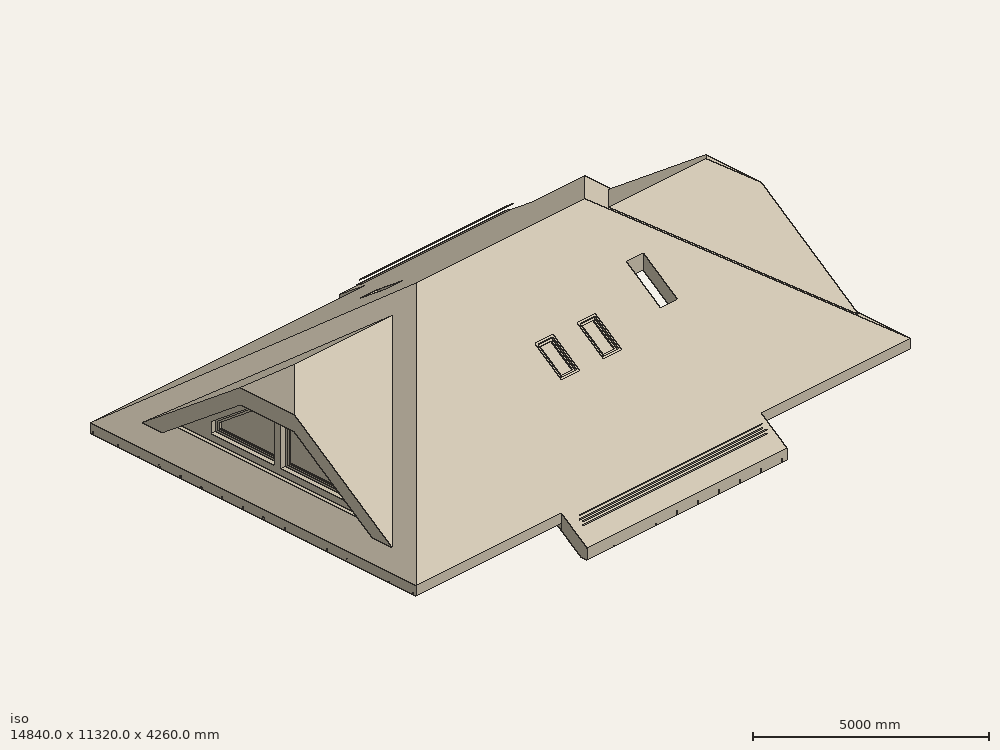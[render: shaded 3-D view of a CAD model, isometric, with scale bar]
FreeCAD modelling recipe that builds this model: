
FCSTD DOCUMENT  (FreeCAD 0.19R)
Label: 2bedr_dev_071121_BIM_mod
License: All rights reserved
LicenseURL: http://en.wikipedia.org/wiki/All_rights_reserved
objects: Part::Part2DObjectPython×578, Part::FeaturePython×547, App::FeaturePython×94, App::DocumentObjectGroupPython×73, App::GeometryPython×66, Sketcher::SketchObject×58, Part::MultiCommon×47, Part::Box×37, Part::Extrusion×36, Part::Cut×35, TechDraw::DrawViewAnnotation×28, Part::MultiFuse×25, App::MaterialObjectPython×20, TechDraw::DrawLeaderLine×17, Part::Feature×16, App::DocumentObjectGroup×12, TechDraw::DrawSVGTemplate×6, TechDraw::DrawPage×6, Part::Cylinder×5, Part::Mirroring×5, +8 more types
note: 1456 computed .brp shape members not serialized (recipe doc carries the construction recipe); baked Part::Feature solids carry a one-line shape summary decoded from their .brp

FEATURE [Part::Part2DObjectPython] Rectangle2169  label="Д-105-254-001"  # Draft 2D object (typed FeaturePython)
  ChamferSize = 0
  Columns = 1
  FilletRadius = 0
  Height = 410
  Length = 1050
  MakeFace = true
  Placement = pos=(5670,-435,0) rot=(0,0,1;0rad)
  Rows = 1
FEATURE [Part::Part2DObjectPython] Rectangle2231  label="ОК-66-001"  # Draft 2D object (typed FeaturePython)
  ChamferSize = 0
  Columns = 1
  FilletRadius = 0
  Height = 410
  Length = 660
  MakeFace = true
  Placement = pos=(7555,-435,0) rot=(0,0,1;0rad)
  Rows = 1
FEATURE [Part::Part2DObjectPython] Rectangle2230  label="ОК-66-002"  # Draft 2D object (typed FeaturePython)
  ChamferSize = 0
  Columns = 1
  FilletRadius = 0
  Height = 410
  Length = 660
  MakeFace = true
  Placement = pos=(4175,-435,0) rot=(0,0,1;0rad)
  Rows = 1
FEATURE [App::FeaturePython] Dimension001  # Draft dimension (typed FeaturePython)
  Diameter = false
  Dimline = (13900,-300,0)
  Direction = (0,0,0)
  Distance = 7510
  End = (12550,7485,0)
  Normal = (0,0,1)
  Start = (12550,-25,0)
FEATURE [App::FeaturePython] Dimension  # Draft dimension (typed FeaturePython)
  Diameter = false
  Dimline = (13600,-1100,0)
  Direction = (0,0,0)
  Distance = 12580
  End = (12550,-10,0)
  Normal = (0,0,1)
  Start = (-30,-10,0)
FEATURE [Part::Part2DObjectPython] Rectangle2234  # Draft 2D object (typed FeaturePython)
  ChamferSize = 0
  Columns = 1
  FilletRadius = 0
  Height = 1500
  Length = 3000
  MakeFace = false
  Placement = pos=(5125,-1770,0) rot=(0,0,1;0rad)
  Rows = 1
FEATURE [Part::FeaturePython] Structure016  label="Проём-ОК-66-002"  # Arch/BIM 52 (typed FeaturePython)
  Base = -> Rectangle2230
  FaceMaker = 0
  Height = 1386
  HorizontalArea = 270600
  IfcData = complex_attributes={"OwnerHistory": {}, "IsNestedBy": {}, "IsDecomposedBy": {}, "IsDefinedBy": {}, "ObjectPlacement": {}, "Representation":... (+4 chars omitted)
  IfcType = 52
  Length = 0
  MoveBase = false
  MoveWithHost = false
  Nodes = (2) [(4618,-185,0),(4618,-185,1386)]
  NodesOffset = 0
  Normal = (0,0,0)
  PerimeterLength = 2140
  Placement = pos=(0,0,955) rot=(0,0,1;0rad)
  VerticalArea = 2966040
  Width = 100
FEATURE [Part::FeaturePython] Structure017  label="Проём-ОК-66-001"  # Arch/BIM 52 (typed FeaturePython)
  Base = -> Rectangle2231
  FaceMaker = 0
  Height = 1386
  HorizontalArea = 270600
  IfcData = complex_attributes={"OwnerHistory": {}, "IsNestedBy": {}, "IsDecomposedBy": {}, "IsDefinedBy": {}, "ObjectPlacement": {}, "Representation":... (+4 chars omitted)
  IfcType = 52
  Length = 0
  MoveBase = false
  MoveWithHost = false
  Nodes = (2) [(7885,-230,0),(7885,-230,1386)]
  NodesOffset = 0
  Normal = (0,0,0)
  PerimeterLength = 2140
  Placement = pos=(0,0,955) rot=(0,0,1;0rad)
  VerticalArea = 2966040
  Width = 100
FEATURE [Part::FeaturePython] Structure019  label="Проём-Д-105-254-001"  # Arch/BIM 52 (typed FeaturePython)
  Base = -> Rectangle2169
  FaceMaker = 0
  Height = 2541
  HorizontalArea = 430500
  IfcData = complex_attributes={"OwnerHistory": {}, "IsNestedBy": {}, "IsDecomposedBy": {}, "IsDefinedBy": {}, "ObjectPlacement": {}, "Representation":... (+4 chars omitted)
  IfcType = 52
  Length = 0
  MoveBase = false
  MoveWithHost = false
  Nodes = (2) [(6195,-230,0),(6195,-230,2541)]
  NodesOffset = 0
  Normal = (0,0,0)
  PerimeterLength = 2920
  Placement = pos=(0,0,-200) rot=(0,0,1;0rad)
  VerticalArea = 7419720
  Width = 100
FEATURE [Part::Part2DObjectPython] Line1049  # Draft 2D object (typed FeaturePython)
  ChamferSize = 0
  Closed = true
  End = (-50,3680,0)
  FilletRadius = 0
  Length = 12620
  MakeFace = false
  Placement = pos=(4290,10400,0) rot=(0,0,1;1.5708rad)
  Points = (2) [(-6720,-8280,0),(-6720,4340,0)]
  Start = (12570,3680,0)
  Subdivisions = 0
FEATURE [Part::Part2DObjectPython] Line1054  # Draft 2D object (typed FeaturePython)
  ChamferSize = 0
  Closed = true
  End = (4870,7505,0)
  FilletRadius = 0
  Length = 3700
  MakeFace = false
  Placement = pos=(9650,5690,0) rot=(0,0,1;0rad)
  Points = (2) [(-4780,-1885,0),(-4780,1815,0)]
  Start = (4870,3805,0)
  Subdivisions = 0
FEATURE [Sketcher::SketchObject] Sketch231  label="Профиль ПНО 120-8"
  FullyConstrained = false
  Placement = pos=(0,0,0) rot=(1,0,0;1.5708rad)
  sketch-geometry (19):
    g0: LineSegment StartX=0 StartY=0 StartZ=0 EndX=1190 EndY=0 EndZ=0
    g1: LineSegment StartX=1190 StartY=0 StartZ=0 EndX=1190 EndY=160 EndZ=0
    g2: LineSegment StartX=1190 StartY=160 StartZ=0 EndX=0 EndY=160 EndZ=0
    g3: LineSegment StartX=0 StartY=160 StartZ=0 EndX=0 EndY=0 EndZ=0
    g4: Circle CenterX=100 CenterY=80 CenterZ=0 NormalX=0 NormalY=0 NormalZ=1 AngleXU=0 Radius=50
    g5: Circle CenterX=240 CenterY=80 CenterZ=0 NormalX=0 NormalY=0 NormalZ=1 AngleXU=0 Radius=50
    g6: LineSegment StartX=100 StartY=80 StartZ=0 EndX=240 EndY=80 EndZ=0
    g7: Circle CenterX=380 CenterY=80 CenterZ=0 NormalX=0 NormalY=0 NormalZ=1 AngleXU=0 Radius=50
    g8: LineSegment StartX=240 StartY=80 StartZ=0 EndX=380 EndY=80 EndZ=0
    g9: Circle CenterX=520 CenterY=80 CenterZ=0 NormalX=0 NormalY=0 NormalZ=1 AngleXU=0 Radius=50
    g10: LineSegment StartX=380 StartY=80 StartZ=0 EndX=520 EndY=80 EndZ=0
    g11: Circle CenterX=660 CenterY=80 CenterZ=0 NormalX=0 NormalY=0 NormalZ=1 AngleXU=0 Radius=50
    g12: LineSegment StartX=520 StartY=80 StartZ=0 EndX=660 EndY=80 EndZ=0
    g13: Circle CenterX=800 CenterY=80 CenterZ=0 NormalX=0 NormalY=0 NormalZ=1 AngleXU=0 Radius=50
    g14: LineSegment StartX=660 StartY=80 StartZ=0 EndX=800 EndY=80 EndZ=0
    g15: Circle CenterX=940 CenterY=80 CenterZ=0 NormalX=0 NormalY=0 NormalZ=1 AngleXU=0 Radius=50
    g16: LineSegment StartX=800 StartY=80 StartZ=0 EndX=940 EndY=80 EndZ=0
    g17: Circle CenterX=1080 CenterY=80 CenterZ=0 NormalX=0 NormalY=0 NormalZ=1 AngleXU=0 Radius=50
    g18: LineSegment StartX=940 StartY=80 StartZ=0 EndX=1080 EndY=80 EndZ=0
  constraints (49):
    c: Coincident(g0,g1)
    c: Coincident(g1,g2)
    c: Coincident(g2,g3)
    c: Coincident(g3,g0)
    c: Horizontal(g0)
    c: Horizontal(g2)
    c: Vertical(g1)
    c: Vertical(g3)
    c: Coincident(g0,g-1)
    c: DistanceY(g3,g3) = 160
    c: DistanceX(g2,g2) = 1190
    c: Diameter(g4) = 100
    c: DistanceY(g4,g2) = 80
    c: Diameter(g5) = 100
    c: Coincident(g4,g6)
    c: Coincident(g5,g6)
    c: Distance(g6) = 140
    c: Angle(g6) = 0
    c: Diameter(g7) = 100
    c: Coincident(g5,g8)
    c: Coincident(g7,g8)
    c: Equal(g6,g8)
    c: Parallel(g8,g6)
    c: Diameter(g9) = 100
    c: Coincident(g7,g10)
    c: Coincident(g9,g10)
    c: Equal(g6,g10)
    c: Parallel(g10,g6)
    c: Diameter(g11) = 100
    c: Coincident(g9,g12)
    c: Coincident(g11,g12)
    c: Equal(g6,g12)
    c: Parallel(g12,g6)
    c: Diameter(g13) = 100
    c: Coincident(g11,g14)
    c: Coincident(g13,g14)
    c: Equal(g6,g14)
    c: Parallel(g14,g6)
    c: Diameter(g15) = 100
    c: Coincident(g13,g16)
    c: Coincident(g15,g16)
    c: Equal(g6,g16)
    c: Parallel(g16,g6)
    c: Diameter(g17) = 100
    c: Coincident(g15,g18)
    c: Coincident(g17,g18)
    c: Equal(g6,g18)
    c: Parallel(g18,g6)
    c: DistanceX(g2,g4) = 100
FEATURE [Part::Part2DObjectPython] Line1074  label="ось фундамента внутр.стены"  # Draft 2D object (typed FeaturePython)
  ChamferSize = 0
  Closed = true
  End = (3855,9350,0)
  FilletRadius = 0
  Length = 5200
  MakeFace = false
  Placement = pos=(2155,2900,0) rot=(0,0,1;1.5708rad)
  Points = (2) [(1250,-1700,0),(6450,-1700,0)]
  Start = (3855,4150,0)
  Subdivisions = 0
FEATURE [Part::FeaturePython] Wall037  label="фундамент внутр.стена01"  # Arch/BIM 166 (typed FeaturePython)
  Align = 2
  Area = 2.6e+06
  Base = -> Line1074
  BlockHeight = 0
  BlockLength = 0
  CountBroken = 0
  CountEntire = 0
  Face = 0
  Height = 500
  HorizontalArea = 1.3e+06
  IfcType = 166
  Joint = 0
  Length = 5200
  MakeBlocks = false
  MoveBase = false
  MoveWithHost = false
  Normal = (0,0,-1)
  OffsetFirst = 0
  OffsetSecond = 0
  PerimeterLength = 10900
  Placement = pos=(0,0,-180) rot=(0,0,1;0rad)
  PredefinedType = 0
  VerticalArea = 5.45e+06
  Width = 250
FEATURE [Part::FeaturePython] Wall046  label="утепл фунд. внешней.стены 002"  # Arch/BIM 166 (typed FeaturePython)
  Align = 1
  Area = 28488000
  BlockHeight = 600
  BlockLength = 600
  CountBroken = 1
  CountEntire = 0
  Face = 0
  Height = 600
  HorizontalArea = 3798400
  IfcType = 166
  Joint = 1
  Length = 47480
  MakeBlocks = true
  MoveBase = false
  MoveWithHost = false
  Normal = (0,0,-1)
  OffsetFirst = 0
  OffsetSecond = 0
  PerimeterLength = 95120
  Placement = pos=(0,0,-380) rot=(0,0,1;0rad)
  PredefinedType = 0
  VerticalArea = 57072000
  Width = 80
FEATURE [Part::FeaturePython] Wall047  label="утепл отмостки 001"  # Arch/BIM 166 (typed FeaturePython)
  Align = 1
  Area = 2374000
  BlockHeight = 600
  BlockLength = 1200
  CountBroken = 1
  CountEntire = 0
  Face = 0
  Height = 50
  HorizontalArea = 28488000
  IfcType = 166
  Joint = 1
  Length = 47480
  MakeBlocks = true
  MoveBase = false
  MoveWithHost = false
  Normal = (0,0,-1)
  Offset = 80
  OffsetFirst = 0
  OffsetSecond = 0
  PerimeterLength = 96160
  Placement = pos=(0,0,-930) rot=(0,0,1;0rad)
  PredefinedType = 0
  VerticalArea = 4808000
  Width = 600
FEATURE [Part::Part2DObjectPython] Circle071  # Draft 2D object (typed FeaturePython)
  FirstAngle = 0
  LastAngle = 0
  MakeFace = false
  Placement = pos=(8500,900,0) rot=(0,0,1;0rad)
  Radius = 580
FEATURE [Part::Part2DObjectPython] Circle072  # Draft 2D object (typed FeaturePython)
  FirstAngle = 0
  LastAngle = 0
  MakeFace = false
  Placement = pos=(8500,900,0) rot=(0,0,1;0rad)
  Radius = 500
FEATURE [Part::Part2DObjectPython] Circle073  label="люк_контур 001"  # Draft 2D object (typed FeaturePython)
  FirstAngle = 0
  LastAngle = 0
  MakeFace = false
  Placement = pos=(8500,1000,0) rot=(0,0,1;0rad)
  Radius = 350
FEATURE [Part::FeaturePython] Structure041  label="кольцо с днищем ДК-10.9 внутр."  # Arch/BIM 52 (typed FeaturePython)
  Base = -> Circle072
  FaceMaker = 0
  Height = 800
  HorizontalArea = 785398
  IfcData = complex_attributes={"OwnerHistory": {}, "IsNestedBy": {}, "IsDecomposedBy": {}, "IsDefinedBy": {}, "ObjectPlacement": {}, "Representation":... (+4 chars omitted)
  IfcType = 52
  Length = 0
  MoveBase = false
  MoveWithHost = false
  Nodes = (2) [(8500,900,0),(8500,900,-800)]
  NodesOffset = 0
  Normal = (0,0,-1)
  PerimeterLength = 3141.59
  Placement = pos=(0,0,-300) rot=(0,0,1;0rad)
  VerticalArea = 2.51327e+06
  Width = 100
FEATURE [Part::FeaturePython] Structure040  label="кольцо с днищем ДК-10.9 габарит"  # Arch/BIM 52 (typed FeaturePython)
  Base = -> Circle071
  FaceMaker = 0
  Height = 900
  HorizontalArea = 1.05683e+06
  IfcData = complex_attributes={"OwnerHistory": {}, "IsNestedBy": {}, "IsDecomposedBy": {}, "IsDefinedBy": {}, "ObjectPlacement": {}, "Representation":... (+4 chars omitted)
  IfcType = 52
  Length = 0
  MoveBase = false
  MoveWithHost = false
  Nodes = (2) [(8500,900,0),(8500,900,-900)]
  NodesOffset = 0
  Normal = (0,0,-1)
  PerimeterLength = 3644.25
  Placement = pos=(0,0,-300) rot=(0,0,1;0rad)
  Subtractions = -> [Structure041]
  VerticalArea = 5.7931e+06
  Width = 100
FEATURE [Part::FeaturePython] Structure044  label="люк контур Д700"  # Arch/BIM 52 (typed FeaturePython)
  Base = -> Circle073
  FaceMaker = 0
  Height = 300
  HorizontalArea = 384845
  IfcData = complex_attributes={"OwnerHistory": {}, "IsNestedBy": {}, "IsDecomposedBy": {}, "IsDefinedBy": {}, "ObjectPlacement": {}, "Representation":... (+4 chars omitted)
  IfcType = 52
  Length = 0
  MoveBase = false
  MoveWithHost = false
  Nodes = (2) [(8500,1000,0),(8500,1000,-300)]
  NodesOffset = 0
  Normal = (0,0,-1)
  PerimeterLength = 2199.11
  VerticalArea = 659734
  Width = 100
FEATURE [Part::FeaturePython] Structure043  label="крышка ПП10"  # Arch/BIM 52 (typed FeaturePython)
  Base = -> Circle071
  FaceMaker = 0
  Height = 100
  HorizontalArea = 671987
  IfcData = complex_attributes={"OwnerHistory": {}, "IsNestedBy": {}, "IsDecomposedBy": {}, "IsDefinedBy": {}, "ObjectPlacement": {}, "Representation":... (+4 chars omitted)
  IfcType = 52
  Length = 0
  MoveBase = false
  MoveWithHost = false
  Nodes = (2) [(8500,900,0),(8500,900,-100)]
  NodesOffset = 0
  Normal = (0,0,-1)
  PerimeterLength = 3644.25
  Placement = pos=(0,0,-200) rot=(0,0,1;0rad)
  Subtractions = -> [Structure044]
  VerticalArea = 584336
  Width = 100
FEATURE [App::GeometryPython] BuildingPart015  label="Колодец d1000 (ввод воды и канализации)"  # Arch/BIM 52 (typed FeaturePython)
  Area = 0
  Group = -> [Structure040,Structure043]
  Height = 0
  HeightPropagate = true
  IfcData = complex_attributes={"OwnerHistory": {}, "IsNestedBy": {}, "IsDecomposedBy": {}, "IsDefinedBy": {}, "ObjectPlacement": {}, "Representation":... (+4 chars omitted)
  IfcType = 52
  LevelOffset = 0
FEATURE [Part::Part2DObjectPython] Line1077  # Draft 2D object (typed FeaturePython)
  ChamferSize = 0
  Closed = true
  End = (-50,-45,0)
  FilletRadius = 0
  Length = 12620
  MakeFace = false
  Placement = pos=(12060,265,0) rot=(0,0,1;0rad)
  Points = (2) [(510,-310,0),(-12110,-310,0)]
  Start = (12570,-45,0)
  Subdivisions = 0
FEATURE [Part::Part2DObjectPython] Rectangle2286  # Draft 2D object (typed FeaturePython)
  ChamferSize = 0
  Columns = 1
  FilletRadius = 0
  Height = 5190
  Length = 9350
  MakeFace = false
  Placement = pos=(1950,2210,0) rot=(0,0,1;0rad)
  Rows = 1
FEATURE [Part::FeaturePython] Structure049  label="вычитаемый объём 002"  # Arch/BIM 52 (typed FeaturePython)
  FaceMaker = 0
  Height = 4000
  HorizontalArea = 3.20922e+07
  IfcData = complex_attributes={"OwnerHistory": {}, "IsNestedBy": {}, "IsDecomposedBy": {}, "IsDefinedBy": {}, "ObjectPlacement": {}, "Representation":... (+4 chars omitted)
  IfcType = 52
  Length = 0
  MoveBase = false
  MoveWithHost = false
  Nodes = (2) [(506.667,3830,0),(506.667,3830,4000)]
  NodesOffset = 0
  Normal = (0,0,1)
  PerimeterLength = 27353
  Placement = pos=(0,0,3160) rot=(0,0,1;0rad)
  VerticalArea = 1.09412e+08
  Width = 100
FEATURE [Part::FeaturePython] Structure050  label="вычитаемый объём 004"  # Arch/BIM 52 (typed FeaturePython)
  FaceMaker = 0
  Height = 4000
  HorizontalArea = 5.56586e+07
  IfcData = complex_attributes={"OwnerHistory": {}, "IsNestedBy": {}, "IsDecomposedBy": {}, "IsDefinedBy": {}, "ObjectPlacement": {}, "Representation":... (+4 chars omitted)
  IfcType = 52
  Length = 0
  MoveBase = false
  MoveWithHost = false
  Nodes = (2) [(6040,886.738,0),(6040,886.738,4000)]
  NodesOffset = 0
  Normal = (0,0,1)
  PerimeterLength = 35673
  Placement = pos=(0,0,3160) rot=(0,0,1;0rad)
  VerticalArea = 1.42692e+08
  Width = 100
FEATURE [Part::FeaturePython] Structure051  label="вычитаемый объём 003"  # Arch/BIM 52 (typed FeaturePython)
  FaceMaker = 0
  Height = 4000
  HorizontalArea = 32092225
  IfcData = complex_attributes={"OwnerHistory": {}, "IsNestedBy": {}, "IsDecomposedBy": {}, "IsDefinedBy": {}, "ObjectPlacement": {}, "Representation":... (+4 chars omitted)
  IfcType = 52
  Length = 0
  MoveBase = false
  MoveWithHost = false
  Nodes = (2) [(12481.7,4805,0),(12481.7,4805,4000)]
  NodesOffset = 0
  Normal = (0,0,1)
  PerimeterLength = 27353
  Placement = pos=(0,0,3160) rot=(0,0,1;0rad)
  VerticalArea = 1.09412e+08
  Width = 100
FEATURE [App::FeaturePython] Dimension003  # Draft dimension (typed FeaturePython)
  Diameter = false
  Dimline = (14100,-1000,0)
  Direction = (0,0,0)
  Distance = 8570
  End = (13080,8015,0)
  Normal = (0,0,1)
  Start = (13080,-555,0)
FEATURE [Sketcher::SketchObject] Sketch248
  FullyConstrained = true
  Placement = pos=(3860,3535,0) rot=(1,0,0;1.5708rad)
  sketch-geometry (8):
    g0: LineSegment StartX=0 StartY=0 StartZ=0 EndX=900 EndY=0 EndZ=0
    g1: LineSegment StartX=900 StartY=0 StartZ=0 EndX=900 EndY=2150 EndZ=0
    g2: LineSegment StartX=900 StartY=2150 StartZ=0 EndX=0 EndY=2150 EndZ=0
    g3: LineSegment StartX=0 StartY=2150 StartZ=0 EndX=0 EndY=0 EndZ=0
    g4: LineSegment StartX=50 StartY=0 StartZ=0 EndX=850 EndY=0 EndZ=0
    g5: LineSegment StartX=850 StartY=0 StartZ=0 EndX=850 EndY=2100 EndZ=0
    g6: LineSegment StartX=850 StartY=2100 StartZ=0 EndX=50 EndY=2100 EndZ=0
    g7: LineSegment StartX=50 StartY=2100 StartZ=0 EndX=50 EndY=0 EndZ=0
  constraints (23):
    c: Coincident(g0,g1)
    c: Coincident(g1,g2)
    c: Coincident(g2,g3)
    c: Coincident(g3,g0)
    c: Horizontal(g0)
    c: Horizontal(g2)
    c: Vertical(g1)
    c: Vertical(g3)
    c: Coincident(g4,g5)
    c: Coincident(g5,g6)
    c: Coincident(g6,g7)
    c: Coincident(g7,g4)
    c: Horizontal(g4)
    c: Horizontal(g6)
    c: Vertical(g5)
    c: Vertical(g7)
    c: DistanceY(g1) = 2150  'Height'
    c: DistanceX(g0) = 900  'Width'
    c: DistanceY(g6,g2) = 50  'Frame1'
    c: DistanceX(g2,g6) = 50  'Frame2'
    c: DistanceX(g4,g0) = 50  'Frame3'
    c: DistanceY(g0,g4) = 0
    c: Coincident(g0,g-1)
FEATURE [Sketcher::SketchObject] Sketch249  label="Профиль ПНО 100-6"
  FullyConstrained = false
  Placement = pos=(0,0,0) rot=(1,0,0;1.5708rad)
  sketch-geometry (15):
    g0: LineSegment StartX=0 StartY=0 StartZ=0 EndX=990 EndY=0 EndZ=0
    g1: LineSegment StartX=990 StartY=0 StartZ=0 EndX=990 EndY=160 EndZ=0
    g2: LineSegment StartX=990 StartY=160 StartZ=0 EndX=0 EndY=160 EndZ=0
    g3: LineSegment StartX=0 StartY=160 StartZ=0 EndX=0 EndY=0 EndZ=0
    g4: Circle CenterX=145 CenterY=80 CenterZ=0 NormalX=0 NormalY=0 NormalZ=1 AngleXU=0 Radius=50
    g5: Circle CenterX=285 CenterY=80 CenterZ=0 NormalX=0 NormalY=0 NormalZ=1 AngleXU=0 Radius=50
    g6: LineSegment StartX=145 StartY=80 StartZ=0 EndX=285 EndY=80 EndZ=0
    g7: Circle CenterX=425 CenterY=80 CenterZ=0 NormalX=0 NormalY=0 NormalZ=1 AngleXU=0 Radius=50
    g8: LineSegment StartX=285 StartY=80 StartZ=0 EndX=425 EndY=80 EndZ=0
    g9: Circle CenterX=565 CenterY=80 CenterZ=0 NormalX=0 NormalY=0 NormalZ=1 AngleXU=0 Radius=50
    g10: LineSegment StartX=425 StartY=80 StartZ=0 EndX=565 EndY=80 EndZ=0
    g11: Circle CenterX=705 CenterY=80 CenterZ=0 NormalX=0 NormalY=0 NormalZ=1 AngleXU=0 Radius=50
    g12: LineSegment StartX=565 StartY=80 StartZ=0 EndX=705 EndY=80 EndZ=0
    g13: Circle CenterX=845 CenterY=80 CenterZ=0 NormalX=0 NormalY=0 NormalZ=1 AngleXU=0 Radius=50
    g14: LineSegment StartX=705 StartY=80 StartZ=0 EndX=845 EndY=80 EndZ=0
  constraints (39):
    c: Coincident(g0,g1)
    c: Coincident(g1,g2)
    c: Coincident(g2,g3)
    c: Coincident(g3,g0)
    c: Horizontal(g0)
    c: Horizontal(g2)
    c: Vertical(g1)
    c: Vertical(g3)
    c: Coincident(g0,g-1)
    c: DistanceY(g3,g3) = 160
    c: DistanceX(g2,g2) = 990
    c: Diameter(g4) = 100
    c: DistanceY(g4,g2) = 80
    c: Diameter(g5) = 100
    c: Coincident(g4,g6)
    c: Coincident(g5,g6)
    c: Distance(g6) = 140
    c: Angle(g6) = 0
    c: Diameter(g7) = 100
    c: Coincident(g5,g8)
    c: Coincident(g7,g8)
    c: Equal(g6,g8)
    c: Parallel(g8,g6)
    c: Diameter(g9) = 100
    c: Coincident(g7,g10)
    c: Coincident(g9,g10)
    c: Equal(g6,g10)
    c: Parallel(g10,g6)
    c: Diameter(g11) = 100
    c: Coincident(g9,g12)
    c: Coincident(g11,g12)
    c: Equal(g6,g12)
    c: Parallel(g12,g6)
    c: Diameter(g13) = 100
    c: Coincident(g11,g14)
    c: Coincident(g13,g14)
    c: Equal(g6,g14)
    c: Parallel(g14,g6)
    c: DistanceX(g2,g4) = 145
FEATURE [Part::Part2DObjectPython] Wire460  label="границы участка"  # Draft 2D object (typed FeaturePython)
  ChamferSize = 0
  Closed = true
  End = (26167.8,29983.2,0)
  FilletRadius = 0
  Length = 156987
  MakeFace = false
  Placement = pos=(24404.1,-9481.8,0) rot=(0,0,1;0.025758rad)
  Points = (7) [(0,0,0),(-3118.22,176.296,0),(-9989.98,2199.83,0),(-22349.9,2518.26,0),(-33551.4,825.818,0),(-40981.4,39865.2,0),(2779.54,39406.5,0)]
  Start = (24404.1,-9481.8,0)
  Subdivisions = 0
FEATURE [Part::Part2DObjectPython] Rectangle2365  label="зона парковки-навес"  # Draft 2D object (typed FeaturePython)
  ChamferSize = 0
  Columns = 1
  FilletRadius = 0
  Height = 7000
  Length = 7000
  MakeFace = false
  Placement = pos=(17916.6,-6918.81,0) rot=(0,0,-1;0.068796rad)
  Rows = 1
FEATURE [Part::Part2DObjectPython] Wire463  label="граница по ограждению"  # Draft 2D object (typed FeaturePython)
  ChamferSize = 0
  Closed = true
  End = (5754.6,-6612.02,0)
  FilletRadius = 0
  Length = 153279
  MakeFace = false
  Placement = pos=(24847.4,-8209.78,0) rot=(0,0,1;0rad)
  Points = (6) [(14.0233,-1.17368,0),(2632.1,37116.3,0),(-41128.8,37575,0),(-34003,133.748,0),(-24492.8,1579.34,0),(-19092.8,1597.76,0)]
  Start = (24861.5,-8210.95,0)
  Subdivisions = 0
FEATURE [Part::FeaturePython] Structure133  label="грунт в границах участка"  # Arch/BIM 52 (typed FeaturePython)
  Base = -> Wire460
  FaceMaker = 0
  Height = 1000
  HorizontalArea = 1.47224e+09
  IfcData = complex_attributes={"OwnerHistory": {}, "IsNestedBy": {}, "IsDecomposedBy": {}, "IsDefinedBy": {}, "ObjectPlacement": {}, "Representation":... (+4 chars omitted)
  IfcType = 52
  Length = 0
  MoveBase = false
  MoveWithHost = false
  Nodes = (2) [(5892.5,11504.2,0),(5892.5,11504.2,-1000)]
  NodesOffset = 0
  Normal = (0,0,-1)
  PerimeterLength = 156987
  Placement = pos=(0,0,-320) rot=(0,0,1;0rad)
  VerticalArea = 1.56987e+08
  Width = 100
FEATURE [Part::Part2DObjectPython] Wire464  label="мауэрлат003"  # Draft 2D object (typed FeaturePython)
  ChamferSize = 0
  Closed = true
  End = (14568.5,-7412.72,0)
  FilletRadius = 0
  Length = 30000
  MakeFace = false
  Placement = pos=(20304,-1451.15,0) rot=(0,0,-1;0.229406rad)
  Points = (4) [(3770.46,-7109.62,0),(3770.46,-109.624,0),(-4229.54,-109.624,0),(-4229.54,-7109.62,0)]
  Start = (22359,-9231.91,0)
  Subdivisions = 0
FEATURE [Part::Part2DObjectPython] Rectangle2375  # Draft 2D object (typed FeaturePython)
  ChamferSize = 0
  Columns = 1
  FilletRadius = 0
  Height = 150
  Length = 800
  MakeFace = true
  Placement = pos=(-1461.06,-5083.09,0) rot=(0,0,-1;1.39508rad)
  Rows = 1
FEATURE [Part::Part2DObjectPython] Rectangle2376  # Draft 2D object (typed FeaturePython)
  ChamferSize = 0
  Columns = 1
  FilletRadius = 0
  Height = 150
  Length = 500
  MakeFace = true
  Placement = pos=(-6959.67,-6719.51,0) rot=(0,0,1;1.74651rad)
  Rows = 1
FEATURE [Part::Part2DObjectPython] Rectangle2377  # Draft 2D object (typed FeaturePython)
  ChamferSize = 0
  Columns = 1
  FilletRadius = 0
  Height = 2300
  Length = 6000
  MakeFace = false
  Placement = pos=(-1444.48,-4318.42,0) rot=(0,0,1;3.31731rad)
  Rows = 1
FEATURE [Part::FeaturePython] Roof011  label="Навес над парковкой"  # Arch/BIM 113 (typed FeaturePython)
  Angles = [90,10,90,10]
  Base = -> Wire464
  BorderLength = 0
  Face = 0
  Flip = false
  Heights = [0,617.144,0,617.144]
  HorizontalArea = 5.6e+07
  IdRel = [0,0,0,0]
  IfcType = 113
  MoveBase = false
  MoveWithHost = false
  Overhang = [0,0,0,0]
  PerimeterLength = 30000
  Placement = pos=(0,0,2500) rot=(0,0,1;0rad)
  PredefinedType = 0
  RidgeLength = 0
  Runs = [0,3500,0,3500]
  Thickness = [150,150,150,150]
  VerticalArea = 7.00644e+06
FEATURE [Part::FeaturePython] Structure135  label="Structure134"  # Arch/BIM 52 (typed FeaturePython)
  Base = -> Rectangle2375
  FaceMaker = 0
  Height = 1800
  HorizontalArea = 120000
  IfcData = complex_attributes={"OwnerHistory": {}, "IsNestedBy": {}, "IsDecomposedBy": {}, "IsDefinedBy": {}, "ObjectPlacement": {}, "Representation":... (+4 chars omitted)
  IfcType = 52
  Length = 0
  MoveBase = false
  MoveWithHost = false
  Nodes = (2) [(-35.6948,-25773.1,0),(-35.6948,-25773.1,1800)]
  NodesOffset = 0
  Normal = (0,0,0)
  PerimeterLength = 1900
  VerticalArea = 3.42e+06
  Width = 100
FEATURE [Part::FeaturePython] Structure136  label="Structure135"  # Arch/BIM 52 (typed FeaturePython)
  Base = -> Rectangle2376
  FaceMaker = 0
  Height = 600
  HorizontalArea = 75000
  IfcData = complex_attributes={"OwnerHistory": {}, "IsNestedBy": {}, "IsDecomposedBy": {}, "IsDefinedBy": {}, "ObjectPlacement": {}, "Representation":... (+4 chars omitted)
  IfcType = 52
  Length = 0
  MoveBase = false
  MoveWithHost = false
  Nodes = (2) [(1351.07,-25965.1,0),(1351.07,-25965.1,600)]
  NodesOffset = 0
  Normal = (0,0,0)
  PerimeterLength = 1300
  Placement = pos=(0,-4e-15,1240) rot=(0,0,1;0rad)
  VerticalArea = 780000
  Width = 100
FEATURE [Part::FeaturePython] Wall097  label="Wall007"  # Arch/BIM 166 (typed FeaturePython)
  Align = 1
  Area = 4.067e+07
  Base = -> Rectangle2377
  BlockHeight = 0
  BlockLength = 0
  CountBroken = 0
  CountEntire = 0
  Face = 0
  Height = 2450
  HorizontalArea = 2.595e+06
  IfcType = 166
  Joint = 0
  Length = 16600
  MakeBlocks = false
  MoveBase = false
  MoveWithHost = false
  Normal = (0,0,0)
  OffsetFirst = 0
  OffsetSecond = 0
  PerimeterLength = 12600
  Placement = pos=(0,0,-150) rot=(0,0,1;0rad)
  PredefinedType = 0
  Subtractions = -> [Structure136,Structure135]
  VerticalArea = 7.564e+07
  Width = 150
FEATURE [Sketcher::SketchObject] Sketch250  label="Габарит человека"
  FullyConstrained = false
  Placement = pos=(0,0,0) rot=(1,0,0;1.5708rad)
  sketch-geometry (21):
    g0: LineSegment StartX=-250 StartY=0 StartZ=0 EndX=250 EndY=0 EndZ=0
    g1: LineSegment StartX=250 StartY=0 StartZ=0 EndX=250 EndY=1750 EndZ=0
    g2: LineSegment StartX=250 StartY=1750 StartZ=0 EndX=-250 EndY=1750 EndZ=0
    g3: LineSegment StartX=-250 StartY=1750 StartZ=0 EndX=-250 EndY=0 EndZ=0
    g4: LineSegment StartX=85 StartY=1500 StartZ=0 EndX=85 EndY=1750 EndZ=0
    g5: LineSegment StartX=85 StartY=1750 StartZ=0 EndX=-85 EndY=1750 EndZ=0
    g6: LineSegment StartX=-85 StartY=1750 StartZ=0 EndX=-85 EndY=1500 EndZ=0
    g7: LineSegment StartX=250 StartY=750 StartZ=0 EndX=250 EndY=1500 EndZ=0
    g8: LineSegment StartX=-250 StartY=1500 StartZ=0 EndX=-250 EndY=750 EndZ=0
    g9: LineSegment StartX=-110 StartY=0 StartZ=0 EndX=110 EndY=0 EndZ=0
    g10: LineSegment StartX=110 StartY=0 StartZ=0 EndX=175 EndY=750 EndZ=0
    g11: LineSegment StartX=-175 StartY=750 StartZ=0 EndX=-110 EndY=0 EndZ=0
    g12: GeomPoint X=0 Y=750 Z=0
    g13: GeomPoint X=-110 Y=0 Z=0
    g14: GeomPoint X=110 Y=0 Z=0
    g15: GeomPoint X=175 Y=750 Z=0
    g16: GeomPoint X=-175 Y=750 Z=0
    g17: LineSegment StartX=-250 StartY=1500 StartZ=0 EndX=-85 EndY=1500 EndZ=0
    g18: LineSegment StartX=85 StartY=1500 StartZ=0 EndX=250 EndY=1500 EndZ=0
    g19: LineSegment StartX=-250 StartY=750 StartZ=0 EndX=-175 EndY=750 EndZ=0
    g20: LineSegment StartX=175 StartY=750 StartZ=0 EndX=250 EndY=750 EndZ=0
  constraints (50):
    c: Coincident(g0,g1)
    c: Coincident(g1,g2)
    c: Coincident(g2,g3)
    c: Coincident(g3,g0)
    c: Horizontal(g0)
    c: Horizontal(g2)
    c: Vertical(g1)
    c: Vertical(g3)
    c: Symmetric(g0,g0,g-1)
    c: DistanceX(g2,g2) = 500
    c: DistanceY(g1,g1) = 1750
    c: Coincident(g4,g5)
    c: Coincident(g5,g6)
    c: Horizontal(g5)
    c: Vertical(g4)
    c: Vertical(g6)
    c: Vertical(g7)
    c: Vertical(g8)
    c: Coincident(g9,g10)
    c: DistanceX(g5,g5) = 170
    c: DistanceY(g4,g4) = 250
    c: PointOnObject(g4,g2)
    c: Symmetric(g6,g4,g-2)
    c: PointOnObject(g8,g3)
    c: PointOnObject(g7,g1)
    c: Coincident(g9,g11)
    c: DistanceX(g9,g9) = 220
    c: DistanceY(g0,g7) = 750
    c: PointOnObject(g12,g-2)
    c: Coincident(g13,g9)
    c: Coincident(g14,g9)
    c: Symmetric(g13,g14,g-2)
    c: PointOnObject(g14,g0)
    c: Coincident(g15,g10)
    c: Symmetric(g15,g16,g-2)
    c: DistanceX(g16,g15) = 350
    c: Coincident(g17,g8)
    c: Coincident(g17,g6)
    c: Horizontal(g17)
    c: Coincident(g18,g4)
    c: Coincident(g18,g7)
    c: Horizontal(g18)
    c: Coincident(g19,g8)
    c: Coincident(g19,g11)
    c: Horizontal(g19)
    c: Coincident(g20,g10)
    c: Coincident(g20,g7)
    c: Horizontal(g20)
    c: Equal(g19,g20)
    c: Equal(g11,g10)
FEATURE [Part::Extrusion] Extrude007  label="Габарит человека 001"
  Base = -> Sketch250
  Dir = (0,-1,2e-16)
  DirMode = 2
  FaceMakerClass = Part::FaceMakerBullseye
  LengthFwd = 290
  LengthRev = 0
  Placement = pos=(7375,4690,0) rot=(0,0,1;0rad)
  Solid = true
  Symmetric = false
FEATURE [Part::Extrusion] Extrude008  label="Габарит человека 002"
  Base = -> Sketch250
  Dir = (0,-1,2e-16)
  DirMode = 2
  FaceMakerClass = Part::FaceMakerBullseye
  LengthFwd = 290
  LengthRev = 0
  Placement = pos=(6300,5845,0) rot=(0,0,1;0rad)
  Solid = true
  Symmetric = false
FEATURE [Part::Part2DObjectPython] Rectangle2381  # Draft 2D object (typed FeaturePython)
  ChamferSize = 0
  Columns = 1
  FilletRadius = 0
  Height = 1250
  Length = 2500
  MakeFace = false
  Placement = pos=(5375,-1520,0) rot=(0,0,1;0rad)
  Rows = 1
FEATURE [Part::FeaturePython] Structure140  label="габарит крыльца001"  # Arch/BIM 52 (typed FeaturePython)
  Base = -> Rectangle2381
  FaceMaker = 0
  Height = 180
  HorizontalArea = 3125000
  IfcData = complex_attributes={"OwnerHistory": {}, "IsNestedBy": {}, "IsDecomposedBy": {}, "IsDefinedBy": {}, "ObjectPlacement": {}, "Representation":... (+4 chars omitted)
  IfcType = 52
  Length = 0
  MoveBase = false
  MoveWithHost = false
  Nodes = (2) [(5975,-1250,0),(5975,-1250,-350)]
  NodesOffset = 0
  Normal = (0,0,-1)
  PerimeterLength = 7500
  Placement = pos=(0,0,-40) rot=(0,0,1;0rad)
  VerticalArea = 1350000
  Width = 100
FEATURE [Part::FeaturePython] Structure029  label="габарит крыльца"  # Arch/BIM 52 (typed FeaturePython)
  Additions = -> [Structure140]
  Base = -> Rectangle2234
  FaceMaker = 0
  Height = 180
  HorizontalArea = 4500000
  IfcData = complex_attributes={"OwnerHistory": {}, "IsNestedBy": {}, "IsDecomposedBy": {}, "IsDefinedBy": {}, "ObjectPlacement": {}, "Representation":... (+4 chars omitted)
  IfcType = 52
  Length = 0
  MoveBase = false
  MoveWithHost = false
  Nodes = (2) [(5975,-1250,0),(5975,-1250,-350)]
  NodesOffset = 0
  Normal = (0,0,-1)
  PerimeterLength = 9000
  Placement = pos=(0,0,-220) rot=(0,0,1;0rad)
  VerticalArea = 2970000
  Width = 100
FEATURE [Part::Part2DObjectPython] Rectangle2382  label="террасса"  # Draft 2D object (typed FeaturePython)
  ChamferSize = 0
  Columns = 1
  FilletRadius = 0
  Height = 2400
  Length = 10500
  MakeFace = false
  Placement = pos=(1255,9880,0) rot=(0,0,1;0rad)
  Rows = 1
FEATURE [Part::FeaturePython] Structure028  label="габарит терассы"  # Arch/BIM 52 (typed FeaturePython)
  Base = -> Rectangle2382
  FaceMaker = 0
  Height = 400
  HorizontalArea = 25200000
  IfcData = complex_attributes={"OwnerHistory": {}, "IsNestedBy": {}, "IsDecomposedBy": {}, "IsDefinedBy": {}, "ObjectPlacement": {}, "Representation":... (+4 chars omitted)
  IfcType = 52
  Length = 0
  MoveBase = false
  MoveWithHost = false
  Nodes = (2) [(6755,9400,0),(6755,9400,-400)]
  NodesOffset = 0
  Normal = (0,0,-1)
  PerimeterLength = 25800
  Placement = pos=(0,0,-40) rot=(0,0,1;0rad)
  VerticalArea = 10320000
  Width = 100
FEATURE [App::GeometryPython] BuildingPart035  label="Внешние элементы"  # Arch/BIM 52 (typed FeaturePython)
  Area = 0
  Group = -> [Structure028,Structure029]
  Height = 0
  HeightPropagate = true
  IfcData = complex_attributes={"OwnerHistory": {}, "IsNestedBy": {}, "IsDecomposedBy": {}, "IsDefinedBy": {}, "ObjectPlacement": {}, "Representation":... (+4 chars omitted)
  IfcType = 52
  LevelOffset = 0
FEATURE [Image::ImagePlane] ImagePlane  label="План участка"
  Placement = pos=(1568.88,19724.2,-450) rot=(0,0,1;3.16731rad)
  XSize = 103541
  YSize = 98696.8
FEATURE [Sketcher::SketchObject] Sketch251
  FullyConstrained = true
  Placement = pos=(3400,2535,0) rot=(0.57735,0.57735,0.57735;2.0944rad)
  sketch-geometry (8):
    g0: LineSegment StartX=0 StartY=0 StartZ=0 EndX=900 EndY=0 EndZ=0
    g1: LineSegment StartX=900 StartY=0 StartZ=0 EndX=900 EndY=2150 EndZ=0
    g2: LineSegment StartX=900 StartY=2150 StartZ=0 EndX=0 EndY=2150 EndZ=0
    g3: LineSegment StartX=0 StartY=2150 StartZ=0 EndX=0 EndY=0 EndZ=0
    g4: LineSegment StartX=50 StartY=0 StartZ=0 EndX=850 EndY=0 EndZ=0
    g5: LineSegment StartX=850 StartY=0 StartZ=0 EndX=850 EndY=2100 EndZ=0
    g6: LineSegment StartX=850 StartY=2100 StartZ=0 EndX=50 EndY=2100 EndZ=0
    g7: LineSegment StartX=50 StartY=2100 StartZ=0 EndX=50 EndY=0 EndZ=0
  constraints (23):
    c: Coincident(g0,g1)
    c: Coincident(g1,g2)
    c: Coincident(g2,g3)
    c: Coincident(g3,g0)
    c: Horizontal(g0)
    c: Horizontal(g2)
    c: Vertical(g1)
    c: Vertical(g3)
    c: Coincident(g4,g5)
    c: Coincident(g5,g6)
    c: Coincident(g6,g7)
    c: Coincident(g7,g4)
    c: Horizontal(g4)
    c: Horizontal(g6)
    c: Vertical(g5)
    c: Vertical(g7)
    c: DistanceY(g1) = 2150  'Height'
    c: DistanceX(g0) = 900  'Width'
    c: DistanceY(g6,g2) = 50  'Frame1'
    c: DistanceX(g2,g6) = 50  'Frame2'
    c: DistanceX(g4,g0) = 50  'Frame3'
    c: DistanceY(g0,g4) = 0
    c: Coincident(g0,g-1)
FEATURE [App::FeaturePython] Dimension004  # Draft dimension (typed FeaturePython)
  Diameter = false
  Dimline = (-1600,-1000,0)
  Direction = (0,0,0)
  Distance = 3915
  End = (-1836.7,3680,0)
  Normal = (0,0,1)
  Start = (-1836.7,-235,0)
FEATURE [App::FeaturePython] Dimension006  # Draft dimension (typed FeaturePython)
  Diameter = false
  Dimline = (-1600,3680,0)
  Direction = (0,0,0)
  Distance = 4015
  End = (-1836.7,7695,0)
  Normal = (0,0,1)
  Start = (-1836.7,3680,0)
FEATURE [App::FeaturePython] Dimension007  # Draft dimension (typed FeaturePython)
  Diameter = false
  Dimline = (-600,9000,0)
  Direction = (0,0,0)
  Distance = 5110
  End = (4870,9506.46,0)
  Normal = (0,0,1)
  Start = (-240,9506.46,0)
FEATURE [App::FeaturePython] Dimension009  # Draft dimension (typed FeaturePython)
  Diameter = false
  Dimline = (7910,9000,0)
  Direction = (0,0,0)
  Distance = 1020
  End = (7910,9506.46,0)
  Normal = (0,0,1)
  Start = (6890,9506.46,0)
FEATURE [Part::Part2DObjectPython] Rectangle2392  # Draft 2D object (typed FeaturePython)
  ChamferSize = 0
  Columns = 1
  FilletRadius = 50
  Height = 400
  Length = 400
  MakeFace = false
  Placement = pos=(12050,2061,0) rot=(0,0,1;0rad)
  Rows = 1
FEATURE [Part::Part2DObjectPython] Rectangle2573  label="четверть_530-001"  # Draft 2D object (typed FeaturePython)
  ChamferSize = 0
  Columns = 1
  FilletRadius = 0
  Height = 120
  Length = 530
  MakeFace = true
  Placement = pos=(4240,-555,0) rot=(0,0,1;0rad)
  Rows = 1
FEATURE [Part::Part2DObjectPython] Rectangle2571  label="четверть_105-001"  # Draft 2D object (typed FeaturePython)
  ChamferSize = 0
  Columns = 1
  FilletRadius = 0
  Height = 120
  Length = 1050
  MakeFace = true
  Placement = pos=(5670,-555,0) rot=(0,0,1;0rad)
  Rows = 1
FEATURE [Part::FeaturePython] Structure148  label="Проём_четв._031"  # Arch/BIM 52 (typed FeaturePython)
  Base = -> Rectangle2571
  FaceMaker = 0
  Height = 2315
  HorizontalArea = 126000
  IfcData = complex_attributes={"OwnerHistory": {}, "IsNestedBy": {}, "IsDecomposedBy": {}, "IsDefinedBy": {}, "ObjectPlacement": {}, "Representation":... (+4 chars omitted)
  IfcType = 52
  Length = 0
  MoveBase = false
  MoveWithHost = false
  Nodes = (2) [(5775,-395,0),(5775,-395,2335)]
  NodesOffset = 0
  Normal = (0,0,0)
  PerimeterLength = 2340
  Placement = pos=(0,0,-40) rot=(0,0,1;0rad)
  VerticalArea = 5417100
  Width = 100
FEATURE [Part::Part2DObjectPython] Rectangle2579  label="четверть_183-001"  # Draft 2D object (typed FeaturePython)
  ChamferSize = 0
  Columns = 1
  FilletRadius = 0
  Height = 120
  Length = 1830
  MakeFace = true
  Placement = pos=(12960,3215,0) rot=(0,0,-1;1.5708rad)
  Rows = 1
FEATURE [Part::Part2DObjectPython] Rectangle2577  label="четверть_790-001"  # Draft 2D object (typed FeaturePython)
  ChamferSize = 0
  Columns = 1
  FilletRadius = 0
  Height = 120
  Length = 790
  MakeFace = true
  Placement = pos=(12960,4905,0) rot=(0,0,-1;1.5708rad)
  Rows = 1
FEATURE [Part::Part2DObjectPython] Line1184  label="Line1179"  # Draft 2D object (typed FeaturePython)
  ChamferSize = 0
  Closed = false
  End = (8280,-555,0)
  FilletRadius = 0
  Length = 790
  MakeFace = true
  Placement = pos=(7490,-555,0) rot=(0,0,-1;0rad)
  Points = (2) [(0,0,0),(790,3.41061e-13,0)]
  Start = (7490,-555,0)
  Subdivisions = 0
FEATURE [Part::Part2DObjectPython] Line1186  # Draft 2D object (typed FeaturePython)
  ChamferSize = 0
  Closed = true
  End = (6070,8015,0)
  FilletRadius = 0
  Length = 4170
  MakeFace = true
  Placement = pos=(1900,8015,0) rot=(0,0,1;0rad)
  Points = (2) [(0,0,0),(4170,0,0)]
  Start = (1900,8015,0)
  Subdivisions = 0
FEATURE [Part::Part2DObjectPython] Line1187  # Draft 2D object (typed FeaturePython)
  ChamferSize = 0
  Closed = true
  End = (13080,5035,0)
  FilletRadius = 0
  Length = 3780
  MakeFace = true
  Placement = pos=(13080,1255,0) rot=(0,0,1;1.5708rad)
  Points = (2) [(0,0,0),(3780,9.09495e-12,0)]
  Start = (13080,1255,0)
  Subdivisions = 0
FEATURE [Part::Part2DObjectPython] Rectangle2580  label="четверть_530-002"  # Draft 2D object (typed FeaturePython)
  ChamferSize = 0
  Columns = 1
  FilletRadius = 0
  Height = 120
  Length = 530
  MakeFace = true
  Placement = pos=(7620,-555,0) rot=(0,0,1;0rad)
  Rows = 1
FEATURE [Part::Part2DObjectPython] Line1191  label="Line1184"  # Draft 2D object (typed FeaturePython)
  ChamferSize = 0
  Closed = false
  End = (4900,-555,0)
  FilletRadius = 0
  Length = 790
  MakeFace = true
  Placement = pos=(4110,-585,0) rot=(0,0,-1;0rad)
  Points = (2) [(0,30,0),(790,30,0)]
  Start = (4110,-555,0)
  Subdivisions = 0
FEATURE [Sketcher::SketchObject] Sketch260
  FullyConstrained = true
  Placement = pos=(5810,2285,-180) rot=(1,0,0;1.5708rad)
  sketch-geometry (8):
    g0: LineSegment StartX=0 StartY=0 StartZ=0 EndX=900 EndY=0 EndZ=0
    g1: LineSegment StartX=900 StartY=0 StartZ=0 EndX=900 EndY=2150 EndZ=0
    g2: LineSegment StartX=900 StartY=2150 StartZ=0 EndX=0 EndY=2150 EndZ=0
    g3: LineSegment StartX=0 StartY=2150 StartZ=0 EndX=0 EndY=0 EndZ=0
    g4: LineSegment StartX=50 StartY=0 StartZ=0 EndX=850 EndY=0 EndZ=0
    g5: LineSegment StartX=850 StartY=0 StartZ=0 EndX=850 EndY=2100 EndZ=0
    g6: LineSegment StartX=850 StartY=2100 StartZ=0 EndX=50 EndY=2100 EndZ=0
    g7: LineSegment StartX=50 StartY=2100 StartZ=0 EndX=50 EndY=0 EndZ=0
  constraints (23):
    c: Coincident(g0,g1)
    c: Coincident(g1,g2)
    c: Coincident(g2,g3)
    c: Coincident(g3,g0)
    c: Horizontal(g0)
    c: Horizontal(g2)
    c: Vertical(g1)
    c: Vertical(g3)
    c: Coincident(g4,g5)
    c: Coincident(g5,g6)
    c: Coincident(g6,g7)
    c: Coincident(g7,g4)
    c: Horizontal(g4)
    c: Horizontal(g6)
    c: Vertical(g5)
    c: Vertical(g7)
    c: DistanceY(g1) = 2150  'Height'
    c: DistanceX(g0) = 900  'Width'
    c: DistanceY(g6,g2) = 50  'Frame1'
    c: DistanceX(g2,g6) = 50  'Frame2'
    c: DistanceX(g4,g0) = 50  'Frame3'
    c: DistanceY(g0,g4) = 0
    c: Coincident(g0,g-1)
FEATURE [Part::Part2DObjectPython] Line1200  label="Line1202"  # Draft 2D object (typed FeaturePython)
  ChamferSize = 0
  Closed = true
  End = (7910,6475,0)
  FilletRadius = 0
  Length = 2670
  MakeFace = false
  Placement = pos=(5440,5450,0) rot=(0,0,-1;1.5708rad)
  Points = (2) [(1645,2470,0),(-1025,2470,0)]
  Start = (7910,3805,0)
  Subdivisions = 0
FEATURE [Part::Part2DObjectPython] Line1201  label="ось фундамента внутр.стены001"  # Draft 2D object (typed FeaturePython)
  ChamferSize = 0
  Closed = true
  End = (9525,9350,0)
  FilletRadius = 0
  Length = 9090
  MakeFace = false
  Placement = pos=(7825,2900,0) rot=(0,0,1;1.5708rad)
  Points = (2) [(-2640,-1700,0),(6450,-1700,0)]
  Start = (9525,260,0)
  Subdivisions = 0
FEATURE [Part::FeaturePython] Wall129  label="фундамент внутр.стена002"  # Arch/BIM 166 (typed FeaturePython)
  Align = 2
  Area = 4545000
  Base = -> Line1201
  BlockHeight = 0
  BlockLength = 0
  CountBroken = 0
  CountEntire = 0
  Face = 0
  Height = 500
  HorizontalArea = 2.2725e+06
  IfcType = 166
  Joint = 0
  Length = 9090
  MakeBlocks = false
  MoveBase = false
  MoveWithHost = false
  Normal = (0,0,-1)
  OffsetFirst = 0
  OffsetSecond = 0
  PerimeterLength = 18680
  Placement = pos=(0,0,-180) rot=(0,0,1;0rad)
  PredefinedType = 0
  VerticalArea = 9340000
  Width = 250
FEATURE [Part::Extrusion] Extrude012  label="Габарит человека 003"
  Base = -> Sketch250
  Dir = (0,-1,2e-16)
  DirMode = 2
  FaceMakerClass = Part::FaceMakerBullseye
  LengthFwd = 290
  LengthRev = 0
  Placement = pos=(4469.4,8795.6,0) rot=(0,0,1;0rad)
  Solid = true
  Symmetric = false
FEATURE [Part::Part2DObjectPython] Rectangle2589  label="проём в перекрытии 005"  # Draft 2D object (typed FeaturePython)
  ChamferSize = 0
  Columns = 1
  FilletRadius = 0
  Height = 1550
  Length = 380
  MakeFace = false
  Placement = pos=(-3580,8320,0) rot=(0,0,1;0rad)
  Rows = 1
FEATURE [Part::Part2DObjectPython] Rectangle2597  label="проём вентшахты"  # Draft 2D object (typed FeaturePython)
  ChamferSize = 0
  Columns = 1
  FilletRadius = 0
  Height = 800
  Length = 320
  MakeFace = false
  Placement = pos=(8785,1470,0) rot=(0,0,1;0rad)
  Rows = 1
FEATURE [Part::FeaturePython] Structure158  label="Вентстояк вычитаемы объём 002"  # Arch/BIM 52 (typed FeaturePython)
  Base = -> Rectangle2597
  FaceMaker = 0
  GlobalId = 2VgUxAGbH6UvSFD9GbSn_n
  Height = 4000
  HorizontalArea = 256000
  IfcData = IfcUID=2VgUxAGbH6UvSFD9GbSn_n,attributes={"GlobalId": {"value": "2VgUxAGbH6UvSFD9GbSn_n"}},+1 more (map truncated)
  IfcType = 52
  Length = 0
  MoveBase = false
  MoveWithHost = false
  Nodes = (2) [(8945,1870,0),(8945,1870,4000)]
  NodesOffset = 0
  Normal = (0,0,0)
  PerimeterLength = 2240
  Placement = pos=(0,0,2800) rot=(0,0,1;0rad)
  VerticalArea = 8960000
  Width = 100
FEATURE [Part::Extrusion] Extrude022  label="Габарит человека 004"
  Base = -> Sketch250
  Dir = (0,-1,2e-16)
  DirMode = 2
  FaceMakerClass = Part::FaceMakerBullseye
  LengthFwd = 290
  LengthRev = 0
  Placement = pos=(11840.4,4373.49,3130) rot=(0,0,1;1.5708rad)
  Solid = true
  Symmetric = false
FEATURE [App::GeometryPython] BuildingPart036  label="Эргономика"  # Arch/BIM 52 (typed FeaturePython)
  Area = 0
  GlobalId = 1U0bveIaj1buNClxqFBVzz
  Group = -> [Extrude007,Extrude008,Extrude012,Extrude022]
  Height = 0
  HeightPropagate = true
  IfcData = IfcUID=1U0bveIaj1buNClxqFBVzz,attributes={"GlobalId": {"value": "1U0bveIaj1buNClxqFBVzz"}},+1 more (map truncated)
  IfcType = 52
  LevelOffset = 0
FEATURE [Part::FeaturePython] Wall145  label="табуретка"  # Arch/BIM 166 (typed FeaturePython)
  Align = 2
  Area = 1992000
  BlockHeight = 0
  BlockLength = 0
  CountBroken = 0
  CountEntire = 0
  Face = 0
  Height = 150
  HorizontalArea = 1.328e+06
  IfcType = 166
  Joint = 0
  Length = 13280
  MakeBlocks = false
  MoveBase = false
  MoveWithHost = false
  Normal = (0,0,0)
  OffsetFirst = 0
  OffsetSecond = 0
  PerimeterLength = 26760
  Placement = pos=(0,0,5260) rot=(0,0,1;0rad)
  PredefinedType = 0
  VerticalArea = 4.014e+06
  Width = 100
FEATURE [Part::FeaturePython] Wall146  label="Wall010"  # Arch/BIM 166 (typed FeaturePython)
  Align = 2
  Area = 420000
  BlockHeight = 0
  BlockLength = 0
  CountBroken = 0
  CountEntire = 0
  Face = 0
  Height = 150
  HorizontalArea = 280000
  IfcType = 166
  Joint = 0
  Length = 2800
  MakeBlocks = false
  MoveBase = false
  MoveWithHost = true
  Normal = (0,0,0)
  OffsetFirst = 0
  OffsetSecond = 0
  PerimeterLength = 5800
  Placement = pos=(0,0,3210) rot=(0,0,1;0rad)
  PredefinedType = 0
  VerticalArea = 870000
  Width = 100
FEATURE [Part::Part2DObjectPython] Line1228  label="Line1229"  # Draft 2D object (typed FeaturePython)
  ChamferSize = 0
  Closed = false
  End = (903.033,1056.97,0)
  FilletRadius = 0
  Length = 150
  MakeFace = false
  Placement = pos=(796.967,1163.03,0) rot=(0,0,1;0rad)
  Points = (2) [(0,0,0),(106.066,-106.066,0)]
  Start = (796.967,1163.03,0)
  Subdivisions = 0
FEATURE [Part::Part2DObjectPython] Line1229  label="Line1230"  # Draft 2D object (typed FeaturePython)
  ChamferSize = 0
  Closed = false
  End = (12453,8446.97,0)
  FilletRadius = 0
  Length = 150
  MakeFace = false
  Placement = pos=(12347,8553.03,0) rot=(0,0,1;0rad)
  Points = (2) [(0,0,0),(106.066,-106.066,0)]
  Start = (12347,8553.03,0)
  Subdivisions = 0
FEATURE [Part::Part2DObjectPython] Line1230  label="Line1231"  # Draft 2D object (typed FeaturePython)
  ChamferSize = 0
  Closed = false
  End = (13389.9,7510.05,0)
  FilletRadius = 0
  Length = 2800
  MakeFace = false
  Placement = pos=(11410.1,9489.95,0) rot=(0,0,1;0rad)
  Points = (2) [(0,0,0),(1979.9,-1979.9,0)]
  Start = (11410.1,9489.95,0)
  Subdivisions = 0
FEATURE [Part::FeaturePython] Wall149  label="Wall012"  # Arch/BIM 166 (typed FeaturePython)
  Align = 2
  Area = 420000
  Base = -> Line1230
  BlockHeight = 0
  BlockLength = 0
  CountBroken = 0
  CountEntire = 0
  Face = 0
  Height = 150
  HorizontalArea = 280000
  IfcType = 166
  Joint = 0
  Length = 2800
  MakeBlocks = false
  MoveBase = false
  MoveWithHost = true
  Normal = (0,0,0)
  OffsetFirst = 0
  OffsetSecond = 0
  PerimeterLength = 5800
  Placement = pos=(0,0,3210) rot=(0,0,1;0rad)
  PredefinedType = 0
  VerticalArea = 870000
  Width = 100
FEATURE [Part::Part2DObjectPython] Line1231  label="Line1232"  # Draft 2D object (typed FeaturePython)
  ChamferSize = 0
  Closed = false
  End = (903.033,8553.03,0)
  FilletRadius = 0
  Length = 150
  MakeFace = false
  Placement = pos=(796.967,8446.97,0) rot=(0,0,1;1.5708rad)
  Points = (2) [(0,0,0),(106.066,-106.066,0)]
  Start = (796.967,8446.97,0)
  Subdivisions = 0
FEATURE [Part::Part2DObjectPython] Line1232  label="Line1233"  # Draft 2D object (typed FeaturePython)
  ChamferSize = 0
  Closed = false
  End = (1839.95,9489.95,0)
  FilletRadius = 0
  Length = 2800
  MakeFace = false
  Placement = pos=(-139.949,7510.05,0) rot=(0,0,1;1.5708rad)
  Points = (2) [(0,0,0),(1979.9,-1979.9,0)]
  Start = (-139.949,7510.05,0)
  Subdivisions = 0
FEATURE [Part::FeaturePython] Wall152  label="Wall014"  # Arch/BIM 166 (typed FeaturePython)
  Align = 2
  Area = 420000
  Base = -> Line1232
  BlockHeight = 0
  BlockLength = 0
  CountBroken = 0
  CountEntire = 0
  Face = 0
  Height = 150
  HorizontalArea = 280000
  IfcType = 166
  Joint = 0
  Length = 2800
  MakeBlocks = false
  MoveBase = false
  MoveWithHost = true
  Normal = (0,0,0)
  OffsetFirst = 0
  OffsetSecond = 0
  PerimeterLength = 5800
  Placement = pos=(0,0,3210) rot=(0,0,1;0rad)
  PredefinedType = 0
  VerticalArea = 870000
  Width = 100
FEATURE [Part::Part2DObjectPython] Line1233  label="Line1234"  # Draft 2D object (typed FeaturePython)
  ChamferSize = 0
  Closed = false
  End = (12453,1163.03,0)
  FilletRadius = 0
  Length = 150
  MakeFace = false
  Placement = pos=(12347,1056.97,0) rot=(0,0,1;1.5708rad)
  Points = (2) [(0,0,0),(106.066,-106.066,0)]
  Start = (12347,1056.97,0)
  Subdivisions = 0
FEATURE [Part::Part2DObjectPython] Line1234  label="Line1235"  # Draft 2D object (typed FeaturePython)
  ChamferSize = 0
  Closed = false
  End = (13389.9,2099.95,0)
  FilletRadius = 0
  Length = 2800
  MakeFace = false
  Placement = pos=(11410.1,120.051,0) rot=(0,0,1;1.5708rad)
  Points = (2) [(0,0,0),(1979.9,-1979.9,0)]
  Start = (11410.1,120.051,0)
  Subdivisions = 0
FEATURE [Part::FeaturePython] Wall155  label="Wall016"  # Arch/BIM 166 (typed FeaturePython)
  Align = 2
  Area = 420000
  Base = -> Line1234
  BlockHeight = 0
  BlockLength = 0
  CountBroken = 0
  CountEntire = 0
  Face = 0
  Height = 150
  HorizontalArea = 280000
  IfcType = 166
  Joint = 0
  Length = 2800
  MakeBlocks = false
  MoveBase = false
  MoveWithHost = true
  Normal = (0,0,0)
  OffsetFirst = 0
  OffsetSecond = 0
  PerimeterLength = 5800
  Placement = pos=(0,0,3210) rot=(0,0,1;0rad)
  PredefinedType = 0
  VerticalArea = 870000
  Width = 100
FEATURE [Part::Part2DObjectPython] Rectangle2651  label="уширение фундамента 001"  # Draft 2D object (typed FeaturePython)
  ChamferSize = 0
  Columns = 1
  FilletRadius = 0
  Height = 1030
  Length = 130
  MakeFace = false
  Placement = pos=(3600,5330,0) rot=(0,0,1;0rad)
  Rows = 1
FEATURE [Part::FeaturePython] Structure172  label="уширение фундамента001"  # Arch/BIM 52 (typed FeaturePython)
  Base = -> Rectangle2651
  FaceMaker = 0
  Height = 500
  HorizontalArea = 133900
  IfcData = complex_attributes={"OwnerHistory": {}, "IsNestedBy": {}, "IsDecomposedBy": {}, "IsDefinedBy": {}, "ObjectPlacement": {}, "Representation":... (+4 chars omitted)
  IfcType = 52
  Length = 0
  MoveBase = false
  MoveWithHost = false
  Nodes = (2) [(3665,5845,0),(3665,5845,-500)]
  NodesOffset = 0
  Normal = (0,0,-1)
  PerimeterLength = 2320
  Placement = pos=(0,0,-180) rot=(0,0,1;0rad)
  VerticalArea = 1160000
  Width = 100
FEATURE [Part::FeaturePython] Wall038  label="фундамент внутр. стена 001"  # Arch/BIM 166 (typed FeaturePython)
  Additions = -> [Wall037,Structure172]
  Align = 2
  Area = 1.56e+06
  Base = -> Line1074
  BlockHeight = 0
  BlockLength = 0
  CountBroken = 0
  CountEntire = 0
  Face = 0
  Height = 300
  HorizontalArea = 2.6e+06
  IfcType = 166
  Joint = 0
  Length = 5200
  MakeBlocks = false
  MoveBase = false
  MoveWithHost = false
  Normal = (0,0,-1)
  OffsetFirst = 0
  OffsetSecond = 0
  PerimeterLength = 28620
  Placement = pos=(-25,0,-680) rot=(0,0,1;0rad)
  PredefinedType = 0
  VerticalArea = 9e+06
  Width = 500
FEATURE [Part::Part2DObjectPython] Rectangle556  label="вытяжка осн мал"  # Draft 2D object (typed FeaturePython)
  ChamferSize = 0
  Columns = 1
  FilletRadius = 0
  Height = 400
  Length = 400
  MakeFace = false
  Placement = pos=(11300,375,1600) rot=(0,0,-1;1.5708rad)
  Rows = 1
FEATURE [Part::Box] Box3145  label="ТВ"
  AttacherType = Attacher::AttachEngine3D
  Height = 750
  Length = 1400
  Placement = pos=(8090,6200,620) rot=(0,0,-1;1.5708rad)
  Width = 100
FEATURE [Part::Box] Box3143  label="шкаф книжн. "
  AttacherType = Attacher::AttachEngine3D
  Height = 2700
  Length = 900
  Placement = pos=(320,-25,0) rot=(0,0,1;1.5708rad)
  Width = 350
FEATURE [Part::Part2DObjectPython] Rectangle555  label="вытяжка осн бол"  # Draft 2D object (typed FeaturePython)
  ChamferSize = 0
  Columns = 1
  FilletRadius = 0
  Height = 600
  Length = 500
  MakeFace = false
  Placement = pos=(11200,475,1550) rot=(0,0,-1;1.5708rad)
  Rows = 1
FEATURE [Part::Loft] Loft001  label="вытяжка"
  Closed = false
  MaxDegree = 5
  Ruled = false
  Sections = -> [Rectangle555,Rectangle556]
  Solid = true
FEATURE [Part::Feature] Fillet001  label="стол обеденный"
  Placement = pos=(10350,2890,0) rot=(0,0,1;0rad)
  shape: bbox 1500 x 750 x 750 mm, 30 faces (baked)
FEATURE [Part::Feature] Fusion013  label="стул005"
  Placement = pos=(10350,2890,0) rot=(0,0,1;0rad)
  shape: bbox 480 x 520 x 910 mm, 35 faces (baked)
FEATURE [Part::Feature] Fusion014  label="стул006"
  Placement = pos=(10350,2890,0) rot=(0,0,1;0rad)
  shape: bbox 480 x 520 x 910 mm, 35 faces (baked)
FEATURE [Part::Feature] Fusion015  label="стул007"
  Placement = pos=(10350,2890,0) rot=(0,0,1;0rad)
  shape: bbox 480 x 520 x 910 mm, 35 faces (baked)
FEATURE [Part::Feature] Fusion016  label="стул008"
  Placement = pos=(10350,2890,0) rot=(0,0,1;0rad)
  shape: bbox 480 x 520 x 910 mm, 35 faces (baked)
FEATURE [Part::Box] Box3154  label="шкаф 55 одежда 001"
  AttacherType = Attacher::AttachEngine3D
  Height = 2700
  Length = 2310
  Placement = pos=(7300,-25,0) rot=(0,0,1;1.5708rad)
  Width = 500
FEATURE [Part::Box] Box3155  label="шкаф 60 одежда 002"
  AttacherType = Attacher::AttachEngine3D
  Height = 2700
  Length = 1500
  Placement = pos=(4100,1685,0) rot=(0,0,1;0rad)
  Width = 600
FEATURE [Part::Box] Box3156  label="шкаф 60 одежда 003"
  AttacherType = Attacher::AttachEngine3D
  Height = 2700
  Length = 2310
  Placement = pos=(4000,-25,0) rot=(0,0,1;1.5708rad)
  Width = 600
FEATURE [Part::Box] Box3157  label="шкаф 60 одежда 004"
  AttacherType = Attacher::AttachEngine3D
  Height = 2700
  Length = 1400
  Placement = pos=(-30,5025,0) rot=(0,0,1;0rad)
  Width = 600
FEATURE [Part::Box] Box3159  label="ТВ001"
  AttacherType = Attacher::AttachEngine3D
  Height = 750
  Length = 1200
  Placement = pos=(4720,6225,620) rot=(0,0,-1;1.5708rad)
  Width = 75
FEATURE [Part::Box] Box3163  label="обувница"
  AttacherType = Attacher::AttachEngine3D
  Height = 500
  Length = 1500
  Placement = pos=(4100,-25,0) rot=(0,0,1;0rad)
  Width = 400
FEATURE [Part::Feature] Fusion019  label="кровать 2 спальная 210х170 002"
  Placement = pos=(6970,7925,0) rot=(0,0,-1;1.5708rad)
  shape: bbox 2100 x 1700 x 800 mm, 53 faces (baked)
FEATURE [Part::Feature] Fusion027  label="Диван кабинет"
  Placement = pos=(3475,2970,0) rot=(0,0,1;3.14159rad)
  shape: bbox 1950 x 950 x 800 mm, 23 faces (baked)
FEATURE [Part::Box] Box3175  label="Холодильник"
  AttacherType = Attacher::AttachEngine3D
  Height = 1600
  Length = 600
  Placement = pos=(10150,-10,0) rot=(0,0,1;1.5708rad)
  Width = 600
FEATURE [Part::Box] Box3178  label="шкаф 45 кухонный 002"
  AttacherType = Attacher::AttachEngine3D
  Height = 700
  Length = 1800
  Placement = pos=(10750,-10,1600) rot=(0,0,1;0rad)
  Width = 450
FEATURE [Part::Box] Box3179  label="шкаф 60 кухонный 003"
  AttacherType = Attacher::AttachEngine3D
  Height = 700
  Length = 600
  Placement = pos=(9550,-10,1600) rot=(0,0,1;0rad)
  Width = 600
FEATURE [Part::Feature] Fillet003  label="Столик журнальный"
  Placement = pos=(13600,-900,0) rot=(0,0,1;0rad)
  shape: bbox 1000 x 1000 x 530 mm, 34 faces, 5 solids (baked)
FEATURE [Part::Box] Box3183  label="морозильник 60 см"
  AttacherType = Attacher::AttachEngine3D
  Height = 1800
  Length = 600
  Placement = pos=(8250,-25,0) rot=(0,0,1;0rad)
  Width = 600
FEATURE [Part::Box] Box3184  label="СМ"
  AttacherType = Attacher::AttachEngine3D
  Height = 800
  Length = 600
  Placement = pos=(8850,-25,0) rot=(0,0,1;0rad)
  Width = 600
FEATURE [Part::Feature] Fusion041  label="унитаз с инсталляцией 002"
  Placement = pos=(9508.52,16323.1,0) rot=(0,0,1;3.92699rad)
  shape: bbox 677.3 x 677.3 x 1150 mm, 15 faces (baked)
FEATURE [Part::Box] Box3191  label="кулер"
  AttacherType = Attacher::AttachEngine3D
  Height = 950
  Length = 310
  Placement = pos=(12240,4575,0) rot=(0,0,1;0rad)
  Width = 310
FEATURE [Part::Cylinder] Cylinder  label="бутыль воды"
  Angle = 360
  AttacherType = Attacher::AttachEngine3D
  Height = 400
  Placement = pos=(12395,4730,950) rot=(0,0,1;0rad)
  Radius = 150
FEATURE [Part::Box] Box3192  label="кофеварка"
  AttacherType = Attacher::AttachEngine3D
  Height = 250
  Length = 200
  Placement = pos=(12494,3045.99,850) rot=(0,0,1;1.5708rad)
  Width = 250
FEATURE [Part::Cylinder] Cylinder001  label="чайник"
  Angle = 360
  AttacherType = Attacher::AttachEngine3D
  Height = 250
  Placement = pos=(12393.3,3359.1,850) rot=(0,0,1;1.5708rad)
  Radius = 75
FEATURE [Part::Box] Box3195  label="шкаф 45 кухонный 003"
  AttacherType = Attacher::AttachEngine3D
  Height = 400
  Length = 3000
  Placement = pos=(9550,-10,2300) rot=(0,0,1;0rad)
  Width = 600
FEATURE [Part::Part2DObjectPython] Rectangle2663  label="уширение фундамента 002"  # Draft 2D object (typed FeaturePython)
  ChamferSize = 0
  Columns = 1
  FilletRadius = 0
  Height = 1030
  Length = 130
  MakeFace = false
  Placement = pos=(9650,4310,0) rot=(0,0,1;0rad)
  Rows = 1
FEATURE [Part::FeaturePython] Structure175  label="уширение фундамента002"  # Arch/BIM 52 (typed FeaturePython)
  Base = -> Rectangle2663
  FaceMaker = 0
  Height = 500
  HorizontalArea = 133900
  IfcData = complex_attributes={"OwnerHistory": {}, "IsNestedBy": {}, "IsDecomposedBy": {}, "IsDefinedBy": {}, "ObjectPlacement": {}, "Representation":... (+4 chars omitted)
  IfcType = 52
  Length = 0
  MoveBase = false
  MoveWithHost = false
  Nodes = (2) [(9715,4825,0),(9715,4825,-500)]
  NodesOffset = 0
  Normal = (0,0,-1)
  PerimeterLength = 2320
  Placement = pos=(0,0,-180) rot=(0,0,1;0rad)
  VerticalArea = 1160000
  Width = 100
FEATURE [Part::FeaturePython] Wall130  label="фундамент внутр. стена 002"  # Arch/BIM 166 (typed FeaturePython)
  Additions = -> [Wall129,Structure175]
  Align = 2
  Area = 2727000
  Base = -> Line1201
  BlockHeight = 0
  BlockLength = 0
  CountBroken = 0
  CountEntire = 0
  Face = 0
  Height = 300
  HorizontalArea = 4.55015e+06
  IfcType = 166
  Joint = 0
  Length = 9090
  MakeBlocks = false
  MoveBase = false
  MoveWithHost = false
  Normal = (0,0,-1)
  OffsetFirst = 0
  OffsetSecond = 0
  PerimeterLength = 28620
  Placement = pos=(0,0,-680) rot=(0,0,1;0rad)
  PredefinedType = 0
  VerticalArea = 15224000
  Width = 500
FEATURE [Part::Part2DObjectPython] Rectangle2695  label="Д90-007"  # Draft 2D object (typed FeaturePython)
  ChamferSize = 0
  Columns = 1
  FilletRadius = 0
  Height = 100
  Length = 900
  MakeFace = true
  Placement = pos=(9550,770,0) rot=(0,0,1;1.5708rad)
  Rows = 1
FEATURE [Part::FeaturePython] Structure026  label="Проём-Д90-020"  # Arch/BIM 52 (typed FeaturePython)
  Base = -> Rectangle2695
  FaceMaker = 0
  Height = 2170
  HorizontalArea = 90000
  IfcData = complex_attributes={"OwnerHistory": {}, "IsNestedBy": {}, "IsDecomposedBy": {}, "IsDefinedBy": {}, "ObjectPlacement": {}, "Representation":... (+4 chars omitted)
  IfcType = 52
  Length = 0
  MoveBase = false
  MoveWithHost = false
  Nodes = (2) [(13000,6050,0),(13000,6050,2180)]
  NodesOffset = 0
  Normal = (0,0,0)
  PerimeterLength = 2000
  Placement = pos=(0,0,-20) rot=(0,0,1;0rad)
  VerticalArea = 4340000
  Width = 100
FEATURE [Part::Part2DObjectPython] Rectangle2630  label="Rectangle2624"  # Draft 2D object (typed FeaturePython)
  ChamferSize = 0
  Columns = 1
  FilletRadius = 0
  Height = 1500
  Length = 2100
  MakeFace = false
  Placement = pos=(1150,2125,0) rot=(0,0,-1;1.5708rad)
  Rows = 1
FEATURE [Part::Part2DObjectPython] Rectangle2684  label="Rectangle2703"  # Draft 2D object (typed FeaturePython)
  ChamferSize = 0
  Columns = 1
  FilletRadius = 0
  Height = 1800
  Length = 900
  MakeFace = true
  Placement = pos=(1000,925,0) rot=(0,0,-1;1.5708rad)
  Rows = 1
FEATURE [Part::Part2DObjectPython] Rectangle2712  label="Rectangle2673"  # Draft 2D object (typed FeaturePython)
  ChamferSize = 0
  Columns = 1
  FilletRadius = 0
  Height = 1200
  Length = 75
  MakeFace = false
  Placement = pos=(4795,6225,0) rot=(0,0,1;3.14159rad)
  Rows = 1
FEATURE [Part::Part2DObjectPython] Rectangle2717  label="Д90-006"  # Draft 2D object (typed FeaturePython)
  ChamferSize = 0
  Columns = 1
  FilletRadius = 0
  Height = 100
  Length = 900
  MakeFace = true
  Placement = pos=(5810,2285,0) rot=(0,0,1;0rad)
  Rows = 1
FEATURE [Part::FeaturePython] Structure024  label="Проём-Д90-019"  # Arch/BIM 52 (typed FeaturePython)
  Base = -> Rectangle2717
  FaceMaker = 0
  Height = 2170
  HorizontalArea = 90000
  IfcData = complex_attributes={"OwnerHistory": {}, "IsNestedBy": {}, "IsDecomposedBy": {}, "IsDefinedBy": {}, "ObjectPlacement": {}, "Representation":... (+4 chars omitted)
  IfcType = 52
  Length = 0
  MoveBase = false
  MoveWithHost = false
  Nodes = (2) [(5000,3050,0),(5000,3050,2180)]
  NodesOffset = 0
  Normal = (0,0,0)
  PerimeterLength = 2000
  Placement = pos=(0,0,-20) rot=(0,0,1;0rad)
  VerticalArea = 4340000
  Width = 100
FEATURE [Part::Part2DObjectPython] Rectangle2730  label="Д70-004"  # Draft 2D object (typed FeaturePython)
  ChamferSize = 0
  Columns = 1
  FilletRadius = 0
  Height = 110
  Length = 900
  MakeFace = true
  Placement = pos=(4930,6485,0) rot=(0,0,1;1.5708rad)
  Rows = 1
FEATURE [Part::FeaturePython] Structure141  label="Проём-Д90-001"  # Arch/BIM 52 (typed FeaturePython)
  Base = -> Rectangle2730
  FaceMaker = 0
  Height = 2170
  HorizontalArea = 99000
  IfcData = complex_attributes={"OwnerHistory": {}, "IsNestedBy": {}, "IsDecomposedBy": {}, "IsDefinedBy": {}, "ObjectPlacement": {}, "Representation":... (+4 chars omitted)
  IfcType = 52
  Length = 0
  MoveBase = false
  MoveWithHost = false
  Nodes = (2) [(10750,4050,0),(10750,4050,2180)]
  NodesOffset = 0
  Normal = (0,0,0)
  PerimeterLength = 2020
  Placement = pos=(0,0,-20) rot=(0,0,1;0rad)
  VerticalArea = 4.3834e+06
  Width = 100
FEATURE [Part::Part2DObjectPython] Rectangle2788  label="вн_контур"  # Draft 2D object (typed FeaturePython)
  ChamferSize = 0
  Columns = 1
  FilletRadius = 0
  Height = 7480
  Length = 12580
  MakeFace = false
  Placement = pos=(-30,-10,0) rot=(0,0,1;0rad)
  Rows = 1
FEATURE [Part::Part2DObjectPython] Rectangle2792  # Draft 2D object (typed FeaturePython)
  ChamferSize = 0
  Columns = 1
  FilletRadius = 0
  Height = 600
  Length = 600
  MakeFace = false
  Placement = pos=(10150,-25,0) rot=(0,0,1;0rad)
  Rows = 1
FEATURE [Part::Part2DObjectPython] Rectangle2795  label="Д90-002"  # Draft 2D object (typed FeaturePython)
  ChamferSize = 0
  Columns = 1
  FilletRadius = 0
  Height = 290
  Length = 920
  MakeFace = true
  Placement = pos=(3850,3535,0) rot=(0,0,1;0rad)
  Rows = 1
FEATURE [Part::FeaturePython] Structure023  label="Проём-Д90-018"  # Arch/BIM 52 (typed FeaturePython)
  Base = -> Rectangle2795
  FaceMaker = 0
  Height = 2350
  HorizontalArea = 266800
  IfcData = complex_attributes={"OwnerHistory": {}, "IsNestedBy": {}, "IsDecomposedBy": {}, "IsDefinedBy": {}, "ObjectPlacement": {}, "Representation":... (+4 chars omitted)
  IfcType = 52
  Length = 0
  MoveBase = false
  MoveWithHost = false
  Nodes = (2) [(8900,5350,0),(8900,5350,2180)]
  NodesOffset = 0
  Normal = (0,0,0)
  PerimeterLength = 2420
  Placement = pos=(0,0,-200) rot=(0,0,1;0rad)
  VerticalArea = 5687000
  Width = 100
FEATURE [Part::Part2DObjectPython] Rectangle2798  label="Д90-005"  # Draft 2D object (typed FeaturePython)
  ChamferSize = 0
  Columns = 1
  FilletRadius = 0
  Height = 100
  Length = 900
  MakeFace = true
  Placement = pos=(3500,2535,0) rot=(0,0,1;1.5708rad)
  Rows = 1
FEATURE [Part::FeaturePython] Structure021  label="Проём-Д90-017"  # Arch/BIM 52 (typed FeaturePython)
  Base = -> Rectangle2798
  FaceMaker = 0
  Height = 2170
  HorizontalArea = 90000
  IfcData = complex_attributes={"OwnerHistory": {}, "IsNestedBy": {}, "IsDecomposedBy": {}, "IsDefinedBy": {}, "ObjectPlacement": {}, "Representation":... (+4 chars omitted)
  IfcType = 52
  Length = 0
  MoveBase = false
  MoveWithHost = false
  Nodes = (2) [(7500,3050,0),(7500,3050,2180)]
  NodesOffset = 0
  Normal = (0,0,0)
  PerimeterLength = 2000
  Placement = pos=(0,0,-20) rot=(0,0,1;0rad)
  VerticalArea = 4340000
  Width = 100
FEATURE [Part::Part2DObjectPython] Rectangle2807  label="Д90-001"  # Draft 2D object (typed FeaturePython)
  ChamferSize = 0
  Columns = 1
  FilletRadius = 0
  Height = 290
  Length = 920
  MakeFace = true
  Placement = pos=(6720,3825,0) rot=(0,0,1;3.14159rad)
  Rows = 1
FEATURE [Part::FeaturePython] Structure020  label="Проём-Д90-016"  # Arch/BIM 52 (typed FeaturePython)
  Base = -> Rectangle2807
  FaceMaker = 0
  Height = 2350
  HorizontalArea = 266800
  IfcData = complex_attributes={"OwnerHistory": {}, "IsNestedBy": {}, "IsDecomposedBy": {}, "IsDefinedBy": {}, "ObjectPlacement": {}, "Representation":... (+4 chars omitted)
  IfcType = 52
  Length = 0
  MoveBase = false
  MoveWithHost = false
  Nodes = (2) [(650,-4000,0),(650,-4000,2250)]
  NodesOffset = 0
  Normal = (0,0,0)
  PerimeterLength = 2420
  Placement = pos=(0,0,-200) rot=(0,0,1;0rad)
  VerticalArea = 5687000
  Width = 100
FEATURE [Part::Part2DObjectPython] Rectangle2808  # Draft 2D object (typed FeaturePython)
  ChamferSize = 0
  Columns = 1
  FilletRadius = 0
  Height = 600
  Length = 600
  MakeFace = true
  Placement = pos=(8850,-25,0) rot=(0,0,1;0rad)
  Rows = 1
FEATURE [Part::Part2DObjectPython] Rectangle  label="контур по облицовке"  # Draft 2D object (typed FeaturePython)
  ChamferSize = 0
  Columns = 1
  FilletRadius = 0
  Height = 8570
  Length = 13640
  MakeFace = false
  Placement = pos=(-560,-555,0) rot=(0,0,1;0rad)
  Rows = 1
FEATURE [Part::Extrusion] Extrude061  label="ПНО 40-10-6-003"
  Base = -> Sketch249
  Dir = (0,3980,0)
  DirMode = 0
  FaceMakerClass = Part::FaceMakerBullseye
  LengthFwd = 3980
  LengthRev = 0
  Placement = pos=(10,3685,2800) rot=(0,0,1;0rad)
  Solid = true
  Symmetric = false
FEATURE [Part::Extrusion] Extrude062  label="ПНО 40-12-8-003"
  Base = -> Sketch231
  Dir = (0,3980,0)
  DirMode = 0
  FaceMakerClass = Part::FaceMakerBullseye
  LengthFwd = 3980
  LengthRev = 0
  Placement = pos=(10,3685,2800) rot=(0,0,1;0rad)
  Solid = true
  Symmetric = false
FEATURE [Part::FeaturePython] Array038  label="ПНО-40-12 3шт."  # Draft array (typed FeaturePython)
  Angle = 360
  ArrayType = 0
  Axis = (0,0,1)
  Base = -> Extrude062
  Center = (0,0,0)
  Fuse = false
  IntervalAxis = (0,0,0)
  IntervalX = (1215,0,0)
  IntervalY = (0,0,0)
  IntervalZ = (0,0,1)
  NumberPolar = 1
  NumberX = 3
  NumberY = 1
  NumberZ = 1
  Placement = pos=(7920,9.09e-13,0) rot=(0,0,1;0rad)
FEATURE [Part::Part2DObjectPython] Rectangle544  # Draft 2D object (typed FeaturePython)
  ChamferSize = 0
  Columns = 1
  FilletRadius = 25
  Height = 300
  Length = 2500
  MakeFace = false
  Placement = pos=(12525,4960,0) rot=(0,0,1;1.5708rad)
  Rows = 1
FEATURE [Part::Part2DObjectPython] Rectangle545  # Draft 2D object (typed FeaturePython)
  ChamferSize = 0
  Columns = 1
  FilletRadius = 25
  Height = 950
  Length = 2500
  MakeFace = true
  Placement = pos=(12525,4960,0) rot=(0,0,1;1.5708rad)
  Rows = 1
  Support = -> [Rectangle544]
FEATURE [Part::Part2DObjectPython] Rectangle546  # Draft 2D object (typed FeaturePython)
  ChamferSize = 0
  Columns = 1
  FilletRadius = 25
  Height = 1620
  Length = 250
  MakeFace = false
  Placement = pos=(12525,7210,0) rot=(0,0,1;1.5708rad)
  Rows = 1
FEATURE [Part::Part2DObjectPython] Rectangle547  # Draft 2D object (typed FeaturePython)
  ChamferSize = 0
  Columns = 1
  FilletRadius = 25
  Height = 950
  Length = 250
  MakeFace = false
  Placement = pos=(12525,4960,0) rot=(0,0,1;1.5708rad)
  Rows = 1
FEATURE [Part::Part2DObjectPython] Rectangle2837  # Draft 2D object (typed FeaturePython)
  ChamferSize = 0
  Columns = 1
  FilletRadius = 25
  Height = 670
  Length = 900
  MakeFace = true
  Placement = pos=(11575,6560,0) rot=(0,0,1;1.5708rad)
  Rows = 1
FEATURE [Part::Part2DObjectPython] Rectangle2857  label="ОК-144-001"  # Draft 2D object (typed FeaturePython)
  ChamferSize = 0
  Columns = 1
  FilletRadius = 0
  Height = 410
  Length = 1440
  MakeFace = true
  Placement = pos=(-30,1840,0) rot=(0,0,1;1.5708rad)
  Rows = 1
FEATURE [Part::FeaturePython] Structure285  label="Проём-ОК-144-001"  # Arch/BIM 52 (typed FeaturePython)
  Base = -> Rectangle2857
  FaceMaker = 0
  Height = 1617
  HorizontalArea = 590400
  IfcData = complex_attributes={"OwnerHistory": {}, "IsNestedBy": {}, "IsDecomposedBy": {}, "IsDefinedBy": {}, "ObjectPlacement": {}, "Representation":... (+4 chars omitted)
  IfcType = 52
  Length = 0
  MoveBase = false
  MoveWithHost = false
  Nodes = (2) [(-8120,-170,0),(-8120,-170,1500)]
  NodesOffset = 0
  Normal = (0,0,0)
  PerimeterLength = 3700
  Placement = pos=(0,0,955) rot=(0,0,1;0rad)
  VerticalArea = 5982900
  Width = 100
FEATURE [Part::Part2DObjectPython] Rectangle2858  label="четверть_131-001"  # Draft 2D object (typed FeaturePython)
  ChamferSize = 0
  Columns = 1
  FilletRadius = 0
  Height = 120
  Length = 1310
  MakeFace = true
  Placement = pos=(-560,3215,0) rot=(0,0,-1;1.5708rad)
  Rows = 1
FEATURE [Part::Part2DObjectPython] Line1266  label="Line1267"  # Draft 2D object (typed FeaturePython)
  ChamferSize = 0
  Closed = false
  End = (-560,1775,0)
  FilletRadius = 0
  Length = 1570
  MakeFace = true
  Placement = pos=(-560,3345,0) rot=(0,0,-1;1.5708rad)
  Points = (2) [(0,0,0),(1570,-3.41061e-13,0)]
  Start = (-560,3345,0)
  Subdivisions = 0
FEATURE [Part::Part2DObjectPython] Line1271  label="Line1272"  # Draft 2D object (typed FeaturePython)
  ChamferSize = 0
  Closed = true
  End = (8660,1835,0)
  FilletRadius = 0
  Length = 800
  MakeFace = false
  Placement = pos=(11240,5185,0) rot=(0,0,-1;1.5708rad)
  Points = (2) [(3350,-1780,0),(3350,-2580,0)]
  Start = (9460,1835,0)
  Subdivisions = 0
FEATURE [Part::FeaturePython] Wall162  label="перегородка 042"  # Arch/BIM 166 (typed FeaturePython)
  Align = 2
  Area = 2.24e+06
  Base = -> Line1271
  BlockHeight = 250
  BlockLength = 0
  CountBroken = 0
  CountEntire = 0
  Face = 0
  Height = 2800
  HorizontalArea = 64000
  IfcType = 166
  Joint = 0
  Length = 800
  MakeBlocks = false
  MoveBase = false
  MoveWithHost = false
  Normal = (0,0,0)
  OffsetFirst = 0
  OffsetSecond = 300
  PerimeterLength = 1760
  PredefinedType = 0
  VerticalArea = 4.928e+06
  Width = 80
FEATURE [Part::Box] Box3203  label="шкаф подвесной"
  AttacherType = Attacher::AttachEngine3D
  Height = 1000
  Length = 600
  Placement = pos=(8850,-25,800) rot=(0,0,1;0rad)
  Width = 600
FEATURE [Part::Box] Box3204  label="шкаф 001"
  AttacherType = Attacher::AttachEngine3D
  Height = 2700
  Length = 1215
  Placement = pos=(370,3810,0) rot=(0,0,1;1.5708rad)
  Width = 400
FEATURE [Part::Box] Box3205  label="шкаф 60 кухонный 011"
  AttacherType = Attacher::AttachEngine3D
  Height = 850
  Length = 1800
  Placement = pos=(10750,-10,0) rot=(0,0,1;0rad)
  Width = 600
FEATURE [Part::FeaturePython] Wall163  label="отделка цоколя"  # Arch/BIM 166 (typed FeaturePython)
  Align = 1
  Area = 11870000
  BlockHeight = 600
  BlockLength = 600
  CountBroken = 1
  CountEntire = 0
  Face = 0
  Height = 250
  HorizontalArea = 474800
  IfcType = 166
  Joint = 1
  Length = 47480
  MakeBlocks = true
  MoveBase = false
  MoveWithHost = false
  Normal = (0,0,-1)
  Offset = 80
  OffsetFirst = 0
  OffsetSecond = 0
  PerimeterLength = 94980
  Placement = pos=(0,0,-380) rot=(0,0,1;0rad)
  PredefinedType = 0
  VerticalArea = 23745000
  Width = 10
FEATURE [Part::Part2DObjectPython] Rectangle2939  # Draft 2D object (typed FeaturePython)
  ChamferSize = 0
  Columns = 1
  FilletRadius = 100
  Height = 800
  Length = 1500
  MakeFace = true
  Placement = pos=(10350,3265,0) rot=(0,0,1;0rad)
  Rows = 1
FEATURE [Part::Part2DObjectPython] Rectangle2941  # Draft 2D object (typed FeaturePython)
  ChamferSize = 0
  Columns = 1
  FilletRadius = 0
  Height = 300
  Length = 500
  MakeFace = true
  Placement = pos=(10490,4065,0) rot=(0,0,1;0rad)
  Rows = 1
FEATURE [Part::Part2DObjectPython] Rectangle2944  # Draft 2D object (typed FeaturePython)
  ChamferSize = 0
  Columns = 1
  FilletRadius = 0
  Height = 300
  Length = 500
  MakeFace = true
  Placement = pos=(10490,2965,0) rot=(0,0,1;0rad)
  Rows = 1
FEATURE [Part::FeaturePython] Structure155  label="Вентстояк вычитаемы объём 001"  # Arch/BIM 52 (typed FeaturePython)
  Base = -> Rectangle2589
  FaceMaker = 0
  Height = 6000
  HorizontalArea = 589000
  IfcData = complex_attributes={"OwnerHistory": {}, "IsNestedBy": {}, "IsDecomposedBy": {}, "IsDefinedBy": {}, "ObjectPlacement": {}, "Representation":... (+4 chars omitted)
  IfcType = 52
  Length = 0
  MoveBase = false
  MoveWithHost = false
  Nodes = (2) [(-3390,9095,0),(-3390,9095,6000)]
  NodesOffset = 0
  Normal = (0,0,0)
  PerimeterLength = 3860
  Placement = pos=(0,0,-180) rot=(0,0,1;0rad)
  VerticalArea = 2.316e+07
  Width = 100
FEATURE [Part::Part2DObjectPython] ShapeString131  # Draft 2D object (typed FeaturePython)
  FontFile = <path>
  Placement = pos=(9798.37,89.5753,0) rot=(0,0,1;0rad)
  Size = 300
  String = *
  Tracking = 0
FEATURE [Part::Part2DObjectPython] ShapeString133  # Draft 2D object (typed FeaturePython)
  FontFile = <path>
  Placement = pos=(8956.86,201.345,0) rot=(0,0,1;0rad)
  Size = 200
  String = СМ
  Tracking = 0
FEATURE [Part::Part2DObjectPython] Wire657  label="Облицовка 120мм 001"  # Draft 2D object (typed FeaturePython)
  Area = 856800
  ChamferSize = 0
  Closed = true
  End = (4240,-555,0)
  FilletRadius = 0
  Length = 14520
  MakeFace = true
  Placement = pos=(-560,-555,0) rot=(0,0,1;0rad)
  Points = (6) [(0,0,0),(0,2460,0),(120,2460,0),(120,120,0),(4800,120,0),(4800,4.54747e-13,0)]
  Start = (-560,-555,0)
  Subdivisions = 0
FEATURE [Part::Part2DObjectPython] Wire658  label="Облицовка 120мм 031"  # Draft 2D object (typed FeaturePython)
  Area = 108000
  ChamferSize = 0
  Closed = true
  End = (5670,-555,0)
  FilletRadius = 0
  Length = 2040
  MakeFace = true
  Placement = pos=(4067,-555,0) rot=(0,0,1;0rad)
  Points = (4) [(703,4.09273e-12,0),(703,120,0),(1603,120,0),(1603,3.29692e-12,0)]
  Start = (4770,-555,0)
  Subdivisions = 0
FEATURE [Part::Part2DObjectPython] Wire660  label="Облицовка 120мм 033"  # Draft 2D object (typed FeaturePython)
  Area = 108000
  ChamferSize = 0
  Closed = true
  End = (7620,-555,0)
  FilletRadius = 0
  Length = 2040
  MakeFace = true
  Placement = pos=(5617,-555,0) rot=(0,0,1;0rad)
  Points = (4) [(1103,2.27374e-12,0),(1103,120,0),(2003,120,0),(2003,2.95586e-12,0)]
  Start = (6720,-555,0)
  Subdivisions = 0
FEATURE [Part::Part2DObjectPython] Wire661  label="Облицовка 120мм 034"  # Draft 2D object (typed FeaturePython)
  Area = 810000
  ChamferSize = 0
  Closed = true
  End = (13080,-555,0)
  FilletRadius = 0
  Length = 13740
  MakeFace = true
  Placement = pos=(9970,-555,0) rot=(0,0,1;0rad)
  Points = (6) [(-1820,9.09495e-13,0),(-1820,120,0),(2990,120,0),(2990,1940,0),(3110,1940,0),(3110,4.54747e-13,0)]
  Start = (8150,-555,0)
  Subdivisions = 0
FEATURE [Part::Part2DObjectPython] Wire663  label="Облицовка 120мм 036"  # Draft 2D object (typed FeaturePython)
  Area = 108000
  ChamferSize = 0
  Closed = true
  End = (13080,4115,0)
  FilletRadius = 0
  Length = 2040
  MakeFace = true
  Placement = pos=(13080,2465,0) rot=(0,0,1;0rad)
  Points = (4) [(-3.63798e-12,750,0),(-120,750,0),(-120,1650,0),(-3.63798e-12,1650,0)]
  Start = (13080,3215,0)
  Subdivisions = 0
FEATURE [Part::Part2DObjectPython] Wire664  label="Облицовка 120мм 037"  # Draft 2D object (typed FeaturePython)
  Area = 669600
  ChamferSize = 0
  Closed = true
  End = (13080,8015,0)
  FilletRadius = 0
  Length = 11400
  MakeFace = true
  Placement = pos=(13080,6335,0) rot=(0,0,1;0rad)
  Points = (6) [(-1.81899e-12,-1430,0),(-120,-1430,0),(-120,1560,0),(-2590,1560,0),(-2590,1680,0),(0,1680,0)]
  Start = (13080,4905,0)
  Subdivisions = 0
FEATURE [Part::Part2DObjectPython] Wire665  label="Облицовка 120мм 038"  # Draft 2D object (typed FeaturePython)
  Area = 326400
  ChamferSize = 0
  Closed = true
  End = (5940,8015,0)
  FilletRadius = 0
  Length = 5680
  MakeFace = true
  Placement = pos=(9788,8015,0) rot=(0,0,1;0rad)
  Points = (4) [(-1128,9.09495e-13,0),(-1128,-120,0),(-3848,-120,0),(-3848,1.81899e-12,0)]
  Start = (8660,8015,0)
  Subdivisions = 0
FEATURE [Part::Part2DObjectPython] Wire667  label="Облицовка 120мм 040"  # Draft 2D object (typed FeaturePython)
  Area = 872400
  ChamferSize = 0
  Closed = true
  End = (-560,8015,0)
  FilletRadius = 0
  Length = 14780
  MakeFace = true
  Placement = pos=(1520,8015,0) rot=(0,0,1;0rad)
  Points = (6) [(510,9.09495e-13,0),(510,-120,0),(-1960,-120,0),(-1960,-4800,0),(-2080,-4800,0),(-2080,0,0)]
  Start = (2030,8015,0)
  Subdivisions = 0
FEATURE [Part::Part2DObjectPython] Wire670  label="Стены_и_перегородки 032"  # Draft 2D object (typed FeaturePython)
  Area = 494500
  ChamferSize = 0
  Closed = true
  End = (12550,3810,0)
  FilletRadius = 0
  Length = 3630
  MakeFace = true
  Placement = pos=(13210,6015,0) rot=(0,0,-1;1.5708rad)
  Points = (8) [(1970,-660,0),(1970,-260,0),(2735,-260,0),(2735,-660,0),(2495,-660,0),(2495,-1310,0),(2205,-1310,0),(2205,-660,0)]
  Start = (12550,4045,0)
  Subdivisions = 0
FEATURE [Part::Part2DObjectPython] Wire671  label="Стены_и_перегородки 033"  # Draft 2D object (typed FeaturePython)
  Area = 1.984e+06
  ChamferSize = 0
  Closed = true
  End = (12550,7470,0)
  FilletRadius = 0
  Length = 10720
  MakeFace = true
  Placement = pos=(10175,7700,0) rot=(0,0,1;0rad)
  Points = (6) [(352,-230,0),(352,170,0),(2775,170,0),(2775,-2767,0),(2375,-2767,0),(2375,-230,0)]
  Start = (10527,7470,0)
  Subdivisions = 0
FEATURE [Part::Part2DObjectPython] ShapeString135  # Draft 2D object (typed FeaturePython)
  FontFile = <path>
  Placement = pos=(12278.3,1358.24,0) rot=(0,0,1;1.5708rad)
  Size = 200
  String = ПМ
  Tracking = 0
FEATURE [Part::Part2DObjectPython] Rectangle2972  label="Камин"  # Draft 2D object (typed FeaturePython)
  Area = 400000
  ChamferSize = 0
  Columns = 1
  FilletRadius = 0
  Height = 500
  Length = 800
  MakeFace = true
  Placement = pos=(8750,1885,0) rot=(0,0,1;0rad)
  Rows = 1
FEATURE [Spreadsheet::Sheet] Spreadsheet  label="Площади помещений"
  cells = C1=N/N; D1=Помещение; E1=Площадь; C2=1); D2==<<Прихожая>>.Label; E2==<<Прихожая>>.Shape.Area; C3=2); D3==<<Тех.помещение>>.Label; E3==<<Тех.помещение>>.Shape.Area; C4=3); D4==<<Кабинет>>.Label; E4==<<Кабинет>>.Shape.Area; C5=4); D5==<<Кухня-столовая>>.Label; E5==<<Кухня-столовая>>.Shape.Area; C6=5); D6==<<СУ>>.Label; E6==<<СУ>>.Shape.Area; C7=6); D7==<<Душ>>.Label; E7==<<Душ>>.Shape.Area; C8=7); D8==<<Коридор>>.Label; E8==<<Коридор>>.Shape.Area; C9=8); D9==<<Спальня 1 этаж>>.Label; E9==<<Спальня 1 этаж>>.Shape.Area; C10=9); D10==<<Гостиная>>.Label; E10==<<Гостиная>>.Shape.Area; D11=Итого:; E11==sum(E2:E10); D12=Тёплый контур (Площадь этажа):; E12==<<Тёплый контур>>.Shape.Area; B14=Мансарда (к учёту по СП54.13330); D14==<<h2,5м площадь (к=1.0) 001>>.Label; E14==<<h2,5м площадь (к=1.0) 001>>.Shape.Area * 1; D15==<<h1,6м площадь (к=0.7) 001>>.Label; E15==<<h1,6м площадь (к=0.7) 001>>.Shape.Area * 0.7; D16==<<h1,6м площадь (к=0.7) 002>>.Label; E16==<<h1,6м площадь (к=0.7) 002>>.Shape.Area * 0.7; D17==<<Вычитаемая площадь проёма>>.Label; E17==<<Вычитаемая площадь проёма>>.Shape.Area; D18=Итого:; E18==sum(E14:E16) - E17; D20=Тёплый контур+Мансарда:; E20==E12 + E18; B22=Мансарда фактически (от h=1.2m); D22==<<мансарда h1.2m>>.Label; E22==<<мансарда h1.2m>>.Shape.Area; D23==<<проём в перекрытии 007>>.Label; E23==<<проём в перекрытии 007>>.Shape.Area; E24==E22 - E23; B29=Объёмы материалов (этап коробки под крышу с облицовкой, на готовый фундамент):; B30=Блок ЛСР "Тёплый" 10.7нф; D30==<<Внешняя стена ЛСР 380мм>>.Label; E30==<<Внешняя стена ЛСР 380мм>>.Shape.Volume; D31==<<Стена ЛСР 380мм ряд перекрытия 001>>.Label; E31==<<Стена ЛСР 380мм ряд перекрытия 001>>.Shape.Volume; D32==<<Стена ЛСР 380мм ряд перекрытия 002>>.Label; E32==<<Стена ЛСР 380мм ряд перекрытия 002>>.Shape.Volume; D33==<<Стена ЛСР 380мм под мауэрлат>>.Label; E33==<<Стена ЛСР 380мм под мауэрлат>>.Shape.Volume; D34=Итого:; E34==sum(E30:E33); B36=Кирпич рядовой 1нф и 2.1нф, в соотн. 1:2; D36==<<Стена 250mm 2.1нф+1нф>>.Label; E36==<<Стена 250mm 2.1нф+1нф>>.Shape.Volume; D37==<<Ряд 1нф по плитам ПНО 001>>.Label; E37==<<Ряд 1нф по плитам ПНО 001>>.Shape.Volume; D38==<<Ряд 1нф по плитам ПНО 002>>.Label; E38==<<Ряд 1нф по плитам ПНО 002>>.Shape.Volume; D39==<<Стена 3 ряда 1NF в уровне перекрытия 001>>.Label; E39==<<Стена 3 ряда 1NF в уровне перекрытия 001>>.Shape.Volume; D40==<<Стена 3 ряда 1NF в уровне перекрытия 002>>.Label; E40==<<Стена 3 ряда 1NF в уровне перекрытия 002>>.Shape.Volume; D41==<<ряд  2.1нф в уровне армпояса>>.Label; E41==<<ряд  2.1нф в уровне армпояса>>.Shape.Volume; D42=Итого:; E42==sum(E36:E41); B43=Бетон (без учёта армирования):; D44==<<Перемычки монолитные>>.Label; E44==<<Перемычки монолитные>>.Shape.Volume; D45==<<Армпояс001>>.Label; E45==<<Армпояс001>>.Shape.Volume; D46==<<Армпояс002>>.Label; E46==<<Армпояс002>>.Shape.Volume; D47==<<Армпояс003>>.Label; E47==<<Армпояс003>>.Shape.Volume; D48==<<Армпояс004>>.Label; E48==<<Армпояс004>>.Shape.Volume; D49=Итого:; E49==sum(E44:E44); B50=Утеплитель XPS 80mm и 100mm; D51==<<Утепление перемычек XPS 100mm>>.Label; E51==<<Утепление перемычек XPS 100mm>>.Shape.Volume; D52==<<Утепление торца плит XPS 80mm 001>>.Label; E52==<<Утепление торца плит XPS 80mm 001>>.Shape.Volume; D53==<<Утепление торца плит XPS 80mm 002>>.Label; E53==<<Утепление торца плит XPS 80mm 002>>.Shape.Volume; D54==<<XPS 80mm в уровне армпояса>>.Label; E54==<<XPS 80mm в уровне армпояса>>.Shape.Volume; D55=Итого:; E55==sum(E51:E54); D57=Перегородки 80mm; E57==<<Перегородки>>.Shape.Volume; D58=Утепление перемычек XPS 100mm; E58==<<Утепление перемычек XPS 100mm>>.Shape.Volume; D60=бетон Армпояс+Пол по грунту стяжка; D64=бетон (фундамент МЗЛФ); E64==<<фундамент МЗЛФ>>.Shape.Volume; D65=Утеплитель ЭППС (МЗЛФ); E65==<<утепл фунд. внешней.стены 002>>.Shape.Volume + <<утепл отмостки 001>>.Shape.Volume + <<Утеплитель полки облицовки>>.Shape.Volume; D67=Утепление перекрытия ПСБ25; E67==<<Утепление перекрытия XPS 100mm>>.Shape.Volume; D68=Пояс перекрытия+монолит.уч.; D69=стяжка перекрытия; E69==<<Стяжка пола 50мм>>.Shape.Volume; D70=опорный ряд  под мауэрлат; E70==<<Стена ЛСР 380мм под мауэрлат>>.Shape.Volume; D72=грунт в границах участка, h=1м; E72==<<грунт в границах участка>>.Shape.Volume
FEATURE [Part::Part2DObjectPython] Rectangle2973  label="Шкаф 60 014"  # Draft 2D object (typed FeaturePython)
  Area = 630000
  ChamferSize = 0
  Columns = 1
  FilletRadius = 0
  Height = 1800
  Length = 350
  MakeFace = true
  Placement = pos=(-30,-25,0) rot=(0,0,1;0rad)
  Rows = 1
FEATURE [Part::Part2DObjectPython] ShapeString138  # Draft 2D object (typed FeaturePython)
  FontFile = <path>
  Placement = pos=(5506.65,999.608,0) rot=(0,0,1;0rad)
  Size = 250
  String = 1
  Tracking = 0
FEATURE [Part::Part2DObjectPython] Circle088  # Draft 2D object (typed FeaturePython)
  Area = 0
  FirstAngle = 0
  LastAngle = 0
  MakeFace = false
  Placement = pos=(5600,1100,0) rot=(0,0,1;0rad)
  Radius = 200
FEATURE [Part::Part2DObjectPython] Circle089  label="Circle090"  # Draft 2D object (typed FeaturePython)
  Area = 0
  FirstAngle = 0
  LastAngle = 0
  MakeFace = false
  Placement = pos=(8400,1200,0) rot=(0,0,1;0rad)
  Radius = 200
FEATURE [Part::Part2DObjectPython] ShapeString139  # Draft 2D object (typed FeaturePython)
  FontFile = <path>
  Placement = pos=(8306.65,1099.61,0) rot=(0,0,1;0rad)
  Size = 250
  String = 2
  Tracking = 0
FEATURE [Part::Part2DObjectPython] Circle090  label="Circle091"  # Draft 2D object (typed FeaturePython)
  Area = 0
  FirstAngle = 0
  LastAngle = 0
  MakeFace = false
  Placement = pos=(2300,1700,0) rot=(0,0,1;0rad)
  Radius = 200
FEATURE [Part::Part2DObjectPython] ShapeString140  # Draft 2D object (typed FeaturePython)
  FontFile = <path>
  Placement = pos=(2206.65,1599.61,0) rot=(0,0,1;0rad)
  Size = 250
  String = 3
  Tracking = 0
FEATURE [Part::Part2DObjectPython] Circle091  label="Circle092"  # Draft 2D object (typed FeaturePython)
  Area = 0
  FirstAngle = 0
  LastAngle = 0
  MakeFace = false
  Placement = pos=(7396.98,4803.11,0) rot=(0,0,1;0rad)
  Radius = 200
FEATURE [Part::Part2DObjectPython] ShapeString141  # Draft 2D object (typed FeaturePython)
  FontFile = <path>
  Placement = pos=(7303.64,4702.72,0) rot=(0,0,1;0rad)
  Size = 250
  String = 6
  Tracking = 0
FEATURE [Part::Part2DObjectPython] Circle092  label="Circle093"  # Draft 2D object (typed FeaturePython)
  Area = 0
  FirstAngle = 0
  LastAngle = 0
  MakeFace = false
  Placement = pos=(10900,1200,0) rot=(0,0,1;0rad)
  Radius = 200
FEATURE [Part::Part2DObjectPython] ShapeString142  # Draft 2D object (typed FeaturePython)
  FontFile = <path>
  Placement = pos=(10806.7,1099.61,0) rot=(0,0,1;0rad)
  Size = 250
  String = 4
  Tracking = 0
FEATURE [Part::Part2DObjectPython] Circle093  label="Circle094"  # Draft 2D object (typed FeaturePython)
  Area = 0
  FirstAngle = 0
  LastAngle = 0
  MakeFace = false
  Placement = pos=(5757,4835.02,0) rot=(0,0,1;0rad)
  Radius = 200
FEATURE [Part::Part2DObjectPython] ShapeString143  # Draft 2D object (typed FeaturePython)
  FontFile = <path>
  Placement = pos=(5663.65,4734.63,0) rot=(0,0,1;0rad)
  Size = 250
  String = 5
  Tracking = 0
FEATURE [Part::Part2DObjectPython] Circle094  label="Circle095"  # Draft 2D object (typed FeaturePython)
  Area = 0
  FirstAngle = 0
  LastAngle = 0
  MakeFace = false
  Placement = pos=(4100,5600,0) rot=(0,0,1;0rad)
  Radius = 200
FEATURE [Part::Part2DObjectPython] ShapeString144  # Draft 2D object (typed FeaturePython)
  FontFile = <path>
  Placement = pos=(4006.65,5499.61,0) rot=(0,0,1;0rad)
  Size = 250
  String = 8
  Tracking = 0
FEATURE [Part::Part2DObjectPython] Circle095  label="Circle096"  # Draft 2D object (typed FeaturePython)
  Area = 0
  FirstAngle = 0
  LastAngle = 0
  MakeFace = false
  Placement = pos=(5303.7,2946.83,0) rot=(0,0,1;0rad)
  Radius = 200
FEATURE [Part::Part2DObjectPython] ShapeString145  # Draft 2D object (typed FeaturePython)
  FontFile = <path>
  Placement = pos=(5210.35,2846.44,0) rot=(0,0,1;0rad)
  Size = 250
  String = 7
  Tracking = 0
FEATURE [Part::Part2DObjectPython] Circle097  label="Circle098"  # Draft 2D object (typed FeaturePython)
  Area = 0
  FirstAngle = 0
  LastAngle = 0
  MakeFace = false
  Placement = pos=(9400,5300,0) rot=(0,0,1;0rad)
  Radius = 200
FEATURE [Part::Part2DObjectPython] ShapeString147  # Draft 2D object (typed FeaturePython)
  FontFile = <path>
  Placement = pos=(9306.65,5199.61,0) rot=(0,0,1;0rad)
  Size = 250
  String = 9
  Tracking = 0
FEATURE [Part::Part2DObjectPython] Wire691  label="кровля_контур_001"  # Draft 2D object (typed FeaturePython)
  Area = 0
  ChamferSize = 0
  Closed = true
  End = (-1215,8670,0)
  FilletRadius = 0
  Length = 49660
  MakeFace = false
  Placement = pos=(19000,-1120,0) rot=(0,0,1;0rad)
  Points = (4) [(-20215,-90,0),(-5265,-90,0),(-5265,9790,0),(-20215,9790,0)]
  Start = (-1215,-1210,0)
  Subdivisions = 0
FEATURE [Part::FeaturePython] Roof013  label="Крыша объём стропильной системы"  # Arch/BIM 113 (typed FeaturePython)
  Angles = [30,30,30,30]
  Base = -> Wire691
  BorderLength = 49660
  Face = 0
  Flip = false
  Heights = [2852.11,3345.74,2852.11,3345.74]
  HorizontalArea = 1.47706e+08
  IdRel = [-1,-1,-1,-1]
  IfcData = attributes={"GlobalId": {"name": "GlobalId", "type": "IfcGloballyUniqueId", "is_enum": false, "enum_values": []}, "Description": {"... (+613 chars omitted),+1 more (map truncated)
  IfcType = 113
  MoveBase = false
  MoveWithHost = false
  Overhang = [0,0,0,0]
  PerimeterLength = 0
  Placement = pos=(0,0,3180) rot=(0,0,1;0rad)
  PredefinedType = 0
  RidgeLength = 35253.9
  Runs = [5795,5795,5795,5795]
  Thickness = [190,190,190,190]
  VerticalArea = 1.08951e+07
FEATURE [Part::MultiCommon] Common022
  Shapes = -> [Roof013,Structure050]
FEATURE [Part::MultiCommon] Common024
  Shapes = -> [Roof013,Structure051]
FEATURE [Part::MultiCommon] Common026
  Shapes = -> [Roof013,Structure049]
FEATURE [Part::Part2DObjectPython] Line1297  label="Line1298"  # Draft 2D object (typed FeaturePython)
  Area = 0
  ChamferSize = 0
  Closed = true
  End = (4545,4805,0)
  FilletRadius = 0
  Length = 6957.93
  MakeFace = false
  Placement = pos=(-200,-200,0) rot=(0,0,1;0rad)
  Points = (2) [(-175,85,0),(4745,5005,0)]
  Start = (-375,-115,0)
  Subdivisions = 0
FEATURE [Part::Part2DObjectPython] Line1298  label="Line1299"  # Draft 2D object (typed FeaturePython)
  Area = 0
  ChamferSize = 0
  Closed = true
  End = (4545,4805,0)
  FilletRadius = 0
  Length = 6957.93
  MakeFace = false
  Placement = pos=(-200,9550,0) rot=(0,0,1;0rad)
  Points = (2) [(-175,175,0),(4745,-4745,0)]
  Start = (-375,9725,0)
  Subdivisions = 0
FEATURE [Part::Part2DObjectPython] Line1299  label="Line1300"  # Draft 2D object (typed FeaturePython)
  Area = 0
  ChamferSize = 0
  Closed = true
  End = (8705,4805,0)
  FilletRadius = 0
  Length = 6957.93
  MakeFace = false
  Placement = pos=(13450,9550,0) rot=(0,0,1;0rad)
  Points = (2) [(175,175,0),(-4745,-4745,0)]
  Start = (13625,9725,0)
  Subdivisions = 0
FEATURE [Part::Part2DObjectPython] Line1300  label="Line1301"  # Draft 2D object (typed FeaturePython)
  Area = 0
  ChamferSize = 0
  Closed = true
  End = (8705,4805,0)
  FilletRadius = 0
  Length = 6957.93
  MakeFace = false
  Placement = pos=(13450,-200,0) rot=(0,0,1;0rad)
  Points = (2) [(175,85,0),(-4745,5005,0)]
  Start = (13625,-115,0)
  Subdivisions = 0
FEATURE [Part::Part2DObjectPython] Line1301  label="Line1302"  # Draft 2D object (typed FeaturePython)
  Area = 0
  ChamferSize = 0
  Closed = true
  End = (8705,4805,0)
  FilletRadius = 0
  Length = 4160
  MakeFace = false
  Placement = pos=(4675,4675,0) rot=(0,0,1;0rad)
  Points = (2) [(-130,130,0),(4030,130,0)]
  Start = (4545,4805,0)
  Subdivisions = 0
FEATURE [Part::FeaturePython] Wall169  label="Стена"  # Arch/BIM 166 (typed FeaturePython)
  Align = 2
  Area = 2.43528e+07
  Base = -> Line1297
  BlockHeight = 0
  BlockLength = 0
  CountBroken = 0
  CountEntire = 0
  Face = 0
  Height = 3500
  HorizontalArea = 1.04369e+06
  IfcData = attributes={"GlobalId": {"name": "GlobalId", "type": "IfcGloballyUniqueId", "is_enum": false, "enum_values": []}, "Description": {"... (+533 chars omitted),+1 more (map truncated)
  IfcType = 166
  Joint = 0
  Length = 6957.93
  MakeBlocks = false
  MoveBase = false
  MoveWithHost = false
  Normal = (0,0,0)
  OffsetFirst = 0
  OffsetSecond = 0
  PerimeterLength = 14215.9
  Placement = pos=(0,0,3160) rot=(0,0,1;0rad)
  PredefinedType = 0
  VerticalArea = 4.97555e+07
  Width = 150
FEATURE [Part::FeaturePython] Wall170  label="Стена001"  # Arch/BIM 166 (typed FeaturePython)
  Align = 2
  Area = 2.43528e+07
  Base = -> Line1298
  BlockHeight = 0
  BlockLength = 0
  CountBroken = 0
  CountEntire = 0
  Face = 0
  Height = 3500
  HorizontalArea = 1.04369e+06
  IfcData = attributes={"GlobalId": {"name": "GlobalId", "type": "IfcGloballyUniqueId", "is_enum": false, "enum_values": []}, "Description": {"... (+533 chars omitted),+1 more (map truncated)
  IfcType = 166
  Joint = 0
  Length = 6957.93
  MakeBlocks = false
  MoveBase = false
  MoveWithHost = false
  Normal = (0,0,0)
  OffsetFirst = 0
  OffsetSecond = 0
  PerimeterLength = 14215.9
  Placement = pos=(0,0,3160) rot=(0,0,1;0rad)
  PredefinedType = 0
  VerticalArea = 4.97555e+07
  Width = 150
FEATURE [Part::FeaturePython] Wall171  label="Стена002"  # Arch/BIM 166 (typed FeaturePython)
  Align = 2
  Area = 2.43528e+07
  Base = -> Line1299
  BlockHeight = 0
  BlockLength = 0
  CountBroken = 0
  CountEntire = 0
  Face = 0
  Height = 3500
  HorizontalArea = 1.04369e+06
  IfcData = attributes={"GlobalId": {"name": "GlobalId", "type": "IfcGloballyUniqueId", "is_enum": false, "enum_values": []}, "Description": {"... (+533 chars omitted),+1 more (map truncated)
  IfcType = 166
  Joint = 0
  Length = 6957.93
  MakeBlocks = false
  MoveBase = false
  MoveWithHost = false
  Normal = (0,0,0)
  OffsetFirst = 0
  OffsetSecond = 0
  PerimeterLength = 14215.9
  Placement = pos=(0,0,3160) rot=(0,0,1;0rad)
  PredefinedType = 0
  VerticalArea = 4.97555e+07
  Width = 150
FEATURE [Part::FeaturePython] Wall172  label="Стена003"  # Arch/BIM 166 (typed FeaturePython)
  Align = 2
  Area = 2.43528e+07
  Base = -> Line1300
  BlockHeight = 0
  BlockLength = 0
  CountBroken = 0
  CountEntire = 0
  Face = 0
  Height = 3500
  HorizontalArea = 1.04369e+06
  IfcData = attributes={"GlobalId": {"name": "GlobalId", "type": "IfcGloballyUniqueId", "is_enum": false, "enum_values": []}, "Description": {"... (+533 chars omitted),+1 more (map truncated)
  IfcType = 166
  Joint = 0
  Length = 6957.93
  MakeBlocks = false
  MoveBase = false
  MoveWithHost = false
  Normal = (0,0,0)
  OffsetFirst = 0
  OffsetSecond = 0
  PerimeterLength = 14215.9
  Placement = pos=(0,0,3160) rot=(0,0,1;0rad)
  PredefinedType = 0
  VerticalArea = 4.97555e+07
  Width = 150
FEATURE [Part::FeaturePython] Wall173  label="Стена004"  # Arch/BIM 166 (typed FeaturePython)
  Align = 2
  Area = 14560000
  Base = -> Line1301
  BlockHeight = 0
  BlockLength = 0
  CountBroken = 0
  CountEntire = 0
  Face = 0
  Height = 3500
  HorizontalArea = 208000
  IfcData = attributes={"GlobalId": {"name": "GlobalId", "type": "IfcGloballyUniqueId", "is_enum": false, "enum_values": []}, "Description": {"... (+533 chars omitted),+1 more (map truncated)
  IfcType = 166
  Joint = 0
  Length = 4160
  MakeBlocks = false
  MoveBase = false
  MoveWithHost = false
  Normal = (0,0,0)
  OffsetFirst = 0
  OffsetSecond = 0
  PerimeterLength = 8420
  Placement = pos=(0,0,3160) rot=(0,0,1;0rad)
  PredefinedType = 0
  VerticalArea = 2.947e+07
  Width = 50
FEATURE [Part::MultiFuse] Fusion
  Shapes = -> [Wall169,Wall170,Wall171,Wall172,Wall173]
FEATURE [Part::MultiCommon] Common028  label="Диагональные стропила"
  Shapes = -> [Fusion,Roof013]
FEATURE [Part::Part2DObjectPython] Line1302  label="ось фундамента внутр.стены002"  # Draft 2D object (typed FeaturePython)
  ChamferSize = 0
  Closed = true
  End = (9400,4025,0)
  FilletRadius = 0
  Length = 9400
  MakeFace = false
  Placement = pos=(7825,3025,0) rot=(0,0,1;1.5708rad)
  Points = (2) [(1000,7825,0),(1000,-1575,0)]
  Start = (0,4025,0)
  Subdivisions = 0
FEATURE [Part::FeaturePython] Wall174  label="фундамент внутр.стена003"  # Arch/BIM 166 (typed FeaturePython)
  Align = 2
  Area = 4.7e+06
  Base = -> Line1302
  BlockHeight = 0
  BlockLength = 0
  CountBroken = 0
  CountEntire = 0
  Face = 0
  Height = 500
  HorizontalArea = 2.35e+06
  IfcType = 166
  Joint = 0
  Length = 9400
  MakeBlocks = false
  MoveBase = false
  MoveWithHost = false
  Normal = (0,0,-1)
  OffsetFirst = 0
  OffsetSecond = 0
  PerimeterLength = 19300
  Placement = pos=(0,0,-180) rot=(0,0,1;0rad)
  PredefinedType = 0
  VerticalArea = 9.65e+06
  Width = 250
FEATURE [Part::FeaturePython] Wall175  label="фундамент внутр. стена 003"  # Arch/BIM 166 (typed FeaturePython)
  Additions = -> [Wall174]
  Align = 2
  Area = 2.82e+06
  Base = -> Line1302
  BlockHeight = 0
  BlockLength = 0
  CountBroken = 0
  CountEntire = 0
  Face = 0
  Height = 300
  HorizontalArea = 4.7e+06
  IfcType = 166
  Joint = 0
  Length = 9400
  MakeBlocks = false
  MoveBase = false
  MoveWithHost = false
  Normal = (0,0,-1)
  OffsetFirst = 0
  OffsetSecond = 0
  PerimeterLength = 28620
  Placement = pos=(0,0,-680) rot=(0,0,1;0rad)
  PredefinedType = 0
  VerticalArea = 1.559e+07
  Width = 500
FEATURE [Part::FeaturePython] Roof014  label="Крыша объём кобылок"  # Arch/BIM 113 (typed FeaturePython)
  Angles = [28,28,28,28]
  Base = -> Wire691
  BorderLength = 92920
  Face = 0
  Flip = false
  Heights = [425.368,425.368,425.368,425.368]
  HorizontalArea = 37168000
  IdRel = [-1,-1,-1,-1]
  IfcData = attributes={"GlobalId": {"name": "GlobalId", "type": "IfcGloballyUniqueId", "is_enum": false, "enum_values": []}, "Description": {"... (+613 chars omitted),+1 more (map truncated)
  IfcType = 113
  MoveBase = false
  MoveWithHost = false
  Overhang = [0,0,0,0]
  PerimeterLength = 0
  Placement = pos=(0,0,2820) rot=(0,0,1;0rad)
  PredefinedType = 0
  RidgeLength = 4834.77
  Runs = [800,800,800,800]
  Thickness = [100,100,100,100]
  VerticalArea = 1.05238e+07
FEATURE [Part::Part2DObjectPython] Circle098  label="Circle099"  # Draft 2D object (typed FeaturePython)
  Area = 0
  FirstAngle = 0
  LastAngle = 0
  MakeFace = false
  Placement = pos=(11626.7,117.473,0) rot=(0,0,1;0rad)
  Radius = 75
FEATURE [Part::FeaturePython] Array019  # Draft array (typed FeaturePython)
  Angle = 360
  ArrayType = 0
  Axis = (0,0,1)
  Base = -> Circle098
  Center = (0,0,0)
  Fuse = false
  IntervalAxis = (0,0,0)
  IntervalX = (250,0,0)
  IntervalY = (0,250,0)
  IntervalZ = (0,0,1)
  NumberPolar = 1
  NumberX = 2
  NumberY = 2
  NumberZ = 1
  Placement = pos=(-250,0,0) rot=(0,0,1;0rad)
FEATURE [Part::Extrusion] Extrude058  label="Панель индукционная"
  Base = -> Array019
  Dir = (0,0,1)
  DirMode = 2
  FaceMakerClass = Part::FaceMakerBullseye
  LengthFwd = 50
  LengthRev = 0
  Placement = pos=(0,0,800) rot=(0,0,1;0rad)
  Solid = true
  Symmetric = false
FEATURE [Part::MultiFuse] Fusion044  label="Шкаф с плитой 001"
  Shapes = -> [Box3205,Extrude058]
FEATURE [Part::Box] Box3207  label="ПММ_45_002"
  AttacherType = Attacher::AttachEngine3D
  Height = 700
  Length = 450
  Placement = pos=(12440,1345,100) rot=(0,0,1;1.5708rad)
  Width = 500
FEATURE [Part::Box] Box3209  label="ДШ_001"
  AttacherType = Attacher::AttachEngine3D
  Height = 500
  Length = 500
  Placement = pos=(10740,90,450) rot=(0,0,1;1.5708rad)
  Width = 580
FEATURE [Part::Box] Box3211  label="камин топка 700"
  AttacherType = Attacher::AttachEngine3D
  Height = 500
  Length = 800
  Placement = pos=(8750,1885,800) rot=(0,0,1;0rad)
  Width = 500
FEATURE [Part::Box] Box3215  label="Душ 100*80"
  AttacherType = Attacher::AttachEngine3D
  Height = 5
  Length = 900
  Placement = pos=(6950,3825,0) rot=(0,0,1;0rad)
  Width = 1500
FEATURE [Part::Part2DObjectPython] Rectangle3000  # Draft 2D object (typed FeaturePython)
  Area = 0
  ChamferSize = 0
  Columns = 1
  FilletRadius = 0
  Height = 1500
  Length = 900
  MakeFace = false
  Placement = pos=(6950,3825,0) rot=(0,0,1;0rad)
  Rows = 1
FEATURE [Part::Part2DObjectPython] Rectangle3004  # Draft 2D object (typed FeaturePython)
  ChamferSize = 0
  Columns = 1
  FilletRadius = 0
  Height = 600
  Length = 600
  MakeFace = true
  Placement = pos=(8250,-25,0) rot=(0,0,1;0rad)
  Rows = 1
FEATURE [Part::Part2DObjectPython] ShapeString185  # Draft 2D object (typed FeaturePython)
  FontFile = <path>
  Placement = pos=(8472.79,91.4359,0) rot=(0,0,1;0rad)
  Size = 300
  String = *
  Tracking = 0
FEATURE [Part::Part2DObjectPython] ShapeString186  # Draft 2D object (typed FeaturePython)
  FontFile = <path>
  Placement = pos=(10206,195.637,0) rot=(0,0,1;0rad)
  Size = 200
  String = ДШ
  Tracking = 0
FEATURE [Part::FeaturePython] Wall184  label="МЗЛФ нижняя часть"  # Arch/BIM 166 (typed FeaturePython)
  Align = 0
  Area = 24072000
  Base = -> Rectangle2788
  BlockHeight = 0
  BlockLength = 0
  CountBroken = 0
  CountEntire = 0
  Face = 0
  Height = 600
  HorizontalArea = 1.4532e+07
  IfcData = attributes={"GlobalId": {"name": "GlobalId", "type": "IfcGloballyUniqueId", "is_enum": false, "enum_values": []}, "Description": {"... (+533 chars omitted),+1 more (map truncated)
  IfcType = 166
  Joint = 0
  Length = 40120
  MakeBlocks = false
  MoveBase = false
  MoveWithHost = false
  Normal = (0,0,0)
  OffsetFirst = 0
  OffsetSecond = 0
  PerimeterLength = 42920
  Placement = pos=(0,0,-980) rot=(0,0,1;0rad)
  PredefinedType = 0
  VerticalArea = 49824000
  Width = 350
FEATURE [Part::Part2DObjectPython] Rectangle3023  # Draft 2D object (typed FeaturePython)
  ChamferSize = 0
  Columns = 1
  FilletRadius = 0
  Height = 300
  Length = 500
  MakeFace = true
  Placement = pos=(11190,4065,0) rot=(0,0,1;0rad)
  Rows = 1
FEATURE [Part::Part2DObjectPython] Rectangle3024  # Draft 2D object (typed FeaturePython)
  ChamferSize = 0
  Columns = 1
  FilletRadius = 0
  Height = 300
  Length = 500
  MakeFace = true
  Placement = pos=(11190,2965,0) rot=(0,0,1;0rad)
  Rows = 1
FEATURE [Part::Part2DObjectPython] Rectangle3026  # Draft 2D object (typed FeaturePython)
  Area = 0
  ChamferSize = 0
  Columns = 1
  FilletRadius = 0
  Height = 490
  Length = 450
  MakeFace = false
  Placement = pos=(12440,1330,0) rot=(0,0,1;1.5708rad)
  Rows = 1
FEATURE [Part::Part2DObjectPython] Line1316  # Draft 2D object (typed FeaturePython)
  ChamferSize = 0
  Closed = true
  End = (3490,2335,0)
  FilletRadius = 0
  Length = 5970
  MakeFace = false
  Placement = pos=(4400,5635,0) rot=(0,0,-1;1.5708rad)
  Points = (2) [(3300,5060,0),(3300,-910,0)]
  Start = (9460,2335,0)
  Subdivisions = 0
FEATURE [Part::Part2DObjectPython] Rectangle3032  # Draft 2D object (typed FeaturePython)
  ChamferSize = 0
  Columns = 1
  FilletRadius = 75
  Height = 1000
  Length = 500
  MakeFace = true
  Placement = pos=(10350,5100,0) rot=(0,0,1;0rad)
  Rows = 1
FEATURE [Part::Part2DObjectPython] Line1317  # Draft 2D object (typed FeaturePython)
  Area = 0
  ChamferSize = 0
  Closed = false
  End = (10128.9,732.87,0)
  FilletRadius = 0
  Length = 600
  MakeFace = true
  Placement = pos=(9550,575,0) rot=(0,0,1;0rad)
  Points = (2) [(0,0,0),(578.858,157.87,0)]
  Start = (9550,575,0)
  Subdivisions = 0
FEATURE [Part::Part2DObjectPython] Rectangle3034  label="Унитаз Geberit Smyle 54х35 003"  # Draft 2D object (typed FeaturePython)
  ChamferSize = 0
  Columns = 1
  FilletRadius = 0
  Height = 350
  Length = 400
  MakeFace = true
  Placement = pos=(5283.55,3931.07,0) rot=(0,0,1;0.785398rad)
  Rows = 1
FEATURE [Part::Part2DObjectPython] Rectangle3046  label="Шкаф 60 015"  # Draft 2D object (typed FeaturePython)
  Area = 498000
  ChamferSize = 0
  Columns = 1
  FilletRadius = 0
  Height = 1245
  Length = 400
  MakeFace = true
  Placement = pos=(-30,6240,0) rot=(0,0,1;0rad)
  Rows = 1
FEATURE [Part::Part2DObjectPython] Line1323  # Draft 2D object (typed FeaturePython)
  ChamferSize = 0
  Closed = true
  End = (8700,1875,0)
  FilletRadius = 0
  Length = 420
  MakeFace = false
  Placement = pos=(10280,1880,0) rot=(0,0,1;0rad)
  Points = (2) [(-1580,415,0),(-1580,-5,0)]
  Start = (8700,2295,0)
  Subdivisions = 0
FEATURE [Part::FeaturePython] Wall187  label="перегородка 044"  # Arch/BIM 166 (typed FeaturePython)
  Align = 2
  Area = 1176000
  Base = -> Line1323
  BlockHeight = 250
  BlockLength = 0
  CountBroken = 0
  CountEntire = 0
  Face = 0
  Height = 2800
  HorizontalArea = 33600
  IfcType = 166
  Joint = 0
  Length = 420
  MakeBlocks = false
  MoveBase = false
  MoveWithHost = false
  Normal = (0,0,0)
  OffsetFirst = 0
  OffsetSecond = 300
  PerimeterLength = 1000
  PredefinedType = 0
  VerticalArea = 2800000
  Width = 80
FEATURE [Part::Part2DObjectPython] Line1324  # Draft 2D object (typed FeaturePython)
  ChamferSize = 0
  Closed = true
  End = (7350,-45,0)
  FilletRadius = 0
  Length = 2340
  MakeFace = false
  Placement = pos=(9435,1900,0) rot=(0,0,1;0rad)
  Points = (2) [(-2085,395,0),(-2085,-1945,0)]
  Start = (7350,2295,0)
  Subdivisions = 0
FEATURE [Part::FeaturePython] Wall188  label="перегородка 045"  # Arch/BIM 166 (typed FeaturePython)
  Align = 2
  Area = 6552000
  Base = -> Line1324
  BlockHeight = 250
  BlockLength = 0
  CountBroken = 0
  CountEntire = 0
  Face = 0
  Height = 2800
  HorizontalArea = 187200
  IfcType = 166
  Joint = 0
  Length = 2340
  MakeBlocks = false
  MoveBase = false
  MoveWithHost = false
  Normal = (0,0,0)
  OffsetFirst = 0
  OffsetSecond = 300
  PerimeterLength = 4840
  PredefinedType = 0
  VerticalArea = 13552000
  Width = 80
FEATURE [Part::Part2DObjectPython] Line1326  # Draft 2D object (typed FeaturePython)
  Area = 0
  ChamferSize = 0
  Closed = true
  End = (14600,5100,0)
  FilletRadius = 0
  Length = 1100
  MakeFace = true
  Placement = pos=(14600,6200,0) rot=(0,0,1;0rad)
  Points = (2) [(0,0,0),(0,-1100,0)]
  Start = (14600,6200,0)
  Subdivisions = 0
FEATURE [Part::Part2DObjectPython] Line1327  # Draft 2D object (typed FeaturePython)
  Area = 0
  ChamferSize = 0
  Closed = false
  End = (14600,6200,0)
  FilletRadius = 0
  Length = 282.843
  MakeFace = true
  Placement = pos=(14400,6400,0) rot=(0,0,1;0rad)
  Points = (2) [(0,0,0),(200,-200,0)]
  Start = (14400,6400,0)
  Subdivisions = 0
FEATURE [Part::Part2DObjectPython] Line1328  # Draft 2D object (typed FeaturePython)
  Area = 0
  ChamferSize = 0
  Closed = false
  End = (14800,6400,0)
  FilletRadius = 0
  Length = 282.843
  MakeFace = true
  Placement = pos=(14600,6200,0) rot=(0,0,1;0rad)
  Points = (2) [(0,0,0),(200,200,0)]
  Start = (14600,6200,0)
  Subdivisions = 0
FEATURE [Part::Part2DObjectPython] Line1329  # Draft 2D object (typed FeaturePython)
  Area = 0
  ChamferSize = 0
  Closed = false
  End = (14400,5500,0)
  FilletRadius = 0
  Length = 447.214
  MakeFace = true
  Placement = pos=(14600,5100,0) rot=(0,0,1;0rad)
  Points = (2) [(0,0,0),(-200,400,0)]
  Start = (14600,5100,0)
  Subdivisions = 0
FEATURE [Part::Part2DObjectPython] Line1330  # Draft 2D object (typed FeaturePython)
  Area = 0
  ChamferSize = 0
  Closed = false
  End = (14800,5500,0)
  FilletRadius = 0
  Length = 447.214
  MakeFace = true
  Placement = pos=(14600,5100,0) rot=(0,0,1;0rad)
  Points = (2) [(0,0,0),(200,400,0)]
  Start = (14600,5100,0)
  Subdivisions = 0
FEATURE [Part::Part2DObjectPython] ShapeString189  # Draft 2D object (typed FeaturePython)
  FontFile = <path>
  Placement = pos=(14506.7,4699.61,0) rot=(0,0,1;0rad)
  Size = 250
  String = С
  Tracking = 0
FEATURE [Part::Part2DObjectPython] ShapeString191  # Draft 2D object (typed FeaturePython)
  FontFile = <path>
  Placement = pos=(14406.7,6499.61,0) rot=(0,0,1;0rad)
  Size = 250
  String = Юг
  Tracking = 0
FEATURE [App::FeaturePython] Dimension010  # Draft dimension (typed FeaturePython)
  Diameter = false
  Dimline = (4870,9000,0)
  Direction = (0,0,0)
  Distance = 2020
  End = (6890,9506.46,0)
  Normal = (0,0,1)
  Start = (4870,9506.46,0)
FEATURE [Part::Part2DObjectPython] Line1340  # Draft 2D object (typed FeaturePython)
  Area = 0
  ChamferSize = 0
  Closed = true
  End = (12570,-410,0)
  FilletRadius = 0
  Length = 13000
  MakeFace = false
  Placement = pos=(-400,-505,0) rot=(0,0,1;0rad)
  Points = (2) [(-30,95,0),(12970,95,0)]
  Start = (-430,-410,0)
  Subdivisions = 0
FEATURE [Part::Part2DObjectPython] Rectangle3074  label="Тёплый контур"  # Draft 2D object (typed FeaturePython)
  Area = 9.44758e+07
  ChamferSize = 0
  Columns = 1
  FilletRadius = 0
  Height = 7510
  Length = 12580
  MakeFace = true
  Placement = pos=(-30,-25,0) rot=(0,0,1;0rad)
  Rows = 1
FEATURE [Part::Part2DObjectPython] Rectangle003  label="СУ"  # Draft 2D object (typed FeaturePython)
  Area = 6954000
  ChamferSize = 0
  Columns = 1
  FilletRadius = 0
  Height = 3660
  Length = 1900
  MakeFace = true
  Placement = pos=(4930,3825,0) rot=(0,0,1;0rad)
  Rows = 1
FEATURE [Part::Part2DObjectPython] Rectangle005  label="Прихожая"  # Draft 2D object (typed FeaturePython)
  Area = 7392000
  ChamferSize = 0
  Columns = 1
  FilletRadius = 0
  Height = 2310
  Length = 3200
  MakeFace = true
  Placement = pos=(4100,-25,0) rot=(0,0,1;0rad)
  Rows = 1
FEATURE [Part::Part2DObjectPython] Rectangle006  label="Душ"  # Draft 2D object (typed FeaturePython)
  Area = 1.35e+06
  ChamferSize = 0
  Columns = 1
  FilletRadius = 0
  Height = 1500
  Length = 900
  MakeFace = true
  Placement = pos=(6950,3825,0) rot=(0,0,1;0rad)
  Rows = 1
FEATURE [Part::Part2DObjectPython] Rectangle008  label="Спальня 1 этаж"  # Draft 2D object (typed FeaturePython)
  Area = 1.7751e+07
  ChamferSize = 0
  Columns = 1
  FilletRadius = 0
  Height = 3660
  Length = 4850
  MakeFace = true
  Placement = pos=(-30,3825,0) rot=(0,0,1;0rad)
  Rows = 1
FEATURE [Part::Part2DObjectPython] Rectangle009  label="Кухня-столовая"  # Draft 2D object (typed FeaturePython)
  Area = 10680000
  ChamferSize = 0
  Columns = 1
  FilletRadius = 0
  Height = 3560
  Length = 3000
  MakeFace = true
  Placement = pos=(9550,-25,0) rot=(0,0,1;0rad)
  Rows = 1
FEATURE [Part::Part2DObjectPython] Rectangle011  label="Коридор"  # Draft 2D object (typed FeaturePython)
  Area = 5.658e+06
  ChamferSize = 0
  Columns = 1
  FilletRadius = 0
  Height = 1150
  Length = 4920
  MakeFace = true
  Placement = pos=(3500,2385,0) rot=(0,0,1;0rad)
  Rows = 1
FEATURE [Part::Part2DObjectPython] Line1341  # Draft 2D object (typed FeaturePython)
  Area = 0
  ChamferSize = 0
  Closed = true
  End = (-430,-30,0)
  FilletRadius = 0
  Length = 7900
  MakeFace = false
  Placement = pos=(-345,-380,0) rot=(0,0,1;0rad)
  Points = (2) [(-85,8250,0),(-85,350,0)]
  Start = (-430,7870,0)
  Subdivisions = 0
FEATURE [Part::Part2DObjectPython] Line1342  # Draft 2D object (typed FeaturePython)
  Area = 0
  ChamferSize = 0
  Closed = true
  End = (12950,7490,0)
  FilletRadius = 0
  Length = 7900
  MakeFace = false
  Placement = pos=(-4425,-450,0) rot=(0,0,1;0rad)
  Points = (2) [(17375,40,0),(17375,7940,0)]
  Start = (12950,-410,0)
  Subdivisions = 0
FEATURE [Part::Part2DObjectPython] Line1343  # Draft 2D object (typed FeaturePython)
  Area = 0
  ChamferSize = 0
  Closed = true
  End = (12950,-30,0)
  FilletRadius = 0
  Length = 7900
  MakeFace = false
  Placement = pos=(-4425,-760,0) rot=(0,0,1;0rad)
  Points = (2) [(17375,8630,0),(17375,730,0)]
  Start = (12950,7870,0)
  Subdivisions = 0
FEATURE [Part::Part2DObjectPython] Line1347  # Draft 2D object (typed FeaturePython)
  Area = 0
  ChamferSize = 0
  Closed = true
  End = (-430,7490,0)
  FilletRadius = 0
  Length = 7900
  MakeFace = false
  Placement = pos=(-345,-890,0) rot=(0,0,1;0rad)
  Points = (2) [(-85,480,0),(-85,8380,0)]
  Start = (-430,-410,0)
  Subdivisions = 0
FEATURE [Part::FeaturePython] Wall206  label="Стена021"  # Arch/BIM 166 (typed FeaturePython)
  Align = 0
  Area = 1824900
  Base = -> Line1343
  BlockHeight = 231
  BlockLength = 255
  CountBroken = 1
  CountEntire = 30
  Face = 0
  Height = 231
  HorizontalArea = 0
  IfcData = attributes={"GlobalId": {"name": "GlobalId", "type": "IfcGloballyUniqueId", "is_enum": false, "enum_values": []}, "Description": {"... (+533 chars omitted),+1 more (map truncated)
  IfcType = 166
  Joint = 0
  Length = 7900
  MakeBlocks = true
  MoveBase = false
  MoveWithHost = false
  Normal = (0,0,0)
  OffsetFirst = 0
  OffsetSecond = 0
  PerimeterLength = 0
  Placement = pos=(0,0,31) rot=(0,0,1;0rad)
  PredefinedType = 0
  VerticalArea = 0
  Width = 380
FEATURE [Part::FeaturePython] Wall207  label="Стена022"  # Arch/BIM 166 (typed FeaturePython)
  Align = 1
  Area = 1824900
  Base = -> Line1342
  BlockHeight = 231
  BlockLength = 255
  CountBroken = 1
  CountEntire = 30
  Face = 0
  Height = 231
  HorizontalArea = 0
  IfcData = attributes={"GlobalId": {"name": "GlobalId", "type": "IfcGloballyUniqueId", "is_enum": false, "enum_values": []}, "Description": {"... (+533 chars omitted),+1 more (map truncated)
  IfcType = 166
  Joint = 0
  Length = 7900
  MakeBlocks = true
  MoveBase = false
  MoveWithHost = false
  Normal = (0,0,0)
  OffsetFirst = 0
  OffsetSecond = 0
  PerimeterLength = 0
  Placement = pos=(0,0,-200) rot=(0,0,1;0rad)
  PredefinedType = 0
  VerticalArea = 0
  Width = 380
FEATURE [Part::FeaturePython] Wall209  label="Стена024"  # Arch/BIM 166 (typed FeaturePython)
  Align = 1
  Area = 3003000
  Base = -> Line1340
  BlockHeight = 231
  BlockLength = 255
  CountBroken = 3
  CountEntire = 44
  Face = 0
  Height = 231
  HorizontalArea = 0
  IfcData = attributes={"GlobalId": {"name": "GlobalId", "type": "IfcGloballyUniqueId", "is_enum": false, "enum_values": []}, "Description": {"... (+533 chars omitted),+1 more (map truncated)
  IfcType = 166
  Joint = 0
  Length = 13000
  MakeBlocks = true
  MoveBase = false
  MoveWithHost = false
  Normal = (0,0,0)
  OffsetFirst = 0
  OffsetSecond = 0
  PerimeterLength = 0
  Placement = pos=(0,0,-200) rot=(0,0,1;0rad)
  PredefinedType = 0
  Subtractions = -> [Structure019]
  VerticalArea = 0
  Width = 380
FEATURE [Part::FeaturePython] Wall211  label="Стена026"  # Arch/BIM 166 (typed FeaturePython)
  Align = 0
  Area = 1824900
  Base = -> Line1347
  BlockHeight = 231
  BlockLength = 255
  CountBroken = 1
  CountEntire = 30
  Face = 0
  Height = 231
  HorizontalArea = 0
  IfcData = attributes={"GlobalId": {"name": "GlobalId", "type": "IfcGloballyUniqueId", "is_enum": false, "enum_values": []}, "Description": {"... (+533 chars omitted),+1 more (map truncated)
  IfcType = 166
  Joint = 0
  Length = 7900
  MakeBlocks = true
  MoveBase = false
  MoveWithHost = false
  Normal = (0,0,0)
  OffsetFirst = 0
  OffsetSecond = 0
  PerimeterLength = 0
  Placement = pos=(0,0,31) rot=(0,0,1;0rad)
  PredefinedType = 0
  VerticalArea = 0
  Width = 380
FEATURE [Part::FeaturePython] Wall213  label="Стена028"  # Arch/BIM 166 (typed FeaturePython)
  Align = 1
  Area = 1824900
  Base = -> Line1341
  BlockHeight = 231
  BlockLength = 255
  CountBroken = 1
  CountEntire = 30
  Face = 0
  Height = 231
  HorizontalArea = 0
  IfcData = attributes={"GlobalId": {"name": "GlobalId", "type": "IfcGloballyUniqueId", "is_enum": false, "enum_values": []}, "Description": {"... (+533 chars omitted),+1 more (map truncated)
  IfcType = 166
  Joint = 0
  Length = 7900
  MakeBlocks = true
  MoveBase = false
  MoveWithHost = false
  Normal = (0,0,0)
  OffsetFirst = 0
  OffsetSecond = 0
  PerimeterLength = 0
  Placement = pos=(0,0,-200) rot=(0,0,1;0rad)
  PredefinedType = 0
  VerticalArea = 0
  Width = 380
FEATURE [Part::Part2DObjectPython] Line1349  # Draft 2D object (typed FeaturePython)
  Area = 0
  ChamferSize = 0
  Closed = true
  End = (-50,7870,0)
  FilletRadius = 0
  Length = 13000
  MakeFace = false
  Placement = pos=(-4925,-320,0) rot=(0,0,1;0rad)
  Points = (2) [(17875,8190,0),(4875,8190,0)]
  Start = (12950,7870,0)
  Subdivisions = 0
FEATURE [Part::Part2DObjectPython] Line1350  # Draft 2D object (typed FeaturePython)
  Area = 0
  ChamferSize = 0
  Closed = true
  End = (12570,7870,0)
  FilletRadius = 0
  Length = 13000
  MakeFace = false
  Placement = pos=(-345,-320,0) rot=(0,0,1;0rad)
  Points = (2) [(-85,8190,0),(12915,8190,0)]
  Start = (-430,7870,0)
  Subdivisions = 0
FEATURE [Part::Part2DObjectPython] Line1351  # Draft 2D object (typed FeaturePython)
  Area = 0
  ChamferSize = 0
  Closed = true
  End = (-50,-410,0)
  FilletRadius = 0
  Length = 13000
  MakeFace = false
  Placement = pos=(-4925,-450,0) rot=(0,0,1;0rad)
  Points = (2) [(17875,40,0),(4875,40,0)]
  Start = (12950,-410,0)
  Subdivisions = 0
FEATURE [Part::FeaturePython] Wall212  label="Стена027"  # Arch/BIM 166 (typed FeaturePython)
  Align = 0
  Area = 3003000
  Base = -> Line1351
  BlockHeight = 231
  BlockLength = 255
  CountBroken = 3
  CountEntire = 45
  Face = 0
  Height = 231
  HorizontalArea = 0
  IfcData = attributes={"GlobalId": {"name": "GlobalId", "type": "IfcGloballyUniqueId", "is_enum": false, "enum_values": []}, "Description": {"... (+533 chars omitted),+1 more (map truncated)
  IfcType = 166
  Joint = 0
  Length = 13000
  MakeBlocks = true
  MoveBase = false
  MoveWithHost = false
  Normal = (0,0,0)
  OffsetFirst = 0
  OffsetSecond = 0
  PerimeterLength = 0
  Placement = pos=(0,0,31) rot=(0,0,1;0rad)
  PredefinedType = 0
  Subtractions = -> [Structure019]
  VerticalArea = 0
  Width = 380
FEATURE [Part::Part2DObjectPython] Rectangle016  label="Контур_по_блоку_ЛСР_38_шаг255"  # Draft 2D object (typed FeaturePython)
  Area = 0
  ChamferSize = 0
  Columns = 1
  FilletRadius = 0
  Height = 7550
  Length = 12620
  MakeFace = false
  Placement = pos=(-50,-45,0) rot=(0,0,1;0rad)
  Rows = 1
FEATURE [Part::Part2DObjectPython] Rectangle3075  label="ОК-196-002"  # Draft 2D object (typed FeaturePython)
  ChamferSize = 0
  Columns = 1
  FilletRadius = 0
  Height = 410
  Length = 1960
  MakeFace = true
  Placement = pos=(12550,3280,0) rot=(0,0,-1;1.5708rad)
  Rows = 1
FEATURE [Part::FeaturePython] Structure304  label="Проём-ОК-196-002"  # Arch/BIM 52 (typed FeaturePython)
  Base = -> Rectangle3075
  FaceMaker = 0
  Height = 1386
  HorizontalArea = 803600
  IfcData = complex_attributes={"OwnerHistory": {}, "IsNestedBy": {}, "IsDecomposedBy": {}, "IsDefinedBy": {}, "ObjectPlacement": {}, "Representation":... (+4 chars omitted)
  IfcType = 52
  Length = 0
  MoveBase = false
  MoveWithHost = false
  Nodes = (2) [(4745,-225,0),(4745,-225,1350)]
  NodesOffset = 0
  Normal = (0,0,0)
  PerimeterLength = 4740
  Placement = pos=(0,0,1186) rot=(0,0,1;0rad)
  VerticalArea = 6569640
  Width = 100
FEATURE [Part::Part2DObjectPython] Rectangle3077  label="ОК-92-001"  # Draft 2D object (typed FeaturePython)
  ChamferSize = 0
  Columns = 1
  FilletRadius = 0
  Height = 410
  Length = 920
  MakeFace = true
  Placement = pos=(12550,4970,0) rot=(0,0,-1;1.5708rad)
  Rows = 1
FEATURE [Part::FeaturePython] Structure306  label="Проём-ОК-92-001"  # Arch/BIM 52 (typed FeaturePython)
  Base = -> Rectangle3077
  FaceMaker = 0
  Height = 1386
  HorizontalArea = 377200
  IfcData = complex_attributes={"OwnerHistory": {}, "IsNestedBy": {}, "IsDecomposedBy": {}, "IsDefinedBy": {}, "ObjectPlacement": {}, "Representation":... (+4 chars omitted)
  IfcType = 52
  Length = 0
  MoveBase = false
  MoveWithHost = false
  Nodes = (2) [(1035,250,0),(1035,250,600)]
  NodesOffset = 0
  Normal = (0,0,0)
  PerimeterLength = 2660
  Placement = pos=(0,0,1186) rot=(0,0,1;0rad)
  VerticalArea = 3.68676e+06
  Width = 100
FEATURE [Part::Part2DObjectPython] Rectangle3079  label="ОК-196-001"  # Draft 2D object (typed FeaturePython)
  ChamferSize = 0
  Columns = 1
  FilletRadius = 0
  Height = 410
  Length = 1960
  MakeFace = true
  Placement = pos=(8595,7485,0) rot=(0,0,1;0rad)
  Rows = 1
FEATURE [Part::FeaturePython] Structure308  label="Проём-ОК-196-001"  # Arch/BIM 52 (typed FeaturePython)
  Base = -> Rectangle3079
  FaceMaker = 0
  Height = 2772
  HorizontalArea = 803600
  IfcData = complex_attributes={"OwnerHistory": {}, "IsNestedBy": {}, "IsDecomposedBy": {}, "IsDefinedBy": {}, "ObjectPlacement": {}, "Representation":... (+4 chars omitted)
  IfcType = 52
  Length = 0
  MoveBase = false
  MoveWithHost = false
  Nodes = (2) [(1035,250,0),(1035,250,600)]
  NodesOffset = 0
  Normal = (0,0,0)
  PerimeterLength = 4740
  Placement = pos=(0,0,-200) rot=(0,0,1;0rad)
  VerticalArea = 13139280
  Width = 100
FEATURE [Part::FeaturePython] Wall208  label="Стена023"  # Arch/BIM 166 (typed FeaturePython)
  Align = 1
  Area = 3003000
  Base = -> Line1349
  BlockHeight = 231
  BlockLength = 255
  CountBroken = 3
  CountEntire = 41
  Face = 0
  Height = 231
  HorizontalArea = 0
  IfcData = attributes={"GlobalId": {"name": "GlobalId", "type": "IfcGloballyUniqueId", "is_enum": false, "enum_values": []}, "Description": {"... (+533 chars omitted),+1 more (map truncated)
  IfcType = 166
  Joint = 0
  Length = 13000
  MakeBlocks = true
  MoveBase = false
  MoveWithHost = false
  Normal = (0,0,0)
  OffsetFirst = 0
  OffsetSecond = 0
  PerimeterLength = 0
  Placement = pos=(0,0,-200) rot=(0,0,1;0rad)
  PredefinedType = 0
  Subtractions = -> [Structure308]
  VerticalArea = 0
  Width = 380
FEATURE [Part::FeaturePython] Wall210  label="Стена025"  # Arch/BIM 166 (typed FeaturePython)
  Align = 0
  Area = 3003000
  Base = -> Line1350
  BlockHeight = 231
  BlockLength = 255
  CountBroken = 3
  CountEntire = 41
  Face = 0
  Height = 231
  HorizontalArea = 0
  IfcData = attributes={"GlobalId": {"name": "GlobalId", "type": "IfcGloballyUniqueId", "is_enum": false, "enum_values": []}, "Description": {"... (+533 chars omitted),+1 more (map truncated)
  IfcType = 166
  Joint = 0
  Length = 13000
  MakeBlocks = true
  MoveBase = false
  MoveWithHost = false
  Normal = (0,0,0)
  OffsetFirst = 0
  OffsetSecond = 0
  PerimeterLength = 0
  Placement = pos=(0,0,31) rot=(0,0,1;0rad)
  PredefinedType = 0
  Subtractions = -> [Structure308]
  VerticalArea = 0
  Width = 380
FEATURE [App::GeometryPython] BuildingPart072  label="ряд 2"  # Arch/BIM 52 (typed FeaturePython)
  Area = 9655800
  Group = -> [Wall212,Wall210,Wall211,Wall206]
  Height = 0
  HeightPropagate = true
  IfcData = attributes={"GlobalId": {"name": "GlobalId", "type": "IfcGloballyUniqueId", "is_enum": false, "enum_values": []}, "Description": {"... (+484 chars omitted),+1 more (map truncated)
  IfcType = 52
  LevelOffset = 0
FEATURE [Part::Part2DObjectPython] Rectangle3084  label="ОК-92-002"  # Draft 2D object (typed FeaturePython)
  ChamferSize = 0
  Columns = 1
  FilletRadius = 0
  Height = 410
  Length = 920
  MakeFace = true
  Placement = pos=(5085,7485,0) rot=(0,0,1;0rad)
  Rows = 1
FEATURE [Part::FeaturePython] Structure313  label="Проём-ОК-92-002"  # Arch/BIM 52 (typed FeaturePython)
  Base = -> Rectangle3084
  FaceMaker = 0
  Height = 1617
  HorizontalArea = 377200
  IfcData = complex_attributes={"OwnerHistory": {}, "IsNestedBy": {}, "IsDecomposedBy": {}, "IsDefinedBy": {}, "ObjectPlacement": {}, "Representation":... (+4 chars omitted)
  IfcType = 52
  Length = 0
  MoveBase = false
  MoveWithHost = false
  Nodes = (2) [(1035,250,0),(1035,250,600)]
  NodesOffset = 0
  Normal = (0,0,0)
  PerimeterLength = 2660
  Placement = pos=(0,0,955) rot=(0,0,1;0rad)
  VerticalArea = 4301220
  Width = 100
FEATURE [Part::Part2DObjectPython] Rectangle3086  label="ОК-196-003"  # Draft 2D object (typed FeaturePython)
  ChamferSize = 0
  Columns = 1
  FilletRadius = 0
  Height = 410
  Length = 1960
  MakeFace = true
  Placement = pos=(1965,7485,0) rot=(0,0,1;0rad)
  Rows = 1
FEATURE [Part::FeaturePython] Structure315  label="Проём-ОК-196-003"  # Arch/BIM 52 (typed FeaturePython)
  Base = -> Rectangle3086
  FaceMaker = 0
  Height = 1617
  HorizontalArea = 803600
  IfcData = complex_attributes={"OwnerHistory": {}, "IsNestedBy": {}, "IsDecomposedBy": {}, "IsDefinedBy": {}, "ObjectPlacement": {}, "Representation":... (+4 chars omitted)
  IfcType = 52
  Length = 0
  MoveBase = false
  MoveWithHost = false
  Nodes = (2) [(1035,250,0),(1035,250,600)]
  NodesOffset = 0
  Normal = (0,0,0)
  PerimeterLength = 4740
  Placement = pos=(0,0,955) rot=(0,0,1;0rad)
  VerticalArea = 7664580
  Width = 100
FEATURE [Part::Part2DObjectPython] Rectangle3095  label="ПР352-001"  # Draft 2D object (typed FeaturePython)
  ChamferSize = 0
  Columns = 1
  FilletRadius = 0
  Height = 3520
  Length = 290
  MakeFace = true
  Placement = pos=(11920,3535,0) rot=(0,0,1;1.5708rad)
  Rows = 1
FEATURE [Part::FeaturePython] Structure317  label="Проём-ПР352"  # Arch/BIM 52 (typed FeaturePython)
  Base = -> Rectangle3095
  FaceMaker = 0
  Height = 2700
  HorizontalArea = 1.0208e+06
  IfcData = complex_attributes={"OwnerHistory": {}, "IsNestedBy": {}, "IsDecomposedBy": {}, "IsDefinedBy": {}, "ObjectPlacement": {}, "Representation":... (+4 chars omitted)
  IfcType = 52
  Length = 0
  MoveBase = false
  MoveWithHost = false
  Nodes = (2) [(8200,3800,0),(8200,3800,2250)]
  NodesOffset = 0
  Normal = (0,0,0)
  PerimeterLength = 7620
  Placement = pos=(0,0,-200) rot=(0,0,1;0rad)
  VerticalArea = 20574000
  Width = 100
FEATURE [Part::Part2DObjectPython] Rectangle3104  # Draft 2D object (typed FeaturePython)
  ChamferSize = 0
  Columns = 1
  FilletRadius = 0
  Height = 1060
  Length = 310
  MakeFace = true
  Placement = pos=(12240,3825,0) rot=(0,0,1;0rad)
  Rows = 1
FEATURE [App::FeaturePython] Dimension002  # Draft dimension (typed FeaturePython)
  Diameter = false
  Dimline = (6500,-1800,0)
  Direction = (0,0,0)
  Distance = 13640
  End = (13080,-555,0)
  Normal = (0,0,1)
  Start = (-560,-555,0)
FEATURE [App::FeaturePython] Dimension011  # Draft dimension (typed FeaturePython)
  Diameter = false
  Dimline = (4150,-1500,0)
  Direction = (0,0,0)
  Distance = 3300
  End = (7350,-2107.94,0)
  Normal = (0,0,1)
  Start = (4050,-2107.94,0)
FEATURE [App::FeaturePython] Dimension012  # Draft dimension (typed FeaturePython)
  Diameter = false
  Dimline = (9500,-1500,0)
  Direction = (0,0,0)
  Distance = 2150
  End = (9500,-2107.94,0)
  Normal = (0,0,1)
  Start = (7350,-2107.94,0)
FEATURE [App::FeaturePython] Dimension013  # Draft dimension (typed FeaturePython)
  Diameter = false
  Dimline = (1700,-1500,0)
  Direction = (0,0,0)
  Distance = 4290
  End = (4050,-2107.94,0)
  Normal = (0,0,1)
  Start = (-240,-2107.94,0)
FEATURE [App::FeaturePython] Dimension014  # Draft dimension (typed FeaturePython)
  Diameter = false
  Dimline = (7910,9000,0)
  Direction = (0,0,0)
  Distance = 4850
  End = (12760,9506.46,0)
  Normal = (0,0,1)
  Start = (7910,9506.46,0)
FEATURE [App::FeaturePython] Dimension015  # Draft dimension (typed FeaturePython)
  Diameter = false
  Dimline = (-1200,2335,0)
  Direction = (0,0,0)
  Distance = 2570
  End = (-1836.7,2335,0)
  Normal = (0,0,1)
  Start = (-1836.7,-235,0)
FEATURE [App::FeaturePython] Dimension016  # Draft dimension (typed FeaturePython)
  Diameter = false
  Dimline = (3550,-1350,0)
  Direction = (0,0,0)
  Distance = 600
  End = (4050,-2107.94,0)
  Normal = (0,0,1)
  Start = (3450,-2107.94,0)
FEATURE [App::FeaturePython] Dimension018  # Draft dimension (typed FeaturePython)
  Diameter = false
  Dimline = (8700,4200,0)
  Direction = (0,0,0)
  Distance = 290
  End = (8420,3825,0)
  Normal = (0,0,1)
  Start = (8420,3535,0)
FEATURE [Part::Part2DObjectPython] Wire749  # Draft 2D object (typed FeaturePython)
  Area = 308000
  ChamferSize = 0
  Closed = true
  End = (4925,-410,0)
  FilletRadius = 0
  Length = 2340
  MakeFace = true
  Placement = pos=(27002,5810,0) rot=(0,0,1;0rad)
  Points = (4) [(-22077,-5820,0),(-21307,-5820,0),(-21307,-6220,0),(-22077,-6220,0)]
  Start = (4925,-10,0)
  Subdivisions = 0
FEATURE [Part::Part2DObjectPython] Wire752  # Draft 2D object (typed FeaturePython)
  Area = 428700
  ChamferSize = 0
  Closed = true
  End = (4009,7870,0)
  FilletRadius = 0
  Length = 3132
  MakeFace = true
  Placement = pos=(5410,7880,0) rot=(0,0,1;3.14159rad)
  Points = (8) [(365,10,0),(365,410,0),(480,410,0),(480,540,0),(590,540,0),(590,410,0),(1401,410,0),(1401,10,0)]
  Start = (5045,7870,0)
  Subdivisions = 0
FEATURE [Sketcher::SketchObject] Sketch301  label="Профиль ПНО 150-001"
  FullyConstrained = true
  Placement = pos=(0,0,0) rot=(1,0,0;1.5708rad)
  sketch-geometry (23):
    g0: LineSegment StartX=0 StartY=0 StartZ=0 EndX=1490 EndY=0 EndZ=0
    g1: LineSegment StartX=1490 StartY=0 StartZ=0 EndX=1490 EndY=160 EndZ=0
    g2: LineSegment StartX=1490 StartY=160 StartZ=0 EndX=0 EndY=160 EndZ=0
    g3: LineSegment StartX=0 StartY=160 StartZ=0 EndX=0 EndY=0 EndZ=0
    g4: Circle CenterX=115 CenterY=80 CenterZ=0 NormalX=0 NormalY=0 NormalZ=1 AngleXU=0 Radius=50
    g5: Circle CenterX=255 CenterY=80 CenterZ=0 NormalX=0 NormalY=0 NormalZ=1 AngleXU=0 Radius=50
    g6: LineSegment StartX=115 StartY=80 StartZ=0 EndX=255 EndY=80 EndZ=0
    g7: Circle CenterX=395 CenterY=80 CenterZ=0 NormalX=0 NormalY=0 NormalZ=1 AngleXU=0 Radius=50
    g8: LineSegment StartX=255 StartY=80 StartZ=0 EndX=395 EndY=80 EndZ=0
    g9: Circle CenterX=535 CenterY=80 CenterZ=0 NormalX=0 NormalY=0 NormalZ=1 AngleXU=0 Radius=50
    g10: LineSegment StartX=395 StartY=80 StartZ=0 EndX=535 EndY=80 EndZ=0
    g11: Circle CenterX=675 CenterY=80 CenterZ=0 NormalX=0 NormalY=0 NormalZ=1 AngleXU=0 Radius=50
    g12: LineSegment StartX=535 StartY=80 StartZ=0 EndX=675 EndY=80 EndZ=0
    g13: Circle CenterX=815 CenterY=80 CenterZ=0 NormalX=0 NormalY=0 NormalZ=1 AngleXU=0 Radius=50
    g14: LineSegment StartX=675 StartY=80 StartZ=0 EndX=815 EndY=80 EndZ=0
    g15: Circle CenterX=955 CenterY=80 CenterZ=0 NormalX=0 NormalY=0 NormalZ=1 AngleXU=0 Radius=50
    g16: Circle CenterX=1095 CenterY=80 CenterZ=0 NormalX=0 NormalY=0 NormalZ=1 AngleXU=0 Radius=50
    g17: Circle CenterX=1235 CenterY=80 CenterZ=0 NormalX=0 NormalY=0 NormalZ=1 AngleXU=0 Radius=50
    g18: Circle CenterX=1375 CenterY=80 CenterZ=0 NormalX=0 NormalY=0 NormalZ=1 AngleXU=0 Radius=50
    g19: LineSegment StartX=1235 StartY=80 StartZ=0 EndX=1375 EndY=80 EndZ=0
    g20: LineSegment StartX=1095 StartY=80 StartZ=0 EndX=1235 EndY=80 EndZ=0
    g21: LineSegment StartX=955 StartY=80 StartZ=0 EndX=1095 EndY=80 EndZ=0
    g22: LineSegment StartX=815 StartY=80 StartZ=0 EndX=955 EndY=80 EndZ=0
  constraints (59):
    c: Coincident(g0,g1)
    c: Coincident(g1,g2)
    c: Coincident(g2,g3)
    c: Coincident(g3,g0)
    c: Horizontal(g0)
    c: Horizontal(g2)
    c: Vertical(g1)
    c: Vertical(g3)
    c: Coincident(g0,g-1)
    c: DistanceY(g3,g3) = 160
    c: DistanceX(g2,g2) = 1490
    c: Diameter(g4) = 100
    c: DistanceY(g4,g2) = 80
    c: Diameter(g5) = 100
    c: Coincident(g4,g6)
    c: Coincident(g5,g6)
    c: Distance(g6) = 140
    c: Angle(g6) = 0
    c: Diameter(g7) = 100
    c: Coincident(g5,g8)
    c: Coincident(g7,g8)
    c: Equal(g6,g8)
    c: Parallel(g8,g6)
    c: Diameter(g9) = 100
    c: Coincident(g7,g10)
    c: Coincident(g9,g10)
    c: Equal(g6,g10)
    c: Parallel(g10,g6)
    c: Diameter(g11) = 100
    c: Coincident(g9,g12)
    c: Coincident(g11,g12)
    c: Equal(g6,g12)
    c: Parallel(g12,g6)
    c: Diameter(g13) = 100
    c: Coincident(g11,g14)
    c: Coincident(g13,g14)
    c: Equal(g6,g14)
    c: Parallel(g14,g6)
    c: Diameter(g15) = 100
    c: Coincident(g15,g22)
    c: Diameter(g16) = 100
    c: Coincident(g15,g21)
    c: Coincident(g16,g21)
    c: Diameter(g17) = 100
    c: Coincident(g16,g20)
    c: Coincident(g17,g20)
    c: Diameter(g18) = 100
    c: Coincident(g17,g19)
    c: Coincident(g18,g19)
    c: Coincident(g22,g13)
    c: Equal(g14,g22)
    c: Equal(g22,g21)
    c: Equal(g21,g20)
    c: Equal(g20,g19)
    c: Horizontal(g22)
    c: Horizontal(g21)
    c: Horizontal(g20)
    c: Horizontal(g19)
    c: DistanceX(g18,g1) = 115
FEATURE [Part::Part2DObjectPython] Wire760  label="Кабинет"  # Draft 2D object (typed FeaturePython)
  Area = 1.35968e+07
  ChamferSize = 0
  Closed = true
  End = (-30,-25,0)
  FilletRadius = 0
  Length = 15180
  MakeFace = true
  Placement = pos=(-1.819e-13,2985,0) rot=(0,0,1;0rad)
  Points = (6) [(-30,550,0),(3400,550,0),(3400,-700,0),(4000,-700,0),(4000,-3010,0),(-30,-3010,0)]
  Start = (-30,3535,0)
  Subdivisions = 0
FEATURE [Part::Extrusion] Extrude084  label="ПНО 40-15-002"
  Base = -> Sketch301
  Dir = (0,3980,0)
  DirMode = 0
  FaceMakerClass = Part::FaceMakerBullseye
  LengthFwd = 3980
  LengthRev = 0
  Placement = pos=(10,3685,2800) rot=(0,0,1;0rad)
  Solid = true
  Symmetric = false
FEATURE [Part::FeaturePython] Array054  label="ПНО-40-15 3шт."  # Draft array (typed FeaturePython)
  Angle = 360
  ArrayType = 0
  Axis = (0,0,1)
  Base = -> Extrude084
  Center = (0,0,0)
  Fuse = false
  IntervalAxis = (0,0,0)
  IntervalX = (1510,0,0)
  IntervalY = (0,0,0)
  IntervalZ = (0,0,1)
  NumberPolar = 1
  NumberX = 3
  NumberY = 1
  NumberZ = 1
  Placement = pos=(-50,-9.09e-13,0) rot=(0,0,1;0rad)
FEATURE [Part::Part2DObjectPython] Rectangle3121  label="проём в перекрытии 007"  # Draft 2D object (typed FeaturePython)
  Area = 3860700
  ChamferSize = 0
  Columns = 1
  FilletRadius = 0
  Height = 3785
  Length = 1020
  MakeFace = true
  Placement = pos=(6900,3720,0) rot=(0,0,1;0rad)
  Rows = 1
FEATURE [Part::FeaturePython] Structure037  label="проём в перекрытии 004"  # Arch/BIM 52 (typed FeaturePython)
  Base = -> Rectangle3121
  FaceMaker = 0
  Height = 4500
  HorizontalArea = 3860700
  IfcData = complex_attributes={"OwnerHistory": {}, "IsNestedBy": {}, "IsDecomposedBy": {}, "IsDefinedBy": {}, "ObjectPlacement": {}, "Representation":... (+4 chars omitted)
  IfcType = 52
  Length = 0
  MoveBase = false
  MoveWithHost = false
  Nodes = (2) [(4500,6910,0),(4500,6910,4500)]
  NodesOffset = 0
  Normal = (0,0,0)
  PerimeterLength = 9610
  VerticalArea = 43245000
  Width = 100
FEATURE [Part::FeaturePython] Wall063  label="Объем стоек стропильной системы"  # Arch/BIM 166 (typed FeaturePython)
  Align = 0
  Area = 34896000
  Base = -> Rectangle2286
  BlockHeight = 0
  BlockLength = 0
  CountBroken = 0
  CountEntire = 0
  Face = 0
  Height = 1200
  HorizontalArea = 5.5625e+06
  IfcType = 166
  Joint = 0
  Length = 29080
  MakeBlocks = false
  MoveBase = false
  MoveWithHost = false
  Normal = (0,0,0)
  OffsetFirst = 0
  OffsetSecond = 0
  PerimeterLength = 30600
  Placement = pos=(0,0,3210) rot=(0,0,1;0rad)
  PredefinedType = 0
  Subtractions = -> [Structure037]
  VerticalArea = 71868000
  Width = 190
FEATURE [Part::FeaturePython] Wall064  label="опорная доска стоек стропильной системы"  # Arch/BIM 166 (typed FeaturePython)
  Align = 0
  Area = 1454000
  Base = -> Rectangle2286
  BlockHeight = 0
  BlockLength = 0
  CountBroken = 0
  CountEntire = 0
  Face = 0
  Height = 50
  HorizontalArea = 5.5625e+06
  IfcType = 166
  Joint = 0
  Length = 29080
  MakeBlocks = false
  MoveBase = false
  MoveWithHost = false
  Normal = (0,0,0)
  OffsetFirst = 0
  OffsetSecond = 0
  PerimeterLength = 30600
  Placement = pos=(0,0,3160) rot=(0,0,1;0rad)
  PredefinedType = 0
  Subtractions = -> [Structure037]
  VerticalArea = 2994500
  Width = 190
FEATURE [Part::Cut] Cut  label="Объем стоек стропильной системы_01"
  Base = -> Wall063
  Tool = -> Roof013
FEATURE [Part::Part2DObjectPython] Line1357  # Draft 2D object (typed FeaturePython)
  ChamferSize = 0
  Closed = true
  End = (4050,-45,0)
  FilletRadius = 0
  Length = 2340
  MakeFace = false
  Placement = pos=(5330,5450,0) rot=(0,0,-1;1.5708rad)
  Points = (2) [(3155,-1280,0),(5495,-1280,0)]
  Start = (4050,2295,0)
  Subdivisions = 0
FEATURE [Part::FeaturePython] Wall222  label="перегородка 048"  # Arch/BIM 166 (typed FeaturePython)
  Align = 2
  Area = 6.552e+06
  Base = -> Line1357
  BlockHeight = 250
  BlockLength = 0
  CountBroken = 0
  CountEntire = 0
  Face = 0
  Height = 2800
  HorizontalArea = 187200
  IfcType = 166
  Joint = 0
  Length = 2340
  MakeBlocks = false
  MoveBase = false
  MoveWithHost = false
  Normal = (0,0,0)
  OffsetFirst = 300
  OffsetSecond = 50
  PerimeterLength = 4840
  PredefinedType = 0
  VerticalArea = 1.3552e+07
  Width = 80
FEATURE [Part::Part2DObjectPython] Line1358  # Draft 2D object (typed FeaturePython)
  ChamferSize = 0
  Closed = true
  End = (6890,3805,0)
  FilletRadius = 0
  Length = 3700
  MakeFace = false
  Placement = pos=(5520,5450,0) rot=(0,0,-1;1.5708rad)
  Points = (2) [(-2055,1370,0),(1645,1370,0)]
  Start = (6890,7505,0)
  Subdivisions = 0
FEATURE [Part::Part2DObjectPython] Line1359  # Draft 2D object (typed FeaturePython)
  ChamferSize = 0
  Closed = true
  End = (3450,2295,0)
  FilletRadius = 0
  Length = 1260
  MakeFace = false
  Placement = pos=(5230,5435,0) rot=(0,0,-1;1.5708rad)
  Points = (2) [(1880,-1780,0),(3140,-1780,0)]
  Start = (3450,3555,0)
  Subdivisions = 0
FEATURE [Part::FeaturePython] Wall224  label="перегородка 050"  # Arch/BIM 166 (typed FeaturePython)
  Align = 2
  Area = 3.528e+06
  Base = -> Line1359
  BlockHeight = 250
  BlockLength = 0
  CountBroken = 0
  CountEntire = 0
  Face = 0
  Height = 2800
  HorizontalArea = 100800
  IfcType = 166
  Joint = 0
  Length = 1260
  MakeBlocks = false
  MoveBase = false
  MoveWithHost = false
  Normal = (0,0,0)
  OffsetFirst = 300
  OffsetSecond = 50
  PerimeterLength = 2680
  PredefinedType = 0
  VerticalArea = 7.504e+06
  Width = 80
FEATURE [Part::Part2DObjectPython] Line1360  # Draft 2D object (typed FeaturePython)
  ChamferSize = 0
  Closed = true
  End = (9500,2375,0)
  FilletRadius = 0
  Length = 2420
  MakeFace = false
  Placement = pos=(10380,1920,0) rot=(0,0,1;0rad)
  Points = (2) [(-880,-1965,0),(-880,455,0)]
  Start = (9500,-45,0)
  Subdivisions = 0
FEATURE [Part::FeaturePython] Wall225  label="перегородка 052"  # Arch/BIM 166 (typed FeaturePython)
  Align = 2
  Area = 6776000
  Base = -> Line1360
  BlockHeight = 250
  BlockLength = 0
  CountBroken = 0
  CountEntire = 0
  Face = 0
  Height = 2800
  HorizontalArea = 193600
  IfcType = 166
  Joint = 0
  Length = 2420
  MakeBlocks = false
  MoveBase = false
  MoveWithHost = false
  Normal = (0,0,0)
  OffsetFirst = 0
  OffsetSecond = 300
  PerimeterLength = 5000
  PredefinedType = 0
  VerticalArea = 1.4e+07
  Width = 80
FEATURE [Part::Part2DObjectPython] Rectangle3159  # Draft 2D object (typed FeaturePython)
  Area = 0
  ChamferSize = 0
  Columns = 1
  FilletRadius = 0
  Height = 250
  Length = 900
  MakeFace = false
  Placement = pos=(6940,5803.61,0) rot=(0,0,1;0rad)
  Rows = 1
FEATURE [App::GeometryPython] BuildingPart077  label="ряд 1"  # Arch/BIM 52 (typed FeaturePython)
  Area = 9655800
  Group = -> [Wall209,Wall208,Wall213,Wall207]
  Height = 0
  HeightPropagate = true
  IfcData = attributes={"GlobalId": {"name": "GlobalId", "type": "IfcGloballyUniqueId", "is_enum": false, "enum_values": []}, "Description": {"... (+484 chars omitted),+1 more (map truncated)
  IfcType = 52
  LevelOffset = 0
FEATURE [App::GeometryPython] BuildingPart078  label="Порядовка"  # Arch/BIM 52 (typed FeaturePython)
  Area = 19311600
  Group = -> [BuildingPart077,BuildingPart072]
  Height = 0
  HeightPropagate = true
  IfcData = attributes={"GlobalId": {"name": "GlobalId", "type": "IfcGloballyUniqueId", "is_enum": false, "enum_values": []}, "Description": {"... (+484 chars omitted),+1 more (map truncated)
  IfcType = 52
  LevelOffset = 0
FEATURE [Image::ImagePlane] ImagePlane001  label="Эскиз планировки"
  Placement = pos=(7057.85,2583.46,-10) rot=(0,0,1;0rad)
  XSize = 15451.2
  YSize = 11577
FEATURE [Part::FeaturePython] Array056  label="ПНО-40-10 1шт. (2)"  # Draft array (typed FeaturePython)
  Angle = 360
  ArrayType = 0
  Axis = (0,0,1)
  Base = -> Extrude061
  Center = (0,0,0)
  Fuse = false
  IntervalAxis = (0,0,0)
  IntervalX = (-1010,0,0)
  IntervalY = (0,0,0)
  IntervalZ = (0,0,1)
  NumberPolar = 1
  NumberX = 1
  NumberY = 1
  NumberZ = 1
  Placement = pos=(11560,9.09e-13,0) rot=(0,0,1;0rad)
FEATURE [Part::FeaturePython] Array057  label="ПНО-40-12 1шт."  # Draft array (typed FeaturePython)
  Angle = 360
  ArrayType = 0
  Axis = (0,0,1)
  Base = -> Extrude062
  Center = (0,0,0)
  Fuse = false
  IntervalAxis = (0,0,0)
  IntervalX = (1210,0,0)
  IntervalY = (0,0,0)
  IntervalZ = (0,0,1)
  NumberPolar = 1
  NumberX = 2
  NumberY = 1
  NumberZ = 1
  Placement = pos=(4480,9.09e-13,0) rot=(0,0,1;0rad)
FEATURE [Part::Extrusion] Extrude087  label="ПНО 39-10-6-005"
  Base = -> Sketch249
  Dir = (0,3880,0)
  DirMode = 0
  FaceMakerClass = Part::FaceMakerBullseye
  LengthFwd = 3880
  LengthRev = 0
  Placement = pos=(10,-205,2800) rot=(0,0,1;0rad)
  Solid = true
  Symmetric = false
FEATURE [Part::FeaturePython] Array058  label="ПНО-39-10 1шт. (1)"  # Draft array (typed FeaturePython)
  Angle = 360
  ArrayType = 0
  Axis = (0,0,1)
  Base = -> Extrude087
  Center = (0,0,0)
  Fuse = false
  IntervalAxis = (0,0,0)
  IntervalX = (-1010,0,0)
  IntervalY = (0,0,0)
  IntervalZ = (0,0,1)
  NumberPolar = 1
  NumberX = 1
  NumberY = 1
  NumberZ = 1
  Placement = pos=(-50,0,0) rot=(0,0,1;0rad)
FEATURE [Part::Extrusion] Extrude088  label="ПНО 39-12-8-005"
  Base = -> Sketch231
  Dir = (0,3880,0)
  DirMode = 0
  FaceMakerClass = Part::FaceMakerBullseye
  LengthFwd = 3880
  LengthRev = 0
  Placement = pos=(10,-205,2800) rot=(0,0,1;0rad)
  Solid = true
  Symmetric = false
FEATURE [Part::FeaturePython] Array059  label="ПНО-39-12 2шт."  # Draft array (typed FeaturePython)
  Angle = 360
  ArrayType = 0
  Axis = (0,0,1)
  Base = -> Extrude088
  Center = (0,0,0)
  Fuse = false
  IntervalAxis = (0,0,0)
  IntervalX = (1210,0,0)
  IntervalY = (0,0,0)
  IntervalZ = (0,0,1)
  NumberPolar = 1
  NumberX = 2
  NumberY = 1
  NumberZ = 1
  Placement = pos=(10150,1.364e-12,0) rot=(0,0,1;0rad)
FEATURE [Part::Extrusion] Extrude089  label="ПНО 39-15-003"
  Base = -> Sketch301
  Dir = (0,3880,0)
  DirMode = 0
  FaceMakerClass = Part::FaceMakerBullseye
  LengthFwd = 3880
  LengthRev = 0
  Placement = pos=(10,-205,2800) rot=(0,0,1;0rad)
  Solid = true
  Symmetric = false
FEATURE [Part::FeaturePython] Array060  label="ПНО-39-15 2шт."  # Draft array (typed FeaturePython)
  Angle = 360
  ArrayType = 0
  Axis = (0,0,1)
  Base = -> Extrude089
  Center = (0,0,0)
  Fuse = false
  IntervalAxis = (0,0,0)
  IntervalX = (1510,0,0)
  IntervalY = (0,0,0)
  IntervalZ = (0,0,1)
  NumberPolar = 1
  NumberX = 2
  NumberY = 1
  NumberZ = 1
  Placement = pos=(960,0,0) rot=(0,0,1;0rad)
FEATURE [Part::FeaturePython] Array061  label="ПНО-39-10 1шт. (2)"  # Draft array (typed FeaturePython)
  Angle = 360
  ArrayType = 0
  Axis = (0,0,1)
  Base = -> Extrude087
  Center = (0,0,0)
  Fuse = false
  IntervalAxis = (0,0,0)
  IntervalX = (-1010,0,0)
  IntervalY = (0,0,0)
  IntervalZ = (0,0,1)
  NumberPolar = 1
  NumberX = 1
  NumberY = 1
  NumberZ = 1
  Placement = pos=(6710,4.54e-13,0) rot=(0,0,1;0rad)
FEATURE [Part::Part2DObjectPython] Rectangle3166  label="Д70-017"  # Draft 2D object (typed FeaturePython)
  ChamferSize = 0
  Columns = 1
  FilletRadius = 0
  Height = 120
  Length = 900
  MakeFace = true
  Placement = pos=(6950,3825,0) rot=(0,0,1;1.5708rad)
  Rows = 1
FEATURE [Part::FeaturePython] Structure333  label="Проём-Д90-003"  # Arch/BIM 52 (typed FeaturePython)
  Base = -> Rectangle3166
  FaceMaker = 0
  Height = 2000
  HorizontalArea = 108000
  IfcData = complex_attributes={"OwnerHistory": {}, "IsNestedBy": {}, "IsDecomposedBy": {}, "IsDefinedBy": {}, "ObjectPlacement": {}, "Representation":... (+4 chars omitted)
  IfcType = 52
  Length = 0
  MoveBase = false
  MoveWithHost = false
  Nodes = (2) [(10750,4050,0),(10750,4050,2180)]
  NodesOffset = 0
  Normal = (0,0,0)
  PerimeterLength = 2040
  VerticalArea = 4.08e+06
  Width = 100
FEATURE [Part::Part2DObjectPython] Line1381  # Draft 2D object (typed FeaturePython)
  ChamferSize = 0
  Closed = true
  End = (5030,5625,0)
  FilletRadius = 0
  Length = 100
  MakeFace = false
  Placement = pos=(2200,7795,0) rot=(0,0,-1;1.5708rad)
  Points = (2) [(2170,2730,0),(2170,2830,0)]
  Start = (4930,5625,0)
  Subdivisions = 0
FEATURE [Part::Part2DObjectPython] Rectangle3168  label="трап"  # Draft 2D object (typed FeaturePython)
  Area = 0
  ChamferSize = 0
  Columns = 1
  FilletRadius = 0
  Height = 900
  Length = 70
  MakeFace = false
  Placement = pos=(6950,3825,0) rot=(0,0,1;0rad)
  Rows = 1
FEATURE [Part::Box] Box3216  label="шкаф книжн. 001"
  AttacherType = Attacher::AttachEngine3D
  Height = 2700
  Length = 900
  Placement = pos=(320,875,0) rot=(0,0,1;1.5708rad)
  Width = 350
FEATURE [Part::Box] Box3217  label="шкаф 60 одежда 005"
  AttacherType = Attacher::AttachEngine3D
  Height = 2700
  Length = 1400
  Placement = pos=(-30,5625,0) rot=(0,0,1;0rad)
  Width = 600
FEATURE [Part::Box] Box3218  label="шкаф 003"
  AttacherType = Attacher::AttachEngine3D
  Height = 2700
  Length = 1245
  Placement = pos=(370,6225,0) rot=(0,0,1;1.5708rad)
  Width = 400
FEATURE [Part::Part2DObjectPython] Line1383  # Draft 2D object (typed FeaturePython)
  ChamferSize = 0
  Closed = true
  End = (1370,6575,0)
  FilletRadius = 0
  Length = 1900
  MakeFace = false
  Placement = pos=(-1100,7435,0) rot=(0,0,-1;1.5708rad)
  Points = (2) [(2760,2470,0),(860,2470,0)]
  Start = (1370,4675,0)
  Subdivisions = 0
FEATURE [Part::Feature] Fillet004  label="стол письменный"
  Placement = pos=(1140,1890,0) rot=(0,0,1;1.5708rad)
  shape: bbox 750 x 1500 x 750 mm, 30 faces (baked)
FEATURE [Part::Feature] Fusion045  label="стул009"
  Placement = pos=(-462.225,3197.19,0) rot=(0,0,-1;1.5708rad)
  shape: bbox 520 x 480 x 910 mm, 35 faces (baked)
FEATURE [Part::Part2DObjectPython] Wire784  # Draft 2D object (typed FeaturePython)
  Area = 1.11339e+06
  ChamferSize = 0
  Closed = true
  End = (8360,3825,0)
  FilletRadius = 0
  Length = 6499.55
  MakeFace = true
  Placement = pos=(7960,3835,0) rot=(0,0,1;0rad)
  Points = (10) [(1.36424e-11,-10,0),(1.36424e-11,2650,0),(-100,2650,0),(-99.9902,2715.1,0),(-65.0942,2750,0),(1.36424e-11,2750,0),(250,2750.02,0),(350,2750,0),+2 more]
  Start = (7960,3825,0)
  Subdivisions = 0
FEATURE [Part::Cylinder] Cylinder002  label="БКН 120л"
  Angle = 360
  AttacherType = Attacher::AttachEngine3D
  Height = 1010
  Placement = pos=(7680,1990,1000) rot=(0,0,1;0rad)
  Radius = 250
FEATURE [Part::Part2DObjectPython] Arc113  label="Arc114"  # Draft 2D object (typed FeaturePython)
  Area = 0
  FirstAngle = 90
  LastAngle = 180
  MakeFace = false
  Placement = pos=(6660,3635,0) rot=(0,0,1;0rad)
  Radius = 800
FEATURE [Part::Box] Box3220  label="Котёл 24кВт одноконтурн. закртытая камера"
  AttacherType = Attacher::AttachEngine3D
  Height = 700
  Length = 400
  Placement = pos=(8130,2000,1300) rot=(0,0,1;0rad)
  Width = 250
FEATURE [Part::Cylinder] Cylinder003  label="бак расширительный"
  Angle = 360
  AttacherType = Attacher::AttachEngine3D
  Height = 400
  Placement = pos=(7680,1990,2200) rot=(0,0,1;0rad)
  Radius = 175
FEATURE [Part::Box] Box3222  label="грёбенка и насосы"
  AttacherType = Attacher::AttachEngine3D
  Height = 900
  Length = 150
  Placement = pos=(7400,-10,0) rot=(0,0,1;0rad)
  Width = 1700
FEATURE [Part::Extrusion] Extrude090  label="ПНО 39-12-8-006"
  Base = -> Sketch231
  Dir = (0,3880,0)
  DirMode = 0
  FaceMakerClass = Part::FaceMakerBullseye
  LengthFwd = 3880
  LengthRev = 0
  Placement = pos=(7740,-205,2800) rot=(0,0,1;0rad)
  Solid = true
  Symmetric = false
FEATURE [Part::Extrusion] Extrude091  label="ПНО 39-12-8-007"
  Base = -> Sketch231
  Dir = (0,3880,0)
  DirMode = 0
  FaceMakerClass = Part::FaceMakerBullseye
  LengthFwd = 3880
  LengthRev = 0
  Placement = pos=(8950,-205,2800) rot=(0,0,1;0rad)
  Solid = true
  Symmetric = false
FEATURE [Part::Cut] Cut040  label="ПНО-39-12 1шт. рез. (1)"
  Base = -> Extrude090
  Tool = -> Structure158
FEATURE [Part::Cut] Cut041  label="ПНО-39-12 1шт. рез. (2)"
  Base = -> Extrude091
  Tool = -> Structure158
FEATURE [Part::Cylinder] Cylinder004  label="Гидроакк. 100л"
  Angle = 360
  AttacherType = Attacher::AttachEngine3D
  Height = 700
  Placement = pos=(8350,2020,140) rot=(0,0,1;0rad)
  Radius = 220
FEATURE [Part::Box] Box3223  label="Котёл электр. (резерв)"
  AttacherType = Attacher::AttachEngine3D
  Height = 700
  Length = 200
  Placement = pos=(7550,1490,1300) rot=(0,0,1;1.5708rad)
  Width = 150
FEATURE [Part::Extrusion] Extrude057  label="мойка_вырез"
  Base = -> Rectangle2392
  Dir = (0,0,1)
  DirMode = 0
  FaceMakerClass = Part::FaceMakerBullseye
  LengthFwd = 150
  LengthRev = 0
  Placement = pos=(0,0,700) rot=(0,0,1;0rad)
  Solid = true
  Symmetric = false
FEATURE [Part::Box] Box3224  label="шкаф 60 кухонный 012"
  AttacherType = Attacher::AttachEngine3D
  Height = 850
  Length = 2960
  Placement = pos=(12550,575,0) rot=(0,0,1;1.5708rad)
  Width = 600
FEATURE [Part::Cut] Cut043  label="Шкаф с мойкой"
  Base = -> Box3224
  Tool = -> Extrude057
FEATURE [Part::Part2DObjectPython] Wire787  label="Тех.помещение"  # Draft 2D object (typed FeaturePython)
  Area = 4335500
  ChamferSize = 0
  Closed = true
  End = (9450,-25,0)
  FilletRadius = 0
  Length = 8720
  MakeFace = true
  Placement = pos=(7380,35,0) rot=(0,0,1;0rad)
  Points = (6) [(20,-60,0),(20,2250,0),(1270,2250,0),(1270,1750,0),(2070,1750,0),(2070,-60,0)]
  Start = (7400,-25,0)
  Subdivisions = 0
FEATURE [Part::Box] Box3227  label="комод"
  AttacherType = Attacher::AttachEngine3D
  Height = 950
  Length = 310
  Placement = pos=(12240,3825,0) rot=(0,0,1;0rad)
  Width = 750
FEATURE [Part::Part2DObjectPython] Wire788  label="Гостиная"  # Draft 2D object (typed FeaturePython)
  Area = 21199100
  ChamferSize = 0
  Closed = true
  End = (6940,5435,0)
  FilletRadius = 0
  Length = 21420
  MakeFace = true
  Placement = pos=(6925,7475,0) rot=(0,0,1;0rad)
  Points = (12) [(15,10,0),(5625,10,0),(5625,-3650,0),(4975,-3650,0),(4975,-3940,0),(2625,-3940,0),(2625,-5090,0),(1495,-5090,0),(1495,-3650,0),(1035,-3650,0),+2 more]
  Start = (6940,7485,0)
  Subdivisions = 0
FEATURE [Part::Part2DObjectPython] Line1390  # Draft 2D object (typed FeaturePython)
  ChamferSize = 0
  Closed = true
  End = (5950,5625,0)
  FilletRadius = 0
  Length = 900
  MakeFace = false
  Placement = pos=(8345,9135,0) rot=(0,0,-1;1.5708rad)
  Points = (2) [(3510,-1495,0),(3510,-2395,0)]
  Start = (6850,5625,0)
  Subdivisions = 0
FEATURE [Part::FeaturePython] Array063  # Draft array (typed FeaturePython)
  Angle = 360
  ArrayType = 0
  Axis = (0,0,1)
  Base = -> Rectangle3159
  Center = (0,0,0)
  Count = 10
  ExpandArray = false
  Fuse = false
  IntervalAxis = (0,0,0)
  IntervalX = (100,0,0)
  IntervalY = (0,-250,0)
  IntervalZ = (0,0,100)
  NumberCircles = 3
  NumberPolar = 5
  NumberX = 1
  NumberY = 10
  NumberZ = 1
  PlacementList = 10 placements: arithmetic series from (6940,5803.61,0) step (0,-250,0) to (6940,3553.61,0)
  RadialDistance = 50
  ScaleList = (10) [(1,1,1),(1,1,1),(1,1,1),(1,1,1),(1,1,1),(1,1,1),(1,1,1),(1,1,1),(1,1,1),(1,1,1)]
  Symmetry = 1
  TangentialDistance = 25
FEATURE [Part::Part2DObjectPython] Line1391  # Draft 2D object (typed FeaturePython)
  ChamferSize = 0
  Closed = true
  End = (6930,5385,0)
  FilletRadius = 0
  Length = 940
  MakeFace = false
  Placement = pos=(10350,5380,0) rot=(0,0,-1;1.5708rad)
  Points = (2) [(-5,-2480,0),(-5,-3420,0)]
  Start = (7870,5385,0)
  Subdivisions = 0
FEATURE [Part::Part2DObjectPython] Line1392  # Draft 2D object (typed FeaturePython)
  Area = 0
  ChamferSize = 0
  Closed = true
  End = (7300,-25,0)
  FilletRadius = 0
  Length = 3200
  MakeFace = true
  Placement = pos=(4210,-10,0) rot=(0,0,1;0rad)
  Points = (2) [(-110,-15,0),(3090,-15,0)]
  Start = (4100,-25,0)
  Subdivisions = 0
FEATURE [Part::Part2DObjectPython] Line1393  # Draft 2D object (typed FeaturePython)
  Area = 0
  ChamferSize = 0
  Closed = true
  End = (9450,-25,0)
  FilletRadius = 0
  Length = 2050
  MakeFace = true
  Placement = pos=(7400,-10,0) rot=(0,0,1;0rad)
  Points = (2) [(0,-15,0),(2050,-15,0)]
  Start = (7400,-25,0)
  Subdivisions = 0
FEATURE [Part::Part2DObjectPython] Wire795  # Draft 2D object (typed FeaturePython)
  Area = 0
  ChamferSize = 0
  Closed = false
  End = (3500,3535,0)
  FilletRadius = 0
  Length = 15610
  MakeFace = true
  Placement = pos=(9500,20,0) rot=(0,0,1;0rad)
  Points = (4) [(50,-45,0),(3050,-45,0),(3050,3515,0),(-6000,3515,0)]
  Start = (9550,-25,0)
  Subdivisions = 0
FEATURE [Part::Part2DObjectPython] Wire796  # Draft 2D object (typed FeaturePython)
  Area = 0
  ChamferSize = 0
  Closed = false
  End = (6940,7485,0)
  FilletRadius = 0
  Length = 13860
  MakeFace = true
  Placement = pos=(7940,3810,0) rot=(0,0,1;0rad)
  Points = (4) [(20,15,0),(4610,15,0),(4610,3675,0),(-1000,3675,0)]
  Start = (7960,3825,0)
  Subdivisions = 0
FEATURE [Part::Part2DObjectPython] Wire797  # Draft 2D object (typed FeaturePython)
  Area = 0
  ChamferSize = 0
  Closed = false
  End = (4820,3825,0)
  FilletRadius = 0
  Length = 13360
  MakeFace = true
  Placement = pos=(4820,7440,0) rot=(0,0,1;0rad)
  Points = (4) [(-9.09495e-13,45,0),(-4850,45,0),(-4850,-3615,0),(-9.09495e-13,-3615,0)]
  Start = (4820,7485,0)
  Subdivisions = 0
FEATURE [Part::Part2DObjectPython] Arc114  label="Arc115"  # Draft 2D object (typed FeaturePython)
  Area = 0
  FirstAngle = 90
  LastAngle = 180
  MakeFace = true
  Placement = pos=(4710,3635,0) rot=(0,0,1;0rad)
  Radius = 800
FEATURE [Part::Part2DObjectPython] Line1394  # Draft 2D object (typed FeaturePython)
  Area = 0
  ChamferSize = 0
  Closed = false
  End = (4710,3635,0)
  FilletRadius = 0
  Length = 800
  MakeFace = true
  Placement = pos=(4710,4435,0) rot=(0,0,1;0rad)
  Points = (2) [(0,0,0),(0,-800,0)]
  Start = (4710,4435,0)
  Subdivisions = 0
FEATURE [Part::Part2DObjectPython] Arc115  label="Arc116"  # Draft 2D object (typed FeaturePython)
  Area = 0
  FirstAngle = -180
  LastAngle = -90
  MakeFace = true
  Placement = pos=(3400,3385,0) rot=(0,0,1;0rad)
  Radius = 800
FEATURE [Part::Part2DObjectPython] Arc116  label="Arc117"  # Draft 2D object (typed FeaturePython)
  Area = 0
  FirstAngle = 180
  LastAngle = 270
  MakeFace = true
  Placement = pos=(6660,2285,0) rot=(0,0,1;0rad)
  Radius = 800
FEATURE [Part::Part2DObjectPython] Line1396  # Draft 2D object (typed FeaturePython)
  Area = 0
  ChamferSize = 0
  Closed = false
  End = (6660,2285,0)
  FilletRadius = 0
  Length = 800
  MakeFace = true
  Placement = pos=(6660,1485,0) rot=(0,0,1;0rad)
  Points = (2) [(0,0,0),(0,800,0)]
  Start = (6660,1485,0)
  Subdivisions = 0
FEATURE [Sketcher::SketchObject] Sketch305
  FullyConstrained = true
  Placement = pos=(4820,6485,0) rot=(0.57735,0.57735,0.57735;2.0944rad)
  sketch-geometry (8):
    g0: LineSegment StartX=0 StartY=0 StartZ=0 EndX=900 EndY=0 EndZ=0
    g1: LineSegment StartX=900 StartY=0 StartZ=0 EndX=900 EndY=2150 EndZ=0
    g2: LineSegment StartX=900 StartY=2150 StartZ=0 EndX=0 EndY=2150 EndZ=0
    g3: LineSegment StartX=0 StartY=2150 StartZ=0 EndX=0 EndY=0 EndZ=0
    g4: LineSegment StartX=50 StartY=0 StartZ=0 EndX=850 EndY=0 EndZ=0
    g5: LineSegment StartX=850 StartY=0 StartZ=0 EndX=850 EndY=2100 EndZ=0
    g6: LineSegment StartX=850 StartY=2100 StartZ=0 EndX=50 EndY=2100 EndZ=0
    g7: LineSegment StartX=50 StartY=2100 StartZ=0 EndX=50 EndY=0 EndZ=0
  constraints (23):
    c: Coincident(g0,g1)
    c: Coincident(g1,g2)
    c: Coincident(g2,g3)
    c: Coincident(g3,g0)
    c: Horizontal(g0)
    c: Horizontal(g2)
    c: Vertical(g1)
    c: Vertical(g3)
    c: Coincident(g4,g5)
    c: Coincident(g5,g6)
    c: Coincident(g6,g7)
    c: Coincident(g7,g4)
    c: Horizontal(g4)
    c: Horizontal(g6)
    c: Vertical(g5)
    c: Vertical(g7)
    c: DistanceY(g1) = 2150  'Height'
    c: DistanceX(g0) = 900  'Width'
    c: DistanceY(g6,g2) = 50  'Frame1'
    c: DistanceX(g2,g6) = 50  'Frame2'
    c: DistanceX(g4,g0) = 50  'Frame3'
    c: DistanceY(g0,g4) = 0
    c: Coincident(g0,g-1)
FEATURE [Sketcher::SketchObject] Sketch309
  FullyConstrained = true
  Placement = pos=(9550,770,0) rot=(0.57735,0.57735,0.57735;2.0944rad)
  sketch-geometry (8):
    g0: LineSegment StartX=0 StartY=0 StartZ=0 EndX=900 EndY=0 EndZ=0
    g1: LineSegment StartX=900 StartY=0 StartZ=0 EndX=900 EndY=2150 EndZ=0
    g2: LineSegment StartX=900 StartY=2150 StartZ=0 EndX=0 EndY=2150 EndZ=0
    g3: LineSegment StartX=0 StartY=2150 StartZ=0 EndX=0 EndY=0 EndZ=0
    g4: LineSegment StartX=50 StartY=0 StartZ=0 EndX=850 EndY=0 EndZ=0
    g5: LineSegment StartX=850 StartY=0 StartZ=0 EndX=850 EndY=2100 EndZ=0
    g6: LineSegment StartX=850 StartY=2100 StartZ=0 EndX=50 EndY=2100 EndZ=0
    g7: LineSegment StartX=50 StartY=2100 StartZ=0 EndX=50 EndY=0 EndZ=0
  constraints (23):
    c: Coincident(g0,g1)
    c: Coincident(g1,g2)
    c: Coincident(g2,g3)
    c: Coincident(g3,g0)
    c: Horizontal(g0)
    c: Horizontal(g2)
    c: Vertical(g1)
    c: Vertical(g3)
    c: Coincident(g4,g5)
    c: Coincident(g5,g6)
    c: Coincident(g6,g7)
    c: Coincident(g7,g4)
    c: Horizontal(g4)
    c: Horizontal(g6)
    c: Vertical(g5)
    c: Vertical(g7)
    c: DistanceY(g1) = 2150  'Height'
    c: DistanceX(g0) = 900  'Width'
    c: DistanceY(g6,g2) = 50  'Frame1'
    c: DistanceX(g2,g6) = 50  'Frame2'
    c: DistanceX(g4,g0) = 50  'Frame3'
    c: DistanceY(g0,g4) = 0
    c: Coincident(g0,g-1)
FEATURE [Part::Part2DObjectPython] Arc118  label="Arc119"  # Draft 2D object (typed FeaturePython)
  Area = 0
  FirstAngle = 0
  LastAngle = 90
  MakeFace = true
  Placement = pos=(9550,820,0) rot=(0,0,1;0rad)
  Radius = 800
FEATURE [Part::Part2DObjectPython] Line1398  # Draft 2D object (typed FeaturePython)
  Area = 0
  ChamferSize = 0
  Closed = false
  End = (9550,820,0)
  FilletRadius = 0
  Length = 800
  MakeFace = true
  Placement = pos=(10350,820,0) rot=(0,0,1;0rad)
  Points = (2) [(0,0,0),(-800,5.68434e-13,0)]
  Start = (10350,820,0)
  Subdivisions = 0
FEATURE [Part::Part2DObjectPython] Line1400  # Draft 2D object (typed FeaturePython)
  Area = 0
  ChamferSize = 0
  Closed = false
  End = (6660,3635,0)
  FilletRadius = 0
  Length = 800
  MakeFace = true
  Placement = pos=(6660,4580,0) rot=(0,0,1;0rad)
  Points = (2) [(0,-145,0),(0,-945,0)]
  Start = (6660,4435,0)
  Subdivisions = 0
FEATURE [Part::Part2DObjectPython] Rectangle3176  label="Контур по блоку ЛСР38 внешний"  # Draft 2D object (typed FeaturePython)
  Area = 0
  ChamferSize = 0
  Columns = 1
  FilletRadius = 0
  Height = 8310
  Length = 13380
  MakeFace = false
  Placement = pos=(-430,-425,0) rot=(0,0,1;0rad)
  Rows = 1
FEATURE [Part::Part2DObjectPython] Wire799  # Draft 2D object (typed FeaturePython)
  Area = 2.524e+06
  ChamferSize = 0
  Closed = true
  End = (12950,-410,0)
  FilletRadius = 0
  Length = 14590
  MakeFace = true
  Placement = pos=(8143,-380,0) rot=(0,0,1;0rad)
  Points = (10) [(-38,-30,0),(-38,370,0),(1307,370,0),(1307,1150,0),(1407,1150,0),(1407,370,0),(4407,370,0),(4407,1640,0),(4807,1640,0),(4807,-30,0)]
  Start = (8105,-410,0)
  Subdivisions = 0
FEATURE [Part::Part2DObjectPython] Wire800  # Draft 2D object (typed FeaturePython)
  Area = 3120000
  ChamferSize = 0
  Closed = true
  End = (-430,-410,0)
  FilletRadius = 0
  Length = 23390
  MakeFace = true
  Placement = pos=(-380,1906,0) rot=(0,0,1;0rad)
  Points = (16) [(-50,-6,0),(350,-6,0),(350,-1916,0),(4480,-1916,0),(4480,364,0),(3880,364,0),(3880,594,0),(3980,594,0),(3980,464,0),(6130,464,0),(6130,364,0),+5 more]
  Start = (-430,1900,0)
  Subdivisions = 0
FEATURE [Part::Part2DObjectPython] Wire801  # Draft 2D object (typed FeaturePython)
  Area = 936000
  ChamferSize = 0
  Closed = true
  End = (7475,-410,0)
  FilletRadius = 0
  Length = 14900
  MakeFace = true
  Placement = pos=(6703,-380,0) rot=(0,0,1;0rad)
  Points = (20) [(2,-30,0),(2,370,0),(597,370,0),(597,2650,0),(-53,2650,0),(-53,2750,0),(2047,2750,0),(2047,2250,0),(2747,2250,0),(2747,2750,0),(2847,2750,0),+9 more]
  Start = (6705,-410,0)
  Subdivisions = 0
FEATURE [Part::Part2DObjectPython] Wire802  # Draft 2D object (typed FeaturePython)
  Area = 3.7167e+06
  ChamferSize = 0
  Closed = true
  End = (-30,3400,0)
  FilletRadius = 0
  Length = 21670
  MakeFace = true
  Placement = pos=(-380,3406,0) rot=(0,0,1;0rad)
  Points = (14) [(-50,-6,0),(-50,4464,0),(2365,4464,0),(2365,4064,0),(350,4064,0),(350,404,0),(4180,404,0),(4180,114,0),(3980,114,0),(3980,-6,0),(3880,-6,0),+3 more]
  Start = (-430,3400,0)
  Subdivisions = 0
FEATURE [Part::Part2DObjectPython] Wire805  label="Облицовка 120мм 044"  # Draft 2D object (typed FeaturePython)
  Area = 154800
  ChamferSize = 0
  Closed = true
  End = (3860,8015,0)
  FilletRadius = 0
  Length = 2820
  MakeFace = true
  Placement = pos=(7341,8015,0) rot=(0,0,1;0rad)
  Points = (4) [(-2191,3.63798e-12,0),(-2191,-120,0),(-3481,-120,0),(-3481,3.63798e-12,0)]
  Start = (5150,8015,0)
  Subdivisions = 0
FEATURE [Part::Part2DObjectPython] Wire808  # Draft 2D object (typed FeaturePython)
  Area = 0
  ChamferSize = 0
  Closed = true
  End = (6830,5685,0)
  FilletRadius = 0
  Length = 5400
  MakeFace = false
  Placement = pos=(6100,4810,0) rot=(0,0,1;0rad)
  Points = (4) [(-170,875,0),(-170,2675,0),(730,2675,0),(730,875,0)]
  Start = (5930,5685,0)
  Subdivisions = 0
FEATURE [Part::Part2DObjectPython] Wire809  # Draft 2D object (typed FeaturePython)
  Area = 0
  ChamferSize = 0
  Closed = true
  End = (6705,5785,0)
  FilletRadius = 0
  Length = 4500
  MakeFace = false
  Placement = pos=(6175,4855,0) rot=(0,0,1;0rad)
  Points = (4) [(-120,930,0),(-120,2530,0),(530,2530,0),(530,930,0)]
  Start = (6055,5785,0)
  Subdivisions = 0
FEATURE [Part::FeaturePython] Structure342  label="Структура006"  # Arch/BIM 52 (typed FeaturePython)
  Base = -> Wire809
  FaceMaker = 0
  Height = 450
  HorizontalArea = 1040000
  IfcData = attributes={"GlobalId": {"name": "GlobalId", "type": "IfcGloballyUniqueId", "is_enum": false, "enum_values": []}, "Description": {"... (+484 chars omitted),+1 more (map truncated)
  IfcType = 52
  Length = 0
  MoveBase = false
  MoveWithHost = false
  Nodes = (2) [(6409.93,5722.83,0),(6409.93,5722.83,450)]
  NodesOffset = 0
  Normal = (0,0,1)
  PerimeterLength = 4500
  Placement = pos=(0,0,150) rot=(0,0,1;0rad)
  VerticalArea = 2025000
  Width = 100
FEATURE [Part::Part2DObjectPython] Circle109  label="Circle110"  # Draft 2D object (typed FeaturePython)
  Area = 0
  FirstAngle = 0
  LastAngle = 0
  MakeFace = false
  Placement = pos=(7390,4155,0) rot=(0,0,-1;1.5708rad)
  Radius = 100
FEATURE [Part::Part2DObjectPython] Line1409  # Draft 2D object (typed FeaturePython)
  Area = 0
  ChamferSize = 0
  Closed = false
  End = (7390,3825,0)
  FilletRadius = 0
  Length = 330
  MakeFace = false
  Placement = pos=(7420,4155,0) rot=(0,0,-1;1.5708rad)
  Points = (2) [(0,-30,0),(330,-30,0)]
  Start = (7390,4155,0)
  Subdivisions = 0
FEATURE [Part::Part2DObjectPython] Rectangle3193  # Draft 2D object (typed FeaturePython)
  Area = 0
  ChamferSize = 0
  Columns = 1
  FilletRadius = 75
  Height = 500
  Length = 240
  MakeFace = false
  Placement = pos=(6130,5445,0) rot=(0,0,-1;1.5708rad)
  Rows = 1
FEATURE [Part::Part2DObjectPython] Rectangle3196  # Draft 2D object (typed FeaturePython)
  Area = 1000
  ChamferSize = 0
  Columns = 1
  FilletRadius = 0
  Height = 10
  Length = 100
  MakeFace = true
  Placement = pos=(4930,5620,0) rot=(0,0,1;0rad)
  Rows = 1
FEATURE [Part::Part2DObjectPython] Rectangle3198  # Draft 2D object (typed FeaturePython)
  Area = 9000
  ChamferSize = 0
  Columns = 1
  FilletRadius = 0
  Height = 10
  Length = 900
  MakeFace = true
  Placement = pos=(5030,5620,0) rot=(0,0,1;0rad)
  Rows = 1
FEATURE [Part::Part2DObjectPython] Wire812  # Draft 2D object (typed FeaturePython)
  Area = 0
  ChamferSize = 0
  Closed = true
  End = (5930,5565,0)
  FilletRadius = 0
  Length = 2552.43
  MakeFace = false
  Placement = pos=(6830,5565,0) rot=(0,0,-1;1.5708rad)
  Points = (10) [(0,0,0),(360,0,0),(360,-184.29,0),(393.033,-216.967,0),(410,-275,0),(410,-625,0),(393.033,-683.033,0),(360,-715.711,0),(360,-900,0),+1 more]
  Start = (6830,5565,0)
  Subdivisions = 0
FEATURE [Part::Part2DObjectPython] Line1424  # Draft 2D object (typed FeaturePython)
  ChamferSize = 0
  Closed = true
  End = (5930,5625,0)
  FilletRadius = 0
  Length = 900
  MakeFace = false
  Placement = pos=(2300,7795,0) rot=(0,0,-1;1.5708rad)
  Points = (2) [(2170,2730,0),(2170,3630,0)]
  Start = (5030,5625,0)
  Subdivisions = 0
FEATURE [Part::Part2DObjectPython] Wire815  label="контур по плитке СУ"  # Draft 2D object (typed FeaturePython)
  Area = 0
  ChamferSize = 0
  Closed = true
  End = (6830,5685,0)
  FilletRadius = 0
  Length = 12920
  MakeFace = false
  Placement = pos=(4930,3825,0) rot=(0,0,1;0rad)
  Points = (8) [(1000,1860,0),(1000,1740,0),(1900,1740,0),(1900,1.81899e-12,0),(0,1.81899e-12,0),(0,3660,0),(1900,3660,0),(1900,1860,0)]
  Start = (5930,5685,0)
  Subdivisions = 0
FEATURE [Part::FeaturePython] Structure346  label="Структура007"  # Arch/BIM 52 (typed FeaturePython)
  Base = -> Rectangle3193
  FaceMaker = 0
  Height = 100
  HorizontalArea = 115171
  IfcData = attributes={"GlobalId": {"name": "GlobalId", "type": "IfcGloballyUniqueId", "is_enum": false, "enum_values": []}, "Description": {"... (+484 chars omitted),+1 more (map truncated)
  IfcType = 52
  Length = 0
  MoveBase = false
  MoveWithHost = false
  Nodes = (2) [(6380,5325,0),(6380,5325,100)]
  NodesOffset = 0
  Normal = (0,0,1)
  PerimeterLength = 1351.24
  Placement = pos=(0,0,900) rot=(0,0,1;0rad)
  VerticalArea = 135124
  Width = 100
FEATURE [Part::Part2DObjectPython] Wire816  # Draft 2D object (typed FeaturePython)
  Area = 2.2367e+06
  ChamferSize = 0
  Closed = true
  End = (6830,7470,0)
  FilletRadius = 0
  Length = 22500
  MakeFace = true
  Placement = pos=(6198,7440,0) rot=(0,0,1;0rad)
  Points = (20) [(-265,30,0),(-265,430,0),(2305,430,0),(2305,30,0),(742,30,0),(742,-2020,0),(1642,-2020,0),(1642,-970,0),(1742,-970,0),(1742,-3630,0),(2242,-3630,0),+9 more]
  Start = (5933,7470,0)
  Subdivisions = 0
FEATURE [Part::Box] Box3228  label="Ниша-дровник"
  AttacherType = Attacher::AttachEngine3D
  Height = 400
  Length = 500
  Placement = pos=(8800,1885,200) rot=(0,0,1;0rad)
  Width = 500
FEATURE [Part::Box] Box3229  label="шкаф 60 кухонный 013"
  AttacherType = Attacher::AttachEngine3D
  Height = 700
  Length = 600
  Placement = pos=(10150,-10,1600) rot=(0,0,1;0rad)
  Width = 600
FEATURE [Part::Box] Box3230  label="шкаф 60 кухонный 001"
  AttacherType = Attacher::AttachEngine3D
  Height = 1600
  Length = 600
  Placement = pos=(10750,-10,0) rot=(0,0,1;1.5708rad)
  Width = 600
FEATURE [Part::Box] Box3231  label="МВ_001"
  AttacherType = Attacher::AttachEngine3D
  Height = 350
  Length = 500
  Placement = pos=(10740,90,1000) rot=(0,0,1;1.5708rad)
  Width = 580
FEATURE [Part::Cut] Cut044
  Base = -> Box3230
  Tool = -> Box3231
FEATURE [Part::Cut] Cut045
  Base = -> Cut044
  Tool = -> Box3209
FEATURE [Part::Box] Box3232  label="МВ_002"
  AttacherType = Attacher::AttachEngine3D
  Height = 350
  Length = 500
  Placement = pos=(10740,90,1000) rot=(0,0,1;1.5708rad)
  Width = 580
FEATURE [Part::Box] Box3233  label="ДШ_002"
  AttacherType = Attacher::AttachEngine3D
  Height = 500
  Length = 500
  Placement = pos=(10740,90,450) rot=(0,0,1;1.5708rad)
  Width = 580
FEATURE [Part::Part2DObjectPython] Rectangle3200  label="четверть_183-003"  # Draft 2D object (typed FeaturePython)
  ChamferSize = 0
  Columns = 1
  FilletRadius = 0
  Height = 120
  Length = 1830
  MakeFace = true
  Placement = pos=(2030,7895,0) rot=(0,0,1;0rad)
  Rows = 1
FEATURE [Part::Part2DObjectPython] Rectangle3201  label="четверть_790-002"  # Draft 2D object (typed FeaturePython)
  ChamferSize = 0
  Columns = 1
  FilletRadius = 0
  Height = 120
  Length = 790
  MakeFace = true
  Placement = pos=(5150,7895,0) rot=(0,0,1;0rad)
  Rows = 1
FEATURE [Part::Part2DObjectPython] Rectangle3202  label="четверть_183-002"  # Draft 2D object (typed FeaturePython)
  ChamferSize = 0
  Columns = 1
  FilletRadius = 0
  Height = 120
  Length = 1830
  MakeFace = true
  Placement = pos=(8660,7895,0) rot=(0,0,1;0rad)
  Rows = 1
FEATURE [Part::FeaturePython] Structure350  label="Проём_четв._044"  # Arch/BIM 52 (typed FeaturePython)
  Base = -> Rectangle3202
  FaceMaker = 0
  Height = 2552
  HorizontalArea = 219600
  IfcData = complex_attributes={"OwnerHistory": {}, "IsNestedBy": {}, "IsDecomposedBy": {}, "IsDefinedBy": {}, "ObjectPlacement": {}, "Representation":... (+4 chars omitted)
  IfcType = 52
  Length = 0
  MoveBase = false
  MoveWithHost = false
  Nodes = (2) [(5775,-395,0),(5775,-395,2335)]
  NodesOffset = 0
  Normal = (0,0,0)
  PerimeterLength = 3900
  Placement = pos=(0,0,-40) rot=(0,0,1;0rad)
  VerticalArea = 9.9528e+06
  Width = 100
FEATURE [Part::Part2DObjectPython] Line1426  # Draft 2D object (typed FeaturePython)
  Area = 0
  ChamferSize = 0
  Closed = true
  End = (-430,7885,0)
  FilletRadius = 0
  Length = 8310
  MakeFace = false
  Placement = pos=(-380,-318,0) rot=(0,0,1;0rad)
  Points = (2) [(-50,-107,0),(-50,8203,0)]
  Start = (-430,-425,0)
  Subdivisions = 0
FEATURE [Part::Part2DObjectPython] Line1427  # Draft 2D object (typed FeaturePython)
  Area = 0
  ChamferSize = 0
  Closed = true
  End = (12950,7885,0)
  FilletRadius = 0
  Length = 8310
  MakeFace = false
  Placement = pos=(12900,-318,0) rot=(0,0,1;0rad)
  Points = (2) [(50,-107,0),(50,8203,0)]
  Start = (12950,-425,0)
  Subdivisions = 0
FEATURE [Part::Part2DObjectPython] Line1430  # Draft 2D object (typed FeaturePython)
  Area = 0
  ChamferSize = 0
  Closed = true
  End = (-50,-425,0)
  FilletRadius = 0
  Length = 12620
  MakeFace = false
  Placement = pos=(-380,-425,0) rot=(0,0,1;0rad)
  Points = (2) [(12950,0,0),(330,0,0)]
  Start = (12570,-425,0)
  Subdivisions = 0
FEATURE [Part::Part2DObjectPython] Line1431  # Draft 2D object (typed FeaturePython)
  Area = 0
  ChamferSize = 0
  Closed = true
  End = (12570,7885,0)
  FilletRadius = 0
  Length = 12620
  MakeFace = false
  Placement = pos=(-380,-303,0) rot=(0,0,1;0rad)
  Points = (2) [(330,8188,0),(12950,8188,0)]
  Start = (-50,7885,0)
  Subdivisions = 0
FEATURE [Part::Part2DObjectPython] Wire817  label="кровля_контур_обрезки"  # Draft 2D object (typed FeaturePython)
  Area = 0
  ChamferSize = 0
  Closed = true
  End = (3198,-1155,0)
  FilletRadius = 0
  Length = 52320
  MakeFace = false
  Placement = pos=(-1210,-1210,0) rot=(0,0,1;0rad)
  Points = (12) [(50,55,0),(50,9825,0),(8285,9825,0),(8285,10600,0),(13285,10600,0),(13285,9825,0),(14890,9825,0),(14890,55,0),(10408,55,0),(10408,-720,0),+2 more]
  Start = (-1160,-1155,0)
  Subdivisions = 0
FEATURE [Part::Extrusion] Extrude
  Base = -> Wire817
  Dir = (0,0,1)
  DirMode = 2
  FaceMakerClass = Part::FaceMakerBullseye
  LengthFwd = 5000
  LengthRev = 0
  Placement = pos=(0,0,2720) rot=(0,0,1;0rad)
  Solid = true
  Symmetric = false
FEATURE [Part::Part2DObjectPython] Rectangle3216  # Draft 2D object (typed FeaturePython)
  Area = 0
  ChamferSize = 0
  Columns = 1
  FilletRadius = 0
  Height = 8540
  Length = 20900
  MakeFace = false
  Placement = pos=(-4200,-540,0) rot=(0,0,1;0rad)
  Rows = 1
FEATURE [Part::Part2DObjectPython] Wire  # Draft 2D object (typed FeaturePython)
  Area = 6.01874e+06
  ChamferSize = 0
  Closed = true
  End = (13030,6661.83,3999.83)
  FilletRadius = 0
  Length = 13021.9
  MakeFace = true
  Placement = pos=(13030,798.165,3999.83) rot=(0.57735,0.57735,0.57735;2.0944rad)
  Points = (3) [(0,0,0),(2931.83,2052.89,0),(5863.67,-9.09495e-13,0)]
  Start = (13030,798.165,3999.83)
  Subdivisions = 0
FEATURE [Part::Extrusion] Extrude092
  Base = -> Wire
  Dir = (1,0,0)
  DirMode = 2
  FaceMakerClass = Part::FaceMakerBullseye
  LengthFwd = 15000
  LengthRev = 0
  Placement = pos=(-14250,0,0) rot=(0,0,1;0rad)
  Solid = false
  Symmetric = false
FEATURE [Sketcher::SketchObject] Sketch316
  FullyConstrained = true
  Placement = pos=(-185,3635,4170) rot=(0.57735,0.57735,0.57735;2.0944rad)
  sketch-geometry (20):
    g0: LineSegment StartX=-1900 StartY=0 StartZ=0 EndX=0 EndY=0 EndZ=0
    g1: LineSegment StartX=0 StartY=0 StartZ=0 EndX=0 EndY=1200 EndZ=0
    g2: LineSegment StartX=0 StartY=1200 StartZ=0 EndX=-611.028 EndY=1200 EndZ=0
    g3: LineSegment StartX=-1900 StartY=297.452 StartZ=0 EndX=-1900 EndY=0 EndZ=0
    g4: LineSegment StartX=-1850 StartY=50 StartZ=0 EndX=-50 EndY=50 EndZ=0
    g5: LineSegment StartX=-50 StartY=50 StartZ=0 EndX=-50 EndY=1150 EndZ=0
    g6: LineSegment StartX=-50 StartY=1150 StartZ=0 EndX=-595.263 EndY=1150 EndZ=0
    g7: LineSegment StartX=-1850 StartY=271.423 StartZ=0 EndX=-1850 EndY=50 EndZ=0
    g8: LineSegment StartX=-1845 StartY=55 StartZ=0 EndX=-55 EndY=55 EndZ=0
    g9: LineSegment StartX=-55 StartY=55 StartZ=0 EndX=-55 EndY=1145 EndZ=0
    g10: LineSegment StartX=-55 StartY=1145 StartZ=0 EndX=-611.121 EndY=1145 EndZ=0
    g11: LineSegment StartX=-1845 StartY=281.028 StartZ=0 EndX=-1845 EndY=55 EndZ=0
    g12: LineSegment StartX=-1795 StartY=105 StartZ=0 EndX=-105 EndY=105 EndZ=0
    g13: LineSegment StartX=-105 StartY=105 StartZ=0 EndX=-105 EndY=1095 EndZ=0
    g14: LineSegment StartX=-105 StartY=1095 StartZ=0 EndX=-595.356 EndY=1095 EndZ=0
    g15: LineSegment StartX=-1795 StartY=255 StartZ=0 EndX=-1795 EndY=105 EndZ=0
    g16: LineSegment StartX=-1900 StartY=297.452 StartZ=0 EndX=-611.028 EndY=1200 EndZ=0
    g17: LineSegment StartX=-1850 StartY=271.423 StartZ=0 EndX=-595.263 EndY=1150 EndZ=0
    g18: LineSegment StartX=-1845 StartY=281.028 StartZ=0 EndX=-611.121 EndY=1145 EndZ=0
    g19: LineSegment StartX=-1795 StartY=255 StartZ=0 EndX=-595.356 EndY=1095 EndZ=0
  constraints (59):
    c: Coincident(g1,g2)
    c: Horizontal(g0)
    c: Horizontal(g2)
    c: Vertical(g1)
    c: Vertical(g3)
    c: Coincident(g4,g5)
    c: Coincident(g5,g6)
    c: Coincident(g7,g4)
    c: Horizontal(g4)
    c: Horizontal(g6)
    c: Vertical(g5)
    c: Vertical(g7)
    c: DistanceX(g4,g0) = 50  'Frame3'
    c: DistanceY(g0,g4) = 50  'Frame4'
    c: Coincident(g8,g9)
    c: Coincident(g9,g10)
    c: Coincident(g11,g8)
    c: Horizontal(g8)
    c: Horizontal(g10)
    c: Vertical(g9)
    c: Vertical(g11)
    c: Coincident(g12,g13)
    c: Coincident(g13,g14)
    c: Coincident(g15,g12)
    c: Horizontal(g12)
    c: Horizontal(g14)
    c: Vertical(g13)
    c: Vertical(g15)
    c: DistanceX(g8,g12) = 50  'Frame5'
    c: DistanceY(g8,g12) = 50  'Frame6'
    c: DistanceX(g14,g10) = 50  'Frame8'
    c: DistanceY(g14,g10) = 50  'Frame7'
    c: DistanceX(g4,g8) = 5
    c: DistanceY(g4,g8) = 5
    c: DistanceX(g10,g6) = 5
    c: DistanceY(g10,g6) = 5
    c: Coincident(g16,g3)
    c: Coincident(g16,g2)
    c: Coincident(g17,g7)
    c: Coincident(g17,g6)
    c: Coincident(g18,g11)
    c: Coincident(g18,g10)
    c: Coincident(g19,g15)
    c: Coincident(g19,g14)
    c: Distance(g11,g17) = 5
    c: Distance(g15,g18) = 50
    c: Distance(g7,g16) = 50
    c: DistanceY(g5,g1) = 50
    c: Parallel(g18,g17)
    c: Parallel(g16,g17)
    c: Parallel(g18,g19)
    c: DistanceX(g0,g4) = 50
    c: DistanceY(g15,g15) = 150
    c: Angle(g19) = 0.610865  'угол наклона'
    c: Coincident(g3,g0)
    c: Coincident(g0,g1)
    c: Coincident(g0,g-1)
    c: DistanceX(g0,g0) = 1900
    c: DistanceY(g1,g1) = 1200
FEATURE [Sketcher::SketchObject] Sketch318
  FullyConstrained = true
  Placement = pos=(-185,3825,4170) rot=(0.57735,-0.57735,-0.57735;2.0944rad)
  sketch-geometry (20):
    g0: LineSegment StartX=-1900 StartY=0 StartZ=0 EndX=0 EndY=0 EndZ=0
    g1: LineSegment StartX=0 StartY=0 StartZ=0 EndX=0 EndY=1200 EndZ=0
    g2: LineSegment StartX=0 StartY=1200 StartZ=0 EndX=-611.028 EndY=1200 EndZ=0
    g3: LineSegment StartX=-1900 StartY=297.452 StartZ=0 EndX=-1900 EndY=0 EndZ=0
    g4: LineSegment StartX=-1850 StartY=50 StartZ=0 EndX=-50 EndY=50 EndZ=0
    g5: LineSegment StartX=-50 StartY=50 StartZ=0 EndX=-50 EndY=1150 EndZ=0
    g6: LineSegment StartX=-50 StartY=1150 StartZ=0 EndX=-595.263 EndY=1150 EndZ=0
    g7: LineSegment StartX=-1850 StartY=271.423 StartZ=0 EndX=-1850 EndY=50 EndZ=0
    g8: LineSegment StartX=-1845 StartY=55 StartZ=0 EndX=-55 EndY=55 EndZ=0
    g9: LineSegment StartX=-55 StartY=55 StartZ=0 EndX=-55 EndY=1145 EndZ=0
    g10: LineSegment StartX=-55 StartY=1145 StartZ=0 EndX=-611.121 EndY=1145 EndZ=0
    g11: LineSegment StartX=-1845 StartY=281.028 StartZ=0 EndX=-1845 EndY=55 EndZ=0
    g12: LineSegment StartX=-1795 StartY=105 StartZ=0 EndX=-105 EndY=105 EndZ=0
    g13: LineSegment StartX=-105 StartY=105 StartZ=0 EndX=-105 EndY=1095 EndZ=0
    g14: LineSegment StartX=-105 StartY=1095 StartZ=0 EndX=-595.356 EndY=1095 EndZ=0
    g15: LineSegment StartX=-1795 StartY=255 StartZ=0 EndX=-1795 EndY=105 EndZ=0
    g16: LineSegment StartX=-1900 StartY=297.452 StartZ=0 EndX=-611.028 EndY=1200 EndZ=0
    g17: LineSegment StartX=-1850 StartY=271.423 StartZ=0 EndX=-595.263 EndY=1150 EndZ=0
    g18: LineSegment StartX=-1845 StartY=281.028 StartZ=0 EndX=-611.121 EndY=1145 EndZ=0
    g19: LineSegment StartX=-1795 StartY=255 StartZ=0 EndX=-595.356 EndY=1095 EndZ=0
  constraints (59):
    c: Coincident(g1,g2)
    c: Horizontal(g0)
    c: Horizontal(g2)
    c: Vertical(g1)
    c: Vertical(g3)
    c: Coincident(g4,g5)
    c: Coincident(g5,g6)
    c: Coincident(g7,g4)
    c: Horizontal(g4)
    c: Horizontal(g6)
    c: Vertical(g5)
    c: Vertical(g7)
    c: DistanceY(g1) = 1200  'Height'
    c: DistanceX(g4,g0) = 50  'Frame3'
    c: DistanceY(g0,g4) = 50  'Frame4'
    c: Coincident(g8,g9)
    c: Coincident(g9,g10)
    c: Coincident(g11,g8)
    c: Horizontal(g8)
    c: Horizontal(g10)
    c: Vertical(g9)
    c: Vertical(g11)
    c: Coincident(g12,g13)
    c: Coincident(g13,g14)
    c: Coincident(g15,g12)
    c: Horizontal(g12)
    c: Horizontal(g14)
    c: Vertical(g13)
    c: Vertical(g15)
    c: DistanceX(g8,g12) = 50  'Frame5'
    c: DistanceY(g8,g12) = 50  'Frame6'
    c: DistanceX(g14,g10) = 50  'Frame8'
    c: DistanceY(g14,g10) = 50  'Frame7'
    c: DistanceX(g4,g8) = 5
    c: DistanceY(g4,g8) = 5
    c: DistanceX(g10,g6) = 5
    c: DistanceY(g10,g6) = 5
    c: Coincident(g16,g3)
    c: Coincident(g16,g2)
    c: Coincident(g17,g7)
    c: Coincident(g17,g6)
    c: Coincident(g18,g11)
    c: Coincident(g18,g10)
    c: Coincident(g19,g15)
    c: Coincident(g19,g14)
    c: Distance(g11,g17) = 5
    c: Distance(g15,g18) = 50
    c: Distance(g7,g16) = 50
    c: DistanceY(g5,g1) = 50
    c: Parallel(g18,g17)
    c: Parallel(g16,g17)
    c: Parallel(g18,g19)
    c: DistanceX(g0,g4) = 50
    c: DistanceY(g15,g15) = 150
    c: Angle(g19) = 0.610865  'угол наклона'
    c: Coincident(g3,g0)
    c: Coincident(g0,g1)
    c: Coincident(g0,g-1)
    c: DistanceX(g0,g0) = 1900
FEATURE [Part::Part2DObjectPython] Rectangle3217  # Draft 2D object (typed FeaturePython)
  Area = 142500
  ChamferSize = 0
  Columns = 1
  FilletRadius = 0
  Height = 1900
  Length = 75
  MakeFace = true
  Placement = pos=(1370,4675,0) rot=(0,0,1;0rad)
  Rows = 1
FEATURE [Part::Part2DObjectPython] Wire819  label="мансарда h1.2m"  # Draft 2D object (typed FeaturePython)
  Area = 7.85664e+07
  ChamferSize = 0
  Closed = true
  End = (540,6334.38,0)
  FilletRadius = 0
  Length = 37852.5
  MakeFace = true
  Placement = pos=(20,5942.03,0) rot=(0,0,1;0rad)
  Points = (12) [(-50,391.092,0),(-50,-4815.15,0),(520,-4816.41,0),(520,-5386.41,0),(11960,-5386.41,0),(11960,-4816.41,0),(12530,-4815.15,0),(12530,391.092,0),+4 more]
  Start = (-30,6333.12,0)
  Subdivisions = 0
FEATURE [Part::Part2DObjectPython] Rectangle3220  # Draft 2D object (typed FeaturePython)
  Area = 0
  ChamferSize = 0
  Columns = 1
  FilletRadius = 0
  Height = 8240
  Length = 13300
  MakeFace = false
  Placement = pos=(-390,-390,0) rot=(0,0,1;0rad)
  Rows = 1
FEATURE [Part::Part2DObjectPython] Line1442  # Draft 2D object (typed FeaturePython)
  Area = 0
  ChamferSize = 0
  Closed = false
  End = (13500,3730,0)
  FilletRadius = 0
  Length = 14500
  MakeFace = false
  Placement = pos=(-390,3730,0) rot=(0,0,1;0rad)
  Points = (2) [(-610,4.54747e-13,0),(13890,0,0)]
  Start = (-1000,3730,0)
  Subdivisions = 0
FEATURE [Part::Part2DObjectPython] Rectangle3222  label="Проём ФР 001"  # Draft 2D object (typed FeaturePython)
  Area = 723419
  ChamferSize = 0
  Columns = 1
  FilletRadius = 0
  Height = 2009.5
  Length = 360
  MakeFace = true
  Placement = pos=(-390,3830,0) rot=(0,0,1;0rad)
  Rows = 1
FEATURE [Part::Part2DObjectPython] Rectangle3223  label="Проём ФР 010"  # Draft 2D object (typed FeaturePython)
  Area = 723419
  ChamferSize = 0
  Columns = 1
  FilletRadius = 0
  Height = 2009.5
  Length = 360
  MakeFace = true
  Placement = pos=(-390,1620.5,0) rot=(0,0,1;0rad)
  Rows = 1
FEATURE [Part::Part2DObjectPython] Rectangle3224  label="Проём ФР 011"  # Draft 2D object (typed FeaturePython)
  Area = 723419
  ChamferSize = 0
  Columns = 1
  FilletRadius = 0
  Height = 2009.5
  Length = 360
  MakeFace = true
  Placement = pos=(12550,3830,0) rot=(0,0,1;0rad)
  Rows = 1
FEATURE [Part::Part2DObjectPython] Rectangle3225  label="Проём ФР 012"  # Draft 2D object (typed FeaturePython)
  Area = 723419
  ChamferSize = 0
  Columns = 1
  FilletRadius = 0
  Height = 2009.5
  Length = 360
  MakeFace = true
  Placement = pos=(12550,1620.5,0) rot=(0,0,1;0rad)
  Rows = 1
FEATURE [Part::Extrusion] Extrude093  label="ПНО 39-15-004"
  Base = -> Sketch301
  Dir = (0,3880,0)
  DirMode = 0
  FaceMakerClass = Part::FaceMakerBullseye
  LengthFwd = 3880
  LengthRev = 0
  Placement = pos=(3990,-205,2800) rot=(0,0,1;0rad)
  Solid = true
  Symmetric = false
FEATURE [Part::Extrusion] Extrude094  label="ПНО 39-12-8-008"
  Base = -> Sketch231
  Dir = (0,3880,0)
  DirMode = 0
  FaceMakerClass = Part::FaceMakerBullseye
  LengthFwd = 3880
  LengthRev = 0
  Placement = pos=(5510,-205,2800) rot=(0,0,1;0rad)
  Solid = true
  Symmetric = false
FEATURE [Part::Part2DObjectPython] Rectangle3227  # Draft 2D object (typed FeaturePython)
  Area = 22500
  ChamferSize = 0
  Columns = 1
  FilletRadius = 0
  Height = 150
  Length = 150
  MakeFace = true
  Placement = pos=(3320,3655,0) rot=(0,0,1;0rad)
  Rows = 1
FEATURE [Part::Part2DObjectPython] Rectangle3228  # Draft 2D object (typed FeaturePython)
  Area = 22500
  ChamferSize = 0
  Columns = 1
  FilletRadius = 0
  Height = 150
  Length = 150
  MakeFace = true
  Placement = pos=(9050,3655,0) rot=(0,0,1;0rad)
  Rows = 1
FEATURE [Part::Part2DObjectPython] Rectangle3229  # Draft 2D object (typed FeaturePython)
  Area = 22500
  ChamferSize = 0
  Columns = 1
  FilletRadius = 0
  Height = 150
  Length = 150
  MakeFace = true
  Placement = pos=(5090,3655,0) rot=(0,0,1;0rad)
  Rows = 1
FEATURE [Part::Part2DObjectPython] Rectangle3232  # Draft 2D object (typed FeaturePython)
  Area = 169500
  ChamferSize = 0
  Columns = 1
  FilletRadius = 0
  Height = 150
  Length = 1130
  MakeFace = true
  Placement = pos=(7920,3655,0) rot=(0,0,1;0rad)
  Rows = 1
FEATURE [Part::Part2DObjectPython] Rectangle3233  # Draft 2D object (typed FeaturePython)
  Area = 545250
  ChamferSize = 0
  Columns = 1
  FilletRadius = 0
  Height = 3635
  Length = 150
  MakeFace = true
  Placement = pos=(7920,3805,0) rot=(0,0,1;0rad)
  Rows = 1
FEATURE [Part::Part2DObjectPython] Rectangle3236  # Draft 2D object (typed FeaturePython)
  Area = 545250
  ChamferSize = 0
  Columns = 1
  FilletRadius = 0
  Height = 3635
  Length = 150
  MakeFace = true
  Placement = pos=(6750,3805,0) rot=(0,0,1;0rad)
  Rows = 1
FEATURE [Part::Part2DObjectPython] Rectangle3239  # Draft 2D object (typed FeaturePython)
  Area = 0
  ChamferSize = 0
  Columns = 1
  FilletRadius = 0
  Height = 1200
  Length = 1200
  MakeFace = false
  Placement = pos=(4239.24,2877.18,0) rot=(0,0,1;0.785398rad)
  Rows = 1
FEATURE [Part::Part2DObjectPython] Rectangle3240  # Draft 2D object (typed FeaturePython)
  Area = 22500
  ChamferSize = 0
  Columns = 1
  FilletRadius = 0
  Height = 150
  Length = 150
  MakeFace = true
  Placement = pos=(6550,3655,0) rot=(0,0,1;0rad)
  Rows = 1
FEATURE [Part::Part2DObjectPython] Rectangle3244  # Draft 2D object (typed FeaturePython)
  Area = 122303
  ChamferSize = 0
  Columns = 1
  FilletRadius = 0
  Height = 265
  Length = 461.522
  MakeFace = true
  Placement = pos=(5288.48,3540,0) rot=(0,0,1;0rad)
  Rows = 1
FEATURE [Part::Part2DObjectPython] Rectangle3247  # Draft 2D object (typed FeaturePython)
  Area = 93750
  ChamferSize = 0
  Columns = 1
  FilletRadius = 0
  Height = 1250
  Length = 75
  MakeFace = true
  Placement = pos=(3341.97,3783.03,0) rot=(0,0,-1;0.785398rad)
  Rows = 1
FEATURE [Part::Part2DObjectPython] Rectangle3248  # Draft 2D object (typed FeaturePython)
  Area = 0
  ChamferSize = 0
  Columns = 1
  FilletRadius = 0
  Height = 1215
  Length = 100
  MakeFace = false
  Placement = pos=(9095,2440,0) rot=(0,0,1;0rad)
  Rows = 1
FEATURE [Part::Part2DObjectPython] Rectangle3249  # Draft 2D object (typed FeaturePython)
  Area = 290718
  ChamferSize = 0
  Columns = 1
  FilletRadius = 0
  Height = 2907.18
  Length = 100
  MakeFace = true
  Placement = pos=(4189.24,20,0) rot=(0,0,1;0rad)
  Rows = 1
FEATURE [Part::Part2DObjectPython] Rectangle3250  # Draft 2D object (typed FeaturePython)
  Area = 291576
  ChamferSize = 0
  Columns = 1
  FilletRadius = 0
  Height = 2915.76
  Length = 100
  MakeFace = true
  Placement = pos=(4189.24,4524.24,0) rot=(0,0,1;0rad)
  Rows = 1
FEATURE [Part::Part2DObjectPython] Rectangle3252  # Draft 2D object (typed FeaturePython)
  Area = 179000
  ChamferSize = 0
  Columns = 1
  FilletRadius = 0
  Height = 1790
  Length = 100
  MakeFace = true
  Placement = pos=(9095,-390,0) rot=(0,0,1;0rad)
  Rows = 1
FEATURE [Part::Part2DObjectPython] Rectangle3253  # Draft 2D object (typed FeaturePython)
  Area = 0
  ChamferSize = 0
  Columns = 1
  FilletRadius = 0
  Height = 800
  Length = 100
  MakeFace = false
  Placement = pos=(9095,2600,0) rot=(0,0,1;0rad)
  Rows = 1
FEATURE [Part::Part2DObjectPython] Arc119  label="Arc120"  # Draft 2D object (typed FeaturePython)
  Area = 0
  FirstAngle = 0
  LastAngle = 90
  MakeFace = false
  Placement = pos=(9195,2600,0) rot=(0,0,1;0rad)
  Radius = 800
FEATURE [Part::Part2DObjectPython] Rectangle3255  # Draft 2D object (typed FeaturePython)
  Area = 0
  ChamferSize = 0
  Columns = 1
  FilletRadius = 0
  Height = 800
  Length = 100
  MakeFace = false
  Placement = pos=(4027.11,2947.89,0) rot=(0,0,1;0.785398rad)
  Rows = 1
FEATURE [Part::Part2DObjectPython] Rectangle3257  # Draft 2D object (typed FeaturePython)
  Area = 0
  ChamferSize = 0
  Columns = 1
  FilletRadius = 0
  Height = 800
  Length = 100
  MakeFace = false
  Placement = pos=(4097.82,4432.82,0) rot=(0,0,1;2.35619rad)
  Rows = 1
FEATURE [Part::Part2DObjectPython] Rectangle3258  # Draft 2D object (typed FeaturePython)
  Area = 0
  ChamferSize = 0
  Columns = 1
  FilletRadius = 0
  Height = 800
  Length = 100
  MakeFace = false
  Placement = pos=(4946.35,3867.13,0) rot=(0,0,1;0.785398rad)
  Rows = 1
FEATURE [Part::Part2DObjectPython] Rectangle3259  # Draft 2D object (typed FeaturePython)
  Area = 10000
  ChamferSize = 0
  Columns = 1
  FilletRadius = 0
  Height = 100
  Length = 100
  MakeFace = true
  Placement = pos=(4189.24,4524.24,0) rot=(0,0,1;0rad)
  Rows = 1
FEATURE [Part::Part2DObjectPython] Rectangle3260  # Draft 2D object (typed FeaturePython)
  Area = 10000
  ChamferSize = 0
  Columns = 1
  FilletRadius = 0
  Height = 100
  Length = 100
  MakeFace = true
  Placement = pos=(4189.24,2827.18,0) rot=(0,0,1;0rad)
  Rows = 1
FEATURE [Part::Part2DObjectPython] Rectangle3261  # Draft 2D object (typed FeaturePython)
  Area = 330000
  ChamferSize = 0
  Columns = 1
  FilletRadius = 0
  Height = 100
  Length = 3300
  MakeFace = true
  Placement = pos=(20,3680,0) rot=(0,0,1;0rad)
  Rows = 1
FEATURE [Part::Part2DObjectPython] Rectangle3262  # Draft 2D object (typed FeaturePython)
  Area = 249000
  ChamferSize = 0
  Columns = 1
  FilletRadius = 0
  Height = 150
  Length = 1660
  MakeFace = true
  Placement = pos=(5240,3655,0) rot=(0,0,1;0rad)
  Rows = 1
FEATURE [Part::Part2DObjectPython] Line1447  # Draft 2D object (typed FeaturePython)
  Area = 0
  ChamferSize = 0
  Closed = false
  End = (4027.11,4503.53,0)
  FilletRadius = 0
  Length = 800
  MakeFace = false
  Placement = pos=(3461.42,5069.21,0) rot=(0,0,1;0rad)
  Points = (2) [(0,0,0),(565.685,-565.685,0)]
  Start = (3461.42,5069.21,0)
  Subdivisions = 0
FEATURE [Part::Part2DObjectPython] Line1448  # Draft 2D object (typed FeaturePython)
  Area = 0
  ChamferSize = 0
  Closed = false
  End = (4027.11,2947.89,0)
  FilletRadius = 0
  Length = 800
  MakeFace = false
  Placement = pos=(3461.42,2382.21,0) rot=(0,0,1;0rad)
  Points = (2) [(0,0,0),(565.685,565.685,0)]
  Start = (3461.42,2382.21,0)
  Subdivisions = 0
FEATURE [Part::Part2DObjectPython] Line1449  # Draft 2D object (typed FeaturePython)
  Area = 0
  ChamferSize = 0
  Closed = false
  End = (9995,2600,0)
  FilletRadius = 0
  Length = 800
  MakeFace = false
  Placement = pos=(9195,2600,0) rot=(0,0,1;0rad)
  Points = (2) [(0,0,0),(800,0,0)]
  Start = (9195,2600,0)
  Subdivisions = 0
FEATURE [Part::Part2DObjectPython] Rectangle3264  # Draft 2D object (typed FeaturePython)
  Area = 0
  ChamferSize = 0
  Columns = 1
  FilletRadius = 0
  Height = 600
  Length = 1500
  MakeFace = false
  Placement = pos=(40,3060,0) rot=(0,0,1;0rad)
  Rows = 1
FEATURE [Part::Part2DObjectPython] Rectangle3265  # Draft 2D object (typed FeaturePython)
  Area = 0
  ChamferSize = 0
  Columns = 1
  FilletRadius = 0
  Height = 600
  Length = 1500
  MakeFace = false
  Placement = pos=(40,3800,0) rot=(0,0,1;0rad)
  Rows = 1
FEATURE [Part::Part2DObjectPython] Rectangle3266  # Draft 2D object (typed FeaturePython)
  Area = 0
  ChamferSize = 0
  Columns = 1
  FilletRadius = 0
  Height = 1200
  Length = 2000
  MakeFace = false
  Placement = pos=(900,600,0) rot=(0,0,1;0rad)
  Rows = 1
FEATURE [Part::Part2DObjectPython] Rectangle3267  # Draft 2D object (typed FeaturePython)
  Area = 0
  ChamferSize = 0
  Columns = 1
  FilletRadius = 0
  Height = 1000
  Length = 400
  MakeFace = false
  Placement = pos=(2400,700,0) rot=(0,0,1;0rad)
  Rows = 1
FEATURE [Part::Part2DObjectPython] Arc122  label="Arc123"  # Draft 2D object (typed FeaturePython)
  Area = 0
  FirstAngle = -45
  LastAngle = 45
  MakeFace = false
  Placement = pos=(4451.37,4503.53,0) rot=(0,0,1;0rad)
  Radius = 800
FEATURE [Part::Part2DObjectPython] Line1450  # Draft 2D object (typed FeaturePython)
  Area = 0
  ChamferSize = 0
  Closed = false
  End = (5017.06,5069.21,0)
  FilletRadius = 0
  Length = 800
  MakeFace = false
  Placement = pos=(4451.37,4503.53,0) rot=(0,0,1;0rad)
  Points = (2) [(0,0,0),(565.685,565.685,0)]
  Start = (4451.37,4503.53,0)
  Subdivisions = 0
FEATURE [Part::Part2DObjectPython] Rectangle3271  # Draft 2D object (typed FeaturePython)
  Area = 0
  ChamferSize = 0
  Columns = 1
  FilletRadius = 0
  Height = 50
  Length = 1100
  MakeFace = false
  Placement = pos=(6860,3590,0) rot=(0,0,1;0rad)
  Rows = 1
FEATURE [Part::Part2DObjectPython] Rectangle3272  # Draft 2D object (typed FeaturePython)
  Area = 0
  ChamferSize = 0
  Columns = 1
  FilletRadius = 0
  Height = 50
  Length = 1100
  MakeFace = false
  Placement = pos=(5800,3590,0) rot=(0,0,1;0rad)
  Rows = 1
FEATURE [Part::Part2DObjectPython] Rectangle3273  # Draft 2D object (typed FeaturePython)
  Area = 0
  ChamferSize = 0
  Columns = 1
  FilletRadius = 0
  Height = 2100
  Length = 1800
  MakeFace = false
  Placement = pos=(8990.68,4787.73,0) rot=(0,0,1;0rad)
  Rows = 1
FEATURE [Part::Part2DObjectPython] Rectangle3274  # Draft 2D object (typed FeaturePython)
  Area = 0
  ChamferSize = 0
  Columns = 1
  FilletRadius = 0
  Height = 400
  Length = 800
  MakeFace = false
  Placement = pos=(9090.68,6387.73,0) rot=(0,0,1;0rad)
  Rows = 1
FEATURE [Part::Part2DObjectPython] Rectangle3275  # Draft 2D object (typed FeaturePython)
  Area = 0
  ChamferSize = 0
  Columns = 1
  FilletRadius = 0
  Height = 400
  Length = 700
  MakeFace = false
  Placement = pos=(9990.68,6387.73,0) rot=(0,0,1;0rad)
  Rows = 1
FEATURE [Part::Part2DObjectPython] Arc123  label="Arc124"  # Draft 2D object (typed FeaturePython)
  Area = 0
  FirstAngle = -225
  LastAngle = -135
  MakeFace = false
  Placement = pos=(4027.11,4503.53,0) rot=(0,0,1;0rad)
  Radius = 800
FEATURE [Part::Part2DObjectPython] Line1451  # Draft 2D object (typed FeaturePython)
  Area = 0
  ChamferSize = 0
  Closed = false
  End = (5158.48,3655,0)
  FilletRadius = 0
  Length = 100
  MakeFace = false
  Placement = pos=(5087.77,3725.71,0) rot=(0,0,1;0rad)
  Points = (2) [(0,0,0),(70.7107,-70.7107,0)]
  Start = (5087.77,3725.71,0)
  Subdivisions = 0
FEATURE [Part::Part2DObjectPython] Line1452  # Draft 2D object (typed FeaturePython)
  Area = 0
  ChamferSize = 0
  Closed = false
  End = (3299.29,3675.71,0)
  FilletRadius = 0
  Length = 1300
  MakeFace = false
  Placement = pos=(4218.53,2756.47,0) rot=(0,0,1;0rad)
  Points = (2) [(0,0,0),(-919.239,919.239,0)]
  Start = (4218.53,2756.47,0)
  Subdivisions = 0
FEATURE [Part::Part2DObjectPython] Line1453  # Draft 2D object (typed FeaturePython)
  Area = 0
  ChamferSize = 0
  Closed = false
  End = (4203.88,4680.3,0)
  FilletRadius = 0
  Length = 1300
  MakeFace = false
  Placement = pos=(3284.64,3761.07,0) rot=(0,0,1;0rad)
  Points = (2) [(0,0,0),(919.239,919.239,0)]
  Start = (3284.64,3761.07,0)
  Subdivisions = 0
FEATURE [Part::Part2DObjectPython] Arc124  label="Arc125"  # Draft 2D object (typed FeaturePython)
  Area = 0
  FirstAngle = -225
  LastAngle = -135
  MakeFace = false
  Placement = pos=(4027.11,2947.89,0) rot=(0,0,1;0rad)
  Radius = 800
FEATURE [Part::Part2DObjectPython] Rectangle3277  # Draft 2D object (typed FeaturePython)
  Area = 0
  ChamferSize = 0
  Columns = 1
  FilletRadius = 0
  Height = 1200
  Length = 2000
  MakeFace = false
  Placement = pos=(856.844,5658.03,0) rot=(0,0,1;0rad)
  Rows = 1
FEATURE [Part::Part2DObjectPython] Rectangle3278  # Draft 2D object (typed FeaturePython)
  Area = 0
  ChamferSize = 0
  Columns = 1
  FilletRadius = 0
  Height = 1000
  Length = 400
  MakeFace = false
  Placement = pos=(2356.84,5758.03,0) rot=(0,0,1;0rad)
  Rows = 1
FEATURE [Part::Part2DObjectPython] Rectangle3282  label="проём в перекрытии под фан.стояк001"  # Draft 2D object (typed FeaturePython)
  ChamferSize = 0
  Columns = 1
  FilletRadius = 0
  Height = 130
  Length = 260
  MakeFace = false
  Placement = pos=(5360,3540,0) rot=(0,0,1;0rad)
  Rows = 1
FEATURE [Part::Part2DObjectPython] Rectangle3283  label="проём в перекрытии 008"  # Draft 2D object (typed FeaturePython)
  ChamferSize = 0
  Columns = 1
  FilletRadius = 0
  Height = 800
  Length = 320
  MakeFace = false
  Placement = pos=(8785,1470,0) rot=(0,0,1;0rad)
  Rows = 1
FEATURE [Part::Part2DObjectPython] Wire821  # Draft 2D object (typed FeaturePython)
  Area = 600400
  ChamferSize = 0
  Closed = true
  End = (5360,3520,0)
  FilletRadius = 0
  Length = 9000
  MakeFace = true
  Placement = pos=(4700,3520,0) rot=(1,0,0;3.14159rad)
  Points = (16) [(0,0,0),(0,-290,0),(120,-290,0),(120,-2920,0),(230,-2920,0),(230,-1310,0),(610,-1310,0),(610,-1190,0),(230,-1190,0),(230,-290,0),(1050,-290,0),+5 more]
  Start = (4700,3520,0)
  Subdivisions = 0
FEATURE [App::DocumentObjectGroup] Group118  label="Контуры стен"
  Group = -> [Wire667,Wire660,Wire658,Wire657,Wire661,Wire664,Wire663,Wire665,Wire670,Wire671,Wire752,Wire749,Wire799,Wire800,Wire801,Wire802,Wire805,Wire816,Rectangle3283,Rectangle3282,Wire821]
FEATURE [Part::Part2DObjectPython] Line1456  # Draft 2D object (typed FeaturePython)
  Area = 0
  ChamferSize = 0
  Closed = false
  End = (4820,7335,0)
  FilletRadius = 0
  Length = 800
  MakeFace = true
  Placement = pos=(4020,7335,0) rot=(0,0,1;0rad)
  Points = (2) [(0,0,0),(800,0,0)]
  Start = (4020,7335,0)
  Subdivisions = 0
FEATURE [Part::Part2DObjectPython] Arc125  label="Arc126"  # Draft 2D object (typed FeaturePython)
  Area = 0
  FirstAngle = -180
  LastAngle = -90
  MakeFace = true
  Placement = pos=(4820,7335,0) rot=(0,0,1;0rad)
  Radius = 800
FEATURE [Part::Part2DObjectPython] Wire822  # Draft 2D object (typed FeaturePython)
  Area = 3.74321e+07
  ChamferSize = 0
  Closed = true
  End = (3500,2385,0)
  FilletRadius = 0
  Length = 39480
  MakeFace = true
  Placement = pos=(3600,3535,0) rot=(0,0,1;1.5708rad)
  Points = (18) [(0,100,0),(0,-4820,0),(290,-4820,0),(290,-4360,0),(2950,-4360,0),(2950,-4260,0),(1900,-4260,0),(1900,-3340,0),(3950,-3340,0),(3950,-8950,0),+8 more]
  Start = (3500,3535,0)
  Subdivisions = 0
FEATURE [Sketcher::SketchObject] Sketch
  FullyConstrained = true
  Placement = pos=(5355,993.568,5040.23) rot=(1,0,0;0.610865rad)
  sketch-geometry (16):
    g0: LineSegment StartX=0 StartY=0 StartZ=0 EndX=550 EndY=0 EndZ=0
    g1: LineSegment StartX=550 StartY=0 StartZ=0 EndX=550 EndY=980 EndZ=0
    g2: LineSegment StartX=550 StartY=980 StartZ=0 EndX=0 EndY=980 EndZ=0
    g3: LineSegment StartX=0 StartY=980 StartZ=0 EndX=0 EndY=0 EndZ=0
    g4: LineSegment StartX=50 StartY=50 StartZ=0 EndX=500 EndY=50 EndZ=0
    g5: LineSegment StartX=500 StartY=50 StartZ=0 EndX=500 EndY=930 EndZ=0
    g6: LineSegment StartX=500 StartY=930 StartZ=0 EndX=50 EndY=930 EndZ=0
    g7: LineSegment StartX=50 StartY=930 StartZ=0 EndX=50 EndY=50 EndZ=0
    g8: LineSegment StartX=55 StartY=55 StartZ=0 EndX=495 EndY=55 EndZ=0
    g9: LineSegment StartX=495 StartY=55 StartZ=0 EndX=495 EndY=925 EndZ=0
    g10: LineSegment StartX=495 StartY=925 StartZ=0 EndX=55 EndY=925 EndZ=0
    g11: LineSegment StartX=55 StartY=925 StartZ=0 EndX=55 EndY=55 EndZ=0
    g12: LineSegment StartX=105 StartY=105 StartZ=0 EndX=445 EndY=105 EndZ=0
    g13: LineSegment StartX=445 StartY=105 StartZ=0 EndX=445 EndY=875 EndZ=0
    g14: LineSegment StartX=445 StartY=875 StartZ=0 EndX=105 EndY=875 EndZ=0
    g15: LineSegment StartX=105 StartY=875 StartZ=0 EndX=105 EndY=105 EndZ=0
  constraints (47):
    c: Coincident(g0,g1)
    c: Coincident(g1,g2)
    c: Coincident(g2,g3)
    c: Coincident(g3,g0)
    c: Horizontal(g0)
    c: Horizontal(g2)
    c: Vertical(g1)
    c: Vertical(g3)
    c: Coincident(g4,g5)
    c: Coincident(g5,g6)
    c: Coincident(g6,g7)
    c: Coincident(g7,g4)
    c: Horizontal(g4)
    c: Horizontal(g6)
    c: Vertical(g5)
    c: Vertical(g7)
    c: DistanceY(g1) = 980  'Height'
    c: DistanceX(g0) = 550  'Width'
    c: DistanceY(g6,g2) = 50  'Frame1'
    c: DistanceX(g2,g6) = 50  'Frame2'
    c: DistanceX(g4,g0) = 50  'Frame3'
    c: DistanceY(g0,g4) = 50  'Frame4'
    c: Coincident(g0,g-1)
    c: Coincident(g8,g9)
    c: Coincident(g9,g10)
    c: Coincident(g10,g11)
    c: Coincident(g11,g8)
    c: Horizontal(g8)
    c: Horizontal(g10)
    c: Vertical(g9)
    c: Vertical(g11)
    c: Coincident(g12,g13)
    c: Coincident(g13,g14)
    c: Coincident(g14,g15)
    c: Coincident(g15,g12)
    c: Horizontal(g12)
    c: Horizontal(g14)
    c: Vertical(g13)
    c: Vertical(g15)
    c: DistanceX(g8,g12) = 50  'Frame5'
    c: DistanceY(g8,g12) = 50  'Frame6'
    c: DistanceX(g14,g10) = 50  'Frame8'
    c: DistanceY(g14,g10) = 50  'Frame7'
    c: DistanceX(g4,g8) = 5
    c: DistanceY(g4,g8) = 5
    c: DistanceX(g10,g6) = 5
    c: DistanceY(g10,g6) = 5
FEATURE [Sketcher::SketchObject] Sketch321
  FullyConstrained = true
  Placement = pos=(6615,991.948,5039.09) rot=(1,0,0;0.610865rad)
  sketch-geometry (16):
    g0: LineSegment StartX=0 StartY=0 StartZ=0 EndX=550 EndY=0 EndZ=0
    g1: LineSegment StartX=550 StartY=0 StartZ=0 EndX=550 EndY=980 EndZ=0
    g2: LineSegment StartX=550 StartY=980 StartZ=0 EndX=0 EndY=980 EndZ=0
    g3: LineSegment StartX=0 StartY=980 StartZ=0 EndX=0 EndY=0 EndZ=0
    g4: LineSegment StartX=50 StartY=50 StartZ=0 EndX=500 EndY=50 EndZ=0
    g5: LineSegment StartX=500 StartY=50 StartZ=0 EndX=500 EndY=930 EndZ=0
    g6: LineSegment StartX=500 StartY=930 StartZ=0 EndX=50 EndY=930 EndZ=0
    g7: LineSegment StartX=50 StartY=930 StartZ=0 EndX=50 EndY=50 EndZ=0
    g8: LineSegment StartX=55 StartY=55 StartZ=0 EndX=495 EndY=55 EndZ=0
    g9: LineSegment StartX=495 StartY=55 StartZ=0 EndX=495 EndY=925 EndZ=0
    g10: LineSegment StartX=495 StartY=925 StartZ=0 EndX=55 EndY=925 EndZ=0
    g11: LineSegment StartX=55 StartY=925 StartZ=0 EndX=55 EndY=55 EndZ=0
    g12: LineSegment StartX=105 StartY=105 StartZ=0 EndX=445 EndY=105 EndZ=0
    g13: LineSegment StartX=445 StartY=105 StartZ=0 EndX=445 EndY=875 EndZ=0
    g14: LineSegment StartX=445 StartY=875 StartZ=0 EndX=105 EndY=875 EndZ=0
    g15: LineSegment StartX=105 StartY=875 StartZ=0 EndX=105 EndY=105 EndZ=0
  constraints (47):
    c: Coincident(g0,g1)
    c: Coincident(g1,g2)
    c: Coincident(g2,g3)
    c: Coincident(g3,g0)
    c: Horizontal(g0)
    c: Horizontal(g2)
    c: Vertical(g1)
    c: Vertical(g3)
    c: Coincident(g4,g5)
    c: Coincident(g5,g6)
    c: Coincident(g6,g7)
    c: Coincident(g7,g4)
    c: Horizontal(g4)
    c: Horizontal(g6)
    c: Vertical(g5)
    c: Vertical(g7)
    c: DistanceY(g1) = 980  'Height'
    c: DistanceX(g0) = 550  'Width'
    c: DistanceY(g6,g2) = 50  'Frame1'
    c: DistanceX(g2,g6) = 50  'Frame2'
    c: DistanceX(g4,g0) = 50  'Frame3'
    c: DistanceY(g0,g4) = 50  'Frame4'
    c: Coincident(g0,g-1)
    c: Coincident(g8,g9)
    c: Coincident(g9,g10)
    c: Coincident(g10,g11)
    c: Coincident(g11,g8)
    c: Horizontal(g8)
    c: Horizontal(g10)
    c: Vertical(g9)
    c: Vertical(g11)
    c: Coincident(g12,g13)
    c: Coincident(g13,g14)
    c: Coincident(g14,g15)
    c: Coincident(g15,g12)
    c: Horizontal(g12)
    c: Horizontal(g14)
    c: Vertical(g13)
    c: Vertical(g15)
    c: DistanceX(g8,g12) = 50  'Frame5'
    c: DistanceY(g8,g12) = 50  'Frame6'
    c: DistanceX(g14,g10) = 50  'Frame8'
    c: DistanceY(g14,g10) = 50  'Frame7'
    c: DistanceX(g4,g8) = 5
    c: DistanceY(g4,g8) = 5
    c: DistanceX(g10,g6) = 5
    c: DistanceY(g10,g6) = 5
FEATURE [Sketcher::SketchObject] Sketch322
  FullyConstrained = true
  Placement = pos=(4725,5626.01,5628.7) rot=(-1,0,0;0.610865rad)
  sketch-geometry (16):
    g0: LineSegment StartX=0 StartY=0 StartZ=0 EndX=550 EndY=0 EndZ=0
    g1: LineSegment StartX=550 StartY=0 StartZ=0 EndX=550 EndY=980 EndZ=0
    g2: LineSegment StartX=550 StartY=980 StartZ=0 EndX=0 EndY=980 EndZ=0
    g3: LineSegment StartX=0 StartY=980 StartZ=0 EndX=0 EndY=0 EndZ=0
    g4: LineSegment StartX=50 StartY=50 StartZ=0 EndX=500 EndY=50 EndZ=0
    g5: LineSegment StartX=500 StartY=50 StartZ=0 EndX=500 EndY=930 EndZ=0
    g6: LineSegment StartX=500 StartY=930 StartZ=0 EndX=50 EndY=930 EndZ=0
    g7: LineSegment StartX=50 StartY=930 StartZ=0 EndX=50 EndY=50 EndZ=0
    g8: LineSegment StartX=55 StartY=55 StartZ=0 EndX=495 EndY=55 EndZ=0
    g9: LineSegment StartX=495 StartY=55 StartZ=0 EndX=495 EndY=925 EndZ=0
    g10: LineSegment StartX=495 StartY=925 StartZ=0 EndX=55 EndY=925 EndZ=0
    g11: LineSegment StartX=55 StartY=925 StartZ=0 EndX=55 EndY=55 EndZ=0
    g12: LineSegment StartX=105 StartY=105 StartZ=0 EndX=445 EndY=105 EndZ=0
    g13: LineSegment StartX=445 StartY=105 StartZ=0 EndX=445 EndY=875 EndZ=0
    g14: LineSegment StartX=445 StartY=875 StartZ=0 EndX=105 EndY=875 EndZ=0
    g15: LineSegment StartX=105 StartY=875 StartZ=0 EndX=105 EndY=105 EndZ=0
  constraints (47):
    c: Coincident(g0,g1)
    c: Coincident(g1,g2)
    c: Coincident(g2,g3)
    c: Coincident(g3,g0)
    c: Horizontal(g0)
    c: Horizontal(g2)
    c: Vertical(g1)
    c: Vertical(g3)
    c: Coincident(g4,g5)
    c: Coincident(g5,g6)
    c: Coincident(g6,g7)
    c: Coincident(g7,g4)
    c: Horizontal(g4)
    c: Horizontal(g6)
    c: Vertical(g5)
    c: Vertical(g7)
    c: DistanceY(g1) = 980  'Height'
    c: DistanceX(g0) = 550  'Width'
    c: DistanceY(g6,g2) = 50  'Frame1'
    c: DistanceX(g2,g6) = 50  'Frame2'
    c: DistanceX(g4,g0) = 50  'Frame3'
    c: DistanceY(g0,g4) = 50  'Frame4'
    c: Coincident(g0,g-1)
    c: Coincident(g8,g9)
    c: Coincident(g9,g10)
    c: Coincident(g10,g11)
    c: Coincident(g11,g8)
    c: Horizontal(g8)
    c: Horizontal(g10)
    c: Vertical(g9)
    c: Vertical(g11)
    c: Coincident(g12,g13)
    c: Coincident(g13,g14)
    c: Coincident(g14,g15)
    c: Coincident(g15,g12)
    c: Horizontal(g12)
    c: Horizontal(g14)
    c: Vertical(g13)
    c: Vertical(g15)
    c: DistanceX(g8,g12) = 50  'Frame5'
    c: DistanceY(g8,g12) = 50  'Frame6'
    c: DistanceX(g14,g10) = 50  'Frame8'
    c: DistanceY(g14,g10) = 50  'Frame7'
    c: DistanceX(g4,g8) = 5
    c: DistanceY(g4,g8) = 5
    c: DistanceX(g10,g6) = 5
    c: DistanceY(g10,g6) = 5
FEATURE [Part::Part2DObjectPython] Line1465  # Draft 2D object (typed FeaturePython)
  Area = 0
  ChamferSize = 0
  Closed = true
  End = (5000,3900,7200)
  FilletRadius = 0
  Length = 7200
  MakeFace = true
  Placement = pos=(4655,3900,0) rot=(0,0,1;0rad)
  Points = (2) [(345,1.81899e-12,0),(345,9.09495e-13,7200)]
  Start = (5000,3900,0)
  Subdivisions = 0
FEATURE [Part::Part2DObjectPython] Rectangle3284  # Draft 2D object (typed FeaturePython)
  Area = 0
  ChamferSize = 0
  Columns = 1
  FilletRadius = 0
  Height = 8240
  Length = 14000
  MakeFace = false
  Placement = pos=(-740,-390,0) rot=(0,0,1;0rad)
  Rows = 1
FEATURE [Part::Extrusion] Extrude108
  Base = -> Rectangle3284
  Dir = (0,0,1)
  DirMode = 2
  FaceMakerClass = Part::FaceMakerBullseye
  LengthFwd = 5000
  LengthRev = 0
  Placement = pos=(0,0,2000) rot=(0,0,1;0rad)
  Solid = true
  Symmetric = false
FEATURE [Part::Part2DObjectPython] Wire825  # Draft 2D object (typed FeaturePython)
  Area = 0
  ChamferSize = 0
  Closed = true
  End = (9225,2390,0)
  FilletRadius = 0
  Length = 3200
  MakeFace = false
  Placement = pos=(8665,2390,0) rot=(0,0,1;0rad)
  Points = (4) [(0,0,0),(0,-1040,0),(560,-1040,0),(560,0,0)]
  Start = (8665,2390,0)
  Subdivisions = 0
FEATURE [Part::Part2DObjectPython] Line1468  label="облицовка ВШ_линия_005"  # Draft 2D object (typed FeaturePython)
  ChamferSize = 0
  Closed = true
  End = (8690,1355,0)
  FilletRadius = 0
  Length = 380
  MakeFace = false
  Placement = pos=(8900,1355,0) rot=(0,0,1;0rad)
  Points = (2) [(170,-9.09495e-13,0),(-210,9.09495e-13,0)]
  Start = (9070,1355,0)
  Subdivisions = 0
FEATURE [Part::Part2DObjectPython] Line1469  label="облицовка ВШ_линия_006"  # Draft 2D object (typed FeaturePython)
  ChamferSize = 0
  Closed = true
  End = (9200,2385,0)
  FilletRadius = 0
  Length = 380
  MakeFace = false
  Placement = pos=(8990,2385,0) rot=(0,0,1;3.14159rad)
  Points = (2) [(170,-9.09495e-13,0),(-210,9.09495e-13,0)]
  Start = (8820,2385,0)
  Subdivisions = 0
FEATURE [Part::Part2DObjectPython] Line1470  label="облицовка ВШ_линия_007"  # Draft 2D object (typed FeaturePython)
  ChamferSize = 0
  Closed = true
  End = (8690,2385,0)
  FilletRadius = 0
  Length = 900
  MakeFace = false
  Placement = pos=(8990,2385,0) rot=(0,0,1;3.14159rad)
  Points = (2) [(300,900,0),(300,2.72848e-12,0)]
  Start = (8690,1485,0)
  Subdivisions = 0
FEATURE [Part::Part2DObjectPython] Line1471  label="облицовка ВШ_линия_008"  # Draft 2D object (typed FeaturePython)
  ChamferSize = 0
  Closed = true
  End = (9200,1355,0)
  FilletRadius = 0
  Length = 900
  MakeFace = false
  Placement = pos=(8900,1355,0) rot=(0,0,1;0rad)
  Points = (2) [(300,900,0),(300,2.72848e-12,0)]
  Start = (9200,2255,0)
  Subdivisions = 0
FEATURE [Part::Part2DObjectPython] Rectangle3286  # Draft 2D object (typed FeaturePython)
  Area = 0
  ChamferSize = 0
  Columns = 1
  FilletRadius = 0
  Height = 1003.52
  Length = 550
  MakeFace = false
  Placement = pos=(5355,993.568,0) rot=(0,0,1;0rad)
  Rows = 1
FEATURE [Part::Part2DObjectPython] Rectangle3287  # Draft 2D object (typed FeaturePython)
  Area = 0
  ChamferSize = 0
  Columns = 1
  FilletRadius = 0
  Height = 1003.52
  Length = 550
  MakeFace = false
  Placement = pos=(6615,991.948,0) rot=(0,0,1;0rad)
  Rows = 1
FEATURE [Part::Part2DObjectPython] Rectangle3288  # Draft 2D object (typed FeaturePython)
  Area = 0
  ChamferSize = 0
  Columns = 1
  FilletRadius = 0
  Height = 1003.52
  Length = 550
  MakeFace = false
  Placement = pos=(4725,5425.25,0) rot=(0,0,1;0rad)
  Rows = 1
FEATURE [Part::Part2DObjectPython] Circle111  label="Circle112"  # Draft 2D object (typed FeaturePython)
  Area = 0
  FirstAngle = 0
  LastAngle = 0
  MakeFace = false
  Placement = pos=(8945,1979.8,0) rot=(0,0,1;0rad)
  Radius = 100
FEATURE [Part::Part2DObjectPython] Circle112  label="Circle113"  # Draft 2D object (typed FeaturePython)
  Area = 0
  FirstAngle = 0
  LastAngle = 0
  MakeFace = false
  Placement = pos=(8945,1979.8,0) rot=(0,0,1;0rad)
  Radius = 150
FEATURE [Part::Part2DObjectPython] Circle115  label="Circle116"  # Draft 2D object (typed FeaturePython)
  Area = 0
  FirstAngle = 0
  LastAngle = 0
  MakeFace = false
  Placement = pos=(8867.89,1548.23,0) rot=(0,0,1;0rad)
  Radius = 55
FEATURE [Part::Part2DObjectPython] Circle116  label="Circle117"  # Draft 2D object (typed FeaturePython)
  Area = 0
  FirstAngle = 0
  LastAngle = 0
  MakeFace = false
  Placement = pos=(8945,2200.27,0) rot=(0,0,1;0rad)
  Radius = 30
FEATURE [Part::FeaturePython] Array064  # Draft array (typed FeaturePython)
  Angle = 360
  ArrayType = 0
  Axis = (0,0,1)
  Base = -> Circle115
  Center = (0,0,0)
  Count = 4
  ExpandArray = false
  Fuse = false
  IntervalAxis = (0,0,0)
  IntervalX = (150,0,0)
  IntervalY = (0,150,0)
  IntervalZ = (0,0,100)
  NumberCircles = 3
  NumberPolar = 5
  NumberX = 2
  NumberY = 2
  NumberZ = 1
  PlacementList = 4 placements: [(8867.89,1548.23,0),(8867.89,1698.23,0),(9017.89,1548.23,0),(9017.89,1698.23,0)]
  RadialDistance = 50
  ScaleList = (4) [(1,1,1),(1,1,1),(1,1,1),(1,1,1)]
  Symmetry = 1
  TangentialDistance = 25
FEATURE [Part::Part2DObjectPython] Circle117  label="Circle118"  # Draft 2D object (typed FeaturePython)
  Area = 0
  FirstAngle = 0
  LastAngle = 0
  MakeFace = false
  Placement = pos=(8945,2200.27,0) rot=(0,0,1;0rad)
  Radius = 55
FEATURE [Part::Part2DObjectPython] Line1478  # Draft 2D object (typed FeaturePython)
  Area = 0
  ChamferSize = 0
  Closed = true
  End = (8915,2029.8,6981)
  FilletRadius = 0
  Length = 0
  MakeFace = false
  Placement = pos=(8915,2029.8,6981) rot=(0,0,1;0rad)
  Points = (2) [(0,0,0),(0,0,0)]
  Start = (8915,2029.8,6981)
  Subdivisions = 0
FEATURE [Part::Part2DObjectPython] Line1479  # Draft 2D object (typed FeaturePython)
  Area = 0
  ChamferSize = 0
  Closed = true
  End = (8945,1979.8,7581)
  FilletRadius = 0
  Length = 5600
  MakeFace = false
  Placement = pos=(8945,1979.8,6981) rot=(0,0,1;0rad)
  Points = (2) [(0,2.50111e-12,-5000),(0,0,600)]
  Start = (8945,1979.8,1981)
  Subdivisions = 0
FEATURE [Part::Part2DObjectPython] Wire828  # Draft 2D object (typed FeaturePython)
  Area = 0
  ChamferSize = 0
  Closed = false
  End = (8945,1979.8,6981)
  FilletRadius = 0
  Length = 5777.48
  MakeFace = false
  Placement = pos=(9130,2120,1300) rot=(0,0,1;0rad)
  Points = (4) [(0,0,0),(0,0,500),(-185,-140.202,731),(-185,-140.202,5681)]
  Start = (9130,2120,1300)
  Subdivisions = 0
FEATURE [Part::Part2DObjectPython] Line1480  # Draft 2D object (typed FeaturePython)
  Area = 0
  ChamferSize = 0
  Closed = false
  End = (8867.89,1698.23,6980)
  FilletRadius = 0
  Length = 4200
  MakeFace = false
  Placement = pos=(8867.89,1698.23,2780) rot=(0,0,1;0rad)
  Points = (2) [(0,0,0),(0,0,4200)]
  Start = (8867.89,1698.23,2780)
  Subdivisions = 0
FEATURE [Part::Part2DObjectPython] Line1481  # Draft 2D object (typed FeaturePython)
  Area = 0
  ChamferSize = 0
  Closed = false
  End = (8948,-1570,3275.2)
  FilletRadius = 0
  Length = 5500
  MakeFace = false
  Placement = pos=(3448,-1570,3275.2) rot=(1,0,0;0.610865rad)
  Points = (2) [(0,0,0),(5500,2.27374e-13,9.09495e-13)]
  Start = (3448,-1570,3275.2)
  Subdivisions = 0
FEATURE [Part::Part2DObjectPython] Line1482  # Draft 2D object (typed FeaturePython)
  Area = 0
  ChamferSize = 0
  Closed = false
  End = (8948,-1447.13,3361.23)
  FilletRadius = 0
  Length = 5500
  MakeFace = false
  Placement = pos=(3448,-1447.13,3361.23) rot=(1,0,0;0.610865rad)
  Points = (2) [(0,0,0),(5500,2.27374e-13,-9.09495e-13)]
  Start = (3448,-1447.13,3361.23)
  Subdivisions = 0
FEATURE [Part::Part2DObjectPython] Line1483  # Draft 2D object (typed FeaturePython)
  Area = 0
  ChamferSize = 0
  Closed = false
  End = (8948,-1447.13,3461.23)
  FilletRadius = 0
  Length = 5500
  MakeFace = false
  Placement = pos=(3448,-1447.13,3461.23) rot=(1,0,0;0.610865rad)
  Points = (2) [(0,0,0),(5500,2.27374e-13,-9.09495e-13)]
  Start = (3448,-1447.13,3461.23)
  Subdivisions = 0
FEATURE [Part::Part2DObjectPython] Line1484  # Draft 2D object (typed FeaturePython)
  Area = 0
  ChamferSize = 0
  Closed = false
  End = (8948,-1570,3375.2)
  FilletRadius = 0
  Length = 5500
  MakeFace = false
  Placement = pos=(3448,-1570,3375.2) rot=(1,0,0;0.610865rad)
  Points = (2) [(0,0,0),(5500,0,0)]
  Start = (3448,-1570,3375.2)
  Subdivisions = 0
FEATURE [Part::FeaturePython] Pipe014  label="Снегозадержатели 010"  # Arch/BIM 98 (typed FeaturePython)
  Base = -> Line1481
  Diameter = 25
  GlobalId = 3FGB4W65b7$RelxxBEC_I3
  HorizontalArea = 0
  IfcData = IfcUID=3FGB4W65b7$RelxxBEC_I3,+2 more (map truncated)
  IfcType = 98
  Length = 5500
  MoveBase = false
  MoveWithHost = false
  OffsetEnd = 0
  OffsetStart = 0
  PerimeterLength = 0
  Placement = pos=(0,0,50) rot=(0,0,1;0rad)
  PredefinedType = 0
  VerticalArea = 0
  WallThickness = 0
FEATURE [Part::FeaturePython] Pipe015  label="Снегозадержатели 011"  # Arch/BIM 98 (typed FeaturePython)
  Base = -> Line1482
  Diameter = 25
  GlobalId = 0m162zSxL9MvR8JxGsHhMh
  HorizontalArea = 0
  IfcData = IfcUID=0m162zSxL9MvR8JxGsHhMh,+2 more (map truncated)
  IfcType = 98
  Length = 5500
  MoveBase = false
  MoveWithHost = false
  OffsetEnd = 0
  OffsetStart = 0
  PerimeterLength = 0
  Placement = pos=(0,0,50) rot=(0,0,1;0rad)
  PredefinedType = 0
  VerticalArea = 0
  WallThickness = 0
FEATURE [Part::FeaturePython] Pipe016  label="Снегозадержатели 012"  # Arch/BIM 98 (typed FeaturePython)
  Base = -> Line1483
  Diameter = 25
  GlobalId = 1BHvc1NuD0qQo1xGtb2qrX
  HorizontalArea = 0
  IfcData = IfcUID=1BHvc1NuD0qQo1xGtb2qrX,+2 more (map truncated)
  IfcType = 98
  Length = 5500
  MoveBase = false
  MoveWithHost = false
  OffsetEnd = 0
  OffsetStart = 0
  PerimeterLength = 0
  Placement = pos=(0,0,50) rot=(0,0,1;0rad)
  PredefinedType = 0
  VerticalArea = 0
  WallThickness = 0
FEATURE [Part::FeaturePython] Pipe017  label="Снегозадержатели 001"  # Arch/BIM 98 (typed FeaturePython)
  Base = -> Line1484
  Diameter = 25
  GlobalId = 3Gvi8SLif8WfTz7jjSrXL2
  HorizontalArea = 0
  IfcData = IfcUID=3Gvi8SLif8WfTz7jjSrXL2,+2 more (map truncated)
  IfcType = 98
  Length = 5500
  MoveBase = false
  MoveWithHost = false
  OffsetEnd = 0
  OffsetStart = 0
  PerimeterLength = 0
  Placement = pos=(0,0,50) rot=(0,0,1;0rad)
  PredefinedType = 0
  VerticalArea = 0
  WallThickness = 0
FEATURE [Part::Part2DObjectPython] Line1486  # Draft 2D object (typed FeaturePython)
  Area = 0
  ChamferSize = 0
  Closed = true
  End = (7257,9030,3275.2)
  FilletRadius = 0
  Length = 4460
  MakeFace = false
  Placement = pos=(11717,9030,3275.2) rot=(0,0.300706,0.953717;3.14159rad)
  Points = (2) [(0,0,0),(4460,-5.92209e-05,-8.45762e-05)]
  Start = (11717,9030,3275.2)
  Subdivisions = 0
FEATURE [Part::Part2DObjectPython] Line1487  # Draft 2D object (typed FeaturePython)
  Area = 0
  ChamferSize = 0
  Closed = false
  End = (7257,8907.13,3361.23)
  FilletRadius = 0
  Length = 4460
  MakeFace = false
  Placement = pos=(11717,8907.13,3361.23) rot=(0,0.300706,0.953717;3.14159rad)
  Points = (2) [(0,0,0),(4460,-9.09495e-13,-1.81899e-12)]
  Start = (11717,8907.13,3361.23)
  Subdivisions = 0
FEATURE [Part::Part2DObjectPython] Line1488  # Draft 2D object (typed FeaturePython)
  Area = 0
  ChamferSize = 0
  Closed = false
  End = (7345,8907.13,3461.23)
  FilletRadius = 0
  Length = 4460
  MakeFace = false
  Placement = pos=(11805,8907.13,3461.23) rot=(0,0.300706,0.953717;3.14159rad)
  Points = (2) [(0,0,0),(4460,0,-9.09495e-13)]
  Start = (11805,8907.13,3461.23)
  Subdivisions = 0
FEATURE [Part::Part2DObjectPython] Line1489  # Draft 2D object (typed FeaturePython)
  Area = 0
  ChamferSize = 0
  Closed = false
  End = (7345,9030,3375.2)
  FilletRadius = 0
  Length = 4460
  MakeFace = false
  Placement = pos=(11805,9030,3375.2) rot=(0,0.300706,0.953717;3.14159rad)
  Points = (2) [(0,0,0),(4460,0,0)]
  Start = (11805,9030,3375.2)
  Subdivisions = 0
FEATURE [Part::FeaturePython] Pipe018  label="Снегозадержатели 013"  # Arch/BIM 98 (typed FeaturePython)
  Base = -> Line1486
  Diameter = 25
  GlobalId = 0psA13S1r3kfjsLgw5ftBB
  HorizontalArea = 0
  IfcData = IfcUID=0psA13S1r3kfjsLgw5ftBB,+2 more (map truncated)
  IfcType = 98
  Length = 4460
  MoveBase = false
  MoveWithHost = false
  OffsetEnd = 0
  OffsetStart = 0
  PerimeterLength = 0
  Placement = pos=(0,0,50) rot=(0,0,1;0rad)
  PredefinedType = 0
  VerticalArea = 0
  WallThickness = 0
FEATURE [Part::FeaturePython] Pipe019  label="Снегозадержатели 014"  # Arch/BIM 98 (typed FeaturePython)
  Base = -> Line1487
  Diameter = 25
  GlobalId = 1ajV3GjIH90PewpSEaAIL9
  HorizontalArea = 0
  IfcData = IfcUID=1ajV3GjIH90PewpSEaAIL9,+2 more (map truncated)
  IfcType = 98
  Length = 4460
  MoveBase = false
  MoveWithHost = false
  OffsetEnd = 0
  OffsetStart = 0
  PerimeterLength = 0
  Placement = pos=(0,0,50) rot=(0,0,1;0rad)
  PredefinedType = 0
  VerticalArea = 0
  WallThickness = 0
FEATURE [Part::FeaturePython] Pipe020  label="Снегозадержатели 015"  # Arch/BIM 98 (typed FeaturePython)
  Base = -> Line1488
  Diameter = 25
  GlobalId = 3F76V0rxL2cvmgn6TVRcv1
  HorizontalArea = 0
  IfcData = IfcUID=3F76V0rxL2cvmgn6TVRcv1,+2 more (map truncated)
  IfcType = 98
  Length = 4460
  MoveBase = false
  MoveWithHost = false
  OffsetEnd = 0
  OffsetStart = 0
  PerimeterLength = 0
  Placement = pos=(0,0,50) rot=(0,0,1;0rad)
  PredefinedType = 0
  VerticalArea = 0
  WallThickness = 0
FEATURE [Part::FeaturePython] Pipe021  label="Снегозадержатели 016"  # Arch/BIM 98 (typed FeaturePython)
  Base = -> Line1489
  Diameter = 25
  GlobalId = 2T$R0KaZDBcBfa4GgFt7Wm
  HorizontalArea = 0
  IfcData = IfcUID=2T$R0KaZDBcBfa4GgFt7Wm,+2 more (map truncated)
  IfcType = 98
  Length = 4460
  MoveBase = false
  MoveWithHost = false
  OffsetEnd = 0
  OffsetStart = 0
  PerimeterLength = 0
  Placement = pos=(0,0,50) rot=(0,0,1;0rad)
  PredefinedType = 0
  VerticalArea = 0
  WallThickness = 0
FEATURE [Part::Part2DObjectPython] Wire829  # Draft 2D object (typed FeaturePython)
  Area = 0
  ChamferSize = 0
  Closed = false
  End = (4000,-25,0)
  FilletRadius = 0
  Length = 11020
  MakeFace = false
  Placement = pos=(3510,3520,0) rot=(0,0,1;0rad)
  Points = (4) [(-110,15,0),(-3540,15,0),(-3540,-3545,0),(490,-3545,0)]
  Start = (3400,3535,0)
  Subdivisions = 0
FEATURE [Part::Part2DObjectPython] Wire830  # Draft 2D object (typed FeaturePython)
  Area = 0
  ChamferSize = 0
  Closed = false
  End = (8945,2200.27,7500)
  FilletRadius = 0
  Length = 6119.59
  MakeFace = false
  Placement = pos=(8330,2125,2000) rot=(0,0,1;0rad)
  Points = (4) [(0,0,0),(0,0,200),(615,75.27,200),(615,75.27,5500)]
  Start = (8330,2125,2000)
  Subdivisions = 0
FEATURE [Part::Part2DObjectPython] Rectangle3296  # Draft 2D object (typed FeaturePython)
  Area = 0
  ChamferSize = 0
  Columns = 1
  FilletRadius = 0
  Height = 1030
  Length = 510
  MakeFace = false
  Placement = pos=(8690,1355,0) rot=(0,0,1;0rad)
  Rows = 1
FEATURE [Part::Part2DObjectPython] Rectangle3297  label="проём вентшахты001"  # Draft 2D object (typed FeaturePython)
  ChamferSize = 0
  Columns = 1
  FilletRadius = 0
  Height = 800
  Length = 320
  MakeFace = false
  Placement = pos=(8785,1470,0) rot=(0,0,1;0rad)
  Rows = 1
FEATURE [Part::Part2DObjectPython] Line1497  # Draft 2D object (typed FeaturePython)
  Area = 0
  ChamferSize = 0
  Closed = true
  End = (3725,3730,0)
  FilletRadius = 0
  Length = 6908.43
  MakeFace = true
  Placement = pos=(-1230,8670,0) rot=(0,0,1;0rad)
  Points = (2) [(70,-55,0),(4955,-4940,0)]
  Start = (-1160,8615,0)
  Subdivisions = 0
FEATURE [Part::Part2DObjectPython] Line1498  # Draft 2D object (typed FeaturePython)
  Area = 0
  ChamferSize = 0
  Closed = true
  End = (-1160,-1155,0)
  FilletRadius = 0
  Length = 6908.43
  MakeFace = true
  Placement = pos=(3710,3730,0) rot=(0,0,1;0rad)
  Points = (2) [(15,0,0),(-4870,-4885,0)]
  Start = (3725,3730,0)
  Subdivisions = 0
FEATURE [Part::Part2DObjectPython] Line1499  # Draft 2D object (typed FeaturePython)
  Area = 0
  ChamferSize = 0
  Closed = true
  End = (8795,3730,0)
  FilletRadius = 0
  Length = 5070
  MakeFace = true
  Placement = pos=(3710,3730,0) rot=(0,0,1;0rad)
  Points = (2) [(15,0,0),(5085,0,0)]
  Start = (3725,3730,0)
  Subdivisions = 0
FEATURE [Part::Part2DObjectPython] Line1500  # Draft 2D object (typed FeaturePython)
  Area = 0
  ChamferSize = 0
  Closed = true
  End = (13680,8615,0)
  FilletRadius = 0
  Length = 6908.43
  MakeFace = true
  Placement = pos=(8810,3730,0) rot=(0,0,1;0rad)
  Points = (2) [(-15,-4.54747e-13,0),(4870,4885,0)]
  Start = (8795,3730,0)
  Subdivisions = 0
FEATURE [Part::Part2DObjectPython] Line1501  # Draft 2D object (typed FeaturePython)
  Area = 0
  ChamferSize = 0
  Closed = true
  End = (13680,-1155,0)
  FilletRadius = 0
  Length = 6908.43
  MakeFace = true
  Placement = pos=(8810,3730,0) rot=(0,0,1;0rad)
  Points = (2) [(-15,-4.54747e-13,0),(4870,-4885,0)]
  Start = (8795,3730,0)
  Subdivisions = 0
FEATURE [Part::Part2DObjectPython] Line1502  # Draft 2D object (typed FeaturePython)
  Area = 0
  ChamferSize = 0
  Closed = true
  End = (13260,7465.93,0)
  FilletRadius = 0
  Length = 5283.4
  MakeFace = true
  Placement = pos=(9480,3730,0) rot=(0,0,1;0rad)
  Points = (2) [(44.0742,-4.54747e-13,0),(3780,3735.93,0)]
  Start = (9524.07,3730,0)
  Subdivisions = 0
FEATURE [Part::Part2DObjectPython] Line1503  # Draft 2D object (typed FeaturePython)
  Area = 0
  ChamferSize = 0
  Closed = true
  End = (13260,-5.92599,0)
  FilletRadius = 0
  Length = 5283.4
  MakeFace = true
  Placement = pos=(9480,3730,0) rot=(0,0,1;0rad)
  Points = (2) [(44.0742,-4.54747e-13,0),(3780,-3735.93,0)]
  Start = (9524.07,3730,0)
  Subdivisions = 0
FEATURE [Part::Part2DObjectPython] Line1504  # Draft 2D object (typed FeaturePython)
  Area = 0
  ChamferSize = 0
  Closed = true
  End = (13260,-5.92599,0)
  FilletRadius = 0
  Length = 7471.85
  MakeFace = true
  Placement = pos=(13310,7560,0) rot=(0,0,1;0rad)
  Points = (2) [(-50,-94.0742,0),(-50,-7565.93,0)]
  Start = (13260,7465.93,0)
  Subdivisions = 0
FEATURE [Part::Part2DObjectPython] Line1505  # Draft 2D object (typed FeaturePython)
  Area = 0
  ChamferSize = 0
  Closed = true
  End = (-740,-5.926,0)
  FilletRadius = 0
  Length = 7471.85
  MakeFace = true
  Placement = pos=(-810,7580,0) rot=(0,0,1;0rad)
  Points = (2) [(70,-114.074,0),(70,-7585.93,0)]
  Start = (-740,7465.93,0)
  Subdivisions = 0
FEATURE [Part::Part2DObjectPython] Line1506  # Draft 2D object (typed FeaturePython)
  Area = 0
  ChamferSize = 0
  Closed = true
  End = (2995.93,3730,0)
  FilletRadius = 0
  Length = 5283.4
  MakeFace = true
  Placement = pos=(-810,-120,0) rot=(0,0,1;0rad)
  Points = (2) [(70,114.074,0),(3805.93,3850,0)]
  Start = (-740,-5.926,0)
  Subdivisions = 0
FEATURE [Part::Part2DObjectPython] Line1507  # Draft 2D object (typed FeaturePython)
  Area = 0
  ChamferSize = 0
  Closed = true
  End = (-740,7465.93,0)
  FilletRadius = 0
  Length = 5283.4
  MakeFace = true
  Placement = pos=(3040,3730,0) rot=(0,0,1;0rad)
  Points = (2) [(-44.074,0,0),(-3780,3735.93,0)]
  Start = (2995.93,3730,0)
  Subdivisions = 0
FEATURE [Part::Part2DObjectPython] Wire831  # Draft 2D object (typed FeaturePython)
  Area = 3.576e+06
  ChamferSize = 0
  Closed = true
  End = (11950,575,0)
  FilletRadius = 0
  Length = 13120
  MakeFace = true
  Placement = pos=(9550,575,0) rot=(0,0,1;0rad)
  Points = (6) [(0,0,0),(0,-600,0),(3000,-600,0),(3000,2960,0),(2400,2960,0),(2400,4.54747e-13,0)]
  Start = (9550,575,0)
  Subdivisions = 0
FEATURE [Part::Part2DObjectPython] Rectangle3298  label="Шкаф 60 017"  # Draft 2D object (typed FeaturePython)
  Area = 486000
  ChamferSize = 0
  Columns = 1
  FilletRadius = 0
  Height = 1215
  Length = 400
  MakeFace = true
  Placement = pos=(-30,3825,0) rot=(0,0,1;0rad)
  Rows = 1
FEATURE [Part::Part2DObjectPython] Rectangle3299  label="Шкаф 60 018"  # Draft 2D object (typed FeaturePython)
  Area = 840000
  ChamferSize = 0
  Columns = 1
  FilletRadius = 0
  Height = 600
  Length = 1400
  MakeFace = true
  Placement = pos=(-30,5040,0) rot=(0,0,1;0rad)
  Rows = 1
FEATURE [Part::Part2DObjectPython] Rectangle3300  label="Шкаф 60 019"  # Draft 2D object (typed FeaturePython)
  Area = 840000
  ChamferSize = 0
  Columns = 1
  FilletRadius = 0
  Height = 600
  Length = 1400
  MakeFace = true
  Placement = pos=(-30,5640,0) rot=(0,0,1;0rad)
  Rows = 1
FEATURE [Part::Part2DObjectPython] Rectangle3302  # Draft 2D object (typed FeaturePython)
  ChamferSize = 0
  Columns = 1
  FilletRadius = 100
  Height = 1500
  Length = 750
  MakeFace = true
  Placement = pos=(-10,1890,0) rot=(0,0,1;0rad)
  Rows = 1
FEATURE [Sketcher::SketchObject] Sketch323  label="кресло 45'014"
  FullyConstrained = false
  Placement = pos=(850,2620,0) rot=(0,0,-1;1.5708rad)
  sketch-geometry (11):
    g0: LineSegment StartX=-280 StartY=-350 StartZ=0 EndX=280 EndY=-350 EndZ=0
    g1: LineSegment StartX=330 StartY=-300 StartZ=0 EndX=330 EndY=300 EndZ=0
    g2: LineSegment StartX=280 StartY=350 StartZ=0 EndX=-280 EndY=350 EndZ=0
    g3: LineSegment StartX=-330 StartY=300 StartZ=0 EndX=-330 EndY=-300 EndZ=0
    g4: ArcOfCircle CenterX=-280 CenterY=300 CenterZ=0 NormalX=0 NormalY=0 NormalZ=1 AngleXU=0 Radius=50 StartAngle=1.5708 EndAngle=3.14159
    g5: ArcOfCircle CenterX=280 CenterY=300 CenterZ=0 NormalX=0 NormalY=0 NormalZ=1 AngleXU=0 Radius=50 StartAngle=-9e-16 EndAngle=1.5708
    g6: ArcOfCircle CenterX=280 CenterY=-300 CenterZ=0 NormalX=0 NormalY=0 NormalZ=1 AngleXU=0 Radius=50 StartAngle=4.71239 EndAngle=6.28319
    g7: ArcOfCircle CenterX=-280 CenterY=-300 CenterZ=0 NormalX=0 NormalY=0 NormalZ=1 AngleXU=0 Radius=50 StartAngle=3.14159 EndAngle=4.71239
    g8: LineSegment StartX=-330 StartY=200 StartZ=0 EndX=330 EndY=200 EndZ=0
    g9: LineSegment StartX=-230 StartY=200 StartZ=0 EndX=-230 EndY=-350 EndZ=0
    g10: LineSegment StartX=230 StartY=200 StartZ=0 EndX=230 EndY=-350 EndZ=0
  constraints (29):
    c: Horizontal(g0)
    c: Vertical(g1)
    c: Vertical(g3)
    c: Tangent(g2,g4) = -1.5708
    c: Tangent(g3,g4) = -1.5708
    c: Tangent(g2,g5) = -1.5708
    c: Tangent(g1,g5) = -1.5708
    c: Tangent(g0,g6) = -1.5708
    c: Tangent(g1,g6) = -1.5708
    c: Tangent(g3,g7) = -1.5708
    c: Tangent(g0,g7) = -1.5708
    c: DistanceY(g0,g2) = 700
    c: DistanceX(g3,g1) = 660
    c: Equal(g4,g5)
    c: Equal(g7,g6)
    c: Radius(g5) = 50
    c: Symmetric(g2,g2,g-2)
    c: Symmetric(g2,g0,g-1)
    c: PointOnObject(g8,g3)
    c: PointOnObject(g8,g1)
    c: Horizontal(g8)
    c: DistanceY(g8,g2) = 150
    c: PointOnObject(g9,g8)
    c: PointOnObject(g9,g0)
    c: Vertical(g9)
    c: PointOnObject(g10,g0)
    c: Vertical(g10)
    c: DistanceX(g10,g8) = 100
    c: Symmetric(g10,g9,g-2)
FEATURE [Part::Part2DObjectPython] Rectangle3303  label="Шкаф 60 020"  # Draft 2D object (typed FeaturePython)
  Area = 1386000
  ChamferSize = 0
  Columns = 1
  FilletRadius = 0
  Height = 2310
  Length = 600
  MakeFace = true
  Placement = pos=(3400,-25,0) rot=(0,0,1;0rad)
  Rows = 1
FEATURE [Part::Part2DObjectPython] Rectangle3304  # Draft 2D object (typed FeaturePython)
  ChamferSize = 0
  Columns = 1
  FilletRadius = 0
  Height = 1800
  Length = 2100
  MakeFace = true
  Placement = pos=(3570,6525,0) rot=(0,0,1;3.14159rad)
  Rows = 1
FEATURE [Part::Part2DObjectPython] Rectangle3305  # Draft 2D object (typed FeaturePython)
  Area = 0
  ChamferSize = 0
  Columns = 1
  FilletRadius = 0
  Height = 600
  Length = 350
  MakeFace = false
  Placement = pos=(1570,5725,0) rot=(0,0,1;0rad)
  Rows = 1
FEATURE [Part::Part2DObjectPython] Rectangle3306  # Draft 2D object (typed FeaturePython)
  Area = 0
  ChamferSize = 0
  Columns = 1
  FilletRadius = 0
  Height = 600
  Length = 350
  MakeFace = false
  Placement = pos=(1570,4945,0) rot=(0,0,1;0rad)
  Rows = 1
FEATURE [Part::Part2DObjectPython] Rectangle3307  label="Шкаф 60 021"  # Draft 2D object (typed FeaturePython)
  Area = 600000
  ChamferSize = 0
  Columns = 1
  FilletRadius = 0
  Height = 400
  Length = 1500
  MakeFace = true
  Placement = pos=(4100,-25,0) rot=(0,0,1;0rad)
  Rows = 1
FEATURE [Part::Part2DObjectPython] Rectangle3308  label="Шкаф 60 022"  # Draft 2D object (typed FeaturePython)
  Area = 900000
  ChamferSize = 0
  Columns = 1
  FilletRadius = 0
  Height = 600
  Length = 1500
  MakeFace = true
  Placement = pos=(4100,1685,0) rot=(0,0,1;0rad)
  Rows = 1
FEATURE [Part::Part2DObjectPython] Rectangle3309  label="Шкаф 60 023"  # Draft 2D object (typed FeaturePython)
  Area = 1.155e+06
  ChamferSize = 0
  Columns = 1
  FilletRadius = 0
  Height = 2310
  Length = 500
  MakeFace = true
  Placement = pos=(6800,-25,0) rot=(0,0,1;0rad)
  Rows = 1
FEATURE [Part::Part2DObjectPython] Rectangle3310  # Draft 2D object (typed FeaturePython)
  ChamferSize = 0
  Columns = 1
  FilletRadius = 0
  Height = 1200
  Length = 75
  MakeFace = false
  Placement = pos=(8190,6215,0) rot=(0,0,1;3.14159rad)
  Rows = 1
FEATURE [Part::Part2DObjectPython] Circle119  label="Circle120"  # Draft 2D object (typed FeaturePython)
  Area = 196350
  FirstAngle = 0
  LastAngle = 0
  MakeFace = true
  Placement = pos=(7680,1990,0) rot=(0,0,1;0rad)
  Radius = 250
FEATURE [Part::Part2DObjectPython] Circle120  label="Circle121"  # Draft 2D object (typed FeaturePython)
  Area = 0
  FirstAngle = 0
  LastAngle = 0
  MakeFace = false
  Placement = pos=(7680,1990,0) rot=(0,0,1;0rad)
  Radius = 175
FEATURE [Part::Part2DObjectPython] Rectangle3311  # Draft 2D object (typed FeaturePython)
  Area = 259500
  ChamferSize = 0
  Columns = 1
  FilletRadius = 0
  Height = 1730
  Length = 150
  MakeFace = true
  Placement = pos=(7400,-25,0) rot=(0,0,1;0rad)
  Rows = 1
FEATURE [Part::Part2DObjectPython] Rectangle3312  # Draft 2D object (typed FeaturePython)
  Area = 100000
  ChamferSize = 0
  Columns = 1
  FilletRadius = 0
  Height = 250
  Length = 400
  MakeFace = true
  Placement = pos=(8130,2000,0) rot=(0,0,1;0rad)
  Rows = 1
FEATURE [Part::Part2DObjectPython] Wire833  # Draft 2D object (typed FeaturePython)
  Area = 0
  ChamferSize = 0
  Closed = false
  End = (7390,5600,0)
  FilletRadius = 0
  Length = 2341.58
  MakeFace = true
  Placement = pos=(8310,7021.58,0) rot=(0,0,1;0rad)
  Points = (3) [(0,0,0),(-920,0,0),(-920,-1421.58,0)]
  Start = (8310,7021.58,0)
  Subdivisions = 0
FEATURE [Part::Part2DObjectPython] Wire835  # Draft 2D object (typed FeaturePython)
  Area = 0
  ChamferSize = 0
  Closed = true
  End = (7490,5800,0)
  FilletRadius = 0
  Length = 647.214
  MakeFace = false
  Placement = pos=(7390,5600,0) rot=(0,0,1;0rad)
  Points = (3) [(0,0,0),(-100,200,0),(100,200,0)]
  Start = (7390,5600,0)
  Subdivisions = 0
FEATURE [Part::Part2DObjectPython] Rectangle3316  label="проём в перекрытии под фан.стояк002"  # Draft 2D object (typed FeaturePython)
  ChamferSize = 0
  Columns = 1
  FilletRadius = 0
  Height = 250
  Length = 150
  MakeFace = false
  Placement = pos=(4910,3805,0) rot=(0,0,1;0rad)
  Rows = 1
FEATURE [Part::FeaturePython] Structure360  label="Вентстояк вычитаемы объём 003"  # Arch/BIM 52 (typed FeaturePython)
  Base = -> Rectangle3316
  FaceMaker = 0
  GlobalId = 0eTNl8duH9Xv7LHx2JWCfz
  Height = 6000
  HorizontalArea = 37500
  IfcData = IfcUID=0eTNl8duH9Xv7LHx2JWCfz,attributes={"GlobalId": {"value": "0eTNl8duH9Xv7LHx2JWCfz"}},+1 more (map truncated)
  IfcType = 52
  Length = 0
  MoveBase = false
  MoveWithHost = false
  Nodes = (2) [(4985,3930,0),(4985,3930,6000)]
  NodesOffset = 0
  Normal = (0,0,0)
  PerimeterLength = 800
  Placement = pos=(0,0,-200) rot=(0,0,1;0rad)
  VerticalArea = 4800000
  Width = 100
FEATURE [Part::Cut] Cut048  label="ПНО-39-15 1шт. рез. (1)"
  Base = -> Extrude093
  Tool = -> Structure360
FEATURE [Part::Cut] Cut049  label="ПНО-39-12 1шт. рез. (3)"
  Base = -> Extrude094
  Tool = -> Structure360
FEATURE [App::FeaturePython] Dimension024  # Draft dimension (typed FeaturePython)
  Diameter = false
  Dimline = (9500,-1500,0)
  Direction = (0,0,0)
  Distance = 3260
  End = (12760,-2107.94,0)
  Normal = (0,0,1)
  Start = (9500,-2107.94,0)
FEATURE [Part::Part2DObjectPython] Circle121  label="Circle122"  # Draft 2D object (typed FeaturePython)
  Area = 0
  FirstAngle = 0
  LastAngle = 0
  MakeFace = false
  Placement = pos=(5000,3900,0) rot=(0,0,1;0rad)
  Radius = 55
FEATURE [TechDraw::DrawSVGTemplate] Template001
  EditableTexts = Лист=5; Номер=ИЖС-0000.0001
  Height = 297
  Orientation = 1
  Width = 420
FEATURE [App::MaterialObjectPython] Material  label="Wood"  # material (typed FeaturePython)
  Description = A standard construction wood
  Material = AuthorAndLicense=Wood-Generic,CardName=Wood-Generic,Color=(1.0, 0.8196078431372549, 0.0, 1.0),Density=700 kg/m^3,+10 more (map truncated)
  ProductURL = https://en.wikipedia.org/wiki/Wood
  Transparency = 0
FEATURE [Part::FeaturePython] Wall057  label="мауэрлат"  # Arch/BIM 166 (typed FeaturePython)
  Align = 0
  Area = 6018000
  Base = -> Rectangle2788
  BlockHeight = 0
  BlockLength = 0
  CountBroken = 0
  CountEntire = 0
  Face = 0
  GlobalId = 1B71KP0Y9AOfuyJlUXW0eC
  Height = 150
  HorizontalArea = 6.294e+06
  IfcData = IfcUID=1B71KP0Y9AOfuyJlUXW0eC; attributes={"GlobalId": {"value": "1B71KP0Y9AOfuyJlUXW0eC"}}
  IfcType = 166
  Joint = 0
  Length = 40120
  MakeBlocks = false
  Material = -> Material
  MoveBase = false
  MoveWithHost = false
  Normal = (0,0,0)
  Offset = 155
  OffsetFirst = 0
  OffsetSecond = 0
  PerimeterLength = 42560
  Placement = pos=(0,0,3633) rot=(0,0,1;0rad)
  PredefinedType = 0
  VerticalArea = 12588000
  Width = 150
FEATURE [Part::FeaturePython] Wall147  label="шпренгель 001"  # Arch/BIM 166 (typed FeaturePython)
  Additions = -> [Wall146]
  Align = 2
  Area = 75000
  Base = -> Line1228
  BlockHeight = 0
  BlockLength = 0
  CountBroken = 0
  CountEntire = 0
  Face = 0
  Height = 500
  HorizontalArea = 295000
  IfcType = 166
  Joint = 0
  Length = 150
  MakeBlocks = false
  MoveBase = false
  MoveWithHost = false
  Normal = (0,0,0)
  OffsetFirst = 0
  OffsetSecond = 0
  PerimeterLength = 500
  Placement = pos=(0,0,3260) rot=(0,0,1;0rad)
  PredefinedType = 0
  Subtractions = -> [Wall057]
  VerticalArea = 1120000
  Width = 100
FEATURE [Part::FeaturePython] Wall150  label="шпренгель 010"  # Arch/BIM 166 (typed FeaturePython)
  Additions = -> [Wall149]
  Align = 2
  Area = 75000
  Base = -> Line1229
  BlockHeight = 0
  BlockLength = 0
  CountBroken = 0
  CountEntire = 0
  Face = 0
  Height = 500
  HorizontalArea = 280000
  IfcType = 166
  Joint = 0
  Length = 150
  MakeBlocks = false
  MoveBase = false
  MoveWithHost = false
  Normal = (0,0,0)
  OffsetFirst = 0
  OffsetSecond = 0
  PerimeterLength = 500
  Placement = pos=(0,0,3260) rot=(0,0,1;0rad)
  PredefinedType = 0
  Subtractions = -> [Wall057]
  VerticalArea = 1.07e+06
  Width = 100
FEATURE [Part::FeaturePython] Wall153  label="шпренгель 011"  # Arch/BIM 166 (typed FeaturePython)
  Additions = -> [Wall152]
  Align = 2
  Area = 75000
  Base = -> Line1231
  BlockHeight = 0
  BlockLength = 0
  CountBroken = 0
  CountEntire = 0
  Face = 0
  Height = 500
  HorizontalArea = 280000
  IfcType = 166
  Joint = 0
  Length = 150
  MakeBlocks = false
  MoveBase = false
  MoveWithHost = false
  Normal = (0,0,0)
  OffsetFirst = 0
  OffsetSecond = 0
  PerimeterLength = 500
  Placement = pos=(0,0,3260) rot=(0,0,1;0rad)
  PredefinedType = 0
  Subtractions = -> [Wall057]
  VerticalArea = 1070000
  Width = 100
FEATURE [Part::FeaturePython] Wall156  label="шпренгель 012"  # Arch/BIM 166 (typed FeaturePython)
  Additions = -> [Wall155]
  Align = 2
  Area = 75000
  Base = -> Line1233
  BlockHeight = 0
  BlockLength = 0
  CountBroken = 0
  CountEntire = 0
  Face = 0
  Height = 500
  HorizontalArea = 280000
  IfcType = 166
  Joint = 0
  Length = 150
  MakeBlocks = false
  MoveBase = false
  MoveWithHost = false
  Normal = (0,0,0)
  OffsetFirst = 0
  OffsetSecond = 0
  PerimeterLength = 500
  Placement = pos=(0,0,3260) rot=(0,0,1;0rad)
  PredefinedType = 0
  Subtractions = -> [Wall057]
  VerticalArea = 1.07e+06
  Width = 100
FEATURE [App::GeometryPython] BuildingPart044  label="Шпренгельные стойки"  # Arch/BIM 52 (typed FeaturePython)
  Area = 300000
  Group = -> [Wall147,Wall153,Wall156,Wall150]
  Height = 0
  HeightPropagate = true
  IfcData = complex_attributes={"OwnerHistory": {}, "IsNestedBy": {}, "IsDecomposedBy": {}, "IsDefinedBy": {}, "ObjectPlacement": {}, "Representation":... (+4 chars omitted)
  IfcType = 52
  LevelOffset = 0
FEATURE [App::MaterialObjectPython] Material001  label="Concrete"  # material (typed FeaturePython)
  Description = A standard C-25 construction concrete
  Material = AuthorAndLicense=Concrete-Generic,CardName=Concrete-Generic,Color=(0.47058823529411764, 0.4627450980392157, 0.4627450980392157, 1.0),+13 more (map truncated)
  ProductURL = https://en.wikipedia.org/wiki/Concrete
  StandardCode = Masterformat 03 33 13
  Transparency = 50
FEATURE [Part::FeaturePython] Structure030  label="блок утеплителя 60*10*20 001"  # Arch/BIM 7 (typed FeaturePython)
  FaceMaker = 0
  Height = 200
  HorizontalArea = 60000
  IfcType = 7
  Length = 600
  Material = -> Material001
  MoveBase = false
  MoveWithHost = false
  Nodes = (2) [(0,0,-3.88578e-16),(0,0,600)]
  NodesOffset = 0
  Normal = (0,0,0)
  PerimeterLength = 1400
  Placement = pos=(-175,9700,-280) rot=(0,0,1;0rad)
  PredefinedType = 0
  VerticalArea = 280000
  Width = 100
FEATURE [Part::FeaturePython] Array  label="массив утепления 001"  # Draft array (typed FeaturePython)
  Angle = 360
  ArrayType = 0
  Axis = (0,0,1)
  Base = -> Structure030
  Center = (0,0,0)
  Fuse = false
  IntervalAxis = (0,0,0)
  IntervalX = (765,0,0)
  IntervalY = (0,1,0)
  IntervalZ = (0,0,1)
  NumberPolar = 1
  NumberX = 18
  NumberY = 1
  NumberZ = 1
FEATURE [Part::FeaturePython] Structure031  label="блок утеплителя 60*10*20 002"  # Arch/BIM 7 (typed FeaturePython)
  FaceMaker = 0
  Height = 200
  HorizontalArea = 60000
  IfcType = 7
  Length = 600
  Material = -> Material001
  MoveBase = false
  MoveWithHost = false
  Nodes = (2) [(0,0,-3.88578e-16),(0,0,600)]
  NodesOffset = 0
  Normal = (0,0,0)
  PerimeterLength = 1400
  Placement = pos=(-180,-90,-280) rot=(0,0,1;0rad)
  PredefinedType = 0
  VerticalArea = 280000
  Width = 100
FEATURE [Part::FeaturePython] Array010  label="массив утепления 010"  # Draft array (typed FeaturePython)
  Angle = 360
  ArrayType = 0
  Axis = (0,0,1)
  Base = -> Structure031
  Center = (0,0,0)
  Fuse = false
  IntervalAxis = (0,0,0)
  IntervalX = (765,0,0)
  IntervalY = (0,1,0)
  IntervalZ = (0,0,1)
  NumberPolar = 1
  NumberX = 18
  NumberY = 1
  NumberZ = 1
FEATURE [Part::FeaturePython] Structure032  label="блок утеплителя 60*10*20 003"  # Arch/BIM 7 (typed FeaturePython)
  FaceMaker = 0
  Height = 200
  HorizontalArea = 60000
  IfcType = 7
  Length = 100
  Material = -> Material001
  MoveBase = false
  MoveWithHost = false
  Nodes = (2) [(-1.94289e-16,5.68434e-15,0),(-1.94289e-16,5.68434e-15,200)]
  NodesOffset = 0
  Normal = (0,0,0)
  PerimeterLength = 1400
  Placement = pos=(-350,375,-380) rot=(0,0,1;0rad)
  PredefinedType = 0
  VerticalArea = 280000
  Width = 600
FEATURE [Part::FeaturePython] Array011  label="массив утепления 011"  # Draft array (typed FeaturePython)
  Angle = 360
  ArrayType = 0
  Axis = (0,0,1)
  Base = -> Structure032
  Center = (0,0,0)
  Fuse = false
  IntervalAxis = (0,0,0)
  IntervalX = (0,0,0)
  IntervalY = (0,740,0)
  IntervalZ = (0,0,1)
  NumberPolar = 1
  NumberX = 1
  NumberY = 13
  NumberZ = 1
FEATURE [Part::FeaturePython] Structure033  label="блок утеплителя 60*10*20 004"  # Arch/BIM 7 (typed FeaturePython)
  FaceMaker = 0
  Height = 200
  HorizontalArea = 60000
  IfcType = 7
  Length = 100
  Material = -> Material001
  MoveBase = false
  MoveWithHost = false
  Nodes = (2) [(-1.94289e-16,5.68434e-15,0),(-1.94289e-16,5.68434e-15,200)]
  NodesOffset = 0
  Normal = (0,0,0)
  PerimeterLength = 1400
  Placement = pos=(13600,375,-380) rot=(0,0,1;0rad)
  PredefinedType = 0
  VerticalArea = 280000
  Width = 600
FEATURE [Part::FeaturePython] Array012  label="массив утепления 012"  # Draft array (typed FeaturePython)
  Angle = 360
  ArrayType = 0
  Axis = (0,0,1)
  Base = -> Structure033
  Center = (0,0,0)
  Fuse = false
  IntervalAxis = (0,0,0)
  IntervalX = (0,0,0)
  IntervalY = (0,740,0)
  IntervalZ = (0,0,1)
  NumberPolar = 1
  NumberX = 1
  NumberY = 13
  NumberZ = 1
FEATURE [App::GeometryPython] BuildingPart013  label="Утеплитель полки облицовки"  # Arch/BIM 52 (typed FeaturePython)
  Area = 0
  Group = -> [Array,Array010,Array011,Array012]
  Height = 0
  HeightPropagate = true
  IfcData = complex_attributes={"OwnerHistory": {}, "IsNestedBy": {}, "IsDecomposedBy": {}, "IsDefinedBy": {}, "ObjectPlacement": {}, "Representation":... (+4 chars omitted)
  IfcType = 52
  LevelOffset = 0
FEATURE [Part::FeaturePython] Structure047  label="Плоскость стропила"  # Arch/BIM 7 (typed FeaturePython)
  FaceMaker = 0
  Height = 5000
  HorizontalArea = 600000
  IfcType = 7
  Length = 12000
  Material = -> Material001
  MoveBase = false
  MoveWithHost = false
  Nodes = (2) [(0,1.81899e-16,-8.88178e-15),(0,1.81899e-16,14000)]
  NodesOffset = 0
  Normal = (0,0,0)
  PerimeterLength = 24100
  Placement = pos=(25,-2493.54,4500) rot=(0,0,1;1.5708rad)
  PredefinedType = 0
  VerticalArea = 120500000
  Width = 50
FEATURE [Part::FeaturePython] Structure052  label="Плоскость стропила001"  # Arch/BIM 7 (typed FeaturePython)
  FaceMaker = 0
  Height = 5000
  HorizontalArea = 850000
  IfcType = 7
  Length = 17000
  Material = -> Material001
  MoveBase = false
  MoveWithHost = false
  Nodes = (2) [(0,1.81899e-16,-8.88178e-15),(0,1.81899e-16,17000)]
  NodesOffset = 0
  Normal = (0,0,0)
  PerimeterLength = 34100
  Placement = pos=(-2000,25,4500) rot=(0,0,1;0rad)
  PredefinedType = 0
  VerticalArea = 170500000
  Width = 50
FEATURE [Part::FeaturePython] Array013  # Draft array (typed FeaturePython)
  Angle = 360
  ArrayType = 0
  Axis = (0,0,1)
  Base = -> Structure047
  Center = (0,0,0)
  Fuse = false
  IntervalAxis = (0,0,0)
  IntervalX = (630,0,0)
  IntervalY = (0,1,0)
  IntervalZ = (0,0,1)
  NumberPolar = 1
  NumberX = 22
  NumberY = 1
  NumberZ = 1
  Placement = pos=(-380,-5.457e-12,0) rot=(0,0,1;0rad)
FEATURE [Part::FeaturePython] Array014  # Draft array (typed FeaturePython)
  Angle = 360
  ArrayType = 0
  Axis = (0,0,1)
  Base = -> Structure052
  Center = (0,0,0)
  Fuse = false
  IntervalAxis = (0,0,0)
  IntervalX = (1,0,0)
  IntervalY = (0,625,0)
  IntervalZ = (0,0,1)
  NumberPolar = 1
  NumberX = 1
  NumberY = 14
  NumberZ = 1
  Placement = pos=(0,-360,0) rot=(0,0,1;0rad)
FEATURE [Part::MultiCommon] Common023  label="Стропилка_002"
  Shapes = -> [Array013,Common022]
FEATURE [Part::MultiCommon] Common025  label="Стропилка_003"
  Shapes = -> [Common024,Array014]
FEATURE [Part::MultiCommon] Common027  label="Стропилка_004"
  Shapes = -> [Common026,Array014]
FEATURE [Part::MultiCommon] Common029  label="Стойки 001"
  Shapes = -> [Cut,Array013]
FEATURE [Part::MultiCommon] Common030  label="Стойки 002"
  Shapes = -> [Cut,Array014]
FEATURE [Part::Cut] Cut024
  Base = -> Common023
  Tool = -> Wall145
FEATURE [Part::Cut] Cut025  label="Стропила 002"
  Base = -> Cut024
  Tool = -> Wall057
FEATURE [Part::Cut] Cut026
  Base = -> Common025
  Tool = -> Wall145
FEATURE [Part::Cut] Cut027  label="Стропила 003"
  Base = -> Cut026
  Tool = -> Wall057
FEATURE [Part::Cut] Cut028
  Base = -> Common027
  Tool = -> Wall145
FEATURE [Part::Cut] Cut029  label="Стропила 004"
  Base = -> Cut028
  Tool = -> Wall057
FEATURE [Part::FeaturePython] Wall176  label="фундамент МЗЛФ"  # Arch/BIM 166 (typed FeaturePython)
  Additions = -> [Wall130,Wall175,Wall038,Wall184]
  Align = 0
  Area = 8884000
  Base = -> Rectangle
  BlockHeight = 0
  BlockLength = 0
  CountBroken = 0
  CountEntire = 0
  Face = 0
  Height = 200
  HorizontalArea = 0
  IfcType = 166
  Joint = 0
  Length = 44420
  MakeBlocks = false
  MoveBase = false
  MoveWithHost = false
  Normal = (0,0,-1)
  OffsetFirst = 0
  OffsetSecond = 0
  PerimeterLength = 0
  Placement = pos=(0,0,-180) rot=(0,0,1;0rad)
  PredefinedType = 0
  Subtractions = -> [Array,Array010,Array011,Array012]
  VerticalArea = 0
  Width = 520
FEATURE [App::GeometryPython] BuildingPart012  label="Фундамент МЗЛФ в сборе"  # Arch/BIM 52 (typed FeaturePython)
  Area = 51616000
  Group = -> [Wall046,Wall047,BuildingPart013,Wall163,Wall176]
  Height = 0
  HeightPropagate = true
  IfcData = complex_attributes={"OwnerHistory": {}, "IsNestedBy": {}, "IsDecomposedBy": {}, "IsDefinedBy": {}, "ObjectPlacement": {}, "Representation":... (+4 chars omitted)
  IfcType = 52
  LevelOffset = 0
FEATURE [App::GeometryPython] BuildingPart010  label="Фундамент и основание"  # Arch/BIM 14 (typed FeaturePython)
  Area = 51616000
  CompositionType = 0
  Elevation = 0
  Group = -> [BuildingPart012]
  Height = 0
  HeightPropagate = true
  IfcData = attributes={"Elevation": {"value": 0.0}}
  IfcType = 14
  LevelOffset = 0
  LongName = Фундамент и основание
  expr: Elevation = .Placement.Base.z
FEATURE [Part::MultiCommon] Common031  label="Кобылки 001"
  Placement = pos=(50,0,0) rot=(0,0,1;0rad)
  Shapes = -> [Roof014,Array013]
FEATURE [Part::MultiCommon] Common032  label="Кобылки 002"
  Placement = pos=(0,50,0) rot=(0,0,1;0rad)
  Shapes = -> [Roof014,Array014]
FEATURE [Part::Cut] Cut035  label="Стропила 003_001"
  Base = -> Cut027
  Tool = -> Structure155
FEATURE [App::GeometryPython] BuildingPart018  label="Стропильная система"  # Arch/BIM 52 (typed FeaturePython)
  Area = 3.746e+06
  Group = -> [BuildingPart044,Common028,Wall064,Common029,Common030,Cut025,Cut029,Wall145,Common031,Common032,Cut035]
  Height = 0
  HeightPropagate = true
  IfcData = complex_attributes={"OwnerHistory": {}, "IsNestedBy": {}, "IsDecomposedBy": {}, "IsDefinedBy": {}, "ObjectPlacement": {}, "Representation":... (+4 chars omitted)
  IfcType = 52
  LevelOffset = 0
FEATURE [App::GeometryPython] BuildingPart007  label="Чердак и кровля"  # Arch/BIM 14 (typed FeaturePython)
  Area = 3.746e+06
  CompositionType = 0
  Elevation = 0
  Group = -> [BuildingPart018]
  Height = 0
  HeightPropagate = true
  IfcData = attributes={"Elevation": {"value": 0.0}}
  IfcType = 14
  LevelOffset = 0
  LongName = Чердак и кровля
  expr: Elevation = .Placement.Base.z
FEATURE [App::GeometryPython] BuildingPart019  label="Ненужное"  # Arch/BIM 52 (typed FeaturePython)
  Area = 55362000
  Group = -> [Structure044,BuildingPart015,BuildingPart035,BuildingPart007,BuildingPart010]
  Height = 0
  HeightPropagate = true
  IfcData = complex_attributes={"OwnerHistory": {}, "IsNestedBy": {}, "IsDecomposedBy": {}, "IsDefinedBy": {}, "ObjectPlacement": {}, "Representation":... (+4 chars omitted)
  IfcType = 52
  LevelOffset = 0
FEATURE [Part::FeaturePython] Structure368  label="Стяжка тёплого пола  80 мм 001"  # Arch/BIM 52 (typed FeaturePython)
  Base = -> Rectangle2169
  FaceMaker = 0
  GlobalId = 22FHYXjNfD0ge3TUS_JU1i
  Height = 80
  HorizontalArea = 430500
  IfcData = IfcUID=22FHYXjNfD0ge3TUS_JU1i,attributes={"GlobalId": {"value": "22FHYXjNfD0ge3TUS_JU1i"}},+1 more (map truncated)
  IfcType = 52
  Length = 0
  Material = -> Material001
  MoveBase = false
  MoveWithHost = false
  Nodes = (2) [(6195,-230,0),(6195,-230,80)]
  NodesOffset = 0
  Normal = (0,0,1)
  PerimeterLength = 2920
  Placement = pos=(0,0,-100) rot=(0,0,1;0rad)
  VerticalArea = 233600
  Width = 100
FEATURE [Part::FeaturePython] Structure371  label="Стяжка тёплого пола  80 мм 008"  # Arch/BIM 52 (typed FeaturePython)
  Base = -> Rectangle3079
  FaceMaker = 0
  GlobalId = 1aGZ9vCCD9wP_BshGDICol
  Height = 80
  HorizontalArea = 803600
  IfcData = IfcUID=1aGZ9vCCD9wP_BshGDICol,attributes={"GlobalId": {"value": "1aGZ9vCCD9wP_BshGDICol"}},+1 more (map truncated)
  IfcType = 52
  Length = 0
  Material = -> Material001
  MoveBase = false
  MoveWithHost = false
  Nodes = (2) [(4000,4250,0),(4000,4250,100)]
  NodesOffset = 0
  Normal = (0,0,1)
  PerimeterLength = 4740
  Placement = pos=(0,0,-100) rot=(0,0,1;0rad)
  VerticalArea = 379200
  Width = 100
FEATURE [Part::FeaturePython] Structure374  label="покрытие пола 20мм 001"  # Arch/BIM 52 (typed FeaturePython)
  Base = -> Rectangle2169
  FaceMaker = 0
  GlobalId = 2zjFlxA7P7zeUfdNFV2euI
  Height = 20
  HorizontalArea = 430500
  IfcData = IfcUID=2zjFlxA7P7zeUfdNFV2euI,attributes={"GlobalId": {"value": "2zjFlxA7P7zeUfdNFV2euI"}},+1 more (map truncated)
  IfcType = 52
  Length = 0
  Material = -> Material001
  MoveBase = false
  MoveWithHost = false
  Nodes = (2) [(6195,-230,0),(6195,-230,20)]
  NodesOffset = 0
  Normal = (0,0,1)
  PerimeterLength = 2920
  Placement = pos=(0,0,-20) rot=(0,0,1;0rad)
  VerticalArea = 58400
  Width = 20
FEATURE [Part::FeaturePython] Structure377  label="покрытие пола 20мм 003"  # Arch/BIM 52 (typed FeaturePython)
  Base = -> Rectangle3079
  FaceMaker = 0
  GlobalId = 2T3KnpypPEbv6OyL_zSjC5
  Height = 20
  HorizontalArea = 803600
  IfcData = IfcUID=2T3KnpypPEbv6OyL_zSjC5,attributes={"GlobalId": {"value": "2T3KnpypPEbv6OyL_zSjC5"}},+1 more (map truncated)
  IfcType = 52
  Length = 0
  Material = -> Material001
  MoveBase = false
  MoveWithHost = false
  Nodes = (2) [(4000,4250,0),(4000,4250,100)]
  NodesOffset = 0
  Normal = (0,0,1)
  PerimeterLength = 4740
  Placement = pos=(0,0,-20) rot=(0,0,1;0rad)
  VerticalArea = 94800
  Width = 20
FEATURE [App::MaterialObjectPython] Material002  label="XPS"  # material (typed FeaturePython)
  Description = XPS
  Material = AuthorAndLicense=ABS-Generic,CardName=ABS-Generic,Color=(0.9411764705882353, 0.5450980392156862, 0.5686274509803921, 1.0),Density=1060 kg/m^3,+15 more (map truncated)
  Transparency = 0
FEATURE [Part::FeaturePython] Structure066  label="утепление пола в проёмах XPS 100mm 001"  # Arch/BIM 52 (typed FeaturePython)
  Base = -> Rectangle3079
  FaceMaker = 0
  GlobalId = 3EKnpUeW1ADw6RKJbe9Fmo
  Height = 100
  HorizontalArea = 803600
  IfcData = IfcUID=3EKnpUeW1ADw6RKJbe9Fmo,attributes={"GlobalId": {"value": "3EKnpUeW1ADw6RKJbe9Fmo"}},+1 more (map truncated)
  IfcType = 52
  Length = 0
  Material = -> Material002
  MoveBase = false
  MoveWithHost = false
  Nodes = (2) [(4000,4250,0),(4000,4250,100)]
  NodesOffset = 0
  Normal = (0,0,1)
  PerimeterLength = 4740
  Placement = pos=(0,0,-200) rot=(0,0,1;0rad)
  VerticalArea = 474000
  Width = 100
FEATURE [Part::FeaturePython] Structure069  label="утепление пола в проёмах XPS 100mm 002"  # Arch/BIM 52 (typed FeaturePython)
  Base = -> Rectangle2169
  FaceMaker = 0
  GlobalId = 3Shc3AjDz99AkEi1PjraMs
  Height = 100
  HorizontalArea = 430500
  IfcData = IfcUID=3Shc3AjDz99AkEi1PjraMs,attributes={"GlobalId": {"value": "3Shc3AjDz99AkEi1PjraMs"}},+1 more (map truncated)
  IfcType = 52
  Length = 0
  Material = -> Material002
  MoveBase = false
  MoveWithHost = false
  Nodes = (2) [(6195,-230,0),(6195,-230,100)]
  NodesOffset = 0
  Normal = (0,0,1)
  PerimeterLength = 2920
  Placement = pos=(0,0,-200) rot=(0,0,1;0rad)
  VerticalArea = 292000
  Width = 100
FEATURE [Part::FeaturePython] Wall249  label="XPS 80mm в уровне армпояса"  # Arch/BIM 166 (typed FeaturePython)
  Align = 0
  Area = 5647600
  Base = -> Rectangle016
  BlockHeight = 231
  BlockLength = 1200
  CountBroken = 33
  CountEntire = 0
  Face = 0
  GlobalId = 0S$ta$Atf7kQfUAIRZ7neI
  Height = 140
  HorizontalArea = 0
  IfcData = IfcUID=0S$ta$Atf7kQfUAIRZ7neI; attributes={"GlobalId": {"value": "0S$ta$Atf7kQfUAIRZ7neI"}}
  IfcType = 166
  Joint = 0
  Length = 40340
  MakeBlocks = true
  Material = -> Material002
  MoveBase = false
  MoveWithHost = false
  Normal = (0,0,1)
  Offset = 300
  OffsetFirst = 0
  OffsetSecond = 0
  PerimeterLength = 0
  Placement = pos=(0,0,3493) rot=(0,0,1;0rad)
  PredefinedType = 0
  VerticalArea = 0
  Width = 80
FEATURE [Part::FeaturePython] Wall259  label="Утепление торца плит XPS 80mm 002"  # Arch/BIM 166 (typed FeaturePython)
  Align = 0
  Area = 2915220
  Base = -> Line1430
  BlockHeight = 231
  BlockLength = 1200
  CountBroken = 1
  CountEntire = 10
  Face = 0
  GlobalId = 1ibByTMrr7TuIBXHnohxoK
  Height = 231
  HorizontalArea = 0
  IfcData = IfcUID=1ibByTMrr7TuIBXHnohxoK,+2 more (map truncated)
  IfcType = 166
  Joint = 0
  Length = 12620
  MakeBlocks = true
  Material = -> Material002
  MoveBase = false
  MoveWithHost = false
  Normal = (0,0,0)
  OffsetFirst = 0
  OffsetSecond = 0
  PerimeterLength = 0
  Placement = pos=(5.68e-14,0,2800) rot=(0,0,1;0rad)
  PredefinedType = 0
  VerticalArea = 0
  Width = 80
FEATURE [Part::FeaturePython] Wall260  label="Утепление торца плит XPS 80mm 001"  # Arch/BIM 166 (typed FeaturePython)
  Align = 0
  Area = 2915220
  Base = -> Line1431
  BlockHeight = 231
  BlockLength = 1200
  CountBroken = 1
  CountEntire = 10
  Face = 0
  GlobalId = 1LI82ViEn62R_6CNpLHhhT
  Height = 231
  HorizontalArea = 0
  IfcData = IfcUID=1LI82ViEn62R_6CNpLHhhT,+2 more (map truncated)
  IfcType = 166
  Joint = 0
  Length = 12620
  MakeBlocks = true
  Material = -> Material002
  MoveBase = false
  MoveWithHost = false
  Normal = (0,0,0)
  OffsetFirst = 0
  OffsetSecond = 0
  PerimeterLength = 0
  Placement = pos=(5.68e-14,0,2800) rot=(0,0,1;0rad)
  PredefinedType = 0
  VerticalArea = 0
  Width = 80
FEATURE [App::MaterialObjectPython] Material003  label="Red brick"  # material (typed FeaturePython)
  Description = A standard red brick
  Material = AuthorAndLicense=Concrete-Generic,CardName=Concrete-Generic,Color=(0.788235294117647, 0.2980392156862745, 0.18823529411764706, 1.0),+11 more (map truncated)
  Transparency = 0
FEATURE [Part::FeaturePython] Wall120  label="Перемычка облицовки 014"  # Arch/BIM 166 (typed FeaturePython)
  Align = 2
  Area = 1379700
  Base = -> Line1187
  BlockHeight = 250
  BlockLength = 64.2
  CountBroken = 53
  CountEntire = 49
  Face = 0
  GlobalId = 2CDkG$u1H6yg879o_wXiaT
  Height = 365
  HorizontalArea = 0
  IfcData = IfcUID=2CDkG$u1H6yg879o_wXiaT; attributes={"GlobalId": {"value": "2CDkG$u1H6yg879o_wXiaT"}}
  IfcType = 166
  Joint = 10
  Length = 3780
  MakeBlocks = true
  Material = -> Material003
  MoveBase = false
  MoveWithHost = false
  Normal = (0,0,1)
  OffsetFirst = 0
  OffsetSecond = 0
  PerimeterLength = 0
  Placement = pos=(0,0,2510) rot=(0,0,1;0rad)
  PredefinedType = 0
  VerticalArea = 0
  Width = 10
FEATURE [Part::FeaturePython] Wall121  label="Перемычка облицовки 015"  # Arch/BIM 166 (typed FeaturePython)
  Align = 2
  Area = 1522050
  Base = -> Line1186
  BlockHeight = 250
  BlockLength = 65.8
  CountBroken = 57
  CountEntire = 53
  Face = 0
  GlobalId = 3Y7MnwAmX628ZvBXKl4dyB
  Height = 365
  HorizontalArea = 0
  IfcData = IfcUID=3Y7MnwAmX628ZvBXKl4dyB; attributes={"GlobalId": {"value": "3Y7MnwAmX628ZvBXKl4dyB"}}
  IfcType = 166
  Joint = 10
  Length = 4170
  MakeBlocks = true
  Material = -> Material003
  MoveBase = false
  MoveWithHost = false
  Normal = (0,0,1)
  OffsetFirst = 0
  OffsetSecond = 0
  PerimeterLength = 0
  Placement = pos=(0,0,2510) rot=(0,0,1;0rad)
  PredefinedType = 0
  VerticalArea = 0
  Width = 10
FEATURE [Part::FeaturePython] Wall123  label="Перемычка облицовки 017"  # Arch/BIM 166 (typed FeaturePython)
  Align = 2
  Area = 288350
  Base = -> Line1184
  BlockHeight = 250
  BlockLength = 68
  CountBroken = 12
  CountEntire = 8
  Face = 0
  GlobalId = 3lCsDqyJL5KvboFIYAEUQo
  Height = 365
  HorizontalArea = 0
  IfcData = IfcUID=3lCsDqyJL5KvboFIYAEUQo; attributes={"GlobalId": {"value": "3lCsDqyJL5KvboFIYAEUQo"}}
  IfcType = 166
  Joint = 10
  Length = 790
  MakeBlocks = true
  Material = -> Material003
  MoveBase = false
  MoveWithHost = false
  Normal = (0,0,1)
  OffsetFirst = 0
  OffsetSecond = 0
  PerimeterLength = 0
  Placement = pos=(0,0,2285) rot=(0,0,1;0rad)
  PredefinedType = 0
  VerticalArea = 0
  Width = 10
FEATURE [Part::FeaturePython] Wall124  label="Перемычка облицовки 018"  # Arch/BIM 166 (typed FeaturePython)
  Align = 2
  Area = 288350
  Base = -> Line1191
  BlockHeight = 250
  BlockLength = 68
  CountBroken = 12
  CountEntire = 8
  Face = 0
  GlobalId = 07ToIk0b17KwOPIvB7CAEx
  Height = 365
  HorizontalArea = 0
  IfcData = IfcUID=07ToIk0b17KwOPIvB7CAEx; attributes={"GlobalId": {"value": "07ToIk0b17KwOPIvB7CAEx"}}
  IfcType = 166
  Joint = 10
  Length = 790
  MakeBlocks = true
  Material = -> Material003
  MoveBase = false
  MoveWithHost = false
  Normal = (0,0,1)
  OffsetFirst = 0
  OffsetSecond = 0
  PerimeterLength = 0
  Placement = pos=(0,0,2285) rot=(0,0,1;0rad)
  PredefinedType = 0
  VerticalArea = 0
  Width = 10
FEATURE [Part::FeaturePython] Wall159  label="Перемычка облицовки 019"  # Arch/BIM 166 (typed FeaturePython)
  Align = 2
  Area = 573050
  Base = -> Line1266
  BlockHeight = 250
  BlockLength = 65
  CountBroken = 23
  CountEntire = 19
  Face = 0
  GlobalId = 0T7dyAI05B38PZhXyjg8rR
  Height = 365
  HorizontalArea = 0
  IfcData = IfcUID=0T7dyAI05B38PZhXyjg8rR; attributes={"GlobalId": {"value": "0T7dyAI05B38PZhXyjg8rR"}}
  IfcType = 166
  Joint = 10
  Length = 1570
  MakeBlocks = true
  Material = -> Material003
  MoveBase = false
  MoveWithHost = false
  Normal = (0,0,1)
  OffsetFirst = 0
  OffsetSecond = 0
  PerimeterLength = 0
  Placement = pos=(0,0,2510) rot=(0,0,1;0rad)
  PredefinedType = 0
  VerticalArea = 0
  Width = 10
FEATURE [App::GeometryPython] BuildingPart038  label="Перемычки облицовки 1nf"  # Arch/BIM 52 (typed FeaturePython)
  Area = 4.0515e+06
  GlobalId = 0KtQz4WtXFJO7H9uDU_qkV
  Group = -> [Wall120,Wall121,Wall123,Wall124,Wall159]
  Height = 0
  HeightPropagate = true
  IfcData = IfcUID=0KtQz4WtXFJO7H9uDU_qkV,attributes={"GlobalId": {"value": "0KtQz4WtXFJO7H9uDU_qkV"}},+1 more (map truncated)
  IfcType = 52
  LevelOffset = 0
FEATURE [Part::FeaturePython] Wall215  label="Ряд 1нф по плитам ПНО 001"  # Arch/BIM 166 (typed FeaturePython)
  Align = 0
  Area = 820300
  Base = -> Line1430
  BlockHeight = 65
  BlockLength = 260
  CountBroken = 2
  CountEntire = 48
  Face = 0
  GlobalId = 0Kxc8b9mX0hhA4A11jgaug
  Height = 65
  HorizontalArea = 0
  IfcData = IfcUID=0Kxc8b9mX0hhA4A11jgaug,+2 more (map truncated)
  IfcType = 166
  Joint = 0
  Length = 12620
  MakeBlocks = true
  Material = -> Material003
  MoveBase = false
  MoveWithHost = false
  Normal = (0,0,0)
  Offset = 210
  OffsetFirst = 120
  OffsetSecond = 0
  PerimeterLength = 0
  Placement = pos=(0,0,2963) rot=(0,0,1;0rad)
  PredefinedType = 0
  VerticalArea = 0
  Width = 170
FEATURE [Part::FeaturePython] Wall245  label="Стена 3 ряда 1NF в уровне перекрытия 001"  # Arch/BIM 166 (typed FeaturePython)
  Align = 0
  Area = 2915220
  Base = -> Line1430
  BlockHeight = 65
  BlockLength = 250
  CountBroken = 6
  CountEntire = 141
  Face = 0
  GlobalId = 3KlxKDIJjA7Q82FRbrh_9n
  Height = 231
  HorizontalArea = 0
  IfcData = IfcUID=3KlxKDIJjA7Q82FRbrh_9n,+2 more (map truncated)
  IfcType = 166
  Joint = 12
  Length = 12620
  MakeBlocks = true
  Material = -> Material003
  MoveBase = false
  MoveWithHost = false
  Normal = (0,0,0)
  Offset = 85
  OffsetFirst = 65
  OffsetSecond = 200
  PerimeterLength = 0
  Placement = pos=(5.68e-14,0,2805) rot=(0,0,1;0rad)
  PredefinedType = 0
  VerticalArea = 0
  Width = 120
FEATURE [Part::FeaturePython] Wall246  label="Стена 3 ряда 1NF в уровне перекрытия 002"  # Arch/BIM 166 (typed FeaturePython)
  Align = 0
  Area = 2915220
  Base = -> Line1431
  BlockHeight = 65
  BlockLength = 250
  CountBroken = 6
  CountEntire = 141
  Face = 0
  GlobalId = 2jFZMiwejFCvBCF1MAHti2
  Height = 231
  HorizontalArea = 0
  IfcData = IfcUID=2jFZMiwejFCvBCF1MAHti2,+2 more (map truncated)
  IfcType = 166
  Joint = 12
  Length = 12620
  MakeBlocks = true
  Material = -> Material003
  MoveBase = false
  MoveWithHost = false
  Normal = (0,0,0)
  Offset = 85
  OffsetFirst = 65
  OffsetSecond = 200
  PerimeterLength = 0
  Placement = pos=(5.68e-14,0,2805) rot=(0,0,1;0rad)
  PredefinedType = 0
  VerticalArea = 0
  Width = 120
FEATURE [Part::FeaturePython] Wall247  label="Ряд 1нф по плитам ПНО 002"  # Arch/BIM 166 (typed FeaturePython)
  Align = 0
  Area = 820300
  Base = -> Line1431
  BlockHeight = 65
  BlockLength = 260
  CountBroken = 2
  CountEntire = 48
  Face = 0
  GlobalId = 33o6NID0r8NOJAPg0rbzr4
  Height = 65
  HorizontalArea = 0
  IfcData = IfcUID=33o6NID0r8NOJAPg0rbzr4,+2 more (map truncated)
  IfcType = 166
  Joint = 0
  Length = 12620
  MakeBlocks = true
  Material = -> Material003
  MoveBase = false
  MoveWithHost = false
  Normal = (0,0,0)
  Offset = 210
  OffsetFirst = 120
  OffsetSecond = 0
  PerimeterLength = 0
  Placement = pos=(0,0,2963) rot=(0,0,1;0rad)
  PredefinedType = 0
  VerticalArea = 0
  Width = 170
FEATURE [Part::FeaturePython] Wall248  label="ряд  2.1нф в уровне армпояса"  # Arch/BIM 166 (typed FeaturePython)
  Align = 0
  Area = 5647600
  Base = -> Rectangle016
  BlockHeight = 140
  BlockLength = 260
  CountBroken = 4
  CountEntire = 149
  Face = 0
  GlobalId = 3OBRES97PB8f6_bWU2_YT7
  Height = 140
  HorizontalArea = 4898400
  IfcData = IfcUID=3OBRES97PB8f6_bWU2_YT7; attributes={"GlobalId": {"value": "3OBRES97PB8f6_bWU2_YT7"}}
  IfcType = 166
  Joint = 0
  Length = 40340
  MakeBlocks = false
  Material = -> Material003
  MoveBase = false
  MoveWithHost = false
  Normal = (0,0,1)
  OffsetFirst = 0
  OffsetSecond = 0
  PerimeterLength = 41300
  Placement = pos=(0,0,3493) rot=(0,0,1;0rad)
  PredefinedType = 0
  VerticalArea = 11429600
  Width = 120
FEATURE [Part::FeaturePython] Wall255  label="облицовка ВШ  001"  # Arch/BIM 166 (typed FeaturePython)
  Align = 0
  Area = 1520000
  Base = -> Line1468
  BlockHeight = 65
  BlockLength = 250
  CountBroken = 55
  CountEntire = 53
  Face = 0
  GlobalId = 0NV5Z8QsLE8RP4h00TMdTp
  Height = 4000
  HorizontalArea = 45600
  IfcData = IfcUID=0NV5Z8QsLE8RP4h00TMdTp; attributes={"GlobalId": {"value": "0NV5Z8QsLE8RP4h00TMdTp"}}
  IfcType = 166
  Joint = 10
  Length = 380
  MakeBlocks = false
  Material = -> Material003
  MoveBase = false
  MoveWithHost = false
  Normal = (0,0,0)
  OffsetFirst = 120
  OffsetSecond = 250
  PerimeterLength = 1000
  Placement = pos=(0,0,2960) rot=(0,0,1;0rad)
  PredefinedType = 0
  VerticalArea = 4000000
  Width = 120
FEATURE [Part::FeaturePython] Wall256  label="облицовка ВШ  002"  # Arch/BIM 166 (typed FeaturePython)
  Align = 0
  Area = 1520000
  Base = -> Line1469
  BlockHeight = 65
  BlockLength = 250
  CountBroken = 55
  CountEntire = 53
  Face = 0
  GlobalId = 2TkovYGMD8r9zraP45mHkR
  Height = 4000
  HorizontalArea = 45600
  IfcData = IfcUID=2TkovYGMD8r9zraP45mHkR; attributes={"GlobalId": {"value": "2TkovYGMD8r9zraP45mHkR"}}
  IfcType = 166
  Joint = 10
  Length = 380
  MakeBlocks = false
  Material = -> Material003
  MoveBase = false
  MoveWithHost = false
  Normal = (0,0,0)
  OffsetFirst = 120
  OffsetSecond = 250
  PerimeterLength = 1000
  Placement = pos=(0,0,2960) rot=(0,0,1;0rad)
  PredefinedType = 0
  VerticalArea = 4000000
  Width = 120
FEATURE [Part::FeaturePython] Wall257  label="облицовка ВШ  003"  # Arch/BIM 166 (typed FeaturePython)
  Align = 0
  Area = 3600000
  Base = -> Line1470
  BlockHeight = 65
  BlockLength = 250
  CountBroken = 57
  CountEntire = 159
  Face = 0
  GlobalId = 0woF2TLZD1r929WxYa3eSK
  Height = 4000
  HorizontalArea = 108000
  IfcData = IfcUID=0woF2TLZD1r929WxYa3eSK; attributes={"GlobalId": {"value": "0woF2TLZD1r929WxYa3eSK"}}
  IfcType = 166
  Joint = 10
  Length = 900
  MakeBlocks = false
  Material = -> Material003
  MoveBase = false
  MoveWithHost = false
  Normal = (0,0,0)
  OffsetFirst = 250
  OffsetSecond = 120
  PerimeterLength = 2040
  Placement = pos=(0,0,2960) rot=(0,0,1;0rad)
  PredefinedType = 0
  VerticalArea = 8.16e+06
  Width = 120
FEATURE [Part::FeaturePython] Wall258  label="облицовка ВШ  004"  # Arch/BIM 166 (typed FeaturePython)
  Align = 0
  Area = 3600000
  Base = -> Line1471
  BlockHeight = 65
  BlockLength = 250
  CountBroken = 57
  CountEntire = 159
  Face = 0
  GlobalId = 0uV1Y0I5TBPurrni9deYxv
  Height = 4000
  HorizontalArea = 108000
  IfcData = IfcUID=0uV1Y0I5TBPurrni9deYxv; attributes={"GlobalId": {"value": "0uV1Y0I5TBPurrni9deYxv"}}
  IfcType = 166
  Joint = 10
  Length = 900
  MakeBlocks = false
  Material = -> Material003
  MoveBase = false
  MoveWithHost = false
  Normal = (0,0,0)
  OffsetFirst = 250
  OffsetSecond = 120
  PerimeterLength = 2040
  Placement = pos=(0,0,2960) rot=(0,0,1;0rad)
  PredefinedType = 0
  VerticalArea = 8.16e+06
  Width = 120
FEATURE [App::MaterialObjectPython] Material004  label="Ceramic block"  # material (typed FeaturePython)
  Description = A standard Ceramic block LSR TK380
  Material = AuthorAndLicense=Concrete-Generic,CardName=Concrete-Generic,Color=(0.8627450980392157, 0.5803921568627451, 0.13725490196078433, 1.0),+11 more (map truncated)
  Transparency = 0
FEATURE [Part::FeaturePython] Wall164  label="Стена ЛСР 380мм под мауэрлат"  # Arch/BIM 166 (typed FeaturePython)
  Align = 0
  Area = 18637080
  Base = -> Rectangle016
  BlockHeight = 231
  BlockLength = 0
  CountBroken = 0
  CountEntire = 0
  Face = 0
  GlobalId = 3z2ptnFFLDUOlhnj0g0DYP
  Height = 462
  HorizontalArea = 31813600
  IfcData = IfcUID=3z2ptnFFLDUOlhnj0g0DYP; attributes={"GlobalId": {"value": "3z2ptnFFLDUOlhnj0g0DYP"}}
  IfcType = 166
  Joint = 0
  Length = 40340
  MakeBlocks = true
  Material = -> Material004
  MoveBase = false
  MoveWithHost = false
  Normal = (0,0,1)
  OffsetFirst = 0
  OffsetSecond = 0
  PerimeterLength = 0
  Placement = pos=(0,0,3031) rot=(0,0,1;0rad)
  PredefinedType = 0
  VerticalArea = 38678640
  Width = 380
FEATURE [Part::FeaturePython] Wall242  label="Стена ЛСР 380мм ряд перекрытия 001"  # Arch/BIM 166 (typed FeaturePython)
  Align = 0
  Area = 1919610
  Base = -> Line1426
  BlockHeight = 231
  BlockLength = 255
  CountBroken = 1
  CountEntire = 32
  Face = 0
  GlobalId = 0JF6Mj3WnAXwUaXoCorPV_
  Height = 231
  HorizontalArea = 3157800
  IfcData = IfcUID=0JF6Mj3WnAXwUaXoCorPV_,+2 more (map truncated)
  IfcType = 166
  Joint = 0
  Length = 8310
  MakeBlocks = false
  Material = -> Material004
  MoveBase = false
  MoveWithHost = false
  Normal = (0,0,0)
  OffsetFirst = 0
  OffsetSecond = 0
  PerimeterLength = 17380
  Placement = pos=(5.68e-14,0,2800) rot=(0,0,1;0rad)
  PredefinedType = 0
  VerticalArea = 4014780
  Width = 380
FEATURE [Part::FeaturePython] Wall243  label="Стена ЛСР 380мм ряд перекрытия 002"  # Arch/BIM 166 (typed FeaturePython)
  Align = 1
  Area = 1919610
  Base = -> Line1427
  BlockHeight = 231
  BlockLength = 255
  CountBroken = 1
  CountEntire = 32
  Face = 0
  GlobalId = 25wehzmoL6BRnSZJd_gcHH
  Height = 231
  HorizontalArea = 3157800
  IfcData = IfcUID=25wehzmoL6BRnSZJd_gcHH,+2 more (map truncated)
  IfcType = 166
  Joint = 0
  Length = 8310
  MakeBlocks = false
  Material = -> Material004
  MoveBase = false
  MoveWithHost = false
  Normal = (0,0,0)
  OffsetFirst = 120
  OffsetSecond = 0
  PerimeterLength = 17380
  Placement = pos=(5.68e-14,0,2800) rot=(0,0,1;0rad)
  PredefinedType = 0
  VerticalArea = 4014780
  Width = 380
FEATURE [App::GeometryPython] BuildingPart082  label="Кладка в уровне перекрытия"  # Arch/BIM 52 (typed FeaturePython)
  Area = 17140700
  GlobalId = 1YWPLHYQvChhSjPeXmlyje
  Group = -> [Wall247,Wall242,Wall243,Wall245,Wall246,Wall215,Wall259,Wall260]
  Height = 0
  HeightPropagate = true
  IfcData = IfcUID=1YWPLHYQvChhSjPeXmlyje,+2 more (map truncated)
  IfcType = 52
  LevelOffset = 0
FEATURE [App::MaterialObjectPython] Material005  label="Wall ceramic plates"  # material (typed FeaturePython)
  Description = Wall ceramic plates
  Material = AuthorAndLicense=Concrete-Generic,CardName=Concrete-Generic,Color=(0.1450980392156863, 0.4745098039215686, 0.6980392156862745, 1.0),+11 more (map truncated)
  Transparency = 0
FEATURE [Part::FeaturePython] Wall240  label="Облицовка ванны плиткой 30мм"  # Arch/BIM 166 (typed FeaturePython)
  Align = 0
  Area = 3078000
  Base = -> Wire808
  BlockHeight = 0
  BlockLength = 0
  CountBroken = 0
  CountEntire = 0
  Face = 0
  GlobalId = 36KkLHJl1D_AUwy3AkMKZ7
  Height = 570
  HorizontalArea = 260000
  IfcData = IfcUID=36KkLHJl1D_AUwy3AkMKZ7,+2 more (map truncated)
  IfcType = 166
  Joint = 0
  Length = 5400
  MakeBlocks = false
  Material = -> Material005
  MoveBase = false
  MoveWithHost = false
  Normal = (0,0,0)
  OffsetFirst = 0
  OffsetSecond = 0
  PerimeterLength = 5400
  PredefinedType = 0
  VerticalArea = 5.928e+06
  Width = 50
FEATURE [App::MaterialObjectPython] Material006  label="Glass mate"  # material (typed FeaturePython)
  Description = Generic soda-lime glass
  Material = AuthorAndLicense=Glass-Generic,CardName=Glass-Generic,Color=(0.8, 0.8, 0.8, 1.0),Density=2520 kg/m^3,Description=Generic soda-lime glass,+12 more (map truncated)
  ProductURL = https://en.wikipedia.org/wiki/Soda-lime_glass
  Transparency = 80
FEATURE [Part::FeaturePython] Wall227  label="перегородка Glass 10mm"  # Arch/BIM 166 (typed FeaturePython)
  Align = 0
  Area = 220000
  Base = -> Line1381
  BlockHeight = 250
  BlockLength = 625
  CountBroken = 22
  CountEntire = 16
  Face = 0
  GlobalId = 1zF9$Lwlj2MA8WfKSv6nCa
  Height = 2200
  HorizontalArea = 1000
  IfcData = IfcUID=1zF9$Lwlj2MA8WfKSv6nCa; attributes={"GlobalId": {"value": "1zF9$Lwlj2MA8WfKSv6nCa"}}
  IfcType = 166
  Joint = 0
  Length = 100
  MakeBlocks = false
  Material = -> Material006
  MoveBase = false
  MoveWithHost = false
  Normal = (0,0,0)
  OffsetFirst = 300
  OffsetSecond = 50
  PerimeterLength = 220
  PredefinedType = 0
  VerticalArea = 484000
  Width = 10
FEATURE [Part::FeaturePython] Wall239  label="перегородка Glass 10mm (дверь)"  # Arch/BIM 166 (typed FeaturePython)
  Align = 0
  Area = 1980000
  Base = -> Line1424
  BlockHeight = 250
  BlockLength = 625
  CountBroken = 22
  CountEntire = 16
  Face = 0
  GlobalId = 2SiM96DqX1keqH__WrYAVq
  Height = 2200
  HorizontalArea = 9000
  IfcData = IfcUID=2SiM96DqX1keqH__WrYAVq; attributes={"GlobalId": {"value": "2SiM96DqX1keqH__WrYAVq"}}
  IfcType = 166
  Joint = 0
  Length = 900
  MakeBlocks = false
  Material = -> Material006
  MoveBase = false
  MoveWithHost = false
  Normal = (0,0,0)
  OffsetFirst = 300
  OffsetSecond = 50
  PerimeterLength = 1820
  PredefinedType = 0
  VerticalArea = 4.004e+06
  Width = 10
FEATURE [App::MaterialObjectPython] Material007  label="Stone wild"  # material (typed FeaturePython)
  Description = Stone wild
  Material = AuthorAndLicense=Concrete-Generic,CardName=Concrete-Generic,Color=(0.49019607843137253, 0.49019607843137253, 0.49019607843137253, 1.0),+11 more (map truncated)
  Transparency = 0
FEATURE [Part::FeaturePython] Roof012  label="roof_4_side"  # Arch/BIM 113 (typed FeaturePython)
  Angles = [35,35,35,35]
  Base = -> Wire691
  BorderLength = 68940
  Face = 0
  Flip = false
  Heights = [3459.03,3851.14,3459.03,3851.14]
  HorizontalArea = 0
  IdRel = [-1,-1,-1,-1]
  IfcData = attributes={"GlobalId": {"name": "GlobalId", "type": "IfcGloballyUniqueId", "is_enum": false, "enum_values": []}, "Description": {"... (+613 chars omitted),+1 more (map truncated)
  IfcType = 113
  Material = -> Material007
  MoveBase = false
  MoveWithHost = false
  Overhang = [1000,1000,1000,1000]
  PerimeterLength = 0
  Placement = pos=(0,0,3093.7) rot=(0,0,1;0rad)
  PredefinedType = 0
  RidgeLength = 44214.8
  Runs = [5500,5500,5500,5500]
  Thickness = [350,350,350,350]
  VerticalArea = 0
FEATURE [Part::MultiCommon] Common033  label="Кровля с выступами"
  Shapes = -> [Extrude,Roof012]
FEATURE [Part::FeaturePython] Roof  label="Кровля 2скатн001"  # Arch/BIM 113 (typed FeaturePython)
  Angles = [35,35,35,35]
  Base = -> Rectangle3216
  BorderLength = 58880
  Face = 0
  Flip = false
  Heights = [2989.89,3150.93,2989.89,3150.93]
  HorizontalArea = 1.78486e+08
  IdRel = [-1,-1,-1,-1]
  IfcData = attributes={"GlobalId": {"name": "GlobalId", "type": "IfcGloballyUniqueId", "is_enum": false, "enum_values": []}, "Description": {"... (+613 chars omitted),+1 more (map truncated)
  IfcType = 113
  Material = -> Material007
  MoveBase = false
  MoveWithHost = false
  Overhang = [0,0,0,0]
  PerimeterLength = 0
  Placement = pos=(0,4.55e-13,3062.84) rot=(0,0,1;0rad)
  PredefinedType = 0
  RidgeLength = 39313.4
  Runs = [4500,4500,4500,4500]
  Thickness = [350,350,350,350]
  VerticalArea = 2.51577e+07
FEATURE [Part::Cut] Cut046
  Base = -> Common033
  Tool = -> Extrude092
FEATURE [Part::FeaturePython] Roof015  label="Кровля 4скатн.001"  # Arch/BIM 113 (typed FeaturePython)
  Angles = [35,35,35,35]
  Base = -> Wire691
  BorderLength = 49660
  Face = 0
  Flip = false
  Heights = [3459.03,3851.14,3459.03,3851.14]
  HorizontalArea = 147706000
  IdRel = [-1,-1,-1,-1]
  IfcData = attributes={"GlobalId": {"name": "GlobalId", "type": "IfcGloballyUniqueId", "is_enum": false, "enum_values": []}, "Description": {"... (+613 chars omitted),+1 more (map truncated)
  IfcType = 113
  Material = -> Material007
  MoveBase = false
  MoveWithHost = false
  Overhang = [0,0,0,0]
  PerimeterLength = 0
  Placement = pos=(0,0,-324.469) rot=(0,0,1;0rad)
  PredefinedType = 0
  RidgeLength = 36252.6
  Runs = [5500,5500,5500,5500]
  Thickness = [2800,2800,2800,2800]
  VerticalArea = 1.69746e+08
FEATURE [Part::MultiCommon] Common034
  Shapes = -> [Roof,Extrude108]
FEATURE [Part::MultiFuse] Fusion046
  Shapes = -> [Common034,Cut046]
FEATURE [Part::Cut] Cut050  label="Roof001"
  Base = -> Fusion046
  Tool = -> Roof015
FEATURE [Part::FeaturePython] Roof017  label="Крышка вентшахты"  # Arch/BIM 113 (typed FeaturePython)
  Angles = [35,35,35,35]
  Base = -> Wire825
  BorderLength = 3840
  Face = 0
  Flip = false
  GlobalId = 36hdyCWSLF5w0SQ7_aWhlx
  Heights = [196.058,210.062,196.058,210.062]
  HorizontalArea = 864000
  IdRel = [-1,-1,-1,-1]
  IfcData = IfcUID=36hdyCWSLF5w0SQ7_aWhlx,+2 more (map truncated)
  IfcType = 113
  Material = -> Material007
  MoveBase = false
  MoveWithHost = false
  Overhang = [80,80,80,80]
  PerimeterLength = 0
  Placement = pos=(0,0,7150) rot=(0,0,1;0rad)
  PredefinedType = 0
  RidgeLength = 2752.41
  Runs = [300,300,300,300]
  Thickness = [10,10,10,10]
  VerticalArea = 46877.7
FEATURE [App::GeometryPython] BuildingPart040  label="Вентстояки верх.часть"  # Arch/BIM 52 (typed FeaturePython)
  Area = 10240000
  GlobalId = 0S7MvrNQ9E$RFzm_BzyI1l
  Group = -> [Wall256,Wall257,Wall258,Wall255,Roof017]
  Height = 0
  HeightPropagate = true
  IfcData = IfcUID=0S7MvrNQ9E$RFzm_BzyI1l,attributes={"GlobalId": {"value": "0S7MvrNQ9E$RFzm_BzyI1l"}},+1 more (map truncated)
  IfcType = 52
  LevelOffset = 0
FEATURE [App::MaterialObjectPython] Material008  label="Wall cement"  # material (typed FeaturePython)
  Description = Wall cement
  Material = AuthorAndLicense=Concrete-Generic,CardName=Concrete-Generic,Color=(0.8, 0.8, 0.8, 1.0),CompressiveStrength=25 MPa,Density=2400 kg/m^3,+9 more (map truncated)
  Transparency = 0
FEATURE [Part::FeaturePython] Wall229  label="перегородка ГП 75мм"  # Arch/BIM 166 (typed FeaturePython)
  Align = 0
  Area = 5.32e+06
  Base = -> Line1383
  BlockHeight = 250
  BlockLength = 625
  CountBroken = 22
  CountEntire = 16
  Face = 0
  GlobalId = 2WVLl1wd99i9KCUxxwLupd
  Height = 2800
  HorizontalArea = 142500
  IfcData = IfcUID=2WVLl1wd99i9KCUxxwLupd; attributes={"GlobalId": {"value": "2WVLl1wd99i9KCUxxwLupd"}}
  IfcType = 166
  Joint = 0
  Length = 1900
  MakeBlocks = false
  Material = -> Material008
  MoveBase = false
  MoveWithHost = false
  Normal = (0,0,0)
  OffsetFirst = 300
  OffsetSecond = 50
  PerimeterLength = 3950
  PredefinedType = 0
  VerticalArea = 1.106e+07
  Width = 75
FEATURE [Part::FeaturePython] Wall233  label="Штукатурка 20мм 001"  # Arch/BIM 166 (typed FeaturePython)
  Align = 0
  Area = 30856000
  Base = -> Wire829
  BlockHeight = 0
  BlockLength = 0
  CountBroken = 0
  CountEntire = 0
  Face = 0
  GlobalId = 1_tpg5Ww11ef5dsryiIvTa
  Height = 2800
  HorizontalArea = 250000
  IfcData = IfcUID=1_tpg5Ww11ef5dsryiIvTa,+2 more (map truncated)
  IfcType = 166
  Joint = 0
  Length = 11020
  MakeBlocks = false
  Material = -> Material008
  MoveBase = false
  MoveWithHost = false
  Normal = (0,0,0)
  OffsetFirst = 0
  OffsetSecond = 0
  PerimeterLength = 14792.2
  PredefinedType = 0
  Subtractions = -> [Structure285]
  VerticalArea = 57455720
  Width = 20
FEATURE [Part::FeaturePython] Wall234  label="Штукатурка 20мм 002"  # Arch/BIM 166 (typed FeaturePython)
  Align = 0
  Area = 8960000
  Base = -> Line1392
  BlockHeight = 0
  BlockLength = 0
  CountBroken = 0
  CountEntire = 0
  Face = 0
  GlobalId = 3UxVpvSNzClhJFqsCgM8Mc
  Height = 2800
  HorizontalArea = 77200
  IfcData = IfcUID=3UxVpvSNzClhJFqsCgM8Mc,+2 more (map truncated)
  IfcType = 166
  Joint = 0
  Length = 3200
  MakeBlocks = false
  Material = -> Material008
  MoveBase = false
  MoveWithHost = false
  Normal = (0,0,0)
  OffsetFirst = 0
  OffsetSecond = 0
  PerimeterLength = 6280
  PredefinedType = 0
  Subtractions = -> [Structure019,Structure016]
  VerticalArea = 1.14355e+07
  Width = 20
FEATURE [Part::FeaturePython] Wall235  label="Штукатурка 20мм 003"  # Arch/BIM 166 (typed FeaturePython)
  Align = 0
  Area = 5740000
  Base = -> Line1393
  BlockHeight = 0
  BlockLength = 0
  CountBroken = 0
  CountEntire = 0
  Face = 0
  GlobalId = 0Elsg4vQ59AghdVdDj5fjs
  Height = 2800
  HorizontalArea = 54200
  IfcData = IfcUID=0Elsg4vQ59AghdVdDj5fjs,+2 more (map truncated)
  IfcType = 166
  Joint = 0
  Length = 2050
  MakeBlocks = false
  Material = -> Material008
  MoveBase = false
  MoveWithHost = false
  Normal = (0,0,0)
  OffsetFirst = 0
  OffsetSecond = 0
  PerimeterLength = 4080
  PredefinedType = 0
  Subtractions = -> [Structure017]
  VerticalArea = 9.81792e+06
  Width = 20
FEATURE [Part::FeaturePython] Wall236  label="Штукатурка 20мм 004"  # Arch/BIM 166 (typed FeaturePython)
  Align = 0
  Area = 43708000
  Base = -> Wire795
  BlockHeight = 0
  BlockLength = 0
  CountBroken = 0
  CountEntire = 0
  Face = 0
  GlobalId = 1rvNhjPI97_QqIjlSx0NrH
  Height = 2800
  HorizontalArea = 0
  IfcData = IfcUID=1rvNhjPI97_QqIjlSx0NrH,+2 more (map truncated)
  IfcType = 166
  Joint = 0
  Length = 15610
  MakeBlocks = false
  Material = -> Material008
  MoveBase = false
  MoveWithHost = false
  Normal = (0,0,0)
  OffsetFirst = 0
  OffsetSecond = 0
  PerimeterLength = 0
  PredefinedType = 0
  Subtractions = -> [Structure304,Structure317,Structure020,Structure023]
  VerticalArea = 0
  Width = 20
FEATURE [Part::FeaturePython] Wall237  label="Штукатурка 20мм 005"  # Arch/BIM 166 (typed FeaturePython)
  Align = 0
  Area = 38808000
  Base = -> Wire796
  BlockHeight = 0
  BlockLength = 0
  CountBroken = 0
  CountEntire = 0
  Face = 0
  GlobalId = 0ZsALDo$1EKg5Etd528_ZF
  Height = 2800
  HorizontalArea = 0
  IfcData = IfcUID=0ZsALDo$1EKg5Etd528_ZF,+2 more (map truncated)
  IfcType = 166
  Joint = 0
  Length = 13860
  MakeBlocks = false
  Material = -> Material008
  MoveBase = false
  MoveWithHost = false
  Normal = (0,0,0)
  OffsetFirst = 0
  OffsetSecond = 0
  PerimeterLength = 0
  PredefinedType = 0
  Subtractions = -> [Structure308,Structure317,Structure306]
  VerticalArea = 0
  Width = 20
FEATURE [Part::FeaturePython] Wall238  label="Штукатурка 20мм 006"  # Arch/BIM 166 (typed FeaturePython)
  Align = 0
  Area = 37408000
  Base = -> Wire797
  BlockHeight = 0
  BlockLength = 0
  CountBroken = 0
  CountEntire = 0
  Face = 0
  GlobalId = 2HzDQoGZ5FsODk6SDIgE_Y
  Height = 2800
  HorizontalArea = 307200
  IfcData = IfcUID=2HzDQoGZ5FsODk6SDIgE_Y,+2 more (map truncated)
  IfcType = 166
  Joint = 0
  Length = 13360
  MakeBlocks = false
  Material = -> Material008
  MoveBase = false
  MoveWithHost = false
  Normal = (0,0,0)
  OffsetFirst = 0
  OffsetSecond = 0
  PerimeterLength = 26620
  PredefinedType = 0
  Subtractions = -> [Structure315,Structure023]
  VerticalArea = 6.5008e+07
  Width = 20
FEATURE [App::MaterialObjectPython] Material009  label="Silicate blocks"  # material (typed FeaturePython)
  Description = Silicate blocks
  Material = AuthorAndLicense=Concrete-Generic,CardName=Concrete-Generic,Color=(0.8313725490196079, 0.7647058823529411, 0.7647058823529411, 1.0),+11 more (map truncated)
  Transparency = 0
FEATURE [Part::FeaturePython] Wall015  label="перегородка (сил.блок 500х250х80) 001"  # Arch/BIM 166 (typed FeaturePython)
  Align = 2
  Area = 10360000
  Base = -> Line1054
  BlockHeight = 250
  BlockLength = 0
  CountBroken = 0
  CountEntire = 0
  Face = 0
  GlobalId = 0Pb3kWXLL62hdiT4yMFPnD
  Height = 2800
  HorizontalArea = 296000
  IfcData = IfcUID=0Pb3kWXLL62hdiT4yMFPnD; attributes={"GlobalId": {"value": "0Pb3kWXLL62hdiT4yMFPnD"}}
  IfcType = 166
  Joint = 0
  Length = 3700
  MakeBlocks = false
  Material = -> Material009
  MoveBase = false
  MoveWithHost = false
  Normal = (0,0,0)
  OffsetFirst = 0
  OffsetSecond = 300
  PerimeterLength = 7560
  PredefinedType = 0
  Subtractions = -> [Structure141]
  VerticalArea = 1.7642e+07
  Width = 80
FEATURE [Part::FeaturePython] Wall186  label="перегородка (сил.блок 500х250х80) 002"  # Arch/BIM 166 (typed FeaturePython)
  Additions = -> [Wall162,Wall187,Wall225,Wall188,Wall224,Wall222]
  Align = 2
  Area = 16716000
  Base = -> Line1316
  BlockHeight = 250
  BlockLength = 0
  CountBroken = 0
  CountEntire = 0
  Face = 0
  GlobalId = 1Rj7XWwfD1TACQSKytQJ$J
  Height = 2800
  HorizontalArea = 0
  IfcData = IfcUID=1Rj7XWwfD1TACQSKytQJ$J; attributes={"GlobalId": {"value": "1Rj7XWwfD1TACQSKytQJ$J"}}
  IfcType = 166
  Joint = 0
  Length = 5970
  MakeBlocks = false
  Material = -> Material009
  MoveBase = false
  MoveWithHost = false
  Normal = (0,0,0)
  OffsetFirst = 300
  OffsetSecond = 0
  PerimeterLength = 0
  PredefinedType = 0
  Subtractions = -> [Structure024,Structure026,Structure021,Box3211,Box3228]
  VerticalArea = 0
  Width = 80
FEATURE [Part::FeaturePython] Wall223  label="перегородка (сил.блок 500х250х80) 004"  # Arch/BIM 166 (typed FeaturePython)
  Align = 2
  Area = 1.036e+07
  Base = -> Line1358
  BlockHeight = 250
  BlockLength = 0
  CountBroken = 0
  CountEntire = 0
  Face = 0
  GlobalId = 1OB118XG9DJPL5jtZdDHzR
  Height = 2800
  HorizontalArea = 296000
  IfcData = IfcUID=1OB118XG9DJPL5jtZdDHzR; attributes={"GlobalId": {"value": "1OB118XG9DJPL5jtZdDHzR"}}
  IfcType = 166
  Joint = 0
  Length = 3700
  MakeBlocks = false
  Material = -> Material009
  MoveBase = false
  MoveWithHost = false
  Normal = (0,0,0)
  OffsetFirst = 300
  OffsetSecond = 50
  PerimeterLength = 7560
  PredefinedType = 0
  Subtractions = -> [Structure333]
  VerticalArea = 1.7888e+07
  Width = 80
FEATURE [Part::FeaturePython] Wall230  label="перегородка 053"  # Arch/BIM 166 (typed FeaturePython)
  Align = 2
  Area = 2520000
  Base = -> Line1390
  BlockHeight = 250
  BlockLength = 0
  CountBroken = 0
  CountEntire = 0
  Face = 0
  Height = 2800
  HorizontalArea = 72000
  IfcType = 166
  Joint = 0
  Length = 900
  MakeBlocks = false
  Material = -> Material009
  MoveBase = false
  MoveWithHost = false
  Normal = (0,0,0)
  OffsetFirst = 300
  OffsetSecond = 50
  PerimeterLength = 1960
  PredefinedType = 0
  VerticalArea = 5.488e+06
  Width = 80
FEATURE [App::MaterialObjectPython] Material010  label="Steel-Generic"  # material (typed FeaturePython)
  Description = This is a blend Steel material card. The values are at the low end of the spectrum. If you need a more precise material definition use the more specialised steel cards.
  Material = AuthorAndLicense=Steel-Generic,CardName=Steel-Generic,Color=(0.3803921568627451, 0.3803921568627451, 0.3803921568627451, 1.0),Density=7900 kg/m^3,+13 more (map truncated)
  ProductURL = https://en.wikipedia.org/wiki/Steel
  Transparency = 0
FEATURE [Part::FeaturePython] Pipe004  label="коакс. дымоход 120"  # Arch/BIM 98 (typed FeaturePython)
  Base = -> Wire830
  Diameter = 120
  GlobalId = 3_rhopNO93fB54w5AHh6mI
  HorizontalArea = 0
  IfcData = IfcUID=3_rhopNO93fB54w5AHh6mI,+2 more (map truncated)
  IfcType = 98
  Length = 6119.59
  Material = -> Material010
  MoveBase = false
  MoveWithHost = false
  OffsetEnd = 0
  OffsetStart = 0
  PerimeterLength = 0
  PredefinedType = 0
  VerticalArea = 0
  WallThickness = 0
FEATURE [Part::FeaturePython] Pipe007  label="Дымоход 200/300"  # Arch/BIM 98 (typed FeaturePython)
  Base = -> Wire828
  Diameter = 300
  GlobalId = 2NNTD1t9nFeu6xjn5rmLg2
  HorizontalArea = 0
  IfcData = IfcUID=2NNTD1t9nFeu6xjn5rmLg2,+2 more (map truncated)
  IfcType = 98
  Length = 5777.48
  Material = -> Material010
  MoveBase = false
  MoveWithHost = false
  OffsetEnd = 0
  OffsetStart = 0
  PerimeterLength = 0
  PredefinedType = 0
  VerticalArea = 0
  WallThickness = 0
FEATURE [Part::FeaturePython] Pipe008  label="Дымоход 200"  # Arch/BIM 98 (typed FeaturePython)
  Base = -> Line1479
  Diameter = 200
  GlobalId = 11JHR0lR55LRzzbgV05jpw
  HorizontalArea = 0
  IfcData = IfcUID=11JHR0lR55LRzzbgV05jpw,+2 more (map truncated)
  IfcType = 98
  Length = 5600
  Material = -> Material010
  MoveBase = false
  MoveWithHost = false
  OffsetEnd = 0
  OffsetStart = 0
  PerimeterLength = 0
  PredefinedType = 0
  VerticalArea = 0
  WallThickness = 0
FEATURE [Part::FeaturePython] Pipe009  label="Вентканал 140мм 001"  # Arch/BIM 98 (typed FeaturePython)
  Base = -> Line1480
  Diameter = 140
  GlobalId = 3HmMp4Xfr8TAmJ5ODVlau7
  HorizontalArea = 0
  IfcData = IfcUID=3HmMp4Xfr8TAmJ5ODVlau7,+2 more (map truncated)
  IfcType = 98
  Length = 4200
  Material = -> Material010
  MoveBase = false
  MoveWithHost = false
  OffsetEnd = 0
  OffsetStart = 0
  PerimeterLength = 0
  PredefinedType = 0
  VerticalArea = 0
  WallThickness = 0
FEATURE [Part::FeaturePython] Pipe010  label="Вентканал 140мм 002"  # Arch/BIM 98 (typed FeaturePython)
  Base = -> Line1480
  Diameter = 140
  GlobalId = 3OBLLStZzDnRK0fH7jX7AD
  HorizontalArea = 0
  IfcData = IfcUID=3OBLLStZzDnRK0fH7jX7AD,+2 more (map truncated)
  IfcType = 98
  Length = 4200
  Material = -> Material010
  MoveBase = false
  MoveWithHost = false
  OffsetEnd = 0
  OffsetStart = 0
  PerimeterLength = 0
  Placement = pos=(150,-150,0) rot=(0,0,1;0rad)
  PredefinedType = 0
  VerticalArea = 0
  WallThickness = 0
FEATURE [Part::FeaturePython] Pipe011  label="Вентканал 140мм 003"  # Arch/BIM 98 (typed FeaturePython)
  Base = -> Line1480
  Diameter = 140
  GlobalId = 2bpWL1Qcr8UxhAynMgY7T5
  HorizontalArea = 0
  IfcData = IfcUID=2bpWL1Qcr8UxhAynMgY7T5,+2 more (map truncated)
  IfcType = 98
  Length = 4200
  Material = -> Material010
  MoveBase = false
  MoveWithHost = false
  OffsetEnd = 0
  OffsetStart = 0
  PerimeterLength = 0
  Placement = pos=(0,-150,0) rot=(0,0,1;0rad)
  PredefinedType = 0
  VerticalArea = 0
  WallThickness = 0
FEATURE [Part::FeaturePython] Pipe013  label="Вентканал 140мм 004"  # Arch/BIM 98 (typed FeaturePython)
  Base = -> Line1480
  Diameter = 140
  GlobalId = 22CnrufE59UfX6ZQo80id_
  HorizontalArea = 0
  IfcData = IfcUID=22CnrufE59UfX6ZQo80id_,+2 more (map truncated)
  IfcType = 98
  Length = 4200
  Material = -> Material010
  MoveBase = false
  MoveWithHost = false
  OffsetEnd = 0
  OffsetStart = 0
  PerimeterLength = 0
  Placement = pos=(150,0,0) rot=(0,0,1;0rad)
  PredefinedType = 0
  VerticalArea = 0
  WallThickness = 0
FEATURE [App::MaterialObjectPython] Material011  label="Polypropylene"  # material (typed FeaturePython)
  Material = AuthorAndLicense=PP-Generic,CardName=PP-Generic,Color=(0.38823529411764707, 0.38823529411764707, 0.38823529411764707, 1.0),CompressiveStrength=10 MPa,+15 more (map truncated)
  ProductURL = https://en.wikipedia.org/wiki/Polypropylene
  Transparency = 0
FEATURE [Part::FeaturePython] Window020  label="Д-90-004"  # Arch/BIM 41 (typed FeaturePython)
  Area = 1935000
  Base = -> Sketch248
  Frame = 50
  GlobalId = 00iW5F1Zz0_RepVZ61wedb
  Height = 2150
  HoleDepth = 0
  HoleWire = 0
  HorizontalArea = 0
  IfcData = IfcUID=00iW5F1Zz0_RepVZ61wedb; attributes={"OverallHeight": {"value": 2150.0}, "OverallWidth": {"value": 900.0}, "GlobalId": {"value": "00iW5F1Zz0_RepVZ61wedb"}}
  IfcType = 41
  LouvreSpacing = 0
  LouvreWidth = 0
  Material = -> Material011
  MoveBase = false
  MoveWithHost = true
  Normal = (0,1,0)
  Opening = 0
  OperationType = 0
  OverallHeight = 2150
  OverallWidth = 900
  PerimeterLength = 0
  Placement = pos=(0,50,0) rot=(0,0,1;0rad)
  PredefinedType = 0
  Preset = 6
  SymbolElevation = false
  SymbolPlan = false
  VerticalArea = 0
  Width = 900
  WindowParts = OuterFrame | Frame | Wire0,Wire1 | 0.0+V | 0.00+V | Door | Solid panel | Wire1 | 50.0 | 0.0+V
  expr: OverallWidth = .Width.Value
  expr: OverallHeight = .Height.Value
FEATURE [Part::FeaturePython] Window021  label="Д-90-003"  # Arch/BIM 41 (typed FeaturePython)
  Area = 1935000
  Base = -> Sketch251
  Frame = 50
  GlobalId = 29QgZPyov5qAVey2RViV7P
  Height = 2150
  HoleDepth = 0
  HoleWire = 0
  HorizontalArea = 0
  IfcData = IfcUID=29QgZPyov5qAVey2RViV7P; attributes={"OverallHeight": {"value": 2150.0}, "OverallWidth": {"value": 900.0}, "GlobalId": {"value": "29QgZPyov5qAVey2RViV7P"}}
  IfcType = 41
  LouvreSpacing = 0
  LouvreWidth = 0
  Material = -> Material011
  MoveBase = false
  MoveWithHost = true
  Normal = (1,0,0)
  Opening = 0
  OperationType = 0
  OverallHeight = 2150
  OverallWidth = 900
  PerimeterLength = 0
  PredefinedType = 0
  Preset = 6
  SymbolElevation = false
  SymbolPlan = false
  VerticalArea = 0
  Width = 900
  WindowParts = OuterFrame | Frame | Wire0,Wire1 | 0.0+V | 0.00+V | Door | Solid panel | Wire1 | 50.0 | 0.0+V
  expr: OverallWidth = .Width.Value
  expr: OverallHeight = .Height.Value
FEATURE [Part::FeaturePython] Window026  label="Д-90-002"  # Arch/BIM 41 (typed FeaturePython)
  Area = 1935000
  Base = -> Sketch260
  Frame = 50
  GlobalId = 3IW9J8Pfn69QiBWvx91KEB
  Height = 2150
  HoleDepth = 0
  HoleWire = 0
  HorizontalArea = 0
  IfcData = IfcUID=3IW9J8Pfn69QiBWvx91KEB; attributes={"OverallHeight": {"value": 2150.0}, "OverallWidth": {"value": 900.0}, "GlobalId": {"value": "3IW9J8Pfn69QiBWvx91KEB"}}
  IfcType = 41
  LouvreSpacing = 0
  LouvreWidth = 0
  Material = -> Material011
  MoveBase = false
  MoveWithHost = true
  Normal = (0,1,0)
  Opening = 0
  OperationType = 0
  OverallHeight = 2150
  OverallWidth = 900
  PerimeterLength = 0
  Placement = pos=(0,0,180) rot=(0,0,1;0rad)
  PredefinedType = 0
  Preset = 6
  SymbolElevation = false
  SymbolPlan = false
  VerticalArea = 0
  Width = 900
  WindowParts = OuterFrame | Frame | Wire0,Wire1 | 0.0+V | 0.00+V | Door | Solid panel | Wire1 | 50.0 | 0.0+V
  expr: OverallWidth = .Width.Value
  expr: OverallHeight = .Height.Value
FEATURE [Part::FeaturePython] Window048  label="Д-90-001"  # Arch/BIM 41 (typed FeaturePython)
  Area = 1935000
  Base = -> Sketch305
  Frame = 50
  GlobalId = 3YJH8Y7brE3BZDEOWbTYIP
  Height = 2150
  HoleDepth = 0
  HoleWire = 0
  HorizontalArea = 0
  IfcData = IfcUID=3YJH8Y7brE3BZDEOWbTYIP; attributes={"OverallHeight": {"value": 2150.0}, "OverallWidth": {"value": 900.0}, "GlobalId": {"value": "3YJH8Y7brE3BZDEOWbTYIP"}}
  IfcType = 41
  LouvreSpacing = 0
  LouvreWidth = 0
  Material = -> Material011
  MoveBase = false
  MoveWithHost = true
  Normal = (1,0,0)
  Opening = 0
  OperationType = 0
  OverallHeight = 2150
  OverallWidth = 900
  PerimeterLength = 0
  PredefinedType = 0
  Preset = 6
  SymbolElevation = false
  SymbolPlan = false
  VerticalArea = 0
  Width = 900
  WindowParts = OuterFrame | Frame | Wire0,Wire1 | 0.0+V | 0.00+V | Door | Solid panel | Wire1 | 50.0 | 0.0+V
  expr: OverallHeight = .Height.Value
  expr: OverallWidth = .Width.Value
FEATURE [Part::FeaturePython] Window052  label="Д-90-005"  # Arch/BIM 41 (typed FeaturePython)
  Area = 1935000
  Base = -> Sketch309
  Frame = 50
  GlobalId = 1cijn4gZv3rAlY7HDrqfh6
  Height = 2150
  HoleDepth = 0
  HoleWire = 0
  HorizontalArea = 0
  IfcData = IfcUID=1cijn4gZv3rAlY7HDrqfh6; attributes={"OverallHeight": {"value": 2150.0}, "OverallWidth": {"value": 900.0}, "GlobalId": {"value": "1cijn4gZv3rAlY7HDrqfh6"}}
  IfcType = 41
  LouvreSpacing = 0
  LouvreWidth = 0
  Material = -> Material011
  MoveBase = false
  MoveWithHost = true
  Normal = (-1,0,0)
  Opening = 0
  OperationType = 0
  OverallHeight = 2150
  OverallWidth = 900
  PerimeterLength = 0
  PredefinedType = 0
  Preset = 6
  SymbolElevation = false
  SymbolPlan = false
  VerticalArea = 0
  Width = 900
  WindowParts = OuterFrame | Frame | Wire0,Wire1 | 0.0+V | 0.00+V | Door | Solid panel | Wire1 | 50.0 | 0.0+V
  expr: OverallHeight = .Height.Value
  expr: OverallWidth = .Width.Value
FEATURE [Part::FeaturePython] Window061  label="Окно Velox 55x98 001"  # Arch/BIM 170 (typed FeaturePython)
  Area = 539000
  Base = -> Sketch
  Frame = 50
  GlobalId = 0OgXawITjBROe3cBxnSt2i
  Height = 980
  HoleDepth = 0
  HoleWire = 0
  HorizontalArea = 0
  Hosts = -> [Roof012]
  IfcData = IfcUID=0OgXawITjBROe3cBxnSt2i,+2 more (map truncated)
  IfcType = 170
  LouvreSpacing = 0
  LouvreWidth = 0
  Material = -> Material011
  MoveBase = false
  MoveWithHost = true
  Normal = (0,0.573576,-0.819152)
  Opening = 0
  OverallHeight = 980
  OverallWidth = 550
  PartitioningType = 0
  PerimeterLength = 0
  Placement = pos=(0,0,23.7) rot=(0,0,1;0rad)
  PredefinedType = 0
  Preset = 2
  SymbolElevation = false
  SymbolPlan = false
  VerticalArea = 0
  Width = 550
  WindowParts = OuterFrame | Frame | Wire0,Wire1 | 300.0+V | 0.00+V | InnerFrame | Frame | Wire2,Wire3,Edge8,Mode1 | 50.0 | 50.0+V | InnerGlass | Glass panel | Wire3 | 5.0 | 75.0+V
  expr: OverallHeight = .Height.Value
  expr: OverallWidth = .Width.Value
FEATURE [Part::FeaturePython] Window062  label="Окно Velox 55x98 002"  # Arch/BIM 170 (typed FeaturePython)
  Area = 539000
  Base = -> Sketch321
  Frame = 50
  GlobalId = 1t8PRcMxPE3hYzY8q_2YfV
  Height = 980
  HoleDepth = 0
  HoleWire = 0
  HorizontalArea = 0
  Hosts = -> [Roof012]
  IfcData = IfcUID=1t8PRcMxPE3hYzY8q_2YfV,+2 more (map truncated)
  IfcType = 170
  LouvreSpacing = 0
  LouvreWidth = 0
  Material = -> Material011
  MoveBase = false
  MoveWithHost = true
  Normal = (0,0.573576,-0.819152)
  Opening = 0
  OverallHeight = 980
  OverallWidth = 550
  PartitioningType = 0
  PerimeterLength = 0
  Placement = pos=(0,0,23.7) rot=(0,0,1;0rad)
  PredefinedType = 0
  Preset = 2
  SymbolElevation = false
  SymbolPlan = false
  VerticalArea = 0
  Width = 550
  WindowParts = OuterFrame | Frame | Wire0,Wire1 | 300.0+V | 0.00+V | InnerFrame | Frame | Wire2,Wire3,Edge8,Mode1 | 50.0 | 50.0+V | InnerGlass | Glass panel | Wire3 | 5.0 | 75.0+V
  expr: OverallHeight = .Height.Value
  expr: OverallWidth = .Width.Value
FEATURE [Part::FeaturePython] Window063  label="Окно Velox 55x98 003"  # Arch/BIM 170 (typed FeaturePython)
  Area = 539000
  Base = -> Sketch322
  Frame = 50
  GlobalId = 1OK8u$9hHB99HRKu0QW2Gw
  Height = 980
  HoleDepth = 0
  HoleWire = 0
  HorizontalArea = 0
  Hosts = -> [Roof012]
  IfcData = IfcUID=1OK8u$9hHB99HRKu0QW2Gw,+2 more (map truncated)
  IfcType = 170
  LouvreSpacing = 0
  LouvreWidth = 0
  Material = -> Material011
  MoveBase = false
  MoveWithHost = true
  Normal = (0,-0.573576,-0.819152)
  Opening = 0
  OverallHeight = 980
  OverallWidth = 550
  PartitioningType = 0
  PerimeterLength = 0
  Placement = pos=(0,0,23.7) rot=(0,0,1;0rad)
  PredefinedType = 0
  Preset = 2
  SymbolElevation = false
  SymbolPlan = false
  VerticalArea = 0
  Width = 550
  WindowParts = OuterFrame | Frame | Wire0,Wire1 | 300.0+V | 0.00+V | InnerFrame | Frame | Wire2,Wire3,Edge8,Mode1 | 50.0 | 50.0+V | InnerGlass | Glass panel | Wire3 | 5.0 | 75.0+V
  expr: OverallHeight = .Height.Value
  expr: OverallWidth = .Width.Value
FEATURE [Part::FeaturePython] Pipe006  label="Фановый стояк 001"  # Arch/BIM 98 (typed FeaturePython)
  Base = -> Line1465
  Diameter = 110
  GlobalId = 0tHcO5Qt903xGrElAHG3sm
  HorizontalArea = 0
  IfcData = IfcUID=0tHcO5Qt903xGrElAHG3sm,+2 more (map truncated)
  IfcType = 98
  Length = 7200
  Material = -> Material011
  MoveBase = false
  MoveWithHost = false
  OffsetEnd = 0
  OffsetStart = 0
  PerimeterLength = 0
  PredefinedType = 0
  VerticalArea = 0
  WallThickness = 0
FEATURE [Part::Cut] Cut051  label="Roof002"
  Base = -> Cut050
  Tool = -> Wall057
FEATURE [Part::Part2DObjectPython] Wire836  # Draft 2D object (typed FeaturePython)
  Area = 0
  ChamferSize = 0
  Closed = true
  End = (0,7042.91,3733)
  FilletRadius = 0
  Length = 14626.9
  MakeFace = false
  Placement = pos=(0,436.862,3746.85) rot=(0.57735,0.57735,0.57735;2.0944rad)
  Points = (4) [(-19.7731,-13.8453,0),(3094.8,2167,0),(3491.48,2167,0),(6606.05,-13.8453,0)]
  Start = (0,417.089,3733)
  Subdivisions = 0
FEATURE [Part::FeaturePython] Structure357  label="Фронтон каркасн. 001"  # Arch/BIM 52 (typed FeaturePython)
  Base = -> Wire836
  FaceMaker = 0
  GlobalId = 3jxAwhryLARBy7FrCZDeex
  Height = 380
  HorizontalArea = 0
  IfcData = IfcUID=3jxAwhryLARBy7FrCZDeex,+2 more (map truncated)
  IfcType = 52
  Length = 0
  Material = -> Material003
  MoveBase = false
  MoveWithHost = false
  Nodes = (2) [(0,3730,4501.01),(-380,3730,4501.01)]
  NodesOffset = 0
  Normal = (0,0,0)
  PerimeterLength = 14935.2
  Placement = pos=(12950,3.637e-12,0) rot=(0,0,1;0rad)
  VerticalArea = 9.65978e+06
  Width = 100
FEATURE [Part::FeaturePython] Window057  label="ОК-Фронтон-1-1"  # Arch/BIM 170 (typed FeaturePython)
  Area = 1500000
  Base = -> Sketch316
  Frame = 50
  GlobalId = 0$_XcsZN1ByAmbTwc2WkwE
  Height = 1500
  HoleDepth = 0
  HoleWire = 0
  HorizontalArea = 0
  Hosts = -> [Structure357]
  IfcData = IfcUID=0$_XcsZN1ByAmbTwc2WkwE; attributes={"OverallHeight": {"value": 1500.0}, "OverallWidth": {"value": 1000.0}, "GlobalId": {"value": "0$_XcsZN1ByAmbTwc2WkwE"}}
  IfcType = 170
  LouvreSpacing = 0
  LouvreWidth = 0
  Material = -> Material011
  MoveBase = false
  MoveWithHost = true
  Normal = (-1,0,0)
  Opening = 0
  OverallHeight = 1500
  OverallWidth = 1000
  PartitioningType = 0
  PerimeterLength = 0
  Placement = pos=(12990,4.546e-12,0) rot=(0,0,1;0rad)
  PredefinedType = 0
  Preset = 2
  SymbolElevation = false
  SymbolPlan = false
  VerticalArea = 0
  Width = 1000
  WindowParts = OuterFrame | Frame | Wire0,Wire1 | 0.0+V | 0.00+V | InnerFrame | Frame | Wire2,Wire3 | 0.00+V | 0.0+V | InnerGlass | Glass panel | Wire3 | 10.0 | 50.0+V
  expr: OverallHeight = .Height.Value
  expr: OverallWidth = .Width.Value
FEATURE [Part::FeaturePython] Window059  label="ОК-Фронтон-1-2"  # Arch/BIM 170 (typed FeaturePython)
  Area = 1500000
  Base = -> Sketch318
  Frame = 50
  GlobalId = 0nJFhS2Ib74ffg7zBAHN8z
  Height = 1500
  HoleDepth = 0
  HoleWire = 0
  HorizontalArea = 0
  Hosts = -> [Structure357]
  IfcData = IfcUID=0nJFhS2Ib74ffg7zBAHN8z; attributes={"OverallHeight": {"value": 1500.0}, "OverallWidth": {"value": 1000.0}, "GlobalId": {"value": "0nJFhS2Ib74ffg7zBAHN8z"}}
  IfcType = 170
  LouvreSpacing = 0
  LouvreWidth = 0
  Material = -> Material011
  MoveBase = false
  MoveWithHost = true
  Normal = (-1,0,0)
  Opening = 0
  OverallHeight = 1500
  OverallWidth = 1000
  PartitioningType = 0
  PerimeterLength = 0
  Placement = pos=(12990,4.546e-12,0) rot=(0,0,1;0rad)
  PredefinedType = 0
  Preset = 2
  SymbolElevation = false
  SymbolPlan = false
  VerticalArea = 0
  Width = 1000
  WindowParts = OuterFrame | Frame | Wire0,Wire1 | 0.0+V | 0.00+V | InnerFrame | Frame | Wire2,Wire3 | 0.00+V | 0.0+V | InnerGlass | Glass panel | Wire3 | 10.0 | 50.0+V
  expr: OverallHeight = .Height.Value
  expr: OverallWidth = .Width.Value
FEATURE [Part::FeaturePython] Structure367  label="Фронтон каркасн. 002"  # Arch/BIM 52 (typed FeaturePython)
  Base = -> Wire836
  FaceMaker = 0
  GlobalId = 2MSSJcqfT2sha54GOqmBwm
  Height = 380
  HorizontalArea = 0
  IfcData = IfcUID=2MSSJcqfT2sha54GOqmBwm,+2 more (map truncated)
  IfcType = 52
  Length = 0
  Material = -> Material003
  MoveBase = false
  MoveWithHost = false
  Nodes = (2) [(0,3730,4501.01),(-380,3730,4501.01)]
  NodesOffset = 0
  Normal = (0,0,0)
  PerimeterLength = 0
  Placement = pos=(-50,0,0) rot=(0,0,1;0rad)
  VerticalArea = 9.65978e+06
  Width = 100
FEATURE [App::GeometryPython] BuildingPart083  label="Фронтоны"  # Arch/BIM 52 (typed FeaturePython)
  Area = 0
  GlobalId = 0vaHPODnn9yvkLUa9L_ZFm
  Group = -> [Structure357,Structure367]
  Height = 0
  HeightPropagate = true
  IfcData = IfcUID=0vaHPODnn9yvkLUa9L_ZFm,+2 more (map truncated)
  IfcType = 52
  LevelOffset = 0
FEATURE [Part::FeaturePython] Window066  label="ОК-Фронтон-1-005"  # Arch/BIM 170 (typed FeaturePython)
  Area = 1500000
  Base = -> Sketch316
  Frame = 50
  GlobalId = 2UO6SkOn1FXAzPeAHbjv7O
  Height = 1500
  HoleDepth = 0
  HoleWire = 0
  HorizontalArea = 0
  Hosts = -> [Structure367]
  IfcData = IfcUID=2UO6SkOn1FXAzPeAHbjv7O; attributes={"OverallHeight": {"value": 1500.0}, "OverallWidth": {"value": 1000.0}, "GlobalId": {"value": "2UO6SkOn1FXAzPeAHbjv7O"}}
  IfcType = 170
  LouvreSpacing = 0
  LouvreWidth = 0
  Material = -> Material011
  MoveBase = false
  MoveWithHost = true
  Normal = (1,0,0)
  Opening = 0
  OverallHeight = 1500
  OverallWidth = 1000
  PartitioningType = 0
  PerimeterLength = 0
  Placement = pos=(-100,0,0) rot=(0,0,1;0rad)
  PredefinedType = 0
  Preset = 2
  SymbolElevation = false
  SymbolPlan = false
  VerticalArea = 0
  Width = 1000
  WindowParts = OuterFrame | Frame | Wire0,Wire1 | 0.0+V | 0.00+V | InnerFrame | Frame | Wire2,Wire3 | 0.00+V | 0.0+V | InnerGlass | Glass panel | Wire3 | 10.0 | 50.0+V
  expr: OverallWidth = .Width.Value
  expr: OverallHeight = .Height.Value
FEATURE [Part::FeaturePython] Window067  label="ОК-Фронтон-1-006"  # Arch/BIM 170 (typed FeaturePython)
  Area = 1500000
  Base = -> Sketch318
  Frame = 50
  GlobalId = 1cBa_Vux91PRzEq6I7BfM7
  Height = 1500
  HoleDepth = 0
  HoleWire = 0
  HorizontalArea = 0
  Hosts = -> [Structure367]
  IfcData = IfcUID=1cBa_Vux91PRzEq6I7BfM7; attributes={"OverallHeight": {"value": 1500.0}, "OverallWidth": {"value": 1000.0}, "GlobalId": {"value": "1cBa_Vux91PRzEq6I7BfM7"}}
  IfcType = 170
  LouvreSpacing = 0
  LouvreWidth = 0
  Material = -> Material011
  MoveBase = false
  MoveWithHost = true
  Normal = (1,0,0)
  Opening = 0
  OverallHeight = 1500
  OverallWidth = 1000
  PartitioningType = 0
  PerimeterLength = 0
  Placement = pos=(-100,0,0) rot=(0,0,1;0rad)
  PredefinedType = 0
  Preset = 2
  SymbolElevation = false
  SymbolPlan = false
  VerticalArea = 0
  Width = 1000
  WindowParts = OuterFrame | Frame | Wire0,Wire1 | 0.0+V | 0.00+V | InnerFrame | Frame | Wire2,Wire3 | 0.00+V | 0.0+V | InnerGlass | Glass panel | Wire3 | 10.0 | 50.0+V
  expr: OverallWidth = .Width.Value
  expr: OverallHeight = .Height.Value
FEATURE [Part::Part2DObjectPython] Wire837  # Draft 2D object (typed FeaturePython)
  Area = 0
  ChamferSize = 0
  Closed = false
  End = (3400,3555,0)
  FilletRadius = 0
  Length = 4200
  MakeFace = false
  Placement = pos=(4110,-10,0) rot=(0,0,1;0rad)
  Points = (4) [(-110,-35,0),(-110,2295,0),(-710,2295,0),(-710,3565,0)]
  Start = (4000,-45,0)
  Subdivisions = 0
FEATURE [Part::Part2DObjectPython] Wire838  # Draft 2D object (typed FeaturePython)
  Area = 0
  ChamferSize = 0
  Closed = false
  End = (3500,3555,0)
  FilletRadius = 0
  Length = 9650
  MakeFace = false
  Placement = pos=(9540,-10,0) rot=(0,0,1;0rad)
  Points = (4) [(10,-35,0),(10,2395,0),(-6040,2395,0),(-6040,3565,0)]
  Start = (9550,-45,0)
  Subdivisions = 0
FEATURE [Part::Part2DObjectPython] Wire839  # Draft 2D object (typed FeaturePython)
  Area = 0
  ChamferSize = 0
  Closed = false
  End = (7400,-45,0)
  FilletRadius = 0
  Length = 6710
  MakeFace = false
  Placement = pos=(9460,-10,0) rot=(0,0,1;0rad)
  Points = (6) [(-10,-35,0),(-10,1795,0),(-810,1795,0),(-810,2295,0),(-2060,2295,0),(-2060,-35,0)]
  Start = (9450,-45,0)
  Subdivisions = 0
FEATURE [Part::Part2DObjectPython] Wire840  # Draft 2D object (typed FeaturePython)
  Area = 0
  ChamferSize = 0
  Closed = false
  End = (4100,-45,0)
  FilletRadius = 0
  Length = 7860
  MakeFace = false
  Placement = pos=(7310,-10,0) rot=(0,0,1;0rad)
  Points = (4) [(-10,-35,0),(-10,2295,0),(-3210,2295,0),(-3210,-35,0)]
  Start = (7300,-45,0)
  Subdivisions = 0
FEATURE [Part::FeaturePython] Wall  label="Штукатурка 10мм 001"  # Arch/BIM 166 (typed FeaturePython)
  Align = 0
  Area = 11760000
  Base = -> Wire837
  BlockHeight = 0
  BlockLength = 0
  CountBroken = 0
  CountEntire = 0
  Face = 0
  GlobalId = 0h0Qmcrjb7bRq5SNTtGOK3
  Height = 2800
  HorizontalArea = 42000
  IfcData = IfcUID=0h0Qmcrjb7bRq5SNTtGOK3,+2 more (map truncated)
  IfcType = 166
  Joint = 0
  Length = 4200
  MakeBlocks = false
  Material = -> Material008
  MoveBase = false
  MoveWithHost = false
  Normal = (0,0,0)
  OffsetFirst = 0
  OffsetSecond = 0
  PerimeterLength = 8420
  PredefinedType = 0
  Subtractions = -> [Structure021]
  VerticalArea = 19749000
  Width = 10
FEATURE [Part::FeaturePython] Wall267  label="Штукатурка 10мм 002"  # Arch/BIM 166 (typed FeaturePython)
  Align = 1
  Area = 27020000
  Base = -> Wire838
  BlockHeight = 0
  BlockLength = 0
  CountBroken = 0
  CountEntire = 0
  Face = 0
  GlobalId = 2wC2Vrh6fADPaqtRoWs2md
  Height = 2800
  HorizontalArea = 0
  IfcData = IfcUID=2wC2Vrh6fADPaqtRoWs2md,+2 more (map truncated)
  IfcType = 166
  Joint = 0
  Length = 9650
  MakeBlocks = false
  Material = -> Material008
  MoveBase = false
  MoveWithHost = false
  Normal = (0,0,0)
  OffsetFirst = 0
  OffsetSecond = 0
  PerimeterLength = 0
  PredefinedType = 0
  Subtractions = -> [Structure024,Structure026,Structure021,Box3211,Box3228]
  VerticalArea = 0
  Width = 10
FEATURE [Part::FeaturePython] Wall268  label="Штукатурка 10мм 003"  # Arch/BIM 166 (typed FeaturePython)
  Align = 0
  Area = 18788000
  Base = -> Wire839
  BlockHeight = 0
  BlockLength = 0
  CountBroken = 0
  CountEntire = 0
  Face = 0
  GlobalId = 34dKQn9vP2GQ3oJZbW7CwE
  Height = 2800
  HorizontalArea = 67300
  IfcData = IfcUID=34dKQn9vP2GQ3oJZbW7CwE,+2 more (map truncated)
  IfcType = 166
  Joint = 0
  Length = 6710
  MakeBlocks = false
  Material = -> Material008
  MoveBase = false
  MoveWithHost = false
  Normal = (0,0,0)
  OffsetFirst = 0
  OffsetSecond = 0
  PerimeterLength = 13480
  PredefinedType = 0
  Subtractions = -> [Structure026]
  VerticalArea = 33917000
  Width = 10
FEATURE [Part::FeaturePython] Wall269  label="Штукатурка 10мм 004"  # Arch/BIM 166 (typed FeaturePython)
  Align = 0
  Area = 22008000
  Base = -> Wire840
  BlockHeight = 0
  BlockLength = 0
  CountBroken = 0
  CountEntire = 0
  Face = 0
  GlobalId = 0L504R8CfBD9vh$vQbgFy9
  Height = 2800
  HorizontalArea = 78800
  IfcData = IfcUID=0L504R8CfBD9vh$vQbgFy9,+2 more (map truncated)
  IfcType = 166
  Joint = 0
  Length = 7860
  MakeBlocks = false
  Material = -> Material008
  MoveBase = false
  MoveWithHost = false
  Normal = (0,0,0)
  OffsetFirst = 0
  OffsetSecond = 0
  PerimeterLength = 15780
  PredefinedType = 0
  Subtractions = -> [Structure024]
  VerticalArea = 4.0357e+07
  Width = 10
FEATURE [Part::Part2DObjectPython] Rectangle3317  label="проём вентшахты внешний 001"  # Draft 2D object (typed FeaturePython)
  ChamferSize = 0
  Columns = 1
  FilletRadius = 0
  Height = 1030
  Length = 510
  MakeFace = false
  Placement = pos=(8690,1355,0) rot=(0,0,1;0rad)
  Rows = 1
FEATURE [Part::FeaturePython] Structure384  label="Вентстояк вычитаемы объём 007"  # Arch/BIM 52 (typed FeaturePython)
  Base = -> Rectangle3317
  FaceMaker = 0
  Height = 4000
  HorizontalArea = 525300
  IfcData = complex_attributes={"OwnerHistory": {}, "IsNestedBy": {}, "IsDecomposedBy": {}, "IsDefinedBy": {}, "ObjectPlacement": {}, "Representation":... (+4 chars omitted)
  IfcType = 52
  Length = 0
  MoveBase = false
  MoveWithHost = false
  Nodes = (2) [(8945,1870,0),(8945,1870,4000)]
  NodesOffset = 0
  Normal = (0,0,0)
  PerimeterLength = 3080
  Placement = pos=(0,0,2800) rot=(0,0,1;0rad)
  VerticalArea = 12320000
  Width = 100
FEATURE [Part::Cut] Cut052  label="Кровля габарит_001"
  Base = -> Cut051
  Tool = -> Structure384
FEATURE [Part::Part2DObjectPython] Line1523  label="Перемычки_034"  # Draft 2D object (typed FeaturePython)
  Area = 0
  ChamferSize = 0
  Closed = true
  End = (4185,7505,0)
  FilletRadius = 0
  Length = 2480
  MakeFace = true
  Placement = pos=(1622,7505,0) rot=(0,0,1;0rad)
  Points = (2) [(83,0,0),(2563,0,0)]
  Start = (1705,7505,0)
  Subdivisions = 0
FEATURE [Part::Part2DObjectPython] Line1524  label="Перемычки_035"  # Draft 2D object (typed FeaturePython)
  Area = 0
  ChamferSize = 0
  Closed = true
  End = (6265,7505,0)
  FilletRadius = 0
  Length = 1440
  MakeFace = true
  Placement = pos=(4174,7505,0) rot=(0,0,1;0rad)
  Points = (2) [(651,0,0),(2091,0,0)]
  Start = (4825,7505,0)
  Subdivisions = 0
FEATURE [Part::Part2DObjectPython] Line1526  label="Перемычки_037"  # Draft 2D object (typed FeaturePython)
  Area = 0
  ChamferSize = 0
  Closed = true
  End = (6980,-45,0)
  FilletRadius = 0
  Length = 1570
  MakeFace = true
  Placement = pos=(4825,-45,0) rot=(0,0,1;0rad)
  Points = (2) [(585,0,0),(2155,0,0)]
  Start = (5410,-45,0)
  Subdivisions = 0
FEATURE [Part::Part2DObjectPython] Line1527  label="Перемычки_038"  # Draft 2D object (typed FeaturePython)
  Area = 0
  ChamferSize = 0
  Closed = true
  End = (8475,-45,0)
  FilletRadius = 0
  Length = 1180
  MakeFace = true
  Placement = pos=(6515,-45,0) rot=(0,0,1;0rad)
  Points = (2) [(780,1.13687e-12,0),(1960,1.13687e-12,0)]
  Start = (7295,-45,0)
  Subdivisions = 0
FEATURE [Part::Part2DObjectPython] Line1529  label="Перемычки_039"  # Draft 2D object (typed FeaturePython)
  Area = 0
  ChamferSize = 0
  Closed = true
  End = (12570,1060,0)
  FilletRadius = 0
  Length = 2480
  MakeFace = true
  Placement = pos=(9260,845,0) rot=(0,0,1;0rad)
  Points = (2) [(3310,2695,0),(3310,215,0)]
  Start = (12570,3540,0)
  Subdivisions = 0
FEATURE [Part::Part2DObjectPython] Line1530  label="Перемычки_040"  # Draft 2D object (typed FeaturePython)
  Area = 0
  ChamferSize = 0
  Closed = true
  End = (-50,1580,0)
  FilletRadius = 0
  Length = 1960
  MakeFace = true
  Placement = pos=(-3360,1090,0) rot=(0,0,1;0rad)
  Points = (2) [(3310,2450,0),(3310,490,0)]
  Start = (-50,3540,0)
  Subdivisions = 0
FEATURE [Part::Part2DObjectPython] Line1531  label="Перемычки_041"  # Draft 2D object (typed FeaturePython)
  Area = 0
  ChamferSize = 0
  Closed = true
  End = (12570,3790,0)
  FilletRadius = 0
  Length = 1440
  MakeFace = true
  Placement = pos=(9260,3089,0) rot=(0,0,1;0rad)
  Points = (2) [(3310,2141,0),(3310,701,0)]
  Start = (12570,5230,0)
  Subdivisions = 0
FEATURE [Part::Part2DObjectPython] Line1532  label="Перемычки_042"  # Draft 2D object (typed FeaturePython)
  Area = 0
  ChamferSize = 0
  Closed = true
  End = (5030,3680,0)
  FilletRadius = 0
  Length = 1440
  MakeFace = true
  Placement = pos=(2939,3680,0) rot=(0,0,1;0rad)
  Points = (2) [(651,0,0),(2091,0,0)]
  Start = (3590,3680,0)
  Subdivisions = 0
FEATURE [Part::Part2DObjectPython] Line1533  label="Перемычки_043"  # Draft 2D object (typed FeaturePython)
  Area = 0
  ChamferSize = 0
  Closed = true
  End = (6980,3680,0)
  FilletRadius = 0
  Length = 1440
  MakeFace = true
  Placement = pos=(4889,3680,0) rot=(0,0,1;0rad)
  Points = (2) [(651,0,0),(2091,0,0)]
  Start = (5540,3680,0)
  Subdivisions = 0
FEATURE [Part::Part2DObjectPython] Line1537  label="Перемычки_045"  # Draft 2D object (typed FeaturePython)
  Area = 0
  ChamferSize = 0
  Closed = true
  End = (5095,-45,0)
  FilletRadius = 0
  Length = 1180
  MakeFace = true
  Placement = pos=(3135,-45,0) rot=(0,0,1;0rad)
  Points = (2) [(780,1.13687e-12,0),(1960,1.13687e-12,0)]
  Start = (3915,-45,0)
  Subdivisions = 0
FEATURE [Part::Part2DObjectPython] Line1538  label="Перемычки_046"  # Draft 2D object (typed FeaturePython)
  Area = 0
  ChamferSize = 0
  Closed = true
  End = (10815,7505,0)
  FilletRadius = 0
  Length = 2480
  MakeFace = true
  Placement = pos=(8252,7505,0) rot=(0,0,1;0rad)
  Points = (2) [(83,0,0),(2563,0,0)]
  Start = (8335,7505,0)
  Subdivisions = 0
FEATURE [Part::Part2DObjectPython] Line1540  label="Перемычки_048"  # Draft 2D object (typed FeaturePython)
  Area = 0
  ChamferSize = 0
  Closed = true
  End = (12180,3680,0)
  FilletRadius = 0
  Length = 4040
  MakeFace = true
  Placement = pos=(8057,3680,0) rot=(0,0,1;0rad)
  Points = (2) [(83,0,0),(4123,0,0)]
  Start = (8140,3680,0)
  Subdivisions = 0
FEATURE [Part::FeaturePython] Wall270  label="Перемычка монолитн. 001"  # Arch/BIM 166 (typed FeaturePython)
  Align = 1
  Area = 565440
  Base = -> Line1523
  BlockHeight = 0
  BlockLength = 0
  CountBroken = 0
  CountEntire = 0
  Face = 0
  GlobalId = 2_OOPfC1L9nOo2BwNBJ59E
  Height = 228
  HorizontalArea = 694400
  IfcData = IfcUID=2_OOPfC1L9nOo2BwNBJ59E,+2 more (map truncated)
  IfcType = 166
  Joint = 0
  Length = 2480
  MakeBlocks = false
  Material = -> Material001
  MoveBase = false
  MoveWithHost = false
  Normal = (0,0,0)
  OffsetFirst = 0
  OffsetSecond = 0
  PerimeterLength = 5520
  Placement = pos=(0,0,2572) rot=(0,0,1;0rad)
  PredefinedType = 0
  VerticalArea = 1.25856e+06
  Width = 280
FEATURE [Part::FeaturePython] Wall271  label="Перемычка монолитн. 002"  # Arch/BIM 166 (typed FeaturePython)
  Align = 1
  Area = 328320
  Base = -> Line1524
  BlockHeight = 0
  BlockLength = 0
  CountBroken = 0
  CountEntire = 0
  Face = 0
  GlobalId = 02zZ5o_1DBJf0p5Hr4GWva
  Height = 228
  HorizontalArea = 403200
  IfcData = IfcUID=02zZ5o_1DBJf0p5Hr4GWva,+2 more (map truncated)
  IfcType = 166
  Joint = 0
  Length = 1440
  MakeBlocks = false
  Material = -> Material001
  MoveBase = false
  MoveWithHost = false
  Normal = (0,0,0)
  OffsetFirst = 0
  OffsetSecond = 0
  PerimeterLength = 3440
  Placement = pos=(0,0,2572) rot=(0,0,1;0rad)
  PredefinedType = 0
  VerticalArea = 784320
  Width = 280
FEATURE [Part::FeaturePython] Wall272  label="Перемычка монолитн. 003"  # Arch/BIM 166 (typed FeaturePython)
  Align = 0
  Area = 362670
  Base = -> Line1526
  BlockHeight = 0
  BlockLength = 0
  CountBroken = 0
  CountEntire = 0
  Face = 0
  GlobalId = 2Km2nGMYj6_hkYj1EJr8Pd
  Height = 231
  HorizontalArea = 439600
  IfcData = IfcUID=2Km2nGMYj6_hkYj1EJr8Pd,+2 more (map truncated)
  IfcType = 166
  Joint = 0
  Length = 1570
  MakeBlocks = false
  Material = -> Material001
  MoveBase = false
  MoveWithHost = false
  Normal = (0,0,0)
  OffsetFirst = 0
  OffsetSecond = 0
  PerimeterLength = 3700
  Placement = pos=(0,0,2341) rot=(0,0,1;0rad)
  PredefinedType = 0
  VerticalArea = 854700
  Width = 280
FEATURE [Part::FeaturePython] Wall273  label="Перемычка монолитн. 004"  # Arch/BIM 166 (typed FeaturePython)
  Align = 0
  Area = 272580
  Base = -> Line1527
  BlockHeight = 0
  BlockLength = 0
  CountBroken = 0
  CountEntire = 0
  Face = 0
  GlobalId = 16$DxRw$TB6BfQSNqz60Qz
  Height = 231
  HorizontalArea = 330400
  IfcData = IfcUID=16$DxRw$TB6BfQSNqz60Qz,+2 more (map truncated)
  IfcType = 166
  Joint = 0
  Length = 1180
  MakeBlocks = false
  Material = -> Material001
  MoveBase = false
  MoveWithHost = false
  Normal = (0,0,0)
  OffsetFirst = 0
  OffsetSecond = 0
  PerimeterLength = 2920
  Placement = pos=(0,0,2341) rot=(0,0,1;0rad)
  PredefinedType = 0
  VerticalArea = 674520
  Width = 280
FEATURE [Part::FeaturePython] Wall274  label="Перемычка монолитн. 005"  # Arch/BIM 166 (typed FeaturePython)
  Align = 1
  Area = 565440
  Base = -> Line1529
  BlockHeight = 0
  BlockLength = 0
  CountBroken = 0
  CountEntire = 0
  Face = 0
  GlobalId = 0AqGC86W9B8PvMAPbhOTte
  Height = 228
  HorizontalArea = 694400
  IfcData = IfcUID=0AqGC86W9B8PvMAPbhOTte,+2 more (map truncated)
  IfcType = 166
  Joint = 0
  Length = 2480
  MakeBlocks = false
  Material = -> Material001
  MoveBase = false
  MoveWithHost = false
  Normal = (0,0,0)
  OffsetFirst = 0
  OffsetSecond = 0
  PerimeterLength = 5520
  Placement = pos=(0,0,2572) rot=(0,0,1;0rad)
  PredefinedType = 0
  VerticalArea = 1258560
  Width = 280
FEATURE [Part::FeaturePython] Wall275  label="Перемычка монолитн. 006"  # Arch/BIM 166 (typed FeaturePython)
  Align = 0
  Area = 446880
  Base = -> Line1530
  BlockHeight = 0
  BlockLength = 0
  CountBroken = 0
  CountEntire = 0
  Face = 0
  GlobalId = 23sFNS3FX7B9N2mOSbHlu1
  Height = 228
  HorizontalArea = 548800
  IfcData = IfcUID=23sFNS3FX7B9N2mOSbHlu1,+2 more (map truncated)
  IfcType = 166
  Joint = 0
  Length = 1960
  MakeBlocks = false
  Material = -> Material001
  MoveBase = false
  MoveWithHost = false
  Normal = (0,0,0)
  OffsetFirst = 0
  OffsetSecond = 0
  PerimeterLength = 4480
  Placement = pos=(0,0,2572) rot=(0,0,1;0rad)
  PredefinedType = 0
  VerticalArea = 1021440
  Width = 280
FEATURE [Part::FeaturePython] Wall276  label="Перемычка монолитн. 007"  # Arch/BIM 166 (typed FeaturePython)
  Align = 1
  Area = 328320
  Base = -> Line1531
  BlockHeight = 0
  BlockLength = 0
  CountBroken = 0
  CountEntire = 0
  Face = 0
  GlobalId = 2TdxzIhfb2oA4zfHjvmbo2
  Height = 228
  HorizontalArea = 403200
  IfcData = IfcUID=2TdxzIhfb2oA4zfHjvmbo2,+2 more (map truncated)
  IfcType = 166
  Joint = 0
  Length = 1440
  MakeBlocks = false
  Material = -> Material001
  MoveBase = false
  MoveWithHost = false
  Normal = (0,0,0)
  OffsetFirst = 0
  OffsetSecond = 0
  PerimeterLength = 3440
  Placement = pos=(0,0,2572) rot=(0,0,1;0rad)
  PredefinedType = 0
  VerticalArea = 784320
  Width = 280
FEATURE [Part::FeaturePython] Wall277  label="Перемычка монолитн. 008"  # Arch/BIM 166 (typed FeaturePython)
  Align = 2
  Area = 275040
  Base = -> Line1532
  BlockHeight = 0
  BlockLength = 0
  CountBroken = 0
  CountEntire = 0
  Face = 0
  GlobalId = 0sYYehG3D7NAgPHO$7$lOP
  Height = 191
  HorizontalArea = 360000
  IfcData = IfcUID=0sYYehG3D7NAgPHO$7$lOP,+2 more (map truncated)
  IfcType = 166
  Joint = 0
  Length = 1440
  MakeBlocks = false
  Material = -> Material001
  MoveBase = false
  MoveWithHost = false
  Normal = (0,0,0)
  OffsetFirst = 0
  OffsetSecond = 0
  PerimeterLength = 3380
  Placement = pos=(0,-1.819e-12,2150) rot=(0,0,1;0rad)
  PredefinedType = 0
  VerticalArea = 645580
  Width = 250
FEATURE [Part::FeaturePython] Wall278  label="Перемычка монолитн. 009"  # Arch/BIM 166 (typed FeaturePython)
  Align = 2
  Area = 275040
  Base = -> Line1533
  BlockHeight = 0
  BlockLength = 0
  CountBroken = 0
  CountEntire = 0
  Face = 0
  GlobalId = 0U$bER0DTA2wM7MkZ_5muC
  Height = 191
  HorizontalArea = 360000
  IfcData = IfcUID=0U$bER0DTA2wM7MkZ_5muC,+2 more (map truncated)
  IfcType = 166
  Joint = 0
  Length = 1440
  MakeBlocks = false
  Material = -> Material001
  MoveBase = false
  MoveWithHost = false
  Normal = (0,0,0)
  OffsetFirst = 0
  OffsetSecond = 0
  PerimeterLength = 3380
  Placement = pos=(0,-1.819e-12,2150) rot=(0,0,1;0rad)
  PredefinedType = 0
  VerticalArea = 645580
  Width = 250
FEATURE [Part::FeaturePython] Wall279  label="Перемычка монолитн. 010"  # Arch/BIM 166 (typed FeaturePython)
  Align = 0
  Area = 272580
  Base = -> Line1537
  BlockHeight = 0
  BlockLength = 0
  CountBroken = 0
  CountEntire = 0
  Face = 0
  GlobalId = 2dIW8Z8qb1VQVoHMf0gHj5
  Height = 231
  HorizontalArea = 330400
  IfcData = IfcUID=2dIW8Z8qb1VQVoHMf0gHj5,+2 more (map truncated)
  IfcType = 166
  Joint = 0
  Length = 1180
  MakeBlocks = false
  Material = -> Material001
  MoveBase = false
  MoveWithHost = false
  Normal = (0,0,0)
  OffsetFirst = 0
  OffsetSecond = 0
  PerimeterLength = 2920
  Placement = pos=(0,0,2341) rot=(0,0,1;0rad)
  PredefinedType = 0
  VerticalArea = 674520
  Width = 280
FEATURE [Part::FeaturePython] Wall280  label="Перемычка монолитн. 011"  # Arch/BIM 166 (typed FeaturePython)
  Align = 1
  Area = 565440
  Base = -> Line1538
  BlockHeight = 0
  BlockLength = 0
  CountBroken = 0
  CountEntire = 0
  Face = 0
  GlobalId = 3keULZXVT8QA_IAgUQCOo2
  Height = 228
  HorizontalArea = 694400
  IfcData = IfcUID=3keULZXVT8QA_IAgUQCOo2,+2 more (map truncated)
  IfcType = 166
  Joint = 0
  Length = 2480
  MakeBlocks = false
  Material = -> Material001
  MoveBase = false
  MoveWithHost = false
  Normal = (0,0,0)
  OffsetFirst = 0
  OffsetSecond = 0
  PerimeterLength = 5520
  Placement = pos=(0,-9.09e-13,2572) rot=(0,0,1;0rad)
  PredefinedType = 0
  VerticalArea = 1258560
  Width = 280
FEATURE [Part::FeaturePython] Wall281  label="Перемычка монолитн. 012"  # Arch/BIM 166 (typed FeaturePython)
  Align = 2
  Area = 1212000
  Base = -> Line1540
  BlockHeight = 0
  BlockLength = 0
  CountBroken = 0
  CountEntire = 0
  Face = 0
  GlobalId = 0GYkMrihr4SvLL6ceY8F$x
  Height = 300
  HorizontalArea = 1010000
  IfcData = IfcUID=0GYkMrihr4SvLL6ceY8F$x,+2 more (map truncated)
  IfcType = 166
  Joint = 0
  Length = 4040
  MakeBlocks = false
  Material = -> Material001
  MoveBase = false
  MoveWithHost = false
  Normal = (0,0,0)
  OffsetFirst = 0
  OffsetSecond = 0
  PerimeterLength = 8580
  Placement = pos=(0,-1.819e-12,2500) rot=(0,0,1;0rad)
  PredefinedType = 0
  VerticalArea = 2574000
  Width = 250
FEATURE [Part::FeaturePython] Wall004  label="Стена 250mm 2.1нф+1нф"  # Arch/BIM 166 (typed FeaturePython)
  Align = 2
  Area = 3.786e+07
  Base = -> Line1049
  BlockHeight = 231
  BlockLength = 0
  CountBroken = 0
  CountEntire = 0
  Face = 0
  GlobalId = 1uw9ZyZ5vAkuN6nr$sWkBP
  Height = 3000
  HorizontalArea = 0
  IfcData = IfcUID=1uw9ZyZ5vAkuN6nr$sWkBP; attributes={"GlobalId": {"value": "1uw9ZyZ5vAkuN6nr$sWkBP"}}
  IfcType = 166
  Joint = 0
  Length = 12620
  MakeBlocks = true
  Material = -> Material003
  MoveBase = false
  MoveWithHost = false
  Normal = (0,0,0)
  OffsetFirst = 0
  OffsetSecond = 500
  PerimeterLength = 0
  Placement = pos=(0,0,-200) rot=(0,0,1;0rad)
  PredefinedType = 0
  Subtractions = -> [Structure317,Structure023,Structure020,Wall278,Wall281,Wall277]
  VerticalArea = 0
  Width = 250
FEATURE [App::GeometryPython] BuildingPart088  label="Перемычки монолитные"  # Arch/BIM 52 (typed FeaturePython)
  Area = 5469750
  GlobalId = 3$YVGVb81DNfcCDGoK7nvQ
  Group = -> [Wall270,Wall271,Wall272,Wall273,Wall274,Wall275,Wall276,Wall277,Wall278,Wall279,Wall280,Wall281]
  Height = 0
  HeightPropagate = true
  IfcData = IfcUID=3$YVGVb81DNfcCDGoK7nvQ,+2 more (map truncated)
  IfcType = 52
  LevelOffset = 0
FEATURE [Part::FeaturePython] Wall282  label="Утепление перемычки XPS 100mm 001"  # Arch/BIM 166 (typed FeaturePython)
  Align = 1
  Area = 565440
  Base = -> Line1523
  BlockHeight = 0
  BlockLength = 0
  CountBroken = 0
  CountEntire = 0
  Face = 0
  Height = 228
  HorizontalArea = 248000
  IfcData = attributes={"GlobalId": {"name": "GlobalId", "type": "IfcGloballyUniqueId", "is_enum": false, "enum_values": []}, "Description": {"... (+533 chars omitted),+1 more (map truncated)
  IfcType = 166
  Joint = 0
  Length = 2480
  MakeBlocks = false
  Material = -> Material002
  MoveBase = false
  MoveWithHost = false
  Normal = (0,0,0)
  Offset = 280
  OffsetFirst = 0
  OffsetSecond = 0
  PerimeterLength = 5160
  Placement = pos=(0,0,2572) rot=(0,0,1;0rad)
  PredefinedType = 0
  VerticalArea = 1.17648e+06
  Width = 100
FEATURE [Part::FeaturePython] Wall283  label="Утепление перемычки XPS 100mm 025"  # Arch/BIM 166 (typed FeaturePython)
  Align = 0
  Area = 269040
  Base = -> Line1537
  BlockHeight = 0
  BlockLength = 0
  CountBroken = 0
  CountEntire = 0
  Face = 0
  Height = 228
  HorizontalArea = 118000
  IfcData = attributes={"GlobalId": {"name": "GlobalId", "type": "IfcGloballyUniqueId", "is_enum": false, "enum_values": []}, "Description": {"... (+533 chars omitted),+1 more (map truncated)
  IfcType = 166
  Joint = 0
  Length = 1180
  MakeBlocks = false
  Material = -> Material002
  MoveBase = false
  MoveWithHost = false
  Normal = (0,0,0)
  Offset = 280
  OffsetFirst = 0
  OffsetSecond = 0
  PerimeterLength = 2560
  Placement = pos=(0,0,2341) rot=(0,0,1;0rad)
  PredefinedType = 0
  VerticalArea = 583680
  Width = 100
FEATURE [Part::FeaturePython] Wall284  label="Утепление перемычки XPS 100mm 026"  # Arch/BIM 166 (typed FeaturePython)
  Align = 1
  Area = 328320
  Base = -> Line1524
  BlockHeight = 0
  BlockLength = 0
  CountBroken = 0
  CountEntire = 0
  Face = 0
  Height = 228
  HorizontalArea = 144000
  IfcData = attributes={"GlobalId": {"name": "GlobalId", "type": "IfcGloballyUniqueId", "is_enum": false, "enum_values": []}, "Description": {"... (+533 chars omitted),+1 more (map truncated)
  IfcType = 166
  Joint = 0
  Length = 1440
  MakeBlocks = false
  Material = -> Material002
  MoveBase = false
  MoveWithHost = false
  Normal = (0,0,0)
  Offset = 280
  OffsetFirst = 0
  OffsetSecond = 0
  PerimeterLength = 3080
  Placement = pos=(0,0,2572) rot=(0,0,1;0rad)
  PredefinedType = 0
  VerticalArea = 702240
  Width = 100
FEATURE [Part::FeaturePython] Wall285  label="Утепление перемычки XPS 100mm 027"  # Arch/BIM 166 (typed FeaturePython)
  Align = 0
  Area = 446880
  Base = -> Line1530
  BlockHeight = 0
  BlockLength = 0
  CountBroken = 0
  CountEntire = 0
  Face = 0
  Height = 228
  HorizontalArea = 196000
  IfcData = attributes={"GlobalId": {"name": "GlobalId", "type": "IfcGloballyUniqueId", "is_enum": false, "enum_values": []}, "Description": {"... (+533 chars omitted),+1 more (map truncated)
  IfcType = 166
  Joint = 0
  Length = 1960
  MakeBlocks = false
  Material = -> Material002
  MoveBase = false
  MoveWithHost = false
  Normal = (0,0,0)
  Offset = 280
  OffsetFirst = 0
  OffsetSecond = 0
  PerimeterLength = 4120
  Placement = pos=(0,0,2572) rot=(0,0,1;0rad)
  PredefinedType = 0
  VerticalArea = 939360
  Width = 100
FEATURE [Part::FeaturePython] Wall286  label="Утепление перемычки XPS 100mm 028"  # Arch/BIM 166 (typed FeaturePython)
  Align = 0
  Area = 269040
  Base = -> Line1527
  BlockHeight = 0
  BlockLength = 0
  CountBroken = 0
  CountEntire = 0
  Face = 0
  Height = 228
  HorizontalArea = 118000
  IfcData = attributes={"GlobalId": {"name": "GlobalId", "type": "IfcGloballyUniqueId", "is_enum": false, "enum_values": []}, "Description": {"... (+533 chars omitted),+1 more (map truncated)
  IfcType = 166
  Joint = 0
  Length = 1180
  MakeBlocks = false
  Material = -> Material002
  MoveBase = false
  MoveWithHost = false
  Normal = (0,0,0)
  Offset = 280
  OffsetFirst = 0
  OffsetSecond = 0
  PerimeterLength = 2560
  Placement = pos=(0,0,2341) rot=(0,0,1;0rad)
  PredefinedType = 0
  VerticalArea = 583680
  Width = 100
FEATURE [Part::FeaturePython] Wall287  label="Утепление перемычки XPS 100mm 029"  # Arch/BIM 166 (typed FeaturePython)
  Align = 1
  Area = 565440
  Base = -> Line1538
  BlockHeight = 0
  BlockLength = 0
  CountBroken = 0
  CountEntire = 0
  Face = 0
  Height = 228
  HorizontalArea = 248000
  IfcData = attributes={"GlobalId": {"name": "GlobalId", "type": "IfcGloballyUniqueId", "is_enum": false, "enum_values": []}, "Description": {"... (+533 chars omitted),+1 more (map truncated)
  IfcType = 166
  Joint = 0
  Length = 2480
  MakeBlocks = false
  Material = -> Material002
  MoveBase = false
  MoveWithHost = false
  Normal = (0,0,0)
  Offset = 280
  OffsetFirst = 0
  OffsetSecond = 0
  PerimeterLength = 5160
  Placement = pos=(0,-9.09e-13,2572) rot=(0,0,1;0rad)
  PredefinedType = 0
  VerticalArea = 1176480
  Width = 100
FEATURE [Part::FeaturePython] Wall288  label="Утепление перемычки XPS 100mm 030"  # Arch/BIM 166 (typed FeaturePython)
  Align = 0
  Area = 357960
  Base = -> Line1526
  BlockHeight = 0
  BlockLength = 0
  CountBroken = 0
  CountEntire = 0
  Face = 0
  Height = 228
  HorizontalArea = 157000
  IfcData = attributes={"GlobalId": {"name": "GlobalId", "type": "IfcGloballyUniqueId", "is_enum": false, "enum_values": []}, "Description": {"... (+533 chars omitted),+1 more (map truncated)
  IfcType = 166
  Joint = 0
  Length = 1570
  MakeBlocks = false
  Material = -> Material002
  MoveBase = false
  MoveWithHost = false
  Normal = (0,0,0)
  Offset = 280
  OffsetFirst = 0
  OffsetSecond = 0
  PerimeterLength = 3340
  Placement = pos=(0,0,2341) rot=(0,0,1;0rad)
  PredefinedType = 0
  VerticalArea = 761520
  Width = 100
FEATURE [Part::FeaturePython] Wall289  label="Утепление перемычки XPS 100mm 031"  # Arch/BIM 166 (typed FeaturePython)
  Align = 1
  Area = 565440
  Base = -> Line1529
  BlockHeight = 0
  BlockLength = 0
  CountBroken = 0
  CountEntire = 0
  Face = 0
  Height = 228
  HorizontalArea = 248000
  IfcData = attributes={"GlobalId": {"name": "GlobalId", "type": "IfcGloballyUniqueId", "is_enum": false, "enum_values": []}, "Description": {"... (+533 chars omitted),+1 more (map truncated)
  IfcType = 166
  Joint = 0
  Length = 2480
  MakeBlocks = false
  Material = -> Material002
  MoveBase = false
  MoveWithHost = false
  Normal = (0,0,0)
  Offset = 280
  OffsetFirst = 0
  OffsetSecond = 0
  PerimeterLength = 5160
  Placement = pos=(0,0,2572) rot=(0,0,1;0rad)
  PredefinedType = 0
  VerticalArea = 1176480
  Width = 100
FEATURE [Part::FeaturePython] Wall290  label="Утепление перемычки XPS 100mm 032"  # Arch/BIM 166 (typed FeaturePython)
  Align = 1
  Area = 328320
  Base = -> Line1531
  BlockHeight = 0
  BlockLength = 0
  CountBroken = 0
  CountEntire = 0
  Face = 0
  Height = 228
  HorizontalArea = 144000
  IfcData = attributes={"GlobalId": {"name": "GlobalId", "type": "IfcGloballyUniqueId", "is_enum": false, "enum_values": []}, "Description": {"... (+533 chars omitted),+1 more (map truncated)
  IfcType = 166
  Joint = 0
  Length = 1440
  MakeBlocks = false
  Material = -> Material002
  MoveBase = false
  MoveWithHost = false
  Normal = (0,0,0)
  Offset = 280
  OffsetFirst = 0
  OffsetSecond = 0
  PerimeterLength = 3080
  Placement = pos=(0,0,2572) rot=(0,0,1;0rad)
  PredefinedType = 0
  VerticalArea = 702240
  Width = 100
FEATURE [Part::FeaturePython] Wall214  label="Внешняя стена ЛСР 380мм"  # Arch/BIM 166 (typed FeaturePython)
  Align = 0
  Area = 121020000
  Base = -> Rectangle016
  BlockHeight = 231
  BlockLength = 0
  CountBroken = 0
  CountEntire = 0
  Face = 0
  GlobalId = 15i3vb4BrBERo7sMNULkP3
  Height = 3000
  HorizontalArea = 0
  IfcData = IfcUID=15i3vb4BrBERo7sMNULkP3,+2 more (map truncated)
  IfcType = 166
  Joint = 0
  Length = 40340
  MakeBlocks = true
  Material = -> Material004
  MoveBase = false
  MoveWithHost = false
  Normal = (0,0,0)
  OffsetFirst = 0
  OffsetSecond = 0
  PerimeterLength = 0
  Placement = pos=(0,0,-200) rot=(0,0,1;0rad)
  PredefinedType = 0
  Subtractions = -> [Structure315,Structure313,Structure308,Structure304,Structure285,Structure019,Structure016,Structure017,Structure306,Wall270,Wall271,Wall280,Wall276,Wall274,Wall275,Wall279,Wall272,Wall273,Wall285,Wall282,Wall284,Wall287,Wall290,Wall289,Wall283,Wall288,Wall286]
  VerticalArea = 0
  Width = 380
FEATURE [App::GeometryPython] BuildingPart089  label="Утепление перемычек XPS 100mm"  # Arch/BIM 52 (typed FeaturePython)
  Area = 3695880
  GlobalId = 1IqJZ7MUv7eQPyUTFsu7$l
  Group = -> [Wall282,Wall283,Wall284,Wall285,Wall286,Wall287,Wall288,Wall289,Wall290]
  Height = 0
  HeightPropagate = true
  IfcData = IfcUID=1IqJZ7MUv7eQPyUTFsu7$l,+2 more (map truncated)
  IfcType = 52
  LevelOffset = 0
FEATURE [TechDraw::DrawSVGTemplate] Template002
  EditableTexts = Лист=3; Номер=ИЖС-0000.0001
  Height = 297
  Orientation = 1
  Width = 420
FEATURE [App::FeaturePython] Dimension026  # Draft dimension (typed FeaturePython)
  Diameter = false
  Dimline = (5200,6300,0)
  Direction = (0,0,0)
  Distance = 110
  End = (4930,7485,0)
  Normal = (0,0,1)
  Start = (4820,7485,0)
FEATURE [App::FeaturePython] Dimension027  # Draft dimension (typed FeaturePython)
  Diameter = false
  Dimline = (8300,3000,0)
  Direction = (0,0,0)
  Distance = 1150
  End = (7910,3535,0)
  Normal = (0,0,1)
  Start = (7910,2385,0)
FEATURE [Part::Part2DObjectPython] Rectangle3323  # Draft 2D object (typed FeaturePython)
  Area = 0
  ChamferSize = 0
  Columns = 1
  FilletRadius = 0
  Height = 250
  Length = 920
  MakeFace = false
  Placement = pos=(6940,6068.61,0) rot=(0,0,1;0rad)
  Rows = 1
FEATURE [Part::Part2DObjectPython] Rectangle3324  # Draft 2D object (typed FeaturePython)
  Area = 0
  ChamferSize = 0
  Columns = 1
  FilletRadius = 0
  Height = 250
  Length = 920
  MakeFace = false
  Placement = pos=(6940,5818.61,0) rot=(0,0,1;0rad)
  Rows = 1
FEATURE [Part::Part2DObjectPython] Rectangle3325  # Draft 2D object (typed FeaturePython)
  Area = 0
  ChamferSize = 0
  Columns = 1
  FilletRadius = 0
  Height = 250
  Length = 920
  MakeFace = false
  Placement = pos=(6940,5568.61,0) rot=(0,0,1;0rad)
  Rows = 1
FEATURE [Part::FeaturePython] Stairs003  # Arch/BIM 128 (typed FeaturePython)
  AbsTop = (0,0,2208)
  Align = 0
  BlondelRatio = 0
  Flight = 0
  GlobalId = 3uneSe57LCqfWUoFMYeGFv
  Height = 3000
  HorizontalArea = 0
  IfcData = IfcUID=3uneSe57LCqfWUoFMYeGFv,+2 more (map truncated)
  IfcType = 128
  LandingDepth = 0
  Landings = 0
  Length = 4500
  Material = -> Material001
  MoveBase = false
  MoveWithHost = false
  Nosing = 20
  NumberOfSteps = 12
  OutlineLeft = (2) [(0,-60,1044),(2750,-60,3068)]
  OutlineLeftAll = (2) [(0,-60,1044),(2750,-60,3068)]
  OutlineRight = (2) [(2750,-860,3068),(0,-860,1044)]
  OutlineRightAll = (2) [(2750,-860,3068),(0,-860,1044)]
  PerimeterLength = 0
  Placement = pos=(7860,6298.61,1104) rot=(0,0,-1;1.5708rad)
  PredefinedType = 0
  RailingHeightLeft = 900
  RailingHeightRight = 900
  RailingLeft = Rail
  RailingOffsetLeft = 60
  RailingOffsetRight = 60
  RailingRight = Rail001
  RiserHeight = 184
  RiserHeightEnforce = 184
  RiserThickness = 0
  StringerOverlap = 0
  StringerWidth = 100
  Structure = 1
  StructureOffset = 0
  StructureThickness = 80
  TreadDepth = 250
  TreadDepthEnforce = 250
  TreadThickness = 40
  VerticalArea = 0
  Width = 920
  Winders = 0
FEATURE [Part::Part2DObjectPython] Line1552  # Draft 2D object (typed FeaturePython)
  Area = 0
  ChamferSize = 0
  Closed = true
  End = (7390,7020,0)
  FilletRadius = 0
  Length = 1010
  MakeFace = false
  Placement = pos=(8400,7020,0) rot=(1,0,0;3.14159rad)
  Points = (2) [(0,0,0),(-1010,0,0)]
  Start = (8400,7020,0)
  Subdivisions = 0
FEATURE [Part::Part2DObjectPython] Line1553  # Draft 2D object (typed FeaturePython)
  Area = 0
  ChamferSize = 0
  Closed = false
  End = (7390,7020,0)
  FilletRadius = 0
  Length = 3210
  MakeFace = false
  Placement = pos=(7390,3810,0) rot=(0,0,1;0rad)
  Points = (2) [(0,0,0),(0,3210,0)]
  Start = (7390,3810,0)
  Subdivisions = 0
FEATURE [Part::Part2DObjectPython] Arc  # Draft 2D object (typed FeaturePython)
  Area = 0
  FirstAngle = 90
  LastAngle = 180
  MakeFace = false
  Placement = pos=(7840,6570,0) rot=(0,0,1;0rad)
  Radius = 450
FEATURE [Part::Part2DObjectPython] Rectangle3331  # Draft 2D object (typed FeaturePython)
  Area = 0
  ChamferSize = 0
  Columns = 1
  FilletRadius = 0
  Height = 50
  Length = 50
  MakeFace = false
  Placement = pos=(7840,6520,0) rot=(0,0,1;0rad)
  Rows = 1
FEATURE [Part::Part2DObjectPython] Line1554  # Draft 2D object (typed FeaturePython)
  Area = 0
  ChamferSize = 0
  Closed = false
  End = (6940,7470,0)
  FilletRadius = 0
  Length = 1272.79
  MakeFace = false
  Placement = pos=(7840,6570,0) rot=(0,0,1;0rad)
  Points = (2) [(0,0,0),(-900,900,0)]
  Start = (7840,6570,0)
  Subdivisions = 0
FEATURE [Part::Part2DObjectPython] Circle  # Draft 2D object (typed FeaturePython)
  Area = 0
  FirstAngle = 0
  LastAngle = 0
  MakeFace = false
  Placement = pos=(7521.8,6888.2,0) rot=(0,0,1;0rad)
  Radius = 125
FEATURE [Part::Part2DObjectPython] Line1556  # Draft 2D object (typed FeaturePython)
  Area = 0
  ChamferSize = 0
  Closed = false
  End = (7610.19,6976.59,0)
  FilletRadius = 0
  Length = 250
  MakeFace = false
  Placement = pos=(7433.41,6799.81,0) rot=(0,0,1;0rad)
  Points = (2) [(0,0,0),(176.777,176.777,0)]
  Start = (7433.41,6799.81,0)
  Subdivisions = 0
FEATURE [Part::Part2DObjectPython] Arc126  label="Arc127"  # Draft 2D object (typed FeaturePython)
  Area = 0
  FirstAngle = -1.84921
  LastAngle = 26.749
  MakeFace = false
  Placement = pos=(7610.19,6976.59,0) rot=(0,0,1;0rad)
  Radius = 250
FEATURE [Part::Part2DObjectPython] Line1557  # Draft 2D object (typed FeaturePython)
  Area = 0
  ChamferSize = 0
  Closed = false
  End = (7856.39,7020,0)
  FilletRadius = 0
  Length = 250
  MakeFace = false
  Placement = pos=(7610.19,6976.59,0) rot=(0,0,1;0rad)
  Points = (2) [(0,0,0),(246.202,43.4136,0)]
  Start = (7610.19,6976.59,0)
  Subdivisions = 0
FEATURE [Part::Part2DObjectPython] Arc127  label="Arc128"  # Draft 2D object (typed FeaturePython)
  Area = 0
  FirstAngle = -123.355
  LastAngle = -87.0616
  MakeFace = false
  Placement = pos=(7433.41,6799.81,0) rot=(0,0,1;0rad)
  Radius = 250
FEATURE [Part::Part2DObjectPython] Line1558  # Draft 2D object (typed FeaturePython)
  Area = 0
  ChamferSize = 0
  Closed = false
  End = (7433.41,6799.81,0)
  FilletRadius = 0
  Length = 250
  MakeFace = false
  Placement = pos=(7390,6553.61,0) rot=(0,0,1;0rad)
  Points = (2) [(0,0,0),(43.4136,246.202,0)]
  Start = (7390,6553.61,0)
  Subdivisions = 0
FEATURE [Part::Part2DObjectPython] Rectangle3332  # Draft 2D object (typed FeaturePython)
  Area = 0
  ChamferSize = 0
  Columns = 1
  FilletRadius = 0
  Height = 100
  Length = 100
  MakeFace = false
  Placement = pos=(7840,6470,0) rot=(0,0,1;0rad)
  Rows = 1
FEATURE [Part::Part2DObjectPython] Line1564  # Draft 2D object (typed FeaturePython)
  Area = 0
  ChamferSize = 0
  Closed = false
  End = (7714.57,7952.96,0)
  FilletRadius = 0
  Length = 1500
  MakeFace = false
  Placement = pos=(7940,6470,0) rot=(0,0,1;0rad)
  Points = (2) [(0,0,0),(-225.432,1482.96,0)]
  Start = (7940,6470,0)
  Subdivisions = 0
FEATURE [Part::Part2DObjectPython] Line1565  # Draft 2D object (typed FeaturePython)
  Area = 0
  ChamferSize = 0
  Closed = false
  End = (7121.6,7727.07,0)
  FilletRadius = 0
  Length = 1500
  MakeFace = false
  Placement = pos=(7940,6470,0) rot=(0,0,1;0rad)
  Points = (2) [(0,0,0),(-818.404,1257.07,0)]
  Start = (7940,6470,0)
  Subdivisions = 0
FEATURE [Part::Part2DObjectPython] Line1566  # Draft 2D object (typed FeaturePython)
  Area = 0
  ChamferSize = 0
  Closed = false
  End = (6682.93,7288.4,0)
  FilletRadius = 0
  Length = 1500
  MakeFace = false
  Placement = pos=(7940,6470,0) rot=(0,0,1;0rad)
  Points = (2) [(0,0,0),(-1257.07,818.404,0)]
  Start = (7940,6470,0)
  Subdivisions = 0
FEATURE [Part::Part2DObjectPython] Line1567  # Draft 2D object (typed FeaturePython)
  Area = 0
  ChamferSize = 0
  Closed = false
  End = (6457.04,6695.43,0)
  FilletRadius = 0
  Length = 1500
  MakeFace = false
  Placement = pos=(7940,6470,0) rot=(0,0,1;0rad)
  Points = (2) [(0,0,0),(-1482.96,225.432,0)]
  Start = (7940,6470,0)
  Subdivisions = 0
FEATURE [Part::Part2DObjectPython] Rectangle3333  # Draft 2D object (typed FeaturePython)
  Area = 0
  ChamferSize = 0
  Columns = 1
  FilletRadius = 0
  Height = 900
  Length = 250
  MakeFace = false
  Placement = pos=(7856.39,6570,0) rot=(0,0,1;0rad)
  Rows = 1
FEATURE [Part::Part2DObjectPython] Rectangle3334  # Draft 2D object (typed FeaturePython)
  Area = 0
  ChamferSize = 0
  Columns = 1
  FilletRadius = 0
  Height = 250
  Length = 900
  MakeFace = false
  Placement = pos=(6940,6303.61,0) rot=(0,0,1;0rad)
  Rows = 1
FEATURE [Part::Part2DObjectPython] Rectangle3335  # Draft 2D object (typed FeaturePython)
  Area = 0
  ChamferSize = 0
  Columns = 1
  FilletRadius = 0
  Height = 900
  Length = 250
  MakeFace = false
  Placement = pos=(8106.39,6570,0) rot=(0,0,1;0rad)
  Rows = 1
FEATURE [Part::Part2DObjectPython] Rectangle3336  # Draft 2D object (typed FeaturePython)
  Area = 0
  ChamferSize = 0
  Columns = 1
  FilletRadius = 0
  Height = 250
  Length = 900
  MakeFace = false
  Placement = pos=(6940,6053.61,0) rot=(0,0,1;0rad)
  Rows = 1
FEATURE [Part::Part2DObjectPython] Line1568  # Draft 2D object (typed FeaturePython)
  Area = 0
  ChamferSize = 0
  Closed = false
  End = (6940,7470,0)
  FilletRadius = 0
  Length = 1416.39
  MakeFace = false
  Placement = pos=(8356.39,7470,0) rot=(0,0,1;0rad)
  Points = (2) [(0,0,0),(-1416.39,0,0)]
  Start = (8356.39,7470,0)
  Subdivisions = 0
FEATURE [Part::Part2DObjectPython] Line1569  # Draft 2D object (typed FeaturePython)
  Area = 0
  ChamferSize = 0
  Closed = false
  End = (6940,7470,0)
  FilletRadius = 0
  Length = 1416.39
  MakeFace = false
  Placement = pos=(6940,6053.61,0) rot=(0,0,1;0rad)
  Points = (2) [(0,0,0),(0,1416.39,0)]
  Start = (6940,6053.61,0)
  Subdivisions = 0
FEATURE [Part::Part2DObjectPython] Line1570  # Draft 2D object (typed FeaturePython)
  Area = 0
  ChamferSize = 0
  Closed = false
  End = (7874.9,6570,0)
  FilletRadius = 0
  Length = 49.3499
  MakeFace = false
  Placement = pos=(7840,6535.1,0) rot=(0,0,1;0rad)
  Points = (2) [(0,0,0),(34.8957,34.8957,0)]
  Start = (7840,6535.1,0)
  Subdivisions = 0
FEATURE [Part::Part2DObjectPython] Wire856  # Draft 2D object (typed FeaturePython)
  Area = 0
  ChamferSize = 0
  Closed = false
  End = (7840,6303.61,0)
  FilletRadius = 0
  Length = 1410.34
  MakeFace = false
  Placement = pos=(6940,6303.61,0) rot=(0,0,1;0rad)
  Points = (4) [(0,0,0),(0,318.407,0),(900,181.593,0),(900,0,0)]
  Start = (6940,6303.61,0)
  Subdivisions = 0
FEATURE [Part::Part2DObjectPython] Rectangle3337  # Draft 2D object (typed FeaturePython)
  Area = 0
  ChamferSize = 0
  Columns = 1
  FilletRadius = 0
  Height = 20
  Length = 899.99
  MakeFace = false
  Placement = pos=(6940,6283.61,0) rot=(0,0,1;0rad)
  Rows = 1
FEATURE [Part::Part2DObjectPython] Rectangle3338  # Draft 2D object (typed FeaturePython)
  Area = 0
  ChamferSize = 0
  Columns = 1
  FilletRadius = 0
  Height = 900
  Length = 250
  MakeFace = false
  Placement = pos=(8106.4,6585,0) rot=(0,0,1;0rad)
  Rows = 1
FEATURE [Part::Part2DObjectPython] Rectangle3339  # Draft 2D object (typed FeaturePython)
  Area = 0
  ChamferSize = 0
  Columns = 1
  FilletRadius = 0
  Height = 900
  Length = 20
  MakeFace = false
  Placement = pos=(8086.39,6570,0) rot=(0,0,1;0rad)
  Rows = 1
FEATURE [Part::Part2DObjectPython] Line1571  # Draft 2D object (typed FeaturePython)
  Area = 0
  ChamferSize = 0
  Closed = false
  End = (7824.35,7230.77,0)
  FilletRadius = 0
  Length = 20
  MakeFace = false
  Placement = pos=(7804.58,7227.77,0) rot=(0,0,1;0rad)
  Points = (2) [(0,0,0),(19.7728,3.00576,0)]
  Start = (7804.58,7227.77,0)
  Subdivisions = 0
FEATURE [Part::Part2DObjectPython] Line1572  # Draft 2D object (typed FeaturePython)
  Area = 0
  ChamferSize = 0
  Closed = false
  End = (7469.57,7192.58,0)
  FilletRadius = 0
  Length = 20
  MakeFace = false
  Placement = pos=(7452.81,7181.67,0) rot=(0,0,1;0rad)
  Points = (2) [(0,0,0),(16.7609,10.9121,0)]
  Start = (7452.81,7181.67,0)
  Subdivisions = 0
FEATURE [Part::Part2DObjectPython] Line1573  # Draft 2D object (typed FeaturePython)
  Area = 0
  ChamferSize = 0
  Closed = false
  End = (7191.99,6956.99,0)
  FilletRadius = 0
  Length = 20
  MakeFace = false
  Placement = pos=(7181.07,6940.23,0) rot=(0,0,1;0rad)
  Points = (2) [(0,0,0),(10.9121,16.7609,0)]
  Start = (7181.07,6940.23,0)
  Subdivisions = 0
FEATURE [Part::Part2DObjectPython] Line1574  # Draft 2D object (typed FeaturePython)
  Area = 0
  ChamferSize = 0
  Closed = false
  End = (7110.88,6596.04,0)
  FilletRadius = 0
  Length = 20
  MakeFace = false
  Placement = pos=(7107.87,6576.27,0) rot=(0,0,1;0rad)
  Points = (2) [(0,0,0),(3.00576,19.7728,0)]
  Start = (7107.87,6576.27,0)
  Subdivisions = 0
FEATURE [Part::Part2DObjectPython] Line1575  # Draft 2D object (typed FeaturePython)
  Area = 0
  ChamferSize = 0
  Closed = false
  End = (6454.03,6675.66,0)
  FilletRadius = 0
  Length = 1500
  MakeFace = false
  Placement = pos=(7936.99,6450.23,0) rot=(0,0,1;0rad)
  Points = (2) [(0,0,0),(-1482.96,225.432,0)]
  Start = (7936.99,6450.23,0)
  Subdivisions = 0
FEATURE [Part::Part2DObjectPython] Line1576  # Draft 2D object (typed FeaturePython)
  Area = 0
  ChamferSize = 0
  Closed = false
  End = (6672.02,7271.64,0)
  FilletRadius = 0
  Length = 1500
  MakeFace = false
  Placement = pos=(7929.09,6453.24,0) rot=(0,0,1;0rad)
  Points = (2) [(0,0,0),(-1257.07,818.404,0)]
  Start = (7929.09,6453.24,0)
  Subdivisions = 0
FEATURE [Part::Part2DObjectPython] Line1577  # Draft 2D object (typed FeaturePython)
  Area = 0
  ChamferSize = 0
  Closed = false
  End = (7104.83,7716.15,0)
  FilletRadius = 0
  Length = 1500
  MakeFace = false
  Placement = pos=(7923.24,6459.09,0) rot=(0,0,1;0rad)
  Points = (2) [(0,0,0),(-818.404,1257.07,0)]
  Start = (7923.24,6459.09,0)
  Subdivisions = 0
FEATURE [Part::Part2DObjectPython] Line1578  # Draft 2D object (typed FeaturePython)
  Area = 0
  ChamferSize = 0
  Closed = false
  End = (7694.8,7949.96,0)
  FilletRadius = 0
  Length = 1500
  MakeFace = false
  Placement = pos=(7920.23,6466.99,0) rot=(0,0,1;0rad)
  Points = (2) [(0,0,0),(-225.432,1482.96,0)]
  Start = (7920.23,6466.99,0)
  Subdivisions = 0
FEATURE [App::DocumentObjectGroup] Group  label="Лестница построение"
  Group = -> [Line1578,Line1577,Line1576,Line1575,Rectangle3339,Rectangle3335,Rectangle3336,Line1566,Line1569,Line1554,Line1568,Line1565,Line1564,Rectangle3333,Rectangle3334,Rectangle3337,Line1553,Line1552,Circle,Arc127,Line1574,Line1573,Line1572,Line1571,Arc,Arc126,Line1557,Line1556,Line1558,Rectangle3332,Line1567,Rectangle3331,Line1570,Rectangle3338,Wire856]
FEATURE [Part::Part2DObjectPython] Wire857  # Draft 2D object (typed FeaturePython)
  Area = 231189
  ChamferSize = 0
  Closed = true
  End = (7860,6298.61,0)
  FilletRadius = 0
  Length = 2353.16
  MakeFace = true
  Placement = pos=(6960.01,6298.61,0) rot=(0,0,1;0rad)
  Points = (4) [(-20.01,-0.000129917,0),(-20.01,321.217,0),(900,181.364,0),(899.99,0,0)]
  Start = (6940,6298.61,0)
  Subdivisions = 0
FEATURE [Part::Part2DObjectPython] Wire858  # Draft 2D object (typed FeaturePython)
  Area = 253761
  ChamferSize = 0
  Closed = true
  End = (7860.01,6479.97,0)
  FilletRadius = 0
  Length = 2580.03
  MakeFace = true
  Placement = pos=(6960.01,6616.78,0) rot=(0,0,1;0rad)
  Points = (4) [(-20.01,3.04034,0),(-20.01,508.421,0),(900,-90.5456,0),(900,-136.813,0)]
  Start = (6940,6619.83,0)
  Subdivisions = 0
FEATURE [Part::Part2DObjectPython] Wire859  # Draft 2D object (typed FeaturePython)
  Area = 353236
  ChamferSize = 0
  Closed = true
  End = (7860.01,6550.1,0)
  FilletRadius = 0
  Length = 2946.66
  MakeFace = true
  Placement = pos=(7860.01,6526.24,0) rot=(0,0,1;0rad)
  Points = (6) [(0,0,0),(-920.01,598.96,0),(-920.01,958.761,0),(-574.908,958.761,0),(20.4411,44.3062,0),(0,23.8651,0)]
  Start = (7860.01,6526.24,0)
  Subdivisions = 0
FEATURE [Part::Part2DObjectPython] Wire860  # Draft 2D object (typed FeaturePython)
  Area = 250464
  ChamferSize = 0
  Closed = true
  End = (7894.91,6585,0)
  FilletRadius = 0
  Length = 2554.3
  MakeFace = true
  Placement = pos=(7880.45,6570.55,0) rot=(0,0,1;0rad)
  Points = (5) [(0,0,0),(-595.35,914.455,0),(-92.6855,914.455,0),(44.1277,14.4546,0),(14.4546,14.4546,0)]
  Start = (7880.45,6570.55,0)
  Subdivisions = 0
FEATURE [Part::Part2DObjectPython] Wire861  # Draft 2D object (typed FeaturePython)
  Area = 225207
  ChamferSize = 0
  Closed = true
  End = (8106.4,6585,0)
  FilletRadius = 0
  Length = 2310.8
  MakeFace = true
  Placement = pos=(7924.58,6585,0) rot=(0,0,1;0rad)
  Points = (4) [(0,0,0),(-136.813,900,0),(181.823,900,0),(181.823,0,0)]
  Start = (7924.58,6585,0)
  Subdivisions = 0
FEATURE [Part::Part2DObjectPython] Wire862  # Draft 2D object (typed FeaturePython)
  Area = 0
  ChamferSize = 0
  Closed = true
  End = (7859.99,6298.61,0)
  FilletRadius = 0
  Length = 2393.6
  MakeFace = false
  Placement = pos=(6960,6298.61,0) rot=(0,0,1;0rad)
  Points = (4) [(-20,-0.000129917,0),(-20,341.447,0),(900,201.593,0),(899.99,0,0)]
  Start = (6940,6298.61,0)
  Subdivisions = 0
FEATURE [Part::Part2DObjectPython] Wire863  # Draft 2D object (typed FeaturePython)
  Area = 0
  ChamferSize = 0
  Closed = true
  End = (7860,6479.97,0)
  FilletRadius = 0
  Length = 2627.74
  MakeFace = false
  Placement = pos=(6960,6616.78,0) rot=(0,0,1;0rad)
  Points = (4) [(-20,3.04034,0),(-20,532.28,0),(900,-66.6805,0),(900,-136.813,0)]
  Start = (6940,6619.83,0)
  Subdivisions = 0
FEATURE [Part::Part2DObjectPython] Wire864  # Draft 2D object (typed FeaturePython)
  Area = 0
  ChamferSize = 0
  Closed = true
  End = (7860,6526.24,0)
  FilletRadius = 0
  Length = 2973.7
  MakeFace = false
  Placement = pos=(6960,7112.18,0) rot=(0,0,1;0rad)
  Points = (6) [(-20,13.021,0),(-20,372.822,0),(348.957,372.822,0),(934.896,-527.178,0),(900,-562.074,0),(900,-585.939,0)]
  Start = (6940,7125.2,0)
  Subdivisions = 0
FEATURE [Part::Part2DObjectPython] Wire865  # Draft 2D object (typed FeaturePython)
  Area = 0
  ChamferSize = 0
  Closed = true
  End = (7880.44,6570.55,0)
  FilletRadius = 0
  Length = 2594.76
  MakeFace = false
  Placement = pos=(7285.09,7485,0) rot=(0,0,1;0rad)
  Points = (5) [(0,0,0),(522.894,0,0),(659.707,-900,0),(609.804,-900,0),(595.35,-914.455,0)]
  Start = (7285.09,7485,0)
  Subdivisions = 0
FEATURE [Part::Part2DObjectPython] Wire866  # Draft 2D object (typed FeaturePython)
  Area = 0
  ChamferSize = 0
  Closed = true
  End = (7924.57,6585,0)
  FilletRadius = 0
  Length = 2350.8
  MakeFace = false
  Placement = pos=(7787.76,7485,0) rot=(0,0,1;0rad)
  Points = (4) [(0,0,0),(338.636,0,0),(338.636,-900,0),(136.813,-900,0)]
  Start = (7787.76,7485,0)
  Subdivisions = 0
FEATURE [Part::Part2DObjectPython] Rectangle3340  # Draft 2D object (typed FeaturePython)
  Area = 0
  ChamferSize = 0
  Columns = 1
  FilletRadius = 0
  Height = 900
  Length = 270
  MakeFace = false
  Placement = pos=(8106.39,6585,0) rot=(0,0,1;0rad)
  Rows = 1
FEATURE [Part::Part2DObjectPython] Rectangle3341  # Draft 2D object (typed FeaturePython)
  Area = 0
  ChamferSize = 0
  Columns = 1
  FilletRadius = 0
  Height = 189.696
  Length = 920
  MakeFace = false
  Placement = pos=(6940,6108.91,0) rot=(0,0,1;0rad)
  Rows = 1
FEATURE [Part::Part2DObjectPython] Wire869  # Draft 2D object (typed FeaturePython)
  Area = 0
  ChamferSize = 0
  Closed = false
  End = (12159,3610.73,2729.47)
  FilletRadius = 0
  Length = 1079.31
  MakeFace = true
  Placement = pos=(0,20,0) rot=(0,0,1;0rad)
  Points = (7) [(12172.2,3610.53,2749.27),(12170,3564,2795.8),(12167.8,3564,2524),(12165.6,3766,2524),(12163.4,3766,2776),(12161.2,3544.2,2776),+1 more]
  Start = (12172.2,3630.53,2749.27)
  Subdivisions = 0
  Support = -> [Wall281]
FEATURE [Part::FeaturePython] Rebar  label="Stirrup"  # Arch/BIM 110 (typed FeaturePython)
  Amount = 15
  AmountCheck = false
  Base = -> Wire869
  BentAngle = 135
  BentFactor = 4
  BottomCover = 20
  Diameter = 8
  Direction = (-1,0,0)
  Distance = 0
  FrontCover = 100
  HorizontalArea = 0
  Host = -> Wall281
  IfcData = IfcUID=0N2vvO0MT7Dvpb7EyTCBhJ
  IfcType = 110
  LeftCover = 20
  Length = 1079.31
  Mark = Stirrup
  Material = -> Material010
  MoveBase = false
  MoveWithHost = false
  OffsetEnd = 104
  OffsetStart = 104
  PerimeterLength = 0
  PlacementList = 15 placements: arithmetic series from (-104,0,0) step (-273.143,0,0) to (-3928,0,0)
  RebarShape = 3
  RightCover = 20
  Rounding = 1.75
  Spacing = 273.143
  TopCover = 20
  TotalLength = 16189.7
  TrueSpacing = 300
  VerticalArea = 0
FEATURE [App::DocumentObjectGroupPython] Stirrups  # scripted group (container) (typed FeaturePython)
  Group = -> [Rebar]
  Stirrups = -> [Rebar]
  StirrupsConfiguration = Two Legged Stirrups
FEATURE [Sketcher::SketchObject] Sketch326
  FullyConstrained = false
  MapMode = 5
  Placement = pos=(0,3555,2500) rot=(1,0,0;1.5708rad)
  Support = -> [Wall281]
  sketch-geometry (1):
    g0: LineSegment StartX=8230 StartY=263 StartZ=0 EndX=12110 EndY=263 EndZ=0
FEATURE [Part::FeaturePython] Rebar001  label="StraightRebar"  # Arch/BIM 110 (typed FeaturePython)
  Amount = 3
  AmountCheck = true
  Base = -> Sketch326
  Cover = 28
  CoverAlong = Top Side
  Diameter = 18
  Direction = (0,0,0)
  Distance = 0
  FrontCover = 28
  HorizontalArea = 0
  Host = -> Wall281
  IfcData = IfcUID=1dcUT_FHHF_B5oInSCm5hB
  IfcType = 110
  LeftBottomCover = 60
  Length = 3880
  Mark = StraightRebar
  Material = -> Material010
  MoveBase = false
  MoveWithHost = false
  OffsetEnd = 37
  OffsetStart = 37
  Orientation = Horizontal
  PerimeterLength = 0
  PlacementList = 3 placements: arithmetic series from (0,37,-8.21565e-15) step (0,88,-1.95399e-14) to (0,213,-4.72955e-14)
  RebarShape = 0
  RightTopCover = 60
  Rounding = 0
  Spacing = 88
  TotalLength = 11640
  TrueSpacing = 3
  VerticalArea = 0
FEATURE [App::DocumentObjectGroupPython] TopReinforcement  # scripted group (container) (typed FeaturePython)
  Group = -> [Rebar001]
  LayerSpacing = [30]
  NumberDiameterOffset = 3#18.0@60.0
  TopRebars = -> [Rebar001]
FEATURE [Sketcher::SketchObject] Sketch327
  FullyConstrained = false
  MapMode = 5
  Placement = pos=(0,3555,2500) rot=(1,0,0;1.5708rad)
  Support = -> [Wall281]
  sketch-geometry (1):
    g0: LineSegment StartX=8230 StartY=38 StartZ=0 EndX=12110 EndY=38 EndZ=0
FEATURE [Part::FeaturePython] Rebar002  label="StraightRebar001"  # Arch/BIM 110 (typed FeaturePython)
  Amount = 4
  AmountCheck = true
  Base = -> Sketch327
  Cover = 28
  CoverAlong = Bottom Side
  Diameter = 20
  Direction = (0,0,0)
  Distance = 0
  FrontCover = 28
  HorizontalArea = 0
  Host = -> Wall281
  IfcData = IfcUID=1EQ$82SIHAhRdy_3AtFEgy
  IfcType = 110
  LeftBottomCover = 60
  Length = 3880
  Mark = StraightRebar001
  Material = -> Material010
  MoveBase = false
  MoveWithHost = false
  OffsetEnd = 38
  OffsetStart = 38
  Orientation = Horizontal
  PerimeterLength = 0
  PlacementList = 4 placements: arithmetic series from (0,38,-8.43769e-15) step (0,58,-1.28786e-14) to (0,212,-4.70735e-14)
  RebarShape = 0
  RightTopCover = 60
  Rounding = 0
  Spacing = 58
  TotalLength = 15520
  TrueSpacing = 4
  VerticalArea = 0
FEATURE [App::DocumentObjectGroupPython] BottomReinforcement  # scripted group (container) (typed FeaturePython)
  BottomRebars = -> [Rebar002]
  Group = -> [Rebar002]
  LayerSpacing = [30]
  NumberDiameterOffset = 4#20.0@60.0
FEATURE [App::DocumentObjectGroupPython] BeamReinforcement  label="BeamReinforcement012"  # scripted group (container) (typed FeaturePython)
  Group = -> [Stirrups,TopReinforcement,BottomReinforcement]
  ReinforcementGroups = -> [Stirrups,TopReinforcement,BottomReinforcement]
FEATURE [Part::Part2DObjectPython] Wire871  # Draft 2D object (typed FeaturePython)
  Area = 0
  ChamferSize = 0
  Closed = false
  End = (10787.3,7564.85,2727.59)
  FilletRadius = 0
  Length = 898.352
  MakeFace = true
  Placement = pos=(0,15,0) rot=(0,0,1;0rad)
  Points = (7) [(10800.1,7565.41,2743.15),(10798,7524,2784.56),(10795.9,7524,2606),(10793.7,7736,2606),(10791.6,7736,2769),(10789.4,7508.44,2769),+1 more]
  Start = (10800.1,7580.41,2743.15)
  Subdivisions = 0
  Support = -> [Wall280]
FEATURE [Part::FeaturePython] Rebar003  label="Stirrup001"  # Arch/BIM 110 (typed FeaturePython)
  Amount = 10
  AmountCheck = false
  Base = -> Wire871
  BentAngle = 135
  BentFactor = 4
  BottomCover = 30
  Diameter = 8
  Direction = (-1,0,0)
  Distance = 0
  FrontCover = 100
  HorizontalArea = 0
  Host = -> Wall280
  IfcData = IfcUID=03$MgHS6j9GAjpO8e5wY8i
  IfcType = 110
  LeftCover = 30
  Length = 898.352
  Mark = Stirrup001
  Material = -> Material010
  MoveBase = false
  MoveWithHost = false
  OffsetEnd = 104
  OffsetStart = 104
  PerimeterLength = 0
  PlacementList = 10 placements: arithmetic series from (-104,0,0) step (-251.556,0,0) to (-2368,0,0)
  RebarShape = 3
  RightCover = 30
  Rounding = 1.375
  Spacing = 251.556
  TopCover = 30
  TotalLength = 8983.52
  TrueSpacing = 300
  VerticalArea = 0
FEATURE [App::DocumentObjectGroupPython] Stirrups001  # scripted group (container) (typed FeaturePython)
  Group = -> [Rebar003]
  Stirrups = -> [Rebar003]
  StirrupsConfiguration = Two Legged Stirrups
FEATURE [Sketcher::SketchObject] Sketch328
  FullyConstrained = false
  MapMode = 5
  Placement = pos=(0,7505,2572) rot=(1,0,0;1.5708rad)
  Support = -> [Wall280]
  sketch-geometry (1):
    g0: LineSegment StartX=8308 StartY=187 StartZ=0 EndX=10738 EndY=187 EndZ=0
FEATURE [Part::FeaturePython] Rebar004  label="StraightRebar002"  # Arch/BIM 110 (typed FeaturePython)
  Amount = 2
  AmountCheck = true
  Base = -> Sketch328
  Cover = 38
  CoverAlong = Top Side
  Diameter = 12
  Direction = (0,0,0)
  Distance = 0
  FrontCover = 38
  HorizontalArea = 0
  Host = -> Wall280
  IfcData = IfcUID=3CS4Ce6bv4LRFzsmwW8q2U
  IfcType = 110
  LeftBottomCover = 60
  Length = 2430
  Mark = StraightRebar002
  Material = -> Material010
  MoveBase = false
  MoveWithHost = false
  OffsetEnd = 44
  OffsetStart = 44
  Orientation = Horizontal
  PerimeterLength = 0
  Placement = pos=(57,0,0) rot=(0,0,1;0rad)
  PlacementList = 2 placements: [(0,44,-9.76996e-15),(0,236,-5.24025e-14)]
  RebarShape = 0
  RightTopCover = 60
  Rounding = 0
  Spacing = 192
  TotalLength = 4860
  TrueSpacing = 2
  VerticalArea = 0
FEATURE [App::DocumentObjectGroupPython] TopReinforcement001  # scripted group (container) (typed FeaturePython)
  Group = -> [Rebar004]
  LayerSpacing = [30]
  NumberDiameterOffset = 2#12.0@60.0
  TopRebars = -> [Rebar004]
FEATURE [Sketcher::SketchObject] Sketch329
  FullyConstrained = false
  MapMode = 5
  Placement = pos=(0,7505,2572) rot=(1,0,0;1.5708rad)
  Support = -> [Wall280]
  sketch-geometry (1):
    g0: LineSegment StartX=8308 StartY=45 StartZ=0 EndX=10738 EndY=45 EndZ=0
FEATURE [Part::FeaturePython] Rebar005  label="StraightRebar003"  # Arch/BIM 110 (typed FeaturePython)
  Amount = 2
  AmountCheck = true
  Base = -> Sketch329
  Cover = 38
  CoverAlong = Bottom Side
  Diameter = 14
  Direction = (0,0,0)
  Distance = 0
  FrontCover = 38
  HorizontalArea = 0
  Host = -> Wall280
  IfcData = IfcUID=12Y1T$1uv20RkT81nP3$Z0
  IfcType = 110
  LeftBottomCover = 60
  Length = 2430
  Mark = StraightRebar003
  Material = -> Material010
  MoveBase = false
  MoveWithHost = false
  OffsetEnd = 45
  OffsetStart = 45
  Orientation = Horizontal
  PerimeterLength = 0
  Placement = pos=(57,0,0) rot=(0,0,1;0rad)
  PlacementList = 2 placements: [(0,45,-9.99201e-15),(0,235,-5.21805e-14)]
  RebarShape = 0
  RightTopCover = 60
  Rounding = 0
  Spacing = 190
  TotalLength = 4860
  TrueSpacing = 2
  VerticalArea = 0
FEATURE [App::DocumentObjectGroupPython] BottomReinforcement001  # scripted group (container) (typed FeaturePython)
  BottomRebars = -> [Rebar005]
  Group = -> [Rebar005]
  LayerSpacing = [30]
  NumberDiameterOffset = 2#14.0@60.0
FEATURE [App::DocumentObjectGroupPython] BeamReinforcement001  # scripted group (container) (typed FeaturePython)
  Group = -> [Stirrups001,TopReinforcement001,BottomReinforcement001]
  ReinforcementGroups = -> [Stirrups001,TopReinforcement001,BottomReinforcement001]
FEATURE [Part::Part2DObjectPython] Wire872  # Draft 2D object (typed FeaturePython)
  Area = 0
  ChamferSize = 0
  Closed = false
  End = (6264.33,7564.56,2729.3)
  FilletRadius = 0
  Length = 890.697
  MakeFace = true
  Placement = pos=(75,15,0) rot=(0,0,1;0rad)
  Points = (7) [(6202.13,7563.7,2743.44),(6200,7524,2783.14),(6197.87,7524,2606),(6195.73,7736,2606),(6193.6,7736,2769),(6191.47,7509.86,2769),+1 more]
  Start = (6277.13,7578.7,2743.44)
  Subdivisions = 0
  Support = -> [Wall271]
FEATURE [Part::FeaturePython] Rebar006  label="Stirrup002"  # Arch/BIM 110 (typed FeaturePython)
  Amount = 6
  AmountCheck = false
  Base = -> Wire872
  BentAngle = 135
  BentFactor = 4
  BottomCover = 30
  Diameter = 8
  Direction = (-1,0,0)
  Distance = 0
  FrontCover = 100
  HorizontalArea = 0
  Host = -> Wall271
  IfcData = IfcUID=0wbSWuBvbEnPgC0wfqdX_b
  IfcType = 110
  LeftCover = 30
  Length = 890.697
  Mark = Stirrup002
  Material = -> Material010
  MoveBase = false
  MoveWithHost = false
  OffsetEnd = 104
  OffsetStart = 104
  PerimeterLength = 0
  PlacementList = 6 placements: arithmetic series from (-104,0,0) step (-244.8,0,0) to (-1328,0,0)
  RebarShape = 3
  RightCover = 30
  Rounding = 1.25
  Spacing = 244.8
  TopCover = 30
  TotalLength = 5344.18
  TrueSpacing = 300
  VerticalArea = 0
FEATURE [App::DocumentObjectGroupPython] Stirrups002  # scripted group (container) (typed FeaturePython)
  Group = -> [Rebar006]
  Stirrups = -> [Rebar006]
  StirrupsConfiguration = Two Legged Stirrups
FEATURE [Sketcher::SketchObject] Sketch330
  FullyConstrained = false
  MapMode = 5
  Placement = pos=(0,7505,2572) rot=(1,0,0;1.5708rad)
  Support = -> [Wall271]
  sketch-geometry (1):
    g0: LineSegment StartX=4850 StartY=187 StartZ=0 EndX=6140 EndY=187 EndZ=0
FEATURE [Part::FeaturePython] Rebar007  label="StraightRebar004"  # Arch/BIM 110 (typed FeaturePython)
  Amount = 2
  AmountCheck = true
  Base = -> Sketch330
  Cover = 38
  CoverAlong = Top Side
  Diameter = 12
  Direction = (0,0,0)
  Distance = 0
  FrontCover = 38
  HorizontalArea = 0
  Host = -> Wall271
  IfcData = IfcUID=02n1lHqdL8NwZlQltGu_h7
  IfcType = 110
  LeftBottomCover = 60
  Length = 1290
  Mark = StraightRebar004
  Material = -> Material010
  MoveBase = false
  MoveWithHost = false
  OffsetEnd = 44
  OffsetStart = 44
  Orientation = Horizontal
  PerimeterLength = 0
  Placement = pos=(60,0,0) rot=(0,0,1;0rad)
  PlacementList = 2 placements: [(0,44,-9.76996e-15),(0,236,-5.24025e-14)]
  RebarShape = 0
  RightTopCover = 60
  Rounding = 0
  Spacing = 192
  TotalLength = 2580
  TrueSpacing = 2
  VerticalArea = 0
FEATURE [App::DocumentObjectGroupPython] TopReinforcement002  # scripted group (container) (typed FeaturePython)
  Group = -> [Rebar007]
  LayerSpacing = [30]
  NumberDiameterOffset = 2#12.0@60.0
  TopRebars = -> [Rebar007]
FEATURE [Sketcher::SketchObject] Sketch331
  FullyConstrained = false
  MapMode = 5
  Placement = pos=(0,7505,2572) rot=(1,0,0;1.5708rad)
  Support = -> [Wall271]
  sketch-geometry (1):
    g0: LineSegment StartX=4850 StartY=44 StartZ=0 EndX=6140 EndY=44 EndZ=0
FEATURE [Part::FeaturePython] Rebar008  label="StraightRebar005"  # Arch/BIM 110 (typed FeaturePython)
  Amount = 2
  AmountCheck = true
  Base = -> Sketch331
  Cover = 38
  CoverAlong = Bottom Side
  Diameter = 12
  Direction = (0,0,0)
  Distance = 0
  FrontCover = 38
  HorizontalArea = 0
  Host = -> Wall271
  IfcData = IfcUID=10xIFfkxLCGw0mpryRN3cI
  IfcType = 110
  LeftBottomCover = 60
  Length = 1290
  Mark = StraightRebar005
  Material = -> Material010
  MoveBase = false
  MoveWithHost = false
  OffsetEnd = 44
  OffsetStart = 44
  Orientation = Horizontal
  PerimeterLength = 0
  Placement = pos=(60,0,0) rot=(0,0,1;0rad)
  PlacementList = 2 placements: [(0,44,-9.76996e-15),(0,236,-5.24025e-14)]
  RebarShape = 0
  RightTopCover = 60
  Rounding = 0
  Spacing = 192
  TotalLength = 2580
  TrueSpacing = 2
  VerticalArea = 0
FEATURE [App::DocumentObjectGroupPython] BottomReinforcement002  # scripted group (container) (typed FeaturePython)
  BottomRebars = -> [Rebar008]
  Group = -> [Rebar008]
  LayerSpacing = [30]
  NumberDiameterOffset = 2#12.0@60.0
FEATURE [App::DocumentObjectGroupPython] BeamReinforcement002  # scripted group (container) (typed FeaturePython)
  Group = -> [Stirrups002,TopReinforcement002,BottomReinforcement002]
  ReinforcementGroups = -> [Stirrups002,TopReinforcement002,BottomReinforcement002]
FEATURE [Part::Part2DObjectPython] Wire873  # Draft 2D object (typed FeaturePython)
  Area = 0
  ChamferSize = 0
  Closed = false
  End = (12629.6,5219.33,2729.3)
  FilletRadius = 0
  Length = 890.697
  MakeFace = true
  Placement = pos=(0,30,0) rot=(0,0,1;0rad)
  Points = (7) [(12643.7,5202.13,2743.44),(12604,5200,2783.14),(12604,5197.87,2606),(12816,5195.73,2606),(12816,5193.6,2769),(12589.9,5191.47,2769),+1 more]
  Start = (12643.7,5232.13,2743.44)
  Subdivisions = 0
  Support = -> [Wall276]
FEATURE [Part::FeaturePython] Rebar009  label="Stirrup003"  # Arch/BIM 110 (typed FeaturePython)
  Amount = 6
  AmountCheck = false
  Base = -> Wire873
  BentAngle = 135
  BentFactor = 4
  BottomCover = 30
  Diameter = 8
  Direction = (0,-1,0)
  Distance = 0
  FrontCover = 100
  HorizontalArea = 0
  Host = -> Wall276
  IfcData = IfcUID=0yypPYtsPCuBCevCtN2Olt
  IfcType = 110
  LeftCover = 30
  Length = 890.697
  Mark = Stirrup003
  Material = -> Material010
  MoveBase = false
  MoveWithHost = false
  OffsetEnd = 104
  OffsetStart = 104
  PerimeterLength = 0
  PlacementList = 6 placements: arithmetic series from (0,-104,0) step (0,-244.8,0) to (0,-1328,0)
  RebarShape = 3
  RightCover = 30
  Rounding = 1.25
  Spacing = 244.8
  TopCover = 30
  TotalLength = 5344.18
  TrueSpacing = 300
  VerticalArea = 0
FEATURE [App::DocumentObjectGroupPython] Stirrups003  # scripted group (container) (typed FeaturePython)
  Group = -> [Rebar009]
  Stirrups = -> [Rebar009]
  StirrupsConfiguration = Two Legged Stirrups
FEATURE [Sketcher::SketchObject] Sketch332
  FullyConstrained = false
  MapMode = 5
  Placement = pos=(12850,0,2572) rot=(0.57735,0.57735,0.57735;2.0944rad)
  Support = -> [Wall276]
  sketch-geometry (1):
    g0: LineSegment StartX=3850 StartY=187 StartZ=0 EndX=5140 EndY=187 EndZ=0
FEATURE [Part::FeaturePython] Rebar010  label="StraightRebar006"  # Arch/BIM 110 (typed FeaturePython)
  Amount = 2
  AmountCheck = true
  Base = -> Sketch332
  Cover = 38
  CoverAlong = Top Side
  Diameter = 12
  Direction = (0,0,0)
  Distance = 0
  FrontCover = 38
  HorizontalArea = 0
  Host = -> Wall276
  IfcData = IfcUID=3sX30Bu914T9jBbQKNrnT9
  IfcType = 110
  LeftBottomCover = 60
  Length = 1290
  Mark = StraightRebar006
  Material = -> Material010
  MoveBase = false
  MoveWithHost = false
  OffsetEnd = 44
  OffsetStart = 44
  Orientation = Horizontal
  PerimeterLength = 0
  Placement = pos=(0,30,0) rot=(0,0,1;0rad)
  PlacementList = 2 placements: [(-44,0,0),(-236,0,0)]
  RebarShape = 0
  RightTopCover = 60
  Rounding = 0
  Spacing = 192
  TotalLength = 2580
  TrueSpacing = 2
  VerticalArea = 0
FEATURE [App::DocumentObjectGroupPython] TopReinforcement003  # scripted group (container) (typed FeaturePython)
  Group = -> [Rebar010]
  LayerSpacing = [30]
  NumberDiameterOffset = 2#12.0@60.0
  TopRebars = -> [Rebar010]
FEATURE [Sketcher::SketchObject] Sketch333
  FullyConstrained = false
  MapMode = 5
  Placement = pos=(12850,0,2572) rot=(0.57735,0.57735,0.57735;2.0944rad)
  Support = -> [Wall276]
  sketch-geometry (1):
    g0: LineSegment StartX=3850 StartY=44 StartZ=0 EndX=5140 EndY=44 EndZ=0
FEATURE [Part::FeaturePython] Rebar011  label="StraightRebar007"  # Arch/BIM 110 (typed FeaturePython)
  Amount = 2
  AmountCheck = true
  Base = -> Sketch333
  Cover = 38
  CoverAlong = Bottom Side
  Diameter = 12
  Direction = (0,0,0)
  Distance = 0
  FrontCover = 38
  HorizontalArea = 0
  Host = -> Wall276
  IfcData = IfcUID=0U2drE4$P7kvGv3bbH5Yg2
  IfcType = 110
  LeftBottomCover = 60
  Length = 1290
  Mark = StraightRebar007
  Material = -> Material010
  MoveBase = false
  MoveWithHost = false
  OffsetEnd = 44
  OffsetStart = 44
  Orientation = Horizontal
  PerimeterLength = 0
  Placement = pos=(0,30,0) rot=(0,0,1;0rad)
  PlacementList = 2 placements: [(-44,0,0),(-236,0,0)]
  RebarShape = 0
  RightTopCover = 60
  Rounding = 0
  Spacing = 192
  TotalLength = 2580
  TrueSpacing = 2
  VerticalArea = 0
FEATURE [App::DocumentObjectGroupPython] BottomReinforcement003  # scripted group (container) (typed FeaturePython)
  BottomRebars = -> [Rebar011]
  Group = -> [Rebar011]
  LayerSpacing = [30]
  NumberDiameterOffset = 2#12.0@60.0
FEATURE [App::DocumentObjectGroupPython] BeamReinforcement003  # scripted group (container) (typed FeaturePython)
  Group = -> [Stirrups003,TopReinforcement003,BottomReinforcement003]
  ReinforcementGroups = -> [Stirrups003,TopReinforcement003,BottomReinforcement003]
FEATURE [Part::Part2DObjectPython] Wire874  # Draft 2D object (typed FeaturePython)
  Area = 0
  ChamferSize = 0
  Closed = false
  End = (12629.8,1049.27,2727.59)
  FilletRadius = 0
  Length = 898.352
  MakeFace = true
  Placement = pos=(0,75,0) rot=(0,0,1;0rad)
  Points = (7) [(12645.4,987.147,2743.15),(12604,985,2784.56),(12604,982.853,2606),(12816,980.706,2606),(12816,978.56,2769),(12588.4,976.413,2769),+1 more]
  Start = (12645.4,1062.15,2743.15)
  Subdivisions = 0
  Support = -> [Wall274]
FEATURE [Part::FeaturePython] Rebar012  label="Stirrup004"  # Arch/BIM 110 (typed FeaturePython)
  Amount = 10
  AmountCheck = false
  Base = -> Wire874
  BentAngle = 135
  BentFactor = 4
  BottomCover = 30
  Diameter = 8
  Direction = (0,1,0)
  Distance = 0
  FrontCover = 100
  HorizontalArea = 0
  Host = -> Wall274
  IfcData = IfcUID=3XbnhF0cz6mArcGNZbmhw$
  IfcType = 110
  LeftCover = 30
  Length = 898.352
  Mark = Stirrup004
  Material = -> Material010
  MoveBase = false
  MoveWithHost = false
  OffsetEnd = 104
  OffsetStart = 104
  PerimeterLength = 0
  PlacementList = 10 placements: arithmetic series from (0,104,0) step (0,251.556,0) to (0,2368,0)
  RebarShape = 3
  RightCover = 30
  Rounding = 1.375
  Spacing = 251.556
  TopCover = 30
  TotalLength = 8983.52
  TrueSpacing = 300
  VerticalArea = 0
FEATURE [App::DocumentObjectGroupPython] Stirrups004  # scripted group (container) (typed FeaturePython)
  Group = -> [Rebar012]
  Stirrups = -> [Rebar012]
  StirrupsConfiguration = Two Legged Stirrups
FEATURE [Sketcher::SketchObject] Sketch334
  FullyConstrained = false
  MapMode = 5
  Placement = pos=(12570,0,2572) rot=(0.57735,-0.57735,-0.57735;2.0944rad)
  Support = -> [Wall274]
  sketch-geometry (1):
    g0: LineSegment StartX=-3475 StartY=187 StartZ=0 EndX=-1045 EndY=187 EndZ=0
FEATURE [Part::FeaturePython] Rebar013  label="StraightRebar008"  # Arch/BIM 110 (typed FeaturePython)
  Amount = 2
  AmountCheck = true
  Base = -> Sketch334
  Cover = 38
  CoverAlong = Top Side
  Diameter = 12
  Direction = (0,0,0)
  Distance = 0
  FrontCover = 38
  HorizontalArea = 0
  Host = -> Wall274
  IfcData = IfcUID=0IhfJ24H12sPMtpoimhsX_
  IfcType = 110
  LeftBottomCover = 60
  Length = 2430
  Mark = StraightRebar008
  Material = -> Material010
  MoveBase = false
  MoveWithHost = false
  OffsetEnd = 44
  OffsetStart = 44
  Orientation = Horizontal
  PerimeterLength = 0
  Placement = pos=(0,35,0) rot=(0,0,1;0rad)
  PlacementList = 2 placements: [(44,0,0),(236,0,0)]
  RebarShape = 0
  RightTopCover = 60
  Rounding = 0
  Spacing = 192
  TotalLength = 4860
  TrueSpacing = 2
  VerticalArea = 0
FEATURE [App::DocumentObjectGroupPython] TopReinforcement004  # scripted group (container) (typed FeaturePython)
  Group = -> [Rebar013]
  LayerSpacing = [30]
  NumberDiameterOffset = 2#12.0@60.0
  TopRebars = -> [Rebar013]
FEATURE [Sketcher::SketchObject] Sketch335
  FullyConstrained = false
  MapMode = 5
  Placement = pos=(12570,0,2572) rot=(0.57735,-0.57735,-0.57735;2.0944rad)
  Support = -> [Wall274]
  sketch-geometry (1):
    g0: LineSegment StartX=-3475 StartY=45 StartZ=0 EndX=-1045 EndY=45 EndZ=0
FEATURE [Part::FeaturePython] Rebar014  label="StraightRebar009"  # Arch/BIM 110 (typed FeaturePython)
  Amount = 2
  AmountCheck = true
  Base = -> Sketch335
  Cover = 38
  CoverAlong = Bottom Side
  Diameter = 14
  Direction = (0,0,0)
  Distance = 0
  FrontCover = 38
  HorizontalArea = 0
  Host = -> Wall274
  IfcData = IfcUID=38s843Wp98lgFtcANgZxJN
  IfcType = 110
  LeftBottomCover = 60
  Length = 2430
  Mark = StraightRebar009
  Material = -> Material010
  MoveBase = false
  MoveWithHost = false
  OffsetEnd = 45
  OffsetStart = 45
  Orientation = Horizontal
  PerimeterLength = 0
  Placement = pos=(0,35,0) rot=(0,0,1;0rad)
  PlacementList = 2 placements: [(45,0,0),(235,0,0)]
  RebarShape = 0
  RightTopCover = 60
  Rounding = 0
  Spacing = 190
  TotalLength = 4860
  TrueSpacing = 2
  VerticalArea = 0
FEATURE [App::DocumentObjectGroupPython] BottomReinforcement004  # scripted group (container) (typed FeaturePython)
  BottomRebars = -> [Rebar014]
  Group = -> [Rebar014]
  LayerSpacing = [30]
  NumberDiameterOffset = 2#14.0@60.0
FEATURE [App::DocumentObjectGroupPython] BeamReinforcement004  # scripted group (container) (typed FeaturePython)
  Group = -> [Stirrups004,TopReinforcement004,BottomReinforcement004]
  ReinforcementGroups = -> [Stirrups004,TopReinforcement004,BottomReinforcement004]
FEATURE [Part::Part2DObjectPython] Wire875  # Draft 2D object (typed FeaturePython)
  Area = 0
  ChamferSize = 0
  Closed = false
  End = (4194.27,7564.85,2727.59)
  FilletRadius = 0
  Length = 898.352
  MakeFace = true
  Placement = pos=(-75,15,0) rot=(0,0,1;0rad)
  Points = (7) [(4282.15,7565.41,2743.15),(4280,7524,2784.56),(4277.85,7524,2606),(4275.71,7736,2606),(4273.56,7736,2769),(4271.41,7508.44,2769),+1 more]
  Start = (4207.15,7580.41,2743.15)
  Subdivisions = 0
  Support = -> [Wall270]
FEATURE [Part::FeaturePython] Rebar015  label="Stirrup005"  # Arch/BIM 110 (typed FeaturePython)
  Amount = 10
  AmountCheck = false
  Base = -> Wire875
  BentAngle = 135
  BentFactor = 4
  BottomCover = 30
  Diameter = 8
  Direction = (-1,0,0)
  Distance = 0
  FrontCover = 100
  HorizontalArea = 0
  Host = -> Wall270
  IfcData = IfcUID=2RF9jp$wz08A9VdwpHTXzZ
  IfcType = 110
  LeftCover = 30
  Length = 898.352
  Mark = Stirrup005
  Material = -> Material010
  MoveBase = false
  MoveWithHost = false
  OffsetEnd = 104
  OffsetStart = 104
  PerimeterLength = 0
  PlacementList = 10 placements: arithmetic series from (-104,0,0) step (-251.556,0,0) to (-2368,0,0)
  RebarShape = 3
  RightCover = 30
  Rounding = 1.375
  Spacing = 251.556
  TopCover = 30
  TotalLength = 8983.52
  TrueSpacing = 300
  VerticalArea = 0
FEATURE [App::DocumentObjectGroupPython] Stirrups005  # scripted group (container) (typed FeaturePython)
  Group = -> [Rebar015]
  Stirrups = -> [Rebar015]
  StirrupsConfiguration = Two Legged Stirrups
FEATURE [Sketcher::SketchObject] Sketch336
  FullyConstrained = false
  MapMode = 5
  Placement = pos=(0,7505,2572) rot=(1,0,0;1.5708rad)
  Support = -> [Wall270]
  sketch-geometry (1):
    g0: LineSegment StartX=1790 StartY=187 StartZ=0 EndX=4220 EndY=187 EndZ=0
FEATURE [Part::FeaturePython] Rebar016  label="StraightRebar010"  # Arch/BIM 110 (typed FeaturePython)
  Amount = 2
  AmountCheck = true
  Base = -> Sketch336
  Cover = 38
  CoverAlong = Top Side
  Diameter = 12
  Direction = (0,0,0)
  Distance = 0
  FrontCover = 38
  HorizontalArea = 0
  Host = -> Wall270
  IfcData = IfcUID=1nXP$0rpbACR1K2SbosHQt
  IfcType = 110
  LeftBottomCover = 60
  Length = 2430
  Mark = StraightRebar010
  Material = -> Material010
  MoveBase = false
  MoveWithHost = false
  OffsetEnd = 44
  OffsetStart = 44
  Orientation = Horizontal
  PerimeterLength = 0
  Placement = pos=(-50,0,0) rot=(0,0,1;0rad)
  PlacementList = 2 placements: [(0,44,-9.76996e-15),(0,236,-5.24025e-14)]
  RebarShape = 0
  RightTopCover = 60
  Rounding = 0
  Spacing = 192
  TotalLength = 4860
  TrueSpacing = 2
  VerticalArea = 0
FEATURE [App::DocumentObjectGroupPython] TopReinforcement005  # scripted group (container) (typed FeaturePython)
  Group = -> [Rebar016]
  LayerSpacing = [30]
  NumberDiameterOffset = 2#12.0@60.0
  TopRebars = -> [Rebar016]
FEATURE [Sketcher::SketchObject] Sketch337
  FullyConstrained = false
  MapMode = 5
  Placement = pos=(0,7505,2572) rot=(1,0,0;1.5708rad)
  Support = -> [Wall270]
  sketch-geometry (1):
    g0: LineSegment StartX=1790 StartY=45 StartZ=0 EndX=4220 EndY=45 EndZ=0
FEATURE [Part::FeaturePython] Rebar017  label="StraightRebar011"  # Arch/BIM 110 (typed FeaturePython)
  Amount = 2
  AmountCheck = true
  Base = -> Sketch337
  Cover = 38
  CoverAlong = Bottom Side
  Diameter = 14
  Direction = (0,0,0)
  Distance = 0
  FrontCover = 38
  HorizontalArea = 0
  Host = -> Wall270
  IfcData = IfcUID=3zK0LNm4n3mO5pKUyneaxe
  IfcType = 110
  LeftBottomCover = 60
  Length = 2430
  Mark = StraightRebar011
  Material = -> Material010
  MoveBase = false
  MoveWithHost = false
  OffsetEnd = 45
  OffsetStart = 45
  Orientation = Horizontal
  PerimeterLength = 0
  Placement = pos=(-50,0,0) rot=(0,0,1;0rad)
  PlacementList = 2 placements: [(0,45,-9.99201e-15),(0,235,-5.21805e-14)]
  RebarShape = 0
  RightTopCover = 60
  Rounding = 0
  Spacing = 190
  TotalLength = 4860
  TrueSpacing = 2
  VerticalArea = 0
FEATURE [App::DocumentObjectGroupPython] BottomReinforcement005  # scripted group (container) (typed FeaturePython)
  BottomRebars = -> [Rebar017]
  Group = -> [Rebar017]
  LayerSpacing = [30]
  NumberDiameterOffset = 2#14.0@60.0
FEATURE [App::DocumentObjectGroupPython] BeamReinforcement005  # scripted group (container) (typed FeaturePython)
  Group = -> [Stirrups005,TopReinforcement005,BottomReinforcement005]
  ReinforcementGroups = -> [Stirrups005,TopReinforcement005,BottomReinforcement005]
FEATURE [Part::Part2DObjectPython] Wire876  # Draft 2D object (typed FeaturePython)
  Area = 0
  ChamferSize = 0
  Closed = false
  End = (-270.444,3559.33,2729.3)
  FilletRadius = 0
  Length = 890.697
  MakeFace = true
  Placement = pos=(0,-100,0) rot=(0,0,1;0rad)
  Points = (7) [(-256.302,3672.13,2743.44),(-296,3670,2783.14),(-296,3667.87,2606),(-84,3665.73,2606),(-84,3663.6,2769),(-310.142,3661.47,2769),+1 more]
  Start = (-256.302,3572.13,2743.44)
  Subdivisions = 0
  Support = -> [Wall275]
FEATURE [Part::FeaturePython] Rebar018  label="Stirrup006"  # Arch/BIM 110 (typed FeaturePython)
  Amount = 8
  AmountCheck = false
  Base = -> Wire876
  BentAngle = 135
  BentFactor = 4
  BottomCover = 30
  Diameter = 8
  Direction = (0,-1,0)
  Distance = 0
  FrontCover = 100
  HorizontalArea = 0
  Host = -> Wall275
  IfcData = IfcUID=0GO4wNkB97lOlqTACpJZwt
  IfcType = 110
  LeftCover = 30
  Length = 890.697
  Mark = Stirrup006
  Material = -> Material010
  MoveBase = false
  MoveWithHost = false
  OffsetEnd = 104
  OffsetStart = 104
  PerimeterLength = 0
  PlacementList = 8 placements: arithmetic series from (0,-104,0) step (0,-249.143,0) to (0,-1848,0)
  RebarShape = 3
  RightCover = 30
  Rounding = 1.25
  Spacing = 249.143
  TopCover = 30
  TotalLength = 7125.58
  TrueSpacing = 300
  VerticalArea = 0
FEATURE [App::DocumentObjectGroupPython] Stirrups006  # scripted group (container) (typed FeaturePython)
  Group = -> [Rebar018]
  Stirrups = -> [Rebar018]
  StirrupsConfiguration = Two Legged Stirrups
FEATURE [Sketcher::SketchObject] Sketch338
  FullyConstrained = false
  MapMode = 5
  Placement = pos=(-50,0,2572) rot=(0.57735,0.57735,0.57735;2.0944rad)
  Support = -> [Wall275]
  sketch-geometry (1):
    g0: LineSegment StartX=1690 StartY=187 StartZ=0 EndX=3610 EndY=187 EndZ=0
FEATURE [Part::FeaturePython] Rebar019  label="StraightRebar012"  # Arch/BIM 110 (typed FeaturePython)
  Amount = 2
  AmountCheck = true
  Base = -> Sketch338
  Cover = 38
  CoverAlong = Top Side
  Diameter = 12
  Direction = (0,0,0)
  Distance = 0
  FrontCover = 38
  HorizontalArea = 0
  Host = -> Wall275
  IfcData = IfcUID=3m1D0xJN5Ey8da60xgpDpj
  IfcType = 110
  LeftBottomCover = 60
  Length = 1920
  Mark = StraightRebar012
  Material = -> Material010
  MoveBase = false
  MoveWithHost = false
  OffsetEnd = 44
  OffsetStart = 44
  Orientation = Horizontal
  PerimeterLength = 0
  Placement = pos=(0,-80,0) rot=(0,0,1;0rad)
  PlacementList = 2 placements: [(-44,0,0),(-236,0,0)]
  RebarShape = 0
  RightTopCover = 60
  Rounding = 0
  Spacing = 192
  TotalLength = 3840
  TrueSpacing = 2
  VerticalArea = 0
FEATURE [App::DocumentObjectGroupPython] TopReinforcement006  # scripted group (container) (typed FeaturePython)
  Group = -> [Rebar019]
  LayerSpacing = [30]
  NumberDiameterOffset = 2#12.0@60.0
  TopRebars = -> [Rebar019]
FEATURE [Sketcher::SketchObject] Sketch339
  FullyConstrained = false
  MapMode = 5
  Placement = pos=(-50,0,2572) rot=(0.57735,0.57735,0.57735;2.0944rad)
  Support = -> [Wall275]
  sketch-geometry (1):
    g0: LineSegment StartX=1690 StartY=44 StartZ=0 EndX=3610 EndY=44 EndZ=0
FEATURE [Part::FeaturePython] Rebar020  label="StraightRebar013"  # Arch/BIM 110 (typed FeaturePython)
  Amount = 2
  AmountCheck = true
  Base = -> Sketch339
  Cover = 38
  CoverAlong = Bottom Side
  Diameter = 12
  Direction = (0,0,0)
  Distance = 0
  FrontCover = 38
  HorizontalArea = 0
  Host = -> Wall275
  IfcData = IfcUID=1s9A5d1rn8SeYaByjManJ6
  IfcType = 110
  LeftBottomCover = 60
  Length = 1920
  Mark = StraightRebar013
  Material = -> Material010
  MoveBase = false
  MoveWithHost = false
  OffsetEnd = 44
  OffsetStart = 44
  Orientation = Horizontal
  PerimeterLength = 0
  Placement = pos=(0,-80,0) rot=(0,0,1;0rad)
  PlacementList = 2 placements: [(-44,0,0),(-236,0,0)]
  RebarShape = 0
  RightTopCover = 60
  Rounding = 0
  Spacing = 192
  TotalLength = 3840
  TrueSpacing = 2
  VerticalArea = 0
FEATURE [App::DocumentObjectGroupPython] BottomReinforcement006  # scripted group (container) (typed FeaturePython)
  BottomRebars = -> [Rebar020]
  Group = -> [Rebar020]
  LayerSpacing = [30]
  NumberDiameterOffset = 2#12.0@60.0
FEATURE [App::DocumentObjectGroupPython] BeamReinforcement006  # scripted group (container) (typed FeaturePython)
  Group = -> [Stirrups006,TopReinforcement006,BottomReinforcement006]
  ReinforcementGroups = -> [Stirrups006,TopReinforcement006,BottomReinforcement006]
FEATURE [Part::Part2DObjectPython] Wire877  # Draft 2D object (typed FeaturePython)
  Area = 0
  ChamferSize = 0
  Closed = false
  End = (8454.33,-265.444,2498.3)
  FilletRadius = 0
  Length = 890.697
  MakeFace = true
  Placement = pos=(105,-15,0) rot=(0,0,1;0rad)
  Points = (7) [(8362.13,-236.302,2512.44),(8360,-276,2552.14),(8357.87,-276,2375),(8355.73,-64,2375),(8353.6,-64,2538),(8351.47,-290.142,2538),+1 more]
  Start = (8467.13,-251.302,2512.44)
  Subdivisions = 0
  Support = -> [Wall273]
FEATURE [Part::FeaturePython] Rebar021  label="Stirrup007"  # Arch/BIM 110 (typed FeaturePython)
  Amount = 5
  AmountCheck = false
  Base = -> Wire877
  BentAngle = 135
  BentFactor = 4
  BottomCover = 30
  Diameter = 8
  Direction = (-1,0,0)
  Distance = 0
  FrontCover = 100
  HorizontalArea = 0
  Host = -> Wall273
  IfcData = IfcUID=2sOpwtOeP6d93qeK3TWBYN
  IfcType = 110
  LeftCover = 30
  Length = 890.697
  Mark = Stirrup007
  Material = -> Material010
  MoveBase = false
  MoveWithHost = false
  OffsetEnd = 104
  OffsetStart = 104
  PerimeterLength = 0
  PlacementList = 5 placements: arithmetic series from (-104,0,0) step (-241,0,0) to (-1068,0,0)
  RebarShape = 3
  RightCover = 30
  Rounding = 1.25
  Spacing = 241
  TopCover = 30
  TotalLength = 4453.49
  TrueSpacing = 300
  VerticalArea = 0
FEATURE [App::DocumentObjectGroupPython] Stirrups007  # scripted group (container) (typed FeaturePython)
  Group = -> [Rebar021]
  Stirrups = -> [Rebar021]
  StirrupsConfiguration = Two Legged Stirrups
FEATURE [Sketcher::SketchObject] Sketch340
  FullyConstrained = false
  MapMode = 5
  Placement = pos=(0,-325,2341) rot=(1,0,0;1.5708rad)
  Support = -> [Wall273]
  sketch-geometry (1):
    g0: LineSegment StartX=7280 StartY=187 StartZ=0 EndX=8300 EndY=187 EndZ=0
FEATURE [Part::FeaturePython] Rebar022  label="StraightRebar014"  # Arch/BIM 110 (typed FeaturePython)
  Amount = 2
  AmountCheck = true
  Base = -> Sketch340
  Cover = 38
  CoverAlong = Top Side
  Diameter = 12
  Direction = (0,0,0)
  Distance = 0
  FrontCover = 38
  HorizontalArea = 0
  Host = -> Wall273
  IfcData = IfcUID=1vMcNoj0HEmRp1d9MJzP$J
  IfcType = 110
  LeftBottomCover = 60
  Length = 1020
  Mark = StraightRebar014
  Material = -> Material010
  MoveBase = false
  MoveWithHost = false
  OffsetEnd = 44
  OffsetStart = 44
  Orientation = Horizontal
  PerimeterLength = 0
  Placement = pos=(75,7.1e-15,0) rot=(0,0,1;0rad)
  PlacementList = 2 placements: [(0,44,-9.76996e-15),(0,236,-5.24025e-14)]
  RebarShape = 0
  RightTopCover = 60
  Rounding = 0
  Spacing = 192
  TotalLength = 2040
  TrueSpacing = 2
  VerticalArea = 0
FEATURE [App::DocumentObjectGroupPython] TopReinforcement007  # scripted group (container) (typed FeaturePython)
  Group = -> [Rebar022]
  LayerSpacing = [30]
  NumberDiameterOffset = 2#12.0@60.0
  TopRebars = -> [Rebar022]
FEATURE [Sketcher::SketchObject] Sketch341
  FullyConstrained = false
  MapMode = 5
  Placement = pos=(0,-325,2341) rot=(1,0,0;1.5708rad)
  Support = -> [Wall273]
  sketch-geometry (1):
    g0: LineSegment StartX=7280 StartY=44 StartZ=0 EndX=8300 EndY=44 EndZ=0
FEATURE [Part::FeaturePython] Rebar023  label="StraightRebar015"  # Arch/BIM 110 (typed FeaturePython)
  Amount = 2
  AmountCheck = true
  Base = -> Sketch341
  Cover = 38
  CoverAlong = Bottom Side
  Diameter = 12
  Direction = (0,0,0)
  Distance = 0
  FrontCover = 38
  HorizontalArea = 0
  Host = -> Wall273
  IfcData = IfcUID=3uc1wwna11_hIpa5m3v9lF
  IfcType = 110
  LeftBottomCover = 60
  Length = 1020
  Mark = StraightRebar015
  Material = -> Material010
  MoveBase = false
  MoveWithHost = false
  OffsetEnd = 44
  OffsetStart = 44
  Orientation = Horizontal
  PerimeterLength = 0
  Placement = pos=(75,7.1e-15,0) rot=(0,0,1;0rad)
  PlacementList = 2 placements: [(0,44,-9.76996e-15),(0,236,-5.24025e-14)]
  RebarShape = 0
  RightTopCover = 60
  Rounding = 0
  Spacing = 192
  TotalLength = 2040
  TrueSpacing = 2
  VerticalArea = 0
FEATURE [App::DocumentObjectGroupPython] BottomReinforcement007  # scripted group (container) (typed FeaturePython)
  BottomRebars = -> [Rebar023]
  Group = -> [Rebar023]
  LayerSpacing = [30]
  NumberDiameterOffset = 2#12.0@60.0
FEATURE [App::DocumentObjectGroupPython] BeamReinforcement007  # scripted group (container) (typed FeaturePython)
  Group = -> [Stirrups007,TopReinforcement007,BottomReinforcement007]
  ReinforcementGroups = -> [Stirrups007,TopReinforcement007,BottomReinforcement007]
FEATURE [Part::Part2DObjectPython] Wire878  # Draft 2D object (typed FeaturePython)
  Area = 0
  ChamferSize = 0
  Closed = false
  End = (6969.33,-265.444,2498.3)
  FilletRadius = 0
  Length = 890.697
  MakeFace = true
  Placement = pos=(15,-15,0) rot=(0,0,1;0rad)
  Points = (7) [(6967.13,-236.302,2512.44),(6965,-276,2552.14),(6962.87,-276,2375),(6960.73,-64,2375),(6958.6,-64,2538),(6956.47,-290.142,2538),+1 more]
  Start = (6982.13,-251.302,2512.44)
  Subdivisions = 0
  Support = -> [Wall272]
FEATURE [Part::FeaturePython] Rebar024  label="Stirrup008"  # Arch/BIM 110 (typed FeaturePython)
  Amount = 7
  AmountCheck = false
  Base = -> Wire878
  BentAngle = 135
  BentFactor = 4
  BottomCover = 30
  Diameter = 8
  Direction = (-1,0,0)
  Distance = 0
  FrontCover = 100
  HorizontalArea = 0
  Host = -> Wall272
  IfcData = IfcUID=0LnHNELLX3fuNNWSVyCMGl
  IfcType = 110
  LeftCover = 30
  Length = 890.697
  Mark = Stirrup008
  Material = -> Material010
  MoveBase = false
  MoveWithHost = false
  OffsetEnd = 104
  OffsetStart = 104
  PerimeterLength = 0
  PlacementList = 7 placements: arithmetic series from (-104,0,0) step (-225.667,0,0) to (-1458,0,0)
  RebarShape = 3
  RightCover = 30
  Rounding = 1.25
  Spacing = 225.667
  TopCover = 30
  TotalLength = 6234.88
  TrueSpacing = 300
  VerticalArea = 0
FEATURE [App::DocumentObjectGroupPython] Stirrups008  # scripted group (container) (typed FeaturePython)
  Group = -> [Rebar024]
  Stirrups = -> [Rebar024]
  StirrupsConfiguration = Two Legged Stirrups
FEATURE [Sketcher::SketchObject] Sketch342
  FullyConstrained = false
  MapMode = 5
  Placement = pos=(0,-325,2341) rot=(1,0,0;1.5708rad)
  Support = -> [Wall272]
  sketch-geometry (1):
    g0: LineSegment StartX=5495 StartY=187 StartZ=0 EndX=6905 EndY=187 EndZ=0
FEATURE [Part::FeaturePython] Rebar025  label="StraightRebar016"  # Arch/BIM 110 (typed FeaturePython)
  Amount = 2
  AmountCheck = true
  Base = -> Sketch342
  Cover = 38
  CoverAlong = Top Side
  Diameter = 12
  Direction = (0,0,0)
  Distance = 0
  FrontCover = 38
  HorizontalArea = 0
  Host = -> Wall272
  IfcData = IfcUID=1KTuHzywvETe2xYfKlmI5q
  IfcType = 110
  LeftBottomCover = 60
  Length = 1410
  Mark = StraightRebar016
  Material = -> Material010
  MoveBase = false
  MoveWithHost = false
  OffsetEnd = 44
  OffsetStart = 44
  Orientation = Horizontal
  PerimeterLength = 0
  Placement = pos=(-5,0,0) rot=(0,0,1;0rad)
  PlacementList = 2 placements: [(0,44,-9.76996e-15),(0,236,-5.24025e-14)]
  RebarShape = 0
  RightTopCover = 60
  Rounding = 0
  Spacing = 192
  TotalLength = 2820
  TrueSpacing = 2
  VerticalArea = 0
FEATURE [App::DocumentObjectGroupPython] TopReinforcement008  # scripted group (container) (typed FeaturePython)
  Group = -> [Rebar025]
  LayerSpacing = [30]
  NumberDiameterOffset = 2#12.0@60.0
  TopRebars = -> [Rebar025]
FEATURE [Sketcher::SketchObject] Sketch343
  FullyConstrained = false
  MapMode = 5
  Placement = pos=(0,-325,2341) rot=(1,0,0;1.5708rad)
  Support = -> [Wall272]
  sketch-geometry (1):
    g0: LineSegment StartX=5495 StartY=44 StartZ=0 EndX=6905 EndY=44 EndZ=0
FEATURE [Part::FeaturePython] Rebar026  label="StraightRebar017"  # Arch/BIM 110 (typed FeaturePython)
  Amount = 2
  AmountCheck = true
  Base = -> Sketch343
  Cover = 38
  CoverAlong = Bottom Side
  Diameter = 12
  Direction = (0,0,0)
  Distance = 0
  FrontCover = 38
  HorizontalArea = 0
  Host = -> Wall272
  IfcData = IfcUID=12i$N8lpL6MOoc$XX$mBTR
  IfcType = 110
  LeftBottomCover = 60
  Length = 1410
  Mark = StraightRebar017
  Material = -> Material010
  MoveBase = false
  MoveWithHost = false
  OffsetEnd = 44
  OffsetStart = 44
  Orientation = Horizontal
  PerimeterLength = 0
  Placement = pos=(-5,0,0) rot=(0,0,1;0rad)
  PlacementList = 2 placements: [(0,44,-9.76996e-15),(0,236,-5.24025e-14)]
  RebarShape = 0
  RightTopCover = 60
  Rounding = 0
  Spacing = 192
  TotalLength = 2820
  TrueSpacing = 2
  VerticalArea = 0
FEATURE [App::DocumentObjectGroupPython] BottomReinforcement008  # scripted group (container) (typed FeaturePython)
  BottomRebars = -> [Rebar026]
  Group = -> [Rebar026]
  LayerSpacing = [30]
  NumberDiameterOffset = 2#12.0@60.0
FEATURE [App::DocumentObjectGroupPython] BeamReinforcement008  # scripted group (container) (typed FeaturePython)
  Group = -> [Stirrups008,TopReinforcement008,BottomReinforcement008]
  ReinforcementGroups = -> [Stirrups008,TopReinforcement008,BottomReinforcement008]
FEATURE [Part::Part2DObjectPython] Wire879  # Draft 2D object (typed FeaturePython)
  Area = 0
  ChamferSize = 0
  Closed = false
  End = (5069.33,-265.444,2498.3)
  FilletRadius = 0
  Length = 890.697
  MakeFace = true
  Placement = pos=(-100,-15,0) rot=(0,0,1;0rad)
  Points = (7) [(5182.13,-236.302,2512.44),(5180,-276,2552.14),(5177.87,-276,2375),(5175.73,-64,2375),(5173.6,-64,2538),(5171.47,-290.142,2538),+1 more]
  Start = (5082.13,-251.302,2512.44)
  Subdivisions = 0
  Support = -> [Wall279]
FEATURE [Part::FeaturePython] Rebar027  label="Stirrup009"  # Arch/BIM 110 (typed FeaturePython)
  Amount = 5
  AmountCheck = false
  Base = -> Wire879
  BentAngle = 135
  BentFactor = 4
  BottomCover = 30
  Diameter = 8
  Direction = (-1,0,0)
  Distance = 0
  FrontCover = 100
  HorizontalArea = 0
  Host = -> Wall279
  IfcData = IfcUID=31rsnq52n3DxwBSiGvx1jF
  IfcType = 110
  LeftCover = 30
  Length = 890.697
  Mark = Stirrup009
  Material = -> Material010
  MoveBase = false
  MoveWithHost = false
  OffsetEnd = 104
  OffsetStart = 104
  PerimeterLength = 0
  PlacementList = 5 placements: arithmetic series from (-104,0,0) step (-241,0,0) to (-1068,0,0)
  RebarShape = 3
  RightCover = 30
  Rounding = 1.25
  Spacing = 241
  TopCover = 30
  TotalLength = 4453.49
  TrueSpacing = 300
  VerticalArea = 0
FEATURE [App::DocumentObjectGroupPython] Stirrups009  # scripted group (container) (typed FeaturePython)
  Group = -> [Rebar027]
  Stirrups = -> [Rebar027]
  StirrupsConfiguration = Two Legged Stirrups
FEATURE [Sketcher::SketchObject] Sketch344
  FullyConstrained = false
  MapMode = 5
  Placement = pos=(0,-325,2341) rot=(1,0,0;1.5708rad)
  Support = -> [Wall279]
  sketch-geometry (1):
    g0: LineSegment StartX=4100 StartY=187 StartZ=0 EndX=5120 EndY=187 EndZ=0
FEATURE [Part::FeaturePython] Rebar028  label="StraightRebar018"  # Arch/BIM 110 (typed FeaturePython)
  Amount = 2
  AmountCheck = true
  Base = -> Sketch344
  Cover = 38
  CoverAlong = Top Side
  Diameter = 12
  Direction = (0,0,0)
  Distance = 0
  FrontCover = 38
  HorizontalArea = 0
  Host = -> Wall279
  IfcData = IfcUID=3AflJxepXCVOa0re2f_fXP
  IfcType = 110
  LeftBottomCover = 60
  Length = 1020
  Mark = StraightRebar018
  Material = -> Material010
  MoveBase = false
  MoveWithHost = false
  OffsetEnd = 44
  OffsetStart = 44
  Orientation = Horizontal
  PerimeterLength = 0
  Placement = pos=(-125,-7.1e-15,0) rot=(0,0,1;0rad)
  PlacementList = 2 placements: [(0,44,-9.76996e-15),(0,236,-5.24025e-14)]
  RebarShape = 0
  RightTopCover = 60
  Rounding = 0
  Spacing = 192
  TotalLength = 2040
  TrueSpacing = 2
  VerticalArea = 0
FEATURE [App::DocumentObjectGroupPython] TopReinforcement009  # scripted group (container) (typed FeaturePython)
  Group = -> [Rebar028]
  LayerSpacing = [30]
  NumberDiameterOffset = 2#12.0@60.0
  TopRebars = -> [Rebar028]
FEATURE [Sketcher::SketchObject] Sketch345
  FullyConstrained = false
  MapMode = 5
  Placement = pos=(0,-325,2341) rot=(1,0,0;1.5708rad)
  Support = -> [Wall279]
  sketch-geometry (1):
    g0: LineSegment StartX=4100 StartY=44 StartZ=0 EndX=5120 EndY=44 EndZ=0
FEATURE [Part::FeaturePython] Rebar029  label="StraightRebar019"  # Arch/BIM 110 (typed FeaturePython)
  Amount = 2
  AmountCheck = true
  Base = -> Sketch345
  Cover = 38
  CoverAlong = Bottom Side
  Diameter = 12
  Direction = (0,0,0)
  Distance = 0
  FrontCover = 38
  HorizontalArea = 0
  Host = -> Wall279
  IfcData = IfcUID=2gFM5ezKfE0viRuku9MTTs
  IfcType = 110
  LeftBottomCover = 60
  Length = 1020
  Mark = StraightRebar019
  Material = -> Material010
  MoveBase = false
  MoveWithHost = false
  OffsetEnd = 44
  OffsetStart = 44
  Orientation = Horizontal
  PerimeterLength = 0
  Placement = pos=(-125,-7.1e-15,0) rot=(0,0,1;0rad)
  PlacementList = 2 placements: [(0,44,-9.76996e-15),(0,236,-5.24025e-14)]
  RebarShape = 0
  RightTopCover = 60
  Rounding = 0
  Spacing = 192
  TotalLength = 2040
  TrueSpacing = 2
  VerticalArea = 0
FEATURE [App::DocumentObjectGroupPython] BottomReinforcement009  # scripted group (container) (typed FeaturePython)
  BottomRebars = -> [Rebar029]
  Group = -> [Rebar029]
  LayerSpacing = [30]
  NumberDiameterOffset = 2#12.0@60.0
FEATURE [App::DocumentObjectGroupPython] BeamReinforcement009  # scripted group (container) (typed FeaturePython)
  Group = -> [Stirrups009,TopReinforcement009,BottomReinforcement009]
  ReinforcementGroups = -> [Stirrups009,TopReinforcement009,BottomReinforcement009]
FEATURE [App::DocumentObjectGroupPython] Stirrups010  # scripted group (container) (typed FeaturePython)
  StirrupsConfiguration = Two Legged Stirrups
FEATURE [App::DocumentObjectGroupPython] TopReinforcement010  # scripted group (container) (typed FeaturePython)
  LayerSpacing = [30]
  NumberDiameterOffset = 2#12.0@100.0
FEATURE [App::DocumentObjectGroupPython] BottomReinforcement010  # scripted group (container) (typed FeaturePython)
  LayerSpacing = [30]
  NumberDiameterOffset = 2#12.0@100.0
FEATURE [App::DocumentObjectGroupPython] BeamReinforcement010  # scripted group (container) (typed FeaturePython)
  Group = -> [Stirrups010,TopReinforcement010,BottomReinforcement010]
  ReinforcementGroups = -> [Stirrups010,TopReinforcement010,BottomReinforcement010]
FEATURE [App::DocumentObjectGroupPython] Stirrups011  # scripted group (container) (typed FeaturePython)
  StirrupsConfiguration = Two Legged Stirrups
FEATURE [App::DocumentObjectGroupPython] TopReinforcement011  # scripted group (container) (typed FeaturePython)
  LayerSpacing = [30]
  NumberDiameterOffset = 2#12.0@60.0
FEATURE [App::DocumentObjectGroupPython] BottomReinforcement011  # scripted group (container) (typed FeaturePython)
  LayerSpacing = [30]
  NumberDiameterOffset = 2#12.0@60.0
FEATURE [App::DocumentObjectGroupPython] BeamReinforcement011  # scripted group (container) (typed FeaturePython)
  Group = -> [Stirrups011,TopReinforcement011,BottomReinforcement011]
  ReinforcementGroups = -> [Stirrups011,TopReinforcement011,BottomReinforcement011]
FEATURE [Part::Part2DObjectPython] Line1579  # Draft 2D object (typed FeaturePython)
  Area = 0
  ChamferSize = 0
  Closed = false
  End = (12870,-345,0)
  FilletRadius = 0
  Length = 13220
  MakeFace = true
  Placement = pos=(-350,-345,0) rot=(0,0,1;0rad)
  Points = (2) [(0,0,0),(13220,3.97904e-13,0)]
  Start = (-350,-345,0)
  Subdivisions = 0
FEATURE [Part::FeaturePython] Wall291  label="Армпояс001"  # Arch/BIM 166 (typed FeaturePython)
  Align = 1
  Area = 1850800
  Base = -> Line1579
  BlockHeight = 0
  BlockLength = 0
  CountBroken = 0
  CountEntire = 0
  Face = 0
  GlobalId = 16TJfFXcP3X9E$rkeb5rWP
  Height = 140
  HorizontalArea = 2.3796e+06
  IfcData = IfcUID=16TJfFXcP3X9E$rkeb5rWP,+2 more (map truncated)
  IfcType = 166
  Joint = 0
  Length = 13220
  MakeBlocks = false
  Material = -> Material001
  MoveBase = false
  MoveWithHost = false
  Normal = (0,0,0)
  OffsetFirst = 0
  OffsetSecond = 0
  PerimeterLength = 26800
  Placement = pos=(0,0,3493) rot=(0,0,1;0rad)
  PredefinedType = 0
  VerticalArea = 3.752e+06
  Width = 180
FEATURE [Part::Part2DObjectPython] Line1580  # Draft 2D object (typed FeaturePython)
  Area = 0
  ChamferSize = 0
  Closed = true
  End = (-350,7805,0)
  FilletRadius = 0
  Length = 13220
  MakeFace = true
  Placement = pos=(-350,-315,0) rot=(0,0,1;0rad)
  Points = (2) [(13220,8120,0),(0,8120,0)]
  Start = (12870,7805,0)
  Subdivisions = 0
FEATURE [Part::FeaturePython] Wall292  label="Армпояс002"  # Arch/BIM 166 (typed FeaturePython)
  Align = 1
  Area = 1850800
  Base = -> Line1580
  BlockHeight = 0
  BlockLength = 0
  CountBroken = 0
  CountEntire = 0
  Face = 0
  GlobalId = 0QynjLo$PD1uHQZI1aWnKI
  Height = 140
  HorizontalArea = 2.3796e+06
  IfcData = IfcUID=0QynjLo$PD1uHQZI1aWnKI,+2 more (map truncated)
  IfcType = 166
  Joint = 0
  Length = 13220
  MakeBlocks = false
  Material = -> Material001
  MoveBase = false
  MoveWithHost = false
  Normal = (0,0,0)
  OffsetFirst = 0
  OffsetSecond = 0
  PerimeterLength = 26800
  Placement = pos=(0,0,3493) rot=(0,0,1;0rad)
  PredefinedType = 0
  VerticalArea = 3.752e+06
  Width = 180
FEATURE [Part::Part2DObjectPython] Line1581  # Draft 2D object (typed FeaturePython)
  Area = 0
  ChamferSize = 0
  Closed = true
  End = (-350,-165,0)
  FilletRadius = 0
  Length = 7790
  MakeFace = true
  Placement = pos=(-350,-330,0) rot=(0,0,1;0rad)
  Points = (2) [(0,7955,0),(0,165,0)]
  Start = (-350,7625,0)
  Subdivisions = 0
FEATURE [Part::FeaturePython] Wall293  label="Армпояс003"  # Arch/BIM 166 (typed FeaturePython)
  Align = 1
  Area = 1090600
  Base = -> Line1581
  BlockHeight = 0
  BlockLength = 0
  CountBroken = 0
  CountEntire = 0
  Face = 0
  GlobalId = 3eSRug_un8VgtGtFI5hYOD
  Height = 140
  HorizontalArea = 1402200
  IfcData = IfcUID=3eSRug_un8VgtGtFI5hYOD,+2 more (map truncated)
  IfcType = 166
  Joint = 0
  Length = 7790
  MakeBlocks = false
  Material = -> Material001
  MoveBase = false
  MoveWithHost = false
  Normal = (0,0,0)
  OffsetFirst = 0
  OffsetSecond = 0
  PerimeterLength = 15940
  Placement = pos=(0,0,3493) rot=(0,0,1;0rad)
  PredefinedType = 0
  VerticalArea = 2231600
  Width = 180
FEATURE [Part::Part2DObjectPython] Line1582  # Draft 2D object (typed FeaturePython)
  Area = 0
  ChamferSize = 0
  Closed = true
  End = (12870,7625,0)
  FilletRadius = 0
  Length = 7790
  MakeFace = true
  Placement = pos=(-350,-330,0) rot=(0,0,1;0rad)
  Points = (2) [(13220,165,0),(13220,7955,0)]
  Start = (12870,-165,0)
  Subdivisions = 0
FEATURE [Part::FeaturePython] Wall294  label="Армпояс004"  # Arch/BIM 166 (typed FeaturePython)
  Align = 1
  Area = 1090600
  Base = -> Line1582
  BlockHeight = 0
  BlockLength = 0
  CountBroken = 0
  CountEntire = 0
  Face = 0
  GlobalId = 1hI4wR2SfDawL0z1dNH$cq
  Height = 140
  HorizontalArea = 1402200
  IfcData = IfcUID=1hI4wR2SfDawL0z1dNH$cq,+2 more (map truncated)
  IfcType = 166
  Joint = 0
  Length = 7790
  MakeBlocks = false
  Material = -> Material001
  MoveBase = false
  MoveWithHost = false
  Normal = (0,0,0)
  OffsetFirst = 0
  OffsetSecond = 0
  PerimeterLength = 15940
  Placement = pos=(0,0,3493) rot=(0,0,1;0rad)
  PredefinedType = 0
  VerticalArea = 2231600
  Width = 180
FEATURE [Part::Part2DObjectPython] Wire883  # Draft 2D object (typed FeaturePython)
  Area = 0
  ChamferSize = 0
  Closed = false
  End = (12859.1,7673.97,3572.72)
  FilletRadius = 0
  Length = 573.429
  MakeFace = true
  Placement = pos=(0,15,0) rot=(0,0,1;0rad)
  Points = (7) [(12872.2,7670.28,3584.03),(12870,7634,3620.31),(12867.8,7634,3517),(12865.7,7766,3517),(12863.5,7766,3609),(12861.3,7622.69,3609),+1 more]
  Start = (12872.2,7685.28,3584.03)
  Subdivisions = 0
  Support = -> [Wall292]
FEATURE [Part::FeaturePython] Rebar036  label="Stirrup012"  # Arch/BIM 110 (typed FeaturePython)
  Amount = 28
  AmountCheck = false
  Base = -> Wire883
  BentAngle = 135
  BentFactor = 4
  BottomCover = 20
  Diameter = 8
  Direction = (-1,0,0)
  Distance = 0
  FrontCover = 100
  HorizontalArea = 0
  Host = -> Wall292
  IfcData = IfcUID=3K6Qvq_$X52hEgXW4rU6QA
  IfcType = 110
  LeftCover = 20
  Length = 573.429
  Mark = Stirrup012
  Material = -> Material010
  MoveBase = false
  MoveWithHost = false
  OffsetEnd = 104
  OffsetStart = 104
  PerimeterLength = 0
  PlacementList = 28 placements: arithmetic series from (-104,0,0) step (-481.63,0,0) to (-13108,0,0)
  RebarShape = 3
  RightCover = 20
  Rounding = 1
  Spacing = 481.63
  TopCover = 20
  TotalLength = 16056
  TrueSpacing = 500
  VerticalArea = 0
FEATURE [App::DocumentObjectGroupPython] Stirrups012  # scripted group (container) (typed FeaturePython)
  Group = -> [Rebar036]
  Stirrups = -> [Rebar036]
  StirrupsConfiguration = Two Legged Stirrups
FEATURE [Sketcher::SketchObject] Sketch350
  FullyConstrained = false
  MapMode = 5
  Placement = pos=(0,7625,3493) rot=(1,0,0;1.5708rad)
  Support = -> [Wall292]
  sketch-geometry (1):
    g0: LineSegment StartX=-290 StartY=108 StartZ=0 EndX=12810 EndY=108 EndZ=0
FEATURE [Part::FeaturePython] Rebar037  label="StraightRebar024"  # Arch/BIM 110 (typed FeaturePython)
  Amount = 2
  AmountCheck = true
  Base = -> Sketch350
  Cover = 28
  CoverAlong = Top Side
  Diameter = 8
  Direction = (0,0,0)
  Distance = 0
  FrontCover = 28
  HorizontalArea = 0
  Host = -> Wall292
  IfcData = IfcUID=140U$9PZ1AHwJYsE$SOkWK
  IfcType = 110
  LeftBottomCover = 60
  Length = 13100
  Mark = StraightRebar024
  Material = -> Material010
  MoveBase = false
  MoveWithHost = false
  OffsetEnd = 32
  OffsetStart = 32
  Orientation = Horizontal
  PerimeterLength = 0
  PlacementList = 2 placements: [(0,32,-7.10543e-15),(0,148,-3.28626e-14)]
  RebarShape = 0
  RightTopCover = 60
  Rounding = 0
  Spacing = 116
  TotalLength = 26200
  TrueSpacing = 2
  VerticalArea = 0
FEATURE [App::DocumentObjectGroupPython] TopReinforcement012  # scripted group (container) (typed FeaturePython)
  Group = -> [Rebar037]
  LayerSpacing = [30]
  NumberDiameterOffset = 2#8.0@60.0
  TopRebars = -> [Rebar037]
FEATURE [Sketcher::SketchObject] Sketch351
  FullyConstrained = false
  MapMode = 5
  Placement = pos=(0,7625,3493) rot=(1,0,0;1.5708rad)
  Support = -> [Wall292]
  sketch-geometry (1):
    g0: LineSegment StartX=-290 StartY=32 StartZ=0 EndX=12810 EndY=32 EndZ=0
FEATURE [Part::FeaturePython] Rebar038  label="StraightRebar025"  # Arch/BIM 110 (typed FeaturePython)
  Amount = 2
  AmountCheck = true
  Base = -> Sketch351
  Cover = 28
  CoverAlong = Bottom Side
  Diameter = 8
  Direction = (0,0,0)
  Distance = 0
  FrontCover = 28
  HorizontalArea = 0
  Host = -> Wall292
  IfcData = IfcUID=2fxrXb7T52vBDIZ$F2twXk
  IfcType = 110
  LeftBottomCover = 60
  Length = 13100
  Mark = StraightRebar025
  Material = -> Material010
  MoveBase = false
  MoveWithHost = false
  OffsetEnd = 32
  OffsetStart = 32
  Orientation = Horizontal
  PerimeterLength = 0
  PlacementList = 2 placements: [(0,32,-7.10543e-15),(0,148,-3.28626e-14)]
  RebarShape = 0
  RightTopCover = 60
  Rounding = 0
  Spacing = 116
  TotalLength = 26200
  TrueSpacing = 2
  VerticalArea = 0
FEATURE [App::DocumentObjectGroupPython] BottomReinforcement012  # scripted group (container) (typed FeaturePython)
  BottomRebars = -> [Rebar038]
  Group = -> [Rebar038]
  LayerSpacing = [30]
  NumberDiameterOffset = 2#8.0@60.0
FEATURE [App::DocumentObjectGroupPython] BeamReinforcement012  label="BeamReinforcement013"  # scripted group (container) (typed FeaturePython)
  Group = -> [Stirrups012,TopReinforcement012,BottomReinforcement012]
  ReinforcementGroups = -> [Stirrups012,TopReinforcement012,BottomReinforcement012]
FEATURE [Part::Part2DObjectPython] Wire884  # Draft 2D object (typed FeaturePython)
  Area = 0
  ChamferSize = 0
  Closed = false
  End = (12859.1,-296.029,3572.72)
  FilletRadius = 0
  Length = 573.429
  MakeFace = true
  Placement = pos=(0,-15,0) rot=(0,0,1;0rad)
  Points = (7) [(12872.2,-269.716,3584.03),(12870,-306,3620.31),(12867.8,-306,3517),(12865.7,-174,3517),(12863.5,-174,3609),(12861.3,-317.314,3609),+1 more]
  Start = (12872.2,-284.716,3584.03)
  Subdivisions = 0
  Support = -> [Wall291]
FEATURE [Part::FeaturePython] Rebar039  label="Stirrup013"  # Arch/BIM 110 (typed FeaturePython)
  Amount = 28
  AmountCheck = false
  Base = -> Wire884
  BentAngle = 135
  BentFactor = 4
  BottomCover = 20
  Diameter = 8
  Direction = (-1,0,0)
  Distance = 0
  FrontCover = 100
  HorizontalArea = 0
  Host = -> Wall291
  IfcData = IfcUID=3qYUM6LlvEqR380m34$EFs
  IfcType = 110
  LeftCover = 20
  Length = 573.429
  Mark = Stirrup013
  Material = -> Material010
  MoveBase = false
  MoveWithHost = false
  OffsetEnd = 104
  OffsetStart = 104
  PerimeterLength = 0
  PlacementList = 28 placements: arithmetic series from (-104,0,0) step (-481.63,0,0) to (-13108,0,0)
  RebarShape = 3
  RightCover = 20
  Rounding = 1
  Spacing = 481.63
  TopCover = 20
  TotalLength = 16056
  TrueSpacing = 500
  VerticalArea = 0
FEATURE [App::DocumentObjectGroupPython] Stirrups013  # scripted group (container) (typed FeaturePython)
  Group = -> [Rebar039]
  Stirrups = -> [Rebar039]
  StirrupsConfiguration = Two Legged Stirrups
FEATURE [Sketcher::SketchObject] Sketch352
  FullyConstrained = false
  MapMode = 5
  Placement = pos=(1.03e-14,-345,3493) rot=(1,0,0;1.5708rad)
  Support = -> [Wall291]
  sketch-geometry (1):
    g0: LineSegment StartX=-290 StartY=108 StartZ=0 EndX=12810 EndY=108 EndZ=0
FEATURE [Part::FeaturePython] Rebar040  label="StraightRebar026"  # Arch/BIM 110 (typed FeaturePython)
  Amount = 2
  AmountCheck = true
  Base = -> Sketch352
  Cover = 28
  CoverAlong = Top Side
  Diameter = 8
  Direction = (0,0,0)
  Distance = 0
  FrontCover = 28
  HorizontalArea = 0
  Host = -> Wall291
  IfcData = IfcUID=0p007rg9H619hFCHvEy_jd
  IfcType = 110
  LeftBottomCover = 60
  Length = 13100
  Mark = StraightRebar026
  Material = -> Material010
  MoveBase = false
  MoveWithHost = false
  OffsetEnd = 32
  OffsetStart = 32
  Orientation = Horizontal
  PerimeterLength = 0
  PlacementList = 2 placements: [(-9.63156e-16,32,-7.10543e-15),(-4.4546e-15,148,-3.28626e-14)]
  RebarShape = 0
  RightTopCover = 60
  Rounding = 0
  Spacing = 116
  TotalLength = 26200
  TrueSpacing = 2
  VerticalArea = 0
FEATURE [App::DocumentObjectGroupPython] TopReinforcement013  # scripted group (container) (typed FeaturePython)
  Group = -> [Rebar040]
  LayerSpacing = [30]
  NumberDiameterOffset = 2#8.0@60.0
  TopRebars = -> [Rebar040]
FEATURE [Sketcher::SketchObject] Sketch353
  FullyConstrained = false
  MapMode = 5
  Placement = pos=(1.03e-14,-345,3493) rot=(1,0,0;1.5708rad)
  Support = -> [Wall291]
  sketch-geometry (1):
    g0: LineSegment StartX=-290 StartY=32 StartZ=0 EndX=12810 EndY=32 EndZ=0
FEATURE [Part::FeaturePython] Rebar041  label="StraightRebar027"  # Arch/BIM 110 (typed FeaturePython)
  Amount = 2
  AmountCheck = true
  Base = -> Sketch353
  Cover = 28
  CoverAlong = Bottom Side
  Diameter = 8
  Direction = (0,0,0)
  Distance = 0
  FrontCover = 28
  HorizontalArea = 0
  Host = -> Wall291
  IfcData = IfcUID=3WhL2Y$11658LLbofuE694
  IfcType = 110
  LeftBottomCover = 60
  Length = 13100
  Mark = StraightRebar027
  Material = -> Material010
  MoveBase = false
  MoveWithHost = false
  OffsetEnd = 32
  OffsetStart = 32
  Orientation = Horizontal
  PerimeterLength = 0
  PlacementList = 2 placements: [(-9.63156e-16,32,-7.10543e-15),(-4.4546e-15,148,-3.28626e-14)]
  RebarShape = 0
  RightTopCover = 60
  Rounding = 0
  Spacing = 116
  TotalLength = 26200
  TrueSpacing = 2
  VerticalArea = 0
FEATURE [App::DocumentObjectGroupPython] BottomReinforcement013  # scripted group (container) (typed FeaturePython)
  BottomRebars = -> [Rebar041]
  Group = -> [Rebar041]
  LayerSpacing = [30]
  NumberDiameterOffset = 2#8.0@60.0
FEATURE [App::DocumentObjectGroupPython] BeamReinforcement013  label="BeamReinforcement014"  # scripted group (container) (typed FeaturePython)
  Group = -> [Stirrups013,TopReinforcement013,BottomReinforcement013]
  ReinforcementGroups = -> [Stirrups013,TopReinforcement013,BottomReinforcement013]
FEATURE [Part::Part2DObjectPython] Wire886  # Draft 2D object (typed FeaturePython)
  Area = 0
  ChamferSize = 0
  Closed = false
  End = (12739,7599.14,3572.72)
  FilletRadius = 0
  Length = 573.429
  MakeFace = true
  Points = (7) [(12750.3,7612.17,3584.03),(12714,7610,3620.31),(12714,7607.83,3517),(12846,7605.66,3517),(12846,7603.49,3609),(12702.7,7601.31,3609),+1 more]
  Start = (12750.3,7612.17,3584.03)
  Subdivisions = 0
  Support = -> [Wall294]
FEATURE [Part::FeaturePython] Rebar042  label="Stirrup014"  # Arch/BIM 110 (typed FeaturePython)
  Amount = 17
  AmountCheck = false
  Base = -> Wire886
  BentAngle = 135
  BentFactor = 4
  BottomCover = 20
  Diameter = 8
  Direction = (0,-1,0)
  Distance = 0
  FrontCover = 100
  HorizontalArea = 0
  Host = -> Wall294
  IfcData = IfcUID=2hh8STxOfCgxszMIN_Kbtk
  IfcType = 110
  LeftCover = 20
  Length = 573.429
  Mark = Stirrup014
  Material = -> Material010
  MoveBase = false
  MoveWithHost = false
  OffsetEnd = 104
  OffsetStart = 104
  PerimeterLength = 0
  PlacementList = 17 placements: arithmetic series from (0,-104,0) step (0,-473.375,0) to (0,-7678,0)
  RebarShape = 3
  RightCover = 20
  Rounding = 1
  Spacing = 473.375
  TopCover = 20
  TotalLength = 9748.3
  TrueSpacing = 500
  VerticalArea = 0
FEATURE [App::DocumentObjectGroupPython] Stirrups014  # scripted group (container) (typed FeaturePython)
  Group = -> [Rebar042]
  Stirrups = -> [Rebar042]
  StirrupsConfiguration = Two Legged Stirrups
FEATURE [Sketcher::SketchObject] Sketch360
  FullyConstrained = false
  MapMode = 5
  Placement = pos=(12870,0,3493) rot=(0.57735,0.57735,0.57735;2.0944rad)
  Support = -> [Wall294]
  sketch-geometry (1):
    g0: LineSegment StartX=-300 StartY=108 StartZ=0 EndX=7760 EndY=108 EndZ=0
FEATURE [Part::FeaturePython] Rebar045  label="StraightRebar030"  # Arch/BIM 110 (typed FeaturePython)
  Amount = 2
  AmountCheck = true
  Base = -> Sketch360
  Cover = 28
  CoverAlong = Top Side
  Diameter = 8
  Direction = (0,0,0)
  Distance = 0
  FrontCover = 28
  HorizontalArea = 0
  Host = -> Wall294
  IfcData = IfcUID=0$9Ki$QzP9MxF8QuB$I3Ex
  IfcType = 110
  LeftBottomCover = -150
  Length = 8060
  Mark = StraightRebar030
  Material = -> Material010
  MoveBase = false
  MoveWithHost = false
  OffsetEnd = 32
  OffsetStart = 32
  Orientation = Horizontal
  PerimeterLength = 0
  PlacementList = 2 placements: [(-32,0,0),(-148,0,0)]
  RebarShape = 0
  RightTopCover = -150
  Rounding = 0
  Spacing = 116
  TotalLength = 16120
  TrueSpacing = 2
  VerticalArea = 0
FEATURE [App::DocumentObjectGroupPython] TopReinforcement014  # scripted group (container) (typed FeaturePython)
  Group = -> [Rebar045]
  LayerSpacing = [30]
  NumberDiameterOffset = 2#8.0@-150.0
  TopRebars = -> [Rebar045]
FEATURE [Sketcher::SketchObject] Sketch361
  FullyConstrained = false
  MapMode = 5
  Placement = pos=(12870,0,3493) rot=(0.57735,0.57735,0.57735;2.0944rad)
  Support = -> [Wall294]
  sketch-geometry (1):
    g0: LineSegment StartX=-300 StartY=32 StartZ=0 EndX=7760 EndY=32 EndZ=0
FEATURE [Part::FeaturePython] Rebar046  label="StraightRebar031"  # Arch/BIM 110 (typed FeaturePython)
  Amount = 2
  AmountCheck = true
  Base = -> Sketch361
  Cover = 28
  CoverAlong = Bottom Side
  Diameter = 8
  Direction = (0,0,0)
  Distance = 0
  FrontCover = 28
  HorizontalArea = 0
  Host = -> Wall294
  IfcData = IfcUID=3LTvHi1MTDgRMXNthAh_XG
  IfcType = 110
  LeftBottomCover = -150
  Length = 8060
  Mark = StraightRebar031
  Material = -> Material010
  MoveBase = false
  MoveWithHost = false
  OffsetEnd = 32
  OffsetStart = 32
  Orientation = Horizontal
  PerimeterLength = 0
  PlacementList = 2 placements: [(-32,0,0),(-148,0,0)]
  RebarShape = 0
  RightTopCover = -150
  Rounding = 0
  Spacing = 116
  TotalLength = 16120
  TrueSpacing = 2
  VerticalArea = 0
FEATURE [App::DocumentObjectGroupPython] BottomReinforcement014  # scripted group (container) (typed FeaturePython)
  BottomRebars = -> [Rebar046]
  Group = -> [Rebar046]
  LayerSpacing = [30]
  NumberDiameterOffset = 2#8.0@-150.0
FEATURE [App::DocumentObjectGroupPython] BeamReinforcement014  label="BeamReinforcement015"  # scripted group (container) (typed FeaturePython)
  Group = -> [Stirrups014,TopReinforcement014,BottomReinforcement014]
  ReinforcementGroups = -> [Stirrups014,TopReinforcement014,BottomReinforcement014]
FEATURE [Part::Part2DObjectPython] Wire887  # Draft 2D object (typed FeaturePython)
  Area = 0
  ChamferSize = 0
  Closed = false
  End = (-301.029,7599.14,3572.72)
  FilletRadius = 0
  Length = 573.429
  MakeFace = true
  Points = (7) [(-289.716,7612.17,3584.03),(-326,7610,3620.31),(-326,7607.83,3517),(-194,7605.66,3517),(-194,7603.49,3609),(-337.314,7601.31,3609),+1 more]
  Start = (-289.716,7612.17,3584.03)
  Subdivisions = 0
  Support = -> [Wall293]
FEATURE [Part::FeaturePython] Rebar047  label="Stirrup015"  # Arch/BIM 110 (typed FeaturePython)
  Amount = 17
  AmountCheck = false
  Base = -> Wire887
  BentAngle = 135
  BentFactor = 4
  BottomCover = 20
  Diameter = 8
  Direction = (0,-1,0)
  Distance = 0
  FrontCover = 100
  HorizontalArea = 0
  Host = -> Wall293
  IfcData = IfcUID=3cNbPT2cr1VeJ7E6rFKLiC
  IfcType = 110
  LeftCover = 20
  Length = 573.429
  Mark = Stirrup015
  Material = -> Material010
  MoveBase = false
  MoveWithHost = false
  OffsetEnd = 104
  OffsetStart = 104
  PerimeterLength = 0
  PlacementList = 17 placements: arithmetic series from (0,-104,0) step (0,-473.375,0) to (0,-7678,0)
  RebarShape = 3
  RightCover = 20
  Rounding = 1
  Spacing = 473.375
  TopCover = 20
  TotalLength = 9748.3
  TrueSpacing = 500
  VerticalArea = 0
FEATURE [App::DocumentObjectGroupPython] Stirrups015  # scripted group (container) (typed FeaturePython)
  Group = -> [Rebar047]
  Stirrups = -> [Rebar047]
  StirrupsConfiguration = Two Legged Stirrups
FEATURE [Sketcher::SketchObject] Sketch362
  FullyConstrained = false
  MapMode = 5
  Placement = pos=(-170,0,3493) rot=(0.57735,0.57735,0.57735;2.0944rad)
  Support = -> [Wall293]
  sketch-geometry (1):
    g0: LineSegment StartX=-300 StartY=108 StartZ=0 EndX=7760 EndY=108 EndZ=0
FEATURE [Part::FeaturePython] Rebar048  label="StraightRebar032"  # Arch/BIM 110 (typed FeaturePython)
  Amount = 2
  AmountCheck = true
  Base = -> Sketch362
  Cover = 28
  CoverAlong = Top Side
  Diameter = 8
  Direction = (0,0,0)
  Distance = 0
  FrontCover = 28
  HorizontalArea = 0
  Host = -> Wall293
  IfcData = IfcUID=3g7bd8dkj1MPydz_teGZJR
  IfcType = 110
  LeftBottomCover = -150
  Length = 8060
  Mark = StraightRebar032
  Material = -> Material010
  MoveBase = false
  MoveWithHost = false
  OffsetEnd = 32
  OffsetStart = 32
  Orientation = Horizontal
  PerimeterLength = 0
  PlacementList = 2 placements: [(-32,0,0),(-148,0,0)]
  RebarShape = 0
  RightTopCover = -150
  Rounding = 0
  Spacing = 116
  TotalLength = 16120
  TrueSpacing = 2
  VerticalArea = 0
FEATURE [App::DocumentObjectGroupPython] TopReinforcement015  # scripted group (container) (typed FeaturePython)
  Group = -> [Rebar048]
  LayerSpacing = [30]
  NumberDiameterOffset = 2#8.0@-150.0
  TopRebars = -> [Rebar048]
FEATURE [Sketcher::SketchObject] Sketch363
  FullyConstrained = false
  MapMode = 5
  Placement = pos=(-170,0,3493) rot=(0.57735,0.57735,0.57735;2.0944rad)
  Support = -> [Wall293]
  sketch-geometry (1):
    g0: LineSegment StartX=-300 StartY=32 StartZ=0 EndX=7760 EndY=32 EndZ=0
FEATURE [Part::FeaturePython] Rebar049  label="StraightRebar033"  # Arch/BIM 110 (typed FeaturePython)
  Amount = 2
  AmountCheck = true
  Base = -> Sketch363
  Cover = 28
  CoverAlong = Bottom Side
  Diameter = 8
  Direction = (0,0,0)
  Distance = 0
  FrontCover = 28
  HorizontalArea = 0
  Host = -> Wall293
  IfcData = IfcUID=0PUrgqHLj2fuIB$J8Xlgq8
  IfcType = 110
  LeftBottomCover = -150
  Length = 8060
  Mark = StraightRebar033
  Material = -> Material010
  MoveBase = false
  MoveWithHost = false
  OffsetEnd = 32
  OffsetStart = 32
  Orientation = Horizontal
  PerimeterLength = 0
  PlacementList = 2 placements: [(-32,0,0),(-148,0,0)]
  RebarShape = 0
  RightTopCover = -150
  Rounding = 0
  Spacing = 116
  TotalLength = 16120
  TrueSpacing = 2
  VerticalArea = 0
FEATURE [App::DocumentObjectGroupPython] BottomReinforcement015  # scripted group (container) (typed FeaturePython)
  BottomRebars = -> [Rebar049]
  Group = -> [Rebar049]
  LayerSpacing = [30]
  NumberDiameterOffset = 2#8.0@-150.0
FEATURE [App::DocumentObjectGroupPython] BeamReinforcement015  label="BeamReinforcement016"  # scripted group (container) (typed FeaturePython)
  Group = -> [Stirrups015,TopReinforcement015,BottomReinforcement015]
  ReinforcementGroups = -> [Stirrups015,TopReinforcement015,BottomReinforcement015]
FEATURE [App::GeometryPython] BuildingPart098  label="Армирование пояса"  # Arch/BIM 111 (typed FeaturePython)
  Area = 0
  GlobalId = 2PxC9szOX0IvFjy5VtbcaU
  Group = -> [BeamReinforcement012,BeamReinforcement013,BeamReinforcement014,BeamReinforcement015]
  Height = 0
  HeightPropagate = true
  IfcData = IfcUID=2PxC9szOX0IvFjy5VtbcaU,+2 more (map truncated)
  IfcType = 111
  LevelOffset = 0
FEATURE [App::GeometryPython] BuildingPart097  label="Армпояс"  # Arch/BIM 52 (typed FeaturePython)
  Area = 5882800
  GlobalId = 2GdC2J3IrBqAFOXYdeO3oM
  Group = -> [Wall291,Wall292,Wall293,Wall294,BuildingPart098]
  Height = 0
  HeightPropagate = true
  IfcData = IfcUID=2GdC2J3IrBqAFOXYdeO3oM,+2 more (map truncated)
  IfcType = 52
  LevelOffset = 0
FEATURE [App::FeaturePython] Dimension028  # Draft dimension (typed FeaturePython)
  Diameter = false
  Dimline = (-1200,2335,0)
  Direction = (0,0,0)
  Distance = 1345
  End = (-1836.7,3680,0)
  Normal = (0,0,1)
  Start = (-1836.7,2335,0)
FEATURE [Part::Part2DObjectPython] Circle122  label="Circle123"  # Draft 2D object (typed FeaturePython)
  Area = 0
  FirstAngle = 0
  LastAngle = 0
  MakeFace = false
  Placement = pos=(-2036.7,7695,0) rot=(0,0,1;0rad)
  Radius = 200
FEATURE [Part::Part2DObjectPython] ShapeString192  # Draft 2D object (typed FeaturePython)
  FontFile = <path>
  Placement = pos=(-2130.05,7594.61,0) rot=(0,0,1;0rad)
  Size = 200
  String = D
  Tracking = 0
FEATURE [Part::Part2DObjectPython] Circle123  label="Circle124"  # Draft 2D object (typed FeaturePython)
  Area = 0
  FirstAngle = 0
  LastAngle = 0
  MakeFace = false
  Placement = pos=(-2036.7,3680,0) rot=(0,0,1;0rad)
  Radius = 200
FEATURE [Part::Part2DObjectPython] ShapeString193  # Draft 2D object (typed FeaturePython)
  FontFile = <path>
  Placement = pos=(-2133.13,3586.85,0) rot=(0,0,1;0rad)
  Size = 200
  String = C
  Tracking = 0
FEATURE [Part::Part2DObjectPython] Circle124  label="Circle125"  # Draft 2D object (typed FeaturePython)
  Area = 0
  FirstAngle = 0
  LastAngle = 0
  MakeFace = false
  Placement = pos=(-2036.7,2335,0) rot=(0,0,1;0rad)
  Radius = 200
FEATURE [Part::Part2DObjectPython] ShapeString194  # Draft 2D object (typed FeaturePython)
  FontFile = <path>
  Placement = pos=(-2116.38,2246.01,0) rot=(0,0,1;0rad)
  Size = 200
  String = B
  Tracking = 0
FEATURE [Part::Part2DObjectPython] Circle125  label="Circle126"  # Draft 2D object (typed FeaturePython)
  Area = 0
  FirstAngle = 0
  LastAngle = 0
  MakeFace = false
  Placement = pos=(-2036.7,-235,0) rot=(0,0,1;0rad)
  Radius = 200
FEATURE [Part::Part2DObjectPython] ShapeString195  # Draft 2D object (typed FeaturePython)
  FontFile = <path>
  Placement = pos=(-2124.02,-327.945,0) rot=(0,0,1;0rad)
  Size = 200
  String = A
  Tracking = 0
FEATURE [Part::Part2DObjectPython] Circle126  label="Circle127"  # Draft 2D object (typed FeaturePython)
  Area = 0
  FirstAngle = 0
  LastAngle = 0
  MakeFace = false
  Placement = pos=(-240,9706.46,0) rot=(0,0,1;0rad)
  Radius = 200
FEATURE [Part::Part2DObjectPython] ShapeString196  # Draft 2D object (typed FeaturePython)
  FontFile = <path>
  Placement = pos=(-319.076,9614.22,0) rot=(0,0,1;0rad)
  Size = 200
  String = 1
  Tracking = 0
FEATURE [Part::Part2DObjectPython] Circle127  label="Circle128"  # Draft 2D object (typed FeaturePython)
  Area = 0
  FirstAngle = 0
  LastAngle = 0
  MakeFace = false
  Placement = pos=(3450,9706.46,0) rot=(0,0,1;0rad)
  Radius = 200
FEATURE [Part::Part2DObjectPython] ShapeString197  # Draft 2D object (typed FeaturePython)
  FontFile = <path>
  Placement = pos=(3367.38,9622.97,0) rot=(0,0,1;0rad)
  Size = 200
  String = 2
  Tracking = 0
FEATURE [Part::Part2DObjectPython] Circle128  label="Circle129"  # Draft 2D object (typed FeaturePython)
  Area = 0
  FirstAngle = 0
  LastAngle = 0
  MakeFace = false
  Placement = pos=(4050,9706.46,0) rot=(0,0,1;0rad)
  Radius = 200
FEATURE [Part::Part2DObjectPython] ShapeString198  # Draft 2D object (typed FeaturePython)
  FontFile = <path>
  Placement = pos=(3978.07,9610.28,0) rot=(0,0,1;0rad)
  Size = 200
  String = 3
  Tracking = 0
FEATURE [Part::Part2DObjectPython] Circle129  label="Circle130"  # Draft 2D object (typed FeaturePython)
  Area = 0
  FirstAngle = 0
  LastAngle = 0
  MakeFace = false
  Placement = pos=(4870,9706.46,0) rot=(0,0,1;0rad)
  Radius = 200
FEATURE [Part::Part2DObjectPython] ShapeString199  # Draft 2D object (typed FeaturePython)
  FontFile = <path>
  Placement = pos=(4784.17,9612.89,0) rot=(0,0,1;0rad)
  Size = 200
  String = 4
  Tracking = 0
FEATURE [Part::Part2DObjectPython] Circle130  label="Circle131"  # Draft 2D object (typed FeaturePython)
  Area = 0
  FirstAngle = 0
  LastAngle = 0
  MakeFace = false
  Placement = pos=(6890,9706.46,0) rot=(0,0,1;0rad)
  Radius = 200
FEATURE [Part::Part2DObjectPython] ShapeString200  # Draft 2D object (typed FeaturePython)
  FontFile = <path>
  Placement = pos=(6820.3,9606.58,0) rot=(0,0,1;0rad)
  Size = 200
  String = 5
  Tracking = 0
FEATURE [Part::Part2DObjectPython] Circle131  label="Circle132"  # Draft 2D object (typed FeaturePython)
  Area = 0
  FirstAngle = 0
  LastAngle = 0
  MakeFace = false
  Placement = pos=(7350,9706.46,0) rot=(0,0,1;0rad)
  Radius = 200
FEATURE [Part::Part2DObjectPython] ShapeString201  # Draft 2D object (typed FeaturePython)
  FontFile = <path>
  Placement = pos=(7275.5,9616.19,0) rot=(0,0,1;0rad)
  Size = 200
  String = 6
  Tracking = 0
FEATURE [Part::Part2DObjectPython] Circle132  label="Circle133"  # Draft 2D object (typed FeaturePython)
  Area = 0
  FirstAngle = 0
  LastAngle = 0
  MakeFace = false
  Placement = pos=(7910,9706.46,0) rot=(0,0,1;0rad)
  Radius = 200
FEATURE [Part::Part2DObjectPython] ShapeString202  # Draft 2D object (typed FeaturePython)
  FontFile = <path>
  Placement = pos=(7839.18,9604.4,0) rot=(0,0,1;0rad)
  Size = 200
  String = 7
  Tracking = 0
FEATURE [Part::Part2DObjectPython] Circle133  label="Circle134"  # Draft 2D object (typed FeaturePython)
  Area = 0
  FirstAngle = 0
  LastAngle = 0
  MakeFace = false
  Placement = pos=(9500,9706.46,0) rot=(0,0,1;0rad)
  Radius = 200
FEATURE [Part::Part2DObjectPython] ShapeString203  # Draft 2D object (typed FeaturePython)
  FontFile = <path>
  Placement = pos=(9427.59,9608.74,0) rot=(0,0,1;0rad)
  Size = 200
  String = 8
  Tracking = 0
FEATURE [Part::Part2DObjectPython] Circle134  label="Circle135"  # Draft 2D object (typed FeaturePython)
  Area = 0
  FirstAngle = 0
  LastAngle = 0
  MakeFace = false
  Placement = pos=(12760,9706.46,0) rot=(0,0,1;0rad)
  Radius = 200
FEATURE [Part::Part2DObjectPython] ShapeString204  # Draft 2D object (typed FeaturePython)
  FontFile = <path>
  Placement = pos=(12685.6,9616.32,0) rot=(0,0,1;0rad)
  Size = 200
  String = 9
  Tracking = 0
FEATURE [TechDraw::DrawViewAnnotation] Annotation007
  Font = DejaVu Sans
  LineSpace = 80
  LockPosition = false
  MaxWidth = -1
  Rotation = 0
  ScaleType = 0
  Text = \u041f\u043b\u0430\u043d \u043f\u0435\u0440\u0432\u043e\u0433\u043e \u044d\u0442\u0430\u0436\u0430  \u043d\u0430 \u043e\u0442\u043c\u0435\u0442\u043a\u0435 +0.0
  TextSize = 6
  TextStyle = 0
  X = 211.887
  Y = 279.654
FEATURE [TechDraw::DrawViewAnnotation] Annotation008  label="a_085"
  Font = DejaVu Sans
  LineSpace = 80
  LockPosition = true
  MaxWidth = -1
  Rotation = 0
  ScaleType = 0
  Text = \u0420\u0430\u0437\u0440\u0435\u0437 \u043f\u043e \u0410-\u0410
  TextSize = 6
  TextStyle = 0
  X = 203.183
  Y = 279.058
FEATURE [App::FeaturePython] Dimension029  # Draft dimension (typed FeaturePython)
  Diameter = false
  Dimline = (0,5100,-400)
  Direction = (0,0,0)
  Distance = 200
  End = (0,8000,0)
  Normal = (1,0,0)
  Start = (0,8000,-200)
FEATURE [Part::Part2DObjectPython] Wire462  label="мауэрлат002"  # Draft 2D object (typed FeaturePython)
  ChamferSize = 0
  Closed = true
  End = (21584.8,5827.56,0)
  FilletRadius = 0
  Length = 12600
  MakeFace = false
  Placement = pos=(21406.2,1831.55,0) rot=(0,0,-1;1.61546rad)
  Points = (4) [(0,0,0),(0,2300,0),(-4000,2300,0),(-4000,-2.18279e-11,0)]
  Start = (21406.2,1831.55,0)
  Subdivisions = 0
FEATURE [Part::FeaturePython] Roof010  label="Крыша001"  # Arch/BIM 113 (typed FeaturePython)
  Angles = [90,14.6,90,14.6]
  Base = -> Wire462
  BorderLength = 15096.9
  Face = 0
  Flip = false
  Heights = [0,299.553,0,299.553]
  HorizontalArea = 1.26e+07
  IdRel = [0,0,0,0]
  IfcType = 113
  MoveBase = false
  MoveWithHost = false
  Overhang = [250,250,250,250]
  PerimeterLength = 14600
  Placement = pos=(0,0,2200) rot=(0,0,1;0rad)
  PredefinedType = 0
  RidgeLength = 7393.43
  Runs = [250,1150,250,1150]
  Thickness = [150,150,150,150]
  VerticalArea = 2.26308e+06
FEATURE [Part::Part2DObjectPython] Rectangle2373  # Draft 2D object (typed FeaturePython)
  ChamferSize = 0
  Columns = 1
  FilletRadius = 0
  Height = 150
  Length = 800
  MakeFace = true
  Placement = pos=(21464.3,3130.25,0) rot=(0,0,-1;1.61546rad)
  Rows = 1
FEATURE [Part::FeaturePython] Structure131  label="Structure130"  # Arch/BIM 52 (typed FeaturePython)
  Base = -> Rectangle2373
  FaceMaker = 0
  Height = 1800
  HorizontalArea = 120000
  IfcData = complex_attributes={"OwnerHistory": {}, "IsNestedBy": {}, "IsDecomposedBy": {}, "IsDefinedBy": {}, "ObjectPlacement": {}, "Representation":... (+4 chars omitted)
  IfcType = 52
  Length = 0
  MoveBase = false
  MoveWithHost = false
  Nodes = (2) [(-35.6948,-25773.1,0),(-35.6948,-25773.1,1800)]
  NodesOffset = 0
  Normal = (0,0,0)
  PerimeterLength = 1900
  VerticalArea = 3.42e+06
  Width = 100
FEATURE [Part::Part2DObjectPython] Rectangle2370  # Draft 2D object (typed FeaturePython)
  ChamferSize = 0
  Columns = 1
  FilletRadius = 0
  Height = 500
  Length = 150
  MakeFace = true
  Placement = pos=(21862.5,1961.31,0) rot=(0,0,-1;1.61546rad)
  Rows = 1
FEATURE [Part::FeaturePython] Structure130  label="Structure129"  # Arch/BIM 52 (typed FeaturePython)
  Base = -> Rectangle2370
  FaceMaker = 0
  Height = 600
  HorizontalArea = 75000
  IfcData = complex_attributes={"OwnerHistory": {}, "IsNestedBy": {}, "IsDecomposedBy": {}, "IsDefinedBy": {}, "ObjectPlacement": {}, "Representation":... (+4 chars omitted)
  IfcType = 52
  Length = 0
  MoveBase = false
  MoveWithHost = false
  Nodes = (2) [(-938.622,-26279,0),(-938.622,-26279,600)]
  NodesOffset = 0
  Normal = (0,0,0)
  PerimeterLength = 1300
  Placement = pos=(0,-4e-15,1240) rot=(0,0,1;0rad)
  VerticalArea = 780000
  Width = 100
FEATURE [Part::Part2DObjectPython] Rectangle2372  # Draft 2D object (typed FeaturePython)
  ChamferSize = 0
  Columns = 1
  FilletRadius = 0
  Height = 150
  Length = 500
  MakeFace = true
  Placement = pos=(21520.1,4379.01,0) rot=(0,0,-1;1.61546rad)
  Rows = 1
FEATURE [Part::FeaturePython] Structure128  label="Structure"  # Arch/BIM 52 (typed FeaturePython)
  Base = -> Rectangle2372
  FaceMaker = 0
  Height = 600
  HorizontalArea = 75000
  IfcData = complex_attributes={"OwnerHistory": {}, "IsNestedBy": {}, "IsDecomposedBy": {}, "IsDefinedBy": {}, "ObjectPlacement": {}, "Representation":... (+4 chars omitted)
  IfcType = 52
  Length = 0
  MoveBase = false
  MoveWithHost = false
  Nodes = (2) [(1351.07,-25965.1,0),(1351.07,-25965.1,600)]
  NodesOffset = 0
  Normal = (0,0,0)
  PerimeterLength = 1300
  Placement = pos=(0,-4e-15,1240) rot=(0,0,1;0rad)
  VerticalArea = 780000
  Width = 100
FEATURE [Part::Part2DObjectPython] Rectangle2368  # Draft 2D object (typed FeaturePython)
  ChamferSize = 0
  Columns = 1
  FilletRadius = 0
  Height = 2300
  Length = 4000
  MakeFace = false
  Placement = pos=(21584.8,5827.56,0) rot=(0,0,-1;1.61546rad)
  Rows = 1
FEATURE [Part::FeaturePython] Wall094  label="Wall005"  # Arch/BIM 166 (typed FeaturePython)
  Align = 1
  Area = 3.087e+07
  Base = -> Rectangle2368
  BlockHeight = 0
  BlockLength = 0
  CountBroken = 0
  CountEntire = 0
  Face = 0
  Height = 2450
  HorizontalArea = 0
  IfcType = 166
  Joint = 0
  Length = 12600
  MakeBlocks = false
  MoveBase = false
  MoveWithHost = false
  Normal = (0,0,0)
  OffsetFirst = 0
  OffsetSecond = 0
  PerimeterLength = 0
  Placement = pos=(0,0,-150) rot=(0,0,1;0rad)
  PredefinedType = 0
  Subtractions = -> [Structure128,Structure130,Structure131]
  VerticalArea = 0
  Width = 150
FEATURE [Part::FeaturePython] Wall096  label="Wall006"  # Arch/BIM 166 (typed FeaturePython)
  Align = 0
  Area = 6.3e+06
  Base = -> Rectangle2368
  BlockHeight = 0
  BlockLength = 0
  CountBroken = 0
  CountEntire = 0
  Face = 0
  Height = 500
  HorizontalArea = 1.18e+06
  IfcType = 166
  Joint = 0
  Length = 12600
  MakeBlocks = false
  MoveBase = false
  MoveWithHost = false
  Normal = (0,0,-1)
  Offset = 50
  OffsetFirst = 0
  OffsetSecond = 0
  PerimeterLength = 12200
  Placement = pos=(0,0,-150) rot=(0,0,1;0rad)
  PredefinedType = 0
  VerticalArea = 1.18e+07
  Width = 100
FEATURE [App::GeometryPython] BuildingPart032  label="Баня (перевозная)"  # Arch/BIM 10 (typed FeaturePython)
  Area = 3.717e+07
  BuildingType = 0
  CompositionType = 0
  ElevationOfRefHeight = 0
  ElevationOfTerrain = 0
  Group = -> [Wall094,Roof010,Wall096]
  Height = 0
  HeightPropagate = true
  IfcType = 10
  LevelOffset = 0
  LongName = Баня (перевозная)
FEATURE [Part::Part2DObjectPython] Rectangle3343  label="Контур Строения001"  # Draft 2D object (typed FeaturePython)
  Area = 0
  ChamferSize = 0
  Columns = 1
  FilletRadius = 0
  Height = 8540
  Length = 13640
  MakeFace = false
  Placement = pos=(-560,-540,0) rot=(0,0,1;0rad)
  Rows = 1
FEATURE [App::FeaturePython] Text  label="Название Строения"  # WARN: FeaturePython — macro-defined, semantics opaque (R4)
  Placement = pos=(60,-286,0) rot=(0,0,1;0rad)
FEATURE [Part::Feature] Human
  Placement = pos=(2300,-1000,-200) rot=(0,0,1;0rad)
  shape: bbox 490.6 x 1.43e-06 x 1712 mm, 1 faces, 0 solids (baked)
FEATURE [Part::FeaturePython] Axis001006  label="Горизонтальные оси"  # WARN: FeaturePython — macro-defined, semantics opaque (R4)
  Angles = [0,0,0,0]
  Distances = [305,2570,1345,4015]
  Length = 15958.8
  Placement = pos=(14122.1,-540,0) rot=(0,0,1;1.5708rad)
  expr: Length = Rectangle3343.Length * 1.17
  expr: .Placement.Base.x = Rectangle3343.Placement.Base.x + Length * 0.92
  expr: .Placement.Base.y = Rectangle3343.Placement.Base.y
FEATURE [Part::FeaturePython] Axis001007  label="Вертикальные Оси"  # WARN: FeaturePython — macro-defined, semantics opaque (R4)
  Angles = [0,0,0,0,0,0,0,0,0]
  Distances = [320,3690,600,820,2020,460,560,1590,3260]
  Length = 11614.4
  Placement = pos=(-560,-2107.94,0) rot=(0,0,1;0rad)
  expr: Length = Rectangle3343.Height * 1.36
  expr: .Placement.Base.y = Rectangle3343.Placement.Base.y - Length * 0.135
  expr: .Placement.Base.x = Rectangle3343.Placement.Base.x
FEATURE [App::FeaturePython] AxisSystem002  label="Оси"  # WARN: FeaturePython — macro-defined, semantics opaque (R4)
  Axes = -> [Axis001006,Axis001007]
FEATURE [Part::FeaturePython] Axis001008  label="Оси уровня"  # WARN: FeaturePython — macro-defined, semantics opaque (R4)
  Angles = [0,0]
  Distances = [0,3130]
  Labels = 1st floor | mansard
  Length = 15004
  Placement = pos=(13618.8,-540,0) rot=(0.57735,-0.57735,0.57735;2.0944rad)
  expr: Length = Rectangle3343.Length * 1.1
  expr: .Placement.Base.x = Rectangle3343.Placement.Base.x + Length * 0.945
  expr: .Placement.Base.y = Rectangle3343.Placement.Base.y
FEATURE [App::DocumentObjectGroup] App__DocumentObjectGroup  label="Разметка Строения"
  Group = -> [Rectangle3343,Text,AxisSystem002,Axis001008]
FEATURE [App::FeaturePython] WPProxy  # WARN: FeaturePython — macro-defined, semantics opaque (R4)
  Placement = pos=(-560,-540,0) rot=(0,0,1;0rad)
FEATURE [Part::Part2DObjectPython] Rectangle3344  label="Фальшколонна 016"  # Draft 2D object (typed FeaturePython)
  Area = 54600
  ChamferSize = 0
  Columns = 1
  FilletRadius = 0
  Height = 140
  Length = 390
  MakeFace = true
  Placement = pos=(5280,-565,0) rot=(0,0,1;0rad)
  Rows = 1
FEATURE [Part::FeaturePython] Structure413  label="Облицовка камнем 029"  # Arch/BIM 52 (typed FeaturePython)
  Base = -> Rectangle3344
  FaceMaker = 0
  GlobalId = 2ZAbdpbyTAehtFhwD_xQoN
  Height = 2320
  HorizontalArea = 54600
  IfcData = IfcUID=2ZAbdpbyTAehtFhwD_xQoN,+2 more (map truncated)
  IfcType = 52
  Length = 0
  Material = -> Material007
  MoveBase = false
  MoveWithHost = false
  Nodes = (2) [(3798,-460,0),(3798,-460,3600)]
  NodesOffset = 0
  Normal = (0,0,0)
  PerimeterLength = 1060
  Placement = pos=(0,-2.558e-13,-40) rot=(0,0,1;0rad)
  VerticalArea = 2459200
  Width = 100
FEATURE [Part::Part2DObjectPython] Rectangle3345  label="Фальшколонна 017"  # Draft 2D object (typed FeaturePython)
  Area = 256200
  ChamferSize = 0
  Columns = 1
  FilletRadius = 0
  Height = 140
  Length = 1830
  MakeFace = true
  Placement = pos=(5280,-565,0) rot=(0,0,1;0rad)
  Rows = 1
FEATURE [Part::FeaturePython] Structure414  label="Облицовка камнем 030"  # Arch/BIM 52 (typed FeaturePython)
  Base = -> Rectangle3345
  FaceMaker = 0
  GlobalId = 1KN_bE7FH3jPyxIPmeDa18
  Height = 380
  HorizontalArea = 256200
  IfcData = IfcUID=1KN_bE7FH3jPyxIPmeDa18,+2 more (map truncated)
  IfcType = 52
  Length = 0
  Material = -> Material007
  MoveBase = false
  MoveWithHost = false
  Nodes = (2) [(3798,-460,0),(3798,-460,3600)]
  NodesOffset = 0
  Normal = (0,0,0)
  PerimeterLength = 3940
  Placement = pos=(0,1.14e-13,2280) rot=(0,0,1;0rad)
  VerticalArea = 1.4972e+06
  Width = 100
FEATURE [Part::Part2DObjectPython] Rectangle3346  label="Фальшколонна 018"  # Draft 2D object (typed FeaturePython)
  Area = 365400
  ChamferSize = 0
  Columns = 1
  FilletRadius = 0
  Height = 140
  Length = 2610
  MakeFace = true
  Placement = pos=(8270,7895,0) rot=(0,0,1;0rad)
  Rows = 1
FEATURE [Part::FeaturePython] Structure415  label="Облицовка камнем 031"  # Arch/BIM 52 (typed FeaturePython)
  Base = -> Rectangle3346
  FaceMaker = 0
  GlobalId = 0o5mp13GDD3PgfU32fU4jr
  Height = 380
  HorizontalArea = 365400
  IfcData = IfcUID=0o5mp13GDD3PgfU32fU4jr,+2 more (map truncated)
  IfcType = 52
  Length = 0
  Material = -> Material007
  MoveBase = false
  MoveWithHost = false
  Nodes = (2) [(3798,-460,0),(3798,-460,3600)]
  NodesOffset = 0
  Normal = (0,0,0)
  PerimeterLength = 5500
  Placement = pos=(0,1.14e-13,2500) rot=(0,0,1;0rad)
  VerticalArea = 2.09e+06
  Width = 100
FEATURE [Part::Part2DObjectPython] Rectangle3347  label="Фальшколонна 019"  # Draft 2D object (typed FeaturePython)
  Area = 54600
  ChamferSize = 0
  Columns = 1
  FilletRadius = 0
  Height = 140
  Length = 390
  MakeFace = true
  Placement = pos=(8270,7895,0) rot=(0,0,1;0rad)
  Rows = 1
FEATURE [Part::FeaturePython] Structure416  label="Облицовка камнем 032"  # Arch/BIM 52 (typed FeaturePython)
  Base = -> Rectangle3347
  FaceMaker = 0
  GlobalId = 0mLPfwKGf0vhV5LN6Arb3I
  Height = 2540
  HorizontalArea = 54600
  IfcData = IfcUID=0mLPfwKGf0vhV5LN6Arb3I,+2 more (map truncated)
  IfcType = 52
  Length = 0
  Material = -> Material007
  MoveBase = false
  MoveWithHost = false
  Nodes = (2) [(3798,-460,0),(3798,-460,3600)]
  NodesOffset = 0
  Normal = (0,0,0)
  PerimeterLength = 1060
  Placement = pos=(0,4.55e-13,-40) rot=(0,0,1;0rad)
  VerticalArea = 2692400
  Width = 100
FEATURE [Part::Part2DObjectPython] Rectangle3348  label="Фальшколонна 020"  # Draft 2D object (typed FeaturePython)
  Area = 54600
  ChamferSize = 0
  Columns = 1
  FilletRadius = 0
  Height = 140
  Length = 390
  MakeFace = true
  Placement = pos=(6720,-565,0) rot=(0,0,1;0rad)
  Rows = 1
FEATURE [Part::FeaturePython] Structure417  label="Облицовка камнем 033"  # Arch/BIM 52 (typed FeaturePython)
  Base = -> Rectangle3348
  FaceMaker = 0
  GlobalId = 3gi2vzadv7rvN$3wEIiMLm
  Height = 2320
  HorizontalArea = 54600
  IfcData = IfcUID=3gi2vzadv7rvN$3wEIiMLm,+2 more (map truncated)
  IfcType = 52
  Length = 0
  Material = -> Material007
  MoveBase = false
  MoveWithHost = false
  Nodes = (2) [(3798,-460,0),(3798,-460,3600)]
  NodesOffset = 0
  Normal = (0,0,0)
  PerimeterLength = 1060
  Placement = pos=(0,-2.558e-13,-40) rot=(0,0,1;0rad)
  VerticalArea = 2459200
  Width = 100
FEATURE [Part::Part2DObjectPython] Rectangle3349  label="Фальшколонна 021"  # Draft 2D object (typed FeaturePython)
  Area = 54600
  ChamferSize = 0
  Columns = 1
  FilletRadius = 0
  Height = 140
  Length = 390
  MakeFace = true
  Placement = pos=(10490,7895,0) rot=(0,0,1;0rad)
  Rows = 1
FEATURE [Part::FeaturePython] Structure420  label="Облицовка камнем 036"  # Arch/BIM 52 (typed FeaturePython)
  Base = -> Rectangle3349
  FaceMaker = 0
  GlobalId = 0xXC9cy$jFShfp8t3IltaA
  Height = 2540
  HorizontalArea = 54600
  IfcData = IfcUID=0xXC9cy$jFShfp8t3IltaA,+2 more (map truncated)
  IfcType = 52
  Length = 0
  Material = -> Material007
  MoveBase = false
  MoveWithHost = false
  Nodes = (2) [(3798,-460,0),(3798,-460,3600)]
  NodesOffset = 0
  Normal = (0,0,0)
  PerimeterLength = 1060
  Placement = pos=(0,4.55e-13,-40) rot=(0,0,1;0rad)
  VerticalArea = 2692400
  Width = 100
FEATURE [Part::Feature] Extrude098001  label="Подкосы крыльца 015"
  Placement = pos=(19738,7460,0) rot=(0,0,1;3.14159rad)
  shape: bbox 150 x 983 x 1690 mm, 12 faces (baked)
FEATURE [Part::FeaturePython] Component002  label="Подкос011"  # Arch/BIM 52 (typed FeaturePython)
  Base = -> Extrude098001
  GlobalId = 305owz_yPFe8XEoQwHyy9O
  HorizontalArea = 0
  IfcData = IfcUID=305owz_yPFe8XEoQwHyy9O,+2 more (map truncated)
  IfcType = 52
  Material = -> Material
  MoveBase = false
  MoveWithHost = false
  PerimeterLength = 0
  Placement = pos=(19734,7445,0) rot=(0,0,1;3.14159rad)
  VerticalArea = 0
FEATURE [Part::Feature] Extrude095001  label="Подкосы крыльца 013"
  Placement = pos=(476,-7.69351e-07,0) rot=(0,0,1;0rad)
  shape: bbox 150 x 983 x 1690 mm, 12 faces (baked)
FEATURE [Part::FeaturePython] Component  label="Подкос001"  # Arch/BIM 52 (typed FeaturePython)
  Base = -> Extrude095001
  GlobalId = 0BS$y7q7z1ufWzhc1qzE8g
  HorizontalArea = 0
  IfcData = IfcUID=0BS$y7q7z1ufWzhc1qzE8g,+2 more (map truncated)
  IfcType = 52
  Material = -> Material
  MoveBase = false
  MoveWithHost = false
  PerimeterLength = 0
  Placement = pos=(456,15,0) rot=(0,0,1;0rad)
  VerticalArea = 0
FEATURE [Part::Feature] Extrude099001  label="Подкосы крыльца 014"
  Placement = pos=(14668,7460,0) rot=(0,0,1;3.14159rad)
  shape: bbox 150 x 983 x 1690 mm, 12 faces (baked)
FEATURE [Part::FeaturePython] Component001  label="Подкос010"  # Arch/BIM 52 (typed FeaturePython)
  Base = -> Extrude099001
  GlobalId = 3F3uK2ozfBRxSV0PWqxsz5
  HorizontalArea = 0
  IfcData = IfcUID=3F3uK2ozfBRxSV0PWqxsz5,+2 more (map truncated)
  IfcType = 52
  Material = -> Material
  MoveBase = false
  MoveWithHost = false
  PerimeterLength = 0
  Placement = pos=(14664,7445,0) rot=(0,0,1;3.14159rad)
  VerticalArea = 0
FEATURE [Part::Feature] Extrude096001  label="Подкосы крыльца 016"
  Placement = pos=(-3422,-7.69351e-07,0) rot=(0,0,1;0rad)
  shape: bbox 150 x 983 x 1690 mm, 12 faces (baked)
FEATURE [Part::FeaturePython] Component003  label="Подкос012"  # Arch/BIM 52 (typed FeaturePython)
  Base = -> Extrude096001
  GlobalId = 0rQ8hKrWb1kuTVB9ZxaTxQ
  HorizontalArea = 0
  IfcData = IfcUID=0rQ8hKrWb1kuTVB9ZxaTxQ,+2 more (map truncated)
  IfcType = 52
  Material = -> Material
  MoveBase = false
  MoveWithHost = false
  PerimeterLength = 0
  Placement = pos=(-3314,15,0) rot=(0,0,1;0rad)
  VerticalArea = 0
FEATURE [Part::Part2DObjectPython] Line1583  label="облицовка_стены_032"  # Draft 2D object (typed FeaturePython)
  ChamferSize = 0
  Closed = true
  End = (12950,8015,0)
  FilletRadius = 0
  Length = 13510
  MakeFace = false
  Placement = pos=(-450,8535,0) rot=(0,0,1;0rad)
  Points = (2) [(-110,-520,0),(13400,-520,0)]
  Start = (-560,8015,0)
  Subdivisions = 0
FEATURE [Part::FeaturePython] Structure421  label="Проём_четв._045"  # Arch/BIM 52 (typed FeaturePython)
  Base = -> Rectangle3200
  FaceMaker = 0
  Height = 1500
  HorizontalArea = 219600
  IfcData = complex_attributes={"OwnerHistory": {}, "IsNestedBy": {}, "IsDecomposedBy": {}, "IsDefinedBy": {}, "ObjectPlacement": {}, "Representation":... (+4 chars omitted)
  IfcType = 52
  Length = 0
  MoveBase = false
  MoveWithHost = false
  Nodes = (2) [(5775,-395,0),(5775,-395,2335)]
  NodesOffset = 0
  Normal = (0,0,0)
  PerimeterLength = 3900
  Placement = pos=(0,0,1010) rot=(0,0,1;0rad)
  VerticalArea = 5.85e+06
  Width = 100
FEATURE [Part::FeaturePython] Structure422  label="Проём_четв._046"  # Arch/BIM 52 (typed FeaturePython)
  Base = -> Rectangle3201
  FaceMaker = 0
  Height = 1500
  HorizontalArea = 94800
  IfcData = complex_attributes={"OwnerHistory": {}, "IsNestedBy": {}, "IsDecomposedBy": {}, "IsDefinedBy": {}, "ObjectPlacement": {}, "Representation":... (+4 chars omitted)
  IfcType = 52
  Length = 0
  MoveBase = false
  MoveWithHost = false
  Nodes = (2) [(5775,-395,0),(5775,-395,2335)]
  NodesOffset = 0
  Normal = (0,0,0)
  PerimeterLength = 1820
  Placement = pos=(0,0,1010) rot=(0,0,1;0rad)
  VerticalArea = 2.73e+06
  Width = 100
FEATURE [Part::FeaturePython] Structure424  label="Облицовка камнем 037"  # Arch/BIM 52 (typed FeaturePython)
  Base = -> Wire805
  FaceMaker = 0
  Height = 1500
  HorizontalArea = 154800
  IfcData = attributes={"GlobalId": {"name": "GlobalId", "type": "IfcGloballyUniqueId", "is_enum": false, "enum_values": []}, "Description": {"... (+484 chars omitted),+1 more (map truncated)
  IfcType = 52
  Length = 0
  Material = -> Material007
  MoveBase = false
  MoveWithHost = false
  Nodes = (2) [(4505,7955,0),(4505,7955,1500)]
  NodesOffset = 0
  Normal = (0,0,1)
  PerimeterLength = 2820
  Placement = pos=(0,0,1010) rot=(0,0,1;0rad)
  VerticalArea = 4.23e+06
  Width = 100
FEATURE [Part::FeaturePython] Structure425  label="Облицовка камнем 038"  # Arch/BIM 52 (typed FeaturePython)
  Base = -> Rectangle3346
  FaceMaker = 0
  Height = 2925
  HorizontalArea = 365400
  IfcData = attributes={"GlobalId": {"name": "GlobalId", "type": "IfcGloballyUniqueId", "is_enum": false, "enum_values": []}, "Description": {"... (+484 chars omitted),+1 more (map truncated)
  IfcType = 52
  Length = 0
  Material = -> Material007
  MoveBase = false
  MoveWithHost = false
  Nodes = (2) [(3798,-460,0),(3798,-460,3600)]
  NodesOffset = 0
  Normal = (0,0,0)
  PerimeterLength = 5500
  Placement = pos=(0,1.14e-13,-46) rot=(0,0,1;0rad)
  VerticalArea = 1.60875e+07
  Width = 100
FEATURE [Part::FeaturePython] Wall298  label="облицовка 017"  # Arch/BIM 166 (typed FeaturePython)
  Align = 0
  Area = 48636000
  Base = -> Line1583
  BlockHeight = 65
  BlockLength = 250
  CountBroken = 108
  CountEntire = 1737
  Face = 0
  GlobalId = 2NuME8GJTD0RJft756pcFm
  Height = 3600
  HorizontalArea = 2.0904e+06
  IfcData = IfcUID=2NuME8GJTD0RJft756pcFm; attributes={"GlobalId": {"value": "2NuME8GJTD0RJft756pcFm"}}
  IfcType = 166
  Joint = 10
  Length = 13510
  MakeBlocks = false
  Material = -> Material003
  MoveBase = false
  MoveWithHost = false
  Normal = (0,0,0)
  OffsetFirst = 120
  OffsetSecond = 250
  PerimeterLength = 0
  Placement = pos=(0,0,-40) rot=(0,0,1;0rad)
  PredefinedType = 0
  Subtractions = -> [Structure421,Structure422,Structure424,Structure425]
  VerticalArea = 72229380
  Width = 120
FEATURE [Part::Part2DObjectPython] Line1584  label="облицовка_стены_033"  # Draft 2D object (typed FeaturePython)
  ChamferSize = 0
  Closed = true
  End = (-430,-555,0)
  FilletRadius = 0
  Length = 13380
  MakeFace = false
  Placement = pos=(12780,-555,0) rot=(0,0,1;0rad)
  Points = (2) [(170,2.84217e-12,0),(-13210,2.84217e-12,0)]
  Start = (12950,-555,0)
  Subdivisions = 0
FEATURE [Part::FeaturePython] Structure426  label="Проём_четв._048"  # Arch/BIM 52 (typed FeaturePython)
  Base = -> Rectangle2573
  FaceMaker = 0
  Height = 1275
  HorizontalArea = 63600
  IfcData = complex_attributes={"OwnerHistory": {}, "IsNestedBy": {}, "IsDecomposedBy": {}, "IsDefinedBy": {}, "ObjectPlacement": {}, "Representation":... (+4 chars omitted)
  IfcType = 52
  Length = 0
  MoveBase = false
  MoveWithHost = false
  Nodes = (2) [(4618,-450,0),(4618,-450,1320)]
  NodesOffset = 0
  Normal = (0,0,0)
  PerimeterLength = 1300
  Placement = pos=(0,0,1010) rot=(0,0,1;0rad)
  VerticalArea = 1657500
  Width = 100
FEATURE [Part::FeaturePython] Structure427  label="Проём_четв._049"  # Arch/BIM 52 (typed FeaturePython)
  Base = -> Rectangle2571
  FaceMaker = 0
  Height = 2315
  HorizontalArea = 252000
  IfcData = complex_attributes={"OwnerHistory": {}, "IsNestedBy": {}, "IsDecomposedBy": {}, "IsDefinedBy": {}, "ObjectPlacement": {}, "Representation":... (+4 chars omitted)
  IfcType = 52
  Length = 0
  MoveBase = false
  MoveWithHost = false
  Nodes = (2) [(5775,-395,0),(5775,-395,2335)]
  NodesOffset = 0
  Normal = (0,0,0)
  PerimeterLength = 2340
  Placement = pos=(0,0,-40) rot=(0,0,1;0rad)
  VerticalArea = 503100
  Width = 100
FEATURE [Part::FeaturePython] Structure428  label="Проём_четв._050"  # Arch/BIM 52 (typed FeaturePython)
  Base = -> Rectangle2580
  FaceMaker = 0
  Height = 1275
  HorizontalArea = 63600
  IfcData = complex_attributes={"OwnerHistory": {}, "IsNestedBy": {}, "IsDecomposedBy": {}, "IsDefinedBy": {}, "ObjectPlacement": {}, "Representation":... (+4 chars omitted)
  IfcType = 52
  Length = 0
  MoveBase = false
  MoveWithHost = false
  Nodes = (2) [(5775,-395,0),(5775,-395,2335)]
  NodesOffset = 0
  Normal = (0,0,0)
  PerimeterLength = 1300
  Placement = pos=(0,0,1010) rot=(0,0,1;0rad)
  VerticalArea = 1657500
  Width = 100
FEATURE [Part::FeaturePython] Structure429  label="Облицовка камнем 039"  # Arch/BIM 52 (typed FeaturePython)
  Base = -> Rectangle3345
  FaceMaker = 0
  Height = 2700
  HorizontalArea = 256200
  IfcData = attributes={"GlobalId": {"name": "GlobalId", "type": "IfcGloballyUniqueId", "is_enum": false, "enum_values": []}, "Description": {"... (+484 chars omitted),+1 more (map truncated)
  IfcType = 52
  Length = 0
  Material = -> Material007
  MoveBase = false
  MoveWithHost = false
  Nodes = (2) [(3798,-460,0),(3798,-460,3600)]
  NodesOffset = 0
  Normal = (0,0,0)
  PerimeterLength = 3940
  Placement = pos=(0,1.14e-13,-40) rot=(0,0,1;0rad)
  VerticalArea = 1.0638e+07
  Width = 100
FEATURE [Part::FeaturePython] Wall299  label="облицовка 018"  # Arch/BIM 166 (typed FeaturePython)
  Align = 0
  Area = 48168000
  Base = -> Line1584
  BlockHeight = 65
  BlockLength = 250
  CountBroken = 120
  CountEntire = 2088
  Face = 0
  GlobalId = 3SgCB7ImHBKRjTRpndNtdS
  Height = 3600
  HorizontalArea = 1732800
  IfcData = IfcUID=3SgCB7ImHBKRjTRpndNtdS; attributes={"GlobalId": {"value": "3SgCB7ImHBKRjTRpndNtdS"}}
  IfcType = 166
  Joint = 10
  Length = 13380
  MakeBlocks = false
  Material = -> Material003
  MoveBase = false
  MoveWithHost = false
  Normal = (0,0,0)
  OffsetFirst = 120
  OffsetSecond = 250
  PerimeterLength = 0
  Placement = pos=(0,0,-40) rot=(0,0,1;0rad)
  PredefinedType = 0
  Subtractions = -> [Structure426,Structure427,Structure428,Structure429]
  VerticalArea = 85875000
  Width = 120
FEATURE [Part::Part2DObjectPython] Line1585  label="облицовка_стены_034"  # Draft 2D object (typed FeaturePython)
  ChamferSize = 0
  Closed = true
  End = (-560,-555,0)
  FilletRadius = 0
  Length = 8440
  MakeFace = false
  Placement = pos=(-515,-735,0) rot=(0,0,1;0rad)
  Points = (2) [(-45,8620,0),(-45,180,0)]
  Start = (-560,7885,0)
  Subdivisions = 0
FEATURE [Part::FeaturePython] Structure430  label="Проём_четв._051"  # Arch/BIM 52 (typed FeaturePython)
  Base = -> Rectangle2858
  FaceMaker = 0
  Height = 1500
  HorizontalArea = 157200
  IfcData = complex_attributes={"OwnerHistory": {}, "IsNestedBy": {}, "IsDecomposedBy": {}, "IsDefinedBy": {}, "ObjectPlacement": {}, "Representation":... (+4 chars omitted)
  IfcType = 52
  Length = 0
  MoveBase = false
  MoveWithHost = false
  Nodes = (2) [(1035,460,0),(1035,460,535)]
  NodesOffset = 0
  Normal = (0,0,0)
  PerimeterLength = 2860
  Placement = pos=(0,0,1010) rot=(0,0,1;0rad)
  VerticalArea = 4290000
  Width = 100
FEATURE [Part::FeaturePython] Wall300  label="облицовка 019"  # Arch/BIM 166 (typed FeaturePython)
  Align = 1
  Area = 30384000
  Base = -> Line1585
  BlockHeight = 65
  BlockLength = 250
  CountBroken = 68
  CountEntire = 1421
  Face = 0
  GlobalId = 2BxWlk8bv7HwfTqswZTI_V
  Height = 3600
  HorizontalArea = 1170000
  IfcData = IfcUID=2BxWlk8bv7HwfTqswZTI_V; attributes={"GlobalId": {"value": "2BxWlk8bv7HwfTqswZTI_V"}}
  IfcType = 166
  Joint = 10
  Length = 8440
  MakeBlocks = false
  Material = -> Material003
  MoveBase = false
  MoveWithHost = false
  Normal = (0,0,0)
  OffsetFirst = 120
  OffsetSecond = 250
  PerimeterLength = 0
  Placement = pos=(0,0,-40) rot=(0,0,1;0rad)
  PredefinedType = 0
  Subtractions = -> [Structure430]
  VerticalArea = 58062000
  Width = 120
FEATURE [Part::Part2DObjectPython] Line1586  label="облицовка_стены_035"  # Draft 2D object (typed FeaturePython)
  ChamferSize = 0
  Closed = true
  End = (13080,8015,0)
  FilletRadius = 0
  Length = 8570
  MakeFace = false
  Placement = pos=(14815,4225,0) rot=(0,0,1;0rad)
  Points = (2) [(-1735,-4780,0),(-1735,3790,0)]
  Start = (13080,-555,0)
  Subdivisions = 0
FEATURE [Part::FeaturePython] Structure431  label="Проём_четв._052"  # Arch/BIM 52 (typed FeaturePython)
  Base = -> Rectangle2579
  FaceMaker = 0
  Height = 1275
  HorizontalArea = 219600
  IfcData = complex_attributes={"OwnerHistory": {}, "IsNestedBy": {}, "IsDecomposedBy": {}, "IsDefinedBy": {}, "ObjectPlacement": {}, "Representation":... (+4 chars omitted)
  IfcType = 52
  Length = 0
  MoveBase = false
  MoveWithHost = false
  Nodes = (2) [(1035,460,0),(1035,460,535)]
  NodesOffset = 0
  Normal = (0,0,0)
  PerimeterLength = 3900
  Placement = pos=(0,0,1235) rot=(0,0,1;0rad)
  VerticalArea = 4.9725e+06
  Width = 100
FEATURE [Part::FeaturePython] Structure432  label="Проём_четв._053"  # Arch/BIM 52 (typed FeaturePython)
  Base = -> Rectangle2577
  FaceMaker = 0
  Height = 1275
  HorizontalArea = 94800
  IfcData = complex_attributes={"OwnerHistory": {}, "IsNestedBy": {}, "IsDecomposedBy": {}, "IsDefinedBy": {}, "ObjectPlacement": {}, "Representation":... (+4 chars omitted)
  IfcType = 52
  Length = 0
  MoveBase = false
  MoveWithHost = false
  Nodes = (2) [(1035,460,0),(1035,460,535)]
  NodesOffset = 0
  Normal = (0,0,0)
  PerimeterLength = 1820
  Placement = pos=(0,0,1235) rot=(0,0,1;0rad)
  VerticalArea = 2320500
  Width = 100
FEATURE [App::GeometryPython] BuildingPart001  label="проёмы"  # Arch/BIM 52 (typed FeaturePython)
  Area = 0
  Group = -> [Structure016,Structure017,Structure019,Structure020,Structure021,Structure023,Structure024,Structure026,Structure141,Structure158,Structure285,Structure148,Structure304,Structure306,Structure308,Structure313,Structure315,Structure317,Structure333,Structure350,Structure360,Structure421,Structure422,Structure432,Structure431,Structure430,Structure426,Structure428]
  Height = 0
  HeightPropagate = true
  IfcData = complex_attributes={"OwnerHistory": {}, "IsNestedBy": {}, "IsDecomposedBy": {}, "IsDefinedBy": {}, "ObjectPlacement": {}, "Representation":... (+4 chars omitted)
  IfcType = 52
  LevelOffset = 0
FEATURE [Part::FeaturePython] Structure433  label="Облицовка камнем 040"  # Arch/BIM 52 (typed FeaturePython)
  Base = -> Wire663
  FaceMaker = 0
  Height = 1275
  HorizontalArea = 108000
  IfcData = attributes={"GlobalId": {"name": "GlobalId", "type": "IfcGloballyUniqueId", "is_enum": false, "enum_values": []}, "Description": {"... (+484 chars omitted),+1 more (map truncated)
  IfcType = 52
  Length = 0
  Material = -> Material007
  MoveBase = false
  MoveWithHost = false
  Nodes = (2) [(13020,3665,0),(13020,3665,1275)]
  NodesOffset = 0
  Normal = (0,0,1)
  PerimeterLength = 2040
  Placement = pos=(0,0,1235) rot=(0,0,1;0rad)
  VerticalArea = 2.601e+06
  Width = 100
FEATURE [Part::FeaturePython] Wall305  label="облицовка 020"  # Arch/BIM 166 (typed FeaturePython)
  Align = 1
  Area = 30852000
  Base = -> Line1586
  BlockHeight = 65
  BlockLength = 250
  CountBroken = 66
  CountEntire = 1299
  Face = 0
  GlobalId = 0ylFaZ_Q11vgSu8iyeHdyc
  Height = 3600
  HorizontalArea = 1.4508e+06
  IfcData = IfcUID=0ylFaZ_Q11vgSu8iyeHdyc; attributes={"GlobalId": {"value": "0ylFaZ_Q11vgSu8iyeHdyc"}}
  IfcType = 166
  Joint = 10
  Length = 8570
  MakeBlocks = false
  Material = -> Material003
  MoveBase = false
  MoveWithHost = false
  Normal = (0,0,0)
  OffsetFirst = 120
  OffsetSecond = 250
  PerimeterLength = 0
  Placement = pos=(0,0,-40) rot=(0,0,1;0rad)
  PredefinedType = 0
  Subtractions = -> [Structure431,Structure432,Structure433]
  VerticalArea = 53898000
  Width = 120
FEATURE [Part::Part2DObjectPython] Line1587  label="контрфорс_линия_005"  # Draft 2D object (typed FeaturePython)
  ChamferSize = 0
  Closed = true
  End = (3470,-635,0)
  FilletRadius = 0
  Length = 380
  MakeFace = false
  Placement = pos=(3680,-635,0) rot=(0,0,1;0rad)
  Points = (2) [(170,1.02318e-12,0),(-210,9.09495e-13,0)]
  Start = (3850,-635,0)
  Subdivisions = 0
FEATURE [Part::FeaturePython] Wall306  label="Контрфорс 005"  # Arch/BIM 166 (typed FeaturePython)
  Align = 0
  Area = 741000
  Base = -> Line1587
  BlockHeight = 65
  BlockLength = 250
  CountBroken = 26
  CountEntire = 26
  Face = 0
  GlobalId = 342k6QohT2QOnSo3Rt4Yr5
  Height = 1950
  HorizontalArea = 0
  IfcData = IfcUID=342k6QohT2QOnSo3Rt4Yr5; attributes={"GlobalId": {"value": "342k6QohT2QOnSo3Rt4Yr5"}}
  IfcType = 166
  Joint = 10
  Length = 380
  MakeBlocks = true
  Material = -> Material003
  MoveBase = false
  MoveWithHost = false
  Normal = (0,0,0)
  OffsetFirst = 250
  OffsetSecond = 120
  PerimeterLength = 0
  Placement = pos=(0,0,-40) rot=(0,0,1;0rad)
  PredefinedType = 0
  VerticalArea = 0
  Width = 120
FEATURE [Part::Part2DObjectPython] Line1588  label="контрфорс_линия_006"  # Draft 2D object (typed FeaturePython)
  ChamferSize = 0
  Closed = true
  End = (8540,-635,0)
  FilletRadius = 0
  Length = 380
  MakeFace = false
  Placement = pos=(8750,-635,0) rot=(0,0,1;0rad)
  Points = (2) [(170,1.02318e-12,0),(-210,9.09495e-13,0)]
  Start = (8920,-635,0)
  Subdivisions = 0
FEATURE [Part::FeaturePython] Wall307  label="Контрфорс 006"  # Arch/BIM 166 (typed FeaturePython)
  Align = 0
  Area = 741000
  Base = -> Line1588
  BlockHeight = 65
  BlockLength = 250
  CountBroken = 26
  CountEntire = 26
  Face = 0
  GlobalId = 2QQuq56G56SBKvMoDbUykg
  Height = 1950
  HorizontalArea = 0
  IfcData = IfcUID=2QQuq56G56SBKvMoDbUykg; attributes={"GlobalId": {"value": "2QQuq56G56SBKvMoDbUykg"}}
  IfcType = 166
  Joint = 10
  Length = 380
  MakeBlocks = true
  Material = -> Material003
  MoveBase = false
  MoveWithHost = false
  Normal = (0,0,0)
  OffsetFirst = 120
  OffsetSecond = 250
  PerimeterLength = 0
  Placement = pos=(0,0,-40) rot=(0,0,1;0rad)
  PredefinedType = 0
  VerticalArea = 0
  Width = 120
FEATURE [Part::Part2DObjectPython] Line1589  label="контрфорс_линия_007"  # Draft 2D object (typed FeaturePython)
  ChamferSize = 0
  Closed = true
  End = (7500,8095,0)
  FilletRadius = 0
  Length = 380
  MakeFace = false
  Placement = pos=(7710,8095,0) rot=(0,0,1;0rad)
  Points = (2) [(170,9.09495e-13,0),(-210,9.09495e-13,0)]
  Start = (7880,8095,0)
  Subdivisions = 0
FEATURE [Part::FeaturePython] Wall308  label="Контрфорс 007"  # Arch/BIM 166 (typed FeaturePython)
  Align = 1
  Area = 741000
  Base = -> Line1589
  BlockHeight = 65
  BlockLength = 250
  CountBroken = 26
  CountEntire = 26
  Face = 0
  GlobalId = 3waotNP91F$e4vFRfeMs10
  Height = 1950
  HorizontalArea = 0
  IfcData = IfcUID=3waotNP91F$e4vFRfeMs10; attributes={"GlobalId": {"value": "3waotNP91F$e4vFRfeMs10"}}
  IfcType = 166
  Joint = 10
  Length = 380
  MakeBlocks = true
  Material = -> Material003
  MoveBase = false
  MoveWithHost = false
  Normal = (0,0,0)
  OffsetFirst = 120
  OffsetSecond = 250
  PerimeterLength = 0
  Placement = pos=(0,0,-40) rot=(0,0,1;0rad)
  PredefinedType = 0
  VerticalArea = 0
  Width = 120
FEATURE [Part::Part2DObjectPython] Line1590  label="контрфорс_линия_008"  # Draft 2D object (typed FeaturePython)
  ChamferSize = 0
  Closed = true
  End = (11270,8095,0)
  FilletRadius = 0
  Length = 380
  MakeFace = false
  Placement = pos=(11480,8095,0) rot=(0,0,1;0rad)
  Points = (2) [(170,9.09495e-13,0),(-210,9.09495e-13,0)]
  Start = (11650,8095,0)
  Subdivisions = 0
FEATURE [Part::FeaturePython] Wall309  label="Контрфорс 008"  # Arch/BIM 166 (typed FeaturePython)
  Align = 1
  Area = 741000
  Base = -> Line1590
  BlockHeight = 65
  BlockLength = 250
  CountBroken = 26
  CountEntire = 26
  Face = 0
  GlobalId = 0Yg83kwN5EPeGAKGfacmqk
  Height = 1950
  HorizontalArea = 0
  IfcData = IfcUID=0Yg83kwN5EPeGAKGfacmqk; attributes={"GlobalId": {"value": "0Yg83kwN5EPeGAKGfacmqk"}}
  IfcType = 166
  Joint = 10
  Length = 380
  MakeBlocks = true
  Material = -> Material003
  MoveBase = false
  MoveWithHost = false
  Normal = (0,0,0)
  OffsetFirst = 250
  OffsetSecond = 120
  PerimeterLength = 0
  Placement = pos=(0,0,-40) rot=(0,0,1;0rad)
  PredefinedType = 0
  VerticalArea = 0
  Width = 120
FEATURE [App::FeaturePython] WPProxy001  # WARN: FeaturePython — macro-defined, semantics opaque (R4)
  Placement = pos=(-560,-540,3130) rot=(0,0,1;0rad)
FEATURE [Sketcher::SketchObject] Sketch364
  FullyConstrained = false
  MapMode = 5
  Placement = pos=(10929,-710.046,-122.202) rot=(0.57735,0.57735,0.57735;2.0944rad)
  sketch-geometry (10):
    g0: LineSegment StartX=8710.05 StartY=1993.19 StartZ=0 EndX=8710.05 EndY=3683.19 EndZ=0
    g1: LineSegment StartX=8710.05 StartY=3683.19 StartZ=0 EndX=9693.03 EndY=2994.9 EndZ=0
    g2: LineSegment StartX=9693.03 StartY=2994.9 StartZ=0 EndX=9635.67 EndY=2912.98 EndZ=0
    g3: LineSegment StartX=9635.67 StartY=2912.98 StartZ=0 EndX=9471.84 EndY=3027.7 EndZ=0
    g4: LineSegment StartX=9471.84 StartY=3027.7 StartZ=0 EndX=8810.05 EndY=2082.56 EndZ=0
    g5: LineSegment StartX=8810.05 StartY=2082.56 StartZ=0 EndX=8810.05 EndY=1993.19 EndZ=0
    g6: LineSegment StartX=8810.05 StartY=1993.19 StartZ=0 EndX=8710.05 EndY=1993.19 EndZ=0
    g7: LineSegment StartX=8810.05 StartY=2256.9 StartZ=0 EndX=8810.05 EndY=3491.09 EndZ=0
    g8: LineSegment StartX=8810.05 StartY=3491.09 StartZ=0 EndX=9389.93 EndY=3085.06 EndZ=0
    g9: LineSegment StartX=9389.93 StartY=3085.06 StartZ=0 EndX=8810.05 EndY=2256.9 EndZ=0
  constraints (28):
    c: Vertical(g0)
    c: Coincident(g1,g2)
    c: Coincident(g2,g3)
    c: Coincident(g3,g4)
    c: Coincident(g4,g5)
    c: Vertical(g5)
    c: Coincident(g5,g6)
    c: Coincident(g6,g0)
    c: Vertical(g7)
    c: Coincident(g7,g8)
    c: Coincident(g8,g9)
    c: Coincident(g9,g7)
    c: Parallel(g4,g9)
    c: Horizontal(g6)
    c: Parallel(g3,g1)
    c: Parallel(g9,g2)
    c: Parallel(g8,g3)
    c: Distance(g8,g4) = 100
    c: Distance(g8,g1) = 100
    c: Distance(g3,g1) = 100
    c: Distance(g7,g0) = 100
    c: DistanceX(g6,g6) = 100
    c: Angle(g1) = -0.610865
    c: Coincident(g0,g1)
    c: Distance(g1) = 1200
    c: DistanceY(g0,g0) = 1690
    c: Angle(g4,g3) = 1.5708
    c: Distance(g3) = 200
FEATURE [Part::Extrusion] Extrude099002  label="Подкосы крыльца 017"
  Base = -> Sketch364
  Dir = (1,0,0)
  DirMode = 2
  FaceMakerClass = Part::FaceMakerBullseye
  LengthFwd = 150
  LengthRev = 0
  Placement = pos=(19738,7460,0) rot=(0,0,1;3.14159rad)
  Solid = true
  Symmetric = false
FEATURE [Part::Extrusion] Extrude099003  label="Подкосы крыльца 018"
  Base = -> Sketch364
  Dir = (1,0,0)
  DirMode = 2
  FaceMakerClass = Part::FaceMakerBullseye
  LengthFwd = 150
  LengthRev = 0
  Placement = pos=(476,-7.69351e-07,0) rot=(0,0,1;0rad)
  Solid = true
  Symmetric = false
FEATURE [Part::Extrusion] Extrude099004  label="Подкосы крыльца 019"
  Base = -> Sketch364
  Dir = (1,0,0)
  DirMode = 2
  FaceMakerClass = Part::FaceMakerBullseye
  LengthFwd = 150
  LengthRev = 0
  Placement = pos=(-3422,-7.69351e-07,0) rot=(0,0,1;0rad)
  Solid = true
  Symmetric = false
FEATURE [Part::Extrusion] Extrude099005  label="Подкосы крыльца 020"
  Base = -> Sketch364
  Dir = (1,0,0)
  DirMode = 2
  FaceMakerClass = Part::FaceMakerBullseye
  LengthFwd = 150
  LengthRev = 0
  Placement = pos=(14668,7460,0) rot=(0,0,1;3.14159rad)
  Solid = true
  Symmetric = false
FEATURE [App::DocumentObjectGroup] Group128  label="NotSupportedForExport_to_IFC"
  Group = -> [Extrude099002,Extrude099003,Extrude099004,Extrude099005,Pipe004,Pipe007]
FEATURE [App::GeometryPython] BuildingPart  label="Окна и двери (мансарда)"  # Arch/BIM 52 (typed FeaturePython)
  Area = 7617000
  GlobalId = 2ZdcXw_FbERwG8YjxnAt$R
  Group = -> [Window066,Window067,Window063,Window062,Window061,Window059,Window057]
  Height = 0
  HeightPropagate = true
  IfcData = IfcUID=2ZdcXw_FbERwG8YjxnAt$R,+2 more (map truncated)
  IfcType = 52
  LevelOffset = 0
FEATURE [Part::FeaturePython] Component004  label="Топка L700"  # Arch/BIM 15 (typed FeaturePython)
  Base = -> Box3211
  GlobalId = 1gtXDcR713zhxl2yKk2Izx
  HorizontalArea = 0
  IfcData = IfcUID=1gtXDcR713zhxl2yKk2Izx,+2 more (map truncated)
  IfcType = 15
  Material = -> Material006
  MoveBase = false
  MoveWithHost = false
  PerimeterLength = 0
  Placement = pos=(8750,1885,800) rot=(0,0,1;0rad)
  PredefinedType = 0
  VerticalArea = 0
FEATURE [Part::FeaturePython] Component005  label="Дымоход 200 001"  # Arch/BIM 52 (typed FeaturePython)
  Base = -> Pipe008
  GlobalId = 1RYiQBgpbBTAR3hS4pyNB_
  HorizontalArea = 0
  IfcData = IfcUID=1RYiQBgpbBTAR3hS4pyNB_,+2 more (map truncated)
  IfcType = 52
  Material = -> Material010
  MoveBase = false
  MoveWithHost = false
  PerimeterLength = 0
  VerticalArea = 0
FEATURE [Part::FeaturePython] Component007  label="Вентканал 140мм 008"  # Arch/BIM 52 (typed FeaturePython)
  Base = -> Pipe009
  GlobalId = 1bznvW3p57su9hI7viqv$n
  HorizontalArea = 0
  IfcData = IfcUID=1bznvW3p57su9hI7viqv$n,+2 more (map truncated)
  IfcType = 52
  Material = -> Material010
  MoveBase = false
  MoveWithHost = false
  PerimeterLength = 0
  VerticalArea = 0
FEATURE [Part::FeaturePython] Component008  label="Вентканал 140мм 007"  # Arch/BIM 52 (typed FeaturePython)
  Base = -> Pipe010
  GlobalId = 30PUGUtgf8w9a6SsQSC606
  HorizontalArea = 0
  IfcData = IfcUID=30PUGUtgf8w9a6SsQSC606,+2 more (map truncated)
  IfcType = 52
  Material = -> Material010
  MoveBase = false
  MoveWithHost = false
  PerimeterLength = 0
  Placement = pos=(150,-150,0) rot=(0,0,1;0rad)
  VerticalArea = 0
FEATURE [Part::FeaturePython] Component009  label="Вентканал 140мм 006"  # Arch/BIM 52 (typed FeaturePython)
  Base = -> Pipe011
  GlobalId = 2DPp5cUajCNBraILIYWVwM
  HorizontalArea = 0
  IfcData = IfcUID=2DPp5cUajCNBraILIYWVwM,+2 more (map truncated)
  IfcType = 52
  Material = -> Material010
  MoveBase = false
  MoveWithHost = false
  PerimeterLength = 0
  Placement = pos=(0,-150,0) rot=(0,0,1;0rad)
  VerticalArea = 0
FEATURE [Part::FeaturePython] Component010  label="Вентканал 140мм 005"  # Arch/BIM 52 (typed FeaturePython)
  Base = -> Pipe013
  GlobalId = 2ewKzaCcr5eA7xHkmfw3LN
  HorizontalArea = 0
  IfcData = IfcUID=2ewKzaCcr5eA7xHkmfw3LN,+2 more (map truncated)
  IfcType = 52
  Material = -> Material010
  MoveBase = false
  MoveWithHost = false
  PerimeterLength = 0
  Placement = pos=(150,0,0) rot=(0,0,1;0rad)
  VerticalArea = 0
FEATURE [Part::FeaturePython] Component011  label="Фановый стояк 002"  # Arch/BIM 52 (typed FeaturePython)
  Base = -> Pipe006
  GlobalId = 0fM_EzyLfDH9wwlzWxKcxT
  HorizontalArea = 0
  IfcData = IfcUID=0fM_EzyLfDH9wwlzWxKcxT,+2 more (map truncated)
  IfcType = 52
  Material = -> Material010
  MoveBase = false
  MoveWithHost = false
  PerimeterLength = 0
  VerticalArea = 0
FEATURE [Part::FeaturePython] Component013  label="бак расширительный001"  # Arch/BIM 52 (typed FeaturePython)
  Base = -> Cylinder003
  GlobalId = 1M0Pc_1oL1dAVej87m7tiQ
  HorizontalArea = 0
  IfcData = IfcUID=1M0Pc_1oL1dAVej87m7tiQ,+2 more (map truncated)
  IfcType = 52
  Material = -> Material010
  MoveBase = false
  MoveWithHost = false
  PerimeterLength = 0
  Placement = pos=(7680,1990,2200) rot=(0,0,1;0rad)
  VerticalArea = 0
FEATURE [Part::FeaturePython] Component014  label="Котёл 24кВт одноконтурн. закртытая камера001"  # Arch/BIM 52 (typed FeaturePython)
  Base = -> Box3220
  GlobalId = 3xYIuffef0591nSqu_zTts
  HorizontalArea = 0
  IfcData = IfcUID=3xYIuffef0591nSqu_zTts,+2 more (map truncated)
  IfcType = 52
  Material = -> Material010
  MoveBase = false
  MoveWithHost = false
  PerimeterLength = 0
  Placement = pos=(8130,2000,1300) rot=(0,0,1;0rad)
  VerticalArea = 0
FEATURE [Part::FeaturePython] Component015  label="БКН 120л001"  # Arch/BIM 52 (typed FeaturePython)
  Base = -> Cylinder002
  GlobalId = 1rGDNCqJr9TfpJcmQRNPPi
  HorizontalArea = 0
  IfcData = IfcUID=1rGDNCqJr9TfpJcmQRNPPi,+2 more (map truncated)
  IfcType = 52
  Material = -> Material010
  MoveBase = false
  MoveWithHost = false
  PerimeterLength = 0
  Placement = pos=(7680,1990,1000) rot=(0,0,1;0rad)
  VerticalArea = 0
FEATURE [Part::FeaturePython] Component016  label="грёбенка и насосы001"  # Arch/BIM 52 (typed FeaturePython)
  Base = -> Box3222
  GlobalId = 2B4UVsrmbF4xKMeEbnOrEi
  HorizontalArea = 0
  IfcData = IfcUID=2B4UVsrmbF4xKMeEbnOrEi,+2 more (map truncated)
  IfcType = 52
  Material = -> Material010
  MoveBase = false
  MoveWithHost = false
  PerimeterLength = 0
  Placement = pos=(7400,-10,0) rot=(0,0,1;0rad)
  VerticalArea = 0
FEATURE [Part::FeaturePython] Component017  label="Гидроакк. 100л001"  # Arch/BIM 52 (typed FeaturePython)
  Base = -> Cylinder004
  GlobalId = 3jeFyR0bH2F9QaToboQra_
  HorizontalArea = 0
  IfcData = IfcUID=3jeFyR0bH2F9QaToboQra_,+2 more (map truncated)
  IfcType = 52
  Material = -> Material010
  MoveBase = false
  MoveWithHost = false
  PerimeterLength = 0
  Placement = pos=(8350,2020,140) rot=(0,0,1;0rad)
  VerticalArea = 0
FEATURE [Part::FeaturePython] Component018  label="Котёл электр. (резерв)001"  # Arch/BIM 52 (typed FeaturePython)
  Base = -> Box3223
  GlobalId = 3fLs6$YNDCqPUF9yh_StuK
  HorizontalArea = 0
  IfcData = IfcUID=3fLs6$YNDCqPUF9yh_StuK,+2 more (map truncated)
  IfcType = 52
  Material = -> Material010
  MoveBase = false
  MoveWithHost = false
  PerimeterLength = 0
  Placement = pos=(7550,1490,1300) rot=(0,0,1;1.5708rad)
  VerticalArea = 0
FEATURE [App::MaterialObjectPython] Material012  label="Wood_mebel"  # material (typed FeaturePython)
  Description = A standard construction wood
  Material = AuthorAndLicense=Wood-Generic,CardName=Wood-Generic,Color=(0.34509803921568627, 0.6627450980392157, 0.5058823529411764, 1.0),Density=700 kg/m^3,+10 more (map truncated)
  ProductURL = https://en.wikipedia.org/wiki/Wood
  Transparency = 0
FEATURE [Part::FeaturePython] Component019  label="Мебель_001"  # Arch/BIM 52 (typed FeaturePython)
  Base = -> Box3143
  GlobalId = 3nI$K5MXnFSf1FSLhknV3E
  HorizontalArea = 0
  IfcData = IfcUID=3nI$K5MXnFSf1FSLhknV3E,+2 more (map truncated)
  IfcType = 52
  Material = -> Material012
  MoveBase = false
  MoveWithHost = false
  PerimeterLength = 0
  Placement = pos=(320,-25,0) rot=(0,0,1;1.5708rad)
  VerticalArea = 0
FEATURE [Part::FeaturePython] Component020  label="Мебель_031"  # Arch/BIM 52 (typed FeaturePython)
  Base = -> Box3216
  GlobalId = 0sMfDnDfXDKQPzl59nSg3w
  HorizontalArea = 0
  IfcData = IfcUID=0sMfDnDfXDKQPzl59nSg3w,+2 more (map truncated)
  IfcType = 52
  Material = -> Material012
  MoveBase = false
  MoveWithHost = false
  PerimeterLength = 0
  Placement = pos=(320,875,0) rot=(0,0,1;1.5708rad)
  VerticalArea = 0
FEATURE [Part::FeaturePython] Component021  label="Мебель_032"  # Arch/BIM 52 (typed FeaturePython)
  Base = -> Box3204
  GlobalId = 3v4KZ3erzAjxwqMZOEXsgs
  HorizontalArea = 0
  IfcData = IfcUID=3v4KZ3erzAjxwqMZOEXsgs,+2 more (map truncated)
  IfcType = 52
  Material = -> Material012
  MoveBase = false
  MoveWithHost = false
  PerimeterLength = 0
  Placement = pos=(370,3825,0) rot=(0,0,1;1.5708rad)
  VerticalArea = 0
FEATURE [Part::FeaturePython] Component022  label="Мебель_033"  # Arch/BIM 52 (typed FeaturePython)
  Base = -> Box3157
  GlobalId = 1irmjboHHBgQGOddX9HYrQ
  HorizontalArea = 0
  IfcData = IfcUID=1irmjboHHBgQGOddX9HYrQ,+2 more (map truncated)
  IfcType = 52
  Material = -> Material012
  MoveBase = false
  MoveWithHost = false
  PerimeterLength = 0
  Placement = pos=(-30,5040,0) rot=(0,0,1;0rad)
  VerticalArea = 0
FEATURE [Part::FeaturePython] Component023  label="Мебель_034"  # Arch/BIM 52 (typed FeaturePython)
  Base = -> Box3217
  GlobalId = 3xnzb49$n4OeOTx2O8OBOQ
  HorizontalArea = 0
  IfcData = IfcUID=3xnzb49$n4OeOTx2O8OBOQ,+2 more (map truncated)
  IfcType = 52
  Material = -> Material012
  MoveBase = false
  MoveWithHost = false
  PerimeterLength = 0
  Placement = pos=(-30,5640,0) rot=(0,0,1;0rad)
  VerticalArea = 0
FEATURE [Part::FeaturePython] Component024  label="Мебель_035"  # Arch/BIM 52 (typed FeaturePython)
  Base = -> Box3218
  GlobalId = 3zlhB5eMrASwK$nF_B$17d
  HorizontalArea = 0
  IfcData = IfcUID=3zlhB5eMrASwK$nF_B$17d,+2 more (map truncated)
  IfcType = 52
  Material = -> Material012
  MoveBase = false
  MoveWithHost = false
  PerimeterLength = 0
  Placement = pos=(370,6240,0) rot=(0,0,1;1.5708rad)
  VerticalArea = 0
FEATURE [Part::FeaturePython] Component025  label="Мебель_036"  # Arch/BIM 52 (typed FeaturePython)
  Base = -> Box3156
  GlobalId = 2LlK29D3D0RBA6mNzylxS_
  HorizontalArea = 0
  IfcData = IfcUID=2LlK29D3D0RBA6mNzylxS_,+2 more (map truncated)
  IfcType = 52
  Material = -> Material012
  MoveBase = false
  MoveWithHost = false
  PerimeterLength = 0
  Placement = pos=(4000,-25,0) rot=(0,0,1;1.5708rad)
  VerticalArea = 0
FEATURE [Part::FeaturePython] Component026  label="Мебель_037"  # Arch/BIM 52 (typed FeaturePython)
  Base = -> Box3155
  GlobalId = 2akPkUu2HEGPHq0U02EI1f
  HorizontalArea = 0
  IfcData = IfcUID=2akPkUu2HEGPHq0U02EI1f,+2 more (map truncated)
  IfcType = 52
  Material = -> Material012
  MoveBase = false
  MoveWithHost = false
  PerimeterLength = 0
  Placement = pos=(4100,1685,0) rot=(0,0,1;0rad)
  VerticalArea = 0
FEATURE [Part::FeaturePython] Component027  label="Мебель_038"  # Arch/BIM 52 (typed FeaturePython)
  Base = -> Box3154
  GlobalId = 01rWHBvXv688jV3_Ss2xzX
  HorizontalArea = 0
  IfcData = IfcUID=01rWHBvXv688jV3_Ss2xzX,+2 more (map truncated)
  IfcType = 52
  Material = -> Material012
  MoveBase = false
  MoveWithHost = false
  PerimeterLength = 0
  Placement = pos=(7300,-25,0) rot=(0,0,1;1.5708rad)
  VerticalArea = 0
FEATURE [Part::FeaturePython] Component028  label="Мебель_039"  # Arch/BIM 52 (typed FeaturePython)
  Base = -> Box3203
  GlobalId = 0TELnS7a95EADyr_UuBryd
  HorizontalArea = 0
  IfcData = IfcUID=0TELnS7a95EADyr_UuBryd,+2 more (map truncated)
  IfcType = 52
  Material = -> Material012
  MoveBase = false
  MoveWithHost = false
  PerimeterLength = 0
  Placement = pos=(8850,-25,800) rot=(0,0,1;0rad)
  VerticalArea = 0
FEATURE [Part::FeaturePython] Component029  label="Мебель_040"  # Arch/BIM 52 (typed FeaturePython)
  Base = -> Box3163
  GlobalId = 3x$ZLcTwH4lOi2HV3kkIS2
  HorizontalArea = 0
  IfcData = IfcUID=3x$ZLcTwH4lOi2HV3kkIS2,+2 more (map truncated)
  IfcType = 52
  Material = -> Material012
  MoveBase = false
  MoveWithHost = false
  PerimeterLength = 0
  Placement = pos=(4100,-25,0) rot=(0,0,1;0rad)
  VerticalArea = 0
FEATURE [App::MaterialObjectPython] Material013  label="ceramic other"  # material (typed FeaturePython)
  Description = ceramic other
  Material = AuthorAndLicense=Concrete-Generic,CardName=Concrete-Generic,Color=(0.8117647058823529, 0.8117647058823529, 0.8117647058823529, 1.0),+11 more (map truncated)
  Transparency = 0
FEATURE [Part::FeaturePython] Structure343  label="Ванна 170х100"  # Arch/BIM 52 (typed FeaturePython)
  Base = -> Wire808
  FaceMaker = 0
  GlobalId = 2VbcwV0QPCqROXcrzT3$_s
  Height = 600
  HorizontalArea = 1.62e+06
  IfcData = IfcUID=2VbcwV0QPCqROXcrzT3$_s,+2 more (map truncated)
  IfcType = 52
  Length = 0
  Material = -> Material013
  MoveBase = false
  MoveWithHost = false
  Nodes = (2) [(-2856.79,7112.64,0),(-2856.79,7112.64,600)]
  NodesOffset = 0
  Normal = (0,0,1)
  PerimeterLength = 4240.95
  Subtractions = -> [Structure342,Wall240]
  VerticalArea = 5037000
  Width = 100
FEATURE [Part::FeaturePython] Structure347  label="Раковина 90х45 Hatria Area"  # Arch/BIM 52 (typed FeaturePython)
  Base = -> Wire812
  FaceMaker = 0
  GlobalId = 2d5W_OQQf2Fxkoe6wMEOb9
  Height = 150
  HorizontalArea = 0
  IfcData = IfcUID=2d5W_OQQf2Fxkoe6wMEOb9,+2 more (map truncated)
  IfcType = 52
  Length = 0
  Material = -> Material013
  MoveBase = false
  MoveWithHost = false
  Nodes = (2) [(-2856.79,7112.64,0),(-2856.79,7112.64,600)]
  NodesOffset = 0
  Normal = (0,0,1)
  PerimeterLength = 0
  Placement = pos=(0,0,850) rot=(0,0,1;0rad)
  Subtractions = -> [Structure346]
  VerticalArea = 0
  Width = 100
FEATURE [Part::FeaturePython] Component030  label="унитаз с инсталляцией 003"  # Arch/BIM 52 (typed FeaturePython)
  Base = -> Fusion041
  GlobalId = 1DHlQrIaXCZ9oXu4naqRMg
  HorizontalArea = 0
  IfcData = IfcUID=1DHlQrIaXCZ9oXu4naqRMg,+2 more (map truncated)
  IfcType = 52
  Material = -> Material013
  MoveBase = false
  MoveWithHost = false
  PerimeterLength = 0
  Placement = pos=(9508.52,16323.1,0) rot=(0,0,1;3.92699rad)
  VerticalArea = 0
FEATURE [Part::FeaturePython] Component031  label="Душ 100*081"  # Arch/BIM 52 (typed FeaturePython)
  Base = -> Box3215
  GlobalId = 2$9kHs27rDI8YZvC992Gc0
  HorizontalArea = 0
  IfcData = IfcUID=2$9kHs27rDI8YZvC992Gc0,+2 more (map truncated)
  IfcType = 52
  Material = -> Material013
  MoveBase = false
  MoveWithHost = false
  PerimeterLength = 0
  Placement = pos=(6950,3825,-10) rot=(0,0,1;0rad)
  VerticalArea = 0
FEATURE [App::MaterialObjectPython] Material014  label="Wood (laminate)"  # material (typed FeaturePython)
  Description = A standard construction wood
  Material = AuthorAndLicense=Wood-Generic,CardName=Wood-Generic,Color=(0.8196078431372549, 0.8196078431372549, 0.8196078431372549, 1.0),Density=700 kg/m^3,+10 more (map truncated)
  ProductURL = https://en.wikipedia.org/wiki/Wood
  Transparency = 0
FEATURE [App::MaterialObjectPython] Material015  label="Other mebel"  # material (typed FeaturePython)
  Description = Other mebel
  Material = AuthorAndLicense=Wood-Generic,CardName=Wood-Generic,Color=(0.6196078431372549, 0.6941176470588235, 0.7568627450980392, 1.0),Density=700 kg/m^3,+9 more (map truncated)
  Transparency = 0
FEATURE [Part::FeaturePython] Structure277  label="Structure020"  # Arch/BIM 52 (typed FeaturePython)
  Base = -> Rectangle546
  FaceMaker = 0
  GlobalId = 2DDa$j80P5hvQ3LPUQNes4
  Height = 200
  HorizontalArea = 404463
  IfcData = IfcUID=2DDa$j80P5hvQ3LPUQNes4,attributes={"GlobalId": {"value": "2DDa$j80P5hvQ3LPUQNes4"}},+1 more (map truncated)
  IfcType = 52
  Length = 0
  Material = -> Material015
  MoveBase = false
  MoveWithHost = false
  Nodes = (2) [(1656.58,7240.7,0),(1656.58,7240.7,200)]
  NodesOffset = 0
  Normal = (0,0,0)
  PerimeterLength = 3697.08
  Placement = pos=(0,0,400) rot=(0,0,1;0rad)
  VerticalArea = 739416
  Width = 100
FEATURE [Part::FeaturePython] Structure278  label="Structure021"  # Arch/BIM 52 (typed FeaturePython)
  Base = -> Rectangle547
  FaceMaker = 0
  GlobalId = 3Z9IWRZuT13weCYbg7_Khd
  Height = 200
  HorizontalArea = 236963
  IfcData = IfcUID=3Z9IWRZuT13weCYbg7_Khd,attributes={"GlobalId": {"value": "3Z9IWRZuT13weCYbg7_Khd"}},+1 more (map truncated)
  IfcType = 52
  Length = 0
  Material = -> Material015
  MoveBase = false
  MoveWithHost = false
  Nodes = (2) [(156.577,7240.7,0),(156.577,7240.7,200)]
  NodesOffset = 0
  Normal = (0,0,0)
  PerimeterLength = 2357.08
  Placement = pos=(0,0,400) rot=(0,0,1;0rad)
  VerticalArea = 471416
  Width = 100
FEATURE [Part::FeaturePython] Structure275  label="Structure018"  # Arch/BIM 52 (typed FeaturePython)
  Base = -> Rectangle544
  FaceMaker = 0
  GlobalId = 1sWNXrsjP3FQ$2jjEvDesy
  Height = 400
  HorizontalArea = 749463
  IfcData = IfcUID=1sWNXrsjP3FQ$2jjEvDesy,attributes={"GlobalId": {"value": "1sWNXrsjP3FQ$2jjEvDesy"}},+1 more (map truncated)
  IfcType = 52
  Length = 0
  Material = -> Material015
  MoveBase = false
  MoveWithHost = false
  Nodes = (2) [(182.895,-1383.89,0),(182.895,-1383.89,400)]
  NodesOffset = 0
  Normal = (0,0,0)
  PerimeterLength = 5557.08
  Placement = pos=(0,0,400) rot=(0,0,1;0rad)
  VerticalArea = 2.22283e+06
  Width = 100
FEATURE [Part::FeaturePython] Structure276  label="Structure019"  # Arch/BIM 52 (typed FeaturePython)
  Base = -> Rectangle545
  FaceMaker = 0
  GlobalId = 3fmvKSc5DEWOPxKz6nUpvm
  Height = 400
  HorizontalArea = 2.37446e+06
  IfcData = IfcUID=3fmvKSc5DEWOPxKz6nUpvm,attributes={"GlobalId": {"value": "3fmvKSc5DEWOPxKz6nUpvm"}},+1 more (map truncated)
  IfcType = 52
  Length = 0
  Material = -> Material015
  MoveBase = false
  MoveWithHost = false
  Nodes = (2) [(906.577,7240.7,0),(906.577,7240.7,400)]
  NodesOffset = 0
  Normal = (0,0,0)
  PerimeterLength = 6857.08
  VerticalArea = 2.74283e+06
  Width = 100
FEATURE [Part::FeaturePython] Structure279  label="Structure143"  # Arch/BIM 52 (typed FeaturePython)
  Base = -> Rectangle2837
  FaceMaker = 0
  GlobalId = 3TZavIZkH49B1D2AaSuAzL
  Height = 400
  HorizontalArea = 602463
  IfcData = IfcUID=3TZavIZkH49B1D2AaSuAzL,attributes={"GlobalId": {"value": "3TZavIZkH49B1D2AaSuAzL"}},+1 more (map truncated)
  IfcType = 52
  Length = 0
  Material = -> Material015
  MoveBase = false
  MoveWithHost = false
  Nodes = (2) [(906.577,7240.7,0),(906.577,7240.7,400)]
  NodesOffset = 0
  Normal = (0,0,0)
  PerimeterLength = 3097.08
  VerticalArea = 1.23883e+06
  Width = 100
FEATURE [App::GeometryPython] BuildingPart065  label="Диван 250x162L"  # Arch/BIM 52 (typed FeaturePython)
  Area = 0
  GlobalId = 1oZyr4jbn08vwhGg8DOzPQ
  Group = -> [Structure275,Structure278,Structure276,Structure277,Structure279]
  Height = 0
  HeightPropagate = true
  IfcData = IfcUID=1oZyr4jbn08vwhGg8DOzPQ,attributes={"GlobalId": {"value": "1oZyr4jbn08vwhGg8DOzPQ"}},+1 more (map truncated)
  IfcType = 52
  LevelOffset = 0
FEATURE [Part::FeaturePython] Structure339  label="Тумба под ТВ"  # Arch/BIM 52 (typed FeaturePython)
  Base = -> Wire784
  FaceMaker = 0
  GlobalId = 02q3nx$AH4fB0PqHacSjsk
  Height = 550
  HorizontalArea = 1.11339e+06
  IfcData = IfcUID=02q3nx$AH4fB0PqHacSjsk,+2 more (map truncated)
  IfcType = 52
  Length = 0
  Material = -> Material015
  MoveBase = false
  MoveWithHost = false
  Nodes = (2) [(8157.91,5216.2,0),(8157.91,5216.2,550)]
  NodesOffset = 0
  Normal = (0,0,1)
  PerimeterLength = 6499.55
  VerticalArea = 3.57475e+06
  Width = 100
FEATURE [Part::FeaturePython] Component032  label="стол обеденный001"  # Arch/BIM 52 (typed FeaturePython)
  Base = -> Fillet001
  GlobalId = 30KhDQuLT9PRlsli0ojqYH
  HorizontalArea = 0
  IfcData = IfcUID=30KhDQuLT9PRlsli0ojqYH,+2 more (map truncated)
  IfcType = 52
  Material = -> Material014
  MoveBase = false
  MoveWithHost = false
  PerimeterLength = 0
  Placement = pos=(10350,2890,0) rot=(0,0,1;0rad)
  VerticalArea = 0
FEATURE [Part::FeaturePython] Component033  label="стул013"  # Arch/BIM 52 (typed FeaturePython)
  Base = -> Fusion015
  GlobalId = 1jDmJlQDDCvfAqy4Wlc4hX
  HorizontalArea = 0
  IfcData = IfcUID=1jDmJlQDDCvfAqy4Wlc4hX,+2 more (map truncated)
  IfcType = 52
  Material = -> Material014
  MoveBase = false
  MoveWithHost = false
  PerimeterLength = 0
  Placement = pos=(10350,2890,0) rot=(0,0,1;0rad)
  VerticalArea = 0
FEATURE [Part::FeaturePython] Component034  label="стул012"  # Arch/BIM 52 (typed FeaturePython)
  Base = -> Fusion014
  GlobalId = 2fjpVYF01FEf1CPxL3Q2Wu
  HorizontalArea = 0
  IfcData = IfcUID=2fjpVYF01FEf1CPxL3Q2Wu,+2 more (map truncated)
  IfcType = 52
  Material = -> Material014
  MoveBase = false
  MoveWithHost = false
  PerimeterLength = 0
  Placement = pos=(10350,2890,0) rot=(0,0,1;0rad)
  VerticalArea = 0
FEATURE [Part::FeaturePython] Component035  label="стул011"  # Arch/BIM 52 (typed FeaturePython)
  Base = -> Fusion016
  GlobalId = 2rbIXYhRj4JgNPKMNl$8l7
  HorizontalArea = 0
  IfcData = IfcUID=2rbIXYhRj4JgNPKMNl$8l7,+2 more (map truncated)
  IfcType = 52
  Material = -> Material014
  MoveBase = false
  MoveWithHost = false
  PerimeterLength = 0
  Placement = pos=(10350,2890,0) rot=(0,0,1;0rad)
  VerticalArea = 0
FEATURE [Part::FeaturePython] Component036  label="стул010"  # Arch/BIM 52 (typed FeaturePython)
  Base = -> Fusion013
  GlobalId = 1ih4cOnfvDqPPYXDMeM0vw
  HorizontalArea = 0
  IfcData = IfcUID=1ih4cOnfvDqPPYXDMeM0vw,+2 more (map truncated)
  IfcType = 52
  Material = -> Material014
  MoveBase = false
  MoveWithHost = false
  PerimeterLength = 0
  Placement = pos=(10350,2890,0) rot=(0,0,1;0rad)
  VerticalArea = 0
FEATURE [Part::FeaturePython] Component037  label="Столик журнальный001"  # Arch/BIM 52 (typed FeaturePython)
  Base = -> Fillet003
  GlobalId = 2_br9eASD3lOnwEF_KCKKD
  HorizontalArea = 0
  IfcData = IfcUID=2_br9eASD3lOnwEF_KCKKD,+2 more (map truncated)
  IfcType = 52
  Material = -> Material014
  MoveBase = false
  MoveWithHost = false
  PerimeterLength = 0
  Placement = pos=(13600,-900,0) rot=(0,0,1;0rad)
  VerticalArea = 0
FEATURE [App::MaterialObjectPython] Material016  label="PVC"  # material (typed FeaturePython)
  Material = AuthorAndLicense=PVC-Generic,CardName=PVC-Generic,Color=(0.10980392156862745, 0.050980392156862744, 0.050980392156862744, 1.0),Density=1380 kg/m^3,+13 more (map truncated)
  ProductURL = https://en.wikipedia.org/wiki/Polyvinyl_chloride
  Transparency = 0
FEATURE [Part::FeaturePython] Component038  label="TV 001"  # Arch/BIM 52 (typed FeaturePython)
  Base = -> Box3145
  GlobalId = 2JRZAdYer2vvHxwrBL$6Tl
  HorizontalArea = 0
  IfcData = IfcUID=2JRZAdYer2vvHxwrBL$6Tl,+2 more (map truncated)
  IfcType = 52
  Material = -> Material016
  MoveBase = false
  MoveWithHost = false
  PerimeterLength = 0
  Placement = pos=(8090,6200,620) rot=(0,0,-1;1.5708rad)
  VerticalArea = 0
FEATURE [Part::FeaturePython] Component039  label="TV 002"  # Arch/BIM 52 (typed FeaturePython)
  Base = -> Box3159
  GlobalId = 1KbL9tWEn0_9owhEd3OMOe
  HorizontalArea = 0
  IfcData = IfcUID=1KbL9tWEn0_9owhEd3OMOe,+2 more (map truncated)
  IfcType = 52
  Material = -> Material016
  MoveBase = false
  MoveWithHost = false
  PerimeterLength = 0
  Placement = pos=(4720,6225,620) rot=(0,0,-1;1.5708rad)
  VerticalArea = 0
FEATURE [Part::FeaturePython] Component040  label="кровать 2 спальная 210х170 003"  # Arch/BIM 52 (typed FeaturePython)
  Base = -> Fusion019
  GlobalId = 178W44cHTAbgFocl2NGJXF
  HorizontalArea = 0
  IfcData = IfcUID=178W44cHTAbgFocl2NGJXF,+2 more (map truncated)
  IfcType = 52
  Material = -> Material015
  MoveBase = false
  MoveWithHost = false
  PerimeterLength = 0
  Placement = pos=(6970,7925,0) rot=(0,0,-1;1.5708rad)
  VerticalArea = 0
FEATURE [Part::FeaturePython] Component041  label="Диван кабинет001"  # Arch/BIM 52 (typed FeaturePython)
  Base = -> Fusion027
  GlobalId = 03vX7Qg392WAqcZgndFghb
  HorizontalArea = 0
  IfcData = IfcUID=03vX7Qg392WAqcZgndFghb,+2 more (map truncated)
  IfcType = 52
  Material = -> Material015
  MoveBase = false
  MoveWithHost = false
  PerimeterLength = 0
  Placement = pos=(3475,2970,0) rot=(0,0,1;3.14159rad)
  VerticalArea = 0
FEATURE [Part::FeaturePython] Component042  label="стол письменный001"  # Arch/BIM 52 (typed FeaturePython)
  Base = -> Fillet004
  GlobalId = 1qvzd8t693bQPX5BZwJPZ7
  HorizontalArea = 0
  IfcData = IfcUID=1qvzd8t693bQPX5BZwJPZ7,+2 more (map truncated)
  IfcType = 52
  Material = -> Material014
  MoveBase = false
  MoveWithHost = false
  PerimeterLength = 0
  Placement = pos=(1140,1890,0) rot=(0,0,1;1.5708rad)
  VerticalArea = 0
FEATURE [Part::FeaturePython] Component043  label="стул014"  # Arch/BIM 52 (typed FeaturePython)
  Base = -> Fusion045
  GlobalId = 1cZkVUkvD10h41bCcuxnEs
  HorizontalArea = 0
  IfcData = IfcUID=1cZkVUkvD10h41bCcuxnEs,+2 more (map truncated)
  IfcType = 52
  Material = -> Material014
  MoveBase = false
  MoveWithHost = false
  PerimeterLength = 0
  Placement = pos=(-462.225,3197.19,0) rot=(0,0,-1;1.5708rad)
  VerticalArea = 0
FEATURE [Part::FeaturePython] Component044  label="бутыль воды001"  # Arch/BIM 52 (typed FeaturePython)
  Base = -> Cylinder
  GlobalId = 0nuTQ1H4vFqAFkLsCfzz$Y
  HorizontalArea = 0
  IfcData = IfcUID=0nuTQ1H4vFqAFkLsCfzz$Y,+2 more (map truncated)
  IfcType = 52
  Material = -> Material006
  MoveBase = false
  MoveWithHost = false
  PerimeterLength = 0
  Placement = pos=(12395,4730,950) rot=(0,0,1;0rad)
  VerticalArea = 0
FEATURE [Part::FeaturePython] Component047  label="кулер001"  # Arch/BIM 52 (typed FeaturePython)
  Base = -> Box3191
  GlobalId = 1NUnbntaH5wfvllth3pArq
  HorizontalArea = 0
  IfcData = IfcUID=1NUnbntaH5wfvllth3pArq,+2 more (map truncated)
  IfcType = 52
  Material = -> Material015
  MoveBase = false
  MoveWithHost = false
  PerimeterLength = 0
  Placement = pos=(12240,4575,0) rot=(0,0,1;0rad)
  VerticalArea = 0
FEATURE [Part::FeaturePython] Component048  label="комод001"  # Arch/BIM 52 (typed FeaturePython)
  Base = -> Box3227
  GlobalId = 3x1u_ovjXEMwAlsSbA8GHf
  HorizontalArea = 0
  IfcData = IfcUID=3x1u_ovjXEMwAlsSbA8GHf,+2 more (map truncated)
  IfcType = 52
  Material = -> Material015
  MoveBase = false
  MoveWithHost = false
  PerimeterLength = 0
  Placement = pos=(12240,3825,0) rot=(0,0,1;0rad)
  VerticalArea = 0
FEATURE [App::GeometryPython] BuildingPart047  label="Мебель другая"  # Arch/BIM 52 (typed FeaturePython)
  Area = 0
  GlobalId = 1Dl8CuxJnEPxKEPVOok4FA
  Group = -> [BuildingPart065,Structure339,Component019,Component020,Component021,Component022,Component023,Component024,Component025,Component026,Component027,Component028,Component029,Component032,Component033,Component034,Component035,Component036,Component037,Component038,Component039,Component040,Component041,Component042,Component043,Component047,Component048,Component044]
  Height = 0
  HeightPropagate = true
  IfcData = IfcUID=1Dl8CuxJnEPxKEPVOok4FA,attributes={"GlobalId": {"value": "1Dl8CuxJnEPxKEPVOok4FA"}},+1 more (map truncated)
  IfcType = 52
  LevelOffset = 0
FEATURE [App::MaterialObjectPython] Material017  label="Steel (white)"  # material (typed FeaturePython)
  Material = AuthorAndLicense=Steel-Generic,CardName=Steel-Generic,Color=(0.6549019607843137, 0.8823529411764706, 0.9058823529411765, 1.0),Density=7900 kg/m^3,+12 more (map truncated)
  ProductURL = https://en.wikipedia.org/wiki/Steel
  Transparency = 0
FEATURE [Part::FeaturePython] Component045  label="морозильник 60 см001"  # Arch/BIM 52 (typed FeaturePython)
  Base = -> Box3183
  GlobalId = 1vDB6tGTv9rA3TFt87TZXl
  HorizontalArea = 0
  IfcData = IfcUID=1vDB6tGTv9rA3TFt87TZXl,+2 more (map truncated)
  IfcType = 52
  Material = -> Material017
  MoveBase = false
  MoveWithHost = false
  PerimeterLength = 0
  Placement = pos=(8250,-25,0) rot=(0,0,1;0rad)
  VerticalArea = 0
FEATURE [Part::FeaturePython] Component046  label="СМ001"  # Arch/BIM 52 (typed FeaturePython)
  Base = -> Box3184
  GlobalId = 3p89ErDe9E9Opxcq8_zvGg
  HorizontalArea = 0
  IfcData = IfcUID=3p89ErDe9E9Opxcq8_zvGg,+2 more (map truncated)
  IfcType = 52
  Material = -> Material017
  MoveBase = false
  MoveWithHost = false
  PerimeterLength = 0
  Placement = pos=(8850,-25,0) rot=(0,0,1;0rad)
  VerticalArea = 0
FEATURE [Part::FeaturePython] Component049  label="Кухонная мебель 001"  # Arch/BIM 52 (typed FeaturePython)
  Base = -> Fusion044
  GlobalId = 1ieDP$cJrBk8JUU$BNtJAd
  HorizontalArea = 0
  IfcData = IfcUID=1ieDP$cJrBk8JUU$BNtJAd,+2 more (map truncated)
  IfcType = 52
  Material = -> Material015
  MoveBase = false
  MoveWithHost = false
  PerimeterLength = 0
  Placement = pos=(0,-15,0) rot=(0,0,1;0rad)
  VerticalArea = 0
FEATURE [Part::FeaturePython] Component050  label="Кухонная мебель 040"  # Arch/BIM 52 (typed FeaturePython)
  Base = -> Box3175
  GlobalId = 1ED_GkK7LDUfuRWPN8I4HD
  HorizontalArea = 0
  IfcData = IfcUID=1ED_GkK7LDUfuRWPN8I4HD,+2 more (map truncated)
  IfcType = 52
  Material = -> Material015
  MoveBase = false
  MoveWithHost = false
  PerimeterLength = 0
  Placement = pos=(10150,-25,0) rot=(0,0,1;1.5708rad)
  VerticalArea = 0
FEATURE [Part::FeaturePython] Component051  label="Кухонная мебель 041"  # Arch/BIM 52 (typed FeaturePython)
  Base = -> Box3178
  GlobalId = 2Zjfoa06D7BB00eGawwvIP
  HorizontalArea = 0
  IfcData = IfcUID=2Zjfoa06D7BB00eGawwvIP,+2 more (map truncated)
  IfcType = 52
  Material = -> Material014
  MoveBase = false
  MoveWithHost = false
  PerimeterLength = 0
  Placement = pos=(10750,-25,1600) rot=(0,0,1;0rad)
  VerticalArea = 0
FEATURE [Part::FeaturePython] Component052  label="Кухонная мебель 042"  # Arch/BIM 52 (typed FeaturePython)
  Base = -> Box3179
  GlobalId = 2zXaDShtTEIwaqsWia$bJe
  HorizontalArea = 0
  IfcData = IfcUID=2zXaDShtTEIwaqsWia$bJe,+2 more (map truncated)
  IfcType = 52
  Material = -> Material015
  MoveBase = false
  MoveWithHost = false
  PerimeterLength = 0
  Placement = pos=(9550,-25,1600) rot=(0,0,1;0rad)
  VerticalArea = 0
FEATURE [Part::FeaturePython] Component053  label="Кухонная мебель 043"  # Arch/BIM 52 (typed FeaturePython)
  Base = -> Loft001
  GlobalId = 2NbjGyofnF4Q_5s1mmRZID
  HorizontalArea = 0
  IfcData = IfcUID=2NbjGyofnF4Q_5s1mmRZID,+2 more (map truncated)
  IfcType = 52
  Material = -> Material010
  MoveBase = false
  MoveWithHost = false
  PerimeterLength = 0
  Placement = pos=(0,-15,0) rot=(0,0,1;0rad)
  VerticalArea = 0
FEATURE [Part::FeaturePython] Component054  label="Кухонная мебель 044"  # Arch/BIM 52 (typed FeaturePython)
  Base = -> Box3192
  GlobalId = 37d12NPs5EAOYglb_81CGc
  HorizontalArea = 0
  IfcData = IfcUID=37d12NPs5EAOYglb_81CGc,+2 more (map truncated)
  IfcType = 52
  Material = -> Material011
  MoveBase = false
  MoveWithHost = false
  PerimeterLength = 0
  Placement = pos=(12494,3030.99,850) rot=(0,0,1;1.5708rad)
  VerticalArea = 0
FEATURE [Part::FeaturePython] Component055  label="Кухонная мебель 045"  # Arch/BIM 52 (typed FeaturePython)
  Base = -> Cylinder001
  GlobalId = 1nrzgZxzDATfvzL8VMDaoZ
  HorizontalArea = 0
  IfcData = IfcUID=1nrzgZxzDATfvzL8VMDaoZ,+2 more (map truncated)
  IfcType = 52
  Material = -> Material006
  MoveBase = false
  MoveWithHost = false
  PerimeterLength = 0
  Placement = pos=(12393.3,3344.1,850) rot=(0,0,1;1.5708rad)
  VerticalArea = 0
FEATURE [Part::FeaturePython] Component056  label="Кухонная мебель 046"  # Arch/BIM 52 (typed FeaturePython)
  Base = -> Box3195
  GlobalId = 0jonv5hkP7hB1P2BRJZFtA
  HorizontalArea = 0
  IfcData = IfcUID=0jonv5hkP7hB1P2BRJZFtA,+2 more (map truncated)
  IfcType = 52
  Material = -> Material015
  MoveBase = false
  MoveWithHost = false
  PerimeterLength = 0
  Placement = pos=(9550,-25,2300) rot=(0,0,1;0rad)
  VerticalArea = 0
FEATURE [Part::FeaturePython] Component057  label="Кухонная мебель 047"  # Arch/BIM 52 (typed FeaturePython)
  Base = -> Box3207
  GlobalId = 3unBum7Wr2XxUiA4dm2BNM
  HorizontalArea = 0
  IfcData = IfcUID=3unBum7Wr2XxUiA4dm2BNM,+2 more (map truncated)
  IfcType = 52
  Material = -> Material010
  MoveBase = false
  MoveWithHost = false
  PerimeterLength = 0
  Placement = pos=(12440,1330,100) rot=(0,0,1;1.5708rad)
  VerticalArea = 0
FEATURE [Part::FeaturePython] Component058  label="Кухонная мебель 048"  # Arch/BIM 52 (typed FeaturePython)
  Base = -> Cut043
  GlobalId = 0D9H_B8SfDFO$LhgA4khjg
  HorizontalArea = 0
  IfcData = IfcUID=0D9H_B8SfDFO$LhgA4khjg,+2 more (map truncated)
  IfcType = 52
  Material = -> Material015
  MoveBase = false
  MoveWithHost = false
  PerimeterLength = 0
  Placement = pos=(0,9.01e-13,0) rot=(0,0,1;0rad)
  VerticalArea = 0
FEATURE [Part::FeaturePython] Component059  label="Кухонная мебель 049"  # Arch/BIM 52 (typed FeaturePython)
  Base = -> Box3229
  GlobalId = 0wxRoUoAL2SRTsV_v4CUOt
  HorizontalArea = 0
  IfcData = IfcUID=0wxRoUoAL2SRTsV_v4CUOt,+2 more (map truncated)
  IfcType = 52
  Material = -> Material015
  MoveBase = false
  MoveWithHost = false
  PerimeterLength = 0
  Placement = pos=(10150,-25,1600) rot=(0,0,1;0rad)
  VerticalArea = 0
FEATURE [Part::FeaturePython] Component060  label="Кухонная мебель 050"  # Arch/BIM 52 (typed FeaturePython)
  Base = -> Cut045
  GlobalId = 2AztVf12z2KvLRx4YAzmc8
  HorizontalArea = 0
  IfcData = IfcUID=2AztVf12z2KvLRx4YAzmc8,+2 more (map truncated)
  IfcType = 52
  Material = -> Material015
  MoveBase = false
  MoveWithHost = false
  PerimeterLength = 0
  Placement = pos=(0,-15,0) rot=(0,0,1;0rad)
  VerticalArea = 0
FEATURE [Part::FeaturePython] Component061  label="Кухонная мебель 051"  # Arch/BIM 52 (typed FeaturePython)
  Base = -> Box3232
  GlobalId = 3Ik2mwhEnASuyGStdn9Hym
  HorizontalArea = 0
  IfcData = IfcUID=3Ik2mwhEnASuyGStdn9Hym,+2 more (map truncated)
  IfcType = 52
  Material = -> Material010
  MoveBase = false
  MoveWithHost = false
  PerimeterLength = 0
  Placement = pos=(10740,75,1000) rot=(0,0,1;1.5708rad)
  VerticalArea = 0
FEATURE [Part::FeaturePython] Component062  label="Кухонная мебель 052"  # Arch/BIM 52 (typed FeaturePython)
  Base = -> Box3233
  GlobalId = 0Wjbmkijf2hfmVL70WrgpJ
  HorizontalArea = 0
  IfcData = IfcUID=0Wjbmkijf2hfmVL70WrgpJ,+2 more (map truncated)
  IfcType = 52
  Material = -> Material010
  MoveBase = false
  MoveWithHost = false
  PerimeterLength = 0
  Placement = pos=(10740,75,450) rot=(0,0,1;1.5708rad)
  VerticalArea = 0
FEATURE [App::GeometryPython] BuildingPart045  label="Мебель кухонная"  # Arch/BIM 52 (typed FeaturePython)
  Area = 0
  GlobalId = 32uBXoaMr36Ak6fKsSPIPb
  Group = -> [Component046,Component045,Component049,Component050,Component051,Component052,Component053,Component054,Component055,Component056,Component057,Component058,Component059,Component060,Component061,Component062]
  Height = 0
  HeightPropagate = true
  IfcData = IfcUID=32uBXoaMr36Ak6fKsSPIPb,attributes={"GlobalId": {"value": "32uBXoaMr36Ak6fKsSPIPb"}},+1 more (map truncated)
  IfcType = 52
  LevelOffset = 0
FEATURE [Part::FeaturePython] Component075  label="Снегозадержание 001"  # Arch/BIM 52 (typed FeaturePython)
  Base = -> Pipe017
  GlobalId = 3fLgtWsyD8IOEn8l3TiBLL
  HorizontalArea = 0
  IfcData = IfcUID=3fLgtWsyD8IOEn8l3TiBLL,+2 more (map truncated)
  IfcType = 52
  Material = -> Material010
  MoveBase = false
  MoveWithHost = false
  PerimeterLength = 0
  Placement = pos=(0,0,50) rot=(0,0,1;0rad)
  VerticalArea = 0
FEATURE [Part::FeaturePython] Component076  label="Снегозадержание 022"  # Arch/BIM 52 (typed FeaturePython)
  Base = -> Pipe014
  GlobalId = 0fZFyhZkD7zPOVUYzK7U8n
  HorizontalArea = 0
  IfcData = IfcUID=0fZFyhZkD7zPOVUYzK7U8n,+2 more (map truncated)
  IfcType = 52
  Material = -> Material010
  MoveBase = false
  MoveWithHost = false
  PerimeterLength = 0
  Placement = pos=(0,0,50) rot=(0,0,1;0rad)
  VerticalArea = 0
FEATURE [Part::FeaturePython] Component077  label="Снегозадержание 023"  # Arch/BIM 52 (typed FeaturePython)
  Base = -> Pipe015
  GlobalId = 1LTO2PMRz6CfNW9W9wpak_
  HorizontalArea = 0
  IfcData = IfcUID=1LTO2PMRz6CfNW9W9wpak_,+2 more (map truncated)
  IfcType = 52
  Material = -> Material010
  MoveBase = false
  MoveWithHost = false
  PerimeterLength = 0
  Placement = pos=(0,0,50) rot=(0,0,1;0rad)
  VerticalArea = 0
FEATURE [Part::FeaturePython] Component078  label="Снегозадержание 024"  # Arch/BIM 52 (typed FeaturePython)
  Base = -> Pipe016
  GlobalId = 3fQfcs9tzCD9Q9FqWmmUZh
  HorizontalArea = 0
  IfcData = IfcUID=3fQfcs9tzCD9Q9FqWmmUZh,+2 more (map truncated)
  IfcType = 52
  Material = -> Material010
  MoveBase = false
  MoveWithHost = false
  PerimeterLength = 0
  Placement = pos=(0,0,50) rot=(0,0,1;0rad)
  VerticalArea = 0
FEATURE [Part::FeaturePython] Component079  label="Снегозадержание 025"  # Arch/BIM 52 (typed FeaturePython)
  Base = -> Pipe018
  GlobalId = 0JHLrOnyP7EehrYvml2qRo
  HorizontalArea = 0
  IfcData = IfcUID=0JHLrOnyP7EehrYvml2qRo,+2 more (map truncated)
  IfcType = 52
  Material = -> Material010
  MoveBase = false
  MoveWithHost = false
  PerimeterLength = 0
  Placement = pos=(0,0,50) rot=(0,0,1;0rad)
  VerticalArea = 0
FEATURE [Part::FeaturePython] Component080  label="Снегозадержание 026"  # Arch/BIM 52 (typed FeaturePython)
  Base = -> Pipe019
  GlobalId = 2smBLn7S1BvPhRI76FeC6b
  HorizontalArea = 0
  IfcData = IfcUID=2smBLn7S1BvPhRI76FeC6b,+2 more (map truncated)
  IfcType = 52
  Material = -> Material010
  MoveBase = false
  MoveWithHost = false
  PerimeterLength = 0
  Placement = pos=(0,0,50) rot=(0,0,1;0rad)
  VerticalArea = 0
FEATURE [Part::FeaturePython] Component081  label="Снегозадержание 027"  # Arch/BIM 52 (typed FeaturePython)
  Base = -> Pipe020
  GlobalId = 0$KWaMNPf21x_ja3hWF9hF
  HorizontalArea = 0
  IfcData = IfcUID=0$KWaMNPf21x_ja3hWF9hF,+2 more (map truncated)
  IfcType = 52
  Material = -> Material010
  MoveBase = false
  MoveWithHost = false
  PerimeterLength = 0
  Placement = pos=(0,0,50) rot=(0,0,1;0rad)
  VerticalArea = 0
FEATURE [Part::FeaturePython] Component082  label="Снегозадержание 028"  # Arch/BIM 52 (typed FeaturePython)
  Base = -> Pipe021
  GlobalId = 3Kb$CT3C16afQlV9OLZMZP
  HorizontalArea = 0
  IfcData = IfcUID=3Kb$CT3C16afQlV9OLZMZP,+2 more (map truncated)
  IfcType = 52
  Material = -> Material010
  MoveBase = false
  MoveWithHost = false
  PerimeterLength = 0
  Placement = pos=(0,0,50) rot=(0,0,1;0rad)
  VerticalArea = 0
FEATURE [App::GeometryPython] BuildingPart084  label="Снегозадержатели"  # Arch/BIM 52 (typed FeaturePython)
  Area = 0
  GlobalId = 10iOlZVPHFee_$fCiLahbp
  Group = -> [Component081,Component079,Component077,Component075,Component082,Component078,Component080,Component076]
  Height = 0
  HeightPropagate = true
  IfcData = IfcUID=10iOlZVPHFee_$fCiLahbp,+2 more (map truncated)
  IfcType = 52
  LevelOffset = 0
FEATURE [Part::Part2DObjectPython] Line1591  # Draft 2D object (typed FeaturePython)
  Area = 0
  ChamferSize = 0
  Closed = true
  End = (8945,2200.27,7500)
  FilletRadius = 0
  Length = 5600
  MakeFace = false
  Placement = pos=(8945,2200.27,6900) rot=(0,0,1;0rad)
  Points = (2) [(0,-6.91216e-10,-5000),(0,0,600)]
  Start = (8945,2200.27,1900)
  Subdivisions = 0
FEATURE [Part::FeaturePython] Pipe007002  label="Дымоход 201"  # Arch/BIM 98 (typed FeaturePython)
  Base = -> Line1591
  Diameter = 120
  GlobalId = 11JHR0lR55LRzzbgV05jpw
  HorizontalArea = 0
  IfcData = IfcUID=11JHR0lR55LRzzbgV05jpw,+2 more (map truncated)
  IfcType = 98
  Length = 5600
  Material = -> Material010
  MoveBase = false
  MoveWithHost = false
  OffsetEnd = 0
  OffsetStart = 0
  PerimeterLength = 0
  PredefinedType = 0
  VerticalArea = 0
  WallThickness = 0
FEATURE [Part::FeaturePython] Component084  label="Дымоход 120 002"  # Arch/BIM 52 (typed FeaturePython)
  Base = -> Pipe007002
  GlobalId = 1BRcTpsETD4PFK9C3ntAng
  HorizontalArea = 0
  IfcData = IfcUID=1BRcTpsETD4PFK9C3ntAng,+2 more (map truncated)
  IfcType = 52
  Material = -> Material010
  MoveBase = false
  MoveWithHost = false
  PerimeterLength = 0
  VerticalArea = 0
FEATURE [Part::Part2DObjectPython] Line1592  # Draft 2D object (typed FeaturePython)
  Area = 0
  ChamferSize = 0
  Closed = true
  End = (8945,1979.8,6981)
  FilletRadius = 0
  Length = 5000
  MakeFace = false
  Placement = pos=(8945,1979.8,6981) rot=(0,0,1;0rad)
  Points = (2) [(0,2.50111e-12,-5000),(0,2.50111e-12,0)]
  Start = (8945,1979.8,1981)
  Subdivisions = 0
FEATURE [Part::FeaturePython] Pipe007003  label="Дымоход 202"  # Arch/BIM 98 (typed FeaturePython)
  Base = -> Line1592
  Diameter = 300
  GlobalId = 11JHR0lR55LRzzbgV05jpw
  HorizontalArea = 0
  IfcData = IfcUID=11JHR0lR55LRzzbgV05jpw,+2 more (map truncated)
  IfcType = 98
  Length = 5000
  Material = -> Material010
  MoveBase = false
  MoveWithHost = false
  OffsetEnd = 0
  OffsetStart = 0
  PerimeterLength = 0
  PredefinedType = 0
  VerticalArea = 0
  WallThickness = 0
FEATURE [Part::FeaturePython] Component085  label="Дымоход 300 002"  # Arch/BIM 52 (typed FeaturePython)
  Base = -> Pipe007003
  GlobalId = 1RYiQBgpbBTAR3hS4pyNB_
  HorizontalArea = 0
  IfcData = IfcUID=1RYiQBgpbBTAR3hS4pyNB_,+2 more (map truncated)
  IfcType = 52
  Material = -> Material010
  MoveBase = false
  MoveWithHost = false
  PerimeterLength = 0
  VerticalArea = 0
FEATURE [App::GeometryPython] BuildingPart087  label="Инженерные системы"  # Arch/BIM 52 (typed FeaturePython)
  Area = 0
  GlobalId = 0dgo77$PP7IAddqr4C3YZS
  Group = -> [Component004,Component011,Component009,Component008,Component005,Component010,Component007,Component013,Component014,Component015,Component016,Component017,Component018,Component084,Component085]
  Height = 0
  HeightPropagate = true
  IfcData = IfcUID=0dgo77$PP7IAddqr4C3YZS,+2 more (map truncated)
  IfcType = 52
  LevelOffset = 0
FEATURE [Part::FeaturePython] Component086  label="Вычет стены 001"  # Arch/BIM 0 (typed FeaturePython)
  Base = -> Wall004
  HorizontalArea = 0
  IfcData = attributes={"GlobalId": {"name": "GlobalId", "type": "IfcGloballyUniqueId", "is_enum": false, "enum_values": []}, "Description": {"... (+538 chars omitted),+1 more (map truncated)
  IfcType = 0
  MoveBase = false
  MoveWithHost = false
  PerimeterLength = 0
  Placement = pos=(0,0,-200) rot=(0,0,1;0rad)
  PredefinedType = 0
  VerticalArea = 0
FEATURE [Part::FeaturePython] Structure  label="Утепление пола XPS 100mm"  # Arch/BIM 118 (typed FeaturePython)
  Additions = -> [Structure066,Structure069]
  Base = -> Rectangle016
  FaceMaker = 0
  GlobalId = 12HaZCeTXDOvnd1ysX9j$x
  Height = 100
  HorizontalArea = 0
  IfcData = IfcUID=12HaZCeTXDOvnd1ysX9j$x,+2 more (map truncated)
  IfcType = 118
  Length = 7520
  Material = -> Material002
  MoveBase = false
  MoveWithHost = false
  Nodes = (4) [(-50,-45,0),(12570,-45,0),(12570,7505,0),(-50,7505,0)]
  NodesOffset = 0
  Normal = (0,0,0)
  PerimeterLength = 0
  Placement = pos=(0,0,-200) rot=(0,0,1;0rad)
  PredefinedType = 0
  Subtractions = -> [Component086]
  VerticalArea = 0
  Width = 12620
FEATURE [App::GeometryPython] BuildingPart020  label="Утепление пола по грунту"  # Arch/BIM 52 (typed FeaturePython)
  Area = 0
  GlobalId = 3yH_rZ_TXC4Rf1NqFztroU
  Group = -> [Structure]
  Height = 0
  HeightPropagate = true
  IfcData = IfcUID=3yH_rZ_TXC4Rf1NqFztroU,attributes={"GlobalId": {"value": "3yH_rZ_TXC4Rf1NqFztroU"}},+1 more (map truncated)
  IfcType = 52
  LevelOffset = 0
FEATURE [App::MaterialObjectPython] Material018  label="Concrete (not transparent)"  # material (typed FeaturePython)
  Description = A standard C-25 construction concrete
  Material = AuthorAndLicense=Concrete-Generic,CardName=Concrete-Generic,Color=(0.47058823529411764, 0.4627450980392157, 0.4627450980392157, 1.0),+13 more (map truncated)
  ProductURL = https://en.wikipedia.org/wiki/Concrete
  StandardCode = Masterformat 03 33 13
  Transparency = 0
FEATURE [Part::FeaturePython] Structure399  label="Забежные низ 001"  # Arch/BIM 52 (typed FeaturePython)
  Base = -> Wire857
  FaceMaker = 0
  GlobalId = 3xRowyKFv2DhSfk5E$qgY5
  Height = 1064
  HorizontalArea = 231189
  IfcData = IfcUID=3xRowyKFv2DhSfk5E$qgY5,+2 more (map truncated)
  IfcType = 52
  Length = 0
  Material = -> Material018
  MoveBase = false
  MoveWithHost = false
  Nodes = (2) [(7357.33,6427.5,0),(7357.33,6427.5,1064)]
  NodesOffset = 0
  Normal = (0,0,1)
  PerimeterLength = 2353.16
  VerticalArea = 2.50376e+06
  Width = 100
FEATURE [Part::FeaturePython] Structure400  label="Забежные низ 013"  # Arch/BIM 52 (typed FeaturePython)
  Base = -> Wire858
  FaceMaker = 0
  GlobalId = 3$gmb_2qX9N8uPM2$7_dmQ
  Height = 880
  HorizontalArea = 253761
  IfcData = IfcUID=3$gmb_2qX9N8uPM2$7_dmQ,+2 more (map truncated)
  IfcType = 52
  Length = 0
  Material = -> Material018
  MoveBase = false
  MoveWithHost = false
  Nodes = (2) [(7272.39,6739.05,0),(7272.39,6739.05,880)]
  NodesOffset = 0
  Normal = (0,0,1)
  PerimeterLength = 2580.03
  VerticalArea = 2.27043e+06
  Width = 100
FEATURE [Part::FeaturePython] Structure401  label="Забежные низ 014"  # Arch/BIM 52 (typed FeaturePython)
  Base = -> Wire859
  FaceMaker = 0
  GlobalId = 01ecilRVH53xz1ioP6bHrT
  Height = 696
  HorizontalArea = 353236
  IfcData = IfcUID=01ecilRVH53xz1ioP6bHrT,+2 more (map truncated)
  IfcType = 52
  Length = 0
  Material = -> Material018
  MoveBase = false
  MoveWithHost = false
  Nodes = (2) [(7327.45,7090.2,0),(7327.45,7090.2,696)]
  NodesOffset = 0
  Normal = (0,0,1)
  PerimeterLength = 2946.66
  VerticalArea = 2.05087e+06
  Width = 100
FEATURE [Part::FeaturePython] Structure402  label="Забежные низ 015"  # Arch/BIM 52 (typed FeaturePython)
  Base = -> Wire860
  FaceMaker = 0
  GlobalId = 2Qxt6SlRz2T8lyMYD6o2tP
  Height = 512
  HorizontalArea = 250464
  IfcData = IfcUID=2Qxt6SlRz2T8lyMYD6o2tP,+2 more (map truncated)
  IfcType = 52
  Length = 0
  Material = -> Material018
  MoveBase = false
  MoveWithHost = false
  Nodes = (2) [(7668.63,7155.73,0),(7668.63,7155.73,512)]
  NodesOffset = 0
  Normal = (0,0,1)
  PerimeterLength = 2554.3
  VerticalArea = 1.3078e+06
  Width = 100
FEATURE [Part::FeaturePython] Structure403  label="Забежные низ 016"  # Arch/BIM 52 (typed FeaturePython)
  Base = -> Wire861
  FaceMaker = 0
  GlobalId = 22WKr65a12qwGJ$_8YzaFf
  Height = 328
  HorizontalArea = 225207
  IfcData = IfcUID=22WKr65a12qwGJ$_8YzaFf,+2 more (map truncated)
  IfcType = 52
  Length = 0
  Material = -> Material018
  MoveBase = false
  MoveWithHost = false
  Nodes = (2) [(7978.17,7076.01,0),(7978.17,7076.01,328)]
  NodesOffset = 0
  Normal = (0,0,1)
  PerimeterLength = 2310.8
  VerticalArea = 757942
  Width = 100
FEATURE [Part::FeaturePython] Structure404  label="Забежные низ 017"  # Arch/BIM 52 (typed FeaturePython)
  Base = -> Rectangle3338
  FaceMaker = 0
  GlobalId = 1VsCdZ7iTEn9tPuMJaDspx
  Height = 144
  HorizontalArea = 225000
  IfcData = IfcUID=1VsCdZ7iTEn9tPuMJaDspx,+2 more (map truncated)
  IfcType = 52
  Length = 0
  Material = -> Material018
  MoveBase = false
  MoveWithHost = false
  Nodes = (2) [(8231.4,7035,0),(8231.4,7035,144)]
  NodesOffset = 0
  Normal = (0,0,0)
  PerimeterLength = 2300
  VerticalArea = 331200
  Width = 100
FEATURE [Part::FeaturePython] Structure405  label="Структура015"  # Arch/BIM 52 (typed FeaturePython)
  Base = -> Wire862
  FaceMaker = 0
  GlobalId = 17tEtNUWvARhORHH3OyyHE
  Height = 40
  HorizontalArea = 249797
  IfcData = IfcUID=17tEtNUWvARhORHH3OyyHE,+2 more (map truncated)
  IfcType = 52
  Length = 0
  Material = -> Material018
  MoveBase = false
  MoveWithHost = false
  Nodes = (2) [(7360.51,6437.37,0),(7360.51,6437.37,-40)]
  NodesOffset = 0
  Normal = (0,0,0)
  PerimeterLength = 2393.6
  Placement = pos=(0,0,1104) rot=(0,0,1;0rad)
  VerticalArea = 95744
  Width = 100
FEATURE [Part::FeaturePython] Structure406  label="Структура016"  # Arch/BIM 52 (typed FeaturePython)
  Base = -> Wire863
  FaceMaker = 0
  GlobalId = 0bs21bqPT2gQetmdzIKKcU
  Height = 40
  HorizontalArea = 275711
  IfcData = IfcUID=0bs21bqPT2gQetmdzIKKcU,+2 more (map truncated)
  IfcType = 52
  Length = 0
  Material = -> Material018
  MoveBase = false
  MoveWithHost = false
  Nodes = (2) [(7275.7,6726.62,0),(7275.7,6726.62,-40)]
  NodesOffset = 0
  Normal = (0,0,0)
  PerimeterLength = 2627.74
  Placement = pos=(0,0,920) rot=(0,0,1;0rad)
  VerticalArea = 105109
  Width = 100
FEATURE [Part::FeaturePython] Structure407  label="Структура017"  # Arch/BIM 52 (typed FeaturePython)
  Base = -> Wire864
  FaceMaker = 0
  GlobalId = 2j64CQRQHAcRK4sU5nK_W7
  Height = 40
  HorizontalArea = 374881
  IfcData = IfcUID=2j64CQRQHAcRK4sU5nK_W7,+2 more (map truncated)
  IfcType = 52
  Length = 0
  Material = -> Material018
  MoveBase = false
  MoveWithHost = false
  Nodes = (2) [(7342.75,7086.8,0),(7342.75,7086.8,-40)]
  NodesOffset = 0
  Normal = (0,0,0)
  PerimeterLength = 2973.7
  Placement = pos=(0,0,736) rot=(0,0,1;0rad)
  VerticalArea = 118948
  Width = 100
FEATURE [Part::FeaturePython] Structure408  label="Структура018"  # Arch/BIM 52 (typed FeaturePython)
  Base = -> Wire865
  FaceMaker = 0
  GlobalId = 1QIDzeYIT3m8mUX9Kkwym4
  Height = 40
  HorizontalArea = 268670
  IfcData = IfcUID=1QIDzeYIT3m8mUX9Kkwym4,+2 more (map truncated)
  IfcType = 52
  Length = 0
  Material = -> Material018
  MoveBase = false
  MoveWithHost = false
  Nodes = (2) [(7682.02,7147.55,0),(7682.02,7147.55,-40)]
  NodesOffset = 0
  Normal = (0,0,0)
  PerimeterLength = 2594.76
  Placement = pos=(0,0,552) rot=(0,0,1;0rad)
  VerticalArea = 103790
  Width = 100
FEATURE [Part::FeaturePython] Structure409  label="Структура019"  # Arch/BIM 52 (typed FeaturePython)
  Base = -> Wire866
  FaceMaker = 0
  GlobalId = 25WTBURZvCHuciqcaKOkV_
  Height = 40
  HorizontalArea = 243207
  IfcData = IfcUID=25WTBURZvCHuciqcaKOkV_,+2 more (map truncated)
  IfcType = 52
  Length = 0
  Material = -> Material018
  MoveBase = false
  MoveWithHost = false
  Nodes = (2) [(7988.39,7072.97,0),(7988.39,7072.97,-40)]
  NodesOffset = 0
  Normal = (0,0,0)
  PerimeterLength = 2350.8
  Placement = pos=(0,0,369) rot=(0,0,1;0rad)
  VerticalArea = 94032
  Width = 100
FEATURE [Part::FeaturePython] Structure410  label="Структура020"  # Arch/BIM 52 (typed FeaturePython)
  Base = -> Rectangle3340
  FaceMaker = 0
  GlobalId = 3fuuXTC0L9FOhhGPsIqq2n
  Height = 40
  HorizontalArea = 243000
  IfcData = IfcUID=3fuuXTC0L9FOhhGPsIqq2n,+2 more (map truncated)
  IfcType = 52
  Length = 0
  Material = -> Material018
  MoveBase = false
  MoveWithHost = false
  Nodes = (2) [(8241.39,7035,0),(8241.39,7035,-40)]
  NodesOffset = 0
  Normal = (0,0,-1)
  PerimeterLength = 2340
  Placement = pos=(0,0,184) rot=(0,0,1;0rad)
  VerticalArea = 93600
  Width = 100
FEATURE [App::GeometryPython] BuildingPart095  label="Забежные верх"  # Arch/BIM 52 (typed FeaturePython)
  Area = 0
  GlobalId = 1ZYgrdkID2NPN3ZGn3KHqO
  Group = -> [Structure405,Structure406,Structure407,Structure408,Structure409,Structure410]
  Height = 0
  HeightPropagate = true
  IfcData = IfcUID=1ZYgrdkID2NPN3ZGn3KHqO,+2 more (map truncated)
  IfcType = 52
  LevelOffset = 0
FEATURE [Part::FeaturePython] Structure411  label="Забежные низ 018"  # Arch/BIM 52 (typed FeaturePython)
  Base = -> Rectangle3341
  FaceMaker = 0
  GlobalId = 23ZLurxYD1YfxSwC6KIQzz
  Height = 1104
  HorizontalArea = 174521
  IfcData = IfcUID=23ZLurxYD1YfxSwC6KIQzz,+2 more (map truncated)
  IfcType = 52
  Length = 0
  Material = -> Material018
  MoveBase = false
  MoveWithHost = false
  Nodes = (2) [(8211.39,7020,0),(8211.39,7020,143.5)]
  NodesOffset = 0
  Normal = (0,0,0)
  PerimeterLength = 2219.39
  VerticalArea = 2.45021e+06
  Width = 100
FEATURE [App::GeometryPython] BuildingPart094  label="Забежные низ"  # Arch/BIM 52 (typed FeaturePython)
  Area = 0
  GlobalId = 1IKz8gq_D40uVuKk2CcJxb
  Group = -> [Structure399,Structure400,Structure401,Structure402,Structure403,Structure404,Structure411]
  Height = 0
  HeightPropagate = true
  IfcData = IfcUID=1IKz8gq_D40uVuKk2CcJxb,+2 more (map truncated)
  IfcType = 52
  LevelOffset = 0
FEATURE [App::GeometryPython] BuildingPart093  label="Лестница 184/250 17 подъёмов обновл."  # Arch/BIM 52 (typed FeaturePython)
  Area = 0
  GlobalId = 1mPKq_o39C3gXvH55GxGJR
  Group = -> [Stairs003,BuildingPart094,BuildingPart095]
  Height = 0
  HeightPropagate = true
  IfcData = IfcUID=1mPKq_o39C3gXvH55GxGJR,+2 more (map truncated)
  IfcType = 52
  LevelOffset = 0
FEATURE [Part::FeaturePython] Component063  label="ПНО-39-001"  # Arch/BIM 52 (typed FeaturePython)
  Base = -> Array060
  GlobalId = 3XdGCKpWL71eu_U9riFilZ
  HorizontalArea = 0
  IfcData = IfcUID=3XdGCKpWL71eu_U9riFilZ,+2 more (map truncated)
  IfcType = 52
  Material = -> Material018
  MoveBase = false
  MoveWithHost = false
  PerimeterLength = 0
  Placement = pos=(960,0,0) rot=(0,0,1;0rad)
  VerticalArea = 0
FEATURE [Part::FeaturePython] Component064  label="ПНО-39-022"  # Arch/BIM 52 (typed FeaturePython)
  Base = -> Array059
  GlobalId = 0bmcIJyB97$9xeF$u53D6V
  HorizontalArea = 0
  IfcData = IfcUID=0bmcIJyB97$9xeF$u53D6V,+2 more (map truncated)
  IfcType = 52
  Material = -> Material018
  MoveBase = false
  MoveWithHost = false
  PerimeterLength = 0
  Placement = pos=(10150,1.364e-12,0) rot=(0,0,1;0rad)
  VerticalArea = 0
FEATURE [Part::FeaturePython] Component065  label="ПНО-39-023"  # Arch/BIM 52 (typed FeaturePython)
  Base = -> Array058
  GlobalId = 3J7wnUa6v2rfQwTZ0ixKlx
  HorizontalArea = 0
  IfcData = IfcUID=3J7wnUa6v2rfQwTZ0ixKlx,+2 more (map truncated)
  IfcType = 52
  Material = -> Material018
  MoveBase = false
  MoveWithHost = false
  PerimeterLength = 0
  Placement = pos=(-50,0,0) rot=(0,0,1;0rad)
  VerticalArea = 0
FEATURE [Part::FeaturePython] Component066  label="ПНО-39-024"  # Arch/BIM 52 (typed FeaturePython)
  Base = -> Array061
  GlobalId = 04BNWqgZL2Ov5OlXQ9URhu
  HorizontalArea = 0
  IfcData = IfcUID=04BNWqgZL2Ov5OlXQ9URhu,+2 more (map truncated)
  IfcType = 52
  Material = -> Material018
  MoveBase = false
  MoveWithHost = false
  PerimeterLength = 0
  Placement = pos=(6710,4.54e-13,0) rot=(0,0,1;0rad)
  VerticalArea = 0
FEATURE [Part::FeaturePython] Component067  label="ПНО-39-025"  # Arch/BIM 52 (typed FeaturePython)
  Base = -> Cut040
  GlobalId = 3oxNR3o2f3ThkHi0MWyoUk
  HorizontalArea = 0
  IfcData = IfcUID=3oxNR3o2f3ThkHi0MWyoUk,+2 more (map truncated)
  IfcType = 52
  Material = -> Material018
  MoveBase = false
  MoveWithHost = false
  PerimeterLength = 0
  VerticalArea = 0
FEATURE [Part::FeaturePython] Component068  label="ПНО-39-026"  # Arch/BIM 52 (typed FeaturePython)
  Base = -> Cut041
  GlobalId = 248Twkwhj2Cw3m_5Ovog43
  HorizontalArea = 0
  IfcData = IfcUID=248Twkwhj2Cw3m_5Ovog43,+2 more (map truncated)
  IfcType = 52
  Material = -> Material018
  MoveBase = false
  MoveWithHost = false
  PerimeterLength = 0
  VerticalArea = 0
FEATURE [Part::FeaturePython] Component069  label="ПНО-39-027"  # Arch/BIM 52 (typed FeaturePython)
  Base = -> Cut048
  GlobalId = 1Khcr$NwzCrA2G11iVvVb8
  HorizontalArea = 0
  IfcData = IfcUID=1Khcr$NwzCrA2G11iVvVb8,+2 more (map truncated)
  IfcType = 52
  Material = -> Material018
  MoveBase = false
  MoveWithHost = false
  PerimeterLength = 0
  VerticalArea = 0
FEATURE [Part::FeaturePython] Component070  label="ПНО-39-028"  # Arch/BIM 52 (typed FeaturePython)
  Base = -> Cut049
  GlobalId = 0yPrT9kDj0g9Se6444B6w3
  HorizontalArea = 0
  IfcData = IfcUID=0yPrT9kDj0g9Se6444B6w3,+2 more (map truncated)
  IfcType = 52
  Material = -> Material018
  MoveBase = false
  MoveWithHost = false
  PerimeterLength = 0
  VerticalArea = 0
FEATURE [App::GeometryPython] BuildingPart080  label="Перекрытие 2-4"  # Arch/BIM 52 (typed FeaturePython)
  Area = 0
  GlobalId = 0anh3cmIz34vhOpNdTvs5l
  Group = -> [Component063,Component064,Component065,Component066,Component067,Component068,Component069,Component070]
  Height = 0
  HeightPropagate = true
  IfcData = IfcUID=0anh3cmIz34vhOpNdTvs5l,+2 more (map truncated)
  IfcType = 52
  LevelOffset = 0
FEATURE [Part::FeaturePython] Component071  label="ПНО-40-001"  # Arch/BIM 52 (typed FeaturePython)
  Base = -> Array054
  GlobalId = 0wpf9Q8IzA_f4m02htJFBb
  HorizontalArea = 0
  IfcData = IfcUID=0wpf9Q8IzA_f4m02htJFBb,+2 more (map truncated)
  IfcType = 52
  Material = -> Material018
  MoveBase = false
  MoveWithHost = false
  PerimeterLength = 0
  Placement = pos=(-50,-9.09e-13,0) rot=(0,0,1;0rad)
  VerticalArea = 0
FEATURE [Part::FeaturePython] Component072  label="ПНО-40-010"  # Arch/BIM 52 (typed FeaturePython)
  Base = -> Array038
  GlobalId = 0oBCy39Wb7fhN7XKOpfxSu
  HorizontalArea = 0
  IfcData = IfcUID=0oBCy39Wb7fhN7XKOpfxSu,+2 more (map truncated)
  IfcType = 52
  Material = -> Material018
  MoveBase = false
  MoveWithHost = false
  PerimeterLength = 0
  Placement = pos=(7920,9.09e-13,0) rot=(0,0,1;0rad)
  VerticalArea = 0
FEATURE [Part::FeaturePython] Component073  label="ПНО-40-011"  # Arch/BIM 52 (typed FeaturePython)
  Base = -> Array056
  GlobalId = 28AQdtbYrBIx61Ll5jYMHO
  HorizontalArea = 0
  IfcData = IfcUID=28AQdtbYrBIx61Ll5jYMHO,+2 more (map truncated)
  IfcType = 52
  Material = -> Material018
  MoveBase = false
  MoveWithHost = false
  PerimeterLength = 0
  Placement = pos=(11560,9.09e-13,0) rot=(0,0,1;0rad)
  VerticalArea = 0
FEATURE [Part::FeaturePython] Component074  label="ПНО-40-012"  # Arch/BIM 52 (typed FeaturePython)
  Base = -> Array057
  GlobalId = 0ZSNQygeL5b9x0j4AY$sC6
  HorizontalArea = 0
  IfcData = IfcUID=0ZSNQygeL5b9x0j4AY$sC6,+2 more (map truncated)
  IfcType = 52
  Material = -> Material018
  MoveBase = false
  MoveWithHost = false
  PerimeterLength = 0
  Placement = pos=(4480,9.09e-13,0) rot=(0,0,1;0rad)
  VerticalArea = 0
FEATURE [App::GeometryPython] BuildingPart074  label="Перекрытие 1-2"  # Arch/BIM 52 (typed FeaturePython)
  Area = 0
  GlobalId = 2Lvd2Pu4D2h9CzOOmQVni3
  Group = -> [Component074,Component073,Component071,Component072]
  Height = 0
  HeightPropagate = true
  IfcData = IfcUID=2Lvd2Pu4D2h9CzOOmQVni3,+2 more (map truncated)
  IfcType = 52
  LevelOffset = 0
FEATURE [App::GeometryPython] BuildingPart006  label="Перекрытие плитами ПНО"  # Arch/BIM 52 (typed FeaturePython)
  Area = 0
  GlobalId = 29arHl4sD0PxQq1DVpDEyo
  Group = -> [BuildingPart074,BuildingPart080]
  Height = 0
  HeightPropagate = true
  IfcData = IfcUID=29arHl4sD0PxQq1DVpDEyo,attributes={"GlobalId": {"value": "29arHl4sD0PxQq1DVpDEyo"}},+1 more (map truncated)
  IfcType = 52
  LevelOffset = 0
FEATURE [Part::FeaturePython] Structure434  label="Стяжка тёплого пола 80mm"  # Arch/BIM 118 (typed FeaturePython)
  Additions = -> [Structure368,Structure371]
  Base = -> Rectangle016
  FaceMaker = 0
  GlobalId = 3i06NLwF5739lSL_IHGmf1
  Height = 80
  HorizontalArea = 0
  IfcData = IfcUID=3i06NLwF5739lSL_IHGmf1,+2 more (map truncated)
  IfcType = 118
  Length = 7520
  Material = -> Material018
  MoveBase = false
  MoveWithHost = false
  Nodes = (4) [(-50,-45,0),(12570,-45,0),(12570,7505,0),(-50,7505,0)]
  NodesOffset = 0
  Normal = (0,0,0)
  PerimeterLength = 0
  Placement = pos=(0,0,-100) rot=(0,0,1;0rad)
  PredefinedType = 0
  Subtractions = -> [Component086]
  VerticalArea = 0
  Width = 12620
FEATURE [App::GeometryPython] BuildingPart085  label="Стяжка тёплого пола 80мм"  # Arch/BIM 52 (typed FeaturePython)
  Area = 0
  GlobalId = 0paGEjjH988O$uNBI5I7u1
  Group = -> [Structure434]
  Height = 0
  HeightPropagate = true
  IfcData = IfcUID=0paGEjjH988O$uNBI5I7u1,+2 more (map truncated)
  IfcType = 52
  LevelOffset = 0
FEATURE [Part::FeaturePython] Structure435  label="Покрытие пола 20мм001"  # Arch/BIM 118 (typed FeaturePython)
  Additions = -> [Structure374,Structure377]
  Base = -> Rectangle016
  FaceMaker = 0
  GlobalId = 069jleHXv70OyIjGnnOFdt
  Height = 20
  HorizontalArea = 0
  IfcData = IfcUID=069jleHXv70OyIjGnnOFdt,+2 more (map truncated)
  IfcType = 118
  Length = 7520
  Material = -> Material018
  MoveBase = false
  MoveWithHost = false
  Nodes = (4) [(-50,-45,0),(12570,-45,0),(12570,7505,0),(-50,7505,0)]
  NodesOffset = 0
  Normal = (0,0,0)
  PerimeterLength = 0
  Placement = pos=(0,0,-20) rot=(0,0,1;0rad)
  PredefinedType = 0
  Subtractions = -> [Component086]
  VerticalArea = 0
  Width = 12620
FEATURE [App::GeometryPython] BuildingPart086  label="Покрытие пола 20мм"  # Arch/BIM 52 (typed FeaturePython)
  Area = 0
  GlobalId = 1v2dx_MFP8whu6FdM2ihDU
  Group = -> [Structure435]
  Height = 0
  HeightPropagate = true
  IfcData = IfcUID=1v2dx_MFP8whu6FdM2ihDU,+2 more (map truncated)
  IfcType = 52
  LevelOffset = 0
FEATURE [App::GeometryPython] BuildingPart014  label="Полы по грунту"  # Arch/BIM 52 (typed FeaturePython)
  Area = 0
  GlobalId = 1N3QY958b6OO8VUwpY7Wbc
  Group = -> [BuildingPart020,BuildingPart085,BuildingPart086]
  Height = 0
  HeightPropagate = true
  IfcData = IfcUID=1N3QY958b6OO8VUwpY7Wbc,attributes={"GlobalId": {"value": "1N3QY958b6OO8VUwpY7Wbc"}},+1 more (map truncated)
  IfcType = 52
  LevelOffset = 0
FEATURE [App::FeaturePython] Dimension032  # Draft dimension (typed FeaturePython)
  Diameter = false
  Dimline = (3700,2600,0)
  Direction = (0,0,0)
  Distance = 900
  End = (3500,3435,0)
  Normal = (0,0,1)
  Start = (3500,2535,0)
FEATURE [App::FeaturePython] Dimension034  # Draft dimension (typed FeaturePython)
  Diameter = false
  Dimline = (4770,3300,0)
  Direction = (0,0,0)
  Distance = 920
  End = (4770,3825,0)
  Normal = (0,0,1)
  Start = (3850,3825,0)
FEATURE [App::FeaturePython] Dimension035  # Draft dimension (typed FeaturePython)
  Diameter = false
  Dimline = (5800,3300,0)
  Direction = (0,0,0)
  Distance = 920
  End = (6720,3825,0)
  Normal = (0,0,1)
  Start = (5800,3825,0)
FEATURE [App::FeaturePython] Dimension036  # Draft dimension (typed FeaturePython)
  Diameter = false
  Dimline = (5800,2600,0)
  Direction = (0,0,0)
  Distance = 900
  End = (6710,2385,0)
  Normal = (0,0,1)
  Start = (5810,2385,0)
FEATURE [App::FeaturePython] Dimension037  # Draft dimension (typed FeaturePython)
  Diameter = false
  Dimline = (6779.58,4426.21,0)
  Direction = (0,0,0)
  Distance = 900
  End = (6950,4725,0)
  Normal = (0,0,1)
  Start = (6950,3825,0)
FEATURE [App::FeaturePython] Dimension038  # Draft dimension (typed FeaturePython)
  Diameter = false
  Dimline = (5670,-235,0)
  Direction = (0,0,0)
  Distance = 1050
  End = (6720,-25,0)
  Normal = (0,0,1)
  Start = (5670,-25,0)
FEATURE [App::FeaturePython] Dimension039  # Draft dimension (typed FeaturePython)
  Diameter = false
  Dimline = (4835,-235,0)
  Direction = (0,0,0)
  Distance = 660
  End = (4835,-25,0)
  Normal = (0,0,1)
  Start = (4175,-25,0)
FEATURE [App::FeaturePython] Dimension040  # Draft dimension (typed FeaturePython)
  Diameter = false
  Dimline = (7555,-235,0)
  Direction = (0,0,0)
  Distance = 660
  End = (8215,-25,0)
  Normal = (0,0,1)
  Start = (7555,-25,0)
FEATURE [App::FeaturePython] Dimension041  # Draft dimension (typed FeaturePython)
  Diameter = false
  Dimline = (-240,1840,0)
  Direction = (0,0,0)
  Distance = 1440
  End = (-30,3280,0)
  Normal = (0,0,1)
  Start = (-30,1840,0)
FEATURE [App::FeaturePython] Dimension042  # Draft dimension (typed FeaturePython)
  Diameter = false
  Dimline = (12760,1320,0)
  Direction = (0,0,0)
  Distance = 1960
  End = (12550,3280,0)
  Normal = (0,0,1)
  Start = (12550,1320,0)
FEATURE [App::FeaturePython] Dimension043  # Draft dimension (typed FeaturePython)
  Diameter = false
  Dimline = (12760,4000,0)
  Direction = (0,0,0)
  Distance = 920
  End = (12550,4970,0)
  Normal = (0,0,1)
  Start = (12550,4050,0)
FEATURE [App::FeaturePython] Dimension044  # Draft dimension (typed FeaturePython)
  Diameter = false
  Dimline = (8595,7695,0)
  Direction = (0,0,0)
  Distance = 1960
  End = (10555,7485,0)
  Normal = (0,0,1)
  Start = (8595,7485,0)
FEATURE [App::FeaturePython] Dimension045  # Draft dimension (typed FeaturePython)
  Diameter = false
  Dimline = (6005,7695,0)
  Direction = (0,0,0)
  Distance = 920
  End = (6005,7485,0)
  Normal = (0,0,1)
  Start = (5085,7485,0)
FEATURE [App::FeaturePython] Dimension046  # Draft dimension (typed FeaturePython)
  Diameter = false
  Dimline = (3925,7695,0)
  Direction = (0,0,0)
  Distance = 1960
  End = (3925,7485,0)
  Normal = (0,0,1)
  Start = (1965,7485,0)
FEATURE [App::FeaturePython] Dimension047  # Draft dimension (typed FeaturePython)
  Diameter = false
  Dimline = (5690,200,0)
  Direction = (0,0,0)
  Distance = 3200
  End = (7300,-25,0)
  Normal = (0,0,1)
  Start = (4100,-25,0)
FEATURE [App::FeaturePython] Dimension048  # Draft dimension (typed FeaturePython)
  Diameter = false
  Dimline = (6743,1052.26,0)
  Direction = (0,0,0)
  Distance = 2310
  End = (7300,2285,0)
  Normal = (0,0,1)
  Start = (7300,-25,0)
FEATURE [App::FeaturePython] Dimension049  # Draft dimension (typed FeaturePython)
  Diameter = false
  Dimline = (3200,1600,0)
  Direction = (0,0,0)
  Distance = 3560
  End = (-30,3535,0)
  Normal = (0,0,1)
  Start = (-30,-25,0)
FEATURE [App::FeaturePython] Dimension050  # Draft dimension (typed FeaturePython)
  Diameter = false
  Dimline = (2900,1200,0)
  Direction = (0,0,0)
  Distance = 4030
  End = (4000,-25,0)
  Normal = (0,0,1)
  Start = (-30,-25,0)
FEATURE [App::FeaturePython] Dimension052  # Draft dimension (typed FeaturePython)
  Diameter = false
  Dimline = (11900,1600,0)
  Direction = (0,0,0)
  Distance = 3560
  End = (12550,3535,0)
  Normal = (0,0,1)
  Start = (12550,-25,0)
FEATURE [App::FeaturePython] Dimension053  # Draft dimension (typed FeaturePython)
  Diameter = false
  Dimline = (3700,8200,0)
  Direction = (0,0,0)
  Distance = 1830
  End = (3860,8015,0)
  Normal = (0,0,1)
  Start = (2030,8015,0)
FEATURE [App::FeaturePython] Dimension054  # Draft dimension (typed FeaturePython)
  Diameter = false
  Dimline = (2500,4300,0)
  Direction = (0,0,0)
  Distance = 4850
  End = (4820,7485,0)
  Normal = (0,0,1)
  Start = (-30,7485,0)
FEATURE [App::FeaturePython] Dimension055  # Draft dimension (typed FeaturePython)
  Diameter = false
  Dimline = (8800,6200,0)
  Direction = (0,0,0)
  Distance = 4590
  End = (12550,3825,0)
  Normal = (0,0,1)
  Start = (7960,3825,0)
FEATURE [App::FeaturePython] Dimension056  # Draft dimension (typed FeaturePython)
  Diameter = false
  Dimline = (10943.1,642.693,0)
  Direction = (0,0,0)
  Distance = 3000
  End = (12550,-25,0)
  Normal = (0,0,1)
  Start = (9550,-25,0)
FEATURE [App::FeaturePython] Dimension057  # Draft dimension (typed FeaturePython)
  Diameter = false
  Dimline = (800,4600,0)
  Direction = (0,0,0)
  Distance = 3660
  End = (-30,7485,0)
  Normal = (0,0,1)
  Start = (-30,3825,0)
FEATURE [App::FeaturePython] Dimension058  # Draft dimension (typed FeaturePython)
  Diameter = false
  Dimline = (10700,200,0)
  Direction = (0,0,0)
  Distance = 2050
  End = (9450,-25,0)
  Normal = (0,0,1)
  Start = (7400,-25,0)
FEATURE [App::FeaturePython] Dimension059  # Draft dimension (typed FeaturePython)
  Diameter = false
  Dimline = (12100,4500,0)
  Direction = (0,0,0)
  Distance = 3660
  End = (12550,7485,0)
  Normal = (0,0,1)
  Start = (12550,3825,0)
FEATURE [App::FeaturePython] Dimension060  # Draft dimension (typed FeaturePython)
  Diameter = false
  Dimline = (8800,3300,0)
  Direction = (0,0,0)
  Distance = 3520
  End = (11920,3680,0)
  Normal = (0,0,1)
  Start = (8400,3680,0)
FEATURE [App::FeaturePython] Dimension061  # Draft dimension (typed FeaturePython)
  Diameter = false
  Dimline = (11920,3300,0)
  Direction = (0,0,0)
  Distance = 650
  End = (12570,3665,0)
  Normal = (0,0,1)
  Start = (11920,3665,0)
FEATURE [App::FeaturePython] Dimension062  # Draft dimension (typed FeaturePython)
  Diameter = false
  Dimline = (6720,3300,0)
  Direction = (0,0,0)
  Distance = 1680
  End = (8400,3680,0)
  Normal = (0,0,1)
  Start = (6720,3680,0)
FEATURE [App::FeaturePython] Dimension063  # Draft dimension (typed FeaturePython)
  Diameter = false
  Dimline = (5800,3300,0)
  Direction = (0,0,0)
  Distance = 1030
  End = (5800,3680,0)
  Normal = (0,0,1)
  Start = (4770,3680,0)
FEATURE [App::FeaturePython] Dimension064  # Draft dimension (typed FeaturePython)
  Diameter = false
  Dimline = (3850,4000,0)
  Direction = (0,0,0)
  Distance = 3900
  End = (3850,3680,0)
  Normal = (0,0,1)
  Start = (-50,3680,0)
FEATURE [TechDraw::DrawViewAnnotation] Annotation009  label="a_077"
  Font = osifont
  LineSpace = 80
  LockPosition = true
  MaxWidth = -1
  Rotation = 0
  ScaleType = 0
  Text = \u0410\u0440\u043c\u043f\u043e\u044f\u0441 180x140mm
  TextSize = 4
  TextStyle = 0
  X = 256.728
  Y = 224.794
FEATURE [TechDraw::DrawViewAnnotation] Annotation010  label="a_078"
  Font = osifont
  LineSpace = 80
  LockPosition = true
  MaxWidth = -1
  Rotation = 0
  ScaleType = 0
  Text = XPS 80mm
  TextSize = 4
  TextStyle = 0
  X = 265.062
  Y = 229.944
FEATURE [TechDraw::DrawViewAnnotation] Annotation011  label="a_079"
  Font = osifont
  LineSpace = 80
  LockPosition = true
  MaxWidth = -1
  Rotation = 0
  ScaleType = 0
  Text = \u041a\u0438\u0440\u043f\u0438\u0447 2.1 \u043d\u0444
  TextSize = 4
  TextStyle = 0
  X = 260.909
  Y = 212.329
FEATURE [TechDraw::DrawViewAnnotation] Annotation012  label="a_080"
  Font = osifont
  LineSpace = 80
  LockPosition = true
  MaxWidth = -1
  Rotation = 0
  ScaleType = 0
  Text = \u041c\u0430\u0443\u044d\u0440\u043b\u0430\u0442 150\u0445150mm
  TextSize = 4
  TextStyle = 0
  X = 256.196
  Y = 218.755
FEATURE [TechDraw::DrawLeaderLine] LeaderLine
  AutoHorizontal = true
  EndSymbol = 7
  LeaderParent = -> Annotation010
  LockPosition = true
  Rotation = 0
  Scalable = false
  ScaleType = 0
  StartSymbol = 7
  WayPoints = (3) [(0,0,0),(9.82636,-670.069,0),(-263.143,-670.069,0)]
  X = 17.2239
  Y = -68.3719
FEATURE [TechDraw::DrawLeaderLine] LeaderLine001
  AutoHorizontal = true
  EndSymbol = 7
  LeaderParent = -> Annotation012
  LockPosition = true
  Rotation = 0
  Scalable = false
  ScaleType = 0
  StartSymbol = 7
  WayPoints = (3) [(0,0,0),(10.0885,-535.699,0),(-399.504,-535.699,0)]
  X = 22.6678
  Y = -54.1973
FEATURE [TechDraw::DrawLeaderLine] LeaderLine002
  AutoHorizontal = true
  EndSymbol = 7
  LeaderParent = -> Annotation009
  LockPosition = true
  Rotation = 0
  Scalable = false
  ScaleType = 0
  StartSymbol = 7
  WayPoints = (3) [(0,0,0),(10.0885,-626.495,0),(-400.513,-626.495,0)]
  X = 23.346
  Y = -63.2619
FEATURE [TechDraw::DrawLeaderLine] LeaderLine003
  AutoHorizontal = true
  EndSymbol = 7
  LeaderParent = -> Annotation011
  LockPosition = true
  Rotation = 0
  Scalable = false
  ScaleType = 0
  StartSymbol = 7
  WayPoints = (3) [(0,0,0),(11.2011,-497.917,0),(-281.712,-497.917,0)]
  X = 15.6278
  Y = -50.7269
FEATURE [TechDraw::DrawViewAnnotation] Annotation013  label="a_082"
  Font = osifont
  LineSpace = 80
  LockPosition = true
  MaxWidth = -1
  Rotation = 0
  ScaleType = 0
  Text = XPS 100mm
  TextSize = 4
  TextStyle = 0
  X = 118.3
  Y = 198.428
FEATURE [TechDraw::DrawViewAnnotation] Annotation014  label="a_083"
  Font = osifont
  LineSpace = 80
  LockPosition = true
  MaxWidth = -1
  Rotation = 0
  ScaleType = 0
  Text = \u041f\u043e\u043a\u0440\u044b\u0442\u0438\u0435 \u043f\u043e\u043b\u0430 20mm
  TextSize = 4
  TextStyle = 0
  X = 109.298
  Y = 208.784
FEATURE [TechDraw::DrawViewAnnotation] Annotation015  label="a_084"
  Font = osifont
  LineSpace = 80
  LockPosition = true
  MaxWidth = -1
  Rotation = 0
  ScaleType = 0
  Text = \u0421\u0442\u044f\u0436\u043a\u0430 \u043f\u043e\u043b\u0430 50mm
  TextSize = 4
  TextStyle = 0
  X = 111.999
  Y = 203.648
FEATURE [TechDraw::DrawViewAnnotation] Annotation016  label="a_076"
  Font = osifont
  LineSpace = 80
  LockPosition = true
  MaxWidth = -1
  Rotation = 0
  ScaleType = 0
  Text = \u041e\u0431\u043b\u0438\u0446\u043e\u0432\u043e\u0447\u043d\u044b\u0439 \u043a\u0438\u0440\u043f\u0438\u0447 1\u043d\u0444
  TextSize = 4
  TextStyle = 0
  X = 250.884
  Y = 234.906
FEATURE [TechDraw::DrawLeaderLine] LeaderLine004
  AutoHorizontal = true
  EndSymbol = 7
  LeaderParent = -> Annotation016
  LockPosition = true
  Rotation = 0
  Scalable = false
  ScaleType = 0
  StartSymbol = 7
  WayPoints = (3) [(0,0,0),(17.4485,-744.208,0),(-570.424,-744.208,0)]
  X = 33.3756
  Y = -74.7769
FEATURE [TechDraw::DrawViewAnnotation] Annotation017  label="a_001"
  Font = osifont
  LineSpace = 80
  LockPosition = true
  MaxWidth = -1
  Rotation = 0
  ScaleType = 0
  Text = XPS 100mm
  TextSize = 4
  TextStyle = 0
  X = 301.631
  Y = 118.628
FEATURE [TechDraw::DrawViewAnnotation] Annotation018  label="a_028"
  Font = osifont
  LineSpace = 80
  LockPosition = true
  MaxWidth = -1
  Rotation = 0
  ScaleType = 0
  Text = XPS 80mm
  TextSize = 4
  TextStyle = 0
  X = 313.482
  Y = 140.167
FEATURE [TechDraw::DrawViewAnnotation] Annotation019  label="a_029"
  Font = osifont
  LineSpace = 80
  LockPosition = true
  MaxWidth = -1
  Rotation = 0
  ScaleType = 0
  Text = \u041f\u0435\u0440\u0435\u043c\u044b\u0447\u043a\u0430 \u043c\u043e\u043d\u043e\u043b\u0438\u0442\u043d\u0430\u044f
  TextSize = 4
  TextStyle = 0
  X = 311.808
  Y = 112.937
FEATURE [TechDraw::DrawViewAnnotation] Annotation020  label="a_030"
  Font = osifont
  LineSpace = 80
  LockPosition = true
  MaxWidth = -1
  Rotation = 0
  ScaleType = 0
  Text = \u041a\u0430\u043c\u0435\u043d\u044c \u043e\u0431\u043b\u0438\u0446\u043e\u0432\u043e\u0447\u043d\u044b\u0439
  TextSize = 4
  TextStyle = 0
  X = 311.983
  Y = 123.571
FEATURE [TechDraw::DrawViewAnnotation] Annotation021  label="a_031"
  Font = osifont
  LineSpace = 80
  LockPosition = true
  MaxWidth = -1
  Rotation = 0
  ScaleType = 0
  Text = \u041a\u0438\u0440\u043f\u0438\u0447 1\u043d\u0444
  TextSize = 4
  TextStyle = 0
  X = 320.081
  Y = 135.139
FEATURE [TechDraw::DrawViewAnnotation] Annotation022  label="a_032"
  Font = osifont
  LineSpace = 80
  LockPosition = true
  MaxWidth = -1
  Rotation = 0
  ScaleType = 0
  Text = \u0411\u043b\u043e\u043a 380\u043c\u043c \u041b\u0421\u0420 10.7\u043d\u0444 "\u0422\u0451\u043f\u043b\u044b\u0439"
  TextSize = 4
  TextStyle = 0
  X = 68.8072
  Y = 136.929
FEATURE [TechDraw::DrawViewAnnotation] Annotation023  label="a_033"
  Font = osifont
  LineSpace = 80
  LockPosition = true
  MaxWidth = -1
  Rotation = 0
  ScaleType = 0
  Text = XPS 100mm
  TextSize = 4
  TextStyle = 0
  X = 97.5568
  Y = 118.043
FEATURE [TechDraw::DrawViewAnnotation] Annotation024  label="a_034"
  Font = osifont
  LineSpace = 80
  LockPosition = true
  MaxWidth = -1
  Rotation = 0
  ScaleType = 0
  Text = \u0421\u0442\u044f\u0436\u043a\u0430 \u0442\u0451\u043f\u043b\u043e\u0433\u043e \u043f\u043e\u043b\u0430 80mm
  TextSize = 4
  TextStyle = 0
  X = 83.3647
  Y = 122.395
FEATURE [TechDraw::DrawViewAnnotation] Annotation025  label="a_035"
  Font = osifont
  LineSpace = 80
  LockPosition = true
  MaxWidth = -1
  Rotation = 0
  ScaleType = 0
  Text = \u041f\u043e\u043a\u0440\u044b\u0442\u0438\u0435 \u043f\u043e\u043b\u0430 20mm
  TextSize = 4
  TextStyle = 0
  X = 88.1001
  Y = 127.174
FEATURE [TechDraw::DrawViewAnnotation] Annotation026  label="a_036"
  Font = osifont
  LineSpace = 80
  LockPosition = true
  MaxWidth = -1
  Rotation = 0
  ScaleType = 0
  Text = \u041f\u043b\u0438\u0442\u044b \u043e\u0431\u043b\u0435\u0433\u0447\u0451\u043d\u043d\u044b\u0435 160mm
  TextSize = 4
  TextStyle = 0
  X = 104.49
  Y = 193.218
FEATURE [TechDraw::DrawLeaderLine] LeaderLine005
  AutoHorizontal = true
  EndSymbol = 7
  LeaderParent = -> Annotation026
  LockPosition = true
  Rotation = 0
  Scalable = false
  ScaleType = 0
  StartSymbol = 7
  WayPoints = (3) [(0,0,0),(-2.30237,-441.288,0),(-511.894,-441.288,0)]
  X = 27.6874
  Y = -45.469
FEATURE [TechDraw::DrawLeaderLine] LeaderLine006
  AutoHorizontal = true
  EndSymbol = 7
  LeaderParent = -> Annotation023
  LockPosition = true
  Rotation = 0
  Scalable = false
  ScaleType = 0
  StartSymbol = 7
  WayPoints = (4) [(0,0,0),(0,-112.671,0),(-241.304,-298.052,0),(-700.128,-298.052,0)]
  X = 33.001
  Y = -31.105
FEATURE [TechDraw::DrawLeaderLine] LeaderLine007
  AutoHorizontal = true
  EndSymbol = 7
  LeaderParent = -> Annotation022
  LockPosition = true
  Rotation = 0
  Scalable = false
  ScaleType = 0
  StartSymbol = 7
  WayPoints = (3) [(0,0,0),(-234.053,-148.301,0),(-811.115,-148.301,0)]
  X = 52.2554
  Y = -15.2644
FEATURE [TechDraw::DrawLeaderLine] LeaderLine008
  AutoHorizontal = true
  EndSymbol = 7
  LeaderParent = -> Annotation019
  LockPosition = true
  Rotation = 0
  Scalable = false
  ScaleType = 0
  StartSymbol = 7
  WayPoints = (3) [(0,0,0),(123.191,316.527,0),(538.433,316.527,0)]
  X = -33.8955
  Y = 30.8346
FEATURE [TechDraw::DrawLeaderLine] LeaderLine009
  AutoHorizontal = true
  EndSymbol = 7
  LeaderParent = -> Annotation017
  LockPosition = true
  Rotation = 0
  Scalable = false
  ScaleType = 0
  StartSymbol = 7
  WayPoints = (3) [(0,0,0),(99.3175,258.506,0),(299.176,258.506,0)]
  X = -19.5842
  Y = 24.9219
FEATURE [TechDraw::DrawLeaderLine] LeaderLine010
  AutoHorizontal = true
  EndSymbol = 7
  LeaderParent = -> Annotation020
  LockPosition = true
  Rotation = 0
  Scalable = false
  ScaleType = 0
  StartSymbol = 7
  WayPoints = (3) [(0,0,0),(77.3527,184.314,0),(465.976,184.314,0)]
  X = -27.3933
  Y = 17.9304
FEATURE [TechDraw::DrawLeaderLine] LeaderLine011
  AutoHorizontal = true
  EndSymbol = 7
  LeaderParent = -> Annotation021
  LockPosition = true
  Rotation = 0
  Scalable = false
  ScaleType = 0
  StartSymbol = 7
  WayPoints = (3) [(0,0,0),(246.354,145.817,0),(563.314,145.817,0)]
  X = -40.3095
  Y = 13.3285
FEATURE [TechDraw::DrawLeaderLine] LeaderLine012
  AutoHorizontal = true
  EndSymbol = 7
  LeaderParent = -> Annotation018
  LockPosition = true
  Rotation = 0
  Scalable = false
  ScaleType = 0
  StartSymbol = 7
  WayPoints = (3) [(0,0,0),(226.991,110.973,0),(407.743,110.973,0)]
  X = -31.4229
  Y = 10.0706
FEATURE [App::FeaturePython] Dimension065  # Draft dimension (typed FeaturePython)
  Diameter = false
  Dimline = (0,5100,1600)
  Direction = (0,0,0)
  Distance = 2800
  End = (0,3665,2800)
  Normal = (1,0,0)
  Start = (0,3665,0)
FEATURE [App::FeaturePython] Dimension066  # Draft dimension (typed FeaturePython)
  Diameter = false
  Dimline = (0,5100,2700)
  Direction = (0,0,0)
  Distance = 330
  End = (0,3665,3130)
  Normal = (1,0,0)
  Start = (0,3665,2800)
FEATURE [App::FeaturePython] Dimension067  # Draft dimension (typed FeaturePython)
  Diameter = false
  Dimline = (0,5100,4100)
  Direction = (0,0,0)
  Distance = 503
  End = (0,3665,3633)
  Normal = (1,0,0)
  Start = (0,3665,3130)
FEATURE [App::FeaturePython] Dimension069  # Draft dimension (typed FeaturePython)
  Diameter = false
  Dimline = (0,3400,1900)
  Direction = (0,0,0)
  Distance = 300
  End = (0,3790,2800)
  Normal = (1,0,0)
  Start = (0,3790,2500)
FEATURE [App::FeaturePython] Dimension071  # Draft dimension (typed FeaturePython)
  Diameter = false
  Dimline = (0,11400,-400)
  Direction = (0,0,0)
  Distance = 7180
  End = (0,3730,6980)
  Normal = (1,0,0)
  Start = (0,3730,-200)
FEATURE [App::GeometryPython] BuildingPart100  label="Размеры (side)"  # Arch/BIM 52 (typed FeaturePython)
  Area = 0
  GlobalId = 27k3ICoRP4zxJkZ2CvXEQH
  Group = -> [Dimension029,Dimension065,Dimension066,Dimension067,Dimension069,Dimension071]
  Height = 0
  HeightPropagate = true
  IfcData = IfcUID=27k3ICoRP4zxJkZ2CvXEQH,+2 more (map truncated)
  IfcType = 52
  LevelOffset = 0
  Placement = pos=(0,0,0) rot=(0.57735,0.57735,0.57735;2.0944rad)
FEATURE [App::MaterialObjectPython] Material019  label="Red brick (solid)"  # material (typed FeaturePython)
  Description = A standard red brick
  Material = AuthorAndLicense=Concrete-Generic,CardName=Concrete-Generic,Color=(0.6666666666666666, 0.0, 0.0, 1.0),CompressiveStrength=25 MPa,Density=2400 kg/m^3,+9 more (map truncated)
  Transparency = 0
FEATURE [App::DocumentObjectGroupPython] MaterialContainer  label="Materials"  # scripted group (container) (typed FeaturePython)
  Group = -> [Material004,Material001,Material006,Material011,Material003,Material009,Material010,Material007,Material008,Material005,Material,Material002,Material012,Material013,Material014,Material015,Material016,Material017,Material018,Material019]
FEATURE [Part::FeaturePython] Wall301  label="Облицовка цоколя (полнотел.1нф) 001"  # Arch/BIM 166 (typed FeaturePython)
  Align = 1
  Area = 633000
  Base = -> Line1585
  BlockHeight = 65
  BlockLength = 250
  CountBroken = 1
  CountEntire = 32
  Face = 0
  GlobalId = 1E5ZyhmSr7guLYcvr8Y9qj
  Height = 75
  HorizontalArea = 1012800
  IfcData = IfcUID=1E5ZyhmSr7guLYcvr8Y9qj; attributes={"GlobalId": {"value": "1E5ZyhmSr7guLYcvr8Y9qj"}}
  IfcType = 166
  Joint = 10
  Length = 8440
  MakeBlocks = false
  Material = -> Material019
  MoveBase = false
  MoveWithHost = false
  Normal = (0,0,0)
  OffsetFirst = 250
  OffsetSecond = 120
  PerimeterLength = 17120
  Placement = pos=(0,0,-200) rot=(0,0,1;0rad)
  PredefinedType = 0
  VerticalArea = 1284000
  Width = 120
FEATURE [Part::FeaturePython] Wall302  label="Облицовка цоколя (полнотел.1нф) 010"  # Arch/BIM 166 (typed FeaturePython)
  Align = 0
  Area = 1003500
  Base = -> Line1584
  BlockHeight = 65
  BlockLength = 250
  CountBroken = 1
  CountEntire = 51
  Face = 0
  GlobalId = 1TP$vjbOv5ffUx0fDKfugP
  Height = 75
  HorizontalArea = 1605600
  IfcData = IfcUID=1TP$vjbOv5ffUx0fDKfugP; attributes={"GlobalId": {"value": "1TP$vjbOv5ffUx0fDKfugP"}}
  IfcType = 166
  Joint = 10
  Length = 13380
  MakeBlocks = false
  Material = -> Material019
  MoveBase = false
  MoveWithHost = false
  Normal = (0,0,0)
  OffsetFirst = 250
  OffsetSecond = 120
  PerimeterLength = 27000
  Placement = pos=(0,0,-200) rot=(0,0,1;0rad)
  PredefinedType = 0
  VerticalArea = 2025000
  Width = 120
FEATURE [Part::FeaturePython] Wall303  label="Облицовка цоколя (полнотел.1нф) 011"  # Arch/BIM 166 (typed FeaturePython)
  Align = 1
  Area = 642750
  Base = -> Line1586
  BlockHeight = 65
  BlockLength = 250
  CountBroken = 0
  CountEntire = 33
  Face = 0
  GlobalId = 0Qqq80WcDAy9cO4W0cQ$pL
  Height = 75
  HorizontalArea = 1028400
  IfcData = IfcUID=0Qqq80WcDAy9cO4W0cQ$pL; attributes={"GlobalId": {"value": "0Qqq80WcDAy9cO4W0cQ$pL"}}
  IfcType = 166
  Joint = 10
  Length = 8570
  MakeBlocks = false
  Material = -> Material019
  MoveBase = false
  MoveWithHost = false
  Normal = (0,0,0)
  OffsetFirst = 250
  OffsetSecond = 120
  PerimeterLength = 17380
  Placement = pos=(0,0,-200) rot=(0,0,1;0rad)
  PredefinedType = 0
  VerticalArea = 1303500
  Width = 120
FEATURE [Part::FeaturePython] Wall304  label="Облицовка цоколя (полнотел.1нф) 012"  # Arch/BIM 166 (typed FeaturePython)
  Align = 0
  Area = 1013250
  Base = -> Line1583
  BlockHeight = 65
  BlockLength = 250
  CountBroken = 0
  CountEntire = 52
  Face = 0
  GlobalId = 0a9Ful3VXDtwee5LreBW$T
  Height = 75
  HorizontalArea = 1621200
  IfcData = IfcUID=0a9Ful3VXDtwee5LreBW$T; attributes={"GlobalId": {"value": "0a9Ful3VXDtwee5LreBW$T"}}
  IfcType = 166
  Joint = 10
  Length = 13510
  MakeBlocks = false
  Material = -> Material019
  MoveBase = false
  MoveWithHost = false
  Normal = (0,0,0)
  OffsetFirst = 250
  OffsetSecond = 120
  PerimeterLength = 27260
  Placement = pos=(0,0,-200) rot=(0,0,1;0rad)
  PredefinedType = 0
  VerticalArea = 2044500
  Width = 120
FEATURE [Part::Part2DObjectPython] Wire890  # Draft 2D object (typed FeaturePython)
  Area = 0
  ChamferSize = 0
  Closed = true
  End = (12950,-425,0)
  FilletRadius = 0
  Length = 43380
  MakeFace = false
  Placement = pos=(-430,-410,0) rot=(0,0,1;0rad)
  Points = (4) [(0,-15,0),(0,8295,0),(13380,8295,0),(13380,-15,0)]
  Start = (-430,-425,0)
  Subdivisions = 0
FEATURE [Part::FeaturePython] Wall310  label="Отлив (вибропресс. бордюрный камень 1000х200х80мм)"  # Arch/BIM 166 (typed FeaturePython)
  Align = 1
  Area = 3470400
  Base = -> Wire890
  BlockHeight = 80
  BlockLength = 1000
  CountBroken = 4
  CountEntire = 39
  Face = 0
  Height = 80
  HorizontalArea = 8852000
  IfcData = attributes={"GlobalId": {"name": "GlobalId", "type": "IfcGloballyUniqueId", "is_enum": false, "enum_values": []}, "Description": {"... (+533 chars omitted),+1 more (map truncated)
  IfcType = 166
  Joint = 0
  Length = 43380
  MakeBlocks = false
  Material = -> Material018
  MoveBase = false
  MoveWithHost = false
  Normal = (0,0,0)
  Offset = 10
  OffsetFirst = 0
  OffsetSecond = 0
  PerimeterLength = 45060
  Placement = pos=(0,0,-120) rot=(0,0,1;0rad)
  PredefinedType = 0
  VerticalArea = 7081600
  Width = 200
FEATURE [Part::FeaturePython] Wall311  label="Утепление цоколя XPS 50mm"  # Arch/BIM 166 (typed FeaturePython)
  Align = 1
  Area = 8676000
  Base = -> Wire890
  BlockHeight = 80
  BlockLength = 1000
  CountBroken = 4
  CountEntire = 39
  Face = 0
  Height = 200
  HorizontalArea = 2.231e+06
  IfcData = attributes={"GlobalId": {"name": "GlobalId", "type": "IfcGloballyUniqueId", "is_enum": false, "enum_values": []}, "Description": {"... (+533 chars omitted),+1 more (map truncated)
  IfcType = 166
  Joint = 0
  Length = 43380
  MakeBlocks = false
  Material = -> Material002
  MoveBase = false
  MoveWithHost = false
  Normal = (0,0,0)
  Offset = 130
  OffsetFirst = 0
  OffsetSecond = 0
  PerimeterLength = 44820
  Placement = pos=(0,0,-320) rot=(0,0,1;0rad)
  PredefinedType = 0
  VerticalArea = 17848000
  Width = 50
FEATURE [Part::FeaturePython] Wall312  label="Отделка цоколя 15mm"  # Arch/BIM 166 (typed FeaturePython)
  Align = 1
  Area = 8676000
  Base = -> Wire890
  BlockHeight = 80
  BlockLength = 1000
  CountBroken = 4
  CountEntire = 39
  Face = 0
  Height = 200
  HorizontalArea = 673200
  IfcData = attributes={"GlobalId": {"name": "GlobalId", "type": "IfcGloballyUniqueId", "is_enum": false, "enum_values": []}, "Description": {"... (+533 chars omitted),+1 more (map truncated)
  IfcType = 166
  Joint = 0
  Length = 43380
  MakeBlocks = false
  Material = -> Material018
  MoveBase = false
  MoveWithHost = false
  Normal = (0,0,0)
  Offset = 180
  OffsetFirst = 0
  OffsetSecond = 0
  PerimeterLength = 44940
  Placement = pos=(0,0,-320) rot=(0,0,1;0rad)
  PredefinedType = 0
  VerticalArea = 17952000
  Width = 15
FEATURE [App::GeometryPython] BuildingPart102  label="Облицовка 1nf кирпич001"  # Arch/BIM 52 (typed FeaturePython)
  Area = 185118900
  GlobalId = 28tVz6in97ivETWCX3RcDU
  Group = -> [Wall298,Wall299,Wall300,Wall301,Wall302,Wall303,Wall304,Wall305,Wall306,Wall307,Wall308,Wall309,Wall310,Wall311,Wall312]
  Height = 0
  HeightPropagate = true
  IfcData = IfcUID=28tVz6in97ivETWCX3RcDU,attributes={"GlobalId": {"value": "28tVz6in97ivETWCX3RcDU"}},+1 more (map truncated)
  IfcType = 52
  LevelOffset = 0
FEATURE [TechDraw::DrawViewAnnotation] Annotation  label="a_092"
  Font = osifont
  LineSpace = 80
  LockPosition = true
  MaxWidth = -1
  Rotation = 0
  Scale = 0.02
  ScaleType = 0
  Text = \u041e\u0442\u0434\u0435\u043b\u043a\u0430 \u0446\u043e\u043a\u043e\u043b\u044f 15mm
  TextSize = 4
  TextStyle = 0
  X = 85.2969
  Y = 88.0815
FEATURE [TechDraw::DrawViewAnnotation] Annotation027  label="a_093"
  Font = osifont
  LineSpace = 80
  LockPosition = true
  MaxWidth = -1
  Rotation = 0
  Scale = 0.02
  ScaleType = 0
  Text = XPS 50mm
  TextSize = 4
  TextStyle = 0
  X = 95.3409
  Y = 93.1161
FEATURE [TechDraw::DrawViewAnnotation] Annotation028  label="a_094"
  Font = osifont
  LineSpace = 80
  LockPosition = true
  MaxWidth = -1
  Rotation = 0
  Scale = 0.02
  ScaleType = 0
  Text = \u041a\u0430\u043c\u0435\u043d\u044c \u0431\u043e\u0440\u0434\u044e\u0440\u043d\u044b\u0439 1000\u044580\u0445200mm
  TextSize = 4
  TextStyle = 0
  X = 74.5727
  Y = 97.7244
FEATURE [TechDraw::DrawLeaderLine] LeaderLine013
  AutoHorizontal = true
  EndSymbol = 7
  LeaderParent = -> Annotation
  LockPosition = true
  Rotation = 0
  Scalable = false
  ScaleType = 0
  StartSymbol = 7
  WayPoints = (3) [(0,0,0),(-95.8036,-29.0684,0),(-464.748,-29.0684,0)]
  X = 1397.61
  Y = -181.771
FEATURE [TechDraw::DrawLeaderLine] LeaderLine014
  AutoHorizontal = true
  EndSymbol = 7
  LeaderParent = -> Annotation027
  LockPosition = true
  Rotation = 0
  Scalable = false
  ScaleType = 0
  StartSymbol = 7
  WayPoints = (3) [(0,0,0),(-103.814,-76.5886,0),(-277.347,-76.5886,0)]
  X = 939.794
  Y = -403.983
FEATURE [TechDraw::DrawLeaderLine] LeaderLine015
  AutoHorizontal = true
  EndSymbol = 7
  LeaderParent = -> Annotation028
  LockPosition = true
  Rotation = 0
  Scalable = false
  ScaleType = 0
  StartSymbol = 7
  WayPoints = (3) [(0,0,0),(-108.706,-86.9646,0),(-695.382,-86.9646,0)]
  X = 2006.85
  Y = -452.409
FEATURE [TechDraw::DrawViewAnnotation] Annotation029  label="a_095"
  Font = osifont
  LineSpace = 80
  LockPosition = true
  MaxWidth = -1
  Rotation = 0
  Scale = 0.02
  ScaleType = 0
  Text = \u041a\u0438\u0440\u043f\u0438\u0447 \u043f\u043e\u043b\u043d\u043e\u0442\u0435\u043b\u044b\u0439 1\u043d\u0444
  TextSize = 4
  TextStyle = 0
  X = 313.34
  Y = 91.6882
FEATURE [TechDraw::DrawLeaderLine] LeaderLine016
  AutoHorizontal = true
  EndSymbol = 7
  LeaderParent = -> Annotation029
  LockPosition = true
  Rotation = 0
  Scalable = false
  ScaleType = 0
  StartSymbol = 7
  WayPoints = (3) [(0,0,0),(77.064,-40.1375,0),(501.188,-40.1375,0)]
  X = -1439.22
  Y = -222.205
FEATURE [App::DocumentObjectGroup] Group127  label="Выноски"
  Group = -> [LeaderLine,LeaderLine001,LeaderLine002,LeaderLine003,LeaderLine004,LeaderLine005,LeaderLine006,LeaderLine007,LeaderLine008,LeaderLine009,LeaderLine010,LeaderLine011,LeaderLine012,LeaderLine013,LeaderLine014,LeaderLine015,LeaderLine016]
FEATURE [TechDraw::DrawSVGTemplate] Template
  EditableTexts = Лист=2; Номер=ИЖС-0000.0001
  Height = 297
  Orientation = 1
  Width = 420
FEATURE [TechDraw::DrawViewSpreadsheet] Sheet
  CellEnd = E12
  CellStart = C1
  Font = osifont
  LineWidth = 0.35
  LockPosition = false
  Rotation = 0
  Scale = 1.2
  ScaleType = 2
  Source = -> Spreadsheet
  Symbol = <blob: 8017 chars omitted>
  TextSize = 12
  X = 107.319
  Y = 207.308
FEATURE [TechDraw::DrawViewAnnotation] Annotation030
  Font = osifont
  LineSpace = 80
  LockPosition = false
  MaxWidth = -1
  Rotation = 0
  ScaleType = 0
  Text = \u042d\u043a\u0441\u043f\u043b\u0438\u043a\u0430\u0446\u0438\u044f \u043f\u043e\u043c\u0435\u0449\u0435\u043d\u0438\u0439 1-\u0433\u043e \u044d\u0442\u0430\u0436\u0430
  TextSize = 8
  TextStyle = 0
  X = 107.631
  Y = 267.351
FEATURE [TechDraw::DrawPage] Page  label="Экспликация"
  KeepUpdated = false
  NextBalloonIndex = 1
  ProjectionType = 0
  Template = -> Template
  Views = -> [Sheet,Annotation030]
FEATURE [Part::Part2DObjectPython] Line1602  # Draft 2D object (typed FeaturePython)
  Area = 0
  ChamferSize = 0
  Closed = true
  End = (22842.7,-9031.64,0)
  FilletRadius = 0
  Length = 380
  MakeFace = true
  Placement = pos=(17078.5,-7861.73,0) rot=(0,0,1;1.37981rad)
  Points = (2) [(-109.84,-5505.54,0),(-54.4343,-5881.48,0)]
  Start = (22463.1,-9014.68,0)
  Subdivisions = 0
FEATURE [Part::FeaturePython] Wall316  label="Столб 001"  # Arch/BIM 166 (typed FeaturePython)
  Align = 0
  Area = 836000
  Base = -> Line1602
  BlockHeight = 0
  BlockLength = 0
  CountBroken = 0
  CountEntire = 0
  Face = 0
  Height = 2200
  HorizontalArea = 144400
  IfcData = attributes={"GlobalId": {"name": "GlobalId", "type": "IfcGloballyUniqueId", "is_enum": false, "enum_values": []}, "Description": {"... (+533 chars omitted),+1 more (map truncated)
  IfcType = 166
  Joint = 0
  Length = 380
  MakeBlocks = false
  Material = -> Material003
  MoveBase = false
  MoveWithHost = false
  Normal = (0,0,0)
  OffsetFirst = 0
  OffsetSecond = 0
  PerimeterLength = 1520
  Placement = pos=(0,0,-320) rot=(0,0,1;0rad)
  PredefinedType = 0
  VerticalArea = 3.344e+06
  Width = 380
FEATURE [Part::FeaturePython] Wall317  label="Столб 002"  # Arch/BIM 166 (typed FeaturePython)
  Align = 2
  Area = 836000
  BlockHeight = 0
  BlockLength = 0
  CloneOf = -> Wall316
  CountBroken = 0
  CountEntire = 0
  Face = 0
  Height = 2200
  HorizontalArea = 144400
  IfcData = attributes={"GlobalId": {"name": "GlobalId", "type": "IfcGloballyUniqueId", "is_enum": false, "enum_values": []}, "Description": {"... (+533 chars omitted),+1 more (map truncated)
  IfcType = 166
  Joint = 0
  Length = 380
  MakeBlocks = false
  Material = -> Material003
  MoveBase = false
  MoveWithHost = false
  Normal = (0,0,0)
  OffsetFirst = 0
  OffsetSecond = 0
  PerimeterLength = 1520
  Placement = pos=(1578.42,-70.54,-320) rot=(0,0,1;0rad)
  PredefinedType = 0
  VerticalArea = 3.344e+06
  Width = 380
FEATURE [Part::FeaturePython] Wall318  label="Столб 003"  # Arch/BIM 166 (typed FeaturePython)
  Align = 2
  Area = 836000
  BlockHeight = 0
  BlockLength = 0
  CloneOf = -> Wall316
  CountBroken = 0
  CountEntire = 0
  Face = 0
  Height = 2200
  HorizontalArea = 144400
  IfcData = attributes={"GlobalId": {"name": "GlobalId", "type": "IfcGloballyUniqueId", "is_enum": false, "enum_values": []}, "Description": {"... (+533 chars omitted),+1 more (map truncated)
  IfcType = 166
  Joint = 0
  Length = 380
  MakeBlocks = false
  Material = -> Material003
  MoveBase = false
  MoveWithHost = false
  Normal = (0,0,0)
  OffsetFirst = 0
  OffsetSecond = 0
  PerimeterLength = 1520
  Placement = pos=(1818.62,5304.1,-320) rot=(0,0,1;0rad)
  PredefinedType = 0
  VerticalArea = 3.344e+06
  Width = 380
FEATURE [Part::Part2DObjectPython] Line1604  label="Калитка 001"  # Draft 2D object (typed FeaturePython)
  Area = 0
  ChamferSize = 0
  Closed = true
  End = (22834.2,-9221.45,0)
  FilletRadius = 0
  Length = 1200
  MakeFace = true
  Placement = pos=(12251.1,-7121.93,0) rot=(0,0,1;0.025758rad)
  Points = (2) [(11722.5,-2455.82,0),(10525.5,-2371.39,0)]
  Start = (24033,-9275.03,0)
  Subdivisions = 0
FEATURE [Part::FeaturePython] Wall319  label="Калитка 002"  # Arch/BIM 166 (typed FeaturePython)
  Align = 1
  Area = 2.16e+06
  Base = -> Line1604
  BlockHeight = 2000
  BlockLength = 150
  CountBroken = 8
  CountEntire = 0
  Face = 0
  Height = 1800
  HorizontalArea = 0
  IfcData = attributes={"GlobalId": {"name": "GlobalId", "type": "IfcGloballyUniqueId", "is_enum": false, "enum_values": []}, "Description": {"... (+533 chars omitted),+1 more (map truncated)
  IfcType = 166
  Joint = 10
  Length = 1200
  MakeBlocks = true
  Material = -> Material010
  MoveBase = false
  MoveWithHost = false
  Normal = (0,0,0)
  Offset = 50
  OffsetFirst = 90
  OffsetSecond = 0
  PerimeterLength = 0
  Placement = pos=(0,0,-120) rot=(0,0,1;0rad)
  PredefinedType = 0
  VerticalArea = 0
  Width = 50
FEATURE [Part::Part2DObjectPython] Wire892  # Draft 2D object (typed FeaturePython)
  Area = 0
  ChamferSize = 0
  Closed = true
  End = (22842.7,-9031.64,1880)
  FilletRadius = 0
  Length = 1520
  MakeFace = false
  Placement = pos=(22463.1,-9014.68,1880) rot=(0,0,-1;1.61546rad)
  Points = (4) [(0,0,0),(380,0,0),(380,380,0),(-1.72804e-11,380,0)]
  Start = (22463.1,-9014.68,1880)
  Subdivisions = 0
FEATURE [Part::FeaturePython] Roof018  label="Крышка столба 001"  # Arch/BIM 113 (typed FeaturePython)
  Angles = [15,15,15,15]
  Base = -> Wire892
  BorderLength = 1920
  Face = 0
  Flip = false
  Heights = [50.9103,53.5898,50.9103,53.5898]
  HorizontalArea = 230400
  IdRel = [-1,-1,-1,-1]
  IfcData = attributes={"GlobalId": {"name": "GlobalId", "type": "IfcGloballyUniqueId", "is_enum": false, "enum_values": []}, "Description": {"... (+613 chars omitted),+1 more (map truncated)
  IfcType = 113
  Material = -> Material018
  MoveBase = false
  MoveWithHost = false
  Overhang = [50,50,50,50]
  PerimeterLength = 0
  PredefinedType = 0
  RidgeLength = 1381.8
  Runs = [200,200,200,200]
  Thickness = [50,50,50,50]
  VerticalArea = 99386.5
FEATURE [Part::FeaturePython] Roof019  label="Крышка столба 002"  # Arch/BIM 113 (typed FeaturePython)
  BorderLength = 0
  CloneOf = -> Roof018
  Face = 0
  Flip = false
  HorizontalArea = 230400
  IfcData = attributes={"GlobalId": {"name": "GlobalId", "type": "IfcGloballyUniqueId", "is_enum": false, "enum_values": []}, "Description": {"... (+613 chars omitted),+1 more (map truncated)
  IfcType = 113
  Material = -> Material018
  MoveBase = false
  MoveWithHost = false
  PerimeterLength = 0
  Placement = pos=(1578.42,-70.54,0) rot=(0,0,1;0rad)
  PredefinedType = 0
  RidgeLength = 0
  Thickness = [50,50,50,50]
  VerticalArea = 99386.5
FEATURE [Part::FeaturePython] Roof020  label="Крышка столба 003"  # Arch/BIM 113 (typed FeaturePython)
  BorderLength = 0
  CloneOf = -> Roof018
  Face = 0
  Flip = false
  HorizontalArea = 230400
  IfcData = attributes={"GlobalId": {"name": "GlobalId", "type": "IfcGloballyUniqueId", "is_enum": false, "enum_values": []}, "Description": {"... (+613 chars omitted),+1 more (map truncated)
  IfcType = 113
  Material = -> Material018
  MoveBase = false
  MoveWithHost = false
  PerimeterLength = 0
  Placement = pos=(1818.62,5304.1,0) rot=(0,0,1;0rad)
  PredefinedType = 0
  RidgeLength = 0
  Thickness = [50,50,50,50]
  VerticalArea = 99386.5
FEATURE [Part::Part2DObjectPython] Rectangle3361  # Draft 2D object (typed FeaturePython)
  Area = 0
  ChamferSize = 0
  Columns = 1
  FilletRadius = 0
  Height = 8540
  Length = 20900
  MakeFace = false
  Placement = pos=(-4200,-540,0) rot=(0,0,1;0rad)
  Rows = 1
FEATURE [Part::FeaturePython] Roof021  label="Кровля 2скатн002"  # Arch/BIM 113 (typed FeaturePython)
  Angles = [35,35,35,35]
  Base = -> Rectangle3361
  BorderLength = 58880
  Face = 0
  Flip = false
  Heights = [2989.89,3150.93,2989.89,3150.93]
  HorizontalArea = 178486000
  IdRel = [-1,-1,-1,-1]
  IfcData = attributes={"GlobalId": {"name": "GlobalId", "type": "IfcGloballyUniqueId", "is_enum": false, "enum_values": []}, "Description": {"... (+613 chars omitted),+1 more (map truncated)
  IfcType = 113
  Material = -> Material007
  MoveBase = false
  MoveWithHost = false
  Overhang = [0,0,0,0]
  PerimeterLength = 0
  Placement = pos=(0,4.55e-13,3062.84) rot=(0,0,1;0rad)
  PredefinedType = 0
  RidgeLength = 39313.4
  Runs = [4500,4500,4500,4500]
  Thickness = [200,200,200,200]
  VerticalArea = 1.43758e+07
FEATURE [Part::FeaturePython] Roof022  label="roof_4_side001"  # Arch/BIM 113 (typed FeaturePython)
  Angles = [35,35,35,35]
  Base = -> Wire691
  BorderLength = 57660
  Face = 0
  Flip = false
  Heights = [3459.03,3851.14,3459.03,3851.14]
  HorizontalArea = 201366000
  IdRel = [-1,-1,-1,-1]
  IfcData = attributes={"GlobalId": {"name": "GlobalId", "type": "IfcGloballyUniqueId", "is_enum": false, "enum_values": []}, "Description": {"... (+613 chars omitted),+1 more (map truncated)
  IfcType = 113
  Material = -> Material007
  MoveBase = false
  MoveWithHost = false
  Overhang = [1000,1000,1000,1000]
  PerimeterLength = 0
  Placement = pos=(0,0,3093.7) rot=(0,0,1;0rad)
  PredefinedType = 0
  RidgeLength = 42564.8
  Runs = [5500,5500,5500,5500]
  Thickness = [200,200,200,200]
  VerticalArea = 1.4078e+07
FEATURE [Part::MultiCommon] Common035
  Shapes = -> [Roof021,Extrude108]
FEATURE [Part::MultiCommon] Common036
  Shapes = -> [Extrude,Roof022]
FEATURE [Part::Cut] Cut053  label="Объём стропилки вальмы"
  Base = -> Common036
  Tool = -> Extrude092
FEATURE [Part::Cut] Cut054  label="Объём стропилки кукушек001"
  Base = -> Common035
  Tool = -> Roof015
FEATURE [Part::Part2DObjectPython] Wire896  # Draft 2D object (typed FeaturePython)
  Area = 1.07086e+08
  ChamferSize = 0
  Closed = true
  End = (3198,-1210,0)
  FilletRadius = 0
  Length = 60784.9
  MakeFace = true
  Placement = pos=(-1230,-1210,0) rot=(0,0,1;0rad)
  Points = (14) [(0,0,0),(4940,4940,0),(3.63798e-12,9880,0),(8237,9880,0),(8237,10600,0),(13197,10600,0),(13197,9880,0),(14980,9880,0),(10040,4940,0),+5 more]
  Start = (-1230,-1210,0)
  Subdivisions = 0
FEATURE [Part::FeaturePython] Structure048  label="вычитаемый объём 001"  # Arch/BIM 52 (typed FeaturePython)
  Base = -> Wire896
  FaceMaker = 0
  Height = 5000
  HorizontalArea = 1.07086e+08
  IfcData = complex_attributes={"OwnerHistory": {}, "IsNestedBy": {}, "IsDecomposedBy": {}, "IsDefinedBy": {}, "ObjectPlacement": {}, "Representation":... (+4 chars omitted)
  IfcType = 52
  Length = 0
  MoveBase = false
  MoveWithHost = false
  Nodes = (2) [(6625,8181.9,0),(6625,8181.9,4000)]
  NodesOffset = 0
  Normal = (0,0,1)
  PerimeterLength = 60784.9
  Placement = pos=(0,0,2500) rot=(0,0,1;0rad)
  VerticalArea = 3.03924e+08
  Width = 100
FEATURE [Part::MultiCommon] Common
  Shapes = -> [Array013,Structure048]
FEATURE [Part::MultiCommon] Common037  label="Стропилка вальмы боковые скаты 001"
  Shapes = -> [Cut053,Common]
FEATURE [Part::MultiCommon] Common038  label="Стропилка кукушек004"
  Shapes = -> [Array013,Cut054]
FEATURE [Part::FeaturePython] Wall322  label="Стена029"  # Arch/BIM 166 (typed FeaturePython)
  Align = 2
  Area = 3.45422e+07
  Base = -> Line1497
  BlockHeight = 0
  BlockLength = 0
  CountBroken = 0
  CountEntire = 0
  Face = 0
  Height = 5000
  HorizontalArea = 1.03626e+06
  IfcData = attributes={"GlobalId": {"name": "GlobalId", "type": "IfcGloballyUniqueId", "is_enum": false, "enum_values": []}, "Description": {"... (+533 chars omitted),+1 more (map truncated)
  IfcType = 166
  Joint = 0
  Length = 6908.43
  MakeBlocks = false
  MoveBase = false
  MoveWithHost = false
  Normal = (0,0,0)
  OffsetFirst = 0
  OffsetSecond = 0
  PerimeterLength = 14116.9
  Placement = pos=(35.3553,-35.3553,2500) rot=(0,0,1;0rad)
  PredefinedType = 0
  VerticalArea = 7.05843e+07
  Width = 150
FEATURE [Part::FeaturePython] Wall323  label="Стена030"  # Arch/BIM 166 (typed FeaturePython)
  Align = 2
  Area = 3.45422e+07
  Base = -> Line1498
  BlockHeight = 0
  BlockLength = 0
  CountBroken = 0
  CountEntire = 0
  Face = 0
  Height = 5000
  HorizontalArea = 1.03626e+06
  IfcData = attributes={"GlobalId": {"name": "GlobalId", "type": "IfcGloballyUniqueId", "is_enum": false, "enum_values": []}, "Description": {"... (+533 chars omitted),+1 more (map truncated)
  IfcType = 166
  Joint = 0
  Length = 6908.43
  MakeBlocks = false
  MoveBase = false
  MoveWithHost = false
  Normal = (0,0,0)
  OffsetFirst = 0
  OffsetSecond = 0
  PerimeterLength = 14116.9
  Placement = pos=(35.3553,35.3553,2500) rot=(0,0,1;0rad)
  PredefinedType = 0
  VerticalArea = 7.05843e+07
  Width = 150
FEATURE [Part::FeaturePython] Wall324  label="Стена031"  # Arch/BIM 166 (typed FeaturePython)
  Align = 2
  Area = 3.45422e+07
  Base = -> Line1500
  BlockHeight = 0
  BlockLength = 0
  CountBroken = 0
  CountEntire = 0
  Face = 0
  Height = 5000
  HorizontalArea = 1.03626e+06
  IfcData = attributes={"GlobalId": {"name": "GlobalId", "type": "IfcGloballyUniqueId", "is_enum": false, "enum_values": []}, "Description": {"... (+533 chars omitted),+1 more (map truncated)
  IfcType = 166
  Joint = 0
  Length = 6908.43
  MakeBlocks = false
  MoveBase = false
  MoveWithHost = false
  Normal = (0,0,0)
  OffsetFirst = 0
  OffsetSecond = 0
  PerimeterLength = 14116.9
  Placement = pos=(-35.3553,-35.3553,2500) rot=(0,0,1;0rad)
  PredefinedType = 0
  VerticalArea = 7.05843e+07
  Width = 150
FEATURE [Part::FeaturePython] Wall325  label="Стена032"  # Arch/BIM 166 (typed FeaturePython)
  Align = 2
  Area = 3.45422e+07
  Base = -> Line1501
  BlockHeight = 0
  BlockLength = 0
  CountBroken = 0
  CountEntire = 0
  Face = 0
  Height = 5000
  HorizontalArea = 1.03626e+06
  IfcData = attributes={"GlobalId": {"name": "GlobalId", "type": "IfcGloballyUniqueId", "is_enum": false, "enum_values": []}, "Description": {"... (+533 chars omitted),+1 more (map truncated)
  IfcType = 166
  Joint = 0
  Length = 6908.43
  MakeBlocks = false
  MoveBase = false
  MoveWithHost = false
  Normal = (0,0,0)
  OffsetFirst = 0
  OffsetSecond = 0
  PerimeterLength = 14116.9
  Placement = pos=(-35.3553,35.3553,2500) rot=(0,0,1;0rad)
  PredefinedType = 0
  VerticalArea = 7.05843e+07
  Width = 150
FEATURE [Part::MultiCommon] Common040  label="Накосное стропило 004"
  Shapes = -> [Wall323,Cut053]
FEATURE [Part::MultiCommon] Common041  label="Накосное стропило 001"
  Shapes = -> [Wall322,Cut053]
FEATURE [Part::MultiCommon] Common042  label="Накосное стропило 002"
  Shapes = -> [Wall324,Cut053]
FEATURE [Part::MultiCommon] Common043  label="Накосное стропило 003"
  Shapes = -> [Wall325,Cut053]
FEATURE [Part::FeaturePython] Wall327  label="Стена034"  # Arch/BIM 166 (typed FeaturePython)
  Align = 2
  Area = 2.6417e+07
  Base = -> Line1507
  BlockHeight = 0
  BlockLength = 0
  CountBroken = 0
  CountEntire = 0
  Face = 0
  Height = 5000
  HorizontalArea = 792510
  IfcData = attributes={"GlobalId": {"name": "GlobalId", "type": "IfcGloballyUniqueId", "is_enum": false, "enum_values": []}, "Description": {"... (+533 chars omitted),+1 more (map truncated)
  IfcType = 166
  Joint = 0
  Length = 5283.4
  MakeBlocks = false
  MoveBase = false
  MoveWithHost = false
  Normal = (0,0,0)
  OffsetFirst = 0
  OffsetSecond = 0
  PerimeterLength = 10866.8
  Placement = pos=(159.099,-53.033,2500) rot=(0,0,1;0rad)
  PredefinedType = 0
  VerticalArea = 5.4334e+07
  Width = 150
FEATURE [Part::FeaturePython] Wall328  label="Стена035"  # Arch/BIM 166 (typed FeaturePython)
  Align = 2
  Area = 2.6417e+07
  Base = -> Line1506
  BlockHeight = 0
  BlockLength = 0
  CountBroken = 0
  CountEntire = 0
  Face = 0
  Height = 5000
  HorizontalArea = 792510
  IfcData = attributes={"GlobalId": {"name": "GlobalId", "type": "IfcGloballyUniqueId", "is_enum": false, "enum_values": []}, "Description": {"... (+533 chars omitted),+1 more (map truncated)
  IfcType = 166
  Joint = 0
  Length = 5283.4
  MakeBlocks = false
  MoveBase = false
  MoveWithHost = false
  Normal = (0,0,0)
  OffsetFirst = 0
  OffsetSecond = 0
  PerimeterLength = 10866.8
  Placement = pos=(159.099,53.033,2500) rot=(0,0,1;0rad)
  PredefinedType = 0
  VerticalArea = 5.4334e+07
  Width = 150
FEATURE [Part::FeaturePython] Wall329  label="Стена036"  # Arch/BIM 166 (typed FeaturePython)
  Align = 2
  Area = 2.6417e+07
  Base = -> Line1502
  BlockHeight = 0
  BlockLength = 0
  CountBroken = 0
  CountEntire = 0
  Face = 0
  Height = 5000
  HorizontalArea = 792510
  IfcData = attributes={"GlobalId": {"name": "GlobalId", "type": "IfcGloballyUniqueId", "is_enum": false, "enum_values": []}, "Description": {"... (+533 chars omitted),+1 more (map truncated)
  IfcType = 166
  Joint = 0
  Length = 5283.4
  MakeBlocks = false
  MoveBase = false
  MoveWithHost = false
  Normal = (0,0,0)
  OffsetFirst = 0
  OffsetSecond = 0
  PerimeterLength = 10866.8
  Placement = pos=(-159.099,-53.033,2500) rot=(0,0,1;0rad)
  PredefinedType = 0
  VerticalArea = 5.4334e+07
  Width = 150
FEATURE [Part::FeaturePython] Wall330  label="Стена037"  # Arch/BIM 166 (typed FeaturePython)
  Align = 2
  Area = 2.6417e+07
  Base = -> Line1503
  BlockHeight = 0
  BlockLength = 0
  CountBroken = 0
  CountEntire = 0
  Face = 0
  Height = 5000
  HorizontalArea = 792510
  IfcData = attributes={"GlobalId": {"name": "GlobalId", "type": "IfcGloballyUniqueId", "is_enum": false, "enum_values": []}, "Description": {"... (+533 chars omitted),+1 more (map truncated)
  IfcType = 166
  Joint = 0
  Length = 5283.4
  MakeBlocks = false
  MoveBase = false
  MoveWithHost = false
  Normal = (0,0,0)
  OffsetFirst = 0
  OffsetSecond = 0
  PerimeterLength = 10866.8
  Placement = pos=(-159.099,53.033,2500) rot=(0,0,1;0rad)
  PredefinedType = 0
  VerticalArea = 5.4334e+07
  Width = 150
FEATURE [Part::MultiCommon] Common046  label="Накосное стропило кукушки 001"
  Shapes = -> [Wall329,Cut053]
FEATURE [Part::MultiCommon] Common047  label="Накосное стропило кукушки 010"
  Shapes = -> [Wall330,Cut053]
FEATURE [Part::MultiCommon] Common048  label="Накосное стропило кукушки 011"
  Shapes = -> [Wall327,Cut053]
FEATURE [Part::MultiCommon] Common049  label="Накосное стропило кукушки 012"
  Shapes = -> [Wall328,Cut053]
FEATURE [Part::Part2DObjectPython] Wire897  # Draft 2D object (typed FeaturePython)
  Area = 1.44851e+07
  ChamferSize = 0
  Closed = true
  End = (2995.93,3730,0)
  FilletRadius = 0
  Length = 18376.6
  MakeFace = true
  Placement = pos=(-810,-75.926,0) rot=(0,0,1;0rad)
  Points = (3) [(0,0,0),(0,7611.85,0),(3805.93,3805.93,0)]
  Start = (-810,-75.926,0)
  Subdivisions = 0
FEATURE [Part::FeaturePython] Structure438  label="Структура"  # Arch/BIM 172 (typed FeaturePython)
  Base = -> Wire897
  FaceMaker = 0
  Height = 5000
  HorizontalArea = 1.44851e+07
  IfcData = attributes={"GlobalId": {"name": "GlobalId", "type": "IfcGloballyUniqueId", "is_enum": false, "enum_values": []}, "Description": {"... (+484 chars omitted),+1 more (map truncated)
  IfcType = 172
  Length = 0
  MoveBase = false
  MoveWithHost = false
  Nodes = (2) [(458.642,3730,0),(458.642,3730,5000)]
  NodesOffset = 0
  Normal = (0,0,1)
  PerimeterLength = 18376.6
  Placement = pos=(0,0,2500) rot=(0,0,1;0rad)
  PredefinedType = 0
  VerticalArea = 9.18832e+07
  Width = 100
FEATURE [Part::FeaturePython] Structure439  label="Структура021"  # Arch/BIM 172 (typed FeaturePython)
  CloneOf = -> Structure438
  FaceMaker = 0
  Height = 5000
  HorizontalArea = 1.44851e+07
  IfcData = attributes={"GlobalId": {"name": "GlobalId", "type": "IfcGloballyUniqueId", "is_enum": false, "enum_values": []}, "Description": {"... (+484 chars omitted),+1 more (map truncated)
  IfcType = 172
  Length = 0
  MoveBase = false
  MoveWithHost = false
  Nodes = (2) [(458.642,3730,0),(458.642,3730,5000)]
  NodesOffset = 0
  Normal = (0,0,0)
  PerimeterLength = 18376.6
  Placement = pos=(12520,7460,2500) rot=(0,0,1;3.14159rad)
  PredefinedType = 0
  VerticalArea = 9.18832e+07
  Width = 100
FEATURE [Part::MultiFuse] Fusion047
  Shapes = -> [Structure438,Structure439]
FEATURE [Part::MultiCommon] Common050  label="Стропилка кукушек001"
  Shapes = -> [Fusion047,Common038]
FEATURE [Part::Part2DObjectPython] Wire898  # Draft 2D object (typed FeaturePython)
  Area = 2.44036e+07
  ChamferSize = 0
  Closed = true
  End = (3725,3730,0)
  FilletRadius = 0
  Length = 23852.4
  MakeFace = true
  Placement = pos=(-1215,-1210,0) rot=(0,0,1;0rad)
  Points = (3) [(0,0,0),(6.82121e-13,9880,0),(4940,4940,0)]
  Start = (-1215,-1210,0)
  Subdivisions = 0
FEATURE [Part::Extrusion] Extrude099006
  Base = -> Wire898
  Dir = (0,0,1)
  DirMode = 2
  FaceMakerClass = Part::FaceMakerBullseye
  LengthFwd = 5000
  LengthRev = 0
  Placement = pos=(0,0,2500) rot=(0,0,1;0rad)
  Solid = false
  Symmetric = false
FEATURE [Part::FeaturePython] Clone  label="Extrude099007"  # Draft clone (typed FeaturePython)
  AttacherType = Attacher::AttachEngine3D
  Fuse = false
  Objects = -> [Extrude099006]
  Placement = pos=(12520,7460,2500) rot=(0,0,1;3.14159rad)
  Scale = (1,1,1)
FEATURE [Part::MultiFuse] Fusion048
  Shapes = -> [Extrude099006,Clone]
FEATURE [Part::MultiCommon] Common051
  Shapes = -> [Fusion048,Array014]
FEATURE [Part::MultiCommon] Common052
  Shapes = -> [Roof022,Common051]
FEATURE [Part::FeaturePython] Structure440  label="Стойка под конёк 001"  # Arch/BIM 172 (typed FeaturePython)
  Base = -> Rectangle3228
  FaceMaker = 0
  Height = 3220
  HorizontalArea = 22500
  IfcData = attributes={"GlobalId": {"name": "GlobalId", "type": "IfcGloballyUniqueId", "is_enum": false, "enum_values": []}, "Description": {"... (+484 chars omitted),+1 more (map truncated)
  IfcType = 172
  Length = 0
  Material = -> Material
  MoveBase = false
  MoveWithHost = false
  Nodes = (2) [(9125,3730,0),(9125,3730,3220)]
  NodesOffset = 0
  Normal = (0,0,0)
  PerimeterLength = 600
  Placement = pos=(0,0,3130) rot=(0,0,1;0rad)
  PredefinedType = 0
  VerticalArea = 1932000
  Width = 100
FEATURE [Part::FeaturePython] Structure441  label="Стойка под конёк 010"  # Arch/BIM 172 (typed FeaturePython)
  Base = -> Rectangle3227
  FaceMaker = 0
  Height = 3220
  HorizontalArea = 22500
  IfcData = attributes={"GlobalId": {"name": "GlobalId", "type": "IfcGloballyUniqueId", "is_enum": false, "enum_values": []}, "Description": {"... (+484 chars omitted),+1 more (map truncated)
  IfcType = 172
  Length = 0
  Material = -> Material
  MoveBase = false
  MoveWithHost = false
  Nodes = (2) [(3395,3730,0),(3395,3730,3220)]
  NodesOffset = 0
  Normal = (0,0,0)
  PerimeterLength = 600
  Placement = pos=(0,0,3130) rot=(0,0,1;0rad)
  PredefinedType = 0
  VerticalArea = 1932000
  Width = 100
FEATURE [Part::FeaturePython] Structure442  label="Стойка под конёк 011"  # Arch/BIM 172 (typed FeaturePython)
  Base = -> Rectangle3229
  FaceMaker = 0
  Height = 3220
  HorizontalArea = 22500
  IfcData = attributes={"GlobalId": {"name": "GlobalId", "type": "IfcGloballyUniqueId", "is_enum": false, "enum_values": []}, "Description": {"... (+484 chars omitted),+1 more (map truncated)
  IfcType = 172
  Length = 0
  Material = -> Material
  MoveBase = false
  MoveWithHost = false
  Nodes = (2) [(5165,3730,0),(5165,3730,3220)]
  NodesOffset = 0
  Normal = (0,0,0)
  PerimeterLength = 600
  Placement = pos=(0,0,3130) rot=(0,0,1;0rad)
  PredefinedType = 0
  VerticalArea = 1932000
  Width = 100
FEATURE [Part::FeaturePython] Structure443  label="Стойка под конёк 012"  # Arch/BIM 172 (typed FeaturePython)
  Base = -> Rectangle3240
  FaceMaker = 0
  Height = 3220
  HorizontalArea = 22500
  IfcData = attributes={"GlobalId": {"name": "GlobalId", "type": "IfcGloballyUniqueId", "is_enum": false, "enum_values": []}, "Description": {"... (+484 chars omitted),+1 more (map truncated)
  IfcType = 172
  Length = 0
  Material = -> Material
  MoveBase = false
  MoveWithHost = false
  Nodes = (2) [(6625,3730,0),(6625,3730,3220)]
  NodesOffset = 0
  Normal = (0,0,0)
  PerimeterLength = 600
  Placement = pos=(0,0,3130) rot=(0,0,1;0rad)
  PredefinedType = 0
  VerticalArea = 1932000
  Width = 100
FEATURE [Part::Part2DObjectPython] Rectangle3362  # Draft 2D object (typed FeaturePython)
  Area = 22500
  ChamferSize = 0
  Columns = 1
  FilletRadius = 0
  Height = 150
  Length = 150
  MakeFace = true
  Placement = pos=(-335,3655,0) rot=(0,0,1;0rad)
  Rows = 1
FEATURE [Part::Part2DObjectPython] Rectangle3363  # Draft 2D object (typed FeaturePython)
  Area = 22500
  ChamferSize = 0
  Columns = 1
  FilletRadius = 0
  Height = 150
  Length = 150
  MakeFace = true
  Placement = pos=(12705,3655,0) rot=(0,0,1;0rad)
  Rows = 1
FEATURE [Part::FeaturePython] Structure444  label="Стойка фронтона 002"  # Arch/BIM 172 (typed FeaturePython)
  Base = -> Rectangle3363
  FaceMaker = 0
  Height = 2070
  HorizontalArea = 22500
  IfcData = attributes={"GlobalId": {"name": "GlobalId", "type": "IfcGloballyUniqueId", "is_enum": false, "enum_values": []}, "Description": {"... (+484 chars omitted),+1 more (map truncated)
  IfcType = 172
  Length = 0
  Material = -> Material
  MoveBase = false
  MoveWithHost = false
  Nodes = (2) [(12780,3730,0),(12780,3730,2070)]
  NodesOffset = 0
  Normal = (0,0,0)
  PerimeterLength = 600
  Placement = pos=(0,0,3780) rot=(0,0,1;0rad)
  PredefinedType = 0
  VerticalArea = 1242000
  Width = 100
FEATURE [Part::FeaturePython] Structure445  label="Стойка фронтона 001"  # Arch/BIM 172 (typed FeaturePython)
  Base = -> Rectangle3362
  FaceMaker = 0
  Height = 2070
  HorizontalArea = 22500
  IfcData = attributes={"GlobalId": {"name": "GlobalId", "type": "IfcGloballyUniqueId", "is_enum": false, "enum_values": []}, "Description": {"... (+484 chars omitted),+1 more (map truncated)
  IfcType = 172
  Length = 0
  Material = -> Material
  MoveBase = false
  MoveWithHost = false
  Nodes = (2) [(-260,3730,0),(-260,3730,2070)]
  NodesOffset = 0
  Normal = (0,0,0)
  PerimeterLength = 600
  Placement = pos=(0,0,3780) rot=(0,0,1;0rad)
  PredefinedType = 0
  VerticalArea = 1242000
  Width = 100
FEATURE [Part::Part2DObjectPython] Line1606  # Draft 2D object (typed FeaturePython)
  Area = 0
  ChamferSize = 0
  Closed = false
  End = (12850,3730,0)
  FilletRadius = 0
  Length = 3650
  MakeFace = true
  Placement = pos=(9200,3730,0) rot=(0,0,1;0rad)
  Points = (2) [(0,0,0),(3650,0,0)]
  Start = (9200,3730,0)
  Subdivisions = 0
FEATURE [Part::FeaturePython] Wall331  label="Конёк кукушки 002"  # Arch/BIM 166 (typed FeaturePython)
  Align = 2
  Area = 730000
  Base = -> Line1606
  BlockHeight = 0
  BlockLength = 0
  CountBroken = 0
  CountEntire = 0
  Face = 0
  Height = 200
  HorizontalArea = 547500
  IfcData = attributes={"GlobalId": {"name": "GlobalId", "type": "IfcGloballyUniqueId", "is_enum": false, "enum_values": []}, "Description": {"... (+533 chars omitted),+1 more (map truncated)
  IfcType = 166
  Joint = 0
  Length = 3650
  MakeBlocks = false
  MoveBase = false
  MoveWithHost = false
  Normal = (0,0,0)
  OffsetFirst = 0
  OffsetSecond = 0
  PerimeterLength = 7600
  Placement = pos=(0,0,5850) rot=(0,0,1;0rad)
  PredefinedType = 0
  VerticalArea = 1.52e+06
  Width = 150
FEATURE [Part::FeaturePython] Wall333  label="Конёк кукушки 001"  # Arch/BIM 166 (typed FeaturePython)
  Align = 2
  Area = 730000
  BlockHeight = 0
  BlockLength = 0
  CloneOf = -> Wall331
  CountBroken = 0
  CountEntire = 0
  Face = 0
  Height = 200
  HorizontalArea = 547500
  IfcData = attributes={"GlobalId": {"name": "GlobalId", "type": "IfcGloballyUniqueId", "is_enum": false, "enum_values": []}, "Description": {"... (+533 chars omitted),+1 more (map truncated)
  IfcType = 166
  Joint = 0
  Length = 3650
  MakeBlocks = false
  MoveBase = false
  MoveWithHost = false
  Normal = (0,0,0)
  OffsetFirst = 0
  OffsetSecond = 0
  PerimeterLength = 7600
  Placement = pos=(-9530,-4.55e-13,5850) rot=(0,0,1;0rad)
  PredefinedType = 0
  VerticalArea = 1.52e+06
  Width = 150
FEATURE [Part::Part2DObjectPython] Line1607  # Draft 2D object (typed FeaturePython)
  Area = 0
  ChamferSize = 0
  Closed = true
  End = (9200,3730,0)
  FilletRadius = 0
  Length = 5880
  MakeFace = true
  Placement = pos=(9200,3730,0) rot=(0,0,1;0rad)
  Points = (2) [(-5880,0,0),(0,0,0)]
  Start = (3320,3730,0)
  Subdivisions = 0
FEATURE [Part::FeaturePython] Wall334  label="Конёк вальмы"  # Arch/BIM 166 (typed FeaturePython)
  Align = 2
  Area = 1176000
  Base = -> Line1607
  BlockHeight = 0
  BlockLength = 0
  CountBroken = 0
  CountEntire = 0
  Face = 0
  Height = 200
  HorizontalArea = 882000
  IfcData = attributes={"GlobalId": {"name": "GlobalId", "type": "IfcGloballyUniqueId", "is_enum": false, "enum_values": []}, "Description": {"... (+533 chars omitted),+1 more (map truncated)
  IfcType = 166
  Joint = 0
  Length = 5880
  MakeBlocks = false
  Material = -> Material
  MoveBase = false
  MoveWithHost = false
  Normal = (0,0,0)
  OffsetFirst = 0
  OffsetSecond = 0
  PerimeterLength = 12060
  Placement = pos=(0,0,6350) rot=(0,0,1;0rad)
  PredefinedType = 0
  VerticalArea = 2412000
  Width = 150
FEATURE [Part::Part2DObjectPython] Line1611  # Draft 2D object (typed FeaturePython)
  Area = 0
  ChamferSize = 0
  Closed = true
  End = (-335,1400,0)
  FilletRadius = 0
  Length = 4700
  MakeFace = true
  Placement = pos=(-335,7060.93,0) rot=(0,0,1;0rad)
  Points = (2) [(-9.09495e-13,-960.926,0),(-9.09495e-13,-5660.93,0)]
  Start = (-335,6100,0)
  Subdivisions = 0
FEATURE [Part::FeaturePython] Wall335  label="Стена038"  # Arch/BIM 166 (typed FeaturePython)
  Align = 1
  Area = 705000
  Base = -> Line1611
  BlockHeight = 0
  BlockLength = 0
  CountBroken = 0
  CountEntire = 0
  Face = 0
  Height = 150
  HorizontalArea = 705000
  IfcData = attributes={"GlobalId": {"name": "GlobalId", "type": "IfcGloballyUniqueId", "is_enum": false, "enum_values": []}, "Description": {"... (+533 chars omitted),+1 more (map truncated)
  IfcType = 166
  Joint = 0
  Length = 4700
  MakeBlocks = false
  MoveBase = false
  MoveWithHost = false
  Normal = (0,0,0)
  Offset = 50
  OffsetFirst = 0
  OffsetSecond = 0
  PerimeterLength = 9700
  Placement = pos=(0,0,4000) rot=(0,0,1;0rad)
  PredefinedType = 0
  VerticalArea = 1455000
  Width = 150
FEATURE [Part::Part2DObjectPython] Wire900  # Draft 2D object (typed FeaturePython)
  Area = 1.27668e+07
  ChamferSize = 0
  Closed = true
  End = (0,8000,3306.99)
  FilletRadius = 0
  Length = 18965.4
  MakeFace = true
  Placement = pos=(0,-540,3306.99) rot=(0.57735,0.57735,0.57735;2.0944rad)
  Points = (3) [(0,0,0),(4270,2989.89,0),(8540,0,0)]
  Start = (0,-540,3306.99)
  Subdivisions = 0
FEATURE [Part::Extrusion] Extrude099008  label="Extrude099010"
  Base = -> Wire900
  Dir = (1,0,0)
  DirMode = 2
  FaceMakerClass = Part::FaceMakerBullseye
  LengthFwd = 5000
  LengthRev = 0
  Placement = pos=(-2000,0,0) rot=(0,0,1;0rad)
  Solid = false
  Symmetric = false
FEATURE [Part::MultiCommon] Common053  label="Балка фронтона 002"
  Shapes = -> [Wall335,Extrude099008]
FEATURE [Part::FeaturePython] Clone002  label="Балка фронтона 001"  # Draft clone (typed FeaturePython)
  AttacherType = Attacher::AttachEngine3D
  Fuse = false
  Objects = -> [Common053]
  Placement = pos=(12520,7460,0) rot=(0,0,1;3.14159rad)
  Scale = (1,1,1)
FEATURE [Part::MultiFuse] Fusion051  label="Брус подоконный001"
  Shapes = -> [Common053,Clone002]
FEATURE [Part::Cut] Cut058  label="Стропилка вальмы боковые скаты 002"
  Base = -> Common037
  Tool = -> Wall057
FEATURE [Part::Part2DObjectPython] Line1613  # Draft 2D object (typed FeaturePython)
  Area = 0
  ChamferSize = 0
  Closed = false
  End = (3520,3730,0)
  FilletRadius = 0
  Length = 250
  MakeFace = true
  Placement = pos=(3270,3730,0) rot=(0,0,1;0rad)
  Points = (2) [(0,0,0),(250,0,0)]
  Start = (3270,3730,0)
  Subdivisions = 0
FEATURE [Part::FeaturePython] Wall336  label="Кладка под стойки 001"  # Arch/BIM 166 (typed FeaturePython)
  Align = 2
  Area = 42500
  Base = -> Line1613
  BlockHeight = 65
  BlockLength = 250
  CountBroken = 1
  CountEntire = 0
  Face = 0
  Height = 170
  HorizontalArea = 62500
  IfcData = attributes={"GlobalId": {"name": "GlobalId", "type": "IfcGloballyUniqueId", "is_enum": false, "enum_values": []}, "Description": {"... (+533 chars omitted),+1 more (map truncated)
  IfcType = 166
  Joint = 12000
  Length = 250
  MakeBlocks = false
  Material = -> Material019
  MoveBase = false
  MoveWithHost = false
  Normal = (0,0,0)
  OffsetFirst = 120
  OffsetSecond = 200
  PerimeterLength = 1000
  Placement = pos=(0,0,2960) rot=(0,0,1;0rad)
  PredefinedType = 0
  VerticalArea = 170000
  Width = 250
FEATURE [Part::Part2DObjectPython] Line1614  # Draft 2D object (typed FeaturePython)
  Area = 0
  ChamferSize = 0
  Closed = false
  End = (6750,3730,0)
  FilletRadius = 0
  Length = 250
  MakeFace = true
  Placement = pos=(6500,3730,0) rot=(0,0,1;0rad)
  Points = (2) [(0,0,0),(250,0,0)]
  Start = (6500,3730,0)
  Subdivisions = 0
FEATURE [Part::FeaturePython] Wall337  label="Кладка под стойки 002"  # Arch/BIM 166 (typed FeaturePython)
  Align = 2
  Area = 42500
  Base = -> Line1614
  BlockHeight = 65
  BlockLength = 250
  CountBroken = 1
  CountEntire = 0
  Face = 0
  Height = 170
  HorizontalArea = 62500
  IfcData = attributes={"GlobalId": {"name": "GlobalId", "type": "IfcGloballyUniqueId", "is_enum": false, "enum_values": []}, "Description": {"... (+533 chars omitted),+1 more (map truncated)
  IfcType = 166
  Joint = 12000
  Length = 250
  MakeBlocks = false
  Material = -> Material019
  MoveBase = false
  MoveWithHost = false
  Normal = (0,0,0)
  OffsetFirst = 120
  OffsetSecond = 200
  PerimeterLength = 1000
  Placement = pos=(0,0,2960) rot=(0,0,1;0rad)
  PredefinedType = 0
  VerticalArea = 170000
  Width = 250
FEATURE [Part::Part2DObjectPython] Line1615  # Draft 2D object (typed FeaturePython)
  Area = 0
  ChamferSize = 0
  Closed = false
  End = (5290,3730,0)
  FilletRadius = 0
  Length = 250
  MakeFace = true
  Placement = pos=(5040,3730,0) rot=(0,0,1;0rad)
  Points = (2) [(0,0,0),(250,0,0)]
  Start = (5040,3730,0)
  Subdivisions = 0
FEATURE [Part::FeaturePython] Wall338  label="Кладка под стойки 003"  # Arch/BIM 166 (typed FeaturePython)
  Align = 2
  Area = 42500
  Base = -> Line1615
  BlockHeight = 65
  BlockLength = 250
  CountBroken = 1
  CountEntire = 0
  Face = 0
  Height = 170
  HorizontalArea = 62500
  IfcData = attributes={"GlobalId": {"name": "GlobalId", "type": "IfcGloballyUniqueId", "is_enum": false, "enum_values": []}, "Description": {"... (+533 chars omitted),+1 more (map truncated)
  IfcType = 166
  Joint = 12000
  Length = 250
  MakeBlocks = false
  Material = -> Material019
  MoveBase = false
  MoveWithHost = false
  Normal = (0,0,0)
  OffsetFirst = 120
  OffsetSecond = 200
  PerimeterLength = 1000
  Placement = pos=(0,0,2960) rot=(0,0,1;0rad)
  PredefinedType = 0
  VerticalArea = 170000
  Width = 250
FEATURE [Part::Part2DObjectPython] Line1616  # Draft 2D object (typed FeaturePython)
  Area = 0
  ChamferSize = 0
  Closed = false
  End = (9250,3730,0)
  FilletRadius = 0
  Length = 250
  MakeFace = true
  Placement = pos=(9000,3730,0) rot=(0,0,1;0rad)
  Points = (2) [(0,0,0),(250,0,0)]
  Start = (9000,3730,0)
  Subdivisions = 0
FEATURE [Part::FeaturePython] Wall339  label="Кладка под стойки 004"  # Arch/BIM 166 (typed FeaturePython)
  Align = 2
  Area = 42500
  Base = -> Line1616
  BlockHeight = 65
  BlockLength = 250
  CountBroken = 1
  CountEntire = 0
  Face = 0
  Height = 170
  HorizontalArea = 62500
  IfcData = attributes={"GlobalId": {"name": "GlobalId", "type": "IfcGloballyUniqueId", "is_enum": false, "enum_values": []}, "Description": {"... (+533 chars omitted),+1 more (map truncated)
  IfcType = 166
  Joint = 12000
  Length = 250
  MakeBlocks = false
  Material = -> Material019
  MoveBase = false
  MoveWithHost = false
  Normal = (0,0,0)
  OffsetFirst = 120
  OffsetSecond = 200
  PerimeterLength = 1000
  Placement = pos=(0,0,2960) rot=(0,0,1;0rad)
  PredefinedType = 0
  VerticalArea = 170000
  Width = 250
FEATURE [Part::Part2DObjectPython] Wire901  label="Стропильная нога 200х50х6000 001"  # Draft 2D object (typed FeaturePython)
  Area = 1.17137e+06
  ChamferSize = 0
  Closed = true
  End = (0,3730,6552.73)
  FilletRadius = 0
  Length = 12171.8
  MakeFace = true
  Placement = pos=(0,3730,6796.88) rot=(0.57735,0.57735,0.57735;2.0944rad)
  Points = (5) [(0,0,0),(4870,-3410.01,0),(4870,-3496.88,0),(4645.37,-3496.88,0),(0,-244.155,0)]
  Start = (0,3730,6796.88)
  Subdivisions = 0
FEATURE [Part::Extrusion] Extrude099009  label="Extrude099011"
  Base = -> Wire901
  Dir = (1,0,0)
  DirMode = 2
  FaceMakerClass = Part::FaceMakerBullseye
  LengthFwd = 15000
  LengthRev = 0
  Placement = pos=(-1300,0,0) rot=(0,0,1;0rad)
  Solid = false
  Symmetric = false
FEATURE [Part::Mirroring] mirror  label="Extrude099011 (mirrored)"
  Base = (-1300,3730,0)
  Normal = (1e-16,-1,0)
  Source = -> Extrude099009
FEATURE [Part::MultiFuse] Fusion052  label="Объём стропильных ног 6м 001"
  Shapes = -> [Extrude099009,mirror]
FEATURE [Part::Extrusion] Extrude099010  label="Extrude099012"
  Base = -> Wire901
  Dir = (1,0,0)
  DirMode = 2
  FaceMakerClass = Part::FaceMakerBullseye
  LengthFwd = 10000
  LengthRev = 0
  Placement = pos=(7440,-1270,9.09e-13) rot=(0,0,1;1.5708rad)
  Solid = false
  Symmetric = false
FEATURE [Part::Mirroring] mirror001  label="Extrude099012 (mirrored)"
  Base = (6200,11400,0)
  Normal = (-1,1e-16,0)
  Placement = pos=(120,-2.774e-11,0) rot=(0,0,1;0rad)
  Source = -> Extrude099010
FEATURE [Part::MultiFuse] Fusion053  label="Объём стропильных ног 6м 002"
  Shapes = -> [mirror001,Extrude099010]
FEATURE [Part::MultiFuse] Fusion054  label="Накосные стропила 001"
  Shapes = -> [Common041,Common042,Common043,Common040]
FEATURE [Part::MultiCommon] Common055  label="Стропилка вальмы боковые скаты 003"
  Shapes = -> [Fusion052,Cut058]
FEATURE [Part::MultiFuse] Fusion055
  Shapes = -> [Fusion052,Fusion053]
FEATURE [Part::Part2DObjectPython] Line1626  # Draft 2D object (typed FeaturePython)
  Area = 0
  ChamferSize = 0
  Closed = false
  End = (3200,-1930,0)
  FilletRadius = 0
  Length = 2
  MakeFace = true
  Placement = pos=(3198,-1930,0) rot=(0,0,1;0rad)
  Points = (2) [(0,0,0),(2,0,0)]
  Start = (3198,-1930,0)
  Subdivisions = 0
FEATURE [Part::MultiCommon] Common056  label="Накосные стропила001"
  Shapes = -> [Fusion055,Fusion054]
FEATURE [Part::Part2DObjectPython] Rectangle3364  # Draft 2D object (typed FeaturePython)
  Area = 1.119e+07
  ChamferSize = 0
  Columns = 1
  FilletRadius = 0
  Height = 1865
  Length = 6000
  MakeFace = true
  Placement = pos=(3198,-1930,0) rot=(0,0,1;0rad)
  Rows = 1
FEATURE [Part::Part2DObjectPython] Rectangle3365  # Draft 2D object (typed FeaturePython)
  Area = 9.2504e+06
  ChamferSize = 0
  Columns = 1
  FilletRadius = 0
  Height = 1865
  Length = 4960
  MakeFace = true
  Placement = pos=(7007,7525,0) rot=(0,0,1;0rad)
  Rows = 1
FEATURE [Part::Extrusion] Extrude099011  label="Extrude099013"
  Base = -> Rectangle3364
  Dir = (0,0,1)
  DirMode = 2
  FaceMakerClass = Part::FaceMakerBullseye
  LengthFwd = 5000
  LengthRev = 0
  Placement = pos=(0,0,2000) rot=(0,0,1;0rad)
  Solid = false
  Symmetric = false
FEATURE [Part::Extrusion] Extrude099012  label="Extrude099014"
  Base = -> Rectangle3365
  Dir = (0,0,1)
  DirMode = 2
  FaceMakerClass = Part::FaceMakerBullseye
  LengthFwd = 5000
  LengthRev = 0
  Placement = pos=(0,0,2000) rot=(0,0,1;0rad)
  Solid = false
  Symmetric = false
FEATURE [Part::Part2DObjectPython] Rectangle3366  # Draft 2D object (typed FeaturePython)
  Area = 0
  ChamferSize = 0
  Columns = 1
  FilletRadius = 0
  Height = 1130
  Length = 1110
  MakeFace = false
  Placement = pos=(8540,1305,0) rot=(0,0,1;0rad)
  Rows = 1
FEATURE [Part::Extrusion] Extrude099013  label="Extrude099015"
  Base = -> Rectangle3366
  Dir = (0,0,1)
  DirMode = 2
  FaceMakerClass = Part::FaceMakerBullseye
  LengthFwd = 5000
  LengthRev = 0
  Placement = pos=(0,0,2500) rot=(0,0,1;0rad)
  Solid = true
  Symmetric = false
FEATURE [Part::FeaturePython] Wall340  label="Стена039"  # Arch/BIM 166 (typed FeaturePython)
  Align = 0
  Area = 13440000
  Base = -> Rectangle3366
  BlockHeight = 0
  BlockLength = 0
  CountBroken = 0
  CountEntire = 0
  Face = 0
  Height = 3000
  HorizontalArea = 234000
  IfcData = attributes={"GlobalId": {"name": "GlobalId", "type": "IfcGloballyUniqueId", "is_enum": false, "enum_values": []}, "Description": {"... (+533 chars omitted),+1 more (map truncated)
  IfcType = 166
  Joint = 0
  Length = 4480
  MakeBlocks = false
  MoveBase = false
  MoveWithHost = false
  Normal = (0,0,0)
  OffsetFirst = 0
  OffsetSecond = 0
  PerimeterLength = 4880
  Placement = pos=(0,0,4000) rot=(0,0,1;0rad)
  PredefinedType = 0
  VerticalArea = 28080000
  Width = 50
FEATURE [Part::Cut] Cut059  label="Стропилка вальмы боковые скаты 004"
  Base = -> Common055
  Tool = -> Extrude099013
FEATURE [Part::MultiCommon] Common060  label="Проход вентстояка001"
  Shapes = -> [Cut053,Wall340]
FEATURE [Part::Part2DObjectPython] Rectangle3367  # Draft 2D object (typed FeaturePython)
  Area = 15000
  ChamferSize = 0
  Columns = 1
  FilletRadius = 0
  Height = 100
  Length = 150
  MakeFace = true
  Placement = pos=(410.619,455.619,0) rot=(0,0,1;0rad)
  Rows = 1
FEATURE [Part::FeaturePython] Structure446  label="Стойка прогона"  # Arch/BIM 172 (typed FeaturePython)
  Base = -> Rectangle3367
  FaceMaker = 0
  Height = 1050
  HorizontalArea = 15000
  IfcData = attributes={"GlobalId": {"name": "GlobalId", "type": "IfcGloballyUniqueId", "is_enum": false, "enum_values": []}, "Description": {"... (+484 chars omitted),+1 more (map truncated)
  IfcType = 172
  Length = 0
  MoveBase = false
  MoveWithHost = false
  Nodes = (2) [(12780,3730,0),(12780,3730,2100)]
  NodesOffset = 0
  Normal = (0,0,0)
  PerimeterLength = 500
  Placement = pos=(0,0,3100) rot=(0,0,1;0rad)
  PredefinedType = 0
  VerticalArea = 525000
  Width = 100
FEATURE [Part::Part2DObjectPython] Line1646  # Draft 2D object (typed FeaturePython)
  Area = 0
  ChamferSize = 0
  Closed = false
  End = (610.619,505.619,0)
  FilletRadius = 0
  Length = 250
  MakeFace = true
  Placement = pos=(360.619,505.619,0) rot=(0,0,1;0rad)
  Points = (2) [(0,0,0),(250,0,0)]
  Start = (360.619,505.619,0)
  Subdivisions = 0
FEATURE [Part::FeaturePython] Wall341  label="Кладка под стойки 005"  # Arch/BIM 166 (typed FeaturePython)
  Align = 2
  Area = 42500
  Base = -> Line1646
  BlockHeight = 65
  BlockLength = 250
  CountBroken = 1
  CountEntire = 0
  Face = 0
  Height = 170
  HorizontalArea = 62500
  IfcData = attributes={"GlobalId": {"name": "GlobalId", "type": "IfcGloballyUniqueId", "is_enum": false, "enum_values": []}, "Description": {"... (+533 chars omitted),+1 more (map truncated)
  IfcType = 166
  Joint = 12000
  Length = 250
  MakeBlocks = false
  Material = -> Material019
  MoveBase = false
  MoveWithHost = false
  Normal = (0,0,0)
  OffsetFirst = 120
  OffsetSecond = 200
  PerimeterLength = 1000
  Placement = pos=(0,0,2960) rot=(0,0,1;0rad)
  PredefinedType = 0
  VerticalArea = 170000
  Width = 250
FEATURE [Part::FeaturePython] Array066  # Draft array (typed FeaturePython)
  Angle = 360
  ArrayType = 0
  Axis = (0,0,1)
  Base = -> Structure446
  Center = (0,0,0)
  Count = 5
  ExpandArray = false
  Fuse = false
  IntervalAxis = (0,0,0)
  IntervalX = (2880,0,0)
  IntervalY = (0,0,0)
  IntervalZ = (0,0,0)
  NumberCircles = 3
  NumberPolar = 5
  NumberX = 5
  NumberY = 1
  NumberZ = 1
  PlacementList = 5 placements: arithmetic series from (0,0,3100) step (2880,0,0) to (11520,0,3100)
  RadialDistance = 50
  ScaleList = (5) [(1,1,1),(1,1,1),(1,1,1),(1,1,1),(1,1,1)]
  Symmetry = 1
  TangentialDistance = 25
FEATURE [Part::FeaturePython] Array067  # Draft array (typed FeaturePython)
  Angle = 360
  ArrayType = 0
  Axis = (0,0,1)
  Base = -> Wall341
  Center = (0,0,0)
  Count = 5
  ExpandArray = false
  Fuse = false
  IntervalAxis = (0,0,0)
  IntervalX = (2880,0,0)
  IntervalY = (0,100,0)
  IntervalZ = (0,0,100)
  NumberCircles = 3
  NumberPolar = 5
  NumberX = 5
  NumberY = 1
  NumberZ = 1
  PlacementList = 5 placements: arithmetic series from (0,0,2960) step (2880,0,0) to (11520,0,2960)
  RadialDistance = 50
  ScaleList = (5) [(1,1,1),(1,1,1),(1,1,1),(1,1,1),(1,1,1)]
  Symmetry = 1
  TangentialDistance = 25
FEATURE [Part::Part2DObjectPython] Line1650  # Draft 2D object (typed FeaturePython)
  Area = 0
  ChamferSize = 0
  Closed = false
  End = (12080.6,505.619,0)
  FilletRadius = 0
  Length = 11670
  MakeFace = true
  Placement = pos=(410.619,505.619,0) rot=(0,0,1;0rad)
  Points = (2) [(0,0,0),(11670,1.7053e-13,0)]
  Start = (410.619,505.619,0)
  Subdivisions = 0
FEATURE [Part::FeaturePython] Wall342  label="Стена040"  # Arch/BIM 166 (typed FeaturePython)
  Align = 2
  Area = 1750500
  Base = -> Line1650
  BlockHeight = 0
  BlockLength = 0
  CountBroken = 0
  CountEntire = 0
  Face = 0
  Height = 150
  HorizontalArea = 1.167e+06
  IfcData = attributes={"GlobalId": {"name": "GlobalId", "type": "IfcGloballyUniqueId", "is_enum": false, "enum_values": []}, "Description": {"... (+533 chars omitted),+1 more (map truncated)
  IfcType = 166
  Joint = 0
  Length = 11670
  MakeBlocks = false
  Material = -> Material
  MoveBase = false
  MoveWithHost = false
  Normal = (0,0,0)
  OffsetFirst = 0
  OffsetSecond = 0
  PerimeterLength = 23540
  Placement = pos=(0,0,4150) rot=(0,0,1;0rad)
  PredefinedType = 0
  VerticalArea = 3531000
  Width = 100
FEATURE [Part::Mirroring] mirror002  label="Стена040 (mirrored)"
  Base = (3710,3730,0)
  Normal = (-1e-16,-1,0)
  Source = -> Wall342
FEATURE [Part::MultiFuse] Fusion057  label="Прогоны подстропильные002"
  Shapes = -> [Wall342,mirror002]
FEATURE [Part::FeaturePython] Array068  # Draft array (typed FeaturePython)
  Angle = 360
  ArrayType = 0
  Axis = (0,0,1)
  Base = -> Structure446
  Center = (0,0,0)
  Count = 5
  ExpandArray = false
  Fuse = false
  IntervalAxis = (0,0,0)
  IntervalX = (2880,0,0)
  IntervalY = (0,0,0)
  IntervalZ = (0,0,0)
  NumberCircles = 3
  NumberPolar = 5
  NumberX = 5
  NumberY = 1
  NumberZ = 1
  Placement = pos=(0,6448.76,0) rot=(0,0,1;0rad)
  PlacementList = 5 placements: arithmetic series from (0,0,3100) step (2880,0,0) to (11520,0,3100)
  RadialDistance = 50
  ScaleList = (5) [(1,1,1),(1,1,1),(1,1,1),(1,1,1),(1,1,1)]
  Symmetry = 1
  TangentialDistance = 25
FEATURE [Part::FeaturePython] Array069  # Draft array (typed FeaturePython)
  Angle = 360
  ArrayType = 0
  Axis = (0,0,1)
  Base = -> Wall341
  Center = (0,0,0)
  Count = 5
  ExpandArray = false
  Fuse = false
  IntervalAxis = (0,0,0)
  IntervalX = (2880,0,0)
  IntervalY = (0,100,0)
  IntervalZ = (0,0,100)
  NumberCircles = 3
  NumberPolar = 5
  NumberX = 5
  NumberY = 1
  NumberZ = 1
  Placement = pos=(0,6448.76,0) rot=(0,0,1;0rad)
  PlacementList = 5 placements: arithmetic series from (0,0,2960) step (2880,0,0) to (11520,0,2960)
  RadialDistance = 50
  ScaleList = (5) [(1,1,1),(1,1,1),(1,1,1),(1,1,1),(1,1,1)]
  Symmetry = 1
  TangentialDistance = 25
FEATURE [Part::FeaturePython] Component115  label="Кладка под стойки 006"  # Arch/BIM 0 (typed FeaturePython)
  Base = -> Array069
  HorizontalArea = 0
  IfcData = attributes={"GlobalId": {"name": "GlobalId", "type": "IfcGloballyUniqueId", "is_enum": false, "enum_values": []}, "Description": {"... (+538 chars omitted),+1 more (map truncated)
  IfcType = 0
  Material = -> Material019
  MoveBase = false
  MoveWithHost = false
  PerimeterLength = 0
  Placement = pos=(0,6448.76,0) rot=(0,0,1;0rad)
  PredefinedType = 0
  VerticalArea = 0
FEATURE [Part::FeaturePython] Component116  label="Кладка под стойки 007"  # Arch/BIM 0 (typed FeaturePython)
  Base = -> Array067
  HorizontalArea = 0
  IfcData = attributes={"GlobalId": {"name": "GlobalId", "type": "IfcGloballyUniqueId", "is_enum": false, "enum_values": []}, "Description": {"... (+538 chars omitted),+1 more (map truncated)
  IfcType = 0
  Material = -> Material019
  MoveBase = false
  MoveWithHost = false
  PerimeterLength = 0
  PredefinedType = 0
  VerticalArea = 0
FEATURE [Part::Part2DObjectPython] Rectangle3368  # Draft 2D object (typed FeaturePython)
  Area = 22500
  ChamferSize = 0
  Columns = 1
  FilletRadius = 0
  Height = 150
  Length = 150
  MakeFace = true
  Placement = pos=(-335,5740,0) rot=(0,0,1;0rad)
  Rows = 1
FEATURE [Part::FeaturePython] Structure447  label="Стойка фронтона 003"  # Arch/BIM 172 (typed FeaturePython)
  Base = -> Rectangle3368
  FaceMaker = 0
  Height = 1000
  HorizontalArea = 22500
  IfcData = attributes={"GlobalId": {"name": "GlobalId", "type": "IfcGloballyUniqueId", "is_enum": false, "enum_values": []}, "Description": {"... (+484 chars omitted),+1 more (map truncated)
  IfcType = 172
  Length = 0
  Material = -> Material
  MoveBase = false
  MoveWithHost = false
  Nodes = (2) [(-260,3730,0),(-260,3730,2100)]
  NodesOffset = 0
  Normal = (0,0,0)
  PerimeterLength = 600
  Placement = pos=(0,0,3780) rot=(0,0,1;0rad)
  PredefinedType = 0
  VerticalArea = 600000
  Width = 100
FEATURE [Part::Part2DObjectPython] Rectangle3369  # Draft 2D object (typed FeaturePython)
  Area = 22500
  ChamferSize = 0
  Columns = 1
  FilletRadius = 0
  Height = 150
  Length = 150
  MakeFace = true
  Placement = pos=(-335,1565,0) rot=(0,0,1;0rad)
  Rows = 1
FEATURE [Part::FeaturePython] Structure448  label="Стойка фронтона 004"  # Arch/BIM 172 (typed FeaturePython)
  Base = -> Rectangle3369
  FaceMaker = 0
  Height = 1000
  HorizontalArea = 22500
  IfcData = attributes={"GlobalId": {"name": "GlobalId", "type": "IfcGloballyUniqueId", "is_enum": false, "enum_values": []}, "Description": {"... (+484 chars omitted),+1 more (map truncated)
  IfcType = 172
  Length = 0
  Material = -> Material
  MoveBase = false
  MoveWithHost = false
  Nodes = (2) [(-260,3730,0),(-260,3730,2100)]
  NodesOffset = 0
  Normal = (0,0,0)
  PerimeterLength = 600
  Placement = pos=(0,0,3780) rot=(0,0,1;0rad)
  PredefinedType = 0
  VerticalArea = 600000
  Width = 100
FEATURE [Part::Part2DObjectPython] Rectangle3370  # Draft 2D object (typed FeaturePython)
  Area = 22500
  ChamferSize = 0
  Columns = 1
  FilletRadius = 0
  Height = 150
  Length = 150
  MakeFace = true
  Placement = pos=(12705,5740,0) rot=(0,0,1;0rad)
  Rows = 1
FEATURE [Part::FeaturePython] Structure449  label="Стойка фронтона 005"  # Arch/BIM 172 (typed FeaturePython)
  Base = -> Rectangle3370
  FaceMaker = 0
  Height = 1000
  HorizontalArea = 22500
  IfcData = attributes={"GlobalId": {"name": "GlobalId", "type": "IfcGloballyUniqueId", "is_enum": false, "enum_values": []}, "Description": {"... (+484 chars omitted),+1 more (map truncated)
  IfcType = 172
  Length = 0
  Material = -> Material
  MoveBase = false
  MoveWithHost = false
  Nodes = (2) [(-260,3730,0),(-260,3730,2100)]
  NodesOffset = 0
  Normal = (0,0,0)
  PerimeterLength = 600
  Placement = pos=(0,0,3780) rot=(0,0,1;0rad)
  PredefinedType = 0
  VerticalArea = 600000
  Width = 100
FEATURE [Part::Part2DObjectPython] Rectangle3371  # Draft 2D object (typed FeaturePython)
  Area = 22500
  ChamferSize = 0
  Columns = 1
  FilletRadius = 0
  Height = 150
  Length = 150
  MakeFace = true
  Placement = pos=(12705,1565,0) rot=(0,0,1;0rad)
  Rows = 1
FEATURE [Part::FeaturePython] Structure450  label="Стойка фронтона 006"  # Arch/BIM 172 (typed FeaturePython)
  Base = -> Rectangle3371
  FaceMaker = 0
  Height = 1000
  HorizontalArea = 22500
  IfcData = attributes={"GlobalId": {"name": "GlobalId", "type": "IfcGloballyUniqueId", "is_enum": false, "enum_values": []}, "Description": {"... (+484 chars omitted),+1 more (map truncated)
  IfcType = 172
  Length = 0
  Material = -> Material
  MoveBase = false
  MoveWithHost = false
  Nodes = (2) [(-260,3730,0),(-260,3730,2100)]
  NodesOffset = 0
  Normal = (0,0,0)
  PerimeterLength = 600
  Placement = pos=(0,0,3780) rot=(0,0,1;0rad)
  PredefinedType = 0
  VerticalArea = 600000
  Width = 100
FEATURE [App::GeometryPython] BuildingPart111  label="Стойки фронтонов"  # Arch/BIM 172 (typed FeaturePython)
  Area = 0
  Group = -> [Structure444,Structure445,Structure447,Structure448,Structure449,Structure450]
  Height = 0
  HeightPropagate = true
  IfcData = attributes={"GlobalId": {"name": "GlobalId", "type": "IfcGloballyUniqueId", "is_enum": false, "enum_values": []}, "Description": {"... (+484 chars omitted),+1 more (map truncated)
  IfcType = 172
  LevelOffset = 0
  Placement = pos=(0,0,3780) rot=(0,0,1;0rad)
  PredefinedType = 0
FEATURE [Part::Part2DObjectPython] Rectangle3372  # Draft 2D object (typed FeaturePython)
  Area = 28910000
  ChamferSize = 0
  Columns = 1
  FilletRadius = 0
  Height = 5900
  Length = 4900
  MakeFace = true
  Placement = pos=(3800,780,0) rot=(0,0,1;0rad)
  Rows = 1
FEATURE [Part::Extrusion] Extrude099014  label="Extrude099016"
  Base = -> Rectangle3372
  Dir = (0,0,1)
  DirMode = 2
  FaceMakerClass = Part::FaceMakerBullseye
  LengthFwd = 200
  LengthRev = 0
  Placement = pos=(0,0,5880) rot=(0,0,1;0rad)
  Solid = false
  Symmetric = false
FEATURE [Part::FeaturePython] Structure451  label="Балка крыльца 002"  # Arch/BIM 7 (typed FeaturePython)
  FaceMaker = 0
  Height = 100
  HorizontalArea = 0
  IfcData = attributes={"GlobalId": {"name": "GlobalId", "type": "IfcGloballyUniqueId", "is_enum": false, "enum_values": []}, "Description": {"... (+475 chars omitted),+1 more (map truncated)
  IfcType = 7
  Length = 5900
  Material = -> Material
  MoveBase = false
  MoveWithHost = false
  Nodes = (2) [(0,-1.42109e-15,-1.94289e-16),(5900,-1.42109e-15,1.30987e-12)]
  NodesOffset = 0
  Normal = (0,0,0)
  PerimeterLength = 0
  Placement = pos=(3264,-1456.07,2930.06) rot=(1,0,0;0.610865rad)
  PredefinedType = 0
  VerticalArea = 30000
  Width = 150
FEATURE [Part::MultiCommon] Common061
  Shapes = -> [Extrude099011,Array013]
FEATURE [Part::MultiCommon] Common062
  Shapes = -> [Extrude099012,Array013]
FEATURE [Part::MultiCommon] Common063
  Shapes = -> [Extrude099014,Array013]
FEATURE [Part::MultiCommon] Common064
  Shapes = -> [Common063,Roof015]
FEATURE [Part::MultiCommon] Common065
  Shapes = -> [Cut053,Common063]
FEATURE [Part::MultiFuse] Fusion058  label="Затяжки 001"
  Placement = pos=(-50,0,0) rot=(0,0,1;0rad)
  Shapes = -> [Common065,Common064]
FEATURE [Part::MultiCommon] Common066  label="Кобылки навеса 002"
  Placement = pos=(-50,0,0) rot=(0,0,1;0rad)
  Shapes = -> [Cut053,Common061]
FEATURE [Part::MultiCommon] Common067  label="Кобылки навеса 001"
  Placement = pos=(50,0,0) rot=(0,0,1;0rad)
  Shapes = -> [Cut053,Common062]
FEATURE [Part::FeaturePython] Structure452  label="Балка крыльца 001"  # Arch/BIM 7 (typed FeaturePython)
  FaceMaker = 0
  Height = 100
  HorizontalArea = 0
  IfcData = attributes={"GlobalId": {"name": "GlobalId", "type": "IfcGloballyUniqueId", "is_enum": false, "enum_values": []}, "Description": {"... (+475 chars omitted),+1 more (map truncated)
  IfcType = 7
  Length = 4900
  Material = -> Material
  MoveBase = false
  MoveWithHost = false
  Nodes = (2) [(0,-1.42109e-15,-1.94289e-16),(4900,-1.42109e-15,1.08782e-12)]
  NodesOffset = 0
  Normal = (0,0,0)
  PerimeterLength = 0
  Placement = pos=(12025,8916.07,2930.06) rot=(0,0.300706,0.953717;3.14159rad)
  PredefinedType = 0
  VerticalArea = 30000
  Width = 150
FEATURE [App::GeometryPython] BuildingPart101  label="Элементы арх.декора001"  # Arch/BIM 52 (typed FeaturePython)
  Area = 0
  GlobalId = 1dA3$MPA5FehwTwOMwm9Bl
  Group = -> [Structure413,Structure414,Structure415,Structure416,Structure417,Structure420,Component002,Component,Component001,Component003,Structure451,Structure452,Structure424,Structure433]
  Height = 0
  HeightPropagate = true
  IfcData = IfcUID=1dA3$MPA5FehwTwOMwm9Bl,+2 more (map truncated)
  IfcType = 52
  LevelOffset = 0
FEATURE [Part::Part2DObjectPython] Wire902  # Draft 2D object (typed FeaturePython)
  Area = 2.1695e+07
  ChamferSize = 0
  Closed = true
  End = (310,315,0)
  FilletRadius = 0
  Length = 19422
  MakeFace = true
  Placement = pos=(-1160,315,0) rot=(0,0,1;0rad)
  Points = (5) [(0,0,0),(1.59162e-12,6825,0),(1475,6825,0),(4885,3415,0),(1470,-1.36424e-12,0)]
  Start = (-1160,315,0)
  Subdivisions = 0
FEATURE [Part::Extrusion] Extrude099015  label="Extrude099017"
  Base = -> Wire902
  Dir = (0,0,1)
  DirMode = 2
  FaceMakerClass = Part::FaceMakerBullseye
  LengthFwd = 5000
  LengthRev = 0
  Placement = pos=(0,0,2500) rot=(0,0,1;0rad)
  Solid = false
  Symmetric = false
FEATURE [Part::Mirroring] mirror003  label="Extrude099017 (mirrored)"
  Base = (6260,3680,0)
  Normal = (1,0,0)
  Source = -> Extrude099015
FEATURE [Part::MultiFuse] Fusion060
  Shapes = -> [mirror003,Extrude099015]
FEATURE [Part::Part2DObjectPython] Rectangle3377  # Draft 2D object (typed FeaturePython)
  Area = 22500
  ChamferSize = 0
  Columns = 1
  FilletRadius = 0
  Height = 150
  Length = 150
  MakeFace = true
  Placement = pos=(8240,3655,0) rot=(0,0,1;0rad)
  Rows = 1
FEATURE [Part::FeaturePython] Structure457  label="Стойка под конёк 013"  # Arch/BIM 172 (typed FeaturePython)
  Base = -> Rectangle3377
  FaceMaker = 0
  Height = 3220
  HorizontalArea = 22500
  IfcData = attributes={"GlobalId": {"name": "GlobalId", "type": "IfcGloballyUniqueId", "is_enum": false, "enum_values": []}, "Description": {"... (+484 chars omitted),+1 more (map truncated)
  IfcType = 172
  Length = 0
  Material = -> Material
  MoveBase = false
  MoveWithHost = false
  Nodes = (2) [(8315,3730,0),(8315,3730,3220)]
  NodesOffset = 0
  Normal = (0,0,0)
  PerimeterLength = 600
  Placement = pos=(0,0,3130) rot=(0,0,1;0rad)
  PredefinedType = 0
  VerticalArea = 1932000
  Width = 100
FEATURE [App::GeometryPython] BuildingPart112  label="Стойки конька"  # Arch/BIM 172 (typed FeaturePython)
  Area = 0
  Group = -> [Structure440,Structure441,Structure442,Structure443,Structure457]
  Height = 0
  HeightPropagate = true
  IfcData = attributes={"GlobalId": {"name": "GlobalId", "type": "IfcGloballyUniqueId", "is_enum": false, "enum_values": []}, "Description": {"... (+484 chars omitted),+1 more (map truncated)
  IfcType = 172
  LevelOffset = 0
  Placement = pos=(0,0,3130) rot=(0,0,1;0rad)
  PredefinedType = 0
FEATURE [Part::Part2DObjectPython] Line1653  # Draft 2D object (typed FeaturePython)
  Area = 0
  ChamferSize = 0
  Closed = false
  End = (8440,3730,0)
  FilletRadius = 0
  Length = 250
  MakeFace = true
  Placement = pos=(8190,3730,0) rot=(0,0,1;0rad)
  Points = (2) [(0,0,0),(250,0,0)]
  Start = (8190,3730,0)
  Subdivisions = 0
FEATURE [Part::FeaturePython] Wall343  label="Кладка под стойки 008"  # Arch/BIM 166 (typed FeaturePython)
  Align = 2
  Area = 42500
  Base = -> Line1653
  BlockHeight = 65
  BlockLength = 250
  CountBroken = 1
  CountEntire = 0
  Face = 0
  Height = 170
  HorizontalArea = 62500
  IfcData = attributes={"GlobalId": {"name": "GlobalId", "type": "IfcGloballyUniqueId", "is_enum": false, "enum_values": []}, "Description": {"... (+533 chars omitted),+1 more (map truncated)
  IfcType = 166
  Joint = 12000
  Length = 250
  MakeBlocks = false
  Material = -> Material019
  MoveBase = false
  MoveWithHost = false
  Normal = (0,0,0)
  OffsetFirst = 120
  OffsetSecond = 200
  PerimeterLength = 1000
  Placement = pos=(0,0,2960) rot=(0,0,1;0rad)
  PredefinedType = 0
  VerticalArea = 170000
  Width = 250
FEATURE [Part::FeaturePython] Wall054  label="Утепление перекрытия XPS 100mm"  # Arch/BIM 166 (typed FeaturePython)
  Align = 0
  Area = 95281000
  Base = -> Line1077
  BlockHeight = 600
  BlockLength = 1200
  CountBroken = 113
  CountEntire = 88
  Face = 0
  GlobalId = 3kr3_7iVj0bR5GirXoWo2v
  Height = 7550
  HorizontalArea = 0
  IfcData = IfcUID=3kr3_7iVj0bR5GirXoWo2v; attributes={"GlobalId": {"value": "3kr3_7iVj0bR5GirXoWo2v"}}
  IfcType = 166
  Joint = 0
  Length = 12620
  MakeBlocks = false
  Material = -> Material002
  MoveBase = false
  MoveWithHost = false
  Normal = (0,1,0)
  OffsetFirst = 80
  OffsetSecond = 600
  PerimeterLength = 0
  Placement = pos=(0,0,3060) rot=(0,0,1;0rad)
  PredefinedType = 0
  Subtractions = -> [Structure037,Structure360,Structure384,Wall336,Wall337,Wall338,Wall339,Component116,Component115,Wall343]
  VerticalArea = 0
  Width = 100
FEATURE [Part::FeaturePython] Wall098  label="Стяжка пола 50мм"  # Arch/BIM 166 (typed FeaturePython)
  Align = 0
  Area = 95281000
  Base = -> Line1077
  BlockHeight = 0
  BlockLength = 0
  CountBroken = 53
  CountEntire = 111
  Face = 0
  GlobalId = 2jmC5X6fbFRwmp_GUsZLMp
  Height = 7550
  HorizontalArea = 0
  IfcData = IfcUID=2jmC5X6fbFRwmp_GUsZLMp; attributes={"GlobalId": {"value": "2jmC5X6fbFRwmp_GUsZLMp"}}
  IfcType = 166
  Joint = 0
  Length = 12620
  MakeBlocks = false
  Material = -> Material018
  MoveBase = false
  MoveWithHost = false
  Normal = (0,1,0)
  OffsetFirst = 0
  OffsetSecond = 0
  PerimeterLength = 0
  Placement = pos=(0,1.1e-15,3110) rot=(0,0,1;0rad)
  PredefinedType = 0
  Subtractions = -> [Structure037,Structure360,Structure384,Wall336,Wall337,Wall338,Wall339,Component116,Component115,Wall343]
  VerticalArea = 0
  Width = 50
FEATURE [Part::FeaturePython] Wall295  label="Покрытие пола 20мм 001"  # Arch/BIM 166 (typed FeaturePython)
  Align = 0
  Area = 95281000
  Base = -> Line1077
  BlockHeight = 0
  BlockLength = 0
  CountBroken = 53
  CountEntire = 111
  Face = 0
  GlobalId = 3s3if1WDv6dQOvhmOxYeJ$
  Height = 7550
  HorizontalArea = 0
  IfcData = IfcUID=3s3if1WDv6dQOvhmOxYeJ$; attributes={"GlobalId": {"value": "3s3if1WDv6dQOvhmOxYeJ$"}}
  IfcType = 166
  Joint = 0
  Length = 12620
  MakeBlocks = false
  Material = -> Material018
  MoveBase = false
  MoveWithHost = false
  Normal = (0,1,0)
  OffsetFirst = 0
  OffsetSecond = 0
  PerimeterLength = 0
  Placement = pos=(0,1.1e-15,3130) rot=(0,0,1;0rad)
  PredefinedType = 0
  Subtractions = -> [Structure037,Structure360,Structure384,Wall336,Wall337,Wall339,Wall338,Component116,Component115,Wall343]
  VerticalArea = 0
  Width = 20
FEATURE [App::GeometryPython] BuildingPart099  label="Пол мансарды"  # Arch/BIM 52 (typed FeaturePython)
  Area = 285843000
  GlobalId = 0Uv4k6v0XBk8Mx6e_8kGVf
  Group = -> [Wall098,Wall054,Wall295]
  Height = 0
  HeightPropagate = true
  IfcData = IfcUID=0Uv4k6v0XBk8Mx6e_8kGVf,+2 more (map truncated)
  IfcType = 52
  LevelOffset = 0
FEATURE [App::GeometryPython] BuildingPart110  label="Кладка под стойки"  # Arch/BIM 172 (typed FeaturePython)
  Area = 212500
  Group = -> [Wall336,Wall337,Wall338,Wall339,Component116,Component115,Wall343]
  Height = 170
  HeightPropagate = true
  IfcData = attributes={"GlobalId": {"name": "GlobalId", "type": "IfcGloballyUniqueId", "is_enum": false, "enum_values": []}, "Description": {"... (+484 chars omitted),+1 more (map truncated)
  IfcType = 172
  LevelOffset = 0
  Placement = pos=(0,0,2960) rot=(0,0,1;0rad)
  PredefinedType = 0
FEATURE [App::GeometryPython] BuildingPart016  label="Конструкции перекрытия"  # Arch/BIM 52 (typed FeaturePython)
  Area = 349251280
  GlobalId = 3lFo00xcPACR0FdWtYITp1
  Group = -> [BuildingPart006,Wall164,BuildingPart040,BuildingPart082,Wall248,Wall249,BuildingPart097,BuildingPart099,BuildingPart110]
  Height = 0
  HeightPropagate = true
  IfcData = IfcUID=3lFo00xcPACR0FdWtYITp1,attributes={"GlobalId": {"value": "3lFo00xcPACR0FdWtYITp1"}},+1 more (map truncated)
  IfcType = 52
  LevelOffset = 0
FEATURE [Part::Cut] Cut060  label="Стропилка вальмы боковые скаты 005"
  Base = -> Cut059
  Tool = -> Fusion057
FEATURE [Part::Cut] Cut061  label="Кобылки навеса 003"
  Base = -> Common066
  Tool = -> Structure451
FEATURE [Part::Cut] Cut062  label="Кобылки навеса 004"
  Base = -> Common067
  Tool = -> Structure452
FEATURE [Part::Cut] Cut065  label="Стропилка вальмы боковые скаты 006"
  Base = -> Cut060
  Tool = -> Wall334
FEATURE [Part::Cut] Cut066  label="Стропилка вальмы боковые скаты001"
  Base = -> Cut065
  Tool = -> Common056
FEATURE [Part::MultiFuse] Fusion061  label="Конёк кукушки 003"
  Shapes = -> [Wall331,Wall333]
FEATURE [Part::Cut] Cut068  label="Стропилка кукушек002"
  Base = -> Common050
  Tool = -> Fusion061
FEATURE [Part::Part2DObjectPython] Wire903  # Draft 2D object (typed FeaturePython)
  Area = 9.7405e+06
  ChamferSize = 0
  Closed = true
  End = (215.926,940,0)
  FilletRadius = 0
  Length = 14166.1
  MakeFace = true
  Placement = pos=(-135,940,0) rot=(0,0,1;0rad)
  Points = (5) [(0,0,0),(7.95808e-13,5575,0),(355.926,5575,0),(3140.93,2790,0),(350.926,-6.34373e-11,0)]
  Start = (-135,940,0)
  Subdivisions = 0
FEATURE [Part::Extrusion] Extrude099007  label="Extrude099008"
  Base = -> Wire903
  Dir = (0,0,1)
  DirMode = 2
  FaceMakerClass = Part::FaceMakerBullseye
  LengthFwd = 5000
  LengthRev = 0
  Placement = pos=(0,0,2500) rot=(0,0,1;0rad)
  Solid = false
  Symmetric = false
FEATURE [Part::FeaturePython] Clone001  label="Extrude099009"  # Draft clone (typed FeaturePython)
  AttacherType = Attacher::AttachEngine3D
  Fuse = false
  Objects = -> [Extrude099007]
  Placement = pos=(12520,7460,2500) rot=(0,0,1;3.14159rad)
  Scale = (1,1,1)
FEATURE [Part::MultiFuse] Fusion049
  Shapes = -> [Extrude099007,Clone001]
FEATURE [Part::Cut] Cut055  label="Стропилка вальмы скаты с кукушками 001"
  Base = -> Common052
  Tool = -> Fusion049
FEATURE [Part::Cut] Cut056  label="Стропилка вальмы скаты с кукушками 002"
  Base = -> Cut055
  Tool = -> Fusion051
FEATURE [Part::Cut] Cut057  label="Стропилка вальмы скаты с кукушками 003"
  Base = -> Cut056
  Tool = -> Wall057
FEATURE [Part::MultiCommon] Common054  label="Стропилка вальмы скаты с кукушками 004"
  Shapes = -> [Fusion053,Cut057]
FEATURE [Part::Cut] Cut067  label="Стропилка вальмы скаты с кукушками 006"
  Base = -> Common054
  Tool = -> Common056
FEATURE [Part::Part2DObjectPython] Rectangle3384  label="h2,5м площадь (к=1.0) 001"  # Draft 2D object (typed FeaturePython)
  Area = 3.31556e+07
  ChamferSize = 0
  Columns = 1
  FilletRadius = 0
  Height = 2635.58
  Length = 12580
  MakeFace = true
  Placement = pos=(-30,2412.21,0) rot=(0,0,1;0rad)
  Rows = 1
FEATURE [Part::Part2DObjectPython] Rectangle3385  label="h1,6м площадь (к=0.7) 002"  # Draft 2D object (typed FeaturePython)
  Area = 1.61695e+07
  ChamferSize = 0
  Columns = 1
  FilletRadius = 0
  Height = 1285.33
  Length = 12580
  MakeFace = true
  Placement = pos=(-30,1126.88,0) rot=(0,0,1;0rad)
  Rows = 1
FEATURE [Part::Part2DObjectPython] Rectangle3386  label="h1,6м площадь (к=0.7) 001"  # Draft 2D object (typed FeaturePython)
  Area = 1.61695e+07
  ChamferSize = 0
  Columns = 1
  FilletRadius = 0
  Height = 1285.33
  Length = 12580
  MakeFace = true
  Placement = pos=(-30,5047.79,0) rot=(0,0,1;0rad)
  Rows = 1
FEATURE [Part::Part2DObjectPython] Rectangle3387  label="Вычитаемая площадь проёма"  # Draft 2D object (typed FeaturePython)
  Area = 2.5801e+06
  ChamferSize = 0
  Columns = 1
  FilletRadius = 0
  Height = 2529.51
  Length = 1020
  MakeFace = true
  Placement = pos=(6900,3803.61,0) rot=(0,0,1;0rad)
  Rows = 1
FEATURE [App::DocumentObjectGroup] Group126  label="План мансарда 94.1 м2"
  Group = -> [Rectangle2788,Wire819,Rectangle2597,Rectangle3220,Line1442,Rectangle3225,Rectangle3223,Rectangle3224,Rectangle3222,Array063,Rectangle3278,Rectangle3228,Rectangle3229,Rectangle3232,Rectangle3233,Rectangle3236,Rectangle3239,Rectangle3240,Rectangle3247,Rectangle3248,Rectangle3249,Rectangle3250,Rectangle3252,Rectangle3255,Rectangle3257,Rectangle3258,Rectangle3259,Rectangle3260,Rectangle3261,+35 more]
FEATURE [Part::Part2DObjectPython] Wire904  # Draft 2D object (typed FeaturePython)
  Area = 123740
  ChamferSize = 0
  Closed = true
  End = (1250,0,4150)
  FilletRadius = 0
  Length = 2074.13
  MakeFace = true
  Placement = pos=(560.619,0,3460.62) rot=(1,0,0;1.5708rad)
  Points = (4) [(0,0,0),(0,212.132,4.71028e-14),(477.249,689.381,1.38462e-13),(689.381,689.381,1.31967e-13)]
  Start = (560.619,0,3460.62)
  Subdivisions = 0
FEATURE [Part::Extrusion] Extrude099016  label="Extrude099018"
  Base = -> Wire904
  Dir = (0,-1,2e-16)
  DirMode = 2
  FaceMakerClass = Part::FaceMakerBullseye
  LengthFwd = 100
  LengthRev = 0
  Placement = pos=(0,555.619,0) rot=(0,0,1;0rad)
  Solid = false
  Symmetric = false
FEATURE [Part::Mirroring] mirror007  label="Extrude099018 (mirrored)"
  Base = (410.619,555.619,0)
  Normal = (-1,0,0)
  Placement = pos=(11670,6.821e-13,0) rot=(0,0,1;0rad)
  Source = -> Extrude099016
FEATURE [Part::FeaturePython] Array070  # Draft array (typed FeaturePython)
  Angle = 360
  ArrayType = 0
  Axis = (0,0,1)
  Base = -> Extrude099016
  Center = (0,0,0)
  Count = 4
  ExpandArray = false
  Fuse = false
  IntervalAxis = (0,0,0)
  IntervalX = (2880,0,0)
  IntervalY = (0,100,0)
  IntervalZ = (0,0,100)
  NumberCircles = 3
  NumberPolar = 5
  NumberX = 4
  NumberY = 1
  NumberZ = 1
  PlacementList = 4 placements: arithmetic series from (0,555.619,0) step (2880,0,0) to (8640,555.619,0)
  RadialDistance = 50
  ScaleList = (4) [(1,1,1),(1,1,1),(1,1,1),(1,1,1)]
  Symmetry = 1
  TangentialDistance = 25
FEATURE [Part::FeaturePython] Array071  # Draft array (typed FeaturePython)
  Angle = 360
  ArrayType = 0
  Axis = (0,0,1)
  Base = -> mirror007
  Center = (0,0,0)
  Count = 4
  ExpandArray = false
  Fuse = false
  IntervalAxis = (0,0,0)
  IntervalX = (-2880,0,0)
  IntervalY = (0,100,0)
  IntervalZ = (0,0,100)
  NumberCircles = 3
  NumberPolar = 5
  NumberX = 4
  NumberY = 1
  NumberZ = 1
  PlacementList = 4 placements: arithmetic series from (11670,6.82121e-13,0) step (-2880,0,0) to (3030,6.82121e-13,0)
  RadialDistance = 50
  ScaleList = (4) [(1,1,1),(1,1,1),(1,1,1),(1,1,1)]
  Symmetry = 1
  TangentialDistance = 25
FEATURE [Part::MultiFuse] Fusion062
  Shapes = -> [Array070,Array071]
FEATURE [Part::FeaturePython] Clone003  label="Fusion063"  # Draft clone (typed FeaturePython)
  AttacherType = Attacher::AttachEngine3D
  Fuse = false
  Objects = -> [Fusion062]
  Placement = pos=(0,6448.76,0) rot=(0,0,1;0rad)
  Scale = (1,1,1)
FEATURE [Part::MultiFuse] Fusion063  label="Стойки подстропильные (подкосы)"
  Shapes = -> [Fusion062,Clone003]
FEATURE [Part::MultiFuse] Fusion064
  Shapes = -> [Array066,Array068]
FEATURE [Part::MultiFuse] Fusion065
  Shapes = -> [Fusion064,Fusion063]
FEATURE [Part::MultiFuse] Fusion066  label="Прогоны подстропильные 001"
  Shapes = -> [Fusion057,Fusion065]
FEATURE [Part::Part2DObjectPython] Rectangle3388  # Draft 2D object (typed FeaturePython)
  Area = 2640000
  ChamferSize = 0
  Columns = 1
  FilletRadius = 0
  Height = 1200
  Length = 2200
  MakeFace = true
  Placement = pos=(100,3100,0) rot=(0,0,1;0rad)
  Rows = 1
FEATURE [Part::Extrusion] Extrude099017  label="Extrude099019"
  Base = -> Rectangle3388
  Dir = (0,0,1)
  DirMode = 2
  FaceMakerClass = Part::FaceMakerBullseye
  LengthFwd = 300
  LengthRev = 0
  Placement = pos=(0,0,6050) rot=(0,0,1;0rad)
  Solid = false
  Symmetric = false
FEATURE [Part::MultiCommon] Common069
  Shapes = -> [Cut054,Extrude099017]
FEATURE [Part::MultiCommon] Common070
  Placement = pos=(-50,0,0) rot=(0,0,1;0rad)
  Shapes = -> [Array013,Common069]
FEATURE [Part::FeaturePython] Clone004  label="Common071"  # Draft clone (typed FeaturePython)
  AttacherType = Attacher::AttachEngine3D
  Fuse = false
  Objects = -> [Common070]
  Placement = pos=(10130,4.55e-13,0) rot=(0,0,1;0rad)
  Scale = (1,1,1)
FEATURE [Part::MultiFuse] Fusion067  label="Накладки стропил кукушек001"
  Shapes = -> [Common070,Clone004]
FEATURE [Part::Extrusion] Extrude099018  label="Extrude099020"
  Base = -> Rectangle3372
  Dir = (0,0,1)
  DirMode = 2
  FaceMakerClass = Part::FaceMakerBullseye
  LengthFwd = 300
  LengthRev = 0
  Placement = pos=(0,0,6550) rot=(0,0,1;0rad)
  Solid = false
  Symmetric = false
FEATURE [Part::MultiCommon] Common071  label="Common072"
  Shapes = -> [Cut053,Extrude099018]
FEATURE [Part::MultiCommon] Common072  label="Накладки стропил 001"
  Placement = pos=(-50,0,0) rot=(0,0,1;0rad)
  Shapes = -> [Array013,Common071]
FEATURE [Part::MultiFuse] Fusion068
  Shapes = -> [Common046,Common047]
FEATURE [Part::MultiFuse] Fusion069
  Shapes = -> [Common048,Common049]
FEATURE [Part::MultiFuse] Fusion070
  Shapes = -> [Fusion068,Fusion069]
FEATURE [Part::MultiCommon] Common073  label="Накосные стропила кукушки 001"
  Shapes = -> [Fusion060,Fusion070]
FEATURE [Part::Cut] Cut069  label="Стропилка вальмы скаты с кукушками 007"
  Base = -> Cut067
  Tool = -> Common073
FEATURE [Part::FeaturePython] Component117  label="Накосные стропила кукушки"  # Arch/BIM 0 (typed FeaturePython)
  Base = -> Common073
  HorizontalArea = 0
  IfcData = attributes={"GlobalId": {"name": "GlobalId", "type": "IfcGloballyUniqueId", "is_enum": false, "enum_values": []}, "Description": {"... (+538 chars omitted),+1 more (map truncated)
  IfcType = 0
  Material = -> Material
  MoveBase = false
  MoveWithHost = false
  PerimeterLength = 0
  PredefinedType = 0
  VerticalArea = 0
FEATURE [Part::FeaturePython] Component118  label="Стропилка вальмы скаты с кукушками"  # Arch/BIM 0 (typed FeaturePython)
  Base = -> Cut069
  HorizontalArea = 0
  IfcData = attributes={"GlobalId": {"name": "GlobalId", "type": "IfcGloballyUniqueId", "is_enum": false, "enum_values": []}, "Description": {"... (+538 chars omitted),+1 more (map truncated)
  IfcType = 0
  Material = -> Material
  MoveBase = false
  MoveWithHost = false
  PerimeterLength = 0
  PredefinedType = 0
  VerticalArea = 0
FEATURE [Part::FeaturePython] Component119  label="Накладки стропил"  # Arch/BIM 0 (typed FeaturePython)
  Base = -> Common072
  HorizontalArea = 0
  IfcData = attributes={"GlobalId": {"name": "GlobalId", "type": "IfcGloballyUniqueId", "is_enum": false, "enum_values": []}, "Description": {"... (+538 chars omitted),+1 more (map truncated)
  IfcType = 0
  Material = -> Material
  MoveBase = false
  MoveWithHost = false
  PerimeterLength = 0
  Placement = pos=(-50,0,0) rot=(0,0,1;0rad)
  PredefinedType = 0
  VerticalArea = 0
FEATURE [Part::FeaturePython] Component120  label="Затяжки"  # Arch/BIM 0 (typed FeaturePython)
  Base = -> Fusion058
  HorizontalArea = 0
  IfcData = attributes={"GlobalId": {"name": "GlobalId", "type": "IfcGloballyUniqueId", "is_enum": false, "enum_values": []}, "Description": {"... (+538 chars omitted),+1 more (map truncated)
  IfcType = 0
  Material = -> Material
  MoveBase = false
  MoveWithHost = false
  PerimeterLength = 0
  Placement = pos=(-50,0,0) rot=(0,0,1;0rad)
  PredefinedType = 0
  VerticalArea = 0
FEATURE [Part::FeaturePython] Component121  label="Кобылки навеса св."  # Arch/BIM 0 (typed FeaturePython)
  Base = -> Cut061
  HorizontalArea = 0
  IfcData = attributes={"GlobalId": {"name": "GlobalId", "type": "IfcGloballyUniqueId", "is_enum": false, "enum_values": []}, "Description": {"... (+538 chars omitted),+1 more (map truncated)
  IfcType = 0
  Material = -> Material
  MoveBase = false
  MoveWithHost = false
  PerimeterLength = 0
  PredefinedType = 0
  VerticalArea = 0
FEATURE [Part::FeaturePython] Component122  label="Кобылки навеса юг."  # Arch/BIM 0 (typed FeaturePython)
  Base = -> Cut062
  HorizontalArea = 0
  IfcData = attributes={"GlobalId": {"name": "GlobalId", "type": "IfcGloballyUniqueId", "is_enum": false, "enum_values": []}, "Description": {"... (+538 chars omitted),+1 more (map truncated)
  IfcType = 0
  Material = -> Material
  MoveBase = false
  MoveWithHost = false
  PerimeterLength = 0
  PredefinedType = 0
  VerticalArea = 0
FEATURE [Part::FeaturePython] Component123  label="Конёк кукушки"  # Arch/BIM 0 (typed FeaturePython)
  Base = -> Fusion061
  HorizontalArea = 0
  IfcData = attributes={"GlobalId": {"name": "GlobalId", "type": "IfcGloballyUniqueId", "is_enum": false, "enum_values": []}, "Description": {"... (+538 chars omitted),+1 more (map truncated)
  IfcType = 0
  Material = -> Material
  MoveBase = false
  MoveWithHost = false
  PerimeterLength = 0
  PredefinedType = 0
  VerticalArea = 0
FEATURE [Part::FeaturePython] Component124  label="Стропилка кукушек"  # Arch/BIM 0 (typed FeaturePython)
  Base = -> Cut068
  HorizontalArea = 0
  IfcData = attributes={"GlobalId": {"name": "GlobalId", "type": "IfcGloballyUniqueId", "is_enum": false, "enum_values": []}, "Description": {"... (+538 chars omitted),+1 more (map truncated)
  IfcType = 0
  Material = -> Material
  MoveBase = false
  MoveWithHost = false
  PerimeterLength = 0
  PredefinedType = 0
  VerticalArea = 0
FEATURE [Part::FeaturePython] Component125  label="Стропилка вальмы боковые скаты"  # Arch/BIM 0 (typed FeaturePython)
  Base = -> Cut066
  HorizontalArea = 0
  IfcData = attributes={"GlobalId": {"name": "GlobalId", "type": "IfcGloballyUniqueId", "is_enum": false, "enum_values": []}, "Description": {"... (+538 chars omitted),+1 more (map truncated)
  IfcType = 0
  Material = -> Material
  MoveBase = false
  MoveWithHost = false
  PerimeterLength = 0
  PredefinedType = 0
  VerticalArea = 0
FEATURE [Part::FeaturePython] Component126  label="Прогоны подстропильные"  # Arch/BIM 0 (typed FeaturePython)
  Base = -> Fusion066
  HorizontalArea = 0
  IfcData = attributes={"GlobalId": {"name": "GlobalId", "type": "IfcGloballyUniqueId", "is_enum": false, "enum_values": []}, "Description": {"... (+538 chars omitted),+1 more (map truncated)
  IfcType = 0
  Material = -> Material
  MoveBase = false
  MoveWithHost = false
  PerimeterLength = 0
  PredefinedType = 0
  VerticalArea = 0
FEATURE [Part::FeaturePython] Component127  label="Накладки стропил кукушек"  # Arch/BIM 0 (typed FeaturePython)
  Base = -> Fusion067
  HorizontalArea = 0
  IfcData = attributes={"GlobalId": {"name": "GlobalId", "type": "IfcGloballyUniqueId", "is_enum": false, "enum_values": []}, "Description": {"... (+538 chars omitted),+1 more (map truncated)
  IfcType = 0
  Material = -> Material
  MoveBase = false
  MoveWithHost = false
  PerimeterLength = 0
  PredefinedType = 0
  VerticalArea = 0
FEATURE [Part::FeaturePython] Component128  label="Брус подоконный"  # Arch/BIM 0 (typed FeaturePython)
  Base = -> Fusion051
  HorizontalArea = 0
  IfcData = attributes={"GlobalId": {"name": "GlobalId", "type": "IfcGloballyUniqueId", "is_enum": false, "enum_values": []}, "Description": {"... (+538 chars omitted),+1 more (map truncated)
  IfcType = 0
  Material = -> Material
  MoveBase = false
  MoveWithHost = false
  PerimeterLength = 0
  PredefinedType = 0
  VerticalArea = 0
FEATURE [Part::FeaturePython] Component129  label="Проход вентстояка"  # Arch/BIM 0 (typed FeaturePython)
  Base = -> Common060
  HorizontalArea = 0
  IfcData = attributes={"GlobalId": {"name": "GlobalId", "type": "IfcGloballyUniqueId", "is_enum": false, "enum_values": []}, "Description": {"... (+538 chars omitted),+1 more (map truncated)
  IfcType = 0
  Material = -> Material
  MoveBase = false
  MoveWithHost = false
  PerimeterLength = 0
  PredefinedType = 0
  VerticalArea = 0
FEATURE [Part::FeaturePython] Component130  label="Накосные стропила"  # Arch/BIM 0 (typed FeaturePython)
  Base = -> Common056
  HorizontalArea = 0
  IfcData = attributes={"GlobalId": {"name": "GlobalId", "type": "IfcGloballyUniqueId", "is_enum": false, "enum_values": []}, "Description": {"... (+538 chars omitted),+1 more (map truncated)
  IfcType = 0
  Material = -> Material
  MoveBase = false
  MoveWithHost = false
  PerimeterLength = 0
  PredefinedType = 0
  VerticalArea = 0
FEATURE [App::GeometryPython] BuildingPart109  label="Стропильная система кровли"  # Arch/BIM 172 (typed FeaturePython)
  Area = 0
  Group = -> [Component117,Component118,Component119,Component120,Component121,Component122,Component124,Component125,Component127,Component128,Component129,Component130]
  Height = 0
  HeightPropagate = true
  IfcData = attributes={"GlobalId": {"name": "GlobalId", "type": "IfcGloballyUniqueId", "is_enum": false, "enum_values": []}, "Description": {"... (+484 chars omitted),+1 more (map truncated)
  IfcType = 172
  LevelOffset = 0
  Placement = pos=(0,0,3630) rot=(0,0,1;0rad)
  PredefinedType = 0
FEATURE [App::GeometryPython] BuildingPart113  label="Стойки и прогоны"  # Arch/BIM 172 (typed FeaturePython)
  Area = 7194000
  Group = -> [Wall334,Wall057,BuildingPart112,BuildingPart111,Component123,Component126]
  Height = 0
  HeightPropagate = true
  IfcData = attributes={"GlobalId": {"name": "GlobalId", "type": "IfcGloballyUniqueId", "is_enum": false, "enum_values": []}, "Description": {"... (+484 chars omitted),+1 more (map truncated)
  IfcType = 172
  LevelOffset = 0
  PredefinedType = 0
FEATURE [Part::Compound] Compound  label="Оси001"
  Links = -> [Axis001006,Axis001007]
FEATURE [Part::Compound] Compound005  label="Roof003"
  Links = -> [Wire817,Line1497,Line1500,Line1502,Line1503,Line1501,Line1507,Line1506,Line1498,Line1504,Line1505,Line1499]
FEATURE [TechDraw::DrawViewDraft] DraftView001
  Direction = (0,0,1)
  FontSize = 12
  LineSpacing = 1
  LineStyle = Solid
  LineWidth = 0.1
  LockPosition = true
  OverrideStyle = false
  Rotation = 0
  Scale = 0.02
  ScaleType = 2
  Source = -> Compound005
  Symbol = <blob: 3309 chars omitted>
  X = 209.065
  Y = 144.442
FEATURE [TechDraw::DrawSVGTemplate] Template003
  EditableTexts = Лист=4; Номер=ИЖС-0000.0001
  Height = 297
  Orientation = 1
  Width = 420
FEATURE [TechDraw::DrawViewAnnotation] Annotation031
  Font = osifont
  LineSpace = 80
  LockPosition = false
  MaxWidth = -1
  Rotation = 0
  ScaleType = 0
  Text = \u041f\u043b\u0430\u043d \u043c\u0430\u043d\u0441\u0430\u0440\u0434\u043d\u043e\u0433\u043e \u044d\u0442\u0430\u0436\u0430 \u043d\u0430 \u043e\u0442\u043c\u0435\u0442\u043a\u0435 +3.13
  TextSize = 6
  TextStyle = 0
  X = 218.387
  Y = 275.093
FEATURE [Part::Part2DObjectPython] Rectangle3398  # Draft 2D object (typed FeaturePython)
  Area = 0
  ChamferSize = 0
  Columns = 1
  FilletRadius = 0
  Height = 8000
  Length = 7000
  MakeFace = false
  Placement = pos=(22359,-9231.91,0) rot=(0,0,1;1.34139rad)
  Rows = 1
FEATURE [Part::FeaturePython] Structure437  label="Парковка"  # Arch/BIM 118 (typed FeaturePython)
  Base = -> Rectangle3398
  FaceMaker = 0
  Height = 200
  HorizontalArea = 5.6e+07
  IfcData = attributes={"GlobalId": {"name": "GlobalId", "type": "IfcGloballyUniqueId", "is_enum": false, "enum_values": []}, "Description": {"... (+453 chars omitted),+1 more (map truncated)
  IfcType = 118
  Length = 7000
  MoveBase = false
  MoveWithHost = false
  Nodes = (4) [(19575,-8688.32,0),(20865.3,-2828.71,0),(14029.1,-1323.35,0),(12738.8,-7182.97,0)]
  NodesOffset = 0
  Normal = (0,0,-1)
  PerimeterLength = 30000
  Placement = pos=(0,0,-300) rot=(0,0,1;0rad)
  PredefinedType = 0
  VerticalArea = 6e+06
  Width = 6500
FEATURE [Part::Part2DObjectPython] Rectangle3402  # Draft 2D object (typed FeaturePython)
  Area = 1.38e+07
  ChamferSize = 0
  Columns = 1
  FilletRadius = 0
  Height = 2300
  Length = 6000
  MakeFace = true
  Placement = pos=(-6950.03,-7631.87,0) rot=(0,0,1;0.175714rad)
  Rows = 1
FEATURE [Part::Part2DObjectPython] Line1707  # Draft 2D object (typed FeaturePython)
  Area = 0
  ChamferSize = 0
  Closed = false
  End = (24359.1,-3994.32,0)
  FilletRadius = 0
  Length = 5200
  MakeFace = true
  Placement = pos=(24127,-9189.13,0) rot=(0,0,-1;1.61546rad)
  Points = (2) [(0,0,0),(-5200,-3.63798e-11,0)]
  Start = (24127,-9189.13,0)
  Subdivisions = 0
FEATURE [Part::FeaturePython] Wall315  label="Створка ворот 4.7м"  # Arch/BIM 166 (typed FeaturePython)
  Align = 0
  Area = 9.36e+06
  Base = -> Line1707
  BlockHeight = 2000
  BlockLength = 150
  CountBroken = 33
  CountEntire = 0
  Face = 0
  Height = 1800
  HorizontalArea = 0
  IfcData = attributes={"GlobalId": {"name": "GlobalId", "type": "IfcGloballyUniqueId", "is_enum": false, "enum_values": []}, "Description": {"... (+533 chars omitted),+1 more (map truncated)
  IfcType = 166
  Joint = 10
  Length = 5200
  MakeBlocks = true
  Material = -> Material010
  MoveBase = false
  MoveWithHost = false
  Normal = (0,0,0)
  Offset = 125
  OffsetFirst = 100
  OffsetSecond = 0
  PerimeterLength = 0
  Placement = pos=(-290,1.3642e-12,-120) rot=(0,0,1;0rad)
  PredefinedType = 0
  VerticalArea = 0
  Width = 50
FEATURE [Part::Part2DObjectPython] Line1708  # Draft 2D object (typed FeaturePython)
  Area = 0
  ChamferSize = 0
  Closed = false
  End = (24454.5,-4098.68,0)
  FilletRadius = 0
  Length = 5000
  MakeFace = true
  Placement = pos=(24231.3,-9093.7,0) rot=(0,0,-1;0.04466rad)
  Points = (2) [(0,0,0),(-1.81899e-11,5000,0)]
  Start = (24231.3,-9093.7,0)
  Subdivisions = 0
FEATURE [Part::FeaturePython] Wall314  label="Проём ворот 5м"  # Arch/BIM 166 (typed FeaturePython)
  Align = 0
  Area = 1e+07
  Base = -> Line1708
  BlockHeight = 0
  BlockLength = 0
  CountBroken = 0
  CountEntire = 0
  Face = 0
  Height = 2000
  HorizontalArea = 1e+06
  IfcData = attributes={"GlobalId": {"name": "GlobalId", "type": "IfcGloballyUniqueId", "is_enum": false, "enum_values": []}, "Description": {"... (+533 chars omitted),+1 more (map truncated)
  IfcType = 166
  Joint = 0
  Length = 5000
  MakeBlocks = false
  MoveBase = false
  MoveWithHost = false
  Normal = (0,0,0)
  Offset = 100
  OffsetFirst = 0
  OffsetSecond = 0
  PerimeterLength = 10400
  Placement = pos=(0,0,-320) rot=(0,0,1;0rad)
  PredefinedType = 0
  VerticalArea = 2.08e+07
  Width = 200
FEATURE [Part::FeaturePython] Space  label="Проём ворот"  # Arch/BIM 122 (typed FeaturePython)
  Area = 1e+06
  AutoPower = false
  Base = -> Wall314
  CompositionType = 0
  Conditioning = 0
  ElevationWithFlooring = -320
  EquipmentPower = 0
  FloorThickness = 0
  HorizontalArea = 1e+06
  IfcData = attributes={"GlobalId": {"name": "GlobalId", "type": "IfcGloballyUniqueId", "is_enum": false, "enum_values": []}, "Description": {"... (+888 chars omitted),+1 more (map truncated)
  IfcType = 122
  Internal = true
  LightingPower = 0
  LongName = Space
  MoveBase = false
  MoveWithHost = false
  NumberOfPeople = 0
  PerimeterLength = 10400
  Placement = pos=(-490,0,0) rot=(0,0,1;0rad)
  PredefinedType = 0
  SpaceType = 0
  VerticalArea = 2.08e+07
  expr: ElevationWithFlooring = .Shape.BoundBox.ZMin
FEATURE [Part::Part2DObjectPython] Line1709  # Draft 2D object (typed FeaturePython)
  Area = 0
  ChamferSize = 0
  Closed = false
  End = (24811.7,3893.34,0)
  FilletRadius = 0
  Length = 8000
  MakeFace = true
  Placement = pos=(24454.5,-4098.68,0) rot=(0,0,-1;0.04466rad)
  Points = (2) [(0,0,0),(5.45697e-11,8000,0)]
  Start = (24454.5,-4098.68,0)
  Subdivisions = 0
FEATURE [Part::FeaturePython] Wall313  label="Зона отката ворот 7.5м"  # Arch/BIM 166 (typed FeaturePython)
  Align = 0
  Area = 1.6e+07
  Base = -> Line1709
  BlockHeight = 0
  BlockLength = 0
  CountBroken = 0
  CountEntire = 0
  Face = 0
  Height = 2000
  HorizontalArea = 1.6e+06
  IfcData = attributes={"GlobalId": {"name": "GlobalId", "type": "IfcGloballyUniqueId", "is_enum": false, "enum_values": []}, "Description": {"... (+533 chars omitted),+1 more (map truncated)
  IfcType = 166
  Joint = 0
  Length = 8000
  MakeBlocks = false
  MoveBase = false
  MoveWithHost = false
  Normal = (0,0,0)
  Offset = 100
  OffsetFirst = 0
  OffsetSecond = 0
  PerimeterLength = 16400
  Placement = pos=(0,0,-320) rot=(0,0,1;0rad)
  PredefinedType = 0
  VerticalArea = 3.28e+07
  Width = 200
FEATURE [Part::FeaturePython] Space001  label="Зона отката ворот "  # Arch/BIM 122 (typed FeaturePython)
  Area = 1.6e+06
  AutoPower = false
  Base = -> Wall313
  CompositionType = 0
  Conditioning = 0
  ElevationWithFlooring = -320
  EquipmentPower = 0
  FloorThickness = 0
  HorizontalArea = 1.6e+06
  IfcData = attributes={"GlobalId": {"name": "GlobalId", "type": "IfcGloballyUniqueId", "is_enum": false, "enum_values": []}, "Description": {"... (+888 chars omitted),+1 more (map truncated)
  IfcType = 122
  Internal = true
  LightingPower = 0
  LongName = Space
  MoveBase = false
  MoveWithHost = false
  NumberOfPeople = 0
  PerimeterLength = 16400
  Placement = pos=(-490,0,0) rot=(0,0,1;0rad)
  PredefinedType = 0
  SpaceType = 0
  VerticalArea = 3.28e+07
  expr: ElevationWithFlooring = .Shape.BoundBox.ZMin
FEATURE [App::GeometryPython] BuildingPart108  label="Откатные ворота 4.5 с калиткой 1м"  # Arch/BIM 172 (typed FeaturePython)
  Area = 1.6628e+07
  Group = -> [Wall315,Wall316,Wall317,Wall318,Wall319,Space,Space001,Roof018,Roof019,Roof020]
  Height = 0
  HeightPropagate = true
  IfcData = attributes={"GlobalId": {"name": "GlobalId", "type": "IfcGloballyUniqueId", "is_enum": false, "enum_values": []}, "Description": {"... (+484 chars omitted),+1 more (map truncated)
  IfcType = 172
  LevelOffset = 0
  PredefinedType = 0
FEATURE [Part::Part2DObjectPython] Wire905  # Draft 2D object (typed FeaturePython)
  Area = 0
  ChamferSize = 0
  Closed = false
  End = (-16687.8,-6439.13,0)
  FilletRadius = 0
  Length = 42628.1
  MakeFace = true
  Placement = pos=(22450.1,-9304.39,0) rot=(0,0,-1;0.04466rad)
  Points = (6) [(0,0,0),(-11950.7,2233.07,0),(-20644.1,1844.56,0),(-31822.2,-659.433,0),(-32744.5,2829.02,0),(-39226.9,1115.07,0)]
  Start = (22450.1,-9304.39,0)
  Subdivisions = 0
FEATURE [Part::FeaturePython] Wall320  label="Забор 002"  # Arch/BIM 166 (typed FeaturePython)
  Align = 0
  Area = 8.52563e+07
  Base = -> Wire905
  BlockHeight = 2000
  BlockLength = 150
  CountBroken = 6
  CountEntire = 260
  Face = 0
  Height = 2000
  HorizontalArea = 0
  IfcData = attributes={"GlobalId": {"name": "GlobalId", "type": "IfcGloballyUniqueId", "is_enum": false, "enum_values": []}, "Description": {"... (+533 chars omitted),+1 more (map truncated)
  IfcType = 166
  Joint = 10
  Length = 42628.1
  MakeBlocks = true
  Material = -> Material010
  MoveBase = false
  MoveWithHost = false
  Normal = (0,0,0)
  OffsetFirst = 100
  OffsetSecond = 0
  PerimeterLength = 0
  Placement = pos=(0,0,-220) rot=(0,0,1;0rad)
  PredefinedType = 0
  VerticalArea = 0
  Width = 50
FEATURE [Part::Part2DObjectPython] Wire906  # Draft 2D object (typed FeaturePython)
  Area = 0
  ChamferSize = 0
  Closed = false
  End = (28701.9,-939.667,0)
  FilletRadius = 0
  Length = 8059.16
  MakeFace = true
  Placement = pos=(24661.3,-3727.55,0) rot=(0,0,-1;0.04466rad)
  Points = (3) [(0,0,0),(-8.2224e-05,4010,0),(3912.13,2965.49,0)]
  Start = (24661.3,-3727.55,0)
  Subdivisions = 0
FEATURE [Part::FeaturePython] Wall321  label="Забор 001"  # Arch/BIM 166 (typed FeaturePython)
  Align = 0
  Area = 1.61183e+07
  Base = -> Wire906
  BlockHeight = 2000
  BlockLength = 150
  CountBroken = 4
  CountEntire = 47
  Face = 0
  Height = 2000
  HorizontalArea = 0
  IfcData = attributes={"GlobalId": {"name": "GlobalId", "type": "IfcGloballyUniqueId", "is_enum": false, "enum_values": []}, "Description": {"... (+533 chars omitted),+1 more (map truncated)
  IfcType = 166
  Joint = 10
  Length = 8059.16
  MakeBlocks = true
  Material = -> Material010
  MoveBase = false
  MoveWithHost = false
  Normal = (0,0,0)
  OffsetFirst = 0
  OffsetSecond = 0
  PerimeterLength = 0
  Placement = pos=(0,0,-220) rot=(0,0,1;0rad)
  PredefinedType = 0
  VerticalArea = 0
  Width = 50
FEATURE [Part::FeaturePython] Structure458  label="Крыша бытовки"  # Arch/BIM 118 (typed FeaturePython)
  Base = -> Rectangle3402
  FaceMaker = 0
  Height = 50
  HorizontalArea = 1.38e+07
  IfcData = attributes={"GlobalId": {"name": "GlobalId", "type": "IfcGloballyUniqueId", "is_enum": false, "enum_values": []}, "Description": {"... (+453 chars omitted),+1 more (map truncated)
  IfcType = 118
  Length = 2300
  MoveBase = false
  MoveWithHost = false
  Nodes = (4) [(-5840.87,-8273.6,0),(66.7383,-7224.73,0),(-335.328,-4960.14,0),(-6242.94,-6009.01,0)]
  NodesOffset = 0
  Normal = (0,0,0)
  PerimeterLength = 16600
  Placement = pos=(0,0,2300) rot=(0,0,1;0rad)
  PredefinedType = 0
  VerticalArea = 830000
  Width = 6000
FEATURE [App::GeometryPython] BuildingPart033  label="хозблок (бытовка)"  # Arch/BIM 10 (typed FeaturePython)
  Area = 4.067e+07
  BuildingType = 0
  CompositionType = 0
  ElevationOfRefHeight = 0
  ElevationOfTerrain = 0
  Group = -> [Wall097,Structure458]
  Height = 0
  HeightPropagate = true
  IfcType = 10
  LevelOffset = 0
  LongName = хозблок (бытовка)
FEATURE [Part::FeaturePython] Roof023  label="Крышка столба 004"  # Arch/BIM 113 (typed FeaturePython)
  BorderLength = 0
  CloneOf = -> Roof018
  Face = 0
  Flip = false
  HorizontalArea = 230400
  IfcData = attributes={"GlobalId": {"name": "GlobalId", "type": "IfcGloballyUniqueId", "is_enum": false, "enum_values": []}, "Description": {"... (+613 chars omitted),+1 more (map truncated)
  IfcType = 113
  Material = -> Material018
  MoveBase = false
  MoveWithHost = false
  PerimeterLength = 0
  Placement = pos=(-20687.8,2722.97,0) rot=(0,0,1;0rad)
  PredefinedType = 0
  RidgeLength = 0
  Thickness = [50,50,50,50]
  VerticalArea = 99386.5
FEATURE [Part::FeaturePython] Wall344  label="Столб 004"  # Arch/BIM 166 (typed FeaturePython)
  Align = 2
  Area = 836000
  BlockHeight = 0
  BlockLength = 0
  CloneOf = -> Wall316
  CountBroken = 0
  CountEntire = 0
  Face = 0
  Height = 2200
  HorizontalArea = 144400
  IfcData = attributes={"GlobalId": {"name": "GlobalId", "type": "IfcGloballyUniqueId", "is_enum": false, "enum_values": []}, "Description": {"... (+533 chars omitted),+1 more (map truncated)
  IfcType = 166
  Joint = 0
  Length = 380
  MakeBlocks = false
  Material = -> Material003
  MoveBase = false
  MoveWithHost = false
  Normal = (0,0,0)
  OffsetFirst = 0
  OffsetSecond = 0
  PerimeterLength = 1520
  Placement = pos=(-20687.8,2722.97,-320) rot=(0,0,1;0rad)
  PredefinedType = 0
  VerticalArea = 3.344e+06
  Width = 380
FEATURE [Part::FeaturePython] Wall345  label="Столб 005"  # Arch/BIM 166 (typed FeaturePython)
  Align = 2
  Area = 836000
  BlockHeight = 0
  BlockLength = 0
  CloneOf = -> Wall316
  CountBroken = 0
  CountEntire = 0
  Face = 0
  Height = 2200
  HorizontalArea = 144400
  IfcData = attributes={"GlobalId": {"name": "GlobalId", "type": "IfcGloballyUniqueId", "is_enum": false, "enum_values": []}, "Description": {"... (+533 chars omitted),+1 more (map truncated)
  IfcType = 166
  Joint = 0
  Length = 380
  MakeBlocks = false
  Material = -> Material003
  MoveBase = false
  MoveWithHost = false
  Normal = (0,0,0)
  OffsetFirst = 0
  OffsetSecond = 0
  PerimeterLength = 1520
  Placement = pos=(-12035.1,2722.32,-320) rot=(0,0,1;0rad)
  PredefinedType = 0
  VerticalArea = 3.344e+06
  Width = 380
FEATURE [Part::FeaturePython] Roof024  label="Крышка столба 005"  # Arch/BIM 113 (typed FeaturePython)
  BorderLength = 0
  CloneOf = -> Roof018
  Face = 0
  Flip = false
  HorizontalArea = 230400
  IfcData = attributes={"GlobalId": {"name": "GlobalId", "type": "IfcGloballyUniqueId", "is_enum": false, "enum_values": []}, "Description": {"... (+613 chars omitted),+1 more (map truncated)
  IfcType = 113
  Material = -> Material018
  MoveBase = false
  MoveWithHost = false
  PerimeterLength = 0
  Placement = pos=(-12035.1,2722.32,0) rot=(0,0,1;0rad)
  PredefinedType = 0
  RidgeLength = 0
  Thickness = [50,50,50,50]
  VerticalArea = 99386.5
FEATURE [App::GeometryPython] BuildingPart067  label="Участок с ограждением"  # Arch/BIM 52 (typed FeaturePython)
  Area = 1.19675e+08
  Group = -> [Structure133,BuildingPart108,Wall320,Wall321,Structure437,Roof023,Wall344,Wall345,Roof024]
  Height = 0
  HeightPropagate = true
  IfcData = attributes={"GlobalId": {"name": "GlobalId", "type": "IfcGloballyUniqueId", "is_enum": false, "enum_values": []}, "Description": {"... (+484 chars omitted),+1 more (map truncated)
  IfcType = 52
  LevelOffset = 0
FEATURE [App::FeaturePython] Dimension072  # Draft dimension (typed FeaturePython)
  Diameter = false
  Dimline = (-1400,7200,0)
  Direction = (0,0,0)
  Distance = 738.353
  End = (-800,7685.58,0)
  Normal = (0,0,1)
  Start = (-800,6947.23,0)
FEATURE [App::FeaturePython] Dimension073  # Draft dimension (typed FeaturePython)
  Diameter = false
  Dimline = (-1400,7200,0)
  Direction = (0,0,0)
  Distance = 3217.23
  End = (-800,6947.23,0)
  Normal = (0,0,1)
  Start = (-800,3730,0)
FEATURE [App::FeaturePython] Dimension074  # Draft dimension (typed FeaturePython)
  Diameter = false
  Dimline = (-1400,7685.58,0)
  Direction = (0,0,0)
  Distance = 914.422
  End = (-800,8600,0)
  Normal = (0,0,1)
  Start = (-800,7685.58,0)
FEATURE [App::FeaturePython] Dimension075  # Draft dimension (typed FeaturePython)
  Diameter = false
  Dimline = (0,5100,2400)
  Direction = (0,0,0)
  Distance = 6448.76
  End = (0,6954.38,3045)
  Normal = (1,0,0)
  Start = (0,505.619,3045)
FEATURE [App::FeaturePython] Dimension076  # Draft dimension (typed FeaturePython)
  Diameter = false
  Dimline = (0,8900,4000)
  Direction = (0,0,0)
  Distance = 3013.88
  End = (0,9000,6796.88)
  Normal = (1,0,0)
  Start = (0,9000,3783)
FEATURE [App::FeaturePython] Dimension077  # Draft dimension (typed FeaturePython)
  Diameter = false
  Dimline = (0,5000,1500)
  Direction = (0,0,0)
  Distance = 9740
  End = (0,8600,3300)
  Normal = (1,0,0)
  Start = (0,-1140,3300)
FEATURE [App::FeaturePython] Dimension078  # Draft dimension (typed FeaturePython)
  Diameter = false
  Dimline = (0,5000,2000)
  Direction = (0,0,0)
  Distance = 7911.16
  End = (0,7685.58,2200)
  Normal = (1,0,0)
  Start = (0,-225.578,2200)
FEATURE [Part::Part2DObjectPython] Rectangle3389  # Draft 2D object (typed FeaturePython)
  Area = 2.45e+07
  ChamferSize = 0
  Columns = 1
  FilletRadius = 0
  Height = 7000
  Length = 3500
  MakeFace = true
  Placement = pos=(22359,-9231.91,0) rot=(0,0,1;1.34139rad)
  Rows = 1
FEATURE [Part::Part2DObjectPython] Line1687  # Draft 2D object (typed FeaturePython)
  Area = 0
  ChamferSize = 0
  Closed = false
  End = (-3580.3,-8530.19,0)
  FilletRadius = 0
  Length = 1000
  MakeFace = true
  Placement = pos=(-3755.12,-7545.59,0) rot=(0,0,1;1.52614rad)
  Points = (2) [(0,0,0),(-975.816,-218.595,0)]
  Start = (-3755.12,-7545.59,0)
  Subdivisions = 0
FEATURE [Part::Part2DObjectPython] Line1688  # Draft 2D object (typed FeaturePython)
  Area = 0
  ChamferSize = 0
  Closed = false
  End = (7519.32,-7540,0)
  FilletRadius = 0
  Length = 1000
  MakeFace = true
  Placement = pos=(7519.32,-6540,0) rot=(0,0,1;1.52614rad)
  Points = (2) [(0,0,0),(-999.003,-44.6455,0)]
  Start = (7519.32,-6540,0)
  Subdivisions = 0
FEATURE [Part::Part2DObjectPython] Line1689  # Draft 2D object (typed FeaturePython)
  Area = 0
  ChamferSize = 0
  Closed = false
  End = (9687.65,-6293.74,0)
  FilletRadius = 0
  Length = 12000
  MakeFace = true
  Placement = pos=(21282.4,-9385.88,0) rot=(0,0,1;1.52614rad)
  Points = (2) [(0,0,0),(2571.4,11721.3,0)]
  Start = (21282.4,-9385.88,0)
  Subdivisions = 0
FEATURE [Part::Part2DObjectPython] Line1690  # Draft 2D object (typed FeaturePython)
  Area = 0
  ChamferSize = 0
  Closed = false
  End = (1996.8,-7540,0)
  FilletRadius = 0
  Length = 1000
  MakeFace = true
  Placement = pos=(1996.8,-6540,0) rot=(0,0,1;1.52614rad)
  Points = (2) [(0,0,0),(-999.003,-44.6455,0)]
  Start = (1996.8,-6540,0)
  Subdivisions = 0
FEATURE [Part::Part2DObjectPython] Line1692  # Draft 2D object (typed FeaturePython)
  Area = 0
  ChamferSize = 0
  Closed = false
  End = (1996.8,-7540,0)
  FilletRadius = 0
  Length = 1000
  MakeFace = true
  Placement = pos=(1821.99,-6555.4,0) rot=(0,0,1;1.52614rad)
  Points = (2) [(0,0,0),(-975.816,-218.595,0)]
  Start = (1821.99,-6555.4,0)
  Subdivisions = 0
FEATURE [Part::Part2DObjectPython] Line1693  # Draft 2D object (typed FeaturePython)
  Area = 0
  ChamferSize = 0
  Closed = false
  End = (-9993.23,-8653.14,0)
  FilletRadius = 0
  Length = 12000
  MakeFace = true
  Placement = pos=(1821.99,-6555.4,0) rot=(0,0,1;1.52614rad)
  Points = (2) [(0,0,0),(-2623.14,11709.8,0)]
  Start = (1821.99,-6555.4,0)
  Subdivisions = 0
FEATURE [Part::Part2DObjectPython] Line1694  # Draft 2D object (typed FeaturePython)
  Area = 0
  ChamferSize = 0
  Closed = false
  End = (-9662.73,-8594.46,0)
  FilletRadius = 0
  Length = 12000
  MakeFace = true
  Placement = pos=(2152.5,-6496.72,0) rot=(0,0,1;1.52614rad)
  Points = (2) [(0,0,0),(-2623.14,11709.8,0)]
  Start = (2152.5,-6496.72,0)
  Subdivisions = 0
FEATURE [Part::Part2DObjectPython] Line1695  # Draft 2D object (typed FeaturePython)
  Area = 0
  ChamferSize = 0
  Closed = false
  End = (12611.1,-6540,0)
  FilletRadius = 0
  Length = 12000
  MakeFace = true
  Placement = pos=(611.062,-6540,0) rot=(0,0,1;1.52614rad)
  Points = (2) [(0,0,0),(535.746,-11988,0)]
  Start = (611.062,-6540,0)
  Subdivisions = 0
FEATURE [Part::Part2DObjectPython] Rectangle3390  # Draft 2D object (typed FeaturePython)
  Area = 144400
  ChamferSize = 0
  Columns = 1
  FilletRadius = 0
  Height = 380
  Length = 380
  MakeFace = true
  Placement = pos=(22825.7,-9411.26,0) rot=(0,0,1;1.52614rad)
  Rows = 1
FEATURE [Part::Part2DObjectPython] Rectangle3392  # Draft 2D object (typed FeaturePython)
  Area = 144400
  ChamferSize = 0
  Columns = 1
  FilletRadius = 0
  Height = 380
  Length = 380
  MakeFace = true
  Placement = pos=(24404.1,-9481.8,0) rot=(0,0,1;1.52614rad)
  Rows = 1
FEATURE [Part::Part2DObjectPython] Rectangle3393  # Draft 2D object (typed FeaturePython)
  Area = 144400
  ChamferSize = 0
  Columns = 1
  FilletRadius = 0
  Height = 380
  Length = 380
  MakeFace = true
  Placement = pos=(24644.3,-4107.17,0) rot=(0,0,1;1.52614rad)
  Rows = 1
FEATURE [Part::Part2DObjectPython] Rectangle3395  # Draft 2D object (typed FeaturePython)
  Area = 520000
  ChamferSize = 0
  Columns = 1
  FilletRadius = 0
  Height = 100
  Length = 5200
  MakeFace = true
  Placement = pos=(24037,-9185.12,0) rot=(0,0,1;1.52614rad)
  Rows = 1
FEATURE [Part::Part2DObjectPython] Circle135  label="Circle136"  # Draft 2D object (typed FeaturePython)
  Area = 1.05683e+06
  FirstAngle = 0
  LastAngle = 0
  MakeFace = true
  Placement = pos=(22885.9,-1376.75,0) rot=(0,0,1;1.52614rad)
  Radius = 580
FEATURE [Part::Part2DObjectPython] Line1697  # Draft 2D object (typed FeaturePython)
  Area = 0
  ChamferSize = 0
  Closed = false
  End = (24764.4,-1419.85,0)
  FilletRadius = 0
  Length = 1500
  MakeFace = false
  Placement = pos=(23265.9,-1352.88,0) rot=(0,0,1;1.52614rad)
  Points = (2) [(0,0,0),(-2.50111e-12,-1500,0)]
  Start = (23265.9,-1352.88,0)
  Subdivisions = 0
FEATURE [Part::Part2DObjectPython] Line1699  # Draft 2D object (typed FeaturePython)
  Area = 0
  ChamferSize = 0
  Closed = false
  End = (24840.3,278.455,0)
  FilletRadius = 0
  Length = 1300
  MakeFace = false
  Placement = pos=(23541.6,336.495,0) rot=(0,0,1;1.52614rad)
  Points = (2) [(0,0,0),(6.82121e-13,-1300,0)]
  Start = (23541.6,336.495,0)
  Subdivisions = 0
FEATURE [Part::Part2DObjectPython] Circle136  label="Circle137"  # Draft 2D object (typed FeaturePython)
  Area = 1.05683e+06
  FirstAngle = 0
  LastAngle = 0
  MakeFace = true
  Placement = pos=(22961.8,321.557,0) rot=(0,0,1;1.52614rad)
  Radius = 580
FEATURE [Part::Part2DObjectPython] Line1702  # Draft 2D object (typed FeaturePython)
  Area = 0
  ChamferSize = 0
  Closed = true
  End = (14388.6,662.218,0)
  FilletRadius = 0
  Length = 8000
  MakeFace = true
  Placement = pos=(22381.9,303.842,0) rot=(0,0,1;1.52614rad)
  Points = (2) [(38.1281,1.43103,0),(1.15288,8001.35,0)]
  Start = (22382.2,341.996,0)
  Subdivisions = 0
FEATURE [Part::Part2DObjectPython] Rectangle3400  # Draft 2D object (typed FeaturePython)
  Area = 2.45e+07
  ChamferSize = 0
  Columns = 1
  FilletRadius = 0
  Height = 7000
  Length = 3500
  MakeFace = true
  Placement = pos=(22181.1,-5596.2,0) rot=(0,0,1;1.34139rad)
  Rows = 1
FEATURE [Part::Part2DObjectPython] Line1704  # Draft 2D object (typed FeaturePython)
  Area = 0
  ChamferSize = 0
  Closed = false
  End = (14360.8,-420.719,0)
  FilletRadius = 0
  Length = 5100
  MakeFace = false
  Placement = pos=(19455.7,-648.412,0) rot=(0,0,1;0.025758rad)
  Points = (2) [(0,0,0),(-5087.36,358.837,0)]
  Start = (19455.7,-648.412,0)
  Subdivisions = 0
FEATURE [Part::Part2DObjectPython] Circle140  label="Circle141"  # Draft 2D object (typed FeaturePython)
  Area = 1.05683e+06
  FirstAngle = 0
  LastAngle = 0
  MakeFace = true
  Placement = pos=(21460.2,-1031.22,0) rot=(0,0,1;1.52614rad)
  Radius = 580
FEATURE [Part::Part2DObjectPython] Circle141  label="Circle142"  # Draft 2D object (typed FeaturePython)
  Area = 1.05683e+06
  FirstAngle = 0
  LastAngle = 0
  MakeFace = true
  Placement = pos=(20034.5,-685.694,0) rot=(0,0,1;1.52614rad)
  Radius = 580
FEATURE [Part::Part2DObjectPython] Line1705  # Draft 2D object (typed FeaturePython)
  Area = 0
  ChamferSize = 0
  Closed = true
  End = (22885.9,-1376.75,0)
  FilletRadius = 0
  Length = 2933.93
  MakeFace = false
  Placement = pos=(19875.5,-436.151,0) rot=(0,0,1;0.025758rad)
  Points = (2) [(152.568,-253.556,0),(2985.21,-1017.82,0)]
  Start = (20034.5,-685.694,0)
  Subdivisions = 0
FEATURE [Part::Part2DObjectPython] Circle142  label="Circle143"  # Draft 2D object (typed FeaturePython)
  Area = 1.05683e+06
  FirstAngle = 0
  LastAngle = 0
  MakeFace = true
  Placement = pos=(-7874.87,-6660.56,0) rot=(0,0,1;1.52614rad)
  Radius = 580
FEATURE [Part::Part2DObjectPython] Rectangle3401  # Draft 2D object (typed FeaturePython)
  Area = 9.2e+06
  ChamferSize = 0
  Columns = 1
  FilletRadius = 0
  Height = 2300
  Length = 4000
  MakeFace = true
  Placement = pos=(23704,1728.87,0) rot=(0,0,1;1.52614rad)
  Rows = 1
FEATURE [Part::Part2DObjectPython] Line1706  # Draft 2D object (typed FeaturePython)
  Area = 0
  ChamferSize = 0
  Closed = false
  End = (-8436.54,-6805.24,0)
  FilletRadius = 0
  Length = 1200
  MakeFace = true
  Placement = pos=(-9598.6,-7104.59,0) rot=(0,0,1;1.52614rad)
  Points = (2) [(0,0,0),(350.925,-1147.54,0)]
  Start = (-9598.6,-7104.59,0)
  Subdivisions = 0
FEATURE [Part::Part2DObjectPython] Line1710  # Draft 2D object (typed FeaturePython)
  Area = 0
  ChamferSize = 0
  Closed = false
  End = (14360.8,-7540,0)
  FilletRadius = 0
  Length = 6000
  MakeFace = true
  Placement = pos=(14360.8,-1540,0) rot=(0,0,-1;0.04466rad)
  Points = (2) [(0,0,0),(267.873,-5994.02,0)]
  Start = (14360.8,-1540,0)
  Subdivisions = 0
FEATURE [Part::Part2DObjectPython] Line1711  # Draft 2D object (typed FeaturePython)
  Area = 0
  ChamferSize = 0
  Closed = false
  End = (22185.4,-9292.56,0)
  FilletRadius = 0
  Length = 1800
  MakeFace = true
  Placement = pos=(23983.6,-9372.92,0) rot=(0,0,-1;0.04466rad)
  Points = (2) [(0,0,0),(-1800,-7.27596e-12,0)]
  Start = (23983.6,-9372.92,0)
  Subdivisions = 0
FEATURE [Part::Part2DObjectPython] Line1712  # Draft 2D object (typed FeaturePython)
  Area = 0
  ChamferSize = 0
  Closed = false
  End = (10611.1,-6540,0)
  FilletRadius = 0
  Length = 12157.5
  MakeFace = true
  Placement = pos=(22450.1,-9304.39,0) rot=(0,0,-1;0.04466rad)
  Points = (2) [(0,0,0),(-11950.7,2233.07,0)]
  Start = (22450.1,-9304.39,0)
  Subdivisions = 0
FEATURE [Part::Part2DObjectPython] Line1713  # Draft 2D object (typed FeaturePython)
  Area = 0
  ChamferSize = 0
  Closed = false
  End = (24571.4,-3723.53,0)
  FilletRadius = 0
  Length = 90
  MakeFace = true
  Placement = pos=(24661.3,-3727.55,0) rot=(0,0,-1;0.04466rad)
  Points = (2) [(0,0,0),(-90,1.36424e-12,0)]
  Start = (24661.3,-3727.55,0)
  Subdivisions = 0
FEATURE [Part::Part2DObjectPython] Rectangle3403  label="Контур Строения002"  # Draft 2D object (typed FeaturePython)
  Area = 0
  ChamferSize = 0
  Columns = 1
  FilletRadius = 0
  Height = 8540
  Length = 13640
  MakeFace = false
  Placement = pos=(-560,-540,0) rot=(0,0,1;0rad)
  Rows = 1
FEATURE [Part::Part2DObjectPython] Line1714  # Draft 2D object (typed FeaturePython)
  Area = 0
  ChamferSize = 0
  Closed = false
  End = (-34430.2,9739.91,0)
  FilletRadius = 0
  Length = 7432.67
  MakeFace = true
  Placement = pos=(-41420.8,7214.83,0) rot=(0,0,-1;0.04466rad)
  Points = (2) [(0,0,0),(6870.9,2834.66,0)]
  Start = (-41420.8,7214.83,0)
  Subdivisions = 0
FEATURE [Part::Part2DObjectPython] Line1715  # Draft 2D object (typed FeaturePython)
  Area = 0
  ChamferSize = 0
  Closed = false
  End = (-41420.8,7214.83,0)
  FilletRadius = 0
  Length = 5559.77
  MakeFace = true
  Placement = pos=(-39131,2148.46,0) rot=(0,0,-1;0.04466rad)
  Points = (2) [(0,0,0),(-2513.65,4959.09,0)]
  Start = (-39131,2148.46,0)
  Subdivisions = 0
FEATURE [Part::Part2DObjectPython] Line1716  # Draft 2D object (typed FeaturePython)
  Area = 0
  ChamferSize = 0
  Closed = false
  End = (39960.8,38650.8,0)
  FilletRadius = 0
  Length = 6490.01
  MakeFace = true
  Placement = pos=(37704.2,32565.7,0) rot=(0,0,-1;0.04466rad)
  Points = (2) [(0,0,0),(1982.64,6179.75,0)]
  Start = (37704.2,32565.7,0)
  Subdivisions = 0
FEATURE [Part::Part2DObjectPython] Line1717  # Draft 2D object (typed FeaturePython)
  Area = 0
  ChamferSize = 0
  Closed = false
  End = (39960.8,38650.8,0)
  FilletRadius = 0
  Length = 8107.57
  MakeFace = true
  Placement = pos=(32209.4,41027.5,0) rot=(0,0,-1;0.04466rad)
  Points = (2) [(0,0,0),(7849.75,-2028.32,0)]
  Start = (32209.4,41027.5,0)
  Subdivisions = 0
FEATURE [Part::Part2DObjectPython] Line1718  # Draft 2D object (typed FeaturePython)
  Area = 0
  ChamferSize = 0
  Closed = false
  End = (6260,-6540,0)
  FilletRadius = 0
  Length = 6000
  MakeFace = true
  Placement = pos=(6260,-540,0) rot=(0,0,1;1.52614rad)
  Points = (2) [(0,0,0),(-5994.02,-267.873,0)]
  Start = (6260,-540,0)
  Subdivisions = 0
FEATURE [Part::Part2DObjectPython] Line1719  # Draft 2D object (typed FeaturePython)
  Area = 0
  ChamferSize = 0
  Closed = false
  End = (6198,-7540,0)
  FilletRadius = 0
  Length = 5610
  MakeFace = true
  Placement = pos=(6198,-1930,0) rot=(0,0,1;1.52614rad)
  Points = (2) [(0,0,0),(-5604.41,-250.461,0)]
  Start = (6198,-1930,0)
  Subdivisions = 0
FEATURE [App::DocumentObjectGroup] Group132  label="разное"
  Group = -> [Dimension072,Dimension073,Dimension074,Dimension075,Dimension076,Dimension077,Dimension078,Rectangle3389,Line1687,Line1688,Line1689,Line1690,Line1692,Line1693,Line1694,Line1695,Rectangle3390,Rectangle3392,Rectangle3393,Rectangle3395,Circle135,Line1697,Line1699,Circle136,Line1702,Rectangle3400,Line1704,Circle140,Circle141,Line1705,Circle142,Rectangle3401,Line1706,Line1710,Line1711,Line1712,+8 more]
FEATURE [Part::Part2DObjectPython] Wire907  # Draft 2D object (typed FeaturePython)
  Area = 105625
  ChamferSize = 0
  Closed = true
  End = (5389.62,3825,0)
  FilletRadius = 0
  Length = 1569.24
  MakeFace = true
  Placement = pos=(4930,3825,0) rot=(0,0,1;0rad)
  Points = (3) [(0,0,0),(0,459.62,0),(459.619,0,0)]
  Start = (4930,3825,0)
  Subdivisions = 0
FEATURE [Part::FeaturePython] Structure459  label="кожух инсталляции"  # Arch/BIM 172 (typed FeaturePython)
  Base = -> Wire907
  FaceMaker = 0
  Height = 1150
  HorizontalArea = 105625
  IfcData = attributes={"GlobalId": {"name": "GlobalId", "type": "IfcGloballyUniqueId", "is_enum": false, "enum_values": []}, "Description": {"... (+484 chars omitted),+1 more (map truncated)
  IfcType = 172
  Length = 0
  MoveBase = false
  MoveWithHost = false
  Nodes = (2) [(5083.21,3978.21,0),(5083.21,3978.21,1150)]
  NodesOffset = 0
  Normal = (0,0,1)
  PerimeterLength = 1569.24
  PredefinedType = 0
  VerticalArea = 1.80463e+06
  Width = 100
FEATURE [App::GeometryPython] BuildingPart048  label="Сантехника и мебель в ванной"  # Arch/BIM 52 (typed FeaturePython)
  Area = 3078000
  GlobalId = 2oHchfV$vBmBbFkTdd7Thp
  Group = -> [Structure343,Wall240,Structure347,Component030,Component031,Structure459]
  Height = 0
  HeightPropagate = true
  IfcData = IfcUID=2oHchfV$vBmBbFkTdd7Thp,attributes={"GlobalId": {"value": "2oHchfV$vBmBbFkTdd7Thp"}},+1 more (map truncated)
  IfcType = 52
  LevelOffset = 0
FEATURE [App::GeometryPython] BuildingPart049  label="Обстановка"  # Arch/BIM 52 (typed FeaturePython)
  Area = 3078000
  GlobalId = 01a0HsyVr7nurh2jl2zfI$
  Group = -> [BuildingPart047,BuildingPart048,BuildingPart045]
  Height = 0
  HeightPropagate = true
  IfcData = IfcUID=01a0HsyVr7nurh2jl2zfI$,attributes={"GlobalId": {"value": "01a0HsyVr7nurh2jl2zfI$"}},+1 more (map truncated)
  IfcType = 52
  LevelOffset = 0
FEATURE [Part::Part2DObjectPython] Wire914  # Draft 2D object (typed FeaturePython)
  Area = 0
  ChamferSize = 0
  Closed = false
  End = (3579.3,3604.56,2277.3)
  FilletRadius = 0
  Length = 830.703
  MakeFace = true
  Points = (7) [(3592.14,3618.7,2291.44),(3590,3579,2331.14),(3587.86,3579,2174),(3585.72,3781,2174),(3583.58,3781,2317),(3581.44,3564.86,2317),+1 more]
  Start = (3592.14,3618.7,2291.44)
  Subdivisions = 0
  Support = -> [Wall277]
FEATURE [Part::FeaturePython] Rebar050  label="Stirrup016"  # Arch/BIM 110 (typed FeaturePython)
  Amount = 7
  AmountCheck = false
  Base = -> Wire914
  BentAngle = 135
  BentFactor = 4
  BottomCover = 20
  Diameter = 8
  Direction = (1,0,0)
  Distance = 0
  FrontCover = 100
  HorizontalArea = 0
  Host = -> Wall277
  IfcType = 110
  LeftCover = 20
  Length = 830.703
  Mark = Stirrup016
  Material = -> Material010
  MoveBase = false
  MoveWithHost = false
  OffsetEnd = 104
  OffsetStart = 104
  PerimeterLength = 0
  PlacementList = 7 placements: arithmetic series from (104,0,0) step (204,0,0) to (1328,0,0)
  RebarShape = 3
  RightCover = 20
  Rounding = 1.25
  Spacing = 204
  TopCover = 20
  TotalLength = 5814.92
  TrueSpacing = 250
  VerticalArea = 0
FEATURE [App::DocumentObjectGroupPython] Stirrups016  # scripted group (container) (typed FeaturePython)
  Group = -> [Rebar050]
  Stirrups = -> [Rebar050]
  StirrupsConfiguration = Two Legged Stirrups
FEATURE [Sketcher::SketchObject] Sketch365
  FullyConstrained = false
  MapMode = 5
  Placement = pos=(0,3805,2150) rot=(0,0.707107,0.707107;3.14159rad)
  Support = -> [Wall277]
  sketch-geometry (1):
    g0: LineSegment StartX=-4970 StartY=157 StartZ=0 EndX=-3650 EndY=157 EndZ=0
FEATURE [Part::FeaturePython] Rebar051  label="StraightRebar034"  # Arch/BIM 110 (typed FeaturePython)
  Amount = 2
  AmountCheck = true
  Base = -> Sketch365
  Cover = 28
  CoverAlong = Top Side
  Diameter = 12
  Direction = (0,0,0)
  Distance = 0
  FrontCover = 28
  HorizontalArea = 0
  Host = -> Wall277
  IfcType = 110
  LeftBottomCover = 60
  Length = 1320
  Mark = StraightRebar034
  Material = -> Material010
  MoveBase = false
  MoveWithHost = false
  OffsetEnd = 34
  OffsetStart = 34
  Orientation = Horizontal
  PerimeterLength = 0
  PlacementList = 2 placements: [(0,-34,7.54952e-15),(0,-216,4.79616e-14)]
  RebarShape = 0
  RightTopCover = 60
  Rounding = 0
  Spacing = 182
  TotalLength = 2640
  TrueSpacing = 2
  VerticalArea = 0
FEATURE [App::DocumentObjectGroupPython] TopReinforcement016  # scripted group (container) (typed FeaturePython)
  Group = -> [Rebar051]
  LayerSpacing = [30]
  NumberDiameterOffset = 2#12.0@60.0
  TopRebars = -> [Rebar051]
FEATURE [Sketcher::SketchObject] Sketch366
  FullyConstrained = false
  MapMode = 5
  Placement = pos=(0,3805,2150) rot=(0,0.707107,0.707107;3.14159rad)
  Support = -> [Wall277]
  sketch-geometry (1):
    g0: LineSegment StartX=-4970 StartY=34 StartZ=0 EndX=-3650 EndY=34 EndZ=0
FEATURE [Part::FeaturePython] Rebar052  label="StraightRebar035"  # Arch/BIM 110 (typed FeaturePython)
  Amount = 2
  AmountCheck = true
  Base = -> Sketch366
  Cover = 28
  CoverAlong = Bottom Side
  Diameter = 12
  Direction = (0,0,0)
  Distance = 0
  FrontCover = 28
  HorizontalArea = 0
  Host = -> Wall277
  IfcType = 110
  LeftBottomCover = 60
  Length = 1320
  Mark = StraightRebar035
  Material = -> Material010
  MoveBase = false
  MoveWithHost = false
  OffsetEnd = 34
  OffsetStart = 34
  Orientation = Horizontal
  PerimeterLength = 0
  PlacementList = 2 placements: [(0,-34,7.54952e-15),(0,-216,4.79616e-14)]
  RebarShape = 0
  RightTopCover = 60
  Rounding = 0
  Spacing = 182
  TotalLength = 2640
  TrueSpacing = 2
  VerticalArea = 0
FEATURE [App::DocumentObjectGroupPython] BottomReinforcement016  # scripted group (container) (typed FeaturePython)
  BottomRebars = -> [Rebar052]
  Group = -> [Rebar052]
  LayerSpacing = [30]
  NumberDiameterOffset = 2#12.0@60.0
FEATURE [App::DocumentObjectGroupPython] BeamReinforcement016  label="BeamReinforcement017"  # scripted group (container) (typed FeaturePython)
  Group = -> [Stirrups016,TopReinforcement016,BottomReinforcement016]
  ReinforcementGroups = -> [Stirrups016,TopReinforcement016,BottomReinforcement016]
FEATURE [Part::Part2DObjectPython] Wire915  # Draft 2D object (typed FeaturePython)
  Area = 0
  ChamferSize = 0
  Closed = false
  End = (5529.3,3604.56,2277.3)
  FilletRadius = 0
  Length = 830.703
  MakeFace = true
  Points = (7) [(5542.14,3618.7,2291.44),(5540,3579,2331.14),(5537.86,3579,2174),(5535.72,3781,2174),(5533.58,3781,2317),(5531.44,3564.86,2317),+1 more]
  Start = (5542.14,3618.7,2291.44)
  Subdivisions = 0
  Support = -> [Wall278]
FEATURE [App::DocumentObjectGroup] Draft_Construction  label="Construction"
  Group = -> [Rectangle3159,Line1465,Rectangle3284,Line1478,Line1480,Wire869,Wire871,Wire872,Wire873,Wire874,Wire875,Wire876,Wire877,Wire878,Wire879,Line1626,Wire914,Wire915]
FEATURE [Part::FeaturePython] Rebar053  label="Stirrup017"  # Arch/BIM 110 (typed FeaturePython)
  Amount = 7
  AmountCheck = false
  Base = -> Wire915
  BentAngle = 135
  BentFactor = 4
  BottomCover = 20
  Diameter = 8
  Direction = (1,0,0)
  Distance = 0
  FrontCover = 100
  HorizontalArea = 0
  Host = -> Wall278
  IfcType = 110
  LeftCover = 20
  Length = 830.703
  Mark = Stirrup017
  Material = -> Material010
  MoveBase = false
  MoveWithHost = false
  OffsetEnd = 104
  OffsetStart = 104
  PerimeterLength = 0
  PlacementList = 7 placements: arithmetic series from (104,0,0) step (204,0,0) to (1328,0,0)
  RebarShape = 3
  RightCover = 20
  Rounding = 1.25
  Spacing = 204
  TopCover = 20
  TotalLength = 5814.92
  TrueSpacing = 250
  VerticalArea = 0
FEATURE [App::DocumentObjectGroupPython] Stirrups017  # scripted group (container) (typed FeaturePython)
  Group = -> [Rebar053]
  Stirrups = -> [Rebar053]
  StirrupsConfiguration = Two Legged Stirrups
FEATURE [Sketcher::SketchObject] Sketch367
  FullyConstrained = false
  MapMode = 5
  Placement = pos=(0,3805,2150) rot=(0,0.707107,0.707107;3.14159rad)
  Support = -> [Wall278]
  sketch-geometry (1):
    g0: LineSegment StartX=-6920 StartY=157 StartZ=0 EndX=-5600 EndY=157 EndZ=0
FEATURE [Part::FeaturePython] Rebar054  label="StraightRebar036"  # Arch/BIM 110 (typed FeaturePython)
  Amount = 2
  AmountCheck = true
  Base = -> Sketch367
  Cover = 28
  CoverAlong = Top Side
  Diameter = 12
  Direction = (0,0,0)
  Distance = 0
  FrontCover = 28
  HorizontalArea = 0
  Host = -> Wall278
  IfcType = 110
  LeftBottomCover = 60
  Length = 1320
  Mark = StraightRebar036
  Material = -> Material010
  MoveBase = false
  MoveWithHost = false
  OffsetEnd = 34
  OffsetStart = 34
  Orientation = Horizontal
  PerimeterLength = 0
  PlacementList = 2 placements: [(0,-34,7.54952e-15),(0,-216,4.79616e-14)]
  RebarShape = 0
  RightTopCover = 60
  Rounding = 0
  Spacing = 182
  TotalLength = 2640
  TrueSpacing = 2
  VerticalArea = 0
FEATURE [App::DocumentObjectGroupPython] TopReinforcement017  # scripted group (container) (typed FeaturePython)
  Group = -> [Rebar054]
  LayerSpacing = [30]
  NumberDiameterOffset = 2#12.0@60.0
  TopRebars = -> [Rebar054]
FEATURE [Sketcher::SketchObject] Sketch368
  FullyConstrained = false
  MapMode = 5
  Placement = pos=(0,3805,2150) rot=(0,0.707107,0.707107;3.14159rad)
  Support = -> [Wall278]
  sketch-geometry (1):
    g0: LineSegment StartX=-6920 StartY=34 StartZ=0 EndX=-5600 EndY=34 EndZ=0
FEATURE [Part::FeaturePython] Rebar055  label="StraightRebar037"  # Arch/BIM 110 (typed FeaturePython)
  Amount = 2
  AmountCheck = true
  Base = -> Sketch368
  Cover = 28
  CoverAlong = Bottom Side
  Diameter = 12
  Direction = (0,0,0)
  Distance = 0
  FrontCover = 28
  HorizontalArea = 0
  Host = -> Wall278
  IfcType = 110
  LeftBottomCover = 60
  Length = 1320
  Mark = StraightRebar037
  Material = -> Material010
  MoveBase = false
  MoveWithHost = false
  OffsetEnd = 34
  OffsetStart = 34
  Orientation = Horizontal
  PerimeterLength = 0
  PlacementList = 2 placements: [(0,-34,7.54952e-15),(0,-216,4.79616e-14)]
  RebarShape = 0
  RightTopCover = 60
  Rounding = 0
  Spacing = 182
  TotalLength = 2640
  TrueSpacing = 2
  VerticalArea = 0
FEATURE [App::DocumentObjectGroupPython] BottomReinforcement017  # scripted group (container) (typed FeaturePython)
  BottomRebars = -> [Rebar055]
  Group = -> [Rebar055]
  LayerSpacing = [30]
  NumberDiameterOffset = 2#12.0@60.0
FEATURE [App::DocumentObjectGroupPython] BeamReinforcement017  label="BeamReinforcement018"  # scripted group (container) (typed FeaturePython)
  Group = -> [Stirrups017,TopReinforcement017,BottomReinforcement017]
  ReinforcementGroups = -> [Stirrups017,TopReinforcement017,BottomReinforcement017]
FEATURE [App::GeometryPython] BuildingPart096  label="Армирование перемычек"  # Arch/BIM 111 (typed FeaturePython)
  Area = 0
  GlobalId = 0M_P_ho1jD6Ar$JhrFI58w
  Group = -> [BeamReinforcement011,BeamReinforcement010,BeamReinforcement009,BeamReinforcement008,BeamReinforcement007,BeamReinforcement006,BeamReinforcement004,BeamReinforcement003,BeamReinforcement001,BeamReinforcement,BeamReinforcement002,BeamReinforcement005,BeamReinforcement016,BeamReinforcement017]
  Height = 0
  HeightPropagate = true
  IfcData = IfcUID=0M_P_ho1jD6Ar$JhrFI58w,+2 more (map truncated)
  IfcType = 111
  LevelOffset = 0
FEATURE [App::GeometryPython] BuildingPart002  label="Стены несущие"  # Arch/BIM 52 (typed FeaturePython)
  Area = 168045630
  GlobalId = 3CS7VrtqL2RQvRhQ1$1d0X
  Group = -> [Wall004,Wall214,BuildingPart088,BuildingPart089,BuildingPart096]
  Height = 0
  HeightPropagate = true
  IfcData = IfcUID=3CS7VrtqL2RQvRhQ1$1d0X,attributes={"GlobalId": {"value": "3CS7VrtqL2RQvRhQ1$1d0X"}},+1 more (map truncated)
  IfcType = 52
  LevelOffset = 0
FEATURE [Sketcher::SketchObject] Sketch369
  FullyConstrained = true
  Placement = pos=(5810,3535,0) rot=(1,0,0;1.5708rad)
  sketch-geometry (8):
    g0: LineSegment StartX=0 StartY=0 StartZ=0 EndX=900 EndY=0 EndZ=0
    g1: LineSegment StartX=900 StartY=0 StartZ=0 EndX=900 EndY=2150 EndZ=0
    g2: LineSegment StartX=900 StartY=2150 StartZ=0 EndX=0 EndY=2150 EndZ=0
    g3: LineSegment StartX=0 StartY=2150 StartZ=0 EndX=0 EndY=0 EndZ=0
    g4: LineSegment StartX=50 StartY=0 StartZ=0 EndX=850 EndY=0 EndZ=0
    g5: LineSegment StartX=850 StartY=0 StartZ=0 EndX=850 EndY=2100 EndZ=0
    g6: LineSegment StartX=850 StartY=2100 StartZ=0 EndX=50 EndY=2100 EndZ=0
    g7: LineSegment StartX=50 StartY=2100 StartZ=0 EndX=50 EndY=0 EndZ=0
  constraints (23):
    c: Coincident(g0,g1)
    c: Coincident(g1,g2)
    c: Coincident(g2,g3)
    c: Coincident(g3,g0)
    c: Horizontal(g0)
    c: Horizontal(g2)
    c: Vertical(g1)
    c: Vertical(g3)
    c: Coincident(g4,g5)
    c: Coincident(g5,g6)
    c: Coincident(g6,g7)
    c: Coincident(g7,g4)
    c: Horizontal(g4)
    c: Horizontal(g6)
    c: Vertical(g5)
    c: Vertical(g7)
    c: DistanceY(g1) = 2150  'Height'
    c: DistanceX(g0) = 900  'Width'
    c: DistanceY(g6,g2) = 50  'Frame1'
    c: DistanceX(g2,g6) = 50  'Frame2'
    c: DistanceX(g4,g0) = 50  'Frame3'
    c: DistanceY(g0,g4) = 0
    c: Coincident(g0,g-1)
FEATURE [Part::FeaturePython] Window068  label="Д-90-006"  # Arch/BIM 41 (typed FeaturePython)
  Area = 1935000
  Base = -> Sketch369
  Frame = 50
  GlobalId = 00iW5F1Zz0_RepVZ61wedb
  Height = 2150
  HoleDepth = 0
  HoleWire = 0
  HorizontalArea = 0
  IfcData = IfcUID=00iW5F1Zz0_RepVZ61wedb; attributes={"OverallHeight": {"value": 2150.0}, "OverallWidth": {"value": 900.0}, "GlobalId": {"value": "00iW5F1Zz0_RepVZ61wedb"}}
  IfcType = 41
  LouvreSpacing = 0
  LouvreWidth = 0
  Material = -> Material011
  MoveBase = false
  MoveWithHost = true
  Normal = (0,1,0)
  Opening = 0
  OperationType = 0
  OverallHeight = 2150
  OverallWidth = 900
  PerimeterLength = 0
  Placement = pos=(0,50,0) rot=(0,0,1;0rad)
  PredefinedType = 0
  Preset = 6
  SymbolElevation = false
  SymbolPlan = false
  VerticalArea = 0
  Width = 900
  WindowParts = OuterFrame | Frame | Wire0,Wire1 | 0.0+V | 0.00+V | Door | Solid panel | Wire1 | 50.0 | 0.0+V
  expr: OverallHeight = .Height.Value
  expr: OverallWidth = .Width.Value
FEATURE [Sketcher::SketchObject] Sketch370
  FullyConstrained = true
  Placement = pos=(6005,7895,960) rot=(0,0.707107,0.707107;3.14159rad)
  sketch-geometry (16):
    g0: LineSegment StartX=0 StartY=0 StartZ=0 EndX=920 EndY=0 EndZ=0
    g1: LineSegment StartX=920 StartY=0 StartZ=0 EndX=920 EndY=1610 EndZ=0
    g2: LineSegment StartX=920 StartY=1610 StartZ=0 EndX=0 EndY=1610 EndZ=0
    g3: LineSegment StartX=0 StartY=1610 StartZ=0 EndX=0 EndY=0 EndZ=0
    g4: LineSegment StartX=70 StartY=70 StartZ=0 EndX=850 EndY=70 EndZ=0
    g5: LineSegment StartX=850 StartY=70 StartZ=0 EndX=850 EndY=1540 EndZ=0
    g6: LineSegment StartX=850 StartY=1540 StartZ=0 EndX=70 EndY=1540 EndZ=0
    g7: LineSegment StartX=70 StartY=1540 StartZ=0 EndX=70 EndY=70 EndZ=0
    g8: LineSegment StartX=77 StartY=77 StartZ=0 EndX=843 EndY=77 EndZ=0
    g9: LineSegment StartX=843 StartY=77 StartZ=0 EndX=843 EndY=1533 EndZ=0
    g10: LineSegment StartX=843 StartY=1533 StartZ=0 EndX=77 EndY=1533 EndZ=0
    g11: LineSegment StartX=77 StartY=1533 StartZ=0 EndX=77 EndY=77 EndZ=0
    g12: LineSegment StartX=117 StartY=117 StartZ=0 EndX=803 EndY=117 EndZ=0
    g13: LineSegment StartX=803 StartY=117 StartZ=0 EndX=803 EndY=1493 EndZ=0
    g14: LineSegment StartX=803 StartY=1493 StartZ=0 EndX=117 EndY=1493 EndZ=0
    g15: LineSegment StartX=117 StartY=1493 StartZ=0 EndX=117 EndY=117 EndZ=0
  constraints (47):
    c: Coincident(g0,g1)
    c: Coincident(g1,g2)
    c: Coincident(g2,g3)
    c: Coincident(g3,g0)
    c: Horizontal(g0)
    c: Horizontal(g2)
    c: Vertical(g1)
    c: Vertical(g3)
    c: Coincident(g4,g5)
    c: Coincident(g5,g6)
    c: Coincident(g6,g7)
    c: Coincident(g7,g4)
    c: Horizontal(g4)
    c: Horizontal(g6)
    c: Vertical(g5)
    c: Vertical(g7)
    c: DistanceY(g1) = 1610  'Height'
    c: DistanceX(g0) = 920  'Width'
    c: DistanceY(g6,g2) = 70  'Frame1'
    c: DistanceX(g2,g6) = 70  'Frame2'
    c: DistanceX(g4,g0) = 70  'Frame3'
    c: DistanceY(g0,g4) = 70  'Frame4'
    c: Coincident(g0,g-1)
    c: Coincident(g8,g9)
    c: Coincident(g9,g10)
    c: Coincident(g10,g11)
    c: Coincident(g11,g8)
    c: Horizontal(g8)
    c: Horizontal(g10)
    c: Vertical(g9)
    c: Vertical(g11)
    c: Coincident(g12,g13)
    c: Coincident(g13,g14)
    c: Coincident(g14,g15)
    c: Coincident(g15,g12)
    c: Horizontal(g12)
    c: Horizontal(g14)
    c: Vertical(g13)
    c: Vertical(g15)
    c: DistanceX(g8,g12) = 40
    c: DistanceY(g8,g12) = 40
    c: DistanceX(g14,g10) = 40
    c: DistanceY(g14,g10) = 40
    c: DistanceX(g4,g8) = 7
    c: DistanceY(g4,g8) = 7
    c: DistanceX(g10,g6) = 7
    c: DistanceY(g10,g6) = 7
FEATURE [Part::FeaturePython] Window  label="ОК-92/161-001"  # Arch/BIM 170 (typed FeaturePython)
  Area = 1481200
  Base = -> Sketch370
  Frame = 70
  Height = 1610
  HoleDepth = 0
  HoleWire = 0
  HorizontalArea = 0
  IfcData = attributes={"GlobalId": {"name": "GlobalId", "type": "IfcGloballyUniqueId", "is_enum": false, "enum_values": []}, "Description": {"... (+1230 chars omitted),+1 more (map truncated)
  IfcType = 170
  LouvreSpacing = 0
  LouvreWidth = 0
  Material = -> Material011
  MoveBase = false
  MoveWithHost = true
  Normal = (0,-1,2e-16)
  Opening = 0
  OverallHeight = 1610
  OverallWidth = 920
  PartitioningType = 0
  PerimeterLength = 0
  PredefinedType = 0
  Preset = 2
  SymbolElevation = false
  SymbolPlan = false
  VerticalArea = 0
  Width = 920
  WindowParts = OuterFrame | Frame | Wire0,Wire1 | 0.0+V | 0.00+V | InnerFrame | Frame | Wire2,Wire3,Edge8,Mode1 | 0.00+V | 0.0+V | InnerGlass | Glass panel | Wire3 | 8.0 | 40.0+V
  expr: OverallHeight = .Height.Value
  expr: OverallWidth = .Width.Value
FEATURE [Sketcher::SketchObject] Sketch371
  FullyConstrained = true
  Placement = pos=(3925,7895,960) rot=(0,0.707107,0.707107;3.14159rad)
  sketch-geometry (24):
    g0: LineSegment StartX=0 StartY=0 StartZ=0 EndX=1960 EndY=0 EndZ=0
    g1: LineSegment StartX=1960 StartY=0 StartZ=0 EndX=1960 EndY=1610 EndZ=0
    g2: LineSegment StartX=1960 StartY=1610 StartZ=0 EndX=0 EndY=1610 EndZ=0
    g3: LineSegment StartX=0 StartY=1610 StartZ=0 EndX=0 EndY=0 EndZ=0
    g4: LineSegment StartX=70 StartY=70 StartZ=0 EndX=1890 EndY=70 EndZ=0
    g5: LineSegment StartX=1890 StartY=70 StartZ=0 EndX=1890 EndY=1540 EndZ=0
    g6: LineSegment StartX=1890 StartY=1540 StartZ=0 EndX=70 EndY=1540 EndZ=0
    g7: LineSegment StartX=70 StartY=1540 StartZ=0 EndX=70 EndY=70 EndZ=0
    g8: LineSegment StartX=77 StartY=77 StartZ=0 EndX=976.5 EndY=77 EndZ=0
    g9: LineSegment StartX=976.5 StartY=77 StartZ=0 EndX=976.5 EndY=1533 EndZ=0
    g10: LineSegment StartX=976.5 StartY=1533 StartZ=0 EndX=77 EndY=1533 EndZ=0
    g11: LineSegment StartX=77 StartY=1533 StartZ=0 EndX=77 EndY=77 EndZ=0
    g12: LineSegment StartX=117 StartY=117 StartZ=0 EndX=936.5 EndY=117 EndZ=0
    g13: LineSegment StartX=936.5 StartY=117 StartZ=0 EndX=936.5 EndY=1493 EndZ=0
    g14: LineSegment StartX=936.5 StartY=1493 StartZ=0 EndX=117 EndY=1493 EndZ=0
    g15: LineSegment StartX=117 StartY=1493 StartZ=0 EndX=117 EndY=117 EndZ=0
    g16: LineSegment StartX=983.5 StartY=77 StartZ=0 EndX=1883 EndY=77 EndZ=0
    g17: LineSegment StartX=1883 StartY=77 StartZ=0 EndX=1883 EndY=1533 EndZ=0
    g18: LineSegment StartX=1883 StartY=1533 StartZ=0 EndX=983.5 EndY=1533 EndZ=0
    g19: LineSegment StartX=983.5 StartY=1533 StartZ=0 EndX=983.5 EndY=77 EndZ=0
    g20: LineSegment StartX=1023.5 StartY=117 StartZ=0 EndX=1843 EndY=117 EndZ=0
    g21: LineSegment StartX=1843 StartY=117 StartZ=0 EndX=1843 EndY=1493 EndZ=0
    g22: LineSegment StartX=1843 StartY=1493 StartZ=0 EndX=1023.5 EndY=1493 EndZ=0
    g23: LineSegment StartX=1023.5 StartY=1493 StartZ=0 EndX=1023.5 EndY=117 EndZ=0
  constraints (71):
    c: Coincident(g0,g1)
    c: Coincident(g1,g2)
    c: Coincident(g2,g3)
    c: Coincident(g3,g0)
    c: Horizontal(g0)
    c: Horizontal(g2)
    c: Vertical(g1)
    c: Vertical(g3)
    c: Coincident(g4,g5)
    c: Coincident(g5,g6)
    c: Coincident(g6,g7)
    c: Coincident(g7,g4)
    c: Horizontal(g4)
    c: Horizontal(g6)
    c: Vertical(g5)
    c: Vertical(g7)
    c: DistanceY(g1) = 1610  'Height'
    c: DistanceX(g0) = 1960  'Width'
    c: DistanceY(g6,g2) = 70  'Frame1'
    c: DistanceX(g2,g6) = 70  'Frame2'
    c: DistanceX(g4,g0) = 70  'Frame3'
    c: DistanceY(g0,g4) = 70  'Frame4'
    c: Coincident(g0,g-1)
    c: Coincident(g8,g9)
    c: Coincident(g9,g10)
    c: Coincident(g10,g11)
    c: Coincident(g11,g8)
    c: Horizontal(g8)
    c: Horizontal(g10)
    c: Vertical(g9)
    c: Vertical(g11)
    c: Coincident(g12,g13)
    c: Coincident(g13,g14)
    c: Coincident(g14,g15)
    c: Coincident(g15,g12)
    c: Horizontal(g12)
    c: Horizontal(g14)
    c: Vertical(g13)
    c: Vertical(g15)
    c: Coincident(g16,g17)
    c: Coincident(g17,g18)
    c: Coincident(g18,g19)
    c: Coincident(g19,g16)
    c: Horizontal(g16)
    c: Horizontal(g18)
    c: Vertical(g17)
    c: Vertical(g19)
    c: Coincident(g20,g21)
    c: Coincident(g21,g22)
    c: Coincident(g22,g23)
    c: Coincident(g23,g20)
    c: Horizontal(g20)
    c: Horizontal(g22)
    c: Vertical(g21)
    c: Vertical(g23)
    c: DistanceY(g8,g12) = 40
    c: DistanceX(g8,g12) = 40
    c: DistanceX(g21,g17) = 40
    c: DistanceY(g21,g17) = 40
    c: DistanceX(g16,g20) = 40
    c: DistanceX(g14,g10) = 40
    c: Equal(g22,g14)
    c: DistanceY(g8,g16) = 0
    c: DistanceY(g10,g18) = 0
    c: DistanceX(g4,g8) = 7
    c: DistanceY(g4,g8) = 7
    c: DistanceX(g6,g18) = -7
    c: DistanceY(g6,g18) = -7
    c: DistanceX(g9,g19) = 7
    c: PointOnObject(g13,g22)
    c: PointOnObject(g20,g12)
FEATURE [Part::FeaturePython] Window069  label="ОК-196/161-001"  # Arch/BIM 170 (typed FeaturePython)
  Area = 3155600
  Base = -> Sketch371
  Frame = 70
  Height = 1610
  HoleDepth = 0
  HoleWire = 0
  HorizontalArea = 0
  IfcData = attributes={"GlobalId": {"name": "GlobalId", "type": "IfcGloballyUniqueId", "is_enum": false, "enum_values": []}, "Description": {"... (+1231 chars omitted),+1 more (map truncated)
  IfcType = 170
  LouvreSpacing = 0
  LouvreWidth = 0
  Material = -> Material011
  MoveBase = false
  MoveWithHost = true
  Normal = (0,-1,2e-16)
  Opening = 0
  OverallHeight = 1610
  OverallWidth = 1960
  PartitioningType = 0
  PerimeterLength = 0
  PredefinedType = 0
  Preset = 3
  SymbolElevation = false
  SymbolPlan = false
  VerticalArea = 0
  Width = 1960
  WindowParts = OuterFrame | Frame | Wire0,Wire1 | 0.0+V | 0.00+V | LeftFrame | Frame | Wire2,Wire3,Edge8,Mode1 | 0.00+V | 0.0+V | LeftGlass | Glass panel | Wire3 | 8.0 | 40.0+V | RightFrame | Frame | Wire4,Wire5,Edge6,Mode2 | 0.00+V | 0.0+V | RightGlass | Glass panel | Wire5 | 8.0 | 40.0+V
  expr: OverallHeight = .Height.Value
  expr: OverallWidth = .Width.Value
FEATURE [Sketcher::SketchObject] Sketch372
  FullyConstrained = true
  Placement = pos=(-440,3280,960) rot=(0.57735,-0.57735,-0.57735;2.0944rad)
  sketch-geometry (24):
    g0: LineSegment StartX=0 StartY=0 StartZ=0 EndX=1440 EndY=0 EndZ=0
    g1: LineSegment StartX=1440 StartY=0 StartZ=0 EndX=1440 EndY=1610 EndZ=0
    g2: LineSegment StartX=1440 StartY=1610 StartZ=0 EndX=0 EndY=1610 EndZ=0
    g3: LineSegment StartX=0 StartY=1610 StartZ=0 EndX=0 EndY=0 EndZ=0
    g4: LineSegment StartX=70 StartY=70 StartZ=0 EndX=1370 EndY=70 EndZ=0
    g5: LineSegment StartX=1370 StartY=70 StartZ=0 EndX=1370 EndY=1540 EndZ=0
    g6: LineSegment StartX=1370 StartY=1540 StartZ=0 EndX=70 EndY=1540 EndZ=0
    g7: LineSegment StartX=70 StartY=1540 StartZ=0 EndX=70 EndY=70 EndZ=0
    g8: LineSegment StartX=77 StartY=77 StartZ=0 EndX=716.5 EndY=77 EndZ=0
    g9: LineSegment StartX=716.5 StartY=77 StartZ=0 EndX=716.5 EndY=1533 EndZ=0
    g10: LineSegment StartX=716.5 StartY=1533 StartZ=0 EndX=77 EndY=1533 EndZ=0
    g11: LineSegment StartX=77 StartY=1533 StartZ=0 EndX=77 EndY=77 EndZ=0
    g12: LineSegment StartX=117 StartY=117 StartZ=0 EndX=676.5 EndY=117 EndZ=0
    g13: LineSegment StartX=676.5 StartY=117 StartZ=0 EndX=676.5 EndY=1493 EndZ=0
    g14: LineSegment StartX=676.5 StartY=1493 StartZ=0 EndX=117 EndY=1493 EndZ=0
    g15: LineSegment StartX=117 StartY=1493 StartZ=0 EndX=117 EndY=117 EndZ=0
    g16: LineSegment StartX=723.5 StartY=77 StartZ=0 EndX=1363 EndY=77 EndZ=0
    g17: LineSegment StartX=1363 StartY=77 StartZ=0 EndX=1363 EndY=1533 EndZ=0
    g18: LineSegment StartX=1363 StartY=1533 StartZ=0 EndX=723.5 EndY=1533 EndZ=0
    g19: LineSegment StartX=723.5 StartY=1533 StartZ=0 EndX=723.5 EndY=77 EndZ=0
    g20: LineSegment StartX=763.5 StartY=117 StartZ=0 EndX=1323 EndY=117 EndZ=0
    g21: LineSegment StartX=1323 StartY=117 StartZ=0 EndX=1323 EndY=1493 EndZ=0
    g22: LineSegment StartX=1323 StartY=1493 StartZ=0 EndX=763.5 EndY=1493 EndZ=0
    g23: LineSegment StartX=763.5 StartY=1493 StartZ=0 EndX=763.5 EndY=117 EndZ=0
  constraints (71):
    c: Coincident(g0,g1)
    c: Coincident(g1,g2)
    c: Coincident(g2,g3)
    c: Coincident(g3,g0)
    c: Horizontal(g0)
    c: Horizontal(g2)
    c: Vertical(g1)
    c: Vertical(g3)
    c: Coincident(g4,g5)
    c: Coincident(g5,g6)
    c: Coincident(g6,g7)
    c: Coincident(g7,g4)
    c: Horizontal(g4)
    c: Horizontal(g6)
    c: Vertical(g5)
    c: Vertical(g7)
    c: DistanceY(g1) = 1610  'Height'
    c: DistanceX(g0) = 1440  'Width'
    c: DistanceY(g6,g2) = 70  'Frame1'
    c: DistanceX(g2,g6) = 70  'Frame2'
    c: DistanceX(g4,g0) = 70  'Frame3'
    c: DistanceY(g0,g4) = 70  'Frame4'
    c: Coincident(g0,g-1)
    c: Coincident(g8,g9)
    c: Coincident(g9,g10)
    c: Coincident(g10,g11)
    c: Coincident(g11,g8)
    c: Horizontal(g8)
    c: Horizontal(g10)
    c: Vertical(g9)
    c: Vertical(g11)
    c: Coincident(g12,g13)
    c: Coincident(g13,g14)
    c: Coincident(g14,g15)
    c: Coincident(g15,g12)
    c: Horizontal(g12)
    c: Horizontal(g14)
    c: Vertical(g13)
    c: Vertical(g15)
    c: Coincident(g16,g17)
    c: Coincident(g17,g18)
    c: Coincident(g18,g19)
    c: Coincident(g19,g16)
    c: Horizontal(g16)
    c: Horizontal(g18)
    c: Vertical(g17)
    c: Vertical(g19)
    c: Coincident(g20,g21)
    c: Coincident(g21,g22)
    c: Coincident(g22,g23)
    c: Coincident(g23,g20)
    c: Horizontal(g20)
    c: Horizontal(g22)
    c: Vertical(g21)
    c: Vertical(g23)
    c: DistanceY(g8,g12) = 40
    c: DistanceX(g8,g12) = 40
    c: DistanceX(g21,g17) = 40
    c: DistanceY(g21,g17) = 40
    c: DistanceX(g16,g20) = 40
    c: DistanceX(g14,g10) = 40
    c: Equal(g22,g14)
    c: DistanceY(g8,g16) = 0
    c: DistanceY(g10,g18) = 0
    c: DistanceX(g4,g8) = 7
    c: DistanceY(g4,g8) = 7
    c: DistanceX(g6,g18) = -7
    c: DistanceY(g6,g18) = -7
    c: DistanceX(g9,g19) = 7
    c: PointOnObject(g13,g22)
    c: PointOnObject(g20,g12)
FEATURE [Part::FeaturePython] Window070  label="ОК-144/161-001"  # Arch/BIM 170 (typed FeaturePython)
  Area = 2318400
  Base = -> Sketch372
  Frame = 70
  Height = 1610
  HoleDepth = 0
  HoleWire = 0
  HorizontalArea = 0
  IfcData = attributes={"GlobalId": {"name": "GlobalId", "type": "IfcGloballyUniqueId", "is_enum": false, "enum_values": []}, "Description": {"... (+1231 chars omitted),+1 more (map truncated)
  IfcType = 170
  LouvreSpacing = 0
  LouvreWidth = 0
  Material = -> Material011
  MoveBase = false
  MoveWithHost = true
  Normal = (1,0,0)
  Opening = 0
  OverallHeight = 1610
  OverallWidth = 1440
  PartitioningType = 0
  PerimeterLength = 0
  PredefinedType = 0
  Preset = 3
  SymbolElevation = false
  SymbolPlan = false
  VerticalArea = 0
  Width = 1440
  WindowParts = <same value as first occurrence — deduplicated (x3 in doc)>
  expr: OverallHeight = .Height.Value
  expr: OverallWidth = .Width.Value
FEATURE [Sketcher::SketchObject] Sketch373
  FullyConstrained = true
  Placement = pos=(12960,1320,1190) rot=(0.57735,0.57735,0.57735;2.0944rad)
  sketch-geometry (24):
    g0: LineSegment StartX=0 StartY=0 StartZ=0 EndX=1960 EndY=0 EndZ=0
    g1: LineSegment StartX=1960 StartY=0 StartZ=0 EndX=1960 EndY=1380 EndZ=0
    g2: LineSegment StartX=1960 StartY=1380 StartZ=0 EndX=0 EndY=1380 EndZ=0
    g3: LineSegment StartX=0 StartY=1380 StartZ=0 EndX=0 EndY=0 EndZ=0
    g4: LineSegment StartX=70 StartY=70 StartZ=0 EndX=1890 EndY=70 EndZ=0
    g5: LineSegment StartX=1890 StartY=70 StartZ=0 EndX=1890 EndY=1310 EndZ=0
    g6: LineSegment StartX=1890 StartY=1310 StartZ=0 EndX=70 EndY=1310 EndZ=0
    g7: LineSegment StartX=70 StartY=1310 StartZ=0 EndX=70 EndY=70 EndZ=0
    g8: LineSegment StartX=77 StartY=77 StartZ=0 EndX=976.5 EndY=77 EndZ=0
    g9: LineSegment StartX=976.5 StartY=77 StartZ=0 EndX=976.5 EndY=1303 EndZ=0
    g10: LineSegment StartX=976.5 StartY=1303 StartZ=0 EndX=77 EndY=1303 EndZ=0
    g11: LineSegment StartX=77 StartY=1303 StartZ=0 EndX=77 EndY=77 EndZ=0
    g12: LineSegment StartX=117 StartY=117 StartZ=0 EndX=936.5 EndY=117 EndZ=0
    g13: LineSegment StartX=936.5 StartY=117 StartZ=0 EndX=936.5 EndY=1263 EndZ=0
    g14: LineSegment StartX=936.5 StartY=1263 StartZ=0 EndX=117 EndY=1263 EndZ=0
    g15: LineSegment StartX=117 StartY=1263 StartZ=0 EndX=117 EndY=117 EndZ=0
    g16: LineSegment StartX=983.5 StartY=77 StartZ=0 EndX=1883 EndY=77 EndZ=0
    g17: LineSegment StartX=1883 StartY=77 StartZ=0 EndX=1883 EndY=1303 EndZ=0
    g18: LineSegment StartX=1883 StartY=1303 StartZ=0 EndX=983.5 EndY=1303 EndZ=0
    g19: LineSegment StartX=983.5 StartY=1303 StartZ=0 EndX=983.5 EndY=77 EndZ=0
    g20: LineSegment StartX=1023.5 StartY=117 StartZ=0 EndX=1843 EndY=117 EndZ=0
    g21: LineSegment StartX=1843 StartY=117 StartZ=0 EndX=1843 EndY=1263 EndZ=0
    g22: LineSegment StartX=1843 StartY=1263 StartZ=0 EndX=1023.5 EndY=1263 EndZ=0
    g23: LineSegment StartX=1023.5 StartY=1263 StartZ=0 EndX=1023.5 EndY=117 EndZ=0
  constraints (71):
    c: Coincident(g0,g1)
    c: Coincident(g1,g2)
    c: Coincident(g2,g3)
    c: Coincident(g3,g0)
    c: Horizontal(g0)
    c: Horizontal(g2)
    c: Vertical(g1)
    c: Vertical(g3)
    c: Coincident(g4,g5)
    c: Coincident(g5,g6)
    c: Coincident(g6,g7)
    c: Coincident(g7,g4)
    c: Horizontal(g4)
    c: Horizontal(g6)
    c: Vertical(g5)
    c: Vertical(g7)
    c: DistanceY(g1) = 1380  'Height'
    c: DistanceX(g0) = 1960  'Width'
    c: DistanceY(g6,g2) = 70  'Frame1'
    c: DistanceX(g2,g6) = 70  'Frame2'
    c: DistanceX(g4,g0) = 70  'Frame3'
    c: DistanceY(g0,g4) = 70  'Frame4'
    c: Coincident(g0,g-1)
    c: Coincident(g8,g9)
    c: Coincident(g9,g10)
    c: Coincident(g10,g11)
    c: Coincident(g11,g8)
    c: Horizontal(g8)
    c: Horizontal(g10)
    c: Vertical(g9)
    c: Vertical(g11)
    c: Coincident(g12,g13)
    c: Coincident(g13,g14)
    c: Coincident(g14,g15)
    c: Coincident(g15,g12)
    c: Horizontal(g12)
    c: Horizontal(g14)
    c: Vertical(g13)
    c: Vertical(g15)
    c: Coincident(g16,g17)
    c: Coincident(g17,g18)
    c: Coincident(g18,g19)
    c: Coincident(g19,g16)
    c: Horizontal(g16)
    c: Horizontal(g18)
    c: Vertical(g17)
    c: Vertical(g19)
    c: Coincident(g20,g21)
    c: Coincident(g21,g22)
    c: Coincident(g22,g23)
    c: Coincident(g23,g20)
    c: Horizontal(g20)
    c: Horizontal(g22)
    c: Vertical(g21)
    c: Vertical(g23)
    c: DistanceY(g8,g12) = 40
    c: DistanceX(g8,g12) = 40
    c: DistanceX(g21,g17) = 40
    c: DistanceY(g21,g17) = 40
    c: DistanceX(g16,g20) = 40
    c: DistanceX(g14,g10) = 40
    c: Equal(g22,g14)
    c: DistanceY(g8,g16) = 0
    c: DistanceY(g10,g18) = 0
    c: DistanceX(g4,g8) = 7
    c: DistanceY(g4,g8) = 7
    c: DistanceX(g6,g18) = -7
    c: DistanceY(g6,g18) = -7
    c: DistanceX(g9,g19) = 7
    c: PointOnObject(g13,g22)
    c: PointOnObject(g20,g12)
FEATURE [Part::FeaturePython] Window071  label="ОК-196/138-001"  # Arch/BIM 170 (typed FeaturePython)
  Area = 2704800
  Base = -> Sketch373
  Frame = 70
  Height = 1380
  HoleDepth = 0
  HoleWire = 0
  HorizontalArea = 0
  IfcData = attributes={"GlobalId": {"name": "GlobalId", "type": "IfcGloballyUniqueId", "is_enum": false, "enum_values": []}, "Description": {"... (+1231 chars omitted),+1 more (map truncated)
  IfcType = 170
  LouvreSpacing = 0
  LouvreWidth = 0
  Material = -> Material011
  MoveBase = false
  MoveWithHost = true
  Normal = (-1,0,0)
  Opening = 0
  OverallHeight = 1380
  OverallWidth = 1960
  PartitioningType = 0
  PerimeterLength = 0
  PredefinedType = 0
  Preset = 3
  SymbolElevation = false
  SymbolPlan = false
  VerticalArea = 0
  Width = 1960
  WindowParts = <same value as first occurrence — deduplicated (x3 in doc)>
  expr: OverallHeight = .Height.Value
  expr: OverallWidth = .Width.Value
FEATURE [Sketcher::SketchObject] Sketch374
  FullyConstrained = true
  Placement = pos=(12960,4050,0) rot=(0.57735,0.57735,0.57735;2.0944rad)
  sketch-geometry (16):
    g0: LineSegment StartX=0 StartY=0 StartZ=0 EndX=920 EndY=0 EndZ=0
    g1: LineSegment StartX=920 StartY=0 StartZ=0 EndX=920 EndY=1380 EndZ=0
    g2: LineSegment StartX=920 StartY=1380 StartZ=0 EndX=0 EndY=1380 EndZ=0
    g3: LineSegment StartX=0 StartY=1380 StartZ=0 EndX=0 EndY=0 EndZ=0
    g4: LineSegment StartX=70 StartY=70 StartZ=0 EndX=850 EndY=70 EndZ=0
    g5: LineSegment StartX=850 StartY=70 StartZ=0 EndX=850 EndY=1310 EndZ=0
    g6: LineSegment StartX=850 StartY=1310 StartZ=0 EndX=70 EndY=1310 EndZ=0
    g7: LineSegment StartX=70 StartY=1310 StartZ=0 EndX=70 EndY=70 EndZ=0
    g8: LineSegment StartX=77 StartY=77 StartZ=0 EndX=843 EndY=77 EndZ=0
    g9: LineSegment StartX=843 StartY=77 StartZ=0 EndX=843 EndY=1303 EndZ=0
    g10: LineSegment StartX=843 StartY=1303 StartZ=0 EndX=77 EndY=1303 EndZ=0
    g11: LineSegment StartX=77 StartY=1303 StartZ=0 EndX=77 EndY=77 EndZ=0
    g12: LineSegment StartX=117 StartY=117 StartZ=0 EndX=803 EndY=117 EndZ=0
    g13: LineSegment StartX=803 StartY=117 StartZ=0 EndX=803 EndY=1263 EndZ=0
    g14: LineSegment StartX=803 StartY=1263 StartZ=0 EndX=117 EndY=1263 EndZ=0
    g15: LineSegment StartX=117 StartY=1263 StartZ=0 EndX=117 EndY=117 EndZ=0
  constraints (47):
    c: Coincident(g0,g1)
    c: Coincident(g1,g2)
    c: Coincident(g2,g3)
    c: Coincident(g3,g0)
    c: Horizontal(g0)
    c: Horizontal(g2)
    c: Vertical(g1)
    c: Vertical(g3)
    c: Coincident(g4,g5)
    c: Coincident(g5,g6)
    c: Coincident(g6,g7)
    c: Coincident(g7,g4)
    c: Horizontal(g4)
    c: Horizontal(g6)
    c: Vertical(g5)
    c: Vertical(g7)
    c: DistanceY(g1) = 1380  'Height'
    c: DistanceX(g0) = 920  'Width'
    c: DistanceY(g6,g2) = 70  'Frame1'
    c: DistanceX(g2,g6) = 70  'Frame2'
    c: DistanceX(g4,g0) = 70  'Frame3'
    c: DistanceY(g0,g4) = 70  'Frame4'
    c: Coincident(g0,g-1)
    c: Coincident(g8,g9)
    c: Coincident(g9,g10)
    c: Coincident(g10,g11)
    c: Coincident(g11,g8)
    c: Horizontal(g8)
    c: Horizontal(g10)
    c: Vertical(g9)
    c: Vertical(g11)
    c: Coincident(g12,g13)
    c: Coincident(g13,g14)
    c: Coincident(g14,g15)
    c: Coincident(g15,g12)
    c: Horizontal(g12)
    c: Horizontal(g14)
    c: Vertical(g13)
    c: Vertical(g15)
    c: DistanceX(g8,g12) = 40
    c: DistanceY(g8,g12) = 40
    c: DistanceX(g14,g10) = 40
    c: DistanceY(g14,g10) = 40
    c: DistanceX(g4,g8) = 7
    c: DistanceY(g4,g8) = 7
    c: DistanceX(g10,g6) = 7
    c: DistanceY(g10,g6) = 7
FEATURE [Part::FeaturePython] Window072  label="ОК-92/138-001"  # Arch/BIM 170 (typed FeaturePython)
  Area = 1269600
  Base = -> Sketch374
  Frame = 70
  Height = 1380
  HoleDepth = 0
  HoleWire = 0
  HorizontalArea = 0
  IfcData = attributes={"GlobalId": {"name": "GlobalId", "type": "IfcGloballyUniqueId", "is_enum": false, "enum_values": []}, "Description": {"... (+1230 chars omitted),+1 more (map truncated)
  IfcType = 170
  LouvreSpacing = 0
  LouvreWidth = 0
  Material = -> Material011
  MoveBase = false
  MoveWithHost = true
  Normal = (-1,-9e-16,9e-16)
  Opening = 0
  OverallHeight = 1380
  OverallWidth = 920
  PartitioningType = 0
  PerimeterLength = 0
  Placement = pos=(0,0,1190) rot=(0,0,1;0rad)
  PredefinedType = 0
  Preset = 2
  SymbolElevation = false
  SymbolPlan = false
  VerticalArea = 0
  Width = 920
  WindowParts = OuterFrame | Frame | Wire0,Wire1 | 0.0+V | 0.00+V | InnerFrame | Frame | Wire2,Wire3,Edge8,Mode1 | 0.00+V | 0.0+V | InnerGlass | Glass panel | Wire3 | 8.0 | 40.0+V
  expr: OverallHeight = .Height.Value
  expr: OverallWidth = .Width.Value
FEATURE [Sketcher::SketchObject] Sketch375
  FullyConstrained = true
  Placement = pos=(4175,-435,960) rot=(1,0,0;1.5708rad)
  sketch-geometry (16):
    g0: LineSegment StartX=0 StartY=0 StartZ=0 EndX=660 EndY=0 EndZ=0
    g1: LineSegment StartX=660 StartY=0 StartZ=0 EndX=660 EndY=1380 EndZ=0
    g2: LineSegment StartX=660 StartY=1380 StartZ=0 EndX=0 EndY=1380 EndZ=0
    g3: LineSegment StartX=0 StartY=1380 StartZ=0 EndX=0 EndY=0 EndZ=0
    g4: LineSegment StartX=70 StartY=70 StartZ=0 EndX=590 EndY=70 EndZ=0
    g5: LineSegment StartX=590 StartY=70 StartZ=0 EndX=590 EndY=1310 EndZ=0
    g6: LineSegment StartX=590 StartY=1310 StartZ=0 EndX=70 EndY=1310 EndZ=0
    g7: LineSegment StartX=70 StartY=1310 StartZ=0 EndX=70 EndY=70 EndZ=0
    g8: LineSegment StartX=77 StartY=77 StartZ=0 EndX=583 EndY=77 EndZ=0
    g9: LineSegment StartX=583 StartY=77 StartZ=0 EndX=583 EndY=1303 EndZ=0
    g10: LineSegment StartX=583 StartY=1303 StartZ=0 EndX=77 EndY=1303 EndZ=0
    g11: LineSegment StartX=77 StartY=1303 StartZ=0 EndX=77 EndY=77 EndZ=0
    g12: LineSegment StartX=117 StartY=117 StartZ=0 EndX=543 EndY=117 EndZ=0
    g13: LineSegment StartX=543 StartY=117 StartZ=0 EndX=543 EndY=1263 EndZ=0
    g14: LineSegment StartX=543 StartY=1263 StartZ=0 EndX=117 EndY=1263 EndZ=0
    g15: LineSegment StartX=117 StartY=1263 StartZ=0 EndX=117 EndY=117 EndZ=0
  constraints (47):
    c: Coincident(g0,g1)
    c: Coincident(g1,g2)
    c: Coincident(g2,g3)
    c: Coincident(g3,g0)
    c: Horizontal(g0)
    c: Horizontal(g2)
    c: Vertical(g1)
    c: Vertical(g3)
    c: Coincident(g4,g5)
    c: Coincident(g5,g6)
    c: Coincident(g6,g7)
    c: Coincident(g7,g4)
    c: Horizontal(g4)
    c: Horizontal(g6)
    c: Vertical(g5)
    c: Vertical(g7)
    c: DistanceY(g1) = 1380  'Height'
    c: DistanceX(g0) = 660  'Width'
    c: DistanceY(g6,g2) = 70  'Frame1'
    c: DistanceX(g2,g6) = 70  'Frame2'
    c: DistanceX(g4,g0) = 70  'Frame3'
    c: DistanceY(g0,g4) = 70  'Frame4'
    c: Coincident(g0,g-1)
    c: Coincident(g8,g9)
    c: Coincident(g9,g10)
    c: Coincident(g10,g11)
    c: Coincident(g11,g8)
    c: Horizontal(g8)
    c: Horizontal(g10)
    c: Vertical(g9)
    c: Vertical(g11)
    c: Coincident(g12,g13)
    c: Coincident(g13,g14)
    c: Coincident(g14,g15)
    c: Coincident(g15,g12)
    c: Horizontal(g12)
    c: Horizontal(g14)
    c: Vertical(g13)
    c: Vertical(g15)
    c: DistanceX(g8,g12) = 40
    c: DistanceY(g8,g12) = 40
    c: DistanceX(g14,g10) = 40
    c: DistanceY(g14,g10) = 40
    c: DistanceX(g4,g8) = 7
    c: DistanceY(g4,g8) = 7
    c: DistanceX(g10,g6) = 7
    c: DistanceY(g10,g6) = 7
FEATURE [Part::FeaturePython] Window073  label="ОК-66/138-001"  # Arch/BIM 170 (typed FeaturePython)
  Area = 910800
  Base = -> Sketch375
  Frame = 70
  Height = 1380
  HoleDepth = 0
  HoleWire = 0
  HorizontalArea = 0
  IfcData = attributes={"GlobalId": {"name": "GlobalId", "type": "IfcGloballyUniqueId", "is_enum": false, "enum_values": []}, "Description": {"... (+1230 chars omitted),+1 more (map truncated)
  IfcType = 170
  LouvreSpacing = 0
  LouvreWidth = 0
  Material = -> Material011
  MoveBase = false
  MoveWithHost = true
  Normal = (0,1,-2e-16)
  Opening = 0
  OverallHeight = 1380
  OverallWidth = 660
  PartitioningType = 0
  PerimeterLength = 0
  PredefinedType = 0
  Preset = 2
  SymbolElevation = false
  SymbolPlan = false
  VerticalArea = 0
  Width = 660
  WindowParts = OuterFrame | Frame | Wire0,Wire1 | 0.0+V | 0.00+V | InnerFrame | Frame | Wire2,Wire3,Edge8,Mode1 | 0.00+V | 0.0+V | InnerGlass | Glass panel | Wire3 | 8.0 | 40.0+V
  expr: OverallHeight = .Height.Value
  expr: OverallWidth = .Width.Value
FEATURE [Sketcher::SketchObject] Sketch376
  FullyConstrained = true
  Placement = pos=(7555,-435,960) rot=(1,0,0;1.5708rad)
  sketch-geometry (16):
    g0: LineSegment StartX=0 StartY=0 StartZ=0 EndX=660 EndY=0 EndZ=0
    g1: LineSegment StartX=660 StartY=0 StartZ=0 EndX=660 EndY=1380 EndZ=0
    g2: LineSegment StartX=660 StartY=1380 StartZ=0 EndX=0 EndY=1380 EndZ=0
    g3: LineSegment StartX=0 StartY=1380 StartZ=0 EndX=0 EndY=0 EndZ=0
    g4: LineSegment StartX=70 StartY=70 StartZ=0 EndX=590 EndY=70 EndZ=0
    g5: LineSegment StartX=590 StartY=70 StartZ=0 EndX=590 EndY=1310 EndZ=0
    g6: LineSegment StartX=590 StartY=1310 StartZ=0 EndX=70 EndY=1310 EndZ=0
    g7: LineSegment StartX=70 StartY=1310 StartZ=0 EndX=70 EndY=70 EndZ=0
    g8: LineSegment StartX=77 StartY=77 StartZ=0 EndX=583 EndY=77 EndZ=0
    g9: LineSegment StartX=583 StartY=77 StartZ=0 EndX=583 EndY=1303 EndZ=0
    g10: LineSegment StartX=583 StartY=1303 StartZ=0 EndX=77 EndY=1303 EndZ=0
    g11: LineSegment StartX=77 StartY=1303 StartZ=0 EndX=77 EndY=77 EndZ=0
    g12: LineSegment StartX=117 StartY=117 StartZ=0 EndX=543 EndY=117 EndZ=0
    g13: LineSegment StartX=543 StartY=117 StartZ=0 EndX=543 EndY=1263 EndZ=0
    g14: LineSegment StartX=543 StartY=1263 StartZ=0 EndX=117 EndY=1263 EndZ=0
    g15: LineSegment StartX=117 StartY=1263 StartZ=0 EndX=117 EndY=117 EndZ=0
  constraints (47):
    c: Coincident(g0,g1)
    c: Coincident(g1,g2)
    c: Coincident(g2,g3)
    c: Coincident(g3,g0)
    c: Horizontal(g0)
    c: Horizontal(g2)
    c: Vertical(g1)
    c: Vertical(g3)
    c: Coincident(g4,g5)
    c: Coincident(g5,g6)
    c: Coincident(g6,g7)
    c: Coincident(g7,g4)
    c: Horizontal(g4)
    c: Horizontal(g6)
    c: Vertical(g5)
    c: Vertical(g7)
    c: DistanceY(g1) = 1380  'Height'
    c: DistanceX(g0) = 660  'Width'
    c: DistanceY(g6,g2) = 70  'Frame1'
    c: DistanceX(g2,g6) = 70  'Frame2'
    c: DistanceX(g4,g0) = 70  'Frame3'
    c: DistanceY(g0,g4) = 70  'Frame4'
    c: Coincident(g0,g-1)
    c: Coincident(g8,g9)
    c: Coincident(g9,g10)
    c: Coincident(g10,g11)
    c: Coincident(g11,g8)
    c: Horizontal(g8)
    c: Horizontal(g10)
    c: Vertical(g9)
    c: Vertical(g11)
    c: Coincident(g12,g13)
    c: Coincident(g13,g14)
    c: Coincident(g14,g15)
    c: Coincident(g15,g12)
    c: Horizontal(g12)
    c: Horizontal(g14)
    c: Vertical(g13)
    c: Vertical(g15)
    c: DistanceX(g8,g12) = 40
    c: DistanceY(g8,g12) = 40
    c: DistanceX(g14,g10) = 40
    c: DistanceY(g14,g10) = 40
    c: DistanceX(g4,g8) = 7
    c: DistanceY(g4,g8) = 7
    c: DistanceX(g10,g6) = 7
    c: DistanceY(g10,g6) = 7
FEATURE [Part::FeaturePython] Window074  label="ОК-66/138-002"  # Arch/BIM 170 (typed FeaturePython)
  Area = 910800
  Base = -> Sketch376
  Frame = 70
  Height = 1380
  HoleDepth = 0
  HoleWire = 0
  HorizontalArea = 0
  IfcData = attributes={"GlobalId": {"name": "GlobalId", "type": "IfcGloballyUniqueId", "is_enum": false, "enum_values": []}, "Description": {"... (+1230 chars omitted),+1 more (map truncated)
  IfcType = 170
  LouvreSpacing = 0
  LouvreWidth = 0
  Material = -> Material011
  MoveBase = false
  MoveWithHost = true
  Normal = (0,1,-2e-16)
  Opening = 0
  OverallHeight = 1380
  OverallWidth = 660
  PartitioningType = 0
  PerimeterLength = 0
  PredefinedType = 0
  Preset = 2
  SymbolElevation = false
  SymbolPlan = false
  VerticalArea = 0
  Width = 660
  WindowParts = OuterFrame | Frame | Wire0,Wire1 | 0.0+V | 0.00+V | InnerFrame | Frame | Wire2,Wire3,Edge8,Mode1 | 0.00+V | 0.0+V | InnerGlass | Glass panel | Wire3 | 8.0 | 40.0+V
  expr: OverallHeight = .Height.Value
  expr: OverallWidth = .Width.Value
FEATURE [Sketcher::SketchObject] Sketch379
  FullyConstrained = true
  Placement = pos=(10555,7895,-70) rot=(0,0.707107,0.707107;3.14159rad)
  sketch-geometry (24):
    g0: LineSegment StartX=0 StartY=0 StartZ=0 EndX=1960 EndY=0 EndZ=0
    g1: LineSegment StartX=1960 StartY=0 StartZ=0 EndX=1960 EndY=2630 EndZ=0
    g2: LineSegment StartX=1960 StartY=2630 StartZ=0 EndX=0 EndY=2630 EndZ=0
    g3: LineSegment StartX=0 StartY=2630 StartZ=0 EndX=0 EndY=0 EndZ=0
    g4: LineSegment StartX=70 StartY=70 StartZ=0 EndX=1890 EndY=70 EndZ=0
    g5: LineSegment StartX=1890 StartY=70 StartZ=0 EndX=1890 EndY=2560 EndZ=0
    g6: LineSegment StartX=1890 StartY=2560 StartZ=0 EndX=70 EndY=2560 EndZ=0
    g7: LineSegment StartX=70 StartY=2560 StartZ=0 EndX=70 EndY=70 EndZ=0
    g8: LineSegment StartX=77 StartY=77 StartZ=0 EndX=976.5 EndY=77 EndZ=0
    g9: LineSegment StartX=976.5 StartY=77 StartZ=0 EndX=976.5 EndY=2553 EndZ=0
    g10: LineSegment StartX=976.5 StartY=2553 StartZ=0 EndX=77 EndY=2553 EndZ=0
    g11: LineSegment StartX=77 StartY=2553 StartZ=0 EndX=77 EndY=77 EndZ=0
    g12: LineSegment StartX=117 StartY=117 StartZ=0 EndX=936.5 EndY=117 EndZ=0
    g13: LineSegment StartX=936.5 StartY=117 StartZ=0 EndX=936.5 EndY=2513 EndZ=0
    g14: LineSegment StartX=936.5 StartY=2513 StartZ=0 EndX=117 EndY=2513 EndZ=0
    g15: LineSegment StartX=117 StartY=2513 StartZ=0 EndX=117 EndY=117 EndZ=0
    g16: LineSegment StartX=983.5 StartY=77 StartZ=0 EndX=1883 EndY=77 EndZ=0
    g17: LineSegment StartX=1883 StartY=77 StartZ=0 EndX=1883 EndY=2553 EndZ=0
    g18: LineSegment StartX=1883 StartY=2553 StartZ=0 EndX=983.5 EndY=2553 EndZ=0
    g19: LineSegment StartX=983.5 StartY=2553 StartZ=0 EndX=983.5 EndY=77 EndZ=0
    g20: LineSegment StartX=1023.5 StartY=117 StartZ=0 EndX=1843 EndY=117 EndZ=0
    g21: LineSegment StartX=1843 StartY=117 StartZ=0 EndX=1843 EndY=2513 EndZ=0
    g22: LineSegment StartX=1843 StartY=2513 StartZ=0 EndX=1023.5 EndY=2513 EndZ=0
    g23: LineSegment StartX=1023.5 StartY=2513 StartZ=0 EndX=1023.5 EndY=117 EndZ=0
  constraints (71):
    c: Coincident(g0,g1)
    c: Coincident(g1,g2)
    c: Coincident(g2,g3)
    c: Coincident(g3,g0)
    c: Horizontal(g0)
    c: Horizontal(g2)
    c: Vertical(g1)
    c: Vertical(g3)
    c: Coincident(g4,g5)
    c: Coincident(g5,g6)
    c: Coincident(g6,g7)
    c: Coincident(g7,g4)
    c: Horizontal(g4)
    c: Horizontal(g6)
    c: Vertical(g5)
    c: Vertical(g7)
    c: DistanceY(g1) = 2630  'Height'
    c: DistanceX(g0) = 1960  'Width'
    c: DistanceY(g6,g2) = 70  'Frame1'
    c: DistanceX(g2,g6) = 70  'Frame2'
    c: DistanceX(g4,g0) = 70  'Frame3'
    c: DistanceY(g0,g4) = 70  'Frame4'
    c: Coincident(g0,g-1)
    c: Coincident(g8,g9)
    c: Coincident(g9,g10)
    c: Coincident(g10,g11)
    c: Coincident(g11,g8)
    c: Horizontal(g8)
    c: Horizontal(g10)
    c: Vertical(g9)
    c: Vertical(g11)
    c: Coincident(g12,g13)
    c: Coincident(g13,g14)
    c: Coincident(g14,g15)
    c: Coincident(g15,g12)
    c: Horizontal(g12)
    c: Horizontal(g14)
    c: Vertical(g13)
    c: Vertical(g15)
    c: Coincident(g16,g17)
    c: Coincident(g17,g18)
    c: Coincident(g18,g19)
    c: Coincident(g19,g16)
    c: Horizontal(g16)
    c: Horizontal(g18)
    c: Vertical(g17)
    c: Vertical(g19)
    c: Coincident(g20,g21)
    c: Coincident(g21,g22)
    c: Coincident(g22,g23)
    c: Coincident(g23,g20)
    c: Horizontal(g20)
    c: Horizontal(g22)
    c: Vertical(g21)
    c: Vertical(g23)
    c: DistanceY(g8,g12) = 40
    c: DistanceX(g8,g12) = 40
    c: DistanceX(g21,g17) = 40
    c: DistanceY(g21,g17) = 40
    c: DistanceX(g16,g20) = 40
    c: DistanceX(g14,g10) = 40
    c: Equal(g22,g14)
    c: DistanceY(g8,g16) = 0
    c: DistanceY(g10,g18) = 0
    c: DistanceX(g4,g8) = 7
    c: DistanceY(g4,g8) = 7
    c: DistanceX(g6,g18) = -7
    c: DistanceY(g6,g18) = -7
    c: DistanceX(g9,g19) = 7
    c: PointOnObject(g13,g22)
    c: PointOnObject(g12,g20)
FEATURE [Part::FeaturePython] Window077  label="ОК-196/263-001"  # Arch/BIM 170 (typed FeaturePython)
  Area = 5154800
  Base = -> Sketch379
  Frame = 70
  Height = 2630
  HoleDepth = 0
  HoleWire = 0
  HorizontalArea = 0
  IfcData = attributes={"GlobalId": {"name": "GlobalId", "type": "IfcGloballyUniqueId", "is_enum": false, "enum_values": []}, "Description": {"... (+1231 chars omitted),+1 more (map truncated)
  IfcType = 170
  LouvreSpacing = 0
  LouvreWidth = 0
  Material = -> Material011
  MoveBase = false
  MoveWithHost = true
  Normal = (0,-1,2e-16)
  Opening = 0
  OverallHeight = 2630
  OverallWidth = 1960
  PartitioningType = 0
  PerimeterLength = 0
  PredefinedType = 0
  Preset = 5
  SymbolElevation = false
  SymbolPlan = false
  VerticalArea = 0
  Width = 1960
  WindowParts = OuterFrame | Frame | Wire0,Wire1 | 50.0+V | 0.00+V | LeftFrame | Frame | Wire2,Wire3 | 50.0 | 0.0+V | LeftGlass | Glass panel | Wire3 | 5.0 | 25.0+V | RightFrame | Frame | Wire4,Wire5 | 50.0 | 50.0+V | RightGlass | Glass panel | Wire5 | 5.0 | 75.0+V
  expr: OverallHeight = .Height.Value
  expr: OverallWidth = .Width.Value
FEATURE [Sketcher::SketchObject] Sketch381
  FullyConstrained = true
  Placement = pos=(6720,-435,-40) rot=(0,0.707107,0.707107;3.14159rad)
  sketch-geometry (16):
    g0: LineSegment StartX=0 StartY=0 StartZ=0 EndX=1050 EndY=0 EndZ=0
    g1: LineSegment StartX=1050 StartY=0 StartZ=0 EndX=1050 EndY=2320 EndZ=0
    g2: LineSegment StartX=1050 StartY=2320 StartZ=0 EndX=0 EndY=2320 EndZ=0
    g3: LineSegment StartX=0 StartY=2320 StartZ=0 EndX=0 EndY=0 EndZ=0
    g4: LineSegment StartX=40 StartY=0 StartZ=0 EndX=1010 EndY=0 EndZ=0
    g5: LineSegment StartX=1010 StartY=0 StartZ=0 EndX=1010 EndY=2280 EndZ=0
    g6: LineSegment StartX=1010 StartY=2280 StartZ=0 EndX=40 EndY=2280 EndZ=0
    g7: LineSegment StartX=40 StartY=2280 StartZ=0 EndX=40 EndY=0 EndZ=0
    g8: LineSegment StartX=44 StartY=4 StartZ=0 EndX=1006 EndY=4 EndZ=0
    g9: LineSegment StartX=1006 StartY=4 StartZ=0 EndX=1006 EndY=2276 EndZ=0
    g10: LineSegment StartX=1006 StartY=2276 StartZ=0 EndX=44 EndY=2276 EndZ=0
    g11: LineSegment StartX=44 StartY=2276 StartZ=0 EndX=44 EndY=4 EndZ=0
    g12: LineSegment StartX=444 StartY=1204 StartZ=0 EndX=606 EndY=1204 EndZ=0
    g13: LineSegment StartX=606 StartY=1204 StartZ=0 EndX=606 EndY=1876 EndZ=0
    g14: LineSegment StartX=606 StartY=1876 StartZ=0 EndX=444 EndY=1876 EndZ=0
    g15: LineSegment StartX=444 StartY=1876 StartZ=0 EndX=444 EndY=1204 EndZ=0
  constraints (47):
    c: Coincident(g0,g1)
    c: Coincident(g1,g2)
    c: Coincident(g2,g3)
    c: Coincident(g3,g0)
    c: Horizontal(g0)
    c: Horizontal(g2)
    c: Vertical(g1)
    c: Vertical(g3)
    c: Coincident(g4,g5)
    c: Coincident(g5,g6)
    c: Coincident(g6,g7)
    c: Coincident(g7,g4)
    c: Horizontal(g4)
    c: Horizontal(g6)
    c: Vertical(g5)
    c: Vertical(g7)
    c: DistanceY(g1) = 2320  'Height'
    c: DistanceX(g0) = 1050  'Width'
    c: DistanceY(g6,g2) = 40  'Frame1'
    c: DistanceX(g2,g6) = 40  'Frame2'
    c: DistanceX(g4,g0) = 40  'Frame3'
    c: DistanceY(g0,g4) = 0
    c: Coincident(g0,g-1)
    c: Coincident(g8,g9)
    c: Coincident(g9,g10)
    c: Coincident(g10,g11)
    c: Coincident(g11,g8)
    c: Horizontal(g8)
    c: Horizontal(g10)
    c: Vertical(g9)
    c: Vertical(g11)
    c: Coincident(g12,g13)
    c: Coincident(g13,g14)
    c: Coincident(g14,g15)
    c: Coincident(g15,g12)
    c: Horizontal(g12)
    c: Horizontal(g14)
    c: Vertical(g13)
    c: Vertical(g15)
    c: DistanceX(g8,g12) = 400
    c: DistanceY(g8,g12) = 1200
    c: DistanceX(g14,g10) = 400
    c: DistanceY(g14,g10) = 400
    c: DistanceX(g4,g8) = 4
    c: DistanceY(g4,g8) = 4
    c: DistanceX(g10,g6) = 4
    c: DistanceY(g10,g6) = 4
FEATURE [Part::FeaturePython] Window078  label="Д-105/232-001"  # Arch/BIM 41 (typed FeaturePython)
  Area = 2436000
  Base = -> Sketch381
  Frame = 40
  Height = 2320
  HoleDepth = 0
  HoleWire = 0
  HorizontalArea = 0
  IfcData = attributes={"GlobalId": {"name": "GlobalId", "type": "IfcGloballyUniqueId", "is_enum": false, "enum_values": []}, "Description": {"... (+1934 chars omitted),+1 more (map truncated)
  IfcType = 41
  LouvreSpacing = 0
  LouvreWidth = 0
  Material = -> Material011
  MoveBase = false
  MoveWithHost = true
  Normal = (0,-1,2e-16)
  Offset = 20
  Opening = 0
  OperationType = 0
  OverallHeight = 2320
  OverallWidth = 1050
  PerimeterLength = 0
  PredefinedType = 0
  Preset = 7
  SymbolElevation = false
  SymbolPlan = false
  VerticalArea = 0
  Width = 1050
  WindowParts = OuterFrame | Frame | Wire0,Wire1 | 40.0+V | 0.00+V | InnerFrame | Frame | Wire2,Wire3,Edge8,Mode1 | 80.0 | 0.0+V | InnerGlass | Glass panel | Wire3 | 8.0 | 40.0+V
  expr: OverallWidth = .Width.Value
  expr: OverallHeight = .Height.Value
FEATURE [App::GeometryPython] BuildingPart011  label="Окна и двери 1этаж"  # Arch/BIM 52 (typed FeaturePython)
  Area = 31952000
  GlobalId = 2lTKOyIXPBJh5VnrrZDJsa
  Group = -> [Window020,Window021,Window026,Window048,Window052,Window068,Window069,Window,Window070,Window071,Window072,Window073,Window074,Window077,Window078]
  Height = 0
  HeightPropagate = true
  IfcData = IfcUID=2lTKOyIXPBJh5VnrrZDJsa,attributes={"GlobalId": {"value": "2lTKOyIXPBJh5VnrrZDJsa"}},+1 more (map truncated)
  IfcType = 52
  LevelOffset = 0
FEATURE [Part::Part2DObjectPython] Line1395  # Draft 2D object (typed FeaturePython)
  Area = 0
  ChamferSize = 0
  Closed = false
  End = (3400,3385,0)
  FilletRadius = 0
  Length = 800
  MakeFace = true
  Placement = pos=(2600,3385,0) rot=(0,0,1;0rad)
  Points = (2) [(0,0,0),(800,0,0)]
  Start = (2600,3385,0)
  Subdivisions = 0
FEATURE [App::DocumentObjectGroup] Group125  label="План 1 этаж 94.1 м2"
  Group = -> [Rectangle008,Rectangle2795,Rectangle2807,Rectangle3095,Rectangle2972,Rectangle2798,Rectangle2717,Rectangle2230,Rectangle2169,Rectangle2231,Rectangle005,Wire760,Rectangle011,Rectangle2695,Rectangle009,Rectangle003,Rectangle006,Rectangle2730,Rectangle016,Rectangle3074,Rectangle3086,Rectangle3084,Rectangle3079,Rectangle2857,Rectangle3166,Rectangle3168,Rectangle544,Rectangle547,Rectangle545,+139 more]
FEATURE [App::DocumentObjectGroup] Group131  label="Draft"
  Group = -> [Group125,Group118,Group126,ImagePlane001]
FEATURE [Part::FeaturePython] Component131  label="Компонент"  # Arch/BIM 0 (typed FeaturePython)
  Base = -> Arc114
  HorizontalArea = 0
  IfcData = attributes={"GlobalId": {"name": "GlobalId", "type": "IfcGloballyUniqueId", "is_enum": false, "enum_values": []}, "Description": {"... (+538 chars omitted),+1 more (map truncated)
  IfcType = 0
  MoveBase = false
  MoveWithHost = false
  PerimeterLength = 0
  Placement = pos=(4710,3635,0) rot=(0,0,1;0rad)
  PredefinedType = 0
  VerticalArea = 0
FEATURE [Part::FeaturePython] Component132  label="Компонент001"  # Arch/BIM 0 (typed FeaturePython)
  Base = -> Line1394
  HorizontalArea = 0
  IfcData = attributes={"GlobalId": {"name": "GlobalId", "type": "IfcGloballyUniqueId", "is_enum": false, "enum_values": []}, "Description": {"... (+538 chars omitted),+1 more (map truncated)
  IfcType = 0
  MoveBase = false
  MoveWithHost = false
  PerimeterLength = 0
  Placement = pos=(4710,4435,0) rot=(0,0,1;0rad)
  PredefinedType = 0
  VerticalArea = 0
FEATURE [Part::FeaturePython] Component133  label="Компонент002"  # Arch/BIM 0 (typed FeaturePython)
  Base = -> Line1395
  HorizontalArea = 0
  IfcData = attributes={"GlobalId": {"name": "GlobalId", "type": "IfcGloballyUniqueId", "is_enum": false, "enum_values": []}, "Description": {"... (+538 chars omitted),+1 more (map truncated)
  IfcType = 0
  MoveBase = false
  MoveWithHost = false
  PerimeterLength = 0
  Placement = pos=(2600,3385,0) rot=(0,0,1;0rad)
  PredefinedType = 0
  VerticalArea = 0
FEATURE [Part::FeaturePython] Component134  label="Компонент003"  # Arch/BIM 0 (typed FeaturePython)
  Base = -> Arc115
  HorizontalArea = 0
  IfcData = attributes={"GlobalId": {"name": "GlobalId", "type": "IfcGloballyUniqueId", "is_enum": false, "enum_values": []}, "Description": {"... (+538 chars omitted),+1 more (map truncated)
  IfcType = 0
  MoveBase = false
  MoveWithHost = false
  PerimeterLength = 0
  Placement = pos=(3400,3385,0) rot=(0,0,1;0rad)
  PredefinedType = 0
  VerticalArea = 0
FEATURE [Part::FeaturePython] Component135  label="Компонент004"  # Arch/BIM 0 (typed FeaturePython)
  Base = -> Arc116
  HorizontalArea = 0
  IfcData = attributes={"GlobalId": {"name": "GlobalId", "type": "IfcGloballyUniqueId", "is_enum": false, "enum_values": []}, "Description": {"... (+538 chars omitted),+1 more (map truncated)
  IfcType = 0
  MoveBase = false
  MoveWithHost = false
  PerimeterLength = 0
  Placement = pos=(6660,2285,0) rot=(0,0,1;0rad)
  PredefinedType = 0
  VerticalArea = 0
FEATURE [Part::FeaturePython] Component136  label="Компонент005"  # Arch/BIM 0 (typed FeaturePython)
  Base = -> Line1396
  HorizontalArea = 0
  IfcData = attributes={"GlobalId": {"name": "GlobalId", "type": "IfcGloballyUniqueId", "is_enum": false, "enum_values": []}, "Description": {"... (+538 chars omitted),+1 more (map truncated)
  IfcType = 0
  MoveBase = false
  MoveWithHost = false
  PerimeterLength = 0
  Placement = pos=(6660,1485,0) rot=(0,0,1;0rad)
  PredefinedType = 0
  VerticalArea = 0
FEATURE [Part::FeaturePython] Component137  label="Компонент006"  # Arch/BIM 0 (typed FeaturePython)
  Base = -> Arc113
  HorizontalArea = 0
  IfcData = attributes={"GlobalId": {"name": "GlobalId", "type": "IfcGloballyUniqueId", "is_enum": false, "enum_values": []}, "Description": {"... (+538 chars omitted),+1 more (map truncated)
  IfcType = 0
  MoveBase = false
  MoveWithHost = false
  PerimeterLength = 0
  Placement = pos=(6660,3635,0) rot=(0,0,1;0rad)
  PredefinedType = 0
  VerticalArea = 0
FEATURE [Part::FeaturePython] Component138  label="Компонент007"  # Arch/BIM 0 (typed FeaturePython)
  Base = -> Line1400
  HorizontalArea = 0
  IfcData = attributes={"GlobalId": {"name": "GlobalId", "type": "IfcGloballyUniqueId", "is_enum": false, "enum_values": []}, "Description": {"... (+538 chars omitted),+1 more (map truncated)
  IfcType = 0
  MoveBase = false
  MoveWithHost = false
  PerimeterLength = 0
  Placement = pos=(6660,4580,0) rot=(0,0,1;0rad)
  PredefinedType = 0
  VerticalArea = 0
FEATURE [Part::FeaturePython] Component139  label="Компонент008"  # Arch/BIM 0 (typed FeaturePython)
  Base = -> Arc118
  HorizontalArea = 0
  IfcData = attributes={"GlobalId": {"name": "GlobalId", "type": "IfcGloballyUniqueId", "is_enum": false, "enum_values": []}, "Description": {"... (+538 chars omitted),+1 more (map truncated)
  IfcType = 0
  MoveBase = false
  MoveWithHost = false
  PerimeterLength = 0
  Placement = pos=(9550,820,0) rot=(0,0,1;0rad)
  PredefinedType = 0
  VerticalArea = 0
FEATURE [Part::FeaturePython] Component140  label="Компонент009"  # Arch/BIM 0 (typed FeaturePython)
  Base = -> Line1398
  HorizontalArea = 0
  IfcData = attributes={"GlobalId": {"name": "GlobalId", "type": "IfcGloballyUniqueId", "is_enum": false, "enum_values": []}, "Description": {"... (+538 chars omitted),+1 more (map truncated)
  IfcType = 0
  MoveBase = false
  MoveWithHost = false
  PerimeterLength = 0
  Placement = pos=(10350,820,0) rot=(0,0,1;0rad)
  PredefinedType = 0
  VerticalArea = 0
FEATURE [App::FeaturePython] Dimension079  # Draft dimension (typed FeaturePython)
  Diameter = false
  Dimline = (4500,1400,0)
  Direction = (0,0,0)
  Distance = 100
  End = (4100,2285,0)
  Normal = (0,0,1)
  Start = (4000,2285,0)
FEATURE [Part::FeaturePython] Component141  label="Компонент010"  # Arch/BIM 0 (typed FeaturePython)
  Base = -> Circle109
  HorizontalArea = 0
  IfcData = attributes={"GlobalId": {"name": "GlobalId", "type": "IfcGloballyUniqueId", "is_enum": false, "enum_values": []}, "Description": {"... (+538 chars omitted),+1 more (map truncated)
  IfcType = 0
  MoveBase = false
  MoveWithHost = false
  PerimeterLength = 0
  Placement = pos=(7390,4155,0) rot=(0,0,-1;1.5708rad)
  PredefinedType = 0
  VerticalArea = 0
FEATURE [Part::FeaturePython] Component142  label="Компонент011"  # Arch/BIM 0 (typed FeaturePython)
  Base = -> Line1409
  HorizontalArea = 0
  IfcData = attributes={"GlobalId": {"name": "GlobalId", "type": "IfcGloballyUniqueId", "is_enum": false, "enum_values": []}, "Description": {"... (+538 chars omitted),+1 more (map truncated)
  IfcType = 0
  MoveBase = false
  MoveWithHost = false
  PerimeterLength = 0
  Placement = pos=(7420,4155,0) rot=(0,0,-1;1.5708rad)
  PredefinedType = 0
  VerticalArea = 0
FEATURE [App::FeaturePython] Dimension080  # Draft dimension (typed FeaturePython)
  Diameter = false
  Dimline = (2030,8200,0)
  Direction = (0,0,0)
  Distance = 2590
  End = (2030,8015,0)
  Normal = (0,0,1)
  Start = (-560,8015,0)
FEATURE [App::FeaturePython] Dimension081  # Draft dimension (typed FeaturePython)
  Diameter = false
  Dimline = (3860,8200,0)
  Direction = (0,0,0)
  Distance = 1290
  End = (5150,8015,0)
  Normal = (0,0,1)
  Start = (3860,8015,0)
FEATURE [App::FeaturePython] Dimension082  # Draft dimension (typed FeaturePython)
  Diameter = false
  Dimline = (5150,8200,0)
  Direction = (0,0,0)
  Distance = 790
  End = (5940,8015,0)
  Normal = (0,0,1)
  Start = (5150,8015,0)
FEATURE [App::FeaturePython] Dimension083  # Draft dimension (typed FeaturePython)
  Diameter = false
  Dimline = (5940,8200,0)
  Direction = (0,0,0)
  Distance = 2720
  End = (8660,8015,0)
  Normal = (0,0,1)
  Start = (5940,8015,0)
FEATURE [App::FeaturePython] Dimension084  # Draft dimension (typed FeaturePython)
  Diameter = false
  Dimline = (8660,8200,0)
  Direction = (0,0,0)
  Distance = 1830
  End = (10490,8015,0)
  Normal = (0,0,1)
  Start = (8660,8015,0)
FEATURE [App::FeaturePython] Dimension085  # Draft dimension (typed FeaturePython)
  Diameter = false
  Dimline = (10490,8200,0)
  Direction = (0,0,0)
  Distance = 2590
  End = (13080,8015,0)
  Normal = (0,0,1)
  Start = (10490,8015,0)
FEATURE [App::FeaturePython] Dimension086  # Draft dimension (typed FeaturePython)
  Diameter = false
  Dimline = (5000,7200,0)
  Direction = (0,0,0)
  Distance = 1900
  End = (6830,7485,0)
  Normal = (0,0,1)
  Start = (4930,7485,0)
FEATURE [App::FeaturePython] Dimension087  # Draft dimension (typed FeaturePython)
  Diameter = false
  Dimline = (-800,3215,0)
  Direction = (0,0,0)
  Distance = 1310
  End = (-560,3215,0)
  Normal = (0,0,1)
  Start = (-560,1905,0)
FEATURE [App::FeaturePython] Dimension088  # Draft dimension (typed FeaturePython)
  Diameter = false
  Dimline = (-800,1905,0)
  Direction = (0,0,0)
  Distance = 2460
  End = (-560,1905,0)
  Normal = (0,0,1)
  Start = (-560,-555,0)
FEATURE [App::FeaturePython] Dimension089  # Draft dimension (typed FeaturePython)
  Diameter = false
  Dimline = (1700,-800,0)
  Direction = (0,0,0)
  Distance = 4800
  End = (4240,-555,0)
  Normal = (0,0,1)
  Start = (-560,-555,0)
FEATURE [App::FeaturePython] Dimension090  # Draft dimension (typed FeaturePython)
  Diameter = false
  Dimline = (4240,-800,0)
  Direction = (0,0,0)
  Distance = 530
  End = (4770,-555,0)
  Normal = (0,0,1)
  Start = (4240,-555,0)
FEATURE [App::FeaturePython] Dimension091  # Draft dimension (typed FeaturePython)
  Diameter = false
  Dimline = (4770,-800,0)
  Direction = (0,0,0)
  Distance = 900
  End = (5670,-555,0)
  Normal = (0,0,1)
  Start = (4770,-555,0)
FEATURE [App::FeaturePython] Dimension092  # Draft dimension (typed FeaturePython)
  Diameter = false
  Dimline = (7620,-800,0)
  Direction = (0,0,0)
  Distance = 530
  End = (8150,-555,0)
  Normal = (0,0,1)
  Start = (7620,-555,0)
FEATURE [App::FeaturePython] Dimension093  # Draft dimension (typed FeaturePython)
  Diameter = false
  Dimline = (6720,-800,0)
  Direction = (0,0,0)
  Distance = 900
  End = (7620,-555,0)
  Normal = (0,0,1)
  Start = (6720,-555,0)
FEATURE [App::FeaturePython] Dimension094  # Draft dimension (typed FeaturePython)
  Diameter = false
  Dimline = (8150,-800,0)
  Direction = (0,0,0)
  Distance = 4930
  End = (13080,-555,0)
  Normal = (0,0,1)
  Start = (8150,-555,0)
FEATURE [App::FeaturePython] Dimension095  # Draft dimension (typed FeaturePython)
  Diameter = false
  Dimline = (13600,1200,0)
  Direction = (0,0,0)
  Distance = 1940
  End = (13080,1385,0)
  Normal = (0,0,1)
  Start = (13080,-555,0)
FEATURE [App::FeaturePython] Dimension096  # Draft dimension (typed FeaturePython)
  Diameter = false
  Dimline = (13600,1385,0)
  Direction = (0,0,0)
  Distance = 1830
  End = (13080,3215,0)
  Normal = (0,0,1)
  Start = (13080,1385,0)
FEATURE [App::FeaturePython] Dimension097  # Draft dimension (typed FeaturePython)
  Diameter = false
  Dimline = (13600,3215,0)
  Direction = (0,0,0)
  Distance = 900
  End = (13080,4115,0)
  Normal = (0,0,1)
  Start = (13080,3215,0)
FEATURE [App::FeaturePython] Dimension098  # Draft dimension (typed FeaturePython)
  Diameter = false
  Dimline = (13600,4115,0)
  Direction = (0,0,0)
  Distance = 790
  End = (13080,4905,0)
  Normal = (0,0,1)
  Start = (13080,4115,0)
FEATURE [App::FeaturePython] Dimension099  # Draft dimension (typed FeaturePython)
  Diameter = false
  Dimline = (13600,4905,0)
  Direction = (0,0,0)
  Distance = 3110
  End = (13080,8015,0)
  Normal = (0,0,1)
  Start = (13080,4905,0)
FEATURE [App::FeaturePython] Dimension100  # Draft dimension (typed FeaturePython)
  Diameter = false
  Dimline = (-800,3215,0)
  Direction = (0,0,0)
  Distance = 4800
  End = (-560,8015,0)
  Normal = (0,0,1)
  Start = (-560,3215,0)
FEATURE [Part::Part2DObjectPython] Wire916  label="СУ_1"  # Draft 2D object (typed FeaturePython)
  Area = 0
  ChamferSize = 0
  Closed = true
  End = (4930,4072.49,0)
  FilletRadius = 0
  Length = 12775
  MakeFace = false
  Placement = pos=(4930,7485,0) rot=(0,0,1;0rad)
  Points = (9) [(0,0,0),(1900,0,0),(1900,-1800,0),(1000,-1800,0),(1000,-1920,0),(1900,-1920,0),(1900,-3660,0),(247.487,-3660,0),(-9.09495e-13,-3412.51,0)]
  Start = (4930,7485,0)
  Subdivisions = 0
FEATURE [Part::FeaturePython] Wall232  label="Покрытие СУ плиткой 20мм"  # Arch/BIM 166 (typed FeaturePython)
  Align = 1
  Area = 3.57701e+07
  Base = -> Wire916
  BlockHeight = 0
  BlockLength = 0
  CountBroken = 0
  CountEntire = 0
  Face = 0
  GlobalId = 0fSn5rz2v1yx1CM9t4dxRk
  Height = 2800
  HorizontalArea = 0
  IfcData = IfcUID=0fSn5rz2v1yx1CM9t4dxRk,+2 more (map truncated)
  IfcType = 166
  Joint = 0
  Length = 12775
  MakeBlocks = false
  Material = -> Material005
  MoveBase = false
  MoveWithHost = false
  Normal = (0,0,0)
  OffsetFirst = 0
  OffsetSecond = 0
  PerimeterLength = 0
  PredefinedType = 0
  Subtractions = -> [Structure141,Structure313,Structure333,Structure020]
  VerticalArea = 0
  Width = 20
FEATURE [Part::Part2DObjectPython] Wire917  # Draft 2D object (typed FeaturePython)
  Area = 0
  ChamferSize = 0
  Closed = false
  End = (7860,6485,0)
  FilletRadius = 0
  Length = 2780
  MakeFace = false
  Placement = pos=(7960,3805,0) rot=(0,0,1;0rad)
  Points = (3) [(0,0,0),(0,2680,0),(-100,2680,0)]
  Start = (7960,3805,0)
  Subdivisions = 0
FEATURE [Part::Part2DObjectPython] Line1728  # Draft 2D object (typed FeaturePython)
  Area = 0
  ChamferSize = 0
  Closed = false
  End = (6940,3805,0)
  FilletRadius = 0
  Length = 3700
  MakeFace = false
  Placement = pos=(6940,7505,0) rot=(0,0,1;0rad)
  Points = (2) [(0,0,0),(0,-3700,0)]
  Start = (6940,7505,0)
  Subdivisions = 0
FEATURE [Part::FeaturePython] Wall348  label="Стена042"  # Arch/BIM 166 (typed FeaturePython)
  Align = 0
  Area = 1.036e+07
  Base = -> Line1728
  BlockHeight = 0
  BlockLength = 0
  CountBroken = 0
  CountEntire = 0
  Face = 0
  Height = 2800
  HorizontalArea = 37000
  IfcData = attributes={"GlobalId": {"name": "GlobalId", "type": "IfcGloballyUniqueId", "is_enum": false, "enum_values": []}, "Description": {"... (+533 chars omitted),+1 more (map truncated)
  IfcType = 166
  Joint = 0
  Length = 3700
  MakeBlocks = false
  MoveBase = false
  MoveWithHost = false
  Normal = (0,0,0)
  OffsetFirst = 0
  OffsetSecond = 0
  PerimeterLength = 7420
  PredefinedType = 0
  VerticalArea = 2.0776e+07
  Width = 10
FEATURE [Part::Part2DObjectPython] Wire918  # Draft 2D object (typed FeaturePython)
  Area = 0
  ChamferSize = 0
  Closed = true
  End = (7960,7600,48.08)
  FilletRadius = 0
  Length = 13696.2
  MakeFace = false
  Placement = pos=(7960,2995.41,3427.85) rot=(0.57735,0.57735,0.57735;2.0944rad)
  Points = (3) [(0,0,0),(4604.59,0,0),(4604.59,-3379.77,0)]
  Start = (7960,2995.41,3427.85)
  Subdivisions = 0
FEATURE [Part::FeaturePython] Structure337  label="Структура005"  # Arch/BIM 52 (typed FeaturePython)
  Base = -> Wire918
  FaceMaker = 0
  Height = 1030
  HorizontalArea = 4.74273e+06
  IfcData = attributes={"GlobalId": {"name": "GlobalId", "type": "IfcGloballyUniqueId", "is_enum": false, "enum_values": []}, "Description": {"... (+484 chars omitted),+1 more (map truncated)
  IfcType = 52
  Length = 0
  MoveBase = false
  MoveWithHost = false
  Nodes = (2) [(5266.67,6238.33,-4065),(5166.67,6238.33,-4065)]
  NodesOffset = 0
  Normal = (-1,0,0)
  PerimeterLength = 11269.2
  VerticalArea = 1.90436e+07
  Width = 100
FEATURE [Part::FeaturePython] Wall128  label="перегородка (сил.блок 500х250х80) 003"  # Arch/BIM 166 (typed FeaturePython)
  Align = 2
  Area = 7.476e+06
  Base = -> Line1200
  BlockHeight = 250
  BlockLength = 0
  CountBroken = 0
  CountEntire = 0
  Face = 0
  GlobalId = 239nej2f15XxZ4oxwr6VZE
  Height = 2800
  HorizontalArea = 213600
  IfcData = IfcUID=239nej2f15XxZ4oxwr6VZE; attributes={"GlobalId": {"value": "239nej2f15XxZ4oxwr6VZE"}}
  IfcType = 166
  Joint = 0
  Length = 2670
  MakeBlocks = false
  Material = -> Material009
  MoveBase = false
  MoveWithHost = false
  Normal = (0,0,0)
  OffsetFirst = 300
  OffsetSecond = 50
  PerimeterLength = 5720
  PredefinedType = 0
  Subtractions = -> [Structure337]
  VerticalArea = 1.01912e+07
  Width = 80
FEATURE [Part::FeaturePython] Structure460  label="Структура022"  # Arch/BIM 52 (typed FeaturePython)
  Base = -> Wire918
  FaceMaker = 0
  Height = 1030
  HorizontalArea = 4.74273e+06
  IfcData = attributes={"GlobalId": {"name": "GlobalId", "type": "IfcGloballyUniqueId", "is_enum": false, "enum_values": []}, "Description": {"... (+484 chars omitted),+1 more (map truncated)
  IfcType = 52
  Length = 0
  MoveBase = false
  MoveWithHost = false
  Nodes = (2) [(5266.67,6238.33,-4065),(5166.67,6238.33,-4065)]
  NodesOffset = 0
  Normal = (-1,0,0)
  PerimeterLength = 11269.2
  Placement = pos=(0,0,-30) rot=(0,0,1;0rad)
  VerticalArea = 1.90436e+07
  Width = 100
FEATURE [Part::FeaturePython] Wall231  label="перегородка (сил.блок 500х250х80) 005"  # Arch/BIM 166 (typed FeaturePython)
  Align = 2
  Area = 1.5604e+06
  Base = -> Line1391
  BlockHeight = 250
  BlockLength = 0
  CountBroken = 0
  CountEntire = 0
  Face = 0
  GlobalId = 2YMQSCXEvDBOywm4rK59sv
  Height = 1660
  HorizontalArea = 75200
  IfcData = IfcUID=2YMQSCXEvDBOywm4rK59sv; attributes={"GlobalId": {"value": "2YMQSCXEvDBOywm4rK59sv"}}
  IfcType = 166
  Joint = 0
  Length = 940
  MakeBlocks = false
  Material = -> Material009
  MoveBase = false
  MoveWithHost = false
  Normal = (0,0,0)
  OffsetFirst = 300
  OffsetSecond = 50
  PerimeterLength = 2000
  PredefinedType = 0
  Subtractions = -> [Structure460]
  VerticalArea = 3.34084e+06
  Width = 80
FEATURE [App::GeometryPython] BuildingPart005  label="Перегородки"  # Arch/BIM 52 (typed FeaturePython)
  Area = 48992400
  GlobalId = 2hzWGr02f4ewnrclJv7BWz
  Group = -> [Wall015,Wall186,Wall128,Wall223,Wall231,Wall230]
  Height = 0
  HeightPropagate = true
  IfcData = IfcUID=2hzWGr02f4ewnrclJv7BWz,attributes={"GlobalId": {"value": "2hzWGr02f4ewnrclJv7BWz"}},+1 more (map truncated)
  IfcType = 52
  LevelOffset = 0
FEATURE [Part::FeaturePython] Wall346  label="Покрытие Душ плиткой 20мм"  # Arch/BIM 166 (typed FeaturePython)
  Align = 0
  Area = 1.344e+07
  Base = -> Rectangle3000
  BlockHeight = 0
  BlockLength = 0
  CountBroken = 0
  CountEntire = 0
  Face = 0
  Height = 2800
  HorizontalArea = 4623.16
  IfcData = attributes={"GlobalId": {"name": "GlobalId", "type": "IfcGloballyUniqueId", "is_enum": false, "enum_values": []}, "Description": {"... (+533 chars omitted),+1 more (map truncated)
  IfcType = 166
  Joint = 0
  Length = 4800
  MakeBlocks = false
  Material = -> Material005
  MoveBase = false
  MoveWithHost = false
  Normal = (0,0,0)
  OffsetFirst = 0
  OffsetSecond = 0
  PerimeterLength = 1889.84
  PredefinedType = 0
  Subtractions = -> [Structure333,Structure460]
  VerticalArea = 1.83237e+07
  Width = 20
FEATURE [Part::FeaturePython] Wall347  label="Штукатурка 10мм 006"  # Arch/BIM 166 (typed FeaturePython)
  Align = 1
  Area = 7.784e+06
  Base = -> Wire917
  BlockHeight = 0
  BlockLength = 0
  CountBroken = 0
  CountEntire = 0
  Face = 0
  Height = 2800
  HorizontalArea = 27700
  IfcData = attributes={"GlobalId": {"name": "GlobalId", "type": "IfcGloballyUniqueId", "is_enum": false, "enum_values": []}, "Description": {"... (+533 chars omitted),+1 more (map truncated)
  IfcType = 166
  Joint = 0
  Length = 2780
  MakeBlocks = false
  Material = -> Material008
  MoveBase = false
  MoveWithHost = false
  Normal = (0,0,0)
  OffsetFirst = 0
  OffsetSecond = 0
  PerimeterLength = 5560
  PredefinedType = 0
  Subtractions = -> [Structure337]
  VerticalArea = 1.0108e+07
  Width = 10
FEATURE [Part::MultiCommon] Common074  label="Штукатурка 10мм 005"
  Shapes = -> [Wall348,Structure460]
FEATURE [Part::FeaturePython] Component143  label="Компонент012"  # Arch/BIM 0 (typed FeaturePython)
  Base = -> Common074
  HorizontalArea = 0
  IfcData = attributes={"GlobalId": {"name": "GlobalId", "type": "IfcGloballyUniqueId", "is_enum": false, "enum_values": []}, "Description": {"... (+538 chars omitted),+1 more (map truncated)
  IfcType = 0
  Material = -> Material008
  MoveBase = false
  MoveWithHost = false
  PerimeterLength = 0
  PredefinedType = 0
  VerticalArea = 0
FEATURE [Part::Part2DObjectPython] Line1729  # Draft 2D object (typed FeaturePython)
  Area = 0
  ChamferSize = 0
  Closed = false
  End = (4820,3805,0)
  FilletRadius = 0
  Length = 3700
  MakeFace = false
  Placement = pos=(4820,7505,0) rot=(0,0,1;0rad)
  Points = (2) [(0,0,0),(-9.09495e-13,-3700,0)]
  Start = (4820,7505,0)
  Subdivisions = 0
FEATURE [Part::FeaturePython] Wall349  label="Штукатурка 10мм 007"  # Arch/BIM 166 (typed FeaturePython)
  Align = 1
  Area = 1.036e+07
  Base = -> Line1729
  BlockHeight = 0
  BlockLength = 0
  CountBroken = 0
  CountEntire = 0
  Face = 0
  Height = 2800
  HorizontalArea = 37000
  IfcData = attributes={"GlobalId": {"name": "GlobalId", "type": "IfcGloballyUniqueId", "is_enum": false, "enum_values": []}, "Description": {"... (+533 chars omitted),+1 more (map truncated)
  IfcType = 166
  Joint = 0
  Length = 3700
  MakeBlocks = false
  Material = -> Material008
  MoveBase = false
  MoveWithHost = false
  Normal = (0,0,0)
  OffsetFirst = 0
  OffsetSecond = 0
  PerimeterLength = 7420
  PredefinedType = 0
  VerticalArea = 2.0776e+07
  Width = 10
FEATURE [App::GeometryPython] BuildingPart081  label="Отделка"  # Arch/BIM 52 (typed FeaturePython)
  Area = 3.1993e+08
  GlobalId = 3k8znIZGb8Sep8PACCMQ9v
  Group = -> [Wall232,Wall227,Wall229,Wall233,Wall234,Wall235,Wall236,Wall237,Wall238,Wall239,Wall,Wall267,Wall268,Wall269,Wall347,Wall346,Component143,Wall349]
  Height = 0
  HeightPropagate = true
  IfcData = IfcUID=3k8znIZGb8Sep8PACCMQ9v,+2 more (map truncated)
  IfcType = 52
  LevelOffset = 0
FEATURE [App::GeometryPython] BuildingPart103  label="Уровень первого этажа"  # Arch/BIM 14 (typed FeaturePython)
  Area = 7.61169e+08
  CompositionType = 0
  Elevation = 0
  GlobalId = 377tEiMTb6celHDz_UVksa
  Group = -> [BuildingPart101,BuildingPart102,BuildingPart002,BuildingPart005,BuildingPart081,BuildingPart038,BuildingPart014,BuildingPart093,BuildingPart011,BuildingPart087,BuildingPart049]
  Height = 3130
  HeightPropagate = true
  IfcData = IfcUID=377tEiMTb6celHDz_UVksa,+2 more (map truncated)
  IfcType = 14
  LevelOffset = 0
  LongName = Floor
  Placement = pos=(-560,-540,0) rot=(0,0,1;0rad)
  expr: Elevation = .Placement.Base.z
FEATURE [Part::FeaturePython] Component144  label="Компонент013"  # Arch/BIM 0 (typed FeaturePython)
  Base = -> Line1456
  HorizontalArea = 0
  IfcData = attributes={"GlobalId": {"name": "GlobalId", "type": "IfcGloballyUniqueId", "is_enum": false, "enum_values": []}, "Description": {"... (+538 chars omitted),+1 more (map truncated)
  IfcType = 0
  MoveBase = false
  MoveWithHost = false
  PerimeterLength = 0
  Placement = pos=(4020,7335,0) rot=(0,0,1;0rad)
  PredefinedType = 0
  VerticalArea = 0
FEATURE [Part::FeaturePython] Component145  label="Компонент014"  # Arch/BIM 0 (typed FeaturePython)
  Base = -> Arc125
  HorizontalArea = 0
  IfcData = attributes={"GlobalId": {"name": "GlobalId", "type": "IfcGloballyUniqueId", "is_enum": false, "enum_values": []}, "Description": {"... (+538 chars omitted),+1 more (map truncated)
  IfcType = 0
  MoveBase = false
  MoveWithHost = false
  PerimeterLength = 0
  Placement = pos=(4820,7335,0) rot=(0,0,1;0rad)
  PredefinedType = 0
  VerticalArea = 0
FEATURE [App::GeometryPython] BuildingPart107  label="Направление открывания дверей"  # Arch/BIM 172 (typed FeaturePython)
  Area = 0
  Group = -> [Component131,Component132,Component133,Component134,Component135,Component136,Component137,Component138,Component139,Component140,Component144,Component145]
  Height = 0
  HeightPropagate = true
  IfcData = attributes={"GlobalId": {"name": "GlobalId", "type": "IfcGloballyUniqueId", "is_enum": false, "enum_values": []}, "Description": {"... (+484 chars omitted),+1 more (map truncated)
  IfcType = 172
  LevelOffset = 0
  PredefinedType = 0
FEATURE [Part::FeaturePython] Component146  label="Компонент015"  # Arch/BIM 0 (typed FeaturePython)
  Base = -> Wire833
  HorizontalArea = 0
  IfcData = attributes={"GlobalId": {"name": "GlobalId", "type": "IfcGloballyUniqueId", "is_enum": false, "enum_values": []}, "Description": {"... (+538 chars omitted),+1 more (map truncated)
  IfcType = 0
  MoveBase = false
  MoveWithHost = false
  PerimeterLength = 0
  Placement = pos=(8310,7021.58,0) rot=(0,0,1;0rad)
  PredefinedType = 0
  VerticalArea = 0
FEATURE [Part::FeaturePython] Component147  label="Компонент016"  # Arch/BIM 0 (typed FeaturePython)
  Base = -> Wire835
  HorizontalArea = 0
  IfcData = attributes={"GlobalId": {"name": "GlobalId", "type": "IfcGloballyUniqueId", "is_enum": false, "enum_values": []}, "Description": {"... (+538 chars omitted),+1 more (map truncated)
  IfcType = 0
  MoveBase = false
  MoveWithHost = false
  PerimeterLength = 0
  Placement = pos=(7390,5600,0) rot=(0,0,1;0rad)
  PredefinedType = 0
  VerticalArea = 0
FEATURE [Part::FeaturePython] Component148  label="Оси003"  # Arch/BIM 0 (typed FeaturePython)
  Base = -> Compound
  HorizontalArea = 0
  IfcData = attributes={"GlobalId": {"name": "GlobalId", "type": "IfcGloballyUniqueId", "is_enum": false, "enum_values": []}, "Description": {"... (+538 chars omitted),+1 more (map truncated)
  IfcType = 0
  MoveBase = false
  MoveWithHost = false
  PerimeterLength = 0
  PredefinedType = 0
  VerticalArea = 0
FEATURE [Part::Part2DObjectPython] Line1730  # Draft 2D object (typed FeaturePython)
  Area = 0
  ChamferSize = 0
  Closed = false
  End = (9950,9900,0)
  FilletRadius = 0
  Length = 200
  MakeFace = true
  Placement = pos=(9950,10100,0) rot=(0,0,1;0rad)
  Points = (2) [(0,0,0),(0,-200,0)]
  Start = (9950,10100,0)
  Subdivisions = 0
FEATURE [Part::Part2DObjectPython] Line1731  # Draft 2D object (typed FeaturePython)
  Area = 0
  ChamferSize = 0
  Closed = false
  End = (7800,9900,0)
  FilletRadius = 0
  Length = 200
  MakeFace = true
  Placement = pos=(7800,10100,0) rot=(0,0,1;0rad)
  Points = (2) [(0,0,0),(0,-200,0)]
  Start = (7800,10100,0)
  Subdivisions = 0
FEATURE [Part::Part2DObjectPython] Line1732  # Draft 2D object (typed FeaturePython)
  Area = 0
  ChamferSize = 0
  Closed = false
  End = (7800,-2000,0)
  FilletRadius = 0
  Length = 200
  MakeFace = true
  Placement = pos=(7800,-2200,0) rot=(0,0,1;0rad)
  Points = (2) [(0,0,0),(0,200,0)]
  Start = (7800,-2200,0)
  Subdivisions = 0
FEATURE [Part::Part2DObjectPython] Line1733  # Draft 2D object (typed FeaturePython)
  Area = 0
  ChamferSize = 0
  Closed = false
  End = (9950,-2000,0)
  FilletRadius = 0
  Length = 200
  MakeFace = true
  Placement = pos=(9950,-2200,0) rot=(0,0,1;0rad)
  Points = (2) [(0,0,0),(0,200,0)]
  Start = (9950,-2200,0)
  Subdivisions = 0
FEATURE [Part::Part2DObjectPython] Line1734  # Draft 2D object (typed FeaturePython)
  Area = 0
  ChamferSize = 0
  Closed = false
  End = (9950,-2200,0)
  FilletRadius = 0
  Length = 250
  MakeFace = true
  Placement = pos=(10200,-2200,0) rot=(0,0,1;0rad)
  Points = (2) [(0,0,0),(-250,0,0)]
  Start = (10200,-2200,0)
  Subdivisions = 0
FEATURE [Part::Part2DObjectPython] ShapeString205  # Draft 2D object (typed FeaturePython)
  FontFile = <path>
  Placement = pos=(10259.2,-2166.26,0) rot=(0,0,1;0rad)
  Size = 150
  String = А
  Tracking = 0
FEATURE [Part::Part2DObjectPython] ShapeString206  # Draft 2D object (typed FeaturePython)
  FontFile = <path>
  Placement = pos=(10259.2,10133.7,0) rot=(0,0,1;0rad)
  Size = 150
  String = А
  Tracking = 0
FEATURE [Part::Part2DObjectPython] Line1735  # Draft 2D object (typed FeaturePython)
  Area = 0
  ChamferSize = 0
  Closed = false
  End = (9950,10100,0)
  FilletRadius = 0
  Length = 250
  MakeFace = true
  Placement = pos=(10200,10100,0) rot=(0,0,1;0rad)
  Points = (2) [(0,0,0),(-250,0,0)]
  Start = (10200,10100,0)
  Subdivisions = 0
FEATURE [Part::Part2DObjectPython] Line1736  # Draft 2D object (typed FeaturePython)
  Area = 0
  ChamferSize = 0
  Closed = false
  End = (7800,-2200,0)
  FilletRadius = 0
  Length = 250
  MakeFace = true
  Placement = pos=(8050,-2200,0) rot=(0,0,1;0rad)
  Points = (2) [(0,0,0),(-250,0,0)]
  Start = (8050,-2200,0)
  Subdivisions = 0
FEATURE [Part::Part2DObjectPython] ShapeString207  # Draft 2D object (typed FeaturePython)
  FontFile = <path>
  Placement = pos=(8109.21,-2166.26,0) rot=(0,0,1;0rad)
  Size = 150
  String = B
  Tracking = 0
FEATURE [Part::Part2DObjectPython] ShapeString208  # Draft 2D object (typed FeaturePython)
  FontFile = <path>
  Placement = pos=(8109.21,10133.7,0) rot=(0,0,1;0rad)
  Size = 150
  String = B
  Tracking = 0
FEATURE [Part::Part2DObjectPython] Line1737  # Draft 2D object (typed FeaturePython)
  Area = 0
  ChamferSize = 0
  Closed = false
  End = (7800,10100,0)
  FilletRadius = 0
  Length = 250
  MakeFace = true
  Placement = pos=(8050,10100,0) rot=(0,0,1;0rad)
  Points = (2) [(0,0,0),(-250,0,0)]
  Start = (8050,10100,0)
  Subdivisions = 0
FEATURE [App::GeometryPython] BuildingPart114  label="разрезы"  # Arch/BIM 172 (typed FeaturePython)
  Area = 0
  Group = -> [Line1730,Line1731,Line1732,Line1733,Line1734,ShapeString205,ShapeString206,Line1735,Line1736,ShapeString207,ShapeString208,Line1737]
  Height = 0
  HeightPropagate = true
  IfcData = attributes={"GlobalId": {"name": "GlobalId", "type": "IfcGloballyUniqueId", "is_enum": false, "enum_values": []}, "Description": {"... (+484 chars omitted),+1 more (map truncated)
  IfcType = 172
  LevelOffset = 0
  PredefinedType = 0
FEATURE [App::GeometryPython] BuildingPart090  label="Размеры (top)"  # Arch/BIM 52 (typed FeaturePython)
  Area = 0
  GlobalId = 3_s$oy9jj54xonqTEdRA8q
  Group = -> [Dimension001,Dimension,Dimension002,Dimension003,Dimension004,Dimension009,Dimension007,Dimension006,ShapeString147,ShapeString138,Circle088,Circle089,ShapeString139,Circle090,ShapeString140,Circle091,ShapeString141,Circle092,ShapeString142,Circle093,ShapeString143,Circle094,ShapeString144,Circle095,ShapeString145,Circle097,Line1326,Line1327,Line1328,Line1329,Line1330,ShapeString189,+99 more]
  Height = 0
  HeightPropagate = true
  IfcData = IfcUID=3_s$oy9jj54xonqTEdRA8q,+2 more (map truncated)
  IfcType = 52
  LevelOffset = 0
FEATURE [App::FeaturePython] Section006  label="Section 1st floor plan"  # WARN: FeaturePython — macro-defined, semantics opaque (R4)
  Clip = false
  Objects = -> [BuildingPart101,BuildingPart102,BuildingPart002,BuildingPart005,BuildingPart081,BuildingPart093,BuildingPart011,BuildingPart087,BuildingPart049,BuildingPart090]
  OnlySolids = true
  Placement = pos=(6260,3730,1600) rot=(0,0,1;0rad)
  UseMaterialColorForFill = true
FEATURE [TechDraw::DrawViewArch] ArchView007
  AllOn = true
  CutLineWidth = 0.1
  FillSpaces = false
  FontSize = 7
  JoinArch = false
  LineWidth = 0.1
  LockPosition = true
  RenderMode = 0
  Rotation = 0
  Scale = 0.02
  ScaleType = 2
  ShowFill = true
  ShowHidden = false
  Source = -> Section006
  Symbol = <blob: 670766 chars omitted>
  X = 210
  Y = 150
FEATURE [TechDraw::DrawPage] Page002  label="План 1 этаж"
  KeepUpdated = true
  NextBalloonIndex = 1
  ProjectionType = 0
  Template = -> Template002
  Views = -> [Annotation007,ArchView007,DraftView001]
FEATURE [TechDraw::DrawSVGTemplate] Template004
  EditableTexts = Дата_разработки=16.11.21; Лист=1; Листов=1; Масштаб=1:1; Название=Жилой дом; Номер=ИЖС-0000.0001; Разработал=Мавричев Р.С.
  Height = 297
  Orientation = 1
  Width = 420
FEATURE [TechDraw::DrawViewImage] Image001
  Height = 300
  ImageFile = <userpath>/Рабочий стол/sweet_home_3d-2.jpg
  LockPosition = false
  Rotation = 0
  Scale = 0.85
  ScaleType = 2
  Width = 300
  X = 121.023
  Y = 105.685
FEATURE [TechDraw::DrawViewImage] Image002
  Height = 300
  ImageFile = <userpath>/Рабочий стол/sweet_home_3d-1.jpg
  LockPosition = false
  Rotation = 0
  Scale = 1.15
  ScaleType = 2
  Width = 300
  X = 121.334
  Y = 209.487
FEATURE [TechDraw::DrawViewAnnotation] Annotation032
  Font = osifont
  LineSpace = 80
  LockPosition = false
  MaxWidth = -1
  Rotation = 0
  ScaleType = 0
  Text = \u0440\u0438\u0441. 1   \u0421\u0435\u0432\u0435\u0440\u043d\u044b\u0439 \u0444\u0430\u0441\u0430\u0434
  TextSize = 6
  TextStyle = 0
  X = 119.427
  Y = 160.808
FEATURE [TechDraw::DrawViewAnnotation] Annotation033
  Font = osifont
  LineSpace = 80
  LockPosition = false
  MaxWidth = -1
  Rotation = 0
  ScaleType = 0
  Text = \u0440\u0438\u0441. 2  \u042e\u0436\u043d\u044b\u0439 \u0444\u0430\u0441\u0430\u0434
  TextSize = 6
  TextStyle = 0
  X = 122.519
  Y = 56.0962
FEATURE [TechDraw::DrawPage] Page004  label="Титульный лист"
  KeepUpdated = false
  NextBalloonIndex = 1
  ProjectionType = 0
  Template = -> Template004
  Views = -> [Image001,Image002,Annotation032,Annotation033]
FEATURE [TechDraw::DrawSVGTemplate] Template005
  EditableTexts = Лист=6; Номер=ИЖС-0000.0001
  Height = 297
  Orientation = 1
  Width = 420
FEATURE [Part::Part2DObjectPython] Wire920  # Draft 2D object (typed FeaturePython)
  Area = 0
  ChamferSize = 0
  Closed = false
  End = (7075,8615,3132.21)
  FilletRadius = 0
  Length = 22363
  MakeFace = false
  Placement = pos=(3198,-1155,3132.21) rot=(0,0,1;0rad)
  Points = (4) [(0,0,0),(-4358,4.54747e-13,-4.54747e-13),(-4358,9770,1.81899e-12),(3877,9770,4.54747e-13)]
  Start = (3198,-1155,3132.21)
  Subdivisions = 0
FEATURE [Part::Part2DObjectPython] Wire919  # Draft 2D object (typed FeaturePython)
  Area = 0
  ChamferSize = 0
  Closed = false
  End = (9198,-1155,3132.21)
  FilletRadius = 0
  Length = 15857
  MakeFace = false
  Placement = pos=(12075,8615,3132.21) rot=(0,0,1;0rad)
  Points = (4) [(0,0,0),(1605,0,-4.54747e-13),(1605,-9770,-4.54747e-13),(-2877,-9770,-4.54747e-13)]
  Start = (12075,8615,3132.21)
  Subdivisions = 0
FEATURE [Part::FeaturePython] Wall350  label="Стена043"  # Arch/BIM 166 (typed FeaturePython)
  Align = 0
  Area = 2616405
  Base = -> Wire919
  BlockHeight = 0
  BlockLength = 0
  CountBroken = 0
  CountEntire = 0
  Face = 0
  Height = 165
  HorizontalArea = 6022800
  IfcData = attributes={"GlobalId": {"name": "GlobalId", "type": "IfcGloballyUniqueId", "is_enum": false, "enum_values": []}, "Description": {"... (+533 chars omitted),+1 more (map truncated)
  IfcType = 166
  Joint = 0
  Length = 15857
  MakeBlocks = false
  MoveBase = false
  MoveWithHost = false
  Normal = (0,0,0)
  OffsetFirst = 0
  OffsetSecond = 0
  PerimeterLength = 30914
  PredefinedType = 0
  VerticalArea = 5100810
  Width = 400
FEATURE [Part::FeaturePython] Wall351  label="Стена044"  # Arch/BIM 166 (typed FeaturePython)
  Align = 0
  Area = 3689895
  Base = -> Wire920
  BlockHeight = 0
  BlockLength = 0
  CountBroken = 0
  CountEntire = 0
  Face = 0
  Height = 165
  HorizontalArea = 8625200
  IfcData = attributes={"GlobalId": {"name": "GlobalId", "type": "IfcGloballyUniqueId", "is_enum": false, "enum_values": []}, "Description": {"... (+533 chars omitted),+1 more (map truncated)
  IfcType = 166
  Joint = 0
  Length = 22363
  MakeBlocks = false
  MoveBase = false
  MoveWithHost = false
  Normal = (0,0,0)
  OffsetFirst = 0
  OffsetSecond = 0
  PerimeterLength = 43926
  PredefinedType = 0
  VerticalArea = 7.24779e+06
  Width = 400
FEATURE [Part::MultiFuse] Fusion071
  Shapes = -> [Wall350,Wall351]
FEATURE [Part::Cut] Cut070  label="Кровля габарит_002"
  Base = -> Cut052
  Tool = -> Fusion071
FEATURE [Part::FeaturePython] Component149  label="Кровля габарит"  # Arch/BIM 0 (typed FeaturePython)
  Base = -> Cut070
  HorizontalArea = 0
  IfcData = attributes={"GlobalId": {"name": "GlobalId", "type": "IfcGloballyUniqueId", "is_enum": false, "enum_values": []}, "Description": {"... (+538 chars omitted),+1 more (map truncated)
  IfcType = 0
  Material = -> Material007
  MoveBase = false
  MoveWithHost = false
  PerimeterLength = 0
  PredefinedType = 0
  VerticalArea = 0
FEATURE [App::GeometryPython] BuildingPart106  label="Кровля"  # Arch/BIM 52 (typed FeaturePython)
  Area = 0
  GlobalId = 3O6XTUJY1FTBF6rjo3DaEi
  Group = -> [BuildingPart084,Component149]
  Height = 0
  HeightPropagate = true
  IfcData = IfcUID=3O6XTUJY1FTBF6rjo3DaEi,+2 more (map truncated)
  IfcType = 52
  LevelOffset = 0
FEATURE [App::GeometryPython] BuildingPart104  label="Уровень  мансарды"  # Arch/BIM 14 (typed FeaturePython)
  Area = 364062280
  CompositionType = 0
  Elevation = 3130
  GlobalId = 2Sd2b8p9H2Ff7iaZY3OzqZ
  Group = -> [BuildingPart016,BuildingPart083,BuildingPart,BuildingPart106,BuildingPart113]
  Height = 3130
  HeightPropagate = true
  IfcData = IfcUID=2Sd2b8p9H2Ff7iaZY3OzqZ,+2 more (map truncated)
  IfcType = 14
  LevelOffset = 0
  LongName = Floor
  Placement = pos=(-560,-540,3130) rot=(0,0,1;0rad)
  expr: Elevation = .Placement.Base.z
FEATURE [App::GeometryPython] BuildingPart105  label="Индивидуальный жилой дом"  # Arch/BIM 10 (typed FeaturePython)
  Area = 1.12523e+09
  BuildingType = 36
  CompositionType = 0
  ElevationOfRefHeight = 0
  ElevationOfTerrain = 0
  GlobalId = 1wNqu2gmH0$Q5UGcgb9xOg
  Group = -> [App__DocumentObjectGroup,BuildingPart103,BuildingPart104,WPProxy,WPProxy001,BuildingPart109]
  Height = 0
  HeightPropagate = true
  IfcData = IfcUID=1wNqu2gmH0$Q5UGcgb9xOg,+2 more (map truncated)
  IfcType = 10
  LevelOffset = 0
  LongName = Building
  Placement = pos=(-560,-540,0) rot=(0,0,1;0rad)
FEATURE [Part::FeaturePython] Site001  label="Участок ИЖС"  # Arch/BIM 117 (typed FeaturePython)
  AdditionVolume = 0
  CompositionType = 0
  Declination = 0
  Elevation = 0
  ExtrusionVector = (0,0,-100000)
  GlobalId = 0q3YkvPDD0KRQl3VYghQdF
  Group = -> [BuildingPart105]
  IfcData = IfcUID=0q3YkvPDD0KRQl3VYghQdF,+2 more (map truncated)
  IfcType = 117
  Latitude = 0
  LongName = Site
  Longitude = 0
  OriginOffset = (0,0,0)
  Perimeter = 0
  ProjectedArea = 0
  RefElevation = 0
  RemoveSplitter = false
  SubtractionVolume = 0
  TimeZone = 0
  expr: RefElevation = .Elevation.Value
FEATURE [App::FeaturePython] Section  label="Section A-A"  # WARN: FeaturePython — macro-defined, semantics opaque (R4)
  Clip = true
  Objects = -> [BuildingPart103,BuildingPart104,BuildingPart100]
  OnlySolids = true
  Placement = pos=(9950,3730,3690.5) rot=(0.57735,0.57735,0.57735;2.0944rad)
  UseMaterialColorForFill = true
FEATURE [TechDraw::DrawViewArch] ArchView
  AllOn = true
  CutLineWidth = 0.1
  FillSpaces = false
  FontSize = 8
  JoinArch = false
  LineWidth = 0.1
  LockPosition = true
  RenderMode = 0
  Rotation = 90
  Scale = 0.02
  ScaleType = 2
  ShowFill = true
  ShowHidden = false
  Source = -> Section
  Symbol = <blob: 758110 chars omitted>
  X = 224.182
  Y = 160.176
FEATURE [TechDraw::DrawPage] Page001  label="Разрез по А-А"
  KeepUpdated = true
  NextBalloonIndex = 1
  ProjectionType = 0
  Scale = 0.02
  Template = -> Template001
  Views = -> [Annotation008,ArchView,Annotation009,Annotation010,Annotation011,Annotation012,LeaderLine,LeaderLine001,LeaderLine002,LeaderLine003,Annotation013,Annotation014,Annotation015,Annotation016,LeaderLine004,Annotation017,Annotation018,Annotation019,Annotation020,Annotation021,Annotation022,Annotation023,Annotation024,Annotation025,Annotation026,LeaderLine005,LeaderLine006,LeaderLine007,LeaderLine008,+12 more]
FEATURE [App::FeaturePython] Section007  label="Section 2nd floor plan"  # WARN: FeaturePython — macro-defined, semantics opaque (R4)
  Clip = false
  Objects = -> [BuildingPart104,BuildingPart093]
  OnlySolids = true
  Placement = pos=(6260,3730,4300) rot=(0,0,1;0rad)
  UseMaterialColorForFill = true
FEATURE [TechDraw::DrawViewArch] ArchView008
  AllOn = true
  CutLineWidth = 0.1
  FillSpaces = false
  FontSize = 12
  JoinArch = false
  LineWidth = 0.25
  LockPosition = true
  RenderMode = 0
  Rotation = 0
  Scale = 0.02
  ScaleType = 2
  ShowFill = true
  ShowHidden = false
  Source = -> Section007
  Symbol = <blob: 66939 chars omitted>
  X = 210
  Y = 150
FEATURE [TechDraw::DrawPage] Page003  label="План мансарда"
  KeepUpdated = true
  NextBalloonIndex = 1
  ProjectionType = 0
  Template = -> Template003
  Views = -> [ArchView008,Annotation031]
FEATURE [App::FeaturePython] Section008  label="Section B-B"  # WARN: FeaturePython — macro-defined, semantics opaque (R4)
  Clip = true
  Objects = -> [BuildingPart103,BuildingPart104]
  OnlySolids = true
  Placement = pos=(7800,3730,3630.5) rot=(0.57735,0.57735,0.57735;2.0944rad)
  UseMaterialColorForFill = true
FEATURE [App::DocumentObjectGroup] Group129  label="Sections"
  Group = -> [Section006,Section,Section008,Section007]
FEATURE [TechDraw::DrawViewArch] ArchView009
  AllOn = true
  Caption = Разрез "B-B"
  CutLineWidth = 0.1
  FillSpaces = false
  FontSize = 8
  JoinArch = false
  LineWidth = 0.1
  LockPosition = true
  RenderMode = 0
  Rotation = 90
  Scale = 0.02
  ScaleType = 2
  ShowFill = true
  ShowHidden = false
  Source = -> Section008
  Symbol = <blob: 1721199 chars omitted>
  X = 224.18
  Y = 160.18
FEATURE [TechDraw::DrawPage] Page005  label="Разрез по B-B"
  KeepUpdated = true
  NextBalloonIndex = 1
  ProjectionType = 0
  Scale = 0.02
  Template = -> Template005
  Views = -> [ArchView009]
FEATURE [App::DocumentObjectGroup] Group130  label="Листы проекта для печати"
  Group = -> [Group127,Group129,Page,Page002,Page001,Page003,Page004,Page005]
note: 33 file-system paths scrubbed to <path> (originals preserved in the JSON sidecar)
